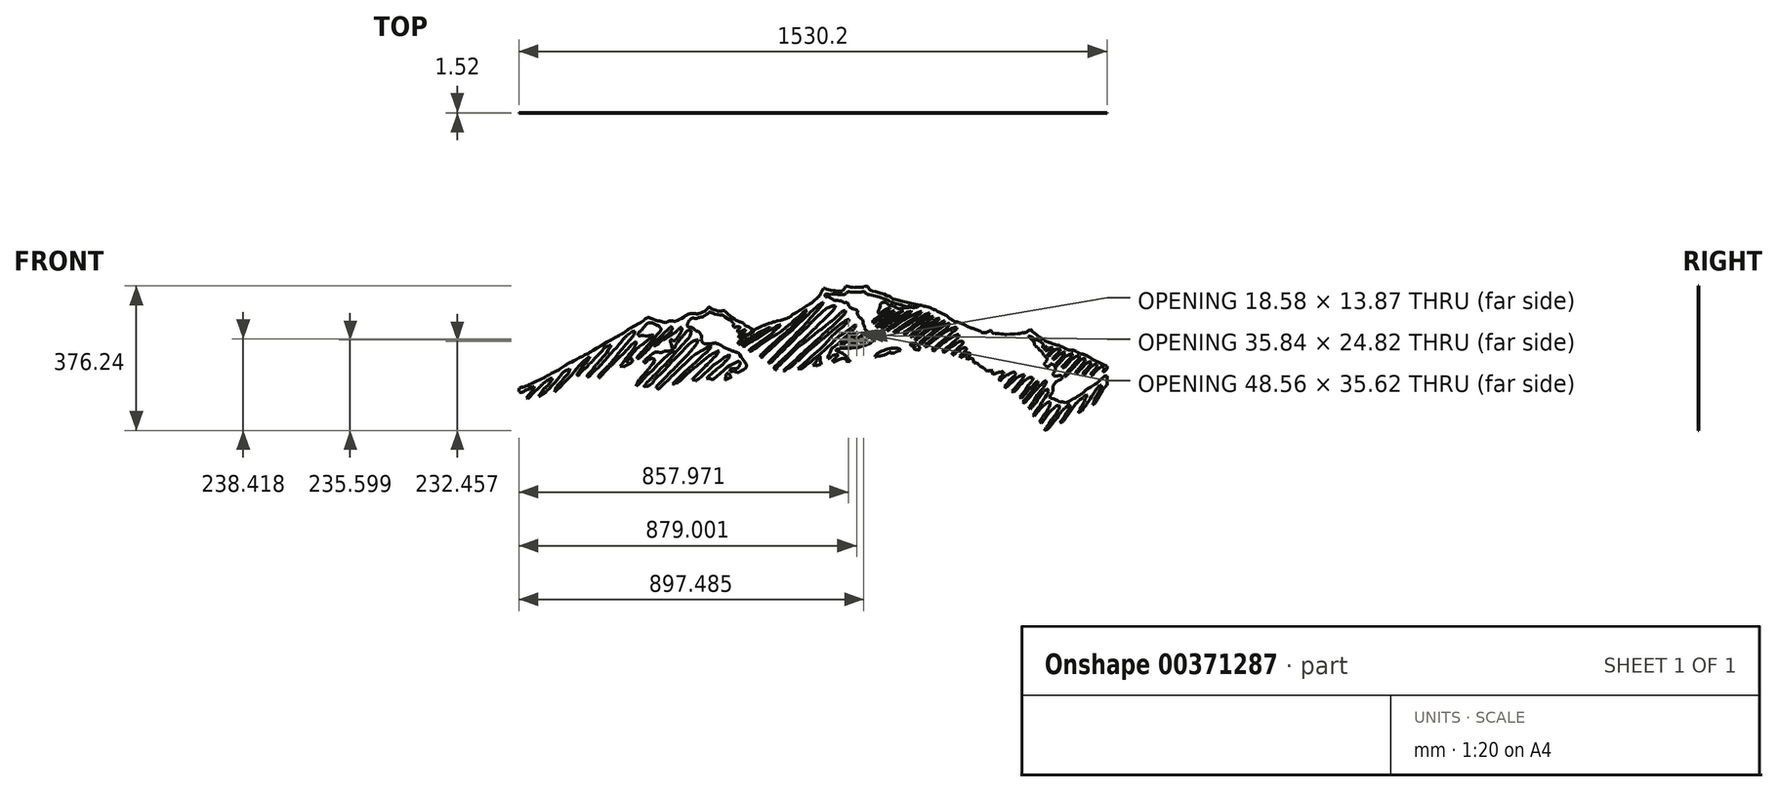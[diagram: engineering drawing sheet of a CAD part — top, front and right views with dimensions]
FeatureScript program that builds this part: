
annotation { "Feature Type Name" : "Feature", "Feature Type Description" : "" }
export const myFeature = defineFeature(function(context is Context, id is Id, definition is map)
    precondition{}
    {
        {
            var Q0;
            Q0=qCreatedBy(makeId("Front.planeOp"),FACE);
            var sketch = newSketch(context, id + "F0", { "sketchPlane" : qUnion([Q0])});
            skLineSegment(sketch, "E0", {"start": v(-154.66, 73) * mm, "end": v(-154.93, 73) * mm});
            skLineSegment(sketch, "E1", {"start": v(-154.93, 73) * mm, "end": v(-155.73, 73.26) * mm});
            skLineSegment(sketch, "E2", {"start": v(-155.73, 73.26) * mm, "end": v(-156.92, 73.96) * mm});
            skLineSegment(sketch, "E3", {"start": v(-156.92, 73.96) * mm, "end": v(-158.2, 74.97) * mm});
            skLineSegment(sketch, "E4", {"start": v(-158.2, 74.97) * mm, "end": v(-159.52, 76.17) * mm});
            skLineSegment(sketch, "E5", {"start": v(-159.52, 76.17) * mm, "end": v(-160.86, 77.43) * mm});
            skLineSegment(sketch, "E6", {"start": v(-160.86, 77.43) * mm, "end": v(-162.18, 78.62) * mm});
            skLineSegment(sketch, "E7", {"start": v(-162.18, 78.62) * mm, "end": v(-163.45, 79.62) * mm});
            skLineSegment(sketch, "E8", {"start": v(-163.45, 79.62) * mm, "end": v(-164.32, 80.17) * mm});
            skLineSegment(sketch, "E9", {"start": v(-164.32, 80.17) * mm, "end": v(-164.63, 80.3) * mm});
            skLineSegment(sketch, "E10", {"start": v(-164.63, 80.3) * mm, "end": v(-165.19, 80.55) * mm});
            skLineSegment(sketch, "E11", {"start": v(-165.19, 80.55) * mm, "end": v(-168.15, 81.65) * mm});
            skLineSegment(sketch, "E12", {"start": v(-168.15, 81.65) * mm, "end": v(-171.05, 82.83) * mm});
            skLineSegment(sketch, "E13", {"start": v(-171.05, 82.83) * mm, "end": v(-171.57, 83.1) * mm});
            skLineSegment(sketch, "E14", {"start": v(-171.57, 83.1) * mm, "end": v(-171.75, 83.2) * mm});
            skLineSegment(sketch, "E15", {"start": v(-171.75, 83.2) * mm, "end": v(-172.31, 83.4) * mm});
            skLineSegment(sketch, "E16", {"start": v(-172.31, 83.4) * mm, "end": v(-173.14, 83.63) * mm});
            skLineSegment(sketch, "E17", {"start": v(-173.14, 83.63) * mm, "end": v(-173.9, 83.85) * mm});
            skLineSegment(sketch, "E18", {"start": v(-173.9, 83.85) * mm, "end": v(-174.37, 84.03) * mm});
            skLineSegment(sketch, "E19", {"start": v(-174.37, 84.03) * mm, "end": v(-174.51, 84.11) * mm});
            skLineSegment(sketch, "E20", {"start": v(-174.51, 84.11) * mm, "end": v(-175, 84.43) * mm});
            skLineSegment(sketch, "E21", {"start": v(-175, 84.43) * mm, "end": v(-176.3, 85.66) * mm});
            skLineSegment(sketch, "E22", {"start": v(-176.3, 85.66) * mm, "end": v(-177.82, 87.53) * mm});
            skLineSegment(sketch, "E23", {"start": v(-177.82, 87.53) * mm, "end": v(-179.36, 89.45) * mm});
            skLineSegment(sketch, "E24", {"start": v(-179.36, 89.45) * mm, "end": v(-180.68, 90.77) * mm});
            skLineSegment(sketch, "E25", {"start": v(-180.68, 90.77) * mm, "end": v(-181.18, 91.12) * mm});
            skLineSegment(sketch, "E26", {"start": v(-181.18, 91.12) * mm, "end": v(-181.77, 91.55) * mm});
            skLineSegment(sketch, "E27", {"start": v(-181.77, 91.55) * mm, "end": v(-185.18, 93.13) * mm});
            skLineSegment(sketch, "E28", {"start": v(-185.18, 93.13) * mm, "end": v(-188.74, 94.46) * mm});
            skLineSegment(sketch, "E29", {"start": v(-188.74, 94.46) * mm, "end": v(-189.4, 94.76) * mm});
            skLineSegment(sketch, "E30", {"start": v(-189.4, 94.76) * mm, "end": v(-190.22, 95.12) * mm});
            skLineSegment(sketch, "E31", {"start": v(-190.22, 95.12) * mm, "end": v(-192.73, 96.1) * mm});
            skLineSegment(sketch, "E32", {"start": v(-192.73, 96.1) * mm, "end": v(-196.17, 97.44) * mm});
            skLineSegment(sketch, "E33", {"start": v(-196.17, 97.44) * mm, "end": v(-199.53, 98.9) * mm});
            skLineSegment(sketch, "E34", {"start": v(-199.53, 98.9) * mm, "end": v(-201.89, 100.16) * mm});
            skLineSegment(sketch, "E35", {"start": v(-201.89, 100.16) * mm, "end": v(-202.62, 100.65) * mm});
            skLineSegment(sketch, "E36", {"start": v(-202.62, 100.65) * mm, "end": v(-204.02, 101.56) * mm});
            skLineSegment(sketch, "E37", {"start": v(-204.02, 101.56) * mm, "end": v(-210.9, 106.39) * mm});
            skLineSegment(sketch, "E38", {"start": v(-210.9, 106.39) * mm, "end": v(-217.38, 111.71) * mm});
            skLineSegment(sketch, "E39", {"start": v(-217.38, 111.71) * mm, "end": v(-218.6, 112.87) * mm});
            skLineSegment(sketch, "E40", {"start": v(-218.6, 112.87) * mm, "end": v(-219.51, 113.75) * mm});
            skLineSegment(sketch, "E41", {"start": v(-219.51, 113.75) * mm, "end": v(-228.41, 122.8) * mm});
            skLineSegment(sketch, "E42", {"start": v(-228.41, 122.8) * mm, "end": v(-229.29, 123.73) * mm});
            skLineSegment(sketch, "E43", {"start": v(-229.29, 123.73) * mm, "end": v(-229.56, 124.01) * mm});
            skLineSegment(sketch, "E44", {"start": v(-229.56, 124.01) * mm, "end": v(-229.94, 124.05) * mm});
            skLineSegment(sketch, "E45", {"start": v(-229.94, 124.05) * mm, "end": v(-230.65, 124.13) * mm});
            skLineSegment(sketch, "E46", {"start": v(-230.65, 124.13) * mm, "end": v(-232.82, 123.92) * mm});
            skLineSegment(sketch, "E47", {"start": v(-232.82, 123.92) * mm, "end": v(-235.5, 123.2) * mm});
            skLineSegment(sketch, "E48", {"start": v(-235.5, 123.2) * mm, "end": v(-238.12, 122.38) * mm});
            skLineSegment(sketch, "E49", {"start": v(-238.12, 122.38) * mm, "end": v(-240.15, 121.95) * mm});
            skLineSegment(sketch, "E50", {"start": v(-240.15, 121.95) * mm, "end": v(-240.84, 121.92) * mm});
            skLineSegment(sketch, "E51", {"start": v(-240.84, 121.92) * mm, "end": v(-242.3, 121.87) * mm});
            skLineSegment(sketch, "E52", {"start": v(-242.3, 121.87) * mm, "end": v(-246.75, 122.56) * mm});
            skLineSegment(sketch, "E53", {"start": v(-246.75, 122.56) * mm, "end": v(-252.44, 124.4) * mm});
            skLineSegment(sketch, "E54", {"start": v(-252.44, 124.4) * mm, "end": v(-258.04, 126.65) * mm});
            skLineSegment(sketch, "E55", {"start": v(-258.04, 126.65) * mm, "end": v(-262.24, 128.16) * mm});
            skLineSegment(sketch, "E56", {"start": v(-262.24, 128.16) * mm, "end": v(-263.68, 128.53) * mm});
            skLineSegment(sketch, "E57", {"start": v(-263.68, 128.53) * mm, "end": v(-264.07, 128.93) * mm});
            skLineSegment(sketch, "E58", {"start": v(-264.07, 128.93) * mm, "end": v(-265.26, 130.13) * mm});
            skLineSegment(sketch, "E59", {"start": v(-265.26, 130.13) * mm, "end": v(-266.9, 131.46) * mm});
            skLineSegment(sketch, "E60", {"start": v(-266.9, 131.46) * mm, "end": v(-268.8, 132.22) * mm});
            skLineSegment(sketch, "E61", {"start": v(-268.8, 132.22) * mm, "end": v(-270.62, 132.25) * mm});
            skLineSegment(sketch, "E62", {"start": v(-270.62, 132.25) * mm, "end": v(-271.19, 132.12) * mm});
            skLineSegment(sketch, "E63", {"start": v(-271.19, 132.12) * mm, "end": v(-271.57, 132.03) * mm});
            skLineSegment(sketch, "E64", {"start": v(-271.57, 132.03) * mm, "end": v(-272.62, 131.34) * mm});
            skLineSegment(sketch, "E65", {"start": v(-272.62, 131.34) * mm, "end": v(-273.76, 130.02) * mm});
            skLineSegment(sketch, "E66", {"start": v(-273.76, 130.02) * mm, "end": v(-274.76, 128.52) * mm});
            skLineSegment(sketch, "E67", {"start": v(-274.76, 128.52) * mm, "end": v(-275.46, 127.52) * mm});
            skLineSegment(sketch, "E68", {"start": v(-275.46, 127.52) * mm, "end": v(-275.74, 127.23) * mm});
            skLineSegment(sketch, "E69", {"start": v(-275.74, 127.23) * mm, "end": v(-276.9, 126.06) * mm});
            skLineSegment(sketch, "E70", {"start": v(-276.9, 126.06) * mm, "end": v(-280.8, 122.96) * mm});
            skLineSegment(sketch, "E71", {"start": v(-280.8, 122.96) * mm, "end": v(-286.58, 119.56) * mm});
            skLineSegment(sketch, "E72", {"start": v(-286.58, 119.56) * mm, "end": v(-292.8, 117.09) * mm});
            skLineSegment(sketch, "E73", {"start": v(-292.8, 117.09) * mm, "end": v(-297.63, 115.84) * mm});
            skLineSegment(sketch, "E74", {"start": v(-297.63, 115.84) * mm, "end": v(-299.26, 115.59) * mm});
            skLineSegment(sketch, "E75", {"start": v(-299.26, 115.59) * mm, "end": v(-299.93, 115.48) * mm});
            skLineSegment(sketch, "E76", {"start": v(-299.93, 115.48) * mm, "end": v(-302, 115.4) * mm});
            skLineSegment(sketch, "E77", {"start": v(-302, 115.4) * mm, "end": v(-304.96, 115.55) * mm});
            skLineSegment(sketch, "E78", {"start": v(-304.96, 115.55) * mm, "end": v(-307.95, 115.8) * mm});
            skLineSegment(sketch, "E79", {"start": v(-307.95, 115.8) * mm, "end": v(-310.08, 115.95) * mm});
            skLineSegment(sketch, "E80", {"start": v(-310.08, 115.95) * mm, "end": v(-310.8, 115.96) * mm});
            skLineSegment(sketch, "E81", {"start": v(-310.8, 115.96) * mm, "end": v(-311.37, 115.98) * mm});
            skLineSegment(sketch, "E82", {"start": v(-311.37, 115.98) * mm, "end": v(-314.2, 116.23) * mm});
            skLineSegment(sketch, "E83", {"start": v(-314.2, 116.23) * mm, "end": v(-317.05, 116.35) * mm});
            skLineSegment(sketch, "E84", {"start": v(-317.05, 116.35) * mm, "end": v(-317.63, 116.3) * mm});
            skLineSegment(sketch, "E85", {"start": v(-317.63, 116.3) * mm, "end": v(-318.1, 116.25) * mm});
            skLineSegment(sketch, "E86", {"start": v(-318.1, 116.25) * mm, "end": v(-319.52, 115.93) * mm});
            skLineSegment(sketch, "E87", {"start": v(-319.52, 115.93) * mm, "end": v(-321.6, 115.22) * mm});
            skLineSegment(sketch, "E88", {"start": v(-321.6, 115.22) * mm, "end": v(-323.8, 114.25) * mm});
            skLineSegment(sketch, "E89", {"start": v(-323.8, 114.25) * mm, "end": v(-326.05, 113.1) * mm});
            skLineSegment(sketch, "E90", {"start": v(-326.05, 113.1) * mm, "end": v(-328.27, 111.86) * mm});
            skLineSegment(sketch, "E91", {"start": v(-328.27, 111.86) * mm, "end": v(-330.41, 110.6) * mm});
            skLineSegment(sketch, "E92", {"start": v(-330.41, 110.6) * mm, "end": v(-332.4, 109.42) * mm});
            skLineSegment(sketch, "E93", {"start": v(-332.4, 109.42) * mm, "end": v(-333.72, 108.65) * mm});
            skLineSegment(sketch, "E94", {"start": v(-333.72, 108.65) * mm, "end": v(-334.16, 108.4) * mm});
            skLineSegment(sketch, "E95", {"start": v(-334.16, 108.4) * mm, "end": v(-335.43, 107.7) * mm});
            skLineSegment(sketch, "E96", {"start": v(-335.43, 107.7) * mm, "end": v(-341.69, 104.02) * mm});
            skLineSegment(sketch, "E97", {"start": v(-341.69, 104.02) * mm, "end": v(-347.94, 100.33) * mm});
            skLineSegment(sketch, "E98", {"start": v(-347.94, 100.33) * mm, "end": v(-349.21, 99.62) * mm});
            skLineSegment(sketch, "E99", {"start": v(-349.21, 99.62) * mm, "end": v(-349.69, 99.37) * mm});
            skLineSegment(sketch, "E100", {"start": v(-349.69, 99.37) * mm, "end": v(-352.39, 97.91) * mm});
            skLineSegment(sketch, "E101", {"start": v(-352.39, 97.91) * mm, "end": v(-355.17, 96.69) * mm});
            skLineSegment(sketch, "E102", {"start": v(-355.17, 96.69) * mm, "end": v(-355.7, 96.55) * mm});
            skLineSegment(sketch, "E103", {"start": v(-355.7, 96.55) * mm, "end": v(-356.82, 96.26) * mm});
            skLineSegment(sketch, "E104", {"start": v(-356.82, 96.26) * mm, "end": v(-360.37, 96.1) * mm});
            skLineSegment(sketch, "E105", {"start": v(-360.37, 96.1) * mm, "end": v(-365.16, 96.53) * mm});
            skLineSegment(sketch, "E106", {"start": v(-365.16, 96.53) * mm, "end": v(-369.9, 96.97) * mm});
            skLineSegment(sketch, "E107", {"start": v(-369.9, 96.97) * mm, "end": v(-373.35, 96.83) * mm});
            skLineSegment(sketch, "E108", {"start": v(-373.35, 96.83) * mm, "end": v(-374.43, 96.55) * mm});
            skLineSegment(sketch, "E109", {"start": v(-374.43, 96.55) * mm, "end": v(-374.92, 96.43) * mm});
            skLineSegment(sketch, "E110", {"start": v(-374.92, 96.43) * mm, "end": v(-376.28, 95.77) * mm});
            skLineSegment(sketch, "E111", {"start": v(-376.28, 95.77) * mm, "end": v(-378.05, 94.66) * mm});
            skLineSegment(sketch, "E112", {"start": v(-378.05, 94.66) * mm, "end": v(-379.8, 93.63) * mm});
            skLineSegment(sketch, "E113", {"start": v(-379.8, 93.63) * mm, "end": v(-381.17, 93.13) * mm});
            skLineSegment(sketch, "E114", {"start": v(-381.17, 93.13) * mm, "end": v(-381.64, 93.08) * mm});
            skLineSegment(sketch, "E115", {"start": v(-381.64, 93.08) * mm, "end": v(-382.45, 93) * mm});
            skLineSegment(sketch, "E116", {"start": v(-382.45, 93) * mm, "end": v(-384.92, 93.19) * mm});
            skLineSegment(sketch, "E117", {"start": v(-384.92, 93.19) * mm, "end": v(-388.1, 93.91) * mm});
            skLineSegment(sketch, "E118", {"start": v(-388.1, 93.91) * mm, "end": v(-391.21, 94.92) * mm});
            skLineSegment(sketch, "E119", {"start": v(-391.21, 94.92) * mm, "end": v(-393.55, 95.66) * mm});
            skLineSegment(sketch, "E120", {"start": v(-393.55, 95.66) * mm, "end": v(-394.34, 95.86) * mm});
            skLineSegment(sketch, "E121", {"start": v(-394.34, 95.86) * mm, "end": v(-395.48, 96.15) * mm});
            skLineSegment(sketch, "E122", {"start": v(-395.48, 96.15) * mm, "end": v(-398.93, 96.82) * mm});
            skLineSegment(sketch, "E123", {"start": v(-398.93, 96.82) * mm, "end": v(-403.6, 97.62) * mm});
            skLineSegment(sketch, "E124", {"start": v(-403.6, 97.62) * mm, "end": v(-408.21, 98.6) * mm});
            skLineSegment(sketch, "E125", {"start": v(-408.21, 98.6) * mm, "end": v(-411.57, 99.6) * mm});
            skLineSegment(sketch, "E126", {"start": v(-411.57, 99.6) * mm, "end": v(-412.63, 100.04) * mm});
            skLineSegment(sketch, "E127", {"start": v(-412.63, 100.04) * mm, "end": v(-413.56, 100.43) * mm});
            skLineSegment(sketch, "E128", {"start": v(-413.56, 100.43) * mm, "end": v(-416.26, 101.75) * mm});
            skLineSegment(sketch, "E129", {"start": v(-416.26, 101.75) * mm, "end": v(-420.03, 103.62) * mm});
            skLineSegment(sketch, "E130", {"start": v(-420.03, 103.62) * mm, "end": v(-423.9, 105.11) * mm});
            skLineSegment(sketch, "E131", {"start": v(-423.9, 105.11) * mm, "end": v(-426.81, 105.73) * mm});
            skLineSegment(sketch, "E132", {"start": v(-426.81, 105.73) * mm, "end": v(-427.78, 105.73) * mm});
            skLineSegment(sketch, "E133", {"start": v(-427.78, 105.73) * mm, "end": v(-428.43, 105.73) * mm});
            skLineSegment(sketch, "E134", {"start": v(-428.43, 105.73) * mm, "end": v(-430.35, 105.37) * mm});
            skLineSegment(sketch, "E135", {"start": v(-430.35, 105.37) * mm, "end": v(-432.33, 104.49) * mm});
            skLineSegment(sketch, "E136", {"start": v(-432.33, 104.49) * mm, "end": v(-434.2, 103.44) * mm});
            skLineSegment(sketch, "E137", {"start": v(-434.2, 103.44) * mm, "end": v(-435.87, 102.7) * mm});
            skLineSegment(sketch, "E138", {"start": v(-435.87, 102.7) * mm, "end": v(-436.45, 102.53) * mm});
            skLineSegment(sketch, "E139", {"start": v(-436.45, 102.53) * mm, "end": v(-436.81, 102.44) * mm});
            skLineSegment(sketch, "E140", {"start": v(-436.81, 102.44) * mm, "end": v(-437.03, 102.14) * mm});
            skLineSegment(sketch, "E141", {"start": v(-437.03, 102.14) * mm, "end": v(-437.65, 101.29) * mm});
            skLineSegment(sketch, "E142", {"start": v(-437.65, 101.29) * mm, "end": v(-439.87, 98.99) * mm});
            skLineSegment(sketch, "E143", {"start": v(-439.87, 98.99) * mm, "end": v(-443.24, 96.22) * mm});
            skLineSegment(sketch, "E144", {"start": v(-443.24, 96.22) * mm, "end": v(-446.87, 93.75) * mm});
            skLineSegment(sketch, "E145", {"start": v(-446.87, 93.75) * mm, "end": v(-449.58, 92.07) * mm});
            skLineSegment(sketch, "E146", {"start": v(-449.58, 92.07) * mm, "end": v(-450.49, 91.5) * mm});
            skLineSegment(sketch, "E147", {"start": v(-450.49, 91.5) * mm, "end": v(-452.63, 90.2) * mm});
            skLineSegment(sketch, "E148", {"start": v(-452.63, 90.2) * mm, "end": v(-463.65, 84.2) * mm});
            skLineSegment(sketch, "E149", {"start": v(-463.65, 84.2) * mm, "end": v(-474.74, 78.32) * mm});
            skLineSegment(sketch, "E150", {"start": v(-474.74, 78.32) * mm, "end": v(-476.9, 77.07) * mm});
            skLineSegment(sketch, "E151", {"start": v(-476.9, 77.07) * mm, "end": v(-478.36, 76.24) * mm});
            skLineSegment(sketch, "E152", {"start": v(-478.36, 76.24) * mm, "end": v(-482.58, 73.55) * mm});
            skLineSegment(sketch, "E153", {"start": v(-482.58, 73.55) * mm, "end": v(-488.06, 69.76) * mm});
            skLineSegment(sketch, "E154", {"start": v(-488.06, 69.76) * mm, "end": v(-493.5, 65.94) * mm});
            skLineSegment(sketch, "E155", {"start": v(-493.5, 65.94) * mm, "end": v(-497.67, 63.18) * mm});
            skLineSegment(sketch, "E156", {"start": v(-497.67, 63.18) * mm, "end": v(-499.09, 62.32) * mm});
            skLineSegment(sketch, "E157", {"start": v(-499.09, 62.32) * mm, "end": v(-500, 61.75) * mm});
            skLineSegment(sketch, "E158", {"start": v(-500, 61.75) * mm, "end": v(-504.75, 59.3) * mm});
            skLineSegment(sketch, "E159", {"start": v(-504.75, 59.3) * mm, "end": v(-509.53, 56.87) * mm});
            skLineSegment(sketch, "E160", {"start": v(-509.53, 56.87) * mm, "end": v(-510.45, 56.32) * mm});
            skLineSegment(sketch, "E161", {"start": v(-510.45, 56.32) * mm, "end": v(-511.36, 55.78) * mm});
            skLineSegment(sketch, "E162", {"start": v(-511.36, 55.78) * mm, "end": v(-520.54, 50.5) * mm});
            skLineSegment(sketch, "E163", {"start": v(-520.54, 50.5) * mm, "end": v(-521.48, 50) * mm});
            skLineSegment(sketch, "E164", {"start": v(-521.48, 50) * mm, "end": v(-524.98, 48.15) * mm});
            skLineSegment(sketch, "E165", {"start": v(-524.98, 48.15) * mm, "end": v(-535.28, 42.16) * mm});
            skLineSegment(sketch, "E166", {"start": v(-535.28, 42.16) * mm, "end": v(-548.8, 33.82) * mm});
            skLineSegment(sketch, "E167", {"start": v(-548.8, 33.82) * mm, "end": v(-562.3, 25.48) * mm});
            skLineSegment(sketch, "E168", {"start": v(-562.3, 25.48) * mm, "end": v(-572.6, 19.48) * mm});
            skLineSegment(sketch, "E169", {"start": v(-572.6, 19.48) * mm, "end": v(-576.1, 17.62) * mm});
            skLineSegment(sketch, "E170", {"start": v(-576.1, 17.62) * mm, "end": v(-576.8, 17.24) * mm});
            skLineSegment(sketch, "E171", {"start": v(-576.8, 17.24) * mm, "end": v(-578.83, 15.95) * mm});
            skLineSegment(sketch, "E172", {"start": v(-578.83, 15.95) * mm, "end": v(-581.54, 14.11) * mm});
            skLineSegment(sketch, "E173", {"start": v(-581.54, 14.11) * mm, "end": v(-584.27, 12.36) * mm});
            skLineSegment(sketch, "E174", {"start": v(-584.27, 12.36) * mm, "end": v(-586.33, 11.26) * mm});
            skLineSegment(sketch, "E175", {"start": v(-586.33, 11.26) * mm, "end": v(-587.05, 10.97) * mm});
            skLineSegment(sketch, "E176", {"start": v(-587.05, 10.97) * mm, "end": v(-587.4, 10.84) * mm});
            skLineSegment(sketch, "E177", {"start": v(-587.4, 10.84) * mm, "end": v(-589.2, 10.46) * mm});
            skLineSegment(sketch, "E178", {"start": v(-589.2, 10.46) * mm, "end": v(-591.05, 10.08) * mm});
            skLineSegment(sketch, "E179", {"start": v(-591.05, 10.08) * mm, "end": v(-591.4, 9.94) * mm});
            skLineSegment(sketch, "E180", {"start": v(-591.4, 9.94) * mm, "end": v(-592.04, 9.67) * mm});
            skLineSegment(sketch, "E181", {"start": v(-592.04, 9.67) * mm, "end": v(-595, 7.85) * mm});
            skLineSegment(sketch, "E182", {"start": v(-595, 7.85) * mm, "end": v(-597.92, 5.95) * mm});
            skLineSegment(sketch, "E183", {"start": v(-597.92, 5.95) * mm, "end": v(-598.54, 5.63) * mm});
            skLineSegment(sketch, "E184", {"start": v(-598.54, 5.63) * mm, "end": v(-599.98, 4.9) * mm});
            skLineSegment(sketch, "E185", {"start": v(-599.98, 4.9) * mm, "end": v(-607.24, 1.24) * mm});
            skLineSegment(sketch, "E186", {"start": v(-607.24, 1.24) * mm, "end": v(-614.35, -2.68) * mm});
            skLineSegment(sketch, "E187", {"start": v(-614.35, -2.68) * mm, "end": v(-615.73, -3.56) * mm});
            skLineSegment(sketch, "E188", {"start": v(-615.73, -3.56) * mm, "end": v(-616.88, -4.28) * mm});
            skLineSegment(sketch, "E189", {"start": v(-616.88, -4.28) * mm, "end": v(-622.91, -7.44) * mm});
            skLineSegment(sketch, "E190", {"start": v(-622.91, -7.44) * mm, "end": v(-629.1, -10.3) * mm});
            skLineSegment(sketch, "E191", {"start": v(-629.1, -10.3) * mm, "end": v(-630.32, -10.88) * mm});
            skLineSegment(sketch, "E192", {"start": v(-630.32, -10.88) * mm, "end": v(-630.9, -11.15) * mm});
            skLineSegment(sketch, "E193", {"start": v(-630.9, -11.15) * mm, "end": v(-633.96, -12.23) * mm});
            skLineSegment(sketch, "E194", {"start": v(-633.96, -12.23) * mm, "end": v(-636.94, -13.44) * mm});
            skLineSegment(sketch, "E195", {"start": v(-636.94, -13.44) * mm, "end": v(-637.48, -13.77) * mm});
            skLineSegment(sketch, "E196", {"start": v(-637.48, -13.77) * mm, "end": v(-637.78, -13.95) * mm});
            skLineSegment(sketch, "E197", {"start": v(-637.78, -13.95) * mm, "end": v(-638.64, -14.59) * mm});
            skLineSegment(sketch, "E198", {"start": v(-638.64, -14.59) * mm, "end": v(-639.71, -15.51) * mm});
            skLineSegment(sketch, "E199", {"start": v(-639.71, -15.51) * mm, "end": v(-640.77, -16.45) * mm});
            skLineSegment(sketch, "E200", {"start": v(-640.77, -16.45) * mm, "end": v(-641.6, -17.1) * mm});
            skLineSegment(sketch, "E201", {"start": v(-641.6, -17.1) * mm, "end": v(-641.9, -17.3) * mm});
            skLineSegment(sketch, "E202", {"start": v(-641.9, -17.3) * mm, "end": v(-643.49, -18.35) * mm});
            skLineSegment(sketch, "E203", {"start": v(-643.49, -18.35) * mm, "end": v(-651.34, -23.75) * mm});
            skLineSegment(sketch, "E204", {"start": v(-651.34, -23.75) * mm, "end": v(-659.3, -28.99) * mm});
            skLineSegment(sketch, "E205", {"start": v(-659.3, -28.99) * mm, "end": v(-660.95, -29.97) * mm});
            skLineSegment(sketch, "E206", {"start": v(-660.95, -29.97) * mm, "end": v(-662.12, -30.66) * mm});
            skLineSegment(sketch, "E207", {"start": v(-662.12, -30.66) * mm, "end": v(-665.76, -32.5) * mm});
            skLineSegment(sketch, "E208", {"start": v(-665.76, -32.5) * mm, "end": v(-670.7, -34.8) * mm});
            skLineSegment(sketch, "E209", {"start": v(-670.7, -34.8) * mm, "end": v(-675.64, -37.14) * mm});
            skLineSegment(sketch, "E210", {"start": v(-675.64, -37.14) * mm, "end": v(-679.26, -39.1) * mm});
            skLineSegment(sketch, "E211", {"start": v(-679.26, -39.1) * mm, "end": v(-680.4, -39.83) * mm});
            skLineSegment(sketch, "E212", {"start": v(-680.4, -39.83) * mm, "end": v(-681.16, -40.3) * mm});
            skLineSegment(sketch, "E213", {"start": v(-681.16, -40.3) * mm, "end": v(-688.94, -44.62) * mm});
            skLineSegment(sketch, "E214", {"start": v(-688.94, -44.62) * mm, "end": v(-689.73, -45.03) * mm});
            skLineSegment(sketch, "E215", {"start": v(-689.73, -45.03) * mm, "end": v(-690.15, -45.26) * mm});
            skLineSegment(sketch, "E216", {"start": v(-690.15, -45.26) * mm, "end": v(-692.18, -46.53) * mm});
            skLineSegment(sketch, "E217", {"start": v(-692.18, -46.53) * mm, "end": v(-694.14, -47.9) * mm});
            skLineSegment(sketch, "E218", {"start": v(-694.14, -47.9) * mm, "end": v(-694.53, -48.17) * mm});
            skLineSegment(sketch, "E219", {"start": v(-694.53, -48.17) * mm, "end": v(-694.85, -48.4) * mm});
            skLineSegment(sketch, "E220", {"start": v(-694.85, -48.4) * mm, "end": v(-696.53, -49.52) * mm});
            skLineSegment(sketch, "E221", {"start": v(-696.53, -49.52) * mm, "end": v(-698.3, -50.47) * mm});
            skLineSegment(sketch, "E222", {"start": v(-698.3, -50.47) * mm, "end": v(-698.67, -50.62) * mm});
            skLineSegment(sketch, "E223", {"start": v(-698.67, -50.62) * mm, "end": v(-699.33, -50.9) * mm});
            skLineSegment(sketch, "E224", {"start": v(-699.33, -50.9) * mm, "end": v(-705.77, -53.88) * mm});
            skLineSegment(sketch, "E225", {"start": v(-705.77, -53.88) * mm, "end": v(-706.42, -54.2) * mm});
            skLineSegment(sketch, "E226", {"start": v(-706.42, -54.2) * mm, "end": v(-708.78, -55.33) * mm});
            skLineSegment(sketch, "E227", {"start": v(-708.78, -55.33) * mm, "end": v(-720.58, -60.94) * mm});
            skLineSegment(sketch, "E228", {"start": v(-720.58, -60.94) * mm, "end": v(-732.3, -66.72) * mm});
            skLineSegment(sketch, "E229", {"start": v(-732.3, -66.72) * mm, "end": v(-734.63, -67.95) * mm});
            skLineSegment(sketch, "E230", {"start": v(-734.63, -67.95) * mm, "end": v(-735.8, -68.55) * mm});
            skLineSegment(sketch, "E231", {"start": v(-735.8, -68.55) * mm, "end": v(-741.82, -71.19) * mm});
            skLineSegment(sketch, "E232", {"start": v(-741.82, -71.19) * mm, "end": v(-748.01, -73.46) * mm});
            skLineSegment(sketch, "E233", {"start": v(-748.01, -73.46) * mm, "end": v(-749.25, -73.88) * mm});
            skLineSegment(sketch, "E234", {"start": v(-749.25, -73.88) * mm, "end": v(-749.72, -74.04) * mm});
            skLineSegment(sketch, "E235", {"start": v(-749.72, -74.04) * mm, "end": v(-754.6, -75.3) * mm});
            skLineSegment(sketch, "E236", {"start": v(-754.6, -75.3) * mm, "end": v(-755.1, -75.42) * mm});
            skLineSegment(sketch, "E237", {"start": v(-755.1, -75.42) * mm, "end": v(-755.75, -75.58) * mm});
            skLineSegment(sketch, "E238", {"start": v(-755.75, -75.58) * mm, "end": v(-757.7, -76.1) * mm});
            skLineSegment(sketch, "E239", {"start": v(-757.7, -76.1) * mm, "end": v(-760.68, -77.1) * mm});
            skLineSegment(sketch, "E240", {"start": v(-760.68, -77.1) * mm, "end": v(-763.31, -78.58) * mm});
            skLineSegment(sketch, "E241", {"start": v(-763.31, -78.58) * mm, "end": v(-764.7, -80.08) * mm});
            skLineSegment(sketch, "E242", {"start": v(-764.7, -80.08) * mm, "end": v(-764.9, -80.66) * mm});
            skLineSegment(sketch, "E243", {"start": v(-764.9, -80.66) * mm, "end": v(-765, -80.94) * mm});
            skLineSegment(sketch, "E244", {"start": v(-765, -80.94) * mm, "end": v(-765.1, -81.82) * mm});
            skLineSegment(sketch, "E245", {"start": v(-765.1, -81.82) * mm, "end": v(-764.95, -82.95) * mm});
            skLineSegment(sketch, "E246", {"start": v(-764.95, -82.95) * mm, "end": v(-764.53, -84.03) * mm});
            skLineSegment(sketch, "E247", {"start": v(-764.53, -84.03) * mm, "end": v(-764.08, -84.8) * mm});
            skLineSegment(sketch, "E248", {"start": v(-764.08, -84.8) * mm, "end": v(-763.92, -85.05) * mm});
            skLineSegment(sketch, "E249", {"start": v(-763.92, -85.05) * mm, "end": v(-763.94, -85.07) * mm});
            skLineSegment(sketch, "E250", {"start": v(-763.94, -85.07) * mm, "end": v(-764.2, -85.36) * mm});
            skLineSegment(sketch, "E251", {"start": v(-764.2, -85.36) * mm, "end": v(-764.22, -85.39) * mm});
            skLineSegment(sketch, "E252", {"start": v(-764.22, -85.39) * mm, "end": v(-764.77, -86.16) * mm});
            skLineSegment(sketch, "E253", {"start": v(-764.77, -86.16) * mm, "end": v(-764.07, -86.8) * mm});
            skLineSegment(sketch, "E254", {"start": v(-764.07, -86.8) * mm, "end": v(-763.78, -87.07) * mm});
            skLineSegment(sketch, "E255", {"start": v(-763.78, -87.07) * mm, "end": v(-760.86, -89.66) * mm});
            skLineSegment(sketch, "E256", {"start": v(-760.86, -89.66) * mm, "end": v(-760.57, -89.91) * mm});
            skLineSegment(sketch, "E257", {"start": v(-760.57, -89.91) * mm, "end": v(-759.86, -90.55) * mm});
            skLineSegment(sketch, "E258", {"start": v(-759.86, -90.55) * mm, "end": v(-759.15, -89.92) * mm});
            skLineSegment(sketch, "E259", {"start": v(-759.15, -89.92) * mm, "end": v(-758.98, -89.77) * mm});
            skLineSegment(sketch, "E260", {"start": v(-758.98, -89.77) * mm, "end": v(-758.05, -88.97) * mm});
            skLineSegment(sketch, "E261", {"start": v(-758.05, -88.97) * mm, "end": v(-757.04, -88.26) * mm});
            skLineSegment(sketch, "E262", {"start": v(-757.04, -88.26) * mm, "end": v(-756.83, -88.17) * mm});
            skLineSegment(sketch, "E263", {"start": v(-756.83, -88.17) * mm, "end": v(-756.68, -88.1) * mm});
            skLineSegment(sketch, "E264", {"start": v(-756.68, -88.1) * mm, "end": v(-756.18, -88.04) * mm});
            skLineSegment(sketch, "E265", {"start": v(-756.18, -88.04) * mm, "end": v(-755.35, -88.03) * mm});
            skLineSegment(sketch, "E266", {"start": v(-755.35, -88.03) * mm, "end": v(-754.45, -88) * mm});
            skLineSegment(sketch, "E267", {"start": v(-754.45, -88) * mm, "end": v(-753.78, -87.91) * mm});
            skLineSegment(sketch, "E268", {"start": v(-753.78, -87.91) * mm, "end": v(-753.57, -87.85) * mm});
            skLineSegment(sketch, "E269", {"start": v(-753.57, -87.85) * mm, "end": v(-753.28, -87.75) * mm});
            skLineSegment(sketch, "E270", {"start": v(-753.28, -87.75) * mm, "end": v(-752.46, -87.3) * mm});
            skLineSegment(sketch, "E271", {"start": v(-752.46, -87.3) * mm, "end": v(-751.4, -86.52) * mm});
            skLineSegment(sketch, "E272", {"start": v(-751.4, -86.52) * mm, "end": v(-750.38, -85.67) * mm});
            skLineSegment(sketch, "E273", {"start": v(-750.38, -85.67) * mm, "end": v(-749.6, -85.09) * mm});
            skLineSegment(sketch, "E274", {"start": v(-749.6, -85.09) * mm, "end": v(-749.33, -84.93) * mm});
            skLineSegment(sketch, "E275", {"start": v(-749.33, -84.93) * mm, "end": v(-748.95, -84.7) * mm});
            skLineSegment(sketch, "E276", {"start": v(-748.95, -84.7) * mm, "end": v(-746.89, -83.87) * mm});
            skLineSegment(sketch, "E277", {"start": v(-746.89, -83.87) * mm, "end": v(-744.78, -83.07) * mm});
            skLineSegment(sketch, "E278", {"start": v(-744.78, -83.07) * mm, "end": v(-744.38, -82.87) * mm});
            skLineSegment(sketch, "E279", {"start": v(-744.38, -82.87) * mm, "end": v(-743.19, -82.3) * mm});
            skLineSegment(sketch, "E280", {"start": v(-743.19, -82.3) * mm, "end": v(-739.71, -80.31) * mm});
            skLineSegment(sketch, "E281", {"start": v(-739.71, -80.31) * mm, "end": v(-735.11, -77.62) * mm});
            skLineSegment(sketch, "E282", {"start": v(-735.11, -77.62) * mm, "end": v(-730.34, -75.4) * mm});
            skLineSegment(sketch, "E283", {"start": v(-730.34, -75.4) * mm, "end": v(-726.46, -74.33) * mm});
            skLineSegment(sketch, "E284", {"start": v(-726.46, -74.33) * mm, "end": v(-725.15, -74.23) * mm});
            skLineSegment(sketch, "E285", {"start": v(-725.15, -74.23) * mm, "end": v(-725.2, -75.1) * mm});
            skLineSegment(sketch, "E286", {"start": v(-725.2, -75.1) * mm, "end": v(-725.92, -77.73) * mm});
            skLineSegment(sketch, "E287", {"start": v(-725.92, -77.73) * mm, "end": v(-727.58, -80.66) * mm});
            skLineSegment(sketch, "E288", {"start": v(-727.58, -80.66) * mm, "end": v(-729.74, -83.37) * mm});
            skLineSegment(sketch, "E289", {"start": v(-729.74, -83.37) * mm, "end": v(-731.46, -85.47) * mm});
            skLineSegment(sketch, "E290", {"start": v(-731.46, -85.47) * mm, "end": v(-731.99, -86.2) * mm});
            skLineSegment(sketch, "E291", {"start": v(-731.99, -86.2) * mm, "end": v(-732.67, -87.15) * mm});
            skLineSegment(sketch, "E292", {"start": v(-732.67, -87.15) * mm, "end": v(-735.97, -91.92) * mm});
            skLineSegment(sketch, "E293", {"start": v(-735.97, -91.92) * mm, "end": v(-739.5, -96.52) * mm});
            skLineSegment(sketch, "E294", {"start": v(-739.5, -96.52) * mm, "end": v(-740.28, -97.38) * mm});
            skLineSegment(sketch, "E295", {"start": v(-740.28, -97.38) * mm, "end": v(-740.65, -97.78) * mm});
            skLineSegment(sketch, "E296", {"start": v(-740.65, -97.78) * mm, "end": v(-744.15, -101.88) * mm});
            skLineSegment(sketch, "E297", {"start": v(-744.15, -101.88) * mm, "end": v(-744.5, -102.3) * mm});
            skLineSegment(sketch, "E298", {"start": v(-744.5, -102.3) * mm, "end": v(-745.22, -103.13) * mm});
            skLineSegment(sketch, "E299", {"start": v(-745.22, -103.13) * mm, "end": v(-744.35, -103.82) * mm});
            skLineSegment(sketch, "E300", {"start": v(-744.35, -103.82) * mm, "end": v(-744.2, -103.95) * mm});
            skLineSegment(sketch, "E301", {"start": v(-744.2, -103.95) * mm, "end": v(-742.66, -105.22) * mm});
            skLineSegment(sketch, "E302", {"start": v(-742.66, -105.22) * mm, "end": v(-742.52, -105.35) * mm});
            skLineSegment(sketch, "E303", {"start": v(-742.52, -105.35) * mm, "end": v(-741.7, -106.08) * mm});
            skLineSegment(sketch, "E304", {"start": v(-741.7, -106.08) * mm, "end": v(-740.99, -105.27) * mm});
            skLineSegment(sketch, "E305", {"start": v(-740.99, -105.27) * mm, "end": v(-738.6, -102.54) * mm});
            skLineSegment(sketch, "E306", {"start": v(-738.6, -102.54) * mm, "end": v(-726.12, -89.3) * mm});
            skLineSegment(sketch, "E307", {"start": v(-726.12, -89.3) * mm, "end": v(-713, -76.68) * mm});
            skLineSegment(sketch, "E308", {"start": v(-713, -76.68) * mm, "end": v(-710.29, -74.27) * mm});
            skLineSegment(sketch, "E309", {"start": v(-710.29, -74.27) * mm, "end": v(-709.67, -73.72) * mm});
            skLineSegment(sketch, "E310", {"start": v(-709.67, -73.72) * mm, "end": v(-707.95, -71.94) * mm});
            skLineSegment(sketch, "E311", {"start": v(-707.95, -71.94) * mm, "end": v(-705.59, -69.49) * mm});
            skLineSegment(sketch, "E312", {"start": v(-705.59, -69.49) * mm, "end": v(-703.07, -67.26) * mm});
            skLineSegment(sketch, "E313", {"start": v(-703.07, -67.26) * mm, "end": v(-700.99, -65.94) * mm});
            skLineSegment(sketch, "E314", {"start": v(-700.99, -65.94) * mm, "end": v(-700.24, -65.65) * mm});
            skLineSegment(sketch, "E315", {"start": v(-700.24, -65.65) * mm, "end": v(-699.9, -65.52) * mm});
            skLineSegment(sketch, "E316", {"start": v(-699.9, -65.52) * mm, "end": v(-699.72, -65.24) * mm});
            skLineSegment(sketch, "E317", {"start": v(-699.72, -65.24) * mm, "end": v(-699.6, -65.02) * mm});
            skLineSegment(sketch, "E318", {"start": v(-699.6, -65.02) * mm, "end": v(-698.44, -62.84) * mm});
            skLineSegment(sketch, "E319", {"start": v(-698.44, -62.84) * mm, "end": v(-698.33, -62.62) * mm});
            skLineSegment(sketch, "E320", {"start": v(-698.33, -62.62) * mm, "end": v(-698.14, -62.62) * mm});
            skLineSegment(sketch, "E321", {"start": v(-698.14, -62.62) * mm, "end": v(-697.42, -62.45) * mm});
            skLineSegment(sketch, "E322", {"start": v(-697.42, -62.45) * mm, "end": v(-696.65, -62.22) * mm});
            skLineSegment(sketch, "E323", {"start": v(-696.65, -62.22) * mm, "end": v(-696.44, -62.2) * mm});
            skLineSegment(sketch, "E324", {"start": v(-696.44, -62.2) * mm, "end": v(-695.97, -62.12) * mm});
            skLineSegment(sketch, "E325", {"start": v(-695.97, -62.12) * mm, "end": v(-695.7, -61.72) * mm});
            skLineSegment(sketch, "E326", {"start": v(-695.7, -61.72) * mm, "end": v(-695.27, -61.06) * mm});
            skLineSegment(sketch, "E327", {"start": v(-695.27, -61.06) * mm, "end": v(-693.64, -59.3) * mm});
            skLineSegment(sketch, "E328", {"start": v(-693.64, -59.3) * mm, "end": v(-691.23, -57.52) * mm});
            skLineSegment(sketch, "E329", {"start": v(-691.23, -57.52) * mm, "end": v(-688.56, -56.08) * mm});
            skLineSegment(sketch, "E330", {"start": v(-688.56, -56.08) * mm, "end": v(-686.4, -55.04) * mm});
            skLineSegment(sketch, "E331", {"start": v(-686.4, -55.04) * mm, "end": v(-685.7, -54.69) * mm});
            skLineSegment(sketch, "E332", {"start": v(-685.7, -54.69) * mm, "end": v(-685.54, -54.6) * mm});
            skLineSegment(sketch, "E333", {"start": v(-685.54, -54.6) * mm, "end": v(-685.06, -54.35) * mm});
            skLineSegment(sketch, "E334", {"start": v(-685.06, -54.35) * mm, "end": v(-684.12, -53.87) * mm});
            skLineSegment(sketch, "E335", {"start": v(-684.12, -53.87) * mm, "end": v(-683, -53.33) * mm});
            skLineSegment(sketch, "E336", {"start": v(-683, -53.33) * mm, "end": v(-681.79, -52.83) * mm});
            skLineSegment(sketch, "E337", {"start": v(-681.79, -52.83) * mm, "end": v(-680.59, -52.46) * mm});
            skLineSegment(sketch, "E338", {"start": v(-680.59, -52.46) * mm, "end": v(-679.51, -52.32) * mm});
            skLineSegment(sketch, "E339", {"start": v(-679.51, -52.32) * mm, "end": v(-678.66, -52.49) * mm});
            skLineSegment(sketch, "E340", {"start": v(-678.66, -52.49) * mm, "end": v(-678.2, -52.9) * mm});
            skLineSegment(sketch, "E341", {"start": v(-678.2, -52.9) * mm, "end": v(-678.14, -53.07) * mm});
            skLineSegment(sketch, "E342", {"start": v(-678.14, -53.07) * mm, "end": v(-677.98, -53.48) * mm});
            skLineSegment(sketch, "E343", {"start": v(-677.98, -53.48) * mm, "end": v(-678.26, -54.98) * mm});
            skLineSegment(sketch, "E344", {"start": v(-678.26, -54.98) * mm, "end": v(-679.4, -57.32) * mm});
            skLineSegment(sketch, "E345", {"start": v(-679.4, -57.32) * mm, "end": v(-680.88, -59.57) * mm});
            skLineSegment(sketch, "E346", {"start": v(-680.88, -59.57) * mm, "end": v(-681.79, -60.85) * mm});
            skLineSegment(sketch, "E347", {"start": v(-681.79, -60.85) * mm, "end": v(-682.05, -61.26) * mm});
            skLineSegment(sketch, "E348", {"start": v(-682.05, -61.26) * mm, "end": v(-682.84, -62.47) * mm});
            skLineSegment(sketch, "E349", {"start": v(-682.84, -62.47) * mm, "end": v(-685.3, -66.03) * mm});
            skLineSegment(sketch, "E350", {"start": v(-685.3, -66.03) * mm, "end": v(-688.88, -70.55) * mm});
            skLineSegment(sketch, "E351", {"start": v(-688.88, -70.55) * mm, "end": v(-692.97, -74.55) * mm});
            skLineSegment(sketch, "E352", {"start": v(-692.97, -74.55) * mm, "end": v(-696.5, -77.1) * mm});
            skLineSegment(sketch, "E353", {"start": v(-696.5, -77.1) * mm, "end": v(-697.77, -77.78) * mm});
            skLineSegment(sketch, "E354", {"start": v(-697.77, -77.78) * mm, "end": v(-697.94, -77.87) * mm});
            skLineSegment(sketch, "E355", {"start": v(-697.94, -77.87) * mm, "end": v(-698.08, -78.04) * mm});
            skLineSegment(sketch, "E356", {"start": v(-698.08, -78.04) * mm, "end": v(-698.2, -78.18) * mm});
            skLineSegment(sketch, "E357", {"start": v(-698.2, -78.18) * mm, "end": v(-699.45, -79.46) * mm});
            skLineSegment(sketch, "E358", {"start": v(-699.45, -79.46) * mm, "end": v(-699.57, -79.6) * mm});
            skLineSegment(sketch, "E359", {"start": v(-699.57, -79.6) * mm, "end": v(-699.62, -79.65) * mm});
            skLineSegment(sketch, "E360", {"start": v(-699.62, -79.65) * mm, "end": v(-713.4, -100.09) * mm});
            skLineSegment(sketch, "E361", {"start": v(-713.4, -100.09) * mm, "end": v(-693.84, -86.5) * mm});
            skLineSegment(sketch, "E362", {"start": v(-693.84, -86.5) * mm, "end": v(-693.79, -86.46) * mm});
            skLineSegment(sketch, "E363", {"start": v(-693.79, -86.46) * mm, "end": v(-691.75, -84.63) * mm});
            skLineSegment(sketch, "E364", {"start": v(-691.75, -84.63) * mm, "end": v(-685.83, -78.92) * mm});
            skLineSegment(sketch, "E365", {"start": v(-685.83, -78.92) * mm, "end": v(-678.24, -71.07) * mm});
            skLineSegment(sketch, "E366", {"start": v(-678.24, -71.07) * mm, "end": v(-670.88, -63) * mm});
            skLineSegment(sketch, "E367", {"start": v(-670.88, -63) * mm, "end": v(-665.43, -56.84) * mm});
            skLineSegment(sketch, "E368", {"start": v(-665.43, -56.84) * mm, "end": v(-663.62, -54.79) * mm});
            skLineSegment(sketch, "E369", {"start": v(-663.62, -54.79) * mm, "end": v(-663.06, -54.15) * mm});
            skLineSegment(sketch, "E370", {"start": v(-663.06, -54.15) * mm, "end": v(-660.4, -50.78) * mm});
            skLineSegment(sketch, "E371", {"start": v(-660.4, -50.78) * mm, "end": v(-657.9, -47.3) * mm});
            skLineSegment(sketch, "E372", {"start": v(-657.9, -47.3) * mm, "end": v(-657.4, -46.6) * mm});
            skLineSegment(sketch, "E373", {"start": v(-657.4, -46.6) * mm, "end": v(-656.84, -45.8) * mm});
            skLineSegment(sketch, "E374", {"start": v(-656.84, -45.8) * mm, "end": v(-655.15, -43.44) * mm});
            skLineSegment(sketch, "E375", {"start": v(-655.15, -43.44) * mm, "end": v(-652.58, -40.08) * mm});
            skLineSegment(sketch, "E376", {"start": v(-652.58, -40.08) * mm, "end": v(-649.77, -36.97) * mm});
            skLineSegment(sketch, "E377", {"start": v(-649.77, -36.97) * mm, "end": v(-647.58, -35.08) * mm});
            skLineSegment(sketch, "E378", {"start": v(-647.58, -35.08) * mm, "end": v(-646.77, -34.58) * mm});
            skLineSegment(sketch, "E379", {"start": v(-646.77, -34.58) * mm, "end": v(-645.68, -33.92) * mm});
            skLineSegment(sketch, "E380", {"start": v(-645.68, -33.92) * mm, "end": v(-639.99, -31.08) * mm});
            skLineSegment(sketch, "E381", {"start": v(-639.99, -31.08) * mm, "end": v(-634.28, -28.3) * mm});
            skLineSegment(sketch, "E382", {"start": v(-634.28, -28.3) * mm, "end": v(-633.18, -27.67) * mm});
            skLineSegment(sketch, "E383", {"start": v(-633.18, -27.67) * mm, "end": v(-632.97, -28) * mm});
            skLineSegment(sketch, "E384", {"start": v(-632.97, -28) * mm, "end": v(-632.68, -29.17) * mm});
            skLineSegment(sketch, "E385", {"start": v(-632.68, -29.17) * mm, "end": v(-632.84, -30.74) * mm});
            skLineSegment(sketch, "E386", {"start": v(-632.84, -30.74) * mm, "end": v(-633.36, -32.33) * mm});
            skLineSegment(sketch, "E387", {"start": v(-633.36, -32.33) * mm, "end": v(-633.82, -33.5) * mm});
            skLineSegment(sketch, "E388", {"start": v(-633.82, -33.5) * mm, "end": v(-633.96, -33.9) * mm});
            skLineSegment(sketch, "E389", {"start": v(-633.96, -33.9) * mm, "end": v(-634.04, -34.14) * mm});
            skLineSegment(sketch, "E390", {"start": v(-634.04, -34.14) * mm, "end": v(-634.4, -35.35) * mm});
            skLineSegment(sketch, "E391", {"start": v(-634.4, -35.35) * mm, "end": v(-634.62, -36.57) * mm});
            skLineSegment(sketch, "E392", {"start": v(-634.62, -36.57) * mm, "end": v(-634.64, -36.82) * mm});
            skLineSegment(sketch, "E393", {"start": v(-634.64, -36.82) * mm, "end": v(-635.73, -38.27) * mm});
            skLineSegment(sketch, "E394", {"start": v(-635.73, -38.27) * mm, "end": v(-639.26, -42.4) * mm});
            skLineSegment(sketch, "E395", {"start": v(-639.26, -42.4) * mm, "end": v(-644.08, -47.76) * mm});
            skLineSegment(sketch, "E396", {"start": v(-644.08, -47.76) * mm, "end": v(-648.72, -53.25) * mm});
            skLineSegment(sketch, "E397", {"start": v(-648.72, -53.25) * mm, "end": v(-651.9, -57.7) * mm});
            skLineSegment(sketch, "E398", {"start": v(-651.9, -57.7) * mm, "end": v(-652.8, -59.28) * mm});
            skLineSegment(sketch, "E399", {"start": v(-652.8, -59.28) * mm, "end": v(-653.97, -59.97) * mm});
            skLineSegment(sketch, "E400", {"start": v(-653.97, -59.97) * mm, "end": v(-657.2, -62.52) * mm});
            skLineSegment(sketch, "E401", {"start": v(-657.2, -62.52) * mm, "end": v(-660.91, -66.37) * mm});
            skLineSegment(sketch, "E402", {"start": v(-660.91, -66.37) * mm, "end": v(-664.27, -70.58) * mm});
            skLineSegment(sketch, "E403", {"start": v(-664.27, -70.58) * mm, "end": v(-666.75, -73.83) * mm});
            skLineSegment(sketch, "E404", {"start": v(-666.75, -73.83) * mm, "end": v(-667.6, -74.9) * mm});
            skLineSegment(sketch, "E405", {"start": v(-667.6, -74.9) * mm, "end": v(-667.67, -74.99) * mm});
            skLineSegment(sketch, "E406", {"start": v(-667.67, -74.99) * mm, "end": v(-668.46, -75.86) * mm});
            skLineSegment(sketch, "E407", {"start": v(-668.46, -75.86) * mm, "end": v(-668.54, -75.95) * mm});
            skLineSegment(sketch, "E408", {"start": v(-668.54, -75.95) * mm, "end": v(-668.69, -76.12) * mm});
            skLineSegment(sketch, "E409", {"start": v(-668.69, -76.12) * mm, "end": v(-672.34, -88.94) * mm});
            skLineSegment(sketch, "E410", {"start": v(-672.34, -88.94) * mm, "end": v(-653.47, -70) * mm});
            skLineSegment(sketch, "E411", {"start": v(-653.47, -70) * mm, "end": v(-653.45, -69.98) * mm});
            skLineSegment(sketch, "E412", {"start": v(-653.45, -69.98) * mm, "end": v(-653.03, -69.5) * mm});
            skLineSegment(sketch, "E413", {"start": v(-653.03, -69.5) * mm, "end": v(-650.84, -67.2) * mm});
            skLineSegment(sketch, "E414", {"start": v(-650.84, -67.2) * mm, "end": v(-648.56, -64.96) * mm});
            skLineSegment(sketch, "E415", {"start": v(-648.56, -64.96) * mm, "end": v(-648.1, -64.52) * mm});
            skLineSegment(sketch, "E416", {"start": v(-648.1, -64.52) * mm, "end": v(-640.17, -56.62) * mm});
            skLineSegment(sketch, "E417", {"start": v(-640.17, -56.62) * mm, "end": v(-638.5, -54.93) * mm});
            skLineSegment(sketch, "E418", {"start": v(-638.5, -54.93) * mm, "end": v(-630.35, -46.25) * mm});
            skLineSegment(sketch, "E419", {"start": v(-630.35, -46.25) * mm, "end": v(-622.54, -37.26) * mm});
            skLineSegment(sketch, "E420", {"start": v(-622.54, -37.26) * mm, "end": v(-621.02, -35.42) * mm});
            skLineSegment(sketch, "E421", {"start": v(-621.02, -35.42) * mm, "end": v(-619.44, -33.49) * mm});
            skLineSegment(sketch, "E422", {"start": v(-619.44, -33.49) * mm, "end": v(-614.73, -27.67) * mm});
            skLineSegment(sketch, "E423", {"start": v(-614.73, -27.67) * mm, "end": v(-608.28, -19.98) * mm});
            skLineSegment(sketch, "E424", {"start": v(-608.28, -19.98) * mm, "end": v(-601.45, -12.64) * mm});
            skLineSegment(sketch, "E425", {"start": v(-601.45, -12.64) * mm, "end": v(-595.97, -7.53) * mm});
            skLineSegment(sketch, "E426", {"start": v(-595.97, -7.53) * mm, "end": v(-594.02, -5.97) * mm});
            skLineSegment(sketch, "E427", {"start": v(-594.02, -5.97) * mm, "end": v(-593.24, -5.34) * mm});
            skLineSegment(sketch, "E428", {"start": v(-593.24, -5.34) * mm, "end": v(-590.94, -3.39) * mm});
            skLineSegment(sketch, "E429", {"start": v(-590.94, -3.39) * mm, "end": v(-587.56, -0.67) * mm});
            skLineSegment(sketch, "E430", {"start": v(-587.56, -0.67) * mm, "end": v(-583.93, 1.67) * mm});
            skLineSegment(sketch, "E431", {"start": v(-583.93, 1.67) * mm, "end": v(-581.1, 2.89) * mm});
            skLineSegment(sketch, "E432", {"start": v(-581.1, 2.89) * mm, "end": v(-580.12, 3.09) * mm});
            skLineSegment(sketch, "E433", {"start": v(-580.12, 3.09) * mm, "end": v(-580.39, 2.33) * mm});
            skLineSegment(sketch, "E434", {"start": v(-580.39, 2.33) * mm, "end": v(-581.45, 0.16) * mm});
            skLineSegment(sketch, "E435", {"start": v(-581.45, 0.16) * mm, "end": v(-583.18, -2.58) * mm});
            skLineSegment(sketch, "E436", {"start": v(-583.18, -2.58) * mm, "end": v(-585.14, -5.17) * mm});
            skLineSegment(sketch, "E437", {"start": v(-585.14, -5.17) * mm, "end": v(-586.66, -7.04) * mm});
            skLineSegment(sketch, "E438", {"start": v(-586.66, -7.04) * mm, "end": v(-587.17, -7.67) * mm});
            skLineSegment(sketch, "E439", {"start": v(-587.17, -7.67) * mm, "end": v(-588.61, -9.44) * mm});
            skLineSegment(sketch, "E440", {"start": v(-588.61, -9.44) * mm, "end": v(-593.04, -14.68) * mm});
            skLineSegment(sketch, "E441", {"start": v(-593.04, -14.68) * mm, "end": v(-598.95, -21.68) * mm});
            skLineSegment(sketch, "E442", {"start": v(-598.95, -21.68) * mm, "end": v(-604.67, -28.81) * mm});
            skLineSegment(sketch, "E443", {"start": v(-604.67, -28.81) * mm, "end": v(-608.74, -34.34) * mm});
            skLineSegment(sketch, "E444", {"start": v(-608.74, -34.34) * mm, "end": v(-610, -36.25) * mm});
            skLineSegment(sketch, "E445", {"start": v(-610, -36.25) * mm, "end": v(-610.3, -36.7) * mm});
            skLineSegment(sketch, "E446", {"start": v(-610.3, -36.7) * mm, "end": v(-611.32, -37.96) * mm});
            skLineSegment(sketch, "E447", {"start": v(-611.32, -37.96) * mm, "end": v(-612.6, -39.69) * mm});
            skLineSegment(sketch, "E448", {"start": v(-612.6, -39.69) * mm, "end": v(-613.36, -41.6) * mm});
            skLineSegment(sketch, "E449", {"start": v(-613.36, -41.6) * mm, "end": v(-613.34, -43.33) * mm});
            skLineSegment(sketch, "E450", {"start": v(-613.34, -43.33) * mm, "end": v(-613.16, -43.86) * mm});
            skLineSegment(sketch, "E451", {"start": v(-613.16, -43.86) * mm, "end": v(-612.95, -44.46) * mm});
            skLineSegment(sketch, "E452", {"start": v(-612.95, -44.46) * mm, "end": v(-612.31, -44.56) * mm});
            skLineSegment(sketch, "E453", {"start": v(-612.31, -44.56) * mm, "end": v(-611.78, -44.66) * mm});
            skLineSegment(sketch, "E454", {"start": v(-611.78, -44.66) * mm, "end": v(-610.12, -44.56) * mm});
            skLineSegment(sketch, "E455", {"start": v(-610.12, -44.56) * mm, "end": v(-608.55, -43.76) * mm});
            skLineSegment(sketch, "E456", {"start": v(-608.55, -43.76) * mm, "end": v(-607.42, -42.33) * mm});
            skLineSegment(sketch, "E457", {"start": v(-607.42, -42.33) * mm, "end": v(-606.7, -40.92) * mm});
            skLineSegment(sketch, "E458", {"start": v(-606.7, -40.92) * mm, "end": v(-606.51, -40.43) * mm});
            skLineSegment(sketch, "E459", {"start": v(-606.51, -40.43) * mm, "end": v(-606.45, -40.27) * mm});
            skLineSegment(sketch, "E460", {"start": v(-606.45, -40.27) * mm, "end": v(-606.1, -39.44) * mm});
            skLineSegment(sketch, "E461", {"start": v(-606.1, -39.44) * mm, "end": v(-605.68, -38.65) * mm});
            skLineSegment(sketch, "E462", {"start": v(-605.68, -38.65) * mm, "end": v(-605.58, -38.5) * mm});
            skLineSegment(sketch, "E463", {"start": v(-605.58, -38.5) * mm, "end": v(-604.8, -37.42) * mm});
            skLineSegment(sketch, "E464", {"start": v(-604.8, -37.42) * mm, "end": v(-602.03, -34.5) * mm});
            skLineSegment(sketch, "E465", {"start": v(-602.03, -34.5) * mm, "end": v(-597.8, -30.92) * mm});
            skLineSegment(sketch, "E466", {"start": v(-597.8, -30.92) * mm, "end": v(-593.38, -27.47) * mm});
            skLineSegment(sketch, "E467", {"start": v(-593.38, -27.47) * mm, "end": v(-590.23, -24.83) * mm});
            skLineSegment(sketch, "E468", {"start": v(-590.23, -24.83) * mm, "end": v(-589.27, -23.87) * mm});
            skLineSegment(sketch, "E469", {"start": v(-589.27, -23.87) * mm, "end": v(-588.6, -23.21) * mm});
            skLineSegment(sketch, "E470", {"start": v(-588.6, -23.21) * mm, "end": v(-585.52, -19.68) * mm});
            skLineSegment(sketch, "E471", {"start": v(-585.52, -19.68) * mm, "end": v(-582.5, -16.1) * mm});
            skLineSegment(sketch, "E472", {"start": v(-582.5, -16.1) * mm, "end": v(-581.85, -15.42) * mm});
            skLineSegment(sketch, "E473", {"start": v(-581.85, -15.42) * mm, "end": v(-581.21, -14.74) * mm});
            skLineSegment(sketch, "E474", {"start": v(-581.21, -14.74) * mm, "end": v(-577.7, -11.7) * mm});
            skLineSegment(sketch, "E475", {"start": v(-577.7, -11.7) * mm, "end": v(-574.17, -8.69) * mm});
            skLineSegment(sketch, "E476", {"start": v(-574.17, -8.69) * mm, "end": v(-573.52, -8.02) * mm});
            skLineSegment(sketch, "E477", {"start": v(-573.52, -8.02) * mm, "end": v(-573.2, -7.7) * mm});
            skLineSegment(sketch, "E478", {"start": v(-573.2, -7.7) * mm, "end": v(-572.35, -6.66) * mm});
            skLineSegment(sketch, "E479", {"start": v(-572.35, -6.66) * mm, "end": v(-571.31, -5.2) * mm});
            skLineSegment(sketch, "E480", {"start": v(-571.31, -5.2) * mm, "end": v(-570.28, -3.74) * mm});
            skLineSegment(sketch, "E481", {"start": v(-570.28, -3.74) * mm, "end": v(-569.44, -2.7) * mm});
            skLineSegment(sketch, "E482", {"start": v(-569.44, -2.7) * mm, "end": v(-569.13, -2.4) * mm});
            skLineSegment(sketch, "E483", {"start": v(-569.13, -2.4) * mm, "end": v(-567.24, -0.48) * mm});
            skLineSegment(sketch, "E484", {"start": v(-567.24, -0.48) * mm, "end": v(-557.99, 9.3) * mm});
            skLineSegment(sketch, "E485", {"start": v(-557.99, 9.3) * mm, "end": v(-548.64, 18.97) * mm});
            skLineSegment(sketch, "E486", {"start": v(-548.64, 18.97) * mm, "end": v(-546.7, 20.83) * mm});
            skLineSegment(sketch, "E487", {"start": v(-546.7, 20.83) * mm, "end": v(-546.36, 21.15) * mm});
            skLineSegment(sketch, "E488", {"start": v(-546.36, 21.15) * mm, "end": v(-546.37, 21.62) * mm});
            skLineSegment(sketch, "E489", {"start": v(-546.37, 21.62) * mm, "end": v(-546.37, 21.85) * mm});
            skLineSegment(sketch, "E490", {"start": v(-546.37, 21.85) * mm, "end": v(-546.25, 22.87) * mm});
            skLineSegment(sketch, "E491", {"start": v(-546.25, 22.87) * mm, "end": v(-545.98, 23.83) * mm});
            skLineSegment(sketch, "E492", {"start": v(-545.98, 23.83) * mm, "end": v(-545.91, 24.03) * mm});
            skLineSegment(sketch, "E493", {"start": v(-545.91, 24.03) * mm, "end": v(-545.45, 24.3) * mm});
            skLineSegment(sketch, "E494", {"start": v(-545.45, 24.3) * mm, "end": v(-543.25, 25.8) * mm});
            skLineSegment(sketch, "E495", {"start": v(-543.25, 25.8) * mm, "end": v(-541.08, 27.35) * mm});
            skLineSegment(sketch, "E496", {"start": v(-541.08, 27.35) * mm, "end": v(-540.63, 27.64) * mm});
            skLineSegment(sketch, "E497", {"start": v(-540.63, 27.64) * mm, "end": v(-539.68, 27.9) * mm});
            skLineSegment(sketch, "E498", {"start": v(-539.68, 27.9) * mm, "end": v(-536.97, 29.16) * mm});
            skLineSegment(sketch, "E499", {"start": v(-536.97, 29.16) * mm, "end": v(-533.45, 31.18) * mm});
            skLineSegment(sketch, "E500", {"start": v(-533.45, 31.18) * mm, "end": v(-529.93, 32.99) * mm});
            skLineSegment(sketch, "E501", {"start": v(-529.93, 32.99) * mm, "end": v(-527.17, 33.84) * mm});
            skLineSegment(sketch, "E502", {"start": v(-527.17, 33.84) * mm, "end": v(-526.24, 33.89) * mm});
            skLineSegment(sketch, "E503", {"start": v(-526.24, 33.89) * mm, "end": v(-526.07, 33.52) * mm});
            skLineSegment(sketch, "E504", {"start": v(-526.07, 33.52) * mm, "end": v(-525.98, 32.22) * mm});
            skLineSegment(sketch, "E505", {"start": v(-525.98, 32.22) * mm, "end": v(-526.5, 30.5) * mm});
            skLineSegment(sketch, "E506", {"start": v(-526.5, 30.5) * mm, "end": v(-527.4, 28.87) * mm});
            skLineSegment(sketch, "E507", {"start": v(-527.4, 28.87) * mm, "end": v(-528.07, 27.77) * mm});
            skLineSegment(sketch, "E508", {"start": v(-528.07, 27.77) * mm, "end": v(-528.27, 27.4) * mm});
            skLineSegment(sketch, "E509", {"start": v(-528.27, 27.4) * mm, "end": v(-529.17, 25.7) * mm});
            skLineSegment(sketch, "E510", {"start": v(-529.17, 25.7) * mm, "end": v(-532.24, 20.82) * mm});
            skLineSegment(sketch, "E511", {"start": v(-532.24, 20.82) * mm, "end": v(-536.65, 14.67) * mm});
            skLineSegment(sketch, "E512", {"start": v(-536.65, 14.67) * mm, "end": v(-541.27, 8.69) * mm});
            skLineSegment(sketch, "E513", {"start": v(-541.27, 8.69) * mm, "end": v(-544.76, 4.14) * mm});
            skLineSegment(sketch, "E514", {"start": v(-544.76, 4.14) * mm, "end": v(-545.88, 2.6) * mm});
            skLineSegment(sketch, "E515", {"start": v(-545.88, 2.6) * mm, "end": v(-547.13, 1.58) * mm});
            skLineSegment(sketch, "E516", {"start": v(-547.13, 1.58) * mm, "end": v(-550.5, -1.94) * mm});
            skLineSegment(sketch, "E517", {"start": v(-550.5, -1.94) * mm, "end": v(-554.64, -6.95) * mm});
            skLineSegment(sketch, "E518", {"start": v(-554.64, -6.95) * mm, "end": v(-558.8, -11.9) * mm});
            skLineSegment(sketch, "E519", {"start": v(-558.8, -11.9) * mm, "end": v(-562.23, -15.33) * mm});
            skLineSegment(sketch, "E520", {"start": v(-562.23, -15.33) * mm, "end": v(-563.5, -16.3) * mm});
            skLineSegment(sketch, "E521", {"start": v(-563.5, -16.3) * mm, "end": v(-563.67, -16.45) * mm});
            skLineSegment(sketch, "E522", {"start": v(-563.67, -16.45) * mm, "end": v(-563.77, -16.63) * mm});
            skLineSegment(sketch, "E523", {"start": v(-563.77, -16.63) * mm, "end": v(-564.64, -18.18) * mm});
            skLineSegment(sketch, "E524", {"start": v(-564.64, -18.18) * mm, "end": v(-567.63, -22.62) * mm});
            skLineSegment(sketch, "E525", {"start": v(-567.63, -22.62) * mm, "end": v(-572.04, -28.17) * mm});
            skLineSegment(sketch, "E526", {"start": v(-572.04, -28.17) * mm, "end": v(-576.8, -33.43) * mm});
            skLineSegment(sketch, "E527", {"start": v(-576.8, -33.43) * mm, "end": v(-580.49, -37.28) * mm});
            skLineSegment(sketch, "E528", {"start": v(-580.49, -37.28) * mm, "end": v(-581.72, -38.56) * mm});
            skLineSegment(sketch, "E529", {"start": v(-581.72, -38.56) * mm, "end": v(-582.2, -39.05) * mm});
            skLineSegment(sketch, "E530", {"start": v(-582.2, -39.05) * mm, "end": v(-583.68, -40.47) * mm});
            skLineSegment(sketch, "E531", {"start": v(-583.68, -40.47) * mm, "end": v(-585.5, -42.47) * mm});
            skLineSegment(sketch, "E532", {"start": v(-585.5, -42.47) * mm, "end": v(-586.66, -44.78) * mm});
            skLineSegment(sketch, "E533", {"start": v(-586.66, -44.78) * mm, "end": v(-586.85, -46.96) * mm});
            skLineSegment(sketch, "E534", {"start": v(-586.85, -46.96) * mm, "end": v(-586.7, -47.64) * mm});
            skLineSegment(sketch, "E535", {"start": v(-586.7, -47.64) * mm, "end": v(-586.52, -48.44) * mm});
            skLineSegment(sketch, "E536", {"start": v(-586.52, -48.44) * mm, "end": v(-585.7, -48.48) * mm});
            skLineSegment(sketch, "E537", {"start": v(-585.7, -48.48) * mm, "end": v(-585.3, -48.5) * mm});
            skLineSegment(sketch, "E538", {"start": v(-585.3, -48.5) * mm, "end": v(-584.08, -48.35) * mm});
            skLineSegment(sketch, "E539", {"start": v(-584.08, -48.35) * mm, "end": v(-582.74, -47.86) * mm});
            skLineSegment(sketch, "E540", {"start": v(-582.74, -47.86) * mm, "end": v(-581.6, -47.08) * mm});
            skLineSegment(sketch, "E541", {"start": v(-581.6, -47.08) * mm, "end": v(-580.63, -46.08) * mm});
            skLineSegment(sketch, "E542", {"start": v(-580.63, -46.08) * mm, "end": v(-579.76, -44.94) * mm});
            skLineSegment(sketch, "E543", {"start": v(-579.76, -44.94) * mm, "end": v(-578.93, -43.75) * mm});
            skLineSegment(sketch, "E544", {"start": v(-578.93, -43.75) * mm, "end": v(-578.08, -42.56) * mm});
            skLineSegment(sketch, "E545", {"start": v(-578.08, -42.56) * mm, "end": v(-577.4, -41.73) * mm});
            skLineSegment(sketch, "E546", {"start": v(-577.4, -41.73) * mm, "end": v(-577.16, -41.47) * mm});
            skLineSegment(sketch, "E547", {"start": v(-577.16, -41.47) * mm, "end": v(-576.8, -41.09) * mm});
            skLineSegment(sketch, "E548", {"start": v(-576.8, -41.09) * mm, "end": v(-574.72, -39.34) * mm});
            skLineSegment(sketch, "E549", {"start": v(-574.72, -39.34) * mm, "end": v(-572.6, -37.64) * mm});
            skLineSegment(sketch, "E550", {"start": v(-572.6, -37.64) * mm, "end": v(-572.2, -37.28) * mm});
            skLineSegment(sketch, "E551", {"start": v(-572.2, -37.28) * mm, "end": v(-571.27, -36.44) * mm});
            skLineSegment(sketch, "E552", {"start": v(-571.27, -36.44) * mm, "end": v(-568.56, -33.86) * mm});
            skLineSegment(sketch, "E553", {"start": v(-568.56, -33.86) * mm, "end": v(-564.91, -30.39) * mm});
            skLineSegment(sketch, "E554", {"start": v(-564.91, -30.39) * mm, "end": v(-561.17, -27.03) * mm});
            skLineSegment(sketch, "E555", {"start": v(-561.17, -27.03) * mm, "end": v(-558.25, -24.7) * mm});
            skLineSegment(sketch, "E556", {"start": v(-558.25, -24.7) * mm, "end": v(-557.24, -23.98) * mm});
            skLineSegment(sketch, "E557", {"start": v(-557.24, -23.98) * mm, "end": v(-557.12, -23.9) * mm});
            skLineSegment(sketch, "E558", {"start": v(-557.12, -23.9) * mm, "end": v(-557.04, -23.8) * mm});
            skLineSegment(sketch, "E559", {"start": v(-557.04, -23.8) * mm, "end": v(-554.46, -20.82) * mm});
            skLineSegment(sketch, "E560", {"start": v(-554.46, -20.82) * mm, "end": v(-541.68, -5.8) * mm});
            skLineSegment(sketch, "E561", {"start": v(-541.68, -5.8) * mm, "end": v(-528.82, 9.14) * mm});
            skLineSegment(sketch, "E562", {"start": v(-528.82, 9.14) * mm, "end": v(-526.2, 12.09) * mm});
            skLineSegment(sketch, "E563", {"start": v(-526.2, 12.09) * mm, "end": v(-524.88, 13.55) * mm});
            skLineSegment(sketch, "E564", {"start": v(-524.88, 13.55) * mm, "end": v(-517.93, 20.5) * mm});
            skLineSegment(sketch, "E565", {"start": v(-517.93, 20.5) * mm, "end": v(-511.04, 27.5) * mm});
            skLineSegment(sketch, "E566", {"start": v(-511.04, 27.5) * mm, "end": v(-509.76, 28.98) * mm});
            skLineSegment(sketch, "E567", {"start": v(-509.76, 28.98) * mm, "end": v(-509.11, 29.74) * mm});
            skLineSegment(sketch, "E568", {"start": v(-509.11, 29.74) * mm, "end": v(-502.7, 37.4) * mm});
            skLineSegment(sketch, "E569", {"start": v(-502.7, 37.4) * mm, "end": v(-502.07, 38.17) * mm});
            skLineSegment(sketch, "E570", {"start": v(-502.07, 38.17) * mm, "end": v(-501.4, 38.95) * mm});
            skLineSegment(sketch, "E571", {"start": v(-501.4, 38.95) * mm, "end": v(-498.49, 43.08) * mm});
            skLineSegment(sketch, "E572", {"start": v(-498.49, 43.08) * mm, "end": v(-495.63, 47.25) * mm});
            skLineSegment(sketch, "E573", {"start": v(-495.63, 47.25) * mm, "end": v(-495, 48.04) * mm});
            skLineSegment(sketch, "E574", {"start": v(-495, 48.04) * mm, "end": v(-494.58, 48.55) * mm});
            skLineSegment(sketch, "E575", {"start": v(-494.58, 48.55) * mm, "end": v(-492.12, 50.88) * mm});
            skLineSegment(sketch, "E576", {"start": v(-492.12, 50.88) * mm, "end": v(-489.55, 53.12) * mm});
            skLineSegment(sketch, "E577", {"start": v(-489.55, 53.12) * mm, "end": v(-489.07, 53.58) * mm});
            skLineSegment(sketch, "E578", {"start": v(-489.07, 53.58) * mm, "end": v(-488.56, 54.06) * mm});
            skLineSegment(sketch, "E579", {"start": v(-488.56, 54.06) * mm, "end": v(-486.27, 56.79) * mm});
            skLineSegment(sketch, "E580", {"start": v(-486.27, 56.79) * mm, "end": v(-483.94, 59.42) * mm});
            skLineSegment(sketch, "E581", {"start": v(-483.94, 59.42) * mm, "end": v(-483.42, 59.85) * mm});
            skLineSegment(sketch, "E582", {"start": v(-483.42, 59.85) * mm, "end": v(-482.73, 60.43) * mm});
            skLineSegment(sketch, "E583", {"start": v(-482.73, 60.43) * mm, "end": v(-479.07, 63.13) * mm});
            skLineSegment(sketch, "E584", {"start": v(-479.07, 63.13) * mm, "end": v(-475.27, 65.63) * mm});
            skLineSegment(sketch, "E585", {"start": v(-475.27, 65.63) * mm, "end": v(-474.5, 66.1) * mm});
            skLineSegment(sketch, "E586", {"start": v(-474.5, 66.1) * mm, "end": v(-473.75, 66.57) * mm});
            skLineSegment(sketch, "E587", {"start": v(-473.75, 66.57) * mm, "end": v(-469.67, 68.72) * mm});
            skLineSegment(sketch, "E588", {"start": v(-469.67, 68.72) * mm, "end": v(-465.32, 70.25) * mm});
            skLineSegment(sketch, "E589", {"start": v(-465.32, 70.25) * mm, "end": v(-464.43, 70.4) * mm});
            skLineSegment(sketch, "E590", {"start": v(-464.43, 70.4) * mm, "end": v(-464.2, 70.06) * mm});
            skLineSegment(sketch, "E591", {"start": v(-464.2, 70.06) * mm, "end": v(-463.82, 68.8) * mm});
            skLineSegment(sketch, "E592", {"start": v(-463.82, 68.8) * mm, "end": v(-463.78, 66.98) * mm});
            skLineSegment(sketch, "E593", {"start": v(-463.78, 66.98) * mm, "end": v(-464.12, 65.15) * mm});
            skLineSegment(sketch, "E594", {"start": v(-464.12, 65.15) * mm, "end": v(-464.5, 63.94) * mm});
            skLineSegment(sketch, "E595", {"start": v(-464.5, 63.94) * mm, "end": v(-464.65, 63.54) * mm});
            skLineSegment(sketch, "E596", {"start": v(-464.65, 63.54) * mm, "end": v(-465.03, 62.6) * mm});
            skLineSegment(sketch, "E597", {"start": v(-465.03, 62.6) * mm, "end": v(-466.63, 59.99) * mm});
            skLineSegment(sketch, "E598", {"start": v(-466.63, 59.99) * mm, "end": v(-469.18, 56.65) * mm});
            skLineSegment(sketch, "E599", {"start": v(-469.18, 56.65) * mm, "end": v(-471.7, 53.29) * mm});
            skLineSegment(sketch, "E600", {"start": v(-471.7, 53.29) * mm, "end": v(-473.26, 50.63) * mm});
            skLineSegment(sketch, "E601", {"start": v(-473.26, 50.63) * mm, "end": v(-473.6, 49.68) * mm});
            skLineSegment(sketch, "E602", {"start": v(-473.6, 49.68) * mm, "end": v(-474.86, 48.55) * mm});
            skLineSegment(sketch, "E603", {"start": v(-474.86, 48.55) * mm, "end": v(-478.45, 45) * mm});
            skLineSegment(sketch, "E604", {"start": v(-478.45, 45) * mm, "end": v(-483, 40.06) * mm});
            skLineSegment(sketch, "E605", {"start": v(-483, 40.06) * mm, "end": v(-487.32, 34.91) * mm});
            skLineSegment(sketch, "E606", {"start": v(-487.32, 34.91) * mm, "end": v(-491.51, 29.65) * mm});
            skLineSegment(sketch, "E607", {"start": v(-491.51, 29.65) * mm, "end": v(-495.66, 24.35) * mm});
            skLineSegment(sketch, "E608", {"start": v(-495.66, 24.35) * mm, "end": v(-499.84, 19.08) * mm});
            skLineSegment(sketch, "E609", {"start": v(-499.84, 19.08) * mm, "end": v(-504.15, 13.92) * mm});
            skLineSegment(sketch, "E610", {"start": v(-504.15, 13.92) * mm, "end": v(-507.51, 10.16) * mm});
            skLineSegment(sketch, "E611", {"start": v(-507.51, 10.16) * mm, "end": v(-508.67, 8.95) * mm});
            skLineSegment(sketch, "E612", {"start": v(-508.67, 8.95) * mm, "end": v(-508.82, 8.78) * mm});
            skLineSegment(sketch, "E613", {"start": v(-508.82, 8.78) * mm, "end": v(-508.9, 8.58) * mm});
            skLineSegment(sketch, "E614", {"start": v(-508.9, 8.58) * mm, "end": v(-509.34, 7.4) * mm});
            skLineSegment(sketch, "E615", {"start": v(-509.34, 7.4) * mm, "end": v(-511.34, 4.13) * mm});
            skLineSegment(sketch, "E616", {"start": v(-511.34, 4.13) * mm, "end": v(-514.62, 0.3) * mm});
            skLineSegment(sketch, "E617", {"start": v(-514.62, 0.3) * mm, "end": v(-518.26, -3.28) * mm});
            skLineSegment(sketch, "E618", {"start": v(-518.26, -3.28) * mm, "end": v(-520.95, -5.97) * mm});
            skLineSegment(sketch, "E619", {"start": v(-520.95, -5.97) * mm, "end": v(-521.78, -6.92) * mm});
            skLineSegment(sketch, "E620", {"start": v(-521.78, -6.92) * mm, "end": v(-521.97, -7.14) * mm});
            skLineSegment(sketch, "E621", {"start": v(-521.97, -7.14) * mm, "end": v(-522.46, -7.88) * mm});
            skLineSegment(sketch, "E622", {"start": v(-522.46, -7.88) * mm, "end": v(-523, -8.9) * mm});
            skLineSegment(sketch, "E623", {"start": v(-523, -8.9) * mm, "end": v(-523.53, -9.9) * mm});
            skLineSegment(sketch, "E624", {"start": v(-523.53, -9.9) * mm, "end": v(-523.97, -10.61) * mm});
            skLineSegment(sketch, "E625", {"start": v(-523.97, -10.61) * mm, "end": v(-524.14, -10.83) * mm});
            skLineSegment(sketch, "E626", {"start": v(-524.14, -10.83) * mm, "end": v(-524.73, -11.54) * mm});
            skLineSegment(sketch, "E627", {"start": v(-524.73, -11.54) * mm, "end": v(-527.96, -14.87) * mm});
            skLineSegment(sketch, "E628", {"start": v(-527.96, -14.87) * mm, "end": v(-531.23, -18.18) * mm});
            skLineSegment(sketch, "E629", {"start": v(-531.23, -18.18) * mm, "end": v(-531.84, -18.88) * mm});
            skLineSegment(sketch, "E630", {"start": v(-531.84, -18.88) * mm, "end": v(-533.69, -21.03) * mm});
            skLineSegment(sketch, "E631", {"start": v(-533.69, -21.03) * mm, "end": v(-543.48, -31.23) * mm});
            skLineSegment(sketch, "E632", {"start": v(-543.48, -31.23) * mm, "end": v(-553.58, -41.14) * mm});
            skLineSegment(sketch, "E633", {"start": v(-553.58, -41.14) * mm, "end": v(-555.58, -43.14) * mm});
            skLineSegment(sketch, "E634", {"start": v(-555.58, -43.14) * mm, "end": v(-555.75, -43.29) * mm});
            skLineSegment(sketch, "E635", {"start": v(-555.75, -43.29) * mm, "end": v(-555.82, -43.48) * mm});
            skLineSegment(sketch, "E636", {"start": v(-555.82, -43.48) * mm, "end": v(-555.96, -43.83) * mm});
            skLineSegment(sketch, "E637", {"start": v(-555.96, -43.83) * mm, "end": v(-556.45, -44.83) * mm});
            skLineSegment(sketch, "E638", {"start": v(-556.45, -44.83) * mm, "end": v(-557.08, -46.3) * mm});
            skLineSegment(sketch, "E639", {"start": v(-557.08, -46.3) * mm, "end": v(-557.42, -47.79) * mm});
            skLineSegment(sketch, "E640", {"start": v(-557.42, -47.79) * mm, "end": v(-557.35, -48.92) * mm});
            skLineSegment(sketch, "E641", {"start": v(-557.35, -48.92) * mm, "end": v(-557.2, -49.25) * mm});
            skLineSegment(sketch, "E642", {"start": v(-557.2, -49.25) * mm, "end": v(-557.11, -49.47) * mm});
            skLineSegment(sketch, "E643", {"start": v(-557.11, -49.47) * mm, "end": v(-556.35, -50.32) * mm});
            skLineSegment(sketch, "E644", {"start": v(-556.35, -50.32) * mm, "end": v(-555.34, -50.84) * mm});
            skLineSegment(sketch, "E645", {"start": v(-555.34, -50.84) * mm, "end": v(-555.1, -50.9) * mm});
            skLineSegment(sketch, "E646", {"start": v(-555.1, -50.9) * mm, "end": v(-554.38, -51.1) * mm});
            skLineSegment(sketch, "E647", {"start": v(-554.38, -51.1) * mm, "end": v(-553.95, -50.47) * mm});
            skLineSegment(sketch, "E648", {"start": v(-553.95, -50.47) * mm, "end": v(-552.48, -48.32) * mm});
            skLineSegment(sketch, "E649", {"start": v(-552.48, -48.32) * mm, "end": v(-547.56, -42.22) * mm});
            skLineSegment(sketch, "E650", {"start": v(-547.56, -42.22) * mm, "end": v(-540.52, -34.55) * mm});
            skLineSegment(sketch, "E651", {"start": v(-540.52, -34.55) * mm, "end": v(-533.23, -27.1) * mm});
            skLineSegment(sketch, "E652", {"start": v(-533.23, -27.1) * mm, "end": v(-527.82, -21.45) * mm});
            skLineSegment(sketch, "E653", {"start": v(-527.82, -21.45) * mm, "end": v(-526.08, -19.5) * mm});
            skLineSegment(sketch, "E654", {"start": v(-526.08, -19.5) * mm, "end": v(-525.91, -19.54) * mm});
            skLineSegment(sketch, "E655", {"start": v(-525.91, -19.54) * mm, "end": v(-525.04, -19.61) * mm});
            skLineSegment(sketch, "E656", {"start": v(-525.04, -19.61) * mm, "end": v(-524.25, -19.6) * mm});
            skLineSegment(sketch, "E657", {"start": v(-524.25, -19.6) * mm, "end": v(-523.99, -19.6) * mm});
            skLineSegment(sketch, "E658", {"start": v(-523.99, -19.6) * mm, "end": v(-523.53, -19.6) * mm});
            skLineSegment(sketch, "E659", {"start": v(-523.53, -19.6) * mm, "end": v(-523.22, -19.27) * mm});
            skLineSegment(sketch, "E660", {"start": v(-523.22, -19.27) * mm, "end": v(-523.05, -19.1) * mm});
            skLineSegment(sketch, "E661", {"start": v(-523.05, -19.1) * mm, "end": v(-522.7, -18.45) * mm});
            skLineSegment(sketch, "E662", {"start": v(-522.7, -18.45) * mm, "end": v(-522.34, -17.44) * mm});
            skLineSegment(sketch, "E663", {"start": v(-522.34, -17.44) * mm, "end": v(-522.06, -16.52) * mm});
            skLineSegment(sketch, "E664", {"start": v(-522.06, -16.52) * mm, "end": v(-521.88, -16.05) * mm});
            skLineSegment(sketch, "E665", {"start": v(-521.88, -16.05) * mm, "end": v(-521.78, -15.94) * mm});
            skLineSegment(sketch, "E666", {"start": v(-521.78, -15.94) * mm, "end": v(-521.62, -15.88) * mm});
            skLineSegment(sketch, "E667", {"start": v(-521.62, -15.88) * mm, "end": v(-521.17, -15.6) * mm});
            skLineSegment(sketch, "E668", {"start": v(-521.17, -15.6) * mm, "end": v(-520.6, -15.19) * mm});
            skLineSegment(sketch, "E669", {"start": v(-520.6, -15.19) * mm, "end": v(-520.06, -14.83) * mm});
            skLineSegment(sketch, "E670", {"start": v(-520.06, -14.83) * mm, "end": v(-519.69, -14.68) * mm});
            skLineSegment(sketch, "E671", {"start": v(-519.69, -14.68) * mm, "end": v(-519.56, -14.67) * mm});
            skLineSegment(sketch, "E672", {"start": v(-519.56, -14.67) * mm, "end": v(-519, -14.64) * mm});
            skLineSegment(sketch, "E673", {"start": v(-519, -14.64) * mm, "end": v(-518.7, -14.15) * mm});
            skLineSegment(sketch, "E674", {"start": v(-518.7, -14.15) * mm, "end": v(-518.01, -12.98) * mm});
            skLineSegment(sketch, "E675", {"start": v(-518.01, -12.98) * mm, "end": v(-515.67, -9.65) * mm});
            skLineSegment(sketch, "E676", {"start": v(-515.67, -9.65) * mm, "end": v(-512.19, -5.47) * mm});
            skLineSegment(sketch, "E677", {"start": v(-512.19, -5.47) * mm, "end": v(-508.37, -1.53) * mm});
            skLineSegment(sketch, "E678", {"start": v(-508.37, -1.53) * mm, "end": v(-504.32, 2.23) * mm});
            skLineSegment(sketch, "E679", {"start": v(-504.32, 2.23) * mm, "end": v(-500.16, 5.89) * mm});
            skLineSegment(sketch, "E680", {"start": v(-500.16, 5.89) * mm, "end": v(-495.98, 9.51) * mm});
            skLineSegment(sketch, "E681", {"start": v(-495.98, 9.51) * mm, "end": v(-491.9, 13.18) * mm});
            skLineSegment(sketch, "E682", {"start": v(-491.9, 13.18) * mm, "end": v(-488.97, 16) * mm});
            skLineSegment(sketch, "E683", {"start": v(-488.97, 16) * mm, "end": v(-488.03, 16.97) * mm});
            skLineSegment(sketch, "E684", {"start": v(-488.03, 16.97) * mm, "end": v(-487.22, 17.8) * mm});
            skLineSegment(sketch, "E685", {"start": v(-487.22, 17.8) * mm, "end": v(-484.87, 20.36) * mm});
            skLineSegment(sketch, "E686", {"start": v(-484.87, 20.36) * mm, "end": v(-481.72, 23.87) * mm});
            skLineSegment(sketch, "E687", {"start": v(-481.72, 23.87) * mm, "end": v(-478.55, 27.43) * mm});
            skLineSegment(sketch, "E688", {"start": v(-478.55, 27.43) * mm, "end": v(-475.32, 30.94) * mm});
            skLineSegment(sketch, "E689", {"start": v(-475.32, 30.94) * mm, "end": v(-471.97, 34.32) * mm});
            skLineSegment(sketch, "E690", {"start": v(-471.97, 34.32) * mm, "end": v(-468.48, 37.5) * mm});
            skLineSegment(sketch, "E691", {"start": v(-468.48, 37.5) * mm, "end": v(-464.8, 40.4) * mm});
            skLineSegment(sketch, "E692", {"start": v(-464.8, 40.4) * mm, "end": v(-461.9, 42.35) * mm});
            skLineSegment(sketch, "E693", {"start": v(-461.9, 42.35) * mm, "end": v(-460.89, 42.93) * mm});
            skLineSegment(sketch, "E694", {"start": v(-460.89, 42.93) * mm, "end": v(-460.76, 42.6) * mm});
            skLineSegment(sketch, "E695", {"start": v(-460.76, 42.6) * mm, "end": v(-460.4, 41.6) * mm});
            skLineSegment(sketch, "E696", {"start": v(-460.4, 41.6) * mm, "end": v(-459.97, 40.22) * mm});
            skLineSegment(sketch, "E697", {"start": v(-459.97, 40.22) * mm, "end": v(-459.7, 38.87) * mm});
            skLineSegment(sketch, "E698", {"start": v(-459.7, 38.87) * mm, "end": v(-459.65, 37.92) * mm});
            skLineSegment(sketch, "E699", {"start": v(-459.65, 37.92) * mm, "end": v(-459.7, 37.62) * mm});
            skLineSegment(sketch, "E700", {"start": v(-459.7, 37.62) * mm, "end": v(-459.7, 37.58) * mm});
            skLineSegment(sketch, "E701", {"start": v(-459.7, 37.58) * mm, "end": v(-459.78, 37.23) * mm});
            skLineSegment(sketch, "E702", {"start": v(-459.78, 37.23) * mm, "end": v(-459.8, 37.2) * mm});
            skLineSegment(sketch, "E703", {"start": v(-459.8, 37.2) * mm, "end": v(-459.86, 37) * mm});
            skLineSegment(sketch, "E704", {"start": v(-459.86, 37) * mm, "end": v(-460.5, 36.07) * mm});
            skLineSegment(sketch, "E705", {"start": v(-460.5, 36.07) * mm, "end": v(-461.26, 35.23) * mm});
            skLineSegment(sketch, "E706", {"start": v(-461.26, 35.23) * mm, "end": v(-461.39, 35.08) * mm});
            skLineSegment(sketch, "E707", {"start": v(-461.39, 35.08) * mm, "end": v(-461.62, 34.83) * mm});
            skLineSegment(sketch, "E708", {"start": v(-461.62, 34.83) * mm, "end": v(-462.66, 33.58) * mm});
            skLineSegment(sketch, "E709", {"start": v(-462.66, 33.58) * mm, "end": v(-463.5, 32.2) * mm});
            skLineSegment(sketch, "E710", {"start": v(-463.5, 32.2) * mm, "end": v(-463.63, 31.88) * mm});
            skLineSegment(sketch, "E711", {"start": v(-463.63, 31.88) * mm, "end": v(-463.71, 31.68) * mm});
            skLineSegment(sketch, "E712", {"start": v(-463.71, 31.68) * mm, "end": v(-463.97, 30.67) * mm});
            skLineSegment(sketch, "E713", {"start": v(-463.97, 30.67) * mm, "end": v(-464.1, 29.62) * mm});
            skLineSegment(sketch, "E714", {"start": v(-464.1, 29.62) * mm, "end": v(-464.11, 29.4) * mm});
            skLineSegment(sketch, "E715", {"start": v(-464.11, 29.4) * mm, "end": v(-464.12, 29.33) * mm});
            skLineSegment(sketch, "E716", {"start": v(-464.12, 29.33) * mm, "end": v(-464.16, 28.72) * mm});
            skLineSegment(sketch, "E717", {"start": v(-464.16, 28.72) * mm, "end": v(-464.26, 28.12) * mm});
            skLineSegment(sketch, "E718", {"start": v(-464.26, 28.12) * mm, "end": v(-464.3, 28.06) * mm});
            skLineSegment(sketch, "E719", {"start": v(-464.3, 28.06) * mm, "end": v(-464.37, 27.9) * mm});
            skLineSegment(sketch, "E720", {"start": v(-464.37, 27.9) * mm, "end": v(-464.75, 27.48) * mm});
            skLineSegment(sketch, "E721", {"start": v(-464.75, 27.48) * mm, "end": v(-465.48, 26.8) * mm});
            skLineSegment(sketch, "E722", {"start": v(-465.48, 26.8) * mm, "end": v(-466.26, 26.08) * mm});
            skLineSegment(sketch, "E723", {"start": v(-466.26, 26.08) * mm, "end": v(-466.76, 25.55) * mm});
            skLineSegment(sketch, "E724", {"start": v(-466.76, 25.55) * mm, "end": v(-466.9, 25.35) * mm});
            skLineSegment(sketch, "E725", {"start": v(-466.9, 25.35) * mm, "end": v(-467.02, 25.17) * mm});
            skLineSegment(sketch, "E726", {"start": v(-467.02, 25.17) * mm, "end": v(-467.3, 24.56) * mm});
            skLineSegment(sketch, "E727", {"start": v(-467.3, 24.56) * mm, "end": v(-467.6, 23.72) * mm});
            skLineSegment(sketch, "E728", {"start": v(-467.6, 23.72) * mm, "end": v(-467.88, 22.9) * mm});
            skLineSegment(sketch, "E729", {"start": v(-467.88, 22.9) * mm, "end": v(-468.13, 22.37) * mm});
            skLineSegment(sketch, "E730", {"start": v(-468.13, 22.37) * mm, "end": v(-468.23, 22.2) * mm});
            skLineSegment(sketch, "E731", {"start": v(-468.23, 22.2) * mm, "end": v(-469, 21.07) * mm});
            skLineSegment(sketch, "E732", {"start": v(-469, 21.07) * mm, "end": v(-471.68, 17.9) * mm});
            skLineSegment(sketch, "E733", {"start": v(-471.68, 17.9) * mm, "end": v(-475.61, 13.54) * mm});
            skLineSegment(sketch, "E734", {"start": v(-475.61, 13.54) * mm, "end": v(-479.22, 9.03) * mm});
            skLineSegment(sketch, "E735", {"start": v(-479.22, 9.03) * mm, "end": v(-481.26, 5.52) * mm});
            skLineSegment(sketch, "E736", {"start": v(-481.26, 5.52) * mm, "end": v(-481.67, 4.26) * mm});
            skLineSegment(sketch, "E737", {"start": v(-481.67, 4.26) * mm, "end": v(-482.51, 3.55) * mm});
            skLineSegment(sketch, "E738", {"start": v(-482.51, 3.55) * mm, "end": v(-484.78, 1.11) * mm});
            skLineSegment(sketch, "E739", {"start": v(-484.78, 1.11) * mm, "end": v(-487.44, -2.43) * mm});
            skLineSegment(sketch, "E740", {"start": v(-487.44, -2.43) * mm, "end": v(-489.88, -6.14) * mm});
            skLineSegment(sketch, "E741", {"start": v(-489.88, -6.14) * mm, "end": v(-491.7, -8.91) * mm});
            skLineSegment(sketch, "E742", {"start": v(-491.7, -8.91) * mm, "end": v(-492.35, -9.81) * mm});
            skLineSegment(sketch, "E743", {"start": v(-492.35, -9.81) * mm, "end": v(-492.96, -10.66) * mm});
            skLineSegment(sketch, "E744", {"start": v(-492.96, -10.66) * mm, "end": v(-499.56, -18.82) * mm});
            skLineSegment(sketch, "E745", {"start": v(-499.56, -18.82) * mm, "end": v(-500.25, -19.6) * mm});
            skLineSegment(sketch, "E746", {"start": v(-500.25, -19.6) * mm, "end": v(-501.73, -21.28) * mm});
            skLineSegment(sketch, "E747", {"start": v(-501.73, -21.28) * mm, "end": v(-490.3, -21.78) * mm});
            skLineSegment(sketch, "E748", {"start": v(-490.3, -21.78) * mm, "end": v(-489.99, -21.57) * mm});
            skLineSegment(sketch, "E749", {"start": v(-489.99, -21.57) * mm, "end": v(-489.81, -21.44) * mm});
            skLineSegment(sketch, "E750", {"start": v(-489.81, -21.44) * mm, "end": v(-488.09, -20.26) * mm});
            skLineSegment(sketch, "E751", {"start": v(-488.09, -20.26) * mm, "end": v(-487.9, -20.16) * mm});
            skLineSegment(sketch, "E752", {"start": v(-487.9, -20.16) * mm, "end": v(-487.27, -19.77) * mm});
            skLineSegment(sketch, "E753", {"start": v(-487.27, -19.77) * mm, "end": v(-485.32, -18.7) * mm});
            skLineSegment(sketch, "E754", {"start": v(-485.32, -18.7) * mm, "end": v(-482.68, -17.35) * mm});
            skLineSegment(sketch, "E755", {"start": v(-482.68, -17.35) * mm, "end": v(-480.04, -16.02) * mm});
            skLineSegment(sketch, "E756", {"start": v(-480.04, -16.02) * mm, "end": v(-477.47, -14.62) * mm});
            skLineSegment(sketch, "E757", {"start": v(-477.47, -14.62) * mm, "end": v(-475, -13.08) * mm});
            skLineSegment(sketch, "E758", {"start": v(-475, -13.08) * mm, "end": v(-472.7, -11.32) * mm});
            skLineSegment(sketch, "E759", {"start": v(-472.7, -11.32) * mm, "end": v(-470.6, -9.24) * mm});
            skLineSegment(sketch, "E760", {"start": v(-470.6, -9.24) * mm, "end": v(-469.2, -7.43) * mm});
            skLineSegment(sketch, "E761", {"start": v(-469.2, -7.43) * mm, "end": v(-468.8, -6.78) * mm});
            skLineSegment(sketch, "E762", {"start": v(-468.8, -6.78) * mm, "end": v(-468.51, -6.34) * mm});
            skLineSegment(sketch, "E763", {"start": v(-468.51, -6.34) * mm, "end": v(-468.7, -5.86) * mm});
            skLineSegment(sketch, "E764", {"start": v(-468.7, -5.86) * mm, "end": v(-468.87, -5.37) * mm});
            skLineSegment(sketch, "E765", {"start": v(-468.87, -5.37) * mm, "end": v(-469.48, -3.93) * mm});
            skLineSegment(sketch, "E766", {"start": v(-469.48, -3.93) * mm, "end": v(-470.63, -1.93) * mm});
            skLineSegment(sketch, "E767", {"start": v(-470.63, -1.93) * mm, "end": v(-472.18, -0.39) * mm});
            skLineSegment(sketch, "E768", {"start": v(-472.18, -0.39) * mm, "end": v(-473.67, 0.16) * mm});
            skLineSegment(sketch, "E769", {"start": v(-473.67, 0.16) * mm, "end": v(-474.14, 0.12) * mm});
            skLineSegment(sketch, "E770", {"start": v(-474.14, 0.12) * mm, "end": v(-474.56, 0.1) * mm});
            skLineSegment(sketch, "E771", {"start": v(-474.56, 0.1) * mm, "end": v(-475.8, -0.67) * mm});
            skLineSegment(sketch, "E772", {"start": v(-475.8, -0.67) * mm, "end": v(-477.14, -2.36) * mm});
            skLineSegment(sketch, "E773", {"start": v(-477.14, -2.36) * mm, "end": v(-478.32, -4.28) * mm});
            skLineSegment(sketch, "E774", {"start": v(-478.32, -4.28) * mm, "end": v(-479.11, -5.48) * mm});
            skLineSegment(sketch, "E775", {"start": v(-479.11, -5.48) * mm, "end": v(-479.45, -5.8) * mm});
            skLineSegment(sketch, "E776", {"start": v(-479.45, -5.8) * mm, "end": v(-479.98, -6.29) * mm});
            skLineSegment(sketch, "E777", {"start": v(-479.98, -6.29) * mm, "end": v(-483.05, -8.62) * mm});
            skLineSegment(sketch, "E778", {"start": v(-483.05, -8.62) * mm, "end": v(-486.45, -10.73) * mm});
            skLineSegment(sketch, "E779", {"start": v(-486.45, -10.73) * mm, "end": v(-487.14, -11.1) * mm});
            skLineSegment(sketch, "E780", {"start": v(-487.14, -11.1) * mm, "end": v(-486.48, -9.97) * mm});
            skLineSegment(sketch, "E781", {"start": v(-486.48, -9.97) * mm, "end": v(-484.41, -6.65) * mm});
            skLineSegment(sketch, "E782", {"start": v(-484.41, -6.65) * mm, "end": v(-481.44, -2.35) * mm});
            skLineSegment(sketch, "E783", {"start": v(-481.44, -2.35) * mm, "end": v(-478.12, 1.67) * mm});
            skLineSegment(sketch, "E784", {"start": v(-478.12, 1.67) * mm, "end": v(-475.37, 4.44) * mm});
            skLineSegment(sketch, "E785", {"start": v(-475.37, 4.44) * mm, "end": v(-474.38, 5.28) * mm});
            skLineSegment(sketch, "E786", {"start": v(-474.38, 5.28) * mm, "end": v(-474.23, 5.41) * mm});
            skLineSegment(sketch, "E787", {"start": v(-474.23, 5.41) * mm, "end": v(-474.12, 5.58) * mm});
            skLineSegment(sketch, "E788", {"start": v(-474.12, 5.58) * mm, "end": v(-473.13, 7.42) * mm});
            skLineSegment(sketch, "E789", {"start": v(-473.13, 7.42) * mm, "end": v(-469.52, 12.58) * mm});
            skLineSegment(sketch, "E790", {"start": v(-469.52, 12.58) * mm, "end": v(-464.01, 18.8) * mm});
            skLineSegment(sketch, "E791", {"start": v(-464.01, 18.8) * mm, "end": v(-457.93, 24.5) * mm});
            skLineSegment(sketch, "E792", {"start": v(-457.93, 24.5) * mm, "end": v(-453.18, 28.6) * mm});
            skLineSegment(sketch, "E793", {"start": v(-453.18, 28.6) * mm, "end": v(-451.59, 29.95) * mm});
            skLineSegment(sketch, "E794", {"start": v(-451.59, 29.95) * mm, "end": v(-450.85, 30.56) * mm});
            skLineSegment(sketch, "E795", {"start": v(-450.85, 30.56) * mm, "end": v(-446.93, 33.32) * mm});
            skLineSegment(sketch, "E796", {"start": v(-446.93, 33.32) * mm, "end": v(-442.97, 36.04) * mm});
            skLineSegment(sketch, "E797", {"start": v(-442.97, 36.04) * mm, "end": v(-442.21, 36.63) * mm});
            skLineSegment(sketch, "E798", {"start": v(-442.21, 36.63) * mm, "end": v(-441.07, 37.5) * mm});
            skLineSegment(sketch, "E799", {"start": v(-441.07, 37.5) * mm, "end": v(-437.77, 40.28) * mm});
            skLineSegment(sketch, "E800", {"start": v(-437.77, 40.28) * mm, "end": v(-433.4, 44.07) * mm});
            skLineSegment(sketch, "E801", {"start": v(-433.4, 44.07) * mm, "end": v(-428.95, 47.72) * mm});
            skLineSegment(sketch, "E802", {"start": v(-428.95, 47.72) * mm, "end": v(-425.44, 50.23) * mm});
            skLineSegment(sketch, "E803", {"start": v(-425.44, 50.23) * mm, "end": v(-424.21, 50.97) * mm});
            skLineSegment(sketch, "E804", {"start": v(-424.21, 50.97) * mm, "end": v(-423.82, 51.2) * mm});
            skLineSegment(sketch, "E805", {"start": v(-423.82, 51.2) * mm, "end": v(-419.93, 53.54) * mm});
            skLineSegment(sketch, "E806", {"start": v(-419.93, 53.54) * mm, "end": v(-419.54, 53.77) * mm});
            skLineSegment(sketch, "E807", {"start": v(-419.54, 53.77) * mm, "end": v(-419.43, 53.84) * mm});
            skLineSegment(sketch, "E808", {"start": v(-419.43, 53.84) * mm, "end": v(-418.57, 54.13) * mm});
            skLineSegment(sketch, "E809", {"start": v(-418.57, 54.13) * mm, "end": v(-417.66, 54.38) * mm});
            skLineSegment(sketch, "E810", {"start": v(-417.66, 54.38) * mm, "end": v(-417.53, 54.42) * mm});
            skLineSegment(sketch, "E811", {"start": v(-417.53, 54.42) * mm, "end": v(-417.35, 54.48) * mm});
            skLineSegment(sketch, "E812", {"start": v(-417.35, 54.48) * mm, "end": v(-416.49, 54.87) * mm});
            skLineSegment(sketch, "E813", {"start": v(-416.49, 54.87) * mm, "end": v(-415.71, 55.4) * mm});
            skLineSegment(sketch, "E814", {"start": v(-415.71, 55.4) * mm, "end": v(-415.57, 55.54) * mm});
            skLineSegment(sketch, "E815", {"start": v(-415.57, 55.54) * mm, "end": v(-415.39, 55.73) * mm});
            skLineSegment(sketch, "E816", {"start": v(-415.39, 55.73) * mm, "end": v(-414.8, 56.81) * mm});
            skLineSegment(sketch, "E817", {"start": v(-414.8, 56.81) * mm, "end": v(-414.64, 58.04) * mm});
            skLineSegment(sketch, "E818", {"start": v(-414.64, 58.04) * mm, "end": v(-414.66, 58.3) * mm});
            skLineSegment(sketch, "E819", {"start": v(-414.66, 58.3) * mm, "end": v(-414.69, 58.67) * mm});
            skLineSegment(sketch, "E820", {"start": v(-414.69, 58.67) * mm, "end": v(-414.95, 58.95) * mm});
            skLineSegment(sketch, "E821", {"start": v(-414.95, 58.95) * mm, "end": v(-415.34, 59.35) * mm});
            skLineSegment(sketch, "E822", {"start": v(-415.34, 59.35) * mm, "end": v(-416.97, 60.1) * mm});
            skLineSegment(sketch, "E823", {"start": v(-416.97, 60.1) * mm, "end": v(-419.16, 60.06) * mm});
            skLineSegment(sketch, "E824", {"start": v(-419.16, 60.06) * mm, "end": v(-421.42, 59.46) * mm});
            skLineSegment(sketch, "E825", {"start": v(-421.42, 59.46) * mm, "end": v(-423.04, 59) * mm});
            skLineSegment(sketch, "E826", {"start": v(-423.04, 59) * mm, "end": v(-423.6, 58.9) * mm});
            skLineSegment(sketch, "E827", {"start": v(-423.6, 58.9) * mm, "end": v(-424.99, 58.7) * mm});
            skLineSegment(sketch, "E828", {"start": v(-424.99, 58.7) * mm, "end": v(-429.2, 58.3) * mm});
            skLineSegment(sketch, "E829", {"start": v(-429.2, 58.3) * mm, "end": v(-435.17, 58.09) * mm});
            skLineSegment(sketch, "E830", {"start": v(-435.17, 58.09) * mm, "end": v(-441.12, 58.37) * mm});
            skLineSegment(sketch, "E831", {"start": v(-441.12, 58.37) * mm, "end": v(-445.29, 58.93) * mm});
            skLineSegment(sketch, "E832", {"start": v(-445.29, 58.93) * mm, "end": v(-446.65, 59.25) * mm});
            skLineSegment(sketch, "E833", {"start": v(-446.65, 59.25) * mm, "end": v(-447.16, 59.37) * mm});
            skLineSegment(sketch, "E834", {"start": v(-447.16, 59.37) * mm, "end": v(-447.57, 59.02) * mm});
            skLineSegment(sketch, "E835", {"start": v(-447.57, 59.02) * mm, "end": v(-447.9, 58.75) * mm});
            skLineSegment(sketch, "E836", {"start": v(-447.9, 58.75) * mm, "end": v(-449.2, 58.33) * mm});
            skLineSegment(sketch, "E837", {"start": v(-449.2, 58.33) * mm, "end": v(-451.4, 58.2) * mm});
            skLineSegment(sketch, "E838", {"start": v(-451.4, 58.2) * mm, "end": v(-453.58, 58.6) * mm});
            skLineSegment(sketch, "E839", {"start": v(-453.58, 58.6) * mm, "end": v(-454.85, 59.21) * mm});
            skLineSegment(sketch, "E840", {"start": v(-454.85, 59.21) * mm, "end": v(-455.14, 59.53) * mm});
            skLineSegment(sketch, "E841", {"start": v(-455.14, 59.53) * mm, "end": v(-455.06, 60.02) * mm});
            skLineSegment(sketch, "E842", {"start": v(-455.06, 60.02) * mm, "end": v(-454.83, 61.46) * mm});
            skLineSegment(sketch, "E843", {"start": v(-454.83, 61.46) * mm, "end": v(-454.42, 63.49) * mm});
            skLineSegment(sketch, "E844", {"start": v(-454.42, 63.49) * mm, "end": v(-453.85, 65.43) * mm});
            skLineSegment(sketch, "E845", {"start": v(-453.85, 65.43) * mm, "end": v(-453.29, 66.73) * mm});
            skLineSegment(sketch, "E846", {"start": v(-453.29, 66.73) * mm, "end": v(-453.04, 67.12) * mm});
            skLineSegment(sketch, "E847", {"start": v(-453.04, 67.12) * mm, "end": v(-452.8, 67.48) * mm});
            skLineSegment(sketch, "E848", {"start": v(-452.8, 67.48) * mm, "end": v(-451.87, 68.4) * mm});
            skLineSegment(sketch, "E849", {"start": v(-451.87, 68.4) * mm, "end": v(-450.33, 69.45) * mm});
            skLineSegment(sketch, "E850", {"start": v(-450.33, 69.45) * mm, "end": v(-448.7, 70.44) * mm});
            skLineSegment(sketch, "E851", {"start": v(-448.7, 70.44) * mm, "end": v(-447.56, 71.2) * mm});
            skLineSegment(sketch, "E852", {"start": v(-447.56, 71.2) * mm, "end": v(-447.22, 71.5) * mm});
            skLineSegment(sketch, "E853", {"start": v(-447.22, 71.5) * mm, "end": v(-446.42, 72.2) * mm});
            skLineSegment(sketch, "E854", {"start": v(-446.42, 72.2) * mm, "end": v(-442.81, 76.14) * mm});
            skLineSegment(sketch, "E855", {"start": v(-442.81, 76.14) * mm, "end": v(-439.42, 80.29) * mm});
            skLineSegment(sketch, "E856", {"start": v(-439.42, 80.29) * mm, "end": v(-438.73, 81.08) * mm});
            skLineSegment(sketch, "E857", {"start": v(-438.73, 81.08) * mm, "end": v(-438.55, 81.28) * mm});
            skLineSegment(sketch, "E858", {"start": v(-438.55, 81.28) * mm, "end": v(-436.9, 83.3) * mm});
            skLineSegment(sketch, "E859", {"start": v(-436.9, 83.3) * mm, "end": v(-436.74, 83.51) * mm});
            skLineSegment(sketch, "E860", {"start": v(-436.74, 83.51) * mm, "end": v(-436.4, 83.94) * mm});
            skLineSegment(sketch, "E861", {"start": v(-436.4, 83.94) * mm, "end": v(-435.44, 85.22) * mm});
            skLineSegment(sketch, "E862", {"start": v(-435.44, 85.22) * mm, "end": v(-433.88, 87.22) * mm});
            skLineSegment(sketch, "E863", {"start": v(-433.88, 87.22) * mm, "end": v(-432.22, 89.09) * mm});
            skLineSegment(sketch, "E864", {"start": v(-432.22, 89.09) * mm, "end": v(-431.07, 90.14) * mm});
            skLineSegment(sketch, "E865", {"start": v(-431.07, 90.14) * mm, "end": v(-430.63, 90.4) * mm});
            skLineSegment(sketch, "E866", {"start": v(-430.63, 90.4) * mm, "end": v(-430, 90.77) * mm});
            skLineSegment(sketch, "E867", {"start": v(-430, 90.77) * mm, "end": v(-427.89, 91.55) * mm});
            skLineSegment(sketch, "E868", {"start": v(-427.89, 91.55) * mm, "end": v(-424.9, 92.08) * mm});
            skLineSegment(sketch, "E869", {"start": v(-424.9, 92.08) * mm, "end": v(-421.76, 92.05) * mm});
            skLineSegment(sketch, "E870", {"start": v(-421.76, 92.05) * mm, "end": v(-418.57, 91.55) * mm});
            skLineSegment(sketch, "E871", {"start": v(-418.57, 91.55) * mm, "end": v(-415.44, 90.64) * mm});
            skLineSegment(sketch, "E872", {"start": v(-415.44, 90.64) * mm, "end": v(-412.46, 89.4) * mm});
            skLineSegment(sketch, "E873", {"start": v(-412.46, 89.4) * mm, "end": v(-409.73, 87.92) * mm});
            skLineSegment(sketch, "E874", {"start": v(-409.73, 87.92) * mm, "end": v(-407.92, 86.7) * mm});
            skLineSegment(sketch, "E875", {"start": v(-407.92, 86.7) * mm, "end": v(-407.36, 86.25) * mm});
            skLineSegment(sketch, "E876", {"start": v(-407.36, 86.25) * mm, "end": v(-407.05, 86) * mm});
            skLineSegment(sketch, "E877", {"start": v(-407.05, 86) * mm, "end": v(-406.65, 86.02) * mm});
            skLineSegment(sketch, "E878", {"start": v(-406.65, 86.02) * mm, "end": v(-405.94, 86.04) * mm});
            skLineSegment(sketch, "E879", {"start": v(-405.94, 86.04) * mm, "end": v(-403.82, 85.65) * mm});
            skLineSegment(sketch, "E880", {"start": v(-403.82, 85.65) * mm, "end": v(-401.81, 84.44) * mm});
            skLineSegment(sketch, "E881", {"start": v(-401.81, 84.44) * mm, "end": v(-400.18, 82.62) * mm});
            skLineSegment(sketch, "E882", {"start": v(-400.18, 82.62) * mm, "end": v(-398.92, 80.97) * mm});
            skLineSegment(sketch, "E883", {"start": v(-398.92, 80.97) * mm, "end": v(-398.48, 80.43) * mm});
            skLineSegment(sketch, "E884", {"start": v(-398.48, 80.43) * mm, "end": v(-398.2, 80.1) * mm});
            skLineSegment(sketch, "E885", {"start": v(-398.2, 80.1) * mm, "end": v(-397.4, 79.08) * mm});
            skLineSegment(sketch, "E886", {"start": v(-397.4, 79.08) * mm, "end": v(-396.33, 77.53) * mm});
            skLineSegment(sketch, "E887", {"start": v(-396.33, 77.53) * mm, "end": v(-395.55, 75.87) * mm});
            skLineSegment(sketch, "E888", {"start": v(-395.55, 75.87) * mm, "end": v(-395.3, 74.57) * mm});
            skLineSegment(sketch, "E889", {"start": v(-395.3, 74.57) * mm, "end": v(-395.35, 74.15) * mm});
            skLineSegment(sketch, "E890", {"start": v(-395.35, 74.15) * mm, "end": v(-395.38, 73.82) * mm});
            skLineSegment(sketch, "E891", {"start": v(-395.38, 73.82) * mm, "end": v(-395.7, 72.84) * mm});
            skLineSegment(sketch, "E892", {"start": v(-395.7, 72.84) * mm, "end": v(-396.5, 71.33) * mm});
            skLineSegment(sketch, "E893", {"start": v(-396.5, 71.33) * mm, "end": v(-397.6, 69.7) * mm});
            skLineSegment(sketch, "E894", {"start": v(-397.6, 69.7) * mm, "end": v(-398.9, 68.03) * mm});
            skLineSegment(sketch, "E895", {"start": v(-398.9, 68.03) * mm, "end": v(-400.27, 66.39) * mm});
            skLineSegment(sketch, "E896", {"start": v(-400.27, 66.39) * mm, "end": v(-401.63, 64.85) * mm});
            skLineSegment(sketch, "E897", {"start": v(-401.63, 64.85) * mm, "end": v(-402.85, 63.5) * mm});
            skLineSegment(sketch, "E898", {"start": v(-402.85, 63.5) * mm, "end": v(-403.57, 62.7) * mm});
            skLineSegment(sketch, "E899", {"start": v(-403.57, 62.7) * mm, "end": v(-403.8, 62.43) * mm});
            skLineSegment(sketch, "E900", {"start": v(-403.8, 62.43) * mm, "end": v(-404.85, 61.21) * mm});
            skLineSegment(sketch, "E901", {"start": v(-404.85, 61.21) * mm, "end": v(-415.48, 49.23) * mm});
            skLineSegment(sketch, "E902", {"start": v(-415.48, 49.23) * mm, "end": v(-416.52, 48.02) * mm});
            skLineSegment(sketch, "E903", {"start": v(-416.52, 48.02) * mm, "end": v(-418.84, 45.33) * mm});
            skLineSegment(sketch, "E904", {"start": v(-418.84, 45.33) * mm, "end": v(-430.82, 32.13) * mm});
            skLineSegment(sketch, "E905", {"start": v(-430.82, 32.13) * mm, "end": v(-442.67, 18.85) * mm});
            skLineSegment(sketch, "E906", {"start": v(-442.67, 18.85) * mm, "end": v(-444.93, 16.1) * mm});
            skLineSegment(sketch, "E907", {"start": v(-444.93, 16.1) * mm, "end": v(-445.46, 15.8) * mm});
            skLineSegment(sketch, "E908", {"start": v(-445.46, 15.8) * mm, "end": v(-446.88, 14.58) * mm});
            skLineSegment(sketch, "E909", {"start": v(-446.88, 14.58) * mm, "end": v(-448.42, 12.76) * mm});
            skLineSegment(sketch, "E910", {"start": v(-448.42, 12.76) * mm, "end": v(-449.81, 10.82) * mm});
            skLineSegment(sketch, "E911", {"start": v(-449.81, 10.82) * mm, "end": v(-450.94, 9.38) * mm});
            skLineSegment(sketch, "E912", {"start": v(-450.94, 9.38) * mm, "end": v(-451.36, 8.94) * mm});
            skLineSegment(sketch, "E913", {"start": v(-451.36, 8.94) * mm, "end": v(-451.84, 8.46) * mm});
            skLineSegment(sketch, "E914", {"start": v(-451.84, 8.46) * mm, "end": v(-453.4, 7.12) * mm});
            skLineSegment(sketch, "E915", {"start": v(-453.4, 7.12) * mm, "end": v(-455.34, 5.37) * mm});
            skLineSegment(sketch, "E916", {"start": v(-455.34, 5.37) * mm, "end": v(-456.88, 3.32) * mm});
            skLineSegment(sketch, "E917", {"start": v(-456.88, 3.32) * mm, "end": v(-457.62, 1.3) * mm});
            skLineSegment(sketch, "E918", {"start": v(-457.62, 1.3) * mm, "end": v(-457.7, 0.6) * mm});
            skLineSegment(sketch, "E919", {"start": v(-457.7, 0.6) * mm, "end": v(-457.76, -0.06) * mm});
            skLineSegment(sketch, "E920", {"start": v(-457.76, -0.06) * mm, "end": v(-457.22, -0.42) * mm});
            skLineSegment(sketch, "E921", {"start": v(-457.22, -0.42) * mm, "end": v(-456.8, -0.7) * mm});
            skLineSegment(sketch, "E922", {"start": v(-456.8, -0.7) * mm, "end": v(-455.32, -1.19) * mm});
            skLineSegment(sketch, "E923", {"start": v(-455.32, -1.19) * mm, "end": v(-453.59, -1) * mm});
            skLineSegment(sketch, "E924", {"start": v(-453.59, -1) * mm, "end": v(-452, -0.1) * mm});
            skLineSegment(sketch, "E925", {"start": v(-452, -0.1) * mm, "end": v(-450.9, 0.9) * mm});
            skLineSegment(sketch, "E926", {"start": v(-450.9, 0.9) * mm, "end": v(-450.56, 1.27) * mm});
            skLineSegment(sketch, "E927", {"start": v(-450.56, 1.27) * mm, "end": v(-450.4, 1.45) * mm});
            skLineSegment(sketch, "E928", {"start": v(-450.4, 1.45) * mm, "end": v(-449.58, 2.44) * mm});
            skLineSegment(sketch, "E929", {"start": v(-449.58, 2.44) * mm, "end": v(-448.72, 3.4) * mm});
            skLineSegment(sketch, "E930", {"start": v(-448.72, 3.4) * mm, "end": v(-448.54, 3.55) * mm});
            skLineSegment(sketch, "E931", {"start": v(-448.54, 3.55) * mm, "end": v(-447.38, 4.6) * mm});
            skLineSegment(sketch, "E932", {"start": v(-447.38, 4.6) * mm, "end": v(-441.6, 9.74) * mm});
            skLineSegment(sketch, "E933", {"start": v(-441.6, 9.74) * mm, "end": v(-436.06, 15.16) * mm});
            skLineSegment(sketch, "E934", {"start": v(-436.06, 15.16) * mm, "end": v(-435.02, 16.34) * mm});
            skLineSegment(sketch, "E935", {"start": v(-435.02, 16.34) * mm, "end": v(-434.52, 16.92) * mm});
            skLineSegment(sketch, "E936", {"start": v(-434.52, 16.92) * mm, "end": v(-431.7, 19.51) * mm});
            skLineSegment(sketch, "E937", {"start": v(-431.7, 19.51) * mm, "end": v(-428.86, 22.08) * mm});
            skLineSegment(sketch, "E938", {"start": v(-428.86, 22.08) * mm, "end": v(-428.34, 22.64) * mm});
            skLineSegment(sketch, "E939", {"start": v(-428.34, 22.64) * mm, "end": v(-427.13, 23.96) * mm});
            skLineSegment(sketch, "E940", {"start": v(-427.13, 23.96) * mm, "end": v(-423.69, 28.1) * mm});
            skLineSegment(sketch, "E941", {"start": v(-423.69, 28.1) * mm, "end": v(-419.22, 33.75) * mm});
            skLineSegment(sketch, "E942", {"start": v(-419.22, 33.75) * mm, "end": v(-414.63, 39.28) * mm});
            skLineSegment(sketch, "E943", {"start": v(-414.63, 39.28) * mm, "end": v(-410.96, 43.2) * mm});
            skLineSegment(sketch, "E944", {"start": v(-410.96, 43.2) * mm, "end": v(-409.63, 44.4) * mm});
            skLineSegment(sketch, "E945", {"start": v(-409.63, 44.4) * mm, "end": v(-407.85, 46.02) * mm});
            skLineSegment(sketch, "E946", {"start": v(-407.85, 46.02) * mm, "end": v(-399.1, 54.2) * mm});
            skLineSegment(sketch, "E947", {"start": v(-399.1, 54.2) * mm, "end": v(-390.6, 62.66) * mm});
            skLineSegment(sketch, "E948", {"start": v(-390.6, 62.66) * mm, "end": v(-388.95, 64.4) * mm});
            skLineSegment(sketch, "E949", {"start": v(-388.95, 64.4) * mm, "end": v(-387.73, 65.03) * mm});
            skLineSegment(sketch, "E950", {"start": v(-387.73, 65.03) * mm, "end": v(-384.39, 67.56) * mm});
            skLineSegment(sketch, "E951", {"start": v(-384.39, 67.56) * mm, "end": v(-380.48, 71.35) * mm});
            skLineSegment(sketch, "E952", {"start": v(-380.48, 71.35) * mm, "end": v(-376.65, 75.18) * mm});
            skLineSegment(sketch, "E953", {"start": v(-376.65, 75.18) * mm, "end": v(-373.48, 77.73) * mm});
            skLineSegment(sketch, "E954", {"start": v(-373.48, 77.73) * mm, "end": v(-372.31, 78.4) * mm});
            skLineSegment(sketch, "E955", {"start": v(-372.31, 78.4) * mm, "end": v(-371.9, 78.64) * mm});
            skLineSegment(sketch, "E956", {"start": v(-371.9, 78.64) * mm, "end": v(-371.8, 79.1) * mm});
            skLineSegment(sketch, "E957", {"start": v(-371.8, 79.1) * mm, "end": v(-371.7, 79.54) * mm});
            skLineSegment(sketch, "E958", {"start": v(-371.7, 79.54) * mm, "end": v(-371.24, 80.79) * mm});
            skLineSegment(sketch, "E959", {"start": v(-371.24, 80.79) * mm, "end": v(-370.48, 81.74) * mm});
            skLineSegment(sketch, "E960", {"start": v(-370.48, 81.74) * mm, "end": v(-369.59, 82.06) * mm});
            skLineSegment(sketch, "E961", {"start": v(-369.59, 82.06) * mm, "end": v(-368.66, 81.84) * mm});
            skLineSegment(sketch, "E962", {"start": v(-368.66, 81.84) * mm, "end": v(-367.76, 81.18) * mm});
            skLineSegment(sketch, "E963", {"start": v(-367.76, 81.18) * mm, "end": v(-367, 80.18) * mm});
            skLineSegment(sketch, "E964", {"start": v(-367, 80.18) * mm, "end": v(-366.44, 78.92) * mm});
            skLineSegment(sketch, "E965", {"start": v(-366.44, 78.92) * mm, "end": v(-366.2, 77.86) * mm});
            skLineSegment(sketch, "E966", {"start": v(-366.2, 77.86) * mm, "end": v(-366.18, 77.5) * mm});
            skLineSegment(sketch, "E967", {"start": v(-366.18, 77.5) * mm, "end": v(-366.16, 77.2) * mm});
            skLineSegment(sketch, "E968", {"start": v(-366.16, 77.2) * mm, "end": v(-366.4, 76.14) * mm});
            skLineSegment(sketch, "E969", {"start": v(-366.4, 76.14) * mm, "end": v(-367, 74.26) * mm});
            skLineSegment(sketch, "E970", {"start": v(-367, 74.26) * mm, "end": v(-367.74, 72.4) * mm});
            skLineSegment(sketch, "E971", {"start": v(-367.74, 72.4) * mm, "end": v(-368.21, 71.38) * mm});
            skLineSegment(sketch, "E972", {"start": v(-368.21, 71.38) * mm, "end": v(-368.39, 71.1) * mm});
            skLineSegment(sketch, "E973", {"start": v(-368.39, 71.1) * mm, "end": v(-368.9, 70.27) * mm});
            skLineSegment(sketch, "E974", {"start": v(-368.9, 70.27) * mm, "end": v(-370.73, 67.94) * mm});
            skLineSegment(sketch, "E975", {"start": v(-370.73, 67.94) * mm, "end": v(-373.66, 64.84) * mm});
            skLineSegment(sketch, "E976", {"start": v(-373.66, 64.84) * mm, "end": v(-376.83, 61.95) * mm});
            skLineSegment(sketch, "E977", {"start": v(-376.83, 61.95) * mm, "end": v(-379.1, 60.02) * mm});
            skLineSegment(sketch, "E978", {"start": v(-379.1, 60.02) * mm, "end": v(-379.87, 59.4) * mm});
            skLineSegment(sketch, "E979", {"start": v(-379.87, 59.4) * mm, "end": v(-380.57, 58.84) * mm});
            skLineSegment(sketch, "E980", {"start": v(-380.57, 58.84) * mm, "end": v(-384.32, 56.25) * mm});
            skLineSegment(sketch, "E981", {"start": v(-384.32, 56.25) * mm, "end": v(-388.26, 53.94) * mm});
            skLineSegment(sketch, "E982", {"start": v(-388.26, 53.94) * mm, "end": v(-389.05, 53.52) * mm});
            skLineSegment(sketch, "E983", {"start": v(-389.05, 53.52) * mm, "end": v(-389.35, 53.37) * mm});
            skLineSegment(sketch, "E984", {"start": v(-389.35, 53.37) * mm, "end": v(-390.32, 53.08) * mm});
            skLineSegment(sketch, "E985", {"start": v(-390.32, 53.08) * mm, "end": v(-391.78, 52.81) * mm});
            skLineSegment(sketch, "E986", {"start": v(-391.78, 52.81) * mm, "end": v(-393.29, 52.55) * mm});
            skLineSegment(sketch, "E987", {"start": v(-393.29, 52.55) * mm, "end": v(-394.35, 52.3) * mm});
            skLineSegment(sketch, "E988", {"start": v(-394.35, 52.3) * mm, "end": v(-394.69, 52.16) * mm});
            skLineSegment(sketch, "E989", {"start": v(-394.69, 52.16) * mm, "end": v(-395.4, 51.86) * mm});
            skLineSegment(sketch, "E990", {"start": v(-395.4, 51.86) * mm, "end": v(-397.37, 50.5) * mm});
            skLineSegment(sketch, "E991", {"start": v(-397.37, 50.5) * mm, "end": v(-399.8, 48.14) * mm});
            skLineSegment(sketch, "E992", {"start": v(-399.8, 48.14) * mm, "end": v(-402.02, 45.52) * mm});
            skLineSegment(sketch, "E993", {"start": v(-402.02, 45.52) * mm, "end": v(-403.56, 43.68) * mm});
            skLineSegment(sketch, "E994", {"start": v(-403.56, 43.68) * mm, "end": v(-404.11, 43.1) * mm});
            skLineSegment(sketch, "E995", {"start": v(-404.11, 43.1) * mm, "end": v(-404.67, 42.52) * mm});
            skLineSegment(sketch, "E996", {"start": v(-404.67, 42.52) * mm, "end": v(-406.39, 40.82) * mm});
            skLineSegment(sketch, "E997", {"start": v(-406.39, 40.82) * mm, "end": v(-408.78, 38.45) * mm});
            skLineSegment(sketch, "E998", {"start": v(-408.78, 38.45) * mm, "end": v(-411.05, 35.98) * mm});
            skLineSegment(sketch, "E999", {"start": v(-411.05, 35.98) * mm, "end": v(-412.52, 34.1) * mm});
            skLineSegment(sketch, "E1000", {"start": v(-412.52, 34.1) * mm, "end": v(-412.94, 33.43) * mm});
            skLineSegment(sketch, "E1001", {"start": v(-412.94, 33.43) * mm, "end": v(-413.72, 32.17) * mm});
            skLineSegment(sketch, "E1002", {"start": v(-413.72, 32.17) * mm, "end": v(-412.28, 31.82) * mm});
            skLineSegment(sketch, "E1003", {"start": v(-412.28, 31.82) * mm, "end": v(-412.07, 31.77) * mm});
            skLineSegment(sketch, "E1004", {"start": v(-412.07, 31.77) * mm, "end": v(-411.4, 31.72) * mm});
            skLineSegment(sketch, "E1005", {"start": v(-411.4, 31.72) * mm, "end": v(-410.65, 31.83) * mm});
            skLineSegment(sketch, "E1006", {"start": v(-410.65, 31.83) * mm, "end": v(-409.99, 32.1) * mm});
            skLineSegment(sketch, "E1007", {"start": v(-409.99, 32.1) * mm, "end": v(-409.4, 32.51) * mm});
            skLineSegment(sketch, "E1008", {"start": v(-409.4, 32.51) * mm, "end": v(-408.84, 33) * mm});
            skLineSegment(sketch, "E1009", {"start": v(-408.84, 33) * mm, "end": v(-408.3, 33.5) * mm});
            skLineSegment(sketch, "E1010", {"start": v(-408.3, 33.5) * mm, "end": v(-407.75, 33.99) * mm});
            skLineSegment(sketch, "E1011", {"start": v(-407.75, 33.99) * mm, "end": v(-407.31, 34.32) * mm});
            skLineSegment(sketch, "E1012", {"start": v(-407.31, 34.32) * mm, "end": v(-407.16, 34.42) * mm});
            skLineSegment(sketch, "E1013", {"start": v(-407.16, 34.42) * mm, "end": v(-406.87, 34.58) * mm});
            skLineSegment(sketch, "E1014", {"start": v(-406.87, 34.58) * mm, "end": v(-405.93, 34.95) * mm});
            skLineSegment(sketch, "E1015", {"start": v(-405.93, 34.95) * mm, "end": v(-404.7, 35.36) * mm});
            skLineSegment(sketch, "E1016", {"start": v(-404.7, 35.36) * mm, "end": v(-403.48, 35.86) * mm});
            skLineSegment(sketch, "E1017", {"start": v(-403.48, 35.86) * mm, "end": v(-402.55, 36.43) * mm});
            skLineSegment(sketch, "E1018", {"start": v(-402.55, 36.43) * mm, "end": v(-402.28, 36.66) * mm});
            skLineSegment(sketch, "E1019", {"start": v(-402.28, 36.66) * mm, "end": v(-401.93, 36.96) * mm});
            skLineSegment(sketch, "E1020", {"start": v(-401.93, 36.96) * mm, "end": v(-401, 38) * mm});
            skLineSegment(sketch, "E1021", {"start": v(-401, 38) * mm, "end": v(-400, 39.48) * mm});
            skLineSegment(sketch, "E1022", {"start": v(-400, 39.48) * mm, "end": v(-399.04, 40.95) * mm});
            skLineSegment(sketch, "E1023", {"start": v(-399.04, 40.95) * mm, "end": v(-398.22, 42) * mm});
            skLineSegment(sketch, "E1024", {"start": v(-398.22, 42) * mm, "end": v(-397.91, 42.32) * mm});
            skLineSegment(sketch, "E1025", {"start": v(-397.91, 42.32) * mm, "end": v(-397.4, 42.8) * mm});
            skLineSegment(sketch, "E1026", {"start": v(-397.4, 42.8) * mm, "end": v(-394.66, 45.07) * mm});
            skLineSegment(sketch, "E1027", {"start": v(-394.66, 45.07) * mm, "end": v(-391.7, 47.07) * mm});
            skLineSegment(sketch, "E1028", {"start": v(-391.7, 47.07) * mm, "end": v(-391.1, 47.4) * mm});
            skLineSegment(sketch, "E1029", {"start": v(-391.1, 47.4) * mm, "end": v(-390.78, 47.58) * mm});
            skLineSegment(sketch, "E1030", {"start": v(-390.78, 47.58) * mm, "end": v(-389.76, 47.94) * mm});
            skLineSegment(sketch, "E1031", {"start": v(-389.76, 47.94) * mm, "end": v(-388.33, 48.29) * mm});
            skLineSegment(sketch, "E1032", {"start": v(-388.33, 48.29) * mm, "end": v(-386.87, 48.63) * mm});
            skLineSegment(sketch, "E1033", {"start": v(-386.87, 48.63) * mm, "end": v(-385.8, 48.98) * mm});
            skLineSegment(sketch, "E1034", {"start": v(-385.8, 48.98) * mm, "end": v(-385.46, 49.13) * mm});
            skLineSegment(sketch, "E1035", {"start": v(-385.46, 49.13) * mm, "end": v(-384.82, 49.43) * mm});
            skLineSegment(sketch, "E1036", {"start": v(-384.82, 49.43) * mm, "end": v(-381.9, 51.5) * mm});
            skLineSegment(sketch, "E1037", {"start": v(-381.9, 51.5) * mm, "end": v(-379.14, 53.77) * mm});
            skLineSegment(sketch, "E1038", {"start": v(-379.14, 53.77) * mm, "end": v(-378.57, 54.18) * mm});
            skLineSegment(sketch, "E1039", {"start": v(-378.57, 54.18) * mm, "end": v(-378, 54.58) * mm});
            skLineSegment(sketch, "E1040", {"start": v(-378, 54.58) * mm, "end": v(-375.2, 56.54) * mm});
            skLineSegment(sketch, "E1041", {"start": v(-375.2, 56.54) * mm, "end": v(-372.67, 58.8) * mm});
            skLineSegment(sketch, "E1042", {"start": v(-372.67, 58.8) * mm, "end": v(-372.23, 59.36) * mm});
            skLineSegment(sketch, "E1043", {"start": v(-372.23, 59.36) * mm, "end": v(-371.35, 59.56) * mm});
            skLineSegment(sketch, "E1044", {"start": v(-371.35, 59.56) * mm, "end": v(-368.79, 60.57) * mm});
            skLineSegment(sketch, "E1045", {"start": v(-368.79, 60.57) * mm, "end": v(-365.72, 62.22) * mm});
            skLineSegment(sketch, "E1046", {"start": v(-365.72, 62.22) * mm, "end": v(-362.72, 63.92) * mm});
            skLineSegment(sketch, "E1047", {"start": v(-362.72, 63.92) * mm, "end": v(-360.32, 65.02) * mm});
            skLineSegment(sketch, "E1048", {"start": v(-360.32, 65.02) * mm, "end": v(-359.48, 65.27) * mm});
            skLineSegment(sketch, "E1049", {"start": v(-359.48, 65.27) * mm, "end": v(-359.13, 65.38) * mm});
            skLineSegment(sketch, "E1050", {"start": v(-359.13, 65.38) * mm, "end": v(-358.92, 65.65) * mm});
            skLineSegment(sketch, "E1051", {"start": v(-358.92, 65.65) * mm, "end": v(-358.39, 66.39) * mm});
            skLineSegment(sketch, "E1052", {"start": v(-358.39, 66.39) * mm, "end": v(-355.12, 69.62) * mm});
            skLineSegment(sketch, "E1053", {"start": v(-355.12, 69.62) * mm, "end": v(-351.62, 72.65) * mm});
            skLineSegment(sketch, "E1054", {"start": v(-351.62, 72.65) * mm, "end": v(-350.97, 73.28) * mm});
            skLineSegment(sketch, "E1055", {"start": v(-350.97, 73.28) * mm, "end": v(-350.77, 73.46) * mm});
            skLineSegment(sketch, "E1056", {"start": v(-350.77, 73.46) * mm, "end": v(-350.23, 74.07) * mm});
            skLineSegment(sketch, "E1057", {"start": v(-350.23, 74.07) * mm, "end": v(-349.34, 75.1) * mm});
            skLineSegment(sketch, "E1058", {"start": v(-349.34, 75.1) * mm, "end": v(-348.34, 76.28) * mm});
            skLineSegment(sketch, "E1059", {"start": v(-348.34, 76.28) * mm, "end": v(-347.26, 77.47) * mm});
            skLineSegment(sketch, "E1060", {"start": v(-347.26, 77.47) * mm, "end": v(-346.14, 78.55) * mm});
            skLineSegment(sketch, "E1061", {"start": v(-346.14, 78.55) * mm, "end": v(-345, 79.42) * mm});
            skLineSegment(sketch, "E1062", {"start": v(-345, 79.42) * mm, "end": v(-343.88, 79.96) * mm});
            skLineSegment(sketch, "E1063", {"start": v(-343.88, 79.96) * mm, "end": v(-343.08, 80.09) * mm});
            skLineSegment(sketch, "E1064", {"start": v(-343.08, 80.09) * mm, "end": v(-342.82, 80.04) * mm});
            skLineSegment(sketch, "E1065", {"start": v(-342.82, 80.04) * mm, "end": v(-342.7, 80.02) * mm});
            skLineSegment(sketch, "E1066", {"start": v(-342.7, 80.02) * mm, "end": v(-342.38, 79.82) * mm});
            skLineSegment(sketch, "E1067", {"start": v(-342.38, 79.82) * mm, "end": v(-341.99, 79.4) * mm});
            skLineSegment(sketch, "E1068", {"start": v(-341.99, 79.4) * mm, "end": v(-341.66, 78.9) * mm});
            skLineSegment(sketch, "E1069", {"start": v(-341.66, 78.9) * mm, "end": v(-341.49, 78.57) * mm});
            skLineSegment(sketch, "E1070", {"start": v(-341.49, 78.57) * mm, "end": v(-341.44, 78.46) * mm});
            skLineSegment(sketch, "E1071", {"start": v(-341.44, 78.46) * mm, "end": v(-341.29, 78.1) * mm});
            skLineSegment(sketch, "E1072", {"start": v(-341.29, 78.1) * mm, "end": v(-340.93, 76.2) * mm});
            skLineSegment(sketch, "E1073", {"start": v(-340.93, 76.2) * mm, "end": v(-341, 74.24) * mm});
            skLineSegment(sketch, "E1074", {"start": v(-341, 74.24) * mm, "end": v(-341.05, 73.87) * mm});
            skLineSegment(sketch, "E1075", {"start": v(-341.05, 73.87) * mm, "end": v(-341.13, 73.37) * mm});
            skLineSegment(sketch, "E1076", {"start": v(-341.13, 73.37) * mm, "end": v(-341.58, 71.9) * mm});
            skLineSegment(sketch, "E1077", {"start": v(-341.58, 71.9) * mm, "end": v(-342.5, 69.73) * mm});
            skLineSegment(sketch, "E1078", {"start": v(-342.5, 69.73) * mm, "end": v(-343.58, 67.62) * mm});
            skLineSegment(sketch, "E1079", {"start": v(-343.58, 67.62) * mm, "end": v(-344.34, 66.26) * mm});
            skLineSegment(sketch, "E1080", {"start": v(-344.34, 66.26) * mm, "end": v(-344.6, 65.81) * mm});
            skLineSegment(sketch, "E1081", {"start": v(-344.6, 65.81) * mm, "end": v(-344.87, 65.33) * mm});
            skLineSegment(sketch, "E1082", {"start": v(-344.87, 65.33) * mm, "end": v(-345.7, 63.88) * mm});
            skLineSegment(sketch, "E1083", {"start": v(-345.7, 63.88) * mm, "end": v(-347.1, 61.45) * mm});
            skLineSegment(sketch, "E1084", {"start": v(-347.1, 61.45) * mm, "end": v(-348.7, 58.7) * mm});
            skLineSegment(sketch, "E1085", {"start": v(-348.7, 58.7) * mm, "end": v(-350.42, 55.84) * mm});
            skLineSegment(sketch, "E1086", {"start": v(-350.42, 55.84) * mm, "end": v(-352.2, 53.05) * mm});
            skLineSegment(sketch, "E1087", {"start": v(-352.2, 53.05) * mm, "end": v(-353.95, 50.54) * mm});
            skLineSegment(sketch, "E1088", {"start": v(-353.95, 50.54) * mm, "end": v(-355.59, 48.49) * mm});
            skLineSegment(sketch, "E1089", {"start": v(-355.59, 48.49) * mm, "end": v(-356.66, 47.4) * mm});
            skLineSegment(sketch, "E1090", {"start": v(-356.66, 47.4) * mm, "end": v(-357.06, 47.1) * mm});
            skLineSegment(sketch, "E1091", {"start": v(-357.06, 47.1) * mm, "end": v(-357.3, 46.91) * mm});
            skLineSegment(sketch, "E1092", {"start": v(-357.3, 46.91) * mm, "end": v(-358.22, 46.46) * mm});
            skLineSegment(sketch, "E1093", {"start": v(-358.22, 46.46) * mm, "end": v(-359.93, 45.8) * mm});
            skLineSegment(sketch, "E1094", {"start": v(-359.93, 45.8) * mm, "end": v(-361.7, 45.3) * mm});
            skLineSegment(sketch, "E1095", {"start": v(-361.7, 45.3) * mm, "end": v(-362.68, 45.13) * mm});
            skLineSegment(sketch, "E1096", {"start": v(-362.68, 45.13) * mm, "end": v(-362.98, 45.17) * mm});
            skLineSegment(sketch, "E1097", {"start": v(-362.98, 45.17) * mm, "end": v(-363.26, 45.21) * mm});
            skLineSegment(sketch, "E1098", {"start": v(-363.26, 45.21) * mm, "end": v(-364.05, 45.82) * mm});
            skLineSegment(sketch, "E1099", {"start": v(-364.05, 45.82) * mm, "end": v(-365.11, 46.98) * mm});
            skLineSegment(sketch, "E1100", {"start": v(-365.11, 46.98) * mm, "end": v(-366.66, 48.04) * mm});
            skLineSegment(sketch, "E1101", {"start": v(-366.66, 48.04) * mm, "end": v(-368.57, 48.43) * mm});
            skLineSegment(sketch, "E1102", {"start": v(-368.57, 48.43) * mm, "end": v(-369.2, 48.39) * mm});
            skLineSegment(sketch, "E1103", {"start": v(-369.2, 48.39) * mm, "end": v(-369.68, 48.36) * mm});
            skLineSegment(sketch, "E1104", {"start": v(-369.68, 48.36) * mm, "end": v(-369.96, 47.99) * mm});
            skLineSegment(sketch, "E1105", {"start": v(-369.96, 47.99) * mm, "end": v(-370.4, 47.44) * mm});
            skLineSegment(sketch, "E1106", {"start": v(-370.4, 47.44) * mm, "end": v(-371.08, 45.31) * mm});
            skLineSegment(sketch, "E1107", {"start": v(-371.08, 45.31) * mm, "end": v(-370.7, 42.66) * mm});
            skLineSegment(sketch, "E1108", {"start": v(-370.7, 42.66) * mm, "end": v(-369.58, 40.04) * mm});
            skLineSegment(sketch, "E1109", {"start": v(-369.58, 40.04) * mm, "end": v(-368.7, 38.14) * mm});
            skLineSegment(sketch, "E1110", {"start": v(-368.7, 38.14) * mm, "end": v(-368.5, 37.47) * mm});
            skLineSegment(sketch, "E1111", {"start": v(-368.5, 37.47) * mm, "end": v(-368.21, 36.58) * mm});
            skLineSegment(sketch, "E1112", {"start": v(-368.21, 36.58) * mm, "end": v(-367.35, 31.94) * mm});
            skLineSegment(sketch, "E1113", {"start": v(-367.35, 31.94) * mm, "end": v(-366.7, 27.25) * mm});
            skLineSegment(sketch, "E1114", {"start": v(-366.7, 27.25) * mm, "end": v(-366.51, 26.33) * mm});
            skLineSegment(sketch, "E1115", {"start": v(-366.51, 26.33) * mm, "end": v(-366.37, 25.62) * mm});
            skLineSegment(sketch, "E1116", {"start": v(-366.37, 25.62) * mm, "end": v(-365.66, 25.5) * mm});
            skLineSegment(sketch, "E1117", {"start": v(-365.66, 25.5) * mm, "end": v(-365.29, 25.42) * mm});
            skLineSegment(sketch, "E1118", {"start": v(-365.29, 25.42) * mm, "end": v(-363.52, 25.14) * mm});
            skLineSegment(sketch, "E1119", {"start": v(-363.52, 25.14) * mm, "end": v(-361.73, 25.07) * mm});
            skLineSegment(sketch, "E1120", {"start": v(-361.73, 25.07) * mm, "end": v(-361.33, 25.1) * mm});
            skLineSegment(sketch, "E1121", {"start": v(-361.33, 25.1) * mm, "end": v(-360.75, 25.14) * mm});
            skLineSegment(sketch, "E1122", {"start": v(-360.75, 25.14) * mm, "end": v(-360.48, 25.66) * mm});
            skLineSegment(sketch, "E1123", {"start": v(-360.48, 25.66) * mm, "end": v(-360.25, 26.08) * mm});
            skLineSegment(sketch, "E1124", {"start": v(-360.25, 26.08) * mm, "end": v(-359.65, 27.4) * mm});
            skLineSegment(sketch, "E1125", {"start": v(-359.65, 27.4) * mm, "end": v(-358.85, 29.33) * mm});
            skLineSegment(sketch, "E1126", {"start": v(-358.85, 29.33) * mm, "end": v(-358.05, 31.37) * mm});
            skLineSegment(sketch, "E1127", {"start": v(-358.05, 31.37) * mm, "end": v(-357.2, 33.4) * mm});
            skLineSegment(sketch, "E1128", {"start": v(-357.2, 33.4) * mm, "end": v(-356.24, 35.35) * mm});
            skLineSegment(sketch, "E1129", {"start": v(-356.24, 35.35) * mm, "end": v(-355.12, 37.1) * mm});
            skLineSegment(sketch, "E1130", {"start": v(-355.12, 37.1) * mm, "end": v(-353.8, 38.57) * mm});
            skLineSegment(sketch, "E1131", {"start": v(-353.8, 38.57) * mm, "end": v(-352.65, 39.45) * mm});
            skLineSegment(sketch, "E1132", {"start": v(-352.65, 39.45) * mm, "end": v(-352.23, 39.66) * mm});
            skLineSegment(sketch, "E1133", {"start": v(-352.23, 39.66) * mm, "end": v(-352, 39.77) * mm});
            skLineSegment(sketch, "E1134", {"start": v(-352, 39.77) * mm, "end": v(-351.85, 39.97) * mm});
            skLineSegment(sketch, "E1135", {"start": v(-351.85, 39.97) * mm, "end": v(-350.31, 42.03) * mm});
            skLineSegment(sketch, "E1136", {"start": v(-350.31, 42.03) * mm, "end": v(-342.36, 52.14) * mm});
            skLineSegment(sketch, "E1137", {"start": v(-342.36, 52.14) * mm, "end": v(-334.35, 62.21) * mm});
            skLineSegment(sketch, "E1138", {"start": v(-334.35, 62.21) * mm, "end": v(-332.79, 64.25) * mm});
            skLineSegment(sketch, "E1139", {"start": v(-332.79, 64.25) * mm, "end": v(-332.42, 64.72) * mm});
            skLineSegment(sketch, "E1140", {"start": v(-332.42, 64.72) * mm, "end": v(-331.36, 66.16) * mm});
            skLineSegment(sketch, "E1141", {"start": v(-331.36, 66.16) * mm, "end": v(-329.7, 68.32) * mm});
            skLineSegment(sketch, "E1142", {"start": v(-329.7, 68.32) * mm, "end": v(-327.93, 70.3) * mm});
            skLineSegment(sketch, "E1143", {"start": v(-327.93, 70.3) * mm, "end": v(-326.6, 71.44) * mm});
            skLineSegment(sketch, "E1144", {"start": v(-326.6, 71.44) * mm, "end": v(-326.1, 71.7) * mm});
            skLineSegment(sketch, "E1145", {"start": v(-326.1, 71.7) * mm, "end": v(-325.89, 71.8) * mm});
            skLineSegment(sketch, "E1146", {"start": v(-325.89, 71.8) * mm, "end": v(-325.23, 72.06) * mm});
            skLineSegment(sketch, "E1147", {"start": v(-325.23, 72.06) * mm, "end": v(-324.05, 72.42) * mm});
            skLineSegment(sketch, "E1148", {"start": v(-324.05, 72.42) * mm, "end": v(-322.7, 72.72) * mm});
            skLineSegment(sketch, "E1149", {"start": v(-322.7, 72.72) * mm, "end": v(-321.24, 72.92) * mm});
            skLineSegment(sketch, "E1150", {"start": v(-321.24, 72.92) * mm, "end": v(-319.82, 72.97) * mm});
            skLineSegment(sketch, "E1151", {"start": v(-319.82, 72.97) * mm, "end": v(-318.52, 72.83) * mm});
            skLineSegment(sketch, "E1152", {"start": v(-318.52, 72.83) * mm, "end": v(-317.47, 72.45) * mm});
            skLineSegment(sketch, "E1153", {"start": v(-317.47, 72.45) * mm, "end": v(-316.89, 71.97) * mm});
            skLineSegment(sketch, "E1154", {"start": v(-316.89, 71.97) * mm, "end": v(-316.77, 71.77) * mm});
            skLineSegment(sketch, "E1155", {"start": v(-316.77, 71.77) * mm, "end": v(-316.72, 71.68) * mm});
            skLineSegment(sketch, "E1156", {"start": v(-316.72, 71.68) * mm, "end": v(-316.47, 71.14) * mm});
            skLineSegment(sketch, "E1157", {"start": v(-316.47, 71.14) * mm, "end": v(-316.36, 70.56) * mm});
            skLineSegment(sketch, "E1158", {"start": v(-316.36, 70.56) * mm, "end": v(-316.39, 70.45) * mm});
            skLineSegment(sketch, "E1159", {"start": v(-316.39, 70.45) * mm, "end": v(-316.4, 70.36) * mm});
            skLineSegment(sketch, "E1160", {"start": v(-316.4, 70.36) * mm, "end": v(-316.6, 69.9) * mm});
            skLineSegment(sketch, "E1161", {"start": v(-316.6, 69.9) * mm, "end": v(-316.82, 69.44) * mm});
            skLineSegment(sketch, "E1162", {"start": v(-316.82, 69.44) * mm, "end": v(-316.85, 69.37) * mm});
            skLineSegment(sketch, "E1163", {"start": v(-316.85, 69.37) * mm, "end": v(-316.94, 69.19) * mm});
            skLineSegment(sketch, "E1164", {"start": v(-316.94, 69.19) * mm, "end": v(-317.53, 67.4) * mm});
            skLineSegment(sketch, "E1165", {"start": v(-317.53, 67.4) * mm, "end": v(-317.56, 67.21) * mm});
            skLineSegment(sketch, "E1166", {"start": v(-317.56, 67.21) * mm, "end": v(-317.7, 66.46) * mm});
            skLineSegment(sketch, "E1167", {"start": v(-317.7, 66.46) * mm, "end": v(-318.15, 64.22) * mm});
            skLineSegment(sketch, "E1168", {"start": v(-318.15, 64.22) * mm, "end": v(-318.9, 60.87) * mm});
            skLineSegment(sketch, "E1169", {"start": v(-318.9, 60.87) * mm, "end": v(-319.86, 57.62) * mm});
            skLineSegment(sketch, "E1170", {"start": v(-319.86, 57.62) * mm, "end": v(-320.72, 55.55) * mm});
            skLineSegment(sketch, "E1171", {"start": v(-320.72, 55.55) * mm, "end": v(-321.1, 54.92) * mm});
            skLineSegment(sketch, "E1172", {"start": v(-321.1, 54.92) * mm, "end": v(-321.8, 53.82) * mm});
            skLineSegment(sketch, "E1173", {"start": v(-321.8, 53.82) * mm, "end": v(-324.26, 50.76) * mm});
            skLineSegment(sketch, "E1174", {"start": v(-324.26, 50.76) * mm, "end": v(-327.91, 46.97) * mm});
            skLineSegment(sketch, "E1175", {"start": v(-327.91, 46.97) * mm, "end": v(-331.74, 43.32) * mm});
            skLineSegment(sketch, "E1176", {"start": v(-331.74, 43.32) * mm, "end": v(-334.52, 40.55) * mm});
            skLineSegment(sketch, "E1177", {"start": v(-334.52, 40.55) * mm, "end": v(-335.4, 39.57) * mm});
            skLineSegment(sketch, "E1178", {"start": v(-335.4, 39.57) * mm, "end": v(-335.82, 39.1) * mm});
            skLineSegment(sketch, "E1179", {"start": v(-335.82, 39.1) * mm, "end": v(-337.7, 36.56) * mm});
            skLineSegment(sketch, "E1180", {"start": v(-337.7, 36.56) * mm, "end": v(-339.62, 34.06) * mm});
            skLineSegment(sketch, "E1181", {"start": v(-339.62, 34.06) * mm, "end": v(-340.06, 33.6) * mm});
            skLineSegment(sketch, "E1182", {"start": v(-340.06, 33.6) * mm, "end": v(-341.39, 32.25) * mm});
            skLineSegment(sketch, "E1183", {"start": v(-341.39, 32.25) * mm, "end": v(-347.8, 25.27) * mm});
            skLineSegment(sketch, "E1184", {"start": v(-347.8, 25.27) * mm, "end": v(-354, 18.09) * mm});
            skLineSegment(sketch, "E1185", {"start": v(-354, 18.09) * mm, "end": v(-355.22, 16.63) * mm});
            skLineSegment(sketch, "E1186", {"start": v(-355.22, 16.63) * mm, "end": v(-357.65, 13.74) * mm});
            skLineSegment(sketch, "E1187", {"start": v(-357.65, 13.74) * mm, "end": v(-364.94, 5.08) * mm});
            skLineSegment(sketch, "E1188", {"start": v(-364.94, 5.08) * mm, "end": v(-374.86, -6.37) * mm});
            skLineSegment(sketch, "E1189", {"start": v(-374.86, -6.37) * mm, "end": v(-385.16, -17.45) * mm});
            skLineSegment(sketch, "E1190", {"start": v(-385.16, -17.45) * mm, "end": v(-393.22, -25.42) * mm});
            skLineSegment(sketch, "E1191", {"start": v(-393.22, -25.42) * mm, "end": v(-396.02, -27.94) * mm});
            skLineSegment(sketch, "E1192", {"start": v(-396.02, -27.94) * mm, "end": v(-397.06, -28.9) * mm});
            skLineSegment(sketch, "E1193", {"start": v(-397.06, -28.9) * mm, "end": v(-400.04, -31.9) * mm});
            skLineSegment(sketch, "E1194", {"start": v(-400.04, -31.9) * mm, "end": v(-403.9, -36.02) * mm});
            skLineSegment(sketch, "E1195", {"start": v(-403.9, -36.02) * mm, "end": v(-407.73, -40.16) * mm});
            skLineSegment(sketch, "E1196", {"start": v(-407.73, -40.16) * mm, "end": v(-410.7, -43.17) * mm});
            skLineSegment(sketch, "E1197", {"start": v(-410.7, -43.17) * mm, "end": v(-411.74, -44.12) * mm});
            skLineSegment(sketch, "E1198", {"start": v(-411.74, -44.12) * mm, "end": v(-412.23, -44.56) * mm});
            skLineSegment(sketch, "E1199", {"start": v(-412.23, -44.56) * mm, "end": v(-414.85, -46.57) * mm});
            skLineSegment(sketch, "E1200", {"start": v(-414.85, -46.57) * mm, "end": v(-417.41, -48.65) * mm});
            skLineSegment(sketch, "E1201", {"start": v(-417.41, -48.65) * mm, "end": v(-417.87, -49.14) * mm});
            skLineSegment(sketch, "E1202", {"start": v(-417.87, -49.14) * mm, "end": v(-418.06, -49.34) * mm});
            skLineSegment(sketch, "E1203", {"start": v(-418.06, -49.34) * mm, "end": v(-418.55, -50.08) * mm});
            skLineSegment(sketch, "E1204", {"start": v(-418.55, -50.08) * mm, "end": v(-419.07, -51.11) * mm});
            skLineSegment(sketch, "E1205", {"start": v(-419.07, -51.11) * mm, "end": v(-419.58, -52.12) * mm});
            skLineSegment(sketch, "E1206", {"start": v(-419.58, -52.12) * mm, "end": v(-420.03, -52.8) * mm});
            skLineSegment(sketch, "E1207", {"start": v(-420.03, -52.8) * mm, "end": v(-420.21, -53) * mm});
            skLineSegment(sketch, "E1208", {"start": v(-420.21, -53) * mm, "end": v(-420.93, -53.8) * mm});
            skLineSegment(sketch, "E1209", {"start": v(-420.93, -53.8) * mm, "end": v(-423.4, -55.9) * mm});
            skLineSegment(sketch, "E1210", {"start": v(-423.4, -55.9) * mm, "end": v(-426.97, -58.56) * mm});
            skLineSegment(sketch, "E1211", {"start": v(-426.97, -58.56) * mm, "end": v(-430.38, -61.3) * mm});
            skLineSegment(sketch, "E1212", {"start": v(-430.38, -61.3) * mm, "end": v(-432.54, -63.58) * mm});
            skLineSegment(sketch, "E1213", {"start": v(-432.54, -63.58) * mm, "end": v(-433.08, -64.44) * mm});
            skLineSegment(sketch, "E1214", {"start": v(-433.08, -64.44) * mm, "end": v(-433.23, -64.69) * mm});
            skLineSegment(sketch, "E1215", {"start": v(-433.23, -64.69) * mm, "end": v(-433.57, -65.5) * mm});
            skLineSegment(sketch, "E1216", {"start": v(-433.57, -65.5) * mm, "end": v(-433.9, -66.62) * mm});
            skLineSegment(sketch, "E1217", {"start": v(-433.9, -66.62) * mm, "end": v(-434.24, -67.7) * mm});
            skLineSegment(sketch, "E1218", {"start": v(-434.24, -67.7) * mm, "end": v(-434.56, -68.43) * mm});
            skLineSegment(sketch, "E1219", {"start": v(-434.56, -68.43) * mm, "end": v(-434.7, -68.64) * mm});
            skLineSegment(sketch, "E1220", {"start": v(-434.7, -68.64) * mm, "end": v(-434.92, -68.94) * mm});
            skLineSegment(sketch, "E1221", {"start": v(-434.92, -68.94) * mm, "end": v(-436.13, -70.35) * mm});
            skLineSegment(sketch, "E1222", {"start": v(-436.13, -70.35) * mm, "end": v(-437.47, -71.66) * mm});
            skLineSegment(sketch, "E1223", {"start": v(-437.47, -71.66) * mm, "end": v(-437.74, -71.9) * mm});
            skLineSegment(sketch, "E1224", {"start": v(-437.74, -71.9) * mm, "end": v(-441.4, -75.2) * mm});
            skLineSegment(sketch, "E1225", {"start": v(-441.4, -75.2) * mm, "end": v(-436.7, -73.72) * mm});
            skLineSegment(sketch, "E1226", {"start": v(-436.7, -73.72) * mm, "end": v(-436.03, -73.5) * mm});
            skLineSegment(sketch, "E1227", {"start": v(-436.03, -73.5) * mm, "end": v(-432.54, -72.77) * mm});
            skLineSegment(sketch, "E1228", {"start": v(-432.54, -72.77) * mm, "end": v(-428.97, -72.59) * mm});
            skLineSegment(sketch, "E1229", {"start": v(-428.97, -72.59) * mm, "end": v(-428.27, -72.65) * mm});
            skLineSegment(sketch, "E1230", {"start": v(-428.27, -72.65) * mm, "end": v(-428.22, -72.67) * mm});
            skLineSegment(sketch, "E1231", {"start": v(-428.22, -72.67) * mm, "end": v(-428.17, -72.66) * mm});
            skLineSegment(sketch, "E1232", {"start": v(-428.17, -72.66) * mm, "end": v(-428.15, -72.66) * mm});
            skLineSegment(sketch, "E1233", {"start": v(-428.15, -72.66) * mm, "end": v(-428.1, -72.67) * mm});
            skLineSegment(sketch, "E1234", {"start": v(-428.1, -72.67) * mm, "end": v(-428.08, -72.67) * mm});
            skLineSegment(sketch, "E1235", {"start": v(-428.08, -72.67) * mm, "end": v(-427.6, -72.67) * mm});
            skLineSegment(sketch, "E1236", {"start": v(-427.6, -72.67) * mm, "end": v(-427.27, -72.3) * mm});
            skLineSegment(sketch, "E1237", {"start": v(-427.27, -72.3) * mm, "end": v(-427.04, -72.03) * mm});
            skLineSegment(sketch, "E1238", {"start": v(-427.04, -72.03) * mm, "end": v(-425.77, -70.58) * mm});
            skLineSegment(sketch, "E1239", {"start": v(-425.77, -70.58) * mm, "end": v(-424.4, -69.24) * mm});
            skLineSegment(sketch, "E1240", {"start": v(-424.4, -69.24) * mm, "end": v(-424.12, -69.02) * mm});
            skLineSegment(sketch, "E1241", {"start": v(-424.12, -69.02) * mm, "end": v(-423.93, -68.89) * mm});
            skLineSegment(sketch, "E1242", {"start": v(-423.93, -68.89) * mm, "end": v(-423.33, -68.56) * mm});
            skLineSegment(sketch, "E1243", {"start": v(-423.33, -68.56) * mm, "end": v(-422.47, -68.2) * mm});
            skLineSegment(sketch, "E1244", {"start": v(-422.47, -68.2) * mm, "end": v(-421.6, -67.8) * mm});
            skLineSegment(sketch, "E1245", {"start": v(-421.6, -67.8) * mm, "end": v(-420.95, -67.42) * mm});
            skLineSegment(sketch, "E1246", {"start": v(-420.95, -67.42) * mm, "end": v(-420.76, -67.27) * mm});
            skLineSegment(sketch, "E1247", {"start": v(-420.76, -67.27) * mm, "end": v(-419.77, -66.48) * mm});
            skLineSegment(sketch, "E1248", {"start": v(-419.77, -66.48) * mm, "end": v(-417.14, -63.7) * mm});
            skLineSegment(sketch, "E1249", {"start": v(-417.14, -63.7) * mm, "end": v(-414.07, -59.68) * mm});
            skLineSegment(sketch, "E1250", {"start": v(-414.07, -59.68) * mm, "end": v(-411.13, -55.55) * mm});
            skLineSegment(sketch, "E1251", {"start": v(-411.13, -55.55) * mm, "end": v(-408.78, -52.56) * mm});
            skLineSegment(sketch, "E1252", {"start": v(-408.78, -52.56) * mm, "end": v(-407.91, -51.65) * mm});
            skLineSegment(sketch, "E1253", {"start": v(-407.91, -51.65) * mm, "end": v(-407.02, -50.73) * mm});
            skLineSegment(sketch, "E1254", {"start": v(-407.02, -50.73) * mm, "end": v(-402.3, -46.33) * mm});
            skLineSegment(sketch, "E1255", {"start": v(-402.3, -46.33) * mm, "end": v(-397.5, -42.02) * mm});
            skLineSegment(sketch, "E1256", {"start": v(-397.5, -42.02) * mm, "end": v(-396.56, -41.13) * mm});
            skLineSegment(sketch, "E1257", {"start": v(-396.56, -41.13) * mm, "end": v(-395.6, -40.23) * mm});
            skLineSegment(sketch, "E1258", {"start": v(-395.6, -40.23) * mm, "end": v(-390.75, -35.75) * mm});
            skLineSegment(sketch, "E1259", {"start": v(-390.75, -35.75) * mm, "end": v(-386.02, -31.14) * mm});
            skLineSegment(sketch, "E1260", {"start": v(-386.02, -31.14) * mm, "end": v(-385.12, -30.17) * mm});
            skLineSegment(sketch, "E1261", {"start": v(-385.12, -30.17) * mm, "end": v(-383.78, -28.73) * mm});
            skLineSegment(sketch, "E1262", {"start": v(-383.78, -28.73) * mm, "end": v(-379.98, -24.19) * mm});
            skLineSegment(sketch, "E1263", {"start": v(-379.98, -24.19) * mm, "end": v(-375, -17.96) * mm});
            skLineSegment(sketch, "E1264", {"start": v(-375, -17.96) * mm, "end": v(-369.91, -11.87) * mm});
            skLineSegment(sketch, "E1265", {"start": v(-369.91, -11.87) * mm, "end": v(-365.86, -7.59) * mm});
            skLineSegment(sketch, "E1266", {"start": v(-365.86, -7.59) * mm, "end": v(-364.4, -6.28) * mm});
            skLineSegment(sketch, "E1267", {"start": v(-364.4, -6.28) * mm, "end": v(-362.18, -4.29) * mm});
            skLineSegment(sketch, "E1268", {"start": v(-362.18, -4.29) * mm, "end": v(-355.7, 1.9) * mm});
            skLineSegment(sketch, "E1269", {"start": v(-355.7, 1.9) * mm, "end": v(-347.3, 10.38) * mm});
            skLineSegment(sketch, "E1270", {"start": v(-347.3, 10.38) * mm, "end": v(-339, 18.95) * mm});
            skLineSegment(sketch, "E1271", {"start": v(-339, 18.95) * mm, "end": v(-332.73, 25.35) * mm});
            skLineSegment(sketch, "E1272", {"start": v(-332.73, 25.35) * mm, "end": v(-330.6, 27.45) * mm});
            skLineSegment(sketch, "E1273", {"start": v(-330.6, 27.45) * mm, "end": v(-330.42, 27.57) * mm});
            skLineSegment(sketch, "E1274", {"start": v(-330.42, 27.57) * mm, "end": v(-329.99, 28.1) * mm});
            skLineSegment(sketch, "E1275", {"start": v(-329.99, 28.1) * mm, "end": v(-329.71, 28.86) * mm});
            skLineSegment(sketch, "E1276", {"start": v(-329.71, 28.86) * mm, "end": v(-329.6, 29.63) * mm});
            skLineSegment(sketch, "E1277", {"start": v(-329.6, 29.63) * mm, "end": v(-329.53, 30.15) * mm});
            skLineSegment(sketch, "E1278", {"start": v(-329.53, 30.15) * mm, "end": v(-329.47, 30.32) * mm});
            skLineSegment(sketch, "E1279", {"start": v(-329.47, 30.32) * mm, "end": v(-328.36, 30.9) * mm});
            skLineSegment(sketch, "E1280", {"start": v(-328.36, 30.9) * mm, "end": v(-325.37, 33.25) * mm});
            skLineSegment(sketch, "E1281", {"start": v(-325.37, 33.25) * mm, "end": v(-321.7, 36.86) * mm});
            skLineSegment(sketch, "E1282", {"start": v(-321.7, 36.86) * mm, "end": v(-317.98, 40.42) * mm});
            skLineSegment(sketch, "E1283", {"start": v(-317.98, 40.42) * mm, "end": v(-314.9, 42.63) * mm});
            skLineSegment(sketch, "E1284", {"start": v(-314.9, 42.63) * mm, "end": v(-313.76, 43.14) * mm});
            skLineSegment(sketch, "E1285", {"start": v(-313.76, 43.14) * mm, "end": v(-313.11, 43.43) * mm});
            skLineSegment(sketch, "E1286", {"start": v(-313.11, 43.43) * mm, "end": v(-309.77, 44.6) * mm});
            skLineSegment(sketch, "E1287", {"start": v(-309.77, 44.6) * mm, "end": v(-306.38, 45.7) * mm});
            skLineSegment(sketch, "E1288", {"start": v(-306.38, 45.7) * mm, "end": v(-305.72, 45.95) * mm});
            skLineSegment(sketch, "E1289", {"start": v(-305.72, 45.95) * mm, "end": v(-305.32, 46.12) * mm});
            skLineSegment(sketch, "E1290", {"start": v(-305.32, 46.12) * mm, "end": v(-304.17, 46.74) * mm});
            skLineSegment(sketch, "E1291", {"start": v(-304.17, 46.74) * mm, "end": v(-302.47, 47.63) * mm});
            skLineSegment(sketch, "E1292", {"start": v(-302.47, 47.63) * mm, "end": v(-300.73, 48.2) * mm});
            skLineSegment(sketch, "E1293", {"start": v(-300.73, 48.2) * mm, "end": v(-299.42, 48.17) * mm});
            skLineSegment(sketch, "E1294", {"start": v(-299.42, 48.17) * mm, "end": v(-299.05, 48) * mm});
            skLineSegment(sketch, "E1295", {"start": v(-299.05, 48) * mm, "end": v(-298.95, 47.41) * mm});
            skLineSegment(sketch, "E1296", {"start": v(-298.95, 47.41) * mm, "end": v(-299, 45.58) * mm});
            skLineSegment(sketch, "E1297", {"start": v(-299, 45.58) * mm, "end": v(-299.53, 43.16) * mm});
            skLineSegment(sketch, "E1298", {"start": v(-299.53, 43.16) * mm, "end": v(-300.48, 40.84) * mm});
            skLineSegment(sketch, "E1299", {"start": v(-300.48, 40.84) * mm, "end": v(-301.36, 39.25) * mm});
            skLineSegment(sketch, "E1300", {"start": v(-301.36, 39.25) * mm, "end": v(-301.7, 38.74) * mm});
            skLineSegment(sketch, "E1301", {"start": v(-301.7, 38.74) * mm, "end": v(-302.45, 37.56) * mm});
            skLineSegment(sketch, "E1302", {"start": v(-302.45, 37.56) * mm, "end": v(-306.76, 32) * mm});
            skLineSegment(sketch, "E1303", {"start": v(-306.76, 32) * mm, "end": v(-311.2, 26.52) * mm});
            skLineSegment(sketch, "E1304", {"start": v(-311.2, 26.52) * mm, "end": v(-312.03, 25.38) * mm});
            skLineSegment(sketch, "E1305", {"start": v(-312.03, 25.38) * mm, "end": v(-312.86, 24.23) * mm});
            skLineSegment(sketch, "E1306", {"start": v(-312.86, 24.23) * mm, "end": v(-317.31, 18.75) * mm});
            skLineSegment(sketch, "E1307", {"start": v(-317.31, 18.75) * mm, "end": v(-322.04, 13.5) * mm});
            skLineSegment(sketch, "E1308", {"start": v(-322.04, 13.5) * mm, "end": v(-323.01, 12.47) * mm});
            skLineSegment(sketch, "E1309", {"start": v(-323.01, 12.47) * mm, "end": v(-325.46, 9.84) * mm});
            skLineSegment(sketch, "E1310", {"start": v(-325.46, 9.84) * mm, "end": v(-337.72, -3.35) * mm});
            skLineSegment(sketch, "E1311", {"start": v(-337.72, -3.35) * mm, "end": v(-350.21, -16.3) * mm});
            skLineSegment(sketch, "E1312", {"start": v(-350.21, -16.3) * mm, "end": v(-352.78, -18.81) * mm});
            skLineSegment(sketch, "E1313", {"start": v(-352.78, -18.81) * mm, "end": v(-353.35, -19.36) * mm});
            skLineSegment(sketch, "E1314", {"start": v(-353.35, -19.36) * mm, "end": v(-358.91, -24.95) * mm});
            skLineSegment(sketch, "E1315", {"start": v(-358.91, -24.95) * mm, "end": v(-359.49, -25.48) * mm});
            skLineSegment(sketch, "E1316", {"start": v(-359.49, -25.48) * mm, "end": v(-362.64, -28.42) * mm});
            skLineSegment(sketch, "E1317", {"start": v(-362.64, -28.42) * mm, "end": v(-371.92, -37.45) * mm});
            skLineSegment(sketch, "E1318", {"start": v(-371.92, -37.45) * mm, "end": v(-384, -49.76) * mm});
            skLineSegment(sketch, "E1319", {"start": v(-384, -49.76) * mm, "end": v(-395.85, -62.33) * mm});
            skLineSegment(sketch, "E1320", {"start": v(-395.85, -62.33) * mm, "end": v(-404.6, -71.86) * mm});
            skLineSegment(sketch, "E1321", {"start": v(-404.6, -71.86) * mm, "end": v(-407.5, -75.06) * mm});
            skLineSegment(sketch, "E1322", {"start": v(-407.5, -75.06) * mm, "end": v(-408.4, -76.04) * mm});
            skLineSegment(sketch, "E1323", {"start": v(-408.4, -76.04) * mm, "end": v(-407.24, -76.7) * mm});
            skLineSegment(sketch, "E1324", {"start": v(-407.24, -76.7) * mm, "end": v(-406.8, -76.95) * mm});
            skLineSegment(sketch, "E1325", {"start": v(-406.8, -76.95) * mm, "end": v(-404.73, -78.32) * mm});
            skLineSegment(sketch, "E1326", {"start": v(-404.73, -78.32) * mm, "end": v(-402.8, -79.88) * mm});
            skLineSegment(sketch, "E1327", {"start": v(-402.8, -79.88) * mm, "end": v(-402.43, -80.22) * mm});
            skLineSegment(sketch, "E1328", {"start": v(-402.43, -80.22) * mm, "end": v(-401.7, -80.91) * mm});
            skLineSegment(sketch, "E1329", {"start": v(-401.7, -80.91) * mm, "end": v(-400.96, -80.2) * mm});
            skLineSegment(sketch, "E1330", {"start": v(-400.96, -80.2) * mm, "end": v(-399.96, -79.25) * mm});
            skLineSegment(sketch, "E1331", {"start": v(-399.96, -79.25) * mm, "end": v(-390.14, -69.56) * mm});
            skLineSegment(sketch, "E1332", {"start": v(-390.14, -69.56) * mm, "end": v(-389.16, -68.58) * mm});
            skLineSegment(sketch, "E1333", {"start": v(-389.16, -68.58) * mm, "end": v(-387.03, -66.45) * mm});
            skLineSegment(sketch, "E1334", {"start": v(-387.03, -66.45) * mm, "end": v(-376.2, -56.01) * mm});
            skLineSegment(sketch, "E1335", {"start": v(-376.2, -56.01) * mm, "end": v(-365.25, -45.7) * mm});
            skLineSegment(sketch, "E1336", {"start": v(-365.25, -45.7) * mm, "end": v(-363.06, -43.62) * mm});
            skLineSegment(sketch, "E1337", {"start": v(-363.06, -43.62) * mm, "end": v(-360.9, -41.56) * mm});
            skLineSegment(sketch, "E1338", {"start": v(-360.9, -41.56) * mm, "end": v(-350.37, -30.9) * mm});
            skLineSegment(sketch, "E1339", {"start": v(-350.37, -30.9) * mm, "end": v(-339.78, -20.3) * mm});
            skLineSegment(sketch, "E1340", {"start": v(-339.78, -20.3) * mm, "end": v(-337.58, -18.27) * mm});
            skLineSegment(sketch, "E1341", {"start": v(-337.58, -18.27) * mm, "end": v(-335.94, -16.75) * mm});
            skLineSegment(sketch, "E1342", {"start": v(-335.94, -16.75) * mm, "end": v(-327.88, -8.96) * mm});
            skLineSegment(sketch, "E1343", {"start": v(-327.88, -8.96) * mm, "end": v(-319.6, -1.4) * mm});
            skLineSegment(sketch, "E1344", {"start": v(-319.6, -1.4) * mm, "end": v(-317.86, 0) * mm});
            skLineSegment(sketch, "E1345", {"start": v(-317.86, 0) * mm, "end": v(-317.26, 0.5) * mm});
            skLineSegment(sketch, "E1346", {"start": v(-317.26, 0.5) * mm, "end": v(-314.5, 3.18) * mm});
            skLineSegment(sketch, "E1347", {"start": v(-314.5, 3.18) * mm, "end": v(-311.75, 5.86) * mm});
            skLineSegment(sketch, "E1348", {"start": v(-311.75, 5.86) * mm, "end": v(-311.15, 6.33) * mm});
            skLineSegment(sketch, "E1349", {"start": v(-311.15, 6.33) * mm, "end": v(-310.2, 7.08) * mm});
            skLineSegment(sketch, "E1350", {"start": v(-310.2, 7.08) * mm, "end": v(-305.18, 10.56) * mm});
            skLineSegment(sketch, "E1351", {"start": v(-305.18, 10.56) * mm, "end": v(-299.96, 13.74) * mm});
            skLineSegment(sketch, "E1352", {"start": v(-299.96, 13.74) * mm, "end": v(-298.9, 14.33) * mm});
            skLineSegment(sketch, "E1353", {"start": v(-298.9, 14.33) * mm, "end": v(-297.8, 14.97) * mm});
            skLineSegment(sketch, "E1354", {"start": v(-297.8, 14.97) * mm, "end": v(-292, 17.8) * mm});
            skLineSegment(sketch, "E1355", {"start": v(-292, 17.8) * mm, "end": v(-286.23, 20.7) * mm});
            skLineSegment(sketch, "E1356", {"start": v(-286.23, 20.7) * mm, "end": v(-285.13, 21.39) * mm});
            skLineSegment(sketch, "E1357", {"start": v(-285.13, 21.39) * mm, "end": v(-284.25, 21.94) * mm});
            skLineSegment(sketch, "E1358", {"start": v(-284.25, 21.94) * mm, "end": v(-279.95, 24.9) * mm});
            skLineSegment(sketch, "E1359", {"start": v(-279.95, 24.9) * mm, "end": v(-275.65, 27.89) * mm});
            skLineSegment(sketch, "E1360", {"start": v(-275.65, 27.89) * mm, "end": v(-274.75, 28.44) * mm});
            skLineSegment(sketch, "E1361", {"start": v(-274.75, 28.44) * mm, "end": v(-274.56, 28.55) * mm});
            skLineSegment(sketch, "E1362", {"start": v(-274.56, 28.55) * mm, "end": v(-273.98, 28.9) * mm});
            skLineSegment(sketch, "E1363", {"start": v(-273.98, 28.9) * mm, "end": v(-272.76, 29.61) * mm});
            skLineSegment(sketch, "E1364", {"start": v(-272.76, 29.61) * mm, "end": v(-271.26, 30.4) * mm});
            skLineSegment(sketch, "E1365", {"start": v(-271.26, 30.4) * mm, "end": v(-269.62, 31.16) * mm});
            skLineSegment(sketch, "E1366", {"start": v(-269.62, 31.16) * mm, "end": v(-268.03, 31.72) * mm});
            skLineSegment(sketch, "E1367", {"start": v(-268.03, 31.72) * mm, "end": v(-266.6, 31.96) * mm});
            skLineSegment(sketch, "E1368", {"start": v(-266.6, 31.96) * mm, "end": v(-265.54, 31.72) * mm});
            skLineSegment(sketch, "E1369", {"start": v(-265.54, 31.72) * mm, "end": v(-265.02, 31.1) * mm});
            skLineSegment(sketch, "E1370", {"start": v(-265.02, 31.1) * mm, "end": v(-264.97, 30.87) * mm});
            skLineSegment(sketch, "E1371", {"start": v(-264.97, 30.87) * mm, "end": v(-264.85, 30.4) * mm});
            skLineSegment(sketch, "E1372", {"start": v(-264.85, 30.4) * mm, "end": v(-265.31, 28.75) * mm});
            skLineSegment(sketch, "E1373", {"start": v(-265.31, 28.75) * mm, "end": v(-266.77, 26.46) * mm});
            skLineSegment(sketch, "E1374", {"start": v(-266.77, 26.46) * mm, "end": v(-268.61, 24.31) * mm});
            skLineSegment(sketch, "E1375", {"start": v(-268.61, 24.31) * mm, "end": v(-269.75, 23.04) * mm});
            skLineSegment(sketch, "E1376", {"start": v(-269.75, 23.04) * mm, "end": v(-270.09, 22.59) * mm});
            skLineSegment(sketch, "E1377", {"start": v(-270.09, 22.59) * mm, "end": v(-270.6, 21.93) * mm});
            skLineSegment(sketch, "E1378", {"start": v(-270.6, 21.93) * mm, "end": v(-276.07, 15.61) * mm});
            skLineSegment(sketch, "E1379", {"start": v(-276.07, 15.61) * mm, "end": v(-276.66, 15.02) * mm});
            skLineSegment(sketch, "E1380", {"start": v(-276.66, 15.02) * mm, "end": v(-279.24, 13.1) * mm});
            skLineSegment(sketch, "E1381", {"start": v(-279.24, 13.1) * mm, "end": v(-286.66, 6.96) * mm});
            skLineSegment(sketch, "E1382", {"start": v(-286.66, 6.96) * mm, "end": v(-296.18, -1.62) * mm});
            skLineSegment(sketch, "E1383", {"start": v(-296.18, -1.62) * mm, "end": v(-305.5, -10.43) * mm});
            skLineSegment(sketch, "E1384", {"start": v(-305.5, -10.43) * mm, "end": v(-312.52, -17) * mm});
            skLineSegment(sketch, "E1385", {"start": v(-312.52, -17) * mm, "end": v(-314.9, -19.15) * mm});
            skLineSegment(sketch, "E1386", {"start": v(-314.9, -19.15) * mm, "end": v(-315.64, -19.82) * mm});
            skLineSegment(sketch, "E1387", {"start": v(-315.64, -19.82) * mm, "end": v(-322.96, -26.6) * mm});
            skLineSegment(sketch, "E1388", {"start": v(-322.96, -26.6) * mm, "end": v(-323.66, -27.31) * mm});
            skLineSegment(sketch, "E1389", {"start": v(-323.66, -27.31) * mm, "end": v(-325.05, -28.68) * mm});
            skLineSegment(sketch, "E1390", {"start": v(-325.05, -28.68) * mm, "end": v(-332.28, -35.17) * mm});
            skLineSegment(sketch, "E1391", {"start": v(-332.28, -35.17) * mm, "end": v(-339.43, -41.74) * mm});
            skLineSegment(sketch, "E1392", {"start": v(-339.43, -41.74) * mm, "end": v(-340.77, -43.16) * mm});
            skLineSegment(sketch, "E1393", {"start": v(-340.77, -43.16) * mm, "end": v(-341.97, -44.41) * mm});
            skLineSegment(sketch, "E1394", {"start": v(-341.97, -44.41) * mm, "end": v(-345.55, -48.21) * mm});
            skLineSegment(sketch, "E1395", {"start": v(-345.55, -48.21) * mm, "end": v(-350.35, -53.24) * mm});
            skLineSegment(sketch, "E1396", {"start": v(-350.35, -53.24) * mm, "end": v(-355.29, -58.12) * mm});
            skLineSegment(sketch, "E1397", {"start": v(-355.29, -58.12) * mm, "end": v(-359.14, -61.65) * mm});
            skLineSegment(sketch, "E1398", {"start": v(-359.14, -61.65) * mm, "end": v(-360.48, -62.76) * mm});
            skLineSegment(sketch, "E1399", {"start": v(-360.48, -62.76) * mm, "end": v(-360.53, -62.8) * mm});
            skLineSegment(sketch, "E1400", {"start": v(-360.53, -62.8) * mm, "end": v(-360.57, -62.86) * mm});
            skLineSegment(sketch, "E1401", {"start": v(-360.57, -62.86) * mm, "end": v(-360.81, -63.12) * mm});
            skLineSegment(sketch, "E1402", {"start": v(-360.81, -63.12) * mm, "end": v(-363.33, -65.73) * mm});
            skLineSegment(sketch, "E1403", {"start": v(-363.33, -65.73) * mm, "end": v(-363.57, -66) * mm});
            skLineSegment(sketch, "E1404", {"start": v(-363.57, -66) * mm, "end": v(-364.2, -66.72) * mm});
            skLineSegment(sketch, "E1405", {"start": v(-364.2, -66.72) * mm, "end": v(-362.95, -68.14) * mm});
            skLineSegment(sketch, "E1406", {"start": v(-362.95, -68.14) * mm, "end": v(-362.16, -67.6) * mm});
            skLineSegment(sketch, "E1407", {"start": v(-362.16, -67.6) * mm, "end": v(-361.54, -67.17) * mm});
            skLineSegment(sketch, "E1408", {"start": v(-361.54, -67.17) * mm, "end": v(-359.56, -66) * mm});
            skLineSegment(sketch, "E1409", {"start": v(-359.56, -66) * mm, "end": v(-356.77, -64.74) * mm});
            skLineSegment(sketch, "E1410", {"start": v(-356.77, -64.74) * mm, "end": v(-353.84, -63.92) * mm});
            skLineSegment(sketch, "E1411", {"start": v(-353.84, -63.92) * mm, "end": v(-351.56, -63.61) * mm});
            skLineSegment(sketch, "E1412", {"start": v(-351.56, -63.61) * mm, "end": v(-350.8, -63.6) * mm});
            skLineSegment(sketch, "E1413", {"start": v(-350.8, -63.6) * mm, "end": v(-350.38, -63.6) * mm});
            skLineSegment(sketch, "E1414", {"start": v(-350.38, -63.6) * mm, "end": v(-350.07, -63.33) * mm});
            skLineSegment(sketch, "E1415", {"start": v(-350.07, -63.33) * mm, "end": v(-346.96, -60.4) * mm});
            skLineSegment(sketch, "E1416", {"start": v(-346.96, -60.4) * mm, "end": v(-331.5, -45.7) * mm});
            skLineSegment(sketch, "E1417", {"start": v(-331.5, -45.7) * mm, "end": v(-315.99, -31.07) * mm});
            skLineSegment(sketch, "E1418", {"start": v(-315.99, -31.07) * mm, "end": v(-312.85, -28.19) * mm});
            skLineSegment(sketch, "E1419", {"start": v(-312.85, -28.19) * mm, "end": v(-309.77, -26.1) * mm});
            skLineSegment(sketch, "E1420", {"start": v(-309.77, -26.1) * mm, "end": v(-300.86, -19.35) * mm});
            skLineSegment(sketch, "E1421", {"start": v(-300.86, -19.35) * mm, "end": v(-289.36, -9.9) * mm});
            skLineSegment(sketch, "E1422", {"start": v(-289.36, -9.9) * mm, "end": v(-277.91, -0.38) * mm});
            skLineSegment(sketch, "E1423", {"start": v(-277.91, -0.38) * mm, "end": v(-269.12, 6.52) * mm});
            skLineSegment(sketch, "E1424", {"start": v(-269.12, 6.52) * mm, "end": v(-266.09, 8.67) * mm});
            skLineSegment(sketch, "E1425", {"start": v(-266.09, 8.67) * mm, "end": v(-265.28, 8.94) * mm});
            skLineSegment(sketch, "E1426", {"start": v(-265.28, 8.94) * mm, "end": v(-262.97, 10.06) * mm});
            skLineSegment(sketch, "E1427", {"start": v(-262.97, 10.06) * mm, "end": v(-260.02, 11.86) * mm});
            skLineSegment(sketch, "E1428", {"start": v(-260.02, 11.86) * mm, "end": v(-257.09, 13.73) * mm});
            skLineSegment(sketch, "E1429", {"start": v(-257.09, 13.73) * mm, "end": v(-254.85, 15.01) * mm});
            skLineSegment(sketch, "E1430", {"start": v(-254.85, 15.01) * mm, "end": v(-254.07, 15.37) * mm});
            skLineSegment(sketch, "E1431", {"start": v(-254.07, 15.37) * mm, "end": v(-253.52, 15.62) * mm});
            skLineSegment(sketch, "E1432", {"start": v(-253.52, 15.62) * mm, "end": v(-251.85, 16.36) * mm});
            skLineSegment(sketch, "E1433", {"start": v(-251.85, 16.36) * mm, "end": v(-249.47, 17.3) * mm});
            skLineSegment(sketch, "E1434", {"start": v(-249.47, 17.3) * mm, "end": v(-247, 18.04) * mm});
            skLineSegment(sketch, "E1435", {"start": v(-247, 18.04) * mm, "end": v(-245.18, 18.38) * mm});
            skLineSegment(sketch, "E1436", {"start": v(-245.18, 18.38) * mm, "end": v(-244.56, 18.42) * mm});
            skLineSegment(sketch, "E1437", {"start": v(-244.56, 18.42) * mm, "end": v(-244.94, 17.34) * mm});
            skLineSegment(sketch, "E1438", {"start": v(-244.94, 17.34) * mm, "end": v(-246.53, 14.27) * mm});
            skLineSegment(sketch, "E1439", {"start": v(-246.53, 14.27) * mm, "end": v(-249.16, 10.53) * mm});
            skLineSegment(sketch, "E1440", {"start": v(-249.16, 10.53) * mm, "end": v(-252.18, 7.04) * mm});
            skLineSegment(sketch, "E1441", {"start": v(-252.18, 7.04) * mm, "end": v(-254.54, 4.5) * mm});
            skLineSegment(sketch, "E1442", {"start": v(-254.54, 4.5) * mm, "end": v(-255.31, 3.64) * mm});
            skLineSegment(sketch, "E1443", {"start": v(-255.31, 3.64) * mm, "end": v(-256.12, 2.75) * mm});
            skLineSegment(sketch, "E1444", {"start": v(-256.12, 2.75) * mm, "end": v(-264.44, -6.01) * mm});
            skLineSegment(sketch, "E1445", {"start": v(-264.44, -6.01) * mm, "end": v(-265.3, -6.85) * mm});
            skLineSegment(sketch, "E1446", {"start": v(-265.3, -6.85) * mm, "end": v(-265.62, -7.14) * mm});
            skLineSegment(sketch, "E1447", {"start": v(-265.62, -7.14) * mm, "end": v(-267.34, -8.42) * mm});
            skLineSegment(sketch, "E1448", {"start": v(-267.34, -8.42) * mm, "end": v(-269.04, -9.73) * mm});
            skLineSegment(sketch, "E1449", {"start": v(-269.04, -9.73) * mm, "end": v(-269.35, -10.04) * mm});
            skLineSegment(sketch, "E1450", {"start": v(-269.35, -10.04) * mm, "end": v(-269.6, -10.29) * mm});
            skLineSegment(sketch, "E1451", {"start": v(-269.6, -10.29) * mm, "end": v(-270.27, -11.14) * mm});
            skLineSegment(sketch, "E1452", {"start": v(-270.27, -11.14) * mm, "end": v(-271.06, -12.34) * mm});
            skLineSegment(sketch, "E1453", {"start": v(-271.06, -12.34) * mm, "end": v(-271.83, -13.54) * mm});
            skLineSegment(sketch, "E1454", {"start": v(-271.83, -13.54) * mm, "end": v(-272.47, -14.38) * mm});
            skLineSegment(sketch, "E1455", {"start": v(-272.47, -14.38) * mm, "end": v(-272.72, -14.63) * mm});
            skLineSegment(sketch, "E1456", {"start": v(-272.72, -14.63) * mm, "end": v(-273.7, -15.61) * mm});
            skLineSegment(sketch, "E1457", {"start": v(-273.7, -15.61) * mm, "end": v(-278.84, -20.37) * mm});
            skLineSegment(sketch, "E1458", {"start": v(-278.84, -20.37) * mm, "end": v(-283.87, -25.24) * mm});
            skLineSegment(sketch, "E1459", {"start": v(-283.87, -25.24) * mm, "end": v(-284.8, -26.28) * mm});
            skLineSegment(sketch, "E1460", {"start": v(-284.8, -26.28) * mm, "end": v(-286.97, -28.71) * mm});
            skLineSegment(sketch, "E1461", {"start": v(-286.97, -28.71) * mm, "end": v(-298.09, -40.6) * mm});
            skLineSegment(sketch, "E1462", {"start": v(-298.09, -40.6) * mm, "end": v(-309.68, -52.04) * mm});
            skLineSegment(sketch, "E1463", {"start": v(-309.68, -52.04) * mm, "end": v(-312.09, -54.23) * mm});
            skLineSegment(sketch, "E1464", {"start": v(-312.09, -54.23) * mm, "end": v(-314.04, -56) * mm});
            skLineSegment(sketch, "E1465", {"start": v(-314.04, -56) * mm, "end": v(-311.4, -56.08) * mm});
            skLineSegment(sketch, "E1466", {"start": v(-311.4, -56.08) * mm, "end": v(-310.7, -56.1) * mm});
            skLineSegment(sketch, "E1467", {"start": v(-310.7, -56.1) * mm, "end": v(-307.37, -56.8) * mm});
            skLineSegment(sketch, "E1468", {"start": v(-307.37, -56.8) * mm, "end": v(-304.3, -58.24) * mm});
            skLineSegment(sketch, "E1469", {"start": v(-304.3, -58.24) * mm, "end": v(-303.73, -58.64) * mm});
            skLineSegment(sketch, "E1470", {"start": v(-303.73, -58.64) * mm, "end": v(-303.06, -59.1) * mm});
            skLineSegment(sketch, "E1471", {"start": v(-303.06, -59.1) * mm, "end": v(-302.43, -58.57) * mm});
            skLineSegment(sketch, "E1472", {"start": v(-302.43, -58.57) * mm, "end": v(-302.16, -58.35) * mm});
            skLineSegment(sketch, "E1473", {"start": v(-302.16, -58.35) * mm, "end": v(-300.9, -57.19) * mm});
            skLineSegment(sketch, "E1474", {"start": v(-300.9, -57.19) * mm, "end": v(-299.82, -55.87) * mm});
            skLineSegment(sketch, "E1475", {"start": v(-299.82, -55.87) * mm, "end": v(-299.65, -55.56) * mm});
            skLineSegment(sketch, "E1476", {"start": v(-299.65, -55.56) * mm, "end": v(-297.27, -53.9) * mm});
            skLineSegment(sketch, "E1477", {"start": v(-297.27, -53.9) * mm, "end": v(-290.45, -48.42) * mm});
            skLineSegment(sketch, "E1478", {"start": v(-290.45, -48.42) * mm, "end": v(-281.82, -40.6) * mm});
            skLineSegment(sketch, "E1479", {"start": v(-281.82, -40.6) * mm, "end": v(-273.48, -32.41) * mm});
            skLineSegment(sketch, "E1480", {"start": v(-273.48, -32.41) * mm, "end": v(-267.28, -26.27) * mm});
            skLineSegment(sketch, "E1481", {"start": v(-267.28, -26.27) * mm, "end": v(-265.18, -24.25) * mm});
            skLineSegment(sketch, "E1482", {"start": v(-265.18, -24.25) * mm, "end": v(-263.34, -22.47) * mm});
            skLineSegment(sketch, "E1483", {"start": v(-263.34, -22.47) * mm, "end": v(-257.33, -17.58) * mm});
            skLineSegment(sketch, "E1484", {"start": v(-257.33, -17.58) * mm, "end": v(-248.97, -11.55) * mm});
            skLineSegment(sketch, "E1485", {"start": v(-248.97, -11.55) * mm, "end": v(-240.55, -5.58) * mm});
            skLineSegment(sketch, "E1486", {"start": v(-240.55, -5.58) * mm, "end": v(-234.44, -0.82) * mm});
            skLineSegment(sketch, "E1487", {"start": v(-234.44, -0.82) * mm, "end": v(-232.53, 0.9) * mm});
            skLineSegment(sketch, "E1488", {"start": v(-232.53, 0.9) * mm, "end": v(-231.5, 1.22) * mm});
            skLineSegment(sketch, "E1489", {"start": v(-231.5, 1.22) * mm, "end": v(-228.6, 2.66) * mm});
            skLineSegment(sketch, "E1490", {"start": v(-228.6, 2.66) * mm, "end": v(-225.1, 4.94) * mm});
            skLineSegment(sketch, "E1491", {"start": v(-225.1, 4.94) * mm, "end": v(-221.66, 7.25) * mm});
            skLineSegment(sketch, "E1492", {"start": v(-221.66, 7.25) * mm, "end": v(-218.92, 8.74) * mm});
            skLineSegment(sketch, "E1493", {"start": v(-218.92, 8.74) * mm, "end": v(-217.95, 9.1) * mm});
            skLineSegment(sketch, "E1494", {"start": v(-217.95, 9.1) * mm, "end": v(-217.68, 8.79) * mm});
            skLineSegment(sketch, "E1495", {"start": v(-217.68, 8.79) * mm, "end": v(-217.13, 7.64) * mm});
            skLineSegment(sketch, "E1496", {"start": v(-217.13, 7.64) * mm, "end": v(-216.98, 6.09) * mm});
            skLineSegment(sketch, "E1497", {"start": v(-216.98, 6.09) * mm, "end": v(-217.36, 4.47) * mm});
            skLineSegment(sketch, "E1498", {"start": v(-217.36, 4.47) * mm, "end": v(-218.14, 2.85) * mm});
            skLineSegment(sketch, "E1499", {"start": v(-218.14, 2.85) * mm, "end": v(-219.19, 1.27) * mm});
            skLineSegment(sketch, "E1500", {"start": v(-219.19, 1.27) * mm, "end": v(-220.35, -0.2) * mm});
            skLineSegment(sketch, "E1501", {"start": v(-220.35, -0.2) * mm, "end": v(-221.5, -1.55) * mm});
            skLineSegment(sketch, "E1502", {"start": v(-221.5, -1.55) * mm, "end": v(-222.26, -2.41) * mm});
            skLineSegment(sketch, "E1503", {"start": v(-222.26, -2.41) * mm, "end": v(-222.51, -2.7) * mm});
            skLineSegment(sketch, "E1504", {"start": v(-222.51, -2.7) * mm, "end": v(-222.93, -3.2) * mm});
            skLineSegment(sketch, "E1505", {"start": v(-222.93, -3.2) * mm, "end": v(-224.25, -4.7) * mm});
            skLineSegment(sketch, "E1506", {"start": v(-224.25, -4.7) * mm, "end": v(-226.19, -6.73) * mm});
            skLineSegment(sketch, "E1507", {"start": v(-226.19, -6.73) * mm, "end": v(-228.24, -8.64) * mm});
            skLineSegment(sketch, "E1508", {"start": v(-228.24, -8.64) * mm, "end": v(-229.78, -9.87) * mm});
            skLineSegment(sketch, "E1509", {"start": v(-229.78, -9.87) * mm, "end": v(-230.33, -10.24) * mm});
            skLineSegment(sketch, "E1510", {"start": v(-230.33, -10.24) * mm, "end": v(-230.67, -10.46) * mm});
            skLineSegment(sketch, "E1511", {"start": v(-230.67, -10.46) * mm, "end": v(-230.76, -10.86) * mm});
            skLineSegment(sketch, "E1512", {"start": v(-230.76, -10.86) * mm, "end": v(-231, -11.74) * mm});
            skLineSegment(sketch, "E1513", {"start": v(-231, -11.74) * mm, "end": v(-232.4, -14.18) * mm});
            skLineSegment(sketch, "E1514", {"start": v(-232.4, -14.18) * mm, "end": v(-234.93, -16.74) * mm});
            skLineSegment(sketch, "E1515", {"start": v(-234.93, -16.74) * mm, "end": v(-237.8, -19.03) * mm});
            skLineSegment(sketch, "E1516", {"start": v(-237.8, -19.03) * mm, "end": v(-239.89, -20.87) * mm});
            skLineSegment(sketch, "E1517", {"start": v(-239.89, -20.87) * mm, "end": v(-240.48, -21.58) * mm});
            skLineSegment(sketch, "E1518", {"start": v(-240.48, -21.58) * mm, "end": v(-241.36, -22.04) * mm});
            skLineSegment(sketch, "E1519", {"start": v(-241.36, -22.04) * mm, "end": v(-245.16, -24.7) * mm});
            skLineSegment(sketch, "E1520", {"start": v(-245.16, -24.7) * mm, "end": v(-248.73, -27.65) * mm});
            skLineSegment(sketch, "E1521", {"start": v(-248.73, -27.65) * mm, "end": v(-249.5, -28.27) * mm});
            skLineSegment(sketch, "E1522", {"start": v(-249.5, -28.27) * mm, "end": v(-251.6, -29.92) * mm});
            skLineSegment(sketch, "E1523", {"start": v(-251.6, -29.92) * mm, "end": v(-261.68, -38.75) * mm});
            skLineSegment(sketch, "E1524", {"start": v(-261.68, -38.75) * mm, "end": v(-271.42, -47.96) * mm});
            skLineSegment(sketch, "E1525", {"start": v(-271.42, -47.96) * mm, "end": v(-273.36, -49.8) * mm});
            skLineSegment(sketch, "E1526", {"start": v(-273.36, -49.8) * mm, "end": v(-273.46, -49.9) * mm});
            skLineSegment(sketch, "E1527", {"start": v(-273.46, -49.9) * mm, "end": v(-274.51, -50.84) * mm});
            skLineSegment(sketch, "E1528", {"start": v(-274.51, -50.84) * mm, "end": v(-274.6, -50.94) * mm});
            skLineSegment(sketch, "E1529", {"start": v(-274.6, -50.94) * mm, "end": v(-276.66, -52.88) * mm});
            skLineSegment(sketch, "E1530", {"start": v(-276.66, -52.88) * mm, "end": v(-273.85, -52.78) * mm});
            skLineSegment(sketch, "E1531", {"start": v(-273.85, -52.78) * mm, "end": v(-272.84, -52.75) * mm});
            skLineSegment(sketch, "E1532", {"start": v(-272.84, -52.75) * mm, "end": v(-267.76, -53.33) * mm});
            skLineSegment(sketch, "E1533", {"start": v(-267.76, -53.33) * mm, "end": v(-262.94, -54.95) * mm});
            skLineSegment(sketch, "E1534", {"start": v(-262.94, -54.95) * mm, "end": v(-262.05, -55.45) * mm});
            skLineSegment(sketch, "E1535", {"start": v(-262.05, -55.45) * mm, "end": v(-261.47, -55.77) * mm});
            skLineSegment(sketch, "E1536", {"start": v(-261.47, -55.77) * mm, "end": v(-260.92, -55.4) * mm});
            skLineSegment(sketch, "E1537", {"start": v(-260.92, -55.4) * mm, "end": v(-258.32, -53.63) * mm});
            skLineSegment(sketch, "E1538", {"start": v(-258.32, -53.63) * mm, "end": v(-250.76, -47.99) * mm});
            skLineSegment(sketch, "E1539", {"start": v(-250.76, -47.99) * mm, "end": v(-241.05, -40.05) * mm});
            skLineSegment(sketch, "E1540", {"start": v(-241.05, -40.05) * mm, "end": v(-231.62, -31.76) * mm});
            skLineSegment(sketch, "E1541", {"start": v(-231.62, -31.76) * mm, "end": v(-224.66, -25.4) * mm});
            skLineSegment(sketch, "E1542", {"start": v(-224.66, -25.4) * mm, "end": v(-222.35, -23.27) * mm});
            skLineSegment(sketch, "E1543", {"start": v(-222.35, -23.27) * mm, "end": v(-220.5, -22.1) * mm});
            skLineSegment(sketch, "E1544", {"start": v(-220.5, -22.1) * mm, "end": v(-214.98, -18.6) * mm});
            skLineSegment(sketch, "E1545", {"start": v(-214.98, -18.6) * mm, "end": v(-207.7, -14.33) * mm});
            skLineSegment(sketch, "E1546", {"start": v(-207.7, -14.33) * mm, "end": v(-200.1, -10.75) * mm});
            skLineSegment(sketch, "E1547", {"start": v(-200.1, -10.75) * mm, "end": v(-193.88, -8.62) * mm});
            skLineSegment(sketch, "E1548", {"start": v(-193.88, -8.62) * mm, "end": v(-191.75, -8.13) * mm});
            skLineSegment(sketch, "E1549", {"start": v(-191.75, -8.13) * mm, "end": v(-191.5, -8.58) * mm});
            skLineSegment(sketch, "E1550", {"start": v(-191.5, -8.58) * mm, "end": v(-190.64, -9.88) * mm});
            skLineSegment(sketch, "E1551", {"start": v(-190.64, -9.88) * mm, "end": v(-189.63, -11.58) * mm});
            skLineSegment(sketch, "E1552", {"start": v(-189.63, -11.58) * mm, "end": v(-188.96, -13.4) * mm});
            skLineSegment(sketch, "E1553", {"start": v(-188.96, -13.4) * mm, "end": v(-188.81, -15.04) * mm});
            skLineSegment(sketch, "E1554", {"start": v(-188.81, -15.04) * mm, "end": v(-188.88, -15.57) * mm});
            skLineSegment(sketch, "E1555", {"start": v(-188.88, -15.57) * mm, "end": v(-188.93, -15.97) * mm});
            skLineSegment(sketch, "E1556", {"start": v(-188.93, -15.97) * mm, "end": v(-189.35, -17.14) * mm});
            skLineSegment(sketch, "E1557", {"start": v(-189.35, -17.14) * mm, "end": v(-190.24, -18.81) * mm});
            skLineSegment(sketch, "E1558", {"start": v(-190.24, -18.81) * mm, "end": v(-191.3, -20.4) * mm});
            skLineSegment(sketch, "E1559", {"start": v(-191.3, -20.4) * mm, "end": v(-192.07, -21.39) * mm});
            skLineSegment(sketch, "E1560", {"start": v(-192.07, -21.39) * mm, "end": v(-192.34, -21.7) * mm});
            skLineSegment(sketch, "E1561", {"start": v(-192.34, -21.7) * mm, "end": v(-192.6, -22.04) * mm});
            skLineSegment(sketch, "E1562", {"start": v(-192.6, -22.04) * mm, "end": v(-193.48, -23) * mm});
            skLineSegment(sketch, "E1563", {"start": v(-193.48, -23) * mm, "end": v(-195.02, -24.52) * mm});
            skLineSegment(sketch, "E1564", {"start": v(-195.02, -24.52) * mm, "end": v(-196.67, -25.88) * mm});
            skLineSegment(sketch, "E1565", {"start": v(-196.67, -25.88) * mm, "end": v(-197.75, -26.56) * mm});
            skLineSegment(sketch, "E1566", {"start": v(-197.75, -26.56) * mm, "end": v(-198.14, -26.67) * mm});
            skLineSegment(sketch, "E1567", {"start": v(-198.14, -26.67) * mm, "end": v(-198.7, -26.82) * mm});
            skLineSegment(sketch, "E1568", {"start": v(-198.7, -26.82) * mm, "end": v(-200.47, -27.05) * mm});
            skLineSegment(sketch, "E1569", {"start": v(-200.47, -27.05) * mm, "end": v(-203.05, -27.12) * mm});
            skLineSegment(sketch, "E1570", {"start": v(-203.05, -27.12) * mm, "end": v(-205.74, -27.08) * mm});
            skLineSegment(sketch, "E1571", {"start": v(-205.74, -27.08) * mm, "end": v(-208.43, -27.13) * mm});
            skLineSegment(sketch, "E1572", {"start": v(-208.43, -27.13) * mm, "end": v(-210.96, -27.47) * mm});
            skLineSegment(sketch, "E1573", {"start": v(-210.96, -27.47) * mm, "end": v(-213.2, -28.3) * mm});
            skLineSegment(sketch, "E1574", {"start": v(-213.2, -28.3) * mm, "end": v(-215.05, -29.82) * mm});
            skLineSegment(sketch, "E1575", {"start": v(-215.05, -29.82) * mm, "end": v(-216.12, -31.6) * mm});
            skLineSegment(sketch, "E1576", {"start": v(-216.12, -31.6) * mm, "end": v(-216.34, -32.24) * mm});
            skLineSegment(sketch, "E1577", {"start": v(-216.34, -32.24) * mm, "end": v(-216.53, -32.81) * mm});
            skLineSegment(sketch, "E1578", {"start": v(-216.53, -32.81) * mm, "end": v(-216.14, -33.26) * mm});
            skLineSegment(sketch, "E1579", {"start": v(-216.14, -33.26) * mm, "end": v(-215.89, -33.56) * mm});
            skLineSegment(sketch, "E1580", {"start": v(-215.89, -33.56) * mm, "end": v(-214.96, -34.3) * mm});
            skLineSegment(sketch, "E1581", {"start": v(-214.96, -34.3) * mm, "end": v(-213.72, -34.82) * mm});
            skLineSegment(sketch, "E1582", {"start": v(-213.72, -34.82) * mm, "end": v(-212.4, -34.94) * mm});
            skLineSegment(sketch, "E1583", {"start": v(-212.4, -34.94) * mm, "end": v(-211.05, -34.78) * mm});
            skLineSegment(sketch, "E1584", {"start": v(-211.05, -34.78) * mm, "end": v(-209.66, -34.48) * mm});
            skLineSegment(sketch, "E1585", {"start": v(-209.66, -34.48) * mm, "end": v(-208.25, -34.17) * mm});
            skLineSegment(sketch, "E1586", {"start": v(-208.25, -34.17) * mm, "end": v(-206.82, -33.97) * mm});
            skLineSegment(sketch, "E1587", {"start": v(-206.82, -33.97) * mm, "end": v(-205.75, -33.96) * mm});
            skLineSegment(sketch, "E1588", {"start": v(-205.75, -33.96) * mm, "end": v(-205.4, -34) * mm});
            skLineSegment(sketch, "E1589", {"start": v(-205.4, -34) * mm, "end": v(-204.71, -34.12) * mm});
            skLineSegment(sketch, "E1590", {"start": v(-204.71, -34.12) * mm, "end": v(-202.7, -34.78) * mm});
            skLineSegment(sketch, "E1591", {"start": v(-202.7, -34.78) * mm, "end": v(-200.06, -35.89) * mm});
            skLineSegment(sketch, "E1592", {"start": v(-200.06, -35.89) * mm, "end": v(-197.36, -36.86) * mm});
            skLineSegment(sketch, "E1593", {"start": v(-197.36, -36.86) * mm, "end": v(-195.21, -37.24) * mm});
            skLineSegment(sketch, "E1594", {"start": v(-195.21, -37.24) * mm, "end": v(-194.5, -37.22) * mm});
            skLineSegment(sketch, "E1595", {"start": v(-194.5, -37.22) * mm, "end": v(-194.08, -37.2) * mm});
            skLineSegment(sketch, "E1596", {"start": v(-194.08, -37.2) * mm, "end": v(-192.84, -36.88) * mm});
            skLineSegment(sketch, "E1597", {"start": v(-192.84, -36.88) * mm, "end": v(-191.5, -36.14) * mm});
            skLineSegment(sketch, "E1598", {"start": v(-191.5, -36.14) * mm, "end": v(-190.29, -35.2) * mm});
            skLineSegment(sketch, "E1599", {"start": v(-190.29, -35.2) * mm, "end": v(-189.3, -34.46) * mm});
            skLineSegment(sketch, "E1600", {"start": v(-189.3, -34.46) * mm, "end": v(-188.94, -34.24) * mm});
            skLineSegment(sketch, "E1601", {"start": v(-188.94, -34.24) * mm, "end": v(-188.03, -33.67) * mm});
            skLineSegment(sketch, "E1602", {"start": v(-188.03, -33.67) * mm, "end": v(-185.2, -32.1) * mm});
            skLineSegment(sketch, "E1603", {"start": v(-185.2, -32.1) * mm, "end": v(-180.98, -29.71) * mm});
            skLineSegment(sketch, "E1604", {"start": v(-180.98, -29.71) * mm, "end": v(-177.04, -27.04) * mm});
            skLineSegment(sketch, "E1605", {"start": v(-177.04, -27.04) * mm, "end": v(-174.74, -24.91) * mm});
            skLineSegment(sketch, "E1606", {"start": v(-174.74, -24.91) * mm, "end": v(-174.18, -24.06) * mm});
            skLineSegment(sketch, "E1607", {"start": v(-174.18, -24.06) * mm, "end": v(-173.88, -23.6) * mm});
            skLineSegment(sketch, "E1608", {"start": v(-173.88, -23.6) * mm, "end": v(-173.17, -22.08) * mm});
            skLineSegment(sketch, "E1609", {"start": v(-173.17, -22.08) * mm, "end": v(-172.66, -20.09) * mm});
            skLineSegment(sketch, "E1610", {"start": v(-172.66, -20.09) * mm, "end": v(-172.63, -18.12) * mm});
            skLineSegment(sketch, "E1611", {"start": v(-172.63, -18.12) * mm, "end": v(-173.03, -16.2) * mm});
            skLineSegment(sketch, "E1612", {"start": v(-173.03, -16.2) * mm, "end": v(-173.8, -14.4) * mm});
            skLineSegment(sketch, "E1613", {"start": v(-173.8, -14.4) * mm, "end": v(-174.92, -12.71) * mm});
            skLineSegment(sketch, "E1614", {"start": v(-174.92, -12.71) * mm, "end": v(-176.33, -11.2) * mm});
            skLineSegment(sketch, "E1615", {"start": v(-176.33, -11.2) * mm, "end": v(-177.55, -10.18) * mm});
            skLineSegment(sketch, "E1616", {"start": v(-177.55, -10.18) * mm, "end": v(-177.98, -9.89) * mm});
            skLineSegment(sketch, "E1617", {"start": v(-177.98, -9.89) * mm, "end": v(-177.98, -9.62) * mm});
            skLineSegment(sketch, "E1618", {"start": v(-177.98, -9.62) * mm, "end": v(-178.21, -8.5) * mm});
            skLineSegment(sketch, "E1619", {"start": v(-178.21, -8.5) * mm, "end": v(-178.71, -7.4) * mm});
            skLineSegment(sketch, "E1620", {"start": v(-178.71, -7.4) * mm, "end": v(-178.84, -7.14) * mm});
            skLineSegment(sketch, "E1621", {"start": v(-178.84, -7.14) * mm, "end": v(-178.93, -6.97) * mm});
            skLineSegment(sketch, "E1622", {"start": v(-178.93, -6.97) * mm, "end": v(-179.08, -6.83) * mm});
            skLineSegment(sketch, "E1623", {"start": v(-179.08, -6.83) * mm, "end": v(-180.27, -5.76) * mm});
            skLineSegment(sketch, "E1624", {"start": v(-180.27, -5.76) * mm, "end": v(-183.37, -2.05) * mm});
            skLineSegment(sketch, "E1625", {"start": v(-183.37, -2.05) * mm, "end": v(-187.01, 3.42) * mm});
            skLineSegment(sketch, "E1626", {"start": v(-187.01, 3.42) * mm, "end": v(-190.43, 9.1) * mm});
            skLineSegment(sketch, "E1627", {"start": v(-190.43, 9.1) * mm, "end": v(-193.05, 13.2) * mm});
            skLineSegment(sketch, "E1628", {"start": v(-193.05, 13.2) * mm, "end": v(-194.02, 14.5) * mm});
            skLineSegment(sketch, "E1629", {"start": v(-194.02, 14.5) * mm, "end": v(-194.38, 14.96) * mm});
            skLineSegment(sketch, "E1630", {"start": v(-194.38, 14.96) * mm, "end": v(-194.96, 14.92) * mm});
            skLineSegment(sketch, "E1631", {"start": v(-194.96, 14.92) * mm, "end": v(-195.5, 14.88) * mm});
            skLineSegment(sketch, "E1632", {"start": v(-195.5, 14.88) * mm, "end": v(-197.1, 15.01) * mm});
            skLineSegment(sketch, "E1633", {"start": v(-197.1, 15.01) * mm, "end": v(-199.11, 15.5) * mm});
            skLineSegment(sketch, "E1634", {"start": v(-199.11, 15.5) * mm, "end": v(-201.02, 16.24) * mm});
            skLineSegment(sketch, "E1635", {"start": v(-201.02, 16.24) * mm, "end": v(-202.88, 17.08) * mm});
            skLineSegment(sketch, "E1636", {"start": v(-202.88, 17.08) * mm, "end": v(-204.73, 17.89) * mm});
            skLineSegment(sketch, "E1637", {"start": v(-204.73, 17.89) * mm, "end": v(-206.64, 18.5) * mm});
            skLineSegment(sketch, "E1638", {"start": v(-206.64, 18.5) * mm, "end": v(-208.63, 18.8) * mm});
            skLineSegment(sketch, "E1639", {"start": v(-208.63, 18.8) * mm, "end": v(-210.25, 18.71) * mm});
            skLineSegment(sketch, "E1640", {"start": v(-210.25, 18.71) * mm, "end": v(-210.78, 18.6) * mm});
            skLineSegment(sketch, "E1641", {"start": v(-210.78, 18.6) * mm, "end": v(-211.02, 18.98) * mm});
            skLineSegment(sketch, "E1642", {"start": v(-211.02, 18.98) * mm, "end": v(-211.95, 20.01) * mm});
            skLineSegment(sketch, "E1643", {"start": v(-211.95, 20.01) * mm, "end": v(-213.34, 21.04) * mm});
            skLineSegment(sketch, "E1644", {"start": v(-213.34, 21.04) * mm, "end": v(-214.9, 21.77) * mm});
            skLineSegment(sketch, "E1645", {"start": v(-214.9, 21.77) * mm, "end": v(-216.58, 22.3) * mm});
            skLineSegment(sketch, "E1646", {"start": v(-216.58, 22.3) * mm, "end": v(-218.34, 22.74) * mm});
            skLineSegment(sketch, "E1647", {"start": v(-218.34, 22.74) * mm, "end": v(-220.12, 23.16) * mm});
            skLineSegment(sketch, "E1648", {"start": v(-220.12, 23.16) * mm, "end": v(-221.88, 23.66) * mm});
            skLineSegment(sketch, "E1649", {"start": v(-221.88, 23.66) * mm, "end": v(-223.15, 24.14) * mm});
            skLineSegment(sketch, "E1650", {"start": v(-223.15, 24.14) * mm, "end": v(-223.55, 24.33) * mm});
            skLineSegment(sketch, "E1651", {"start": v(-223.55, 24.33) * mm, "end": v(-224.05, 24.57) * mm});
            skLineSegment(sketch, "E1652", {"start": v(-224.05, 24.57) * mm, "end": v(-225.45, 25.4) * mm});
            skLineSegment(sketch, "E1653", {"start": v(-225.45, 25.4) * mm, "end": v(-227.15, 26.4) * mm});
            skLineSegment(sketch, "E1654", {"start": v(-227.15, 26.4) * mm, "end": v(-228.94, 27.02) * mm});
            skLineSegment(sketch, "E1655", {"start": v(-228.94, 27.02) * mm, "end": v(-230.6, 27.08) * mm});
            skLineSegment(sketch, "E1656", {"start": v(-230.6, 27.08) * mm, "end": v(-231.12, 26.98) * mm});
            skLineSegment(sketch, "E1657", {"start": v(-231.12, 26.98) * mm, "end": v(-231.34, 27.18) * mm});
            skLineSegment(sketch, "E1658", {"start": v(-231.34, 27.18) * mm, "end": v(-232.4, 28.4) * mm});
            skLineSegment(sketch, "E1659", {"start": v(-232.4, 28.4) * mm, "end": v(-233.37, 29.64) * mm});
            skLineSegment(sketch, "E1660", {"start": v(-233.37, 29.64) * mm, "end": v(-233.54, 29.86) * mm});
            skLineSegment(sketch, "E1661", {"start": v(-233.54, 29.86) * mm, "end": v(-233.74, 30.1) * mm});
            skLineSegment(sketch, "E1662", {"start": v(-233.74, 30.1) * mm, "end": v(-234.78, 31.22) * mm});
            skLineSegment(sketch, "E1663", {"start": v(-234.78, 31.22) * mm, "end": v(-235.95, 32.21) * mm});
            skLineSegment(sketch, "E1664", {"start": v(-235.95, 32.21) * mm, "end": v(-236.21, 32.37) * mm});
            skLineSegment(sketch, "E1665", {"start": v(-236.21, 32.37) * mm, "end": v(-236.42, 32.5) * mm});
            skLineSegment(sketch, "E1666", {"start": v(-236.42, 32.5) * mm, "end": v(-237.14, 32.77) * mm});
            skLineSegment(sketch, "E1667", {"start": v(-237.14, 32.77) * mm, "end": v(-238.1, 32.97) * mm});
            skLineSegment(sketch, "E1668", {"start": v(-238.1, 32.97) * mm, "end": v(-239.07, 33.15) * mm});
            skLineSegment(sketch, "E1669", {"start": v(-239.07, 33.15) * mm, "end": v(-239.76, 33.35) * mm});
            skLineSegment(sketch, "E1670", {"start": v(-239.76, 33.35) * mm, "end": v(-239.97, 33.46) * mm});
            skLineSegment(sketch, "E1671", {"start": v(-239.97, 33.46) * mm, "end": v(-240.3, 33.62) * mm});
            skLineSegment(sketch, "E1672", {"start": v(-240.3, 33.62) * mm, "end": v(-241.2, 34.25) * mm});
            skLineSegment(sketch, "E1673", {"start": v(-241.2, 34.25) * mm, "end": v(-242.35, 35.19) * mm});
            skLineSegment(sketch, "E1674", {"start": v(-242.35, 35.19) * mm, "end": v(-243.53, 36.07) * mm});
            skLineSegment(sketch, "E1675", {"start": v(-243.53, 36.07) * mm, "end": v(-244.48, 36.59) * mm});
            skLineSegment(sketch, "E1676", {"start": v(-244.48, 36.59) * mm, "end": v(-244.82, 36.7) * mm});
            skLineSegment(sketch, "E1677", {"start": v(-244.82, 36.7) * mm, "end": v(-245.33, 36.85) * mm});
            skLineSegment(sketch, "E1678", {"start": v(-245.33, 36.85) * mm, "end": v(-246.88, 37.18) * mm});
            skLineSegment(sketch, "E1679", {"start": v(-246.88, 37.18) * mm, "end": v(-249.02, 37.65) * mm});
            skLineSegment(sketch, "E1680", {"start": v(-249.02, 37.65) * mm, "end": v(-251.03, 38.36) * mm});
            skLineSegment(sketch, "E1681", {"start": v(-251.03, 38.36) * mm, "end": v(-252.38, 39.21) * mm});
            skLineSegment(sketch, "E1682", {"start": v(-252.38, 39.21) * mm, "end": v(-252.73, 39.59) * mm});
            skLineSegment(sketch, "E1683", {"start": v(-252.73, 39.59) * mm, "end": v(-253.4, 40.32) * mm});
            skLineSegment(sketch, "E1684", {"start": v(-253.4, 40.32) * mm, "end": v(-254.19, 39.68) * mm});
            skLineSegment(sketch, "E1685", {"start": v(-254.19, 39.68) * mm, "end": v(-254.24, 39.64) * mm});
            skLineSegment(sketch, "E1686", {"start": v(-254.24, 39.64) * mm, "end": v(-254.8, 39.33) * mm});
            skLineSegment(sketch, "E1687", {"start": v(-254.8, 39.33) * mm, "end": v(-254.87, 39.3) * mm});
            skLineSegment(sketch, "E1688", {"start": v(-254.87, 39.3) * mm, "end": v(-255.06, 39.23) * mm});
            skLineSegment(sketch, "E1689", {"start": v(-255.06, 39.23) * mm, "end": v(-256.13, 39.1) * mm});
            skLineSegment(sketch, "E1690", {"start": v(-256.13, 39.1) * mm, "end": v(-257.23, 39.12) * mm});
            skLineSegment(sketch, "E1691", {"start": v(-257.23, 39.12) * mm, "end": v(-257.42, 39.14) * mm});
            skLineSegment(sketch, "E1692", {"start": v(-257.42, 39.14) * mm, "end": v(-257.75, 39.16) * mm});
            skLineSegment(sketch, "E1693", {"start": v(-257.75, 39.16) * mm, "end": v(-259.34, 39.25) * mm});
            skLineSegment(sketch, "E1694", {"start": v(-259.34, 39.25) * mm, "end": v(-260.95, 39.25) * mm});
            skLineSegment(sketch, "E1695", {"start": v(-260.95, 39.25) * mm, "end": v(-261.27, 39.23) * mm});
            skLineSegment(sketch, "E1696", {"start": v(-261.27, 39.23) * mm, "end": v(-261.53, 39.23) * mm});
            skLineSegment(sketch, "E1697", {"start": v(-261.53, 39.23) * mm, "end": v(-262.32, 39.04) * mm});
            skLineSegment(sketch, "E1698", {"start": v(-262.32, 39.04) * mm, "end": v(-263.02, 38.58) * mm});
            skLineSegment(sketch, "E1699", {"start": v(-263.02, 38.58) * mm, "end": v(-263.5, 38.09) * mm});
            skLineSegment(sketch, "E1700", {"start": v(-263.5, 38.09) * mm, "end": v(-263.8, 37.83) * mm});
            skLineSegment(sketch, "E1701", {"start": v(-263.8, 37.83) * mm, "end": v(-263.9, 37.8) * mm});
            skLineSegment(sketch, "E1702", {"start": v(-263.9, 37.8) * mm, "end": v(-264.4, 37.88) * mm});
            skLineSegment(sketch, "E1703", {"start": v(-264.4, 37.88) * mm, "end": v(-269.44, 37.94) * mm});
            skLineSegment(sketch, "E1704", {"start": v(-269.44, 37.94) * mm, "end": v(-269.94, 37.9) * mm});
            skLineSegment(sketch, "E1705", {"start": v(-269.94, 37.9) * mm, "end": v(-270.71, 37.83) * mm});
            skLineSegment(sketch, "E1706", {"start": v(-270.71, 37.83) * mm, "end": v(-273, 37.55) * mm});
            skLineSegment(sketch, "E1707", {"start": v(-273, 37.55) * mm, "end": v(-276.36, 37.18) * mm});
            skLineSegment(sketch, "E1708", {"start": v(-276.36, 37.18) * mm, "end": v(-279.68, 37.13) * mm});
            skLineSegment(sketch, "E1709", {"start": v(-279.68, 37.13) * mm, "end": v(-281.93, 37.46) * mm});
            skLineSegment(sketch, "E1710", {"start": v(-281.93, 37.46) * mm, "end": v(-282.62, 37.72) * mm});
            skLineSegment(sketch, "E1711", {"start": v(-282.62, 37.72) * mm, "end": v(-283.25, 37.96) * mm});
            skLineSegment(sketch, "E1712", {"start": v(-283.25, 37.96) * mm, "end": v(-284.97, 39.14) * mm});
            skLineSegment(sketch, "E1713", {"start": v(-284.97, 39.14) * mm, "end": v(-287.21, 41.33) * mm});
            skLineSegment(sketch, "E1714", {"start": v(-287.21, 41.33) * mm, "end": v(-289.02, 43.9) * mm});
            skLineSegment(sketch, "E1715", {"start": v(-289.02, 43.9) * mm, "end": v(-289.9, 45.8) * mm});
            skLineSegment(sketch, "E1716", {"start": v(-289.9, 45.8) * mm, "end": v(-290.03, 46.46) * mm});
            skLineSegment(sketch, "E1717", {"start": v(-290.03, 46.46) * mm, "end": v(-290.2, 47.25) * mm});
            skLineSegment(sketch, "E1718", {"start": v(-290.2, 47.25) * mm, "end": v(-290.32, 49.69) * mm});
            skLineSegment(sketch, "E1719", {"start": v(-290.32, 49.69) * mm, "end": v(-290.16, 53.05) * mm});
            skLineSegment(sketch, "E1720", {"start": v(-290.16, 53.05) * mm, "end": v(-289.94, 56.44) * mm});
            skLineSegment(sketch, "E1721", {"start": v(-289.94, 56.44) * mm, "end": v(-289.93, 58.92) * mm});
            skLineSegment(sketch, "E1722", {"start": v(-289.93, 58.92) * mm, "end": v(-290.02, 59.74) * mm});
            skLineSegment(sketch, "E1723", {"start": v(-290.02, 59.74) * mm, "end": v(-290.07, 60.3) * mm});
            skLineSegment(sketch, "E1724", {"start": v(-290.07, 60.3) * mm, "end": v(-290.6, 60.58) * mm});
            skLineSegment(sketch, "E1725", {"start": v(-290.6, 60.58) * mm, "end": v(-290.89, 60.72) * mm});
            skLineSegment(sketch, "E1726", {"start": v(-290.89, 60.72) * mm, "end": v(-291.66, 61.39) * mm});
            skLineSegment(sketch, "E1727", {"start": v(-291.66, 61.39) * mm, "end": v(-292.51, 62.54) * mm});
            skLineSegment(sketch, "E1728", {"start": v(-292.51, 62.54) * mm, "end": v(-293.25, 63.92) * mm});
            skLineSegment(sketch, "E1729", {"start": v(-293.25, 63.92) * mm, "end": v(-293.97, 65.42) * mm});
            skLineSegment(sketch, "E1730", {"start": v(-293.97, 65.42) * mm, "end": v(-294.76, 66.9) * mm});
            skLineSegment(sketch, "E1731", {"start": v(-294.76, 66.9) * mm, "end": v(-295.71, 68.27) * mm});
            skLineSegment(sketch, "E1732", {"start": v(-295.71, 68.27) * mm, "end": v(-296.91, 69.39) * mm});
            skLineSegment(sketch, "E1733", {"start": v(-296.91, 69.39) * mm, "end": v(-298.06, 70.02) * mm});
            skLineSegment(sketch, "E1734", {"start": v(-298.06, 70.02) * mm, "end": v(-298.46, 70.15) * mm});
            skLineSegment(sketch, "E1735", {"start": v(-298.46, 70.15) * mm, "end": v(-298.85, 70.27) * mm});
            skLineSegment(sketch, "E1736", {"start": v(-298.85, 70.27) * mm, "end": v(-300.1, 70.36) * mm});
            skLineSegment(sketch, "E1737", {"start": v(-300.1, 70.36) * mm, "end": v(-301.8, 70.25) * mm});
            skLineSegment(sketch, "E1738", {"start": v(-301.8, 70.25) * mm, "end": v(-303.46, 70.2) * mm});
            skLineSegment(sketch, "E1739", {"start": v(-303.46, 70.2) * mm, "end": v(-304.63, 70.4) * mm});
            skLineSegment(sketch, "E1740", {"start": v(-304.63, 70.4) * mm, "end": v(-304.96, 70.58) * mm});
            skLineSegment(sketch, "E1741", {"start": v(-304.96, 70.58) * mm, "end": v(-305.32, 71.42) * mm});
            skLineSegment(sketch, "E1742", {"start": v(-305.32, 71.42) * mm, "end": v(-306.88, 73.75) * mm});
            skLineSegment(sketch, "E1743", {"start": v(-306.88, 73.75) * mm, "end": v(-309.37, 76.22) * mm});
            skLineSegment(sketch, "E1744", {"start": v(-309.37, 76.22) * mm, "end": v(-312.22, 78.36) * mm});
            skLineSegment(sketch, "E1745", {"start": v(-312.22, 78.36) * mm, "end": v(-314.47, 79.95) * mm});
            skLineSegment(sketch, "E1746", {"start": v(-314.47, 79.95) * mm, "end": v(-315.2, 80.51) * mm});
            skLineSegment(sketch, "E1747", {"start": v(-315.2, 80.51) * mm, "end": v(-315.4, 80.68) * mm});
            skLineSegment(sketch, "E1748", {"start": v(-315.4, 80.68) * mm, "end": v(-315.66, 80.73) * mm});
            skLineSegment(sketch, "E1749", {"start": v(-315.66, 80.73) * mm, "end": v(-316.1, 80.8) * mm});
            skLineSegment(sketch, "E1750", {"start": v(-316.1, 80.8) * mm, "end": v(-318.77, 80.7) * mm});
            skLineSegment(sketch, "E1751", {"start": v(-318.77, 80.7) * mm, "end": v(-321.49, 80.39) * mm});
            skLineSegment(sketch, "E1752", {"start": v(-321.49, 80.39) * mm, "end": v(-321.95, 80.36) * mm});
            skLineSegment(sketch, "E1753", {"start": v(-321.95, 80.36) * mm, "end": v(-322.1, 80.35) * mm});
            skLineSegment(sketch, "E1754", {"start": v(-322.1, 80.35) * mm, "end": v(-323.7, 80.35) * mm});
            skLineSegment(sketch, "E1755", {"start": v(-323.7, 80.35) * mm, "end": v(-323.85, 80.36) * mm});
            skLineSegment(sketch, "E1756", {"start": v(-323.85, 80.36) * mm, "end": v(-324.21, 80.62) * mm});
            skLineSegment(sketch, "E1757", {"start": v(-324.21, 80.62) * mm, "end": v(-325.12, 81.64) * mm});
            skLineSegment(sketch, "E1758", {"start": v(-325.12, 81.64) * mm, "end": v(-325.9, 83.25) * mm});
            skLineSegment(sketch, "E1759", {"start": v(-325.9, 83.25) * mm, "end": v(-326.27, 85.1) * mm});
            skLineSegment(sketch, "E1760", {"start": v(-326.27, 85.1) * mm, "end": v(-326.29, 87.06) * mm});
            skLineSegment(sketch, "E1761", {"start": v(-326.29, 87.06) * mm, "end": v(-326.03, 89.07) * mm});
            skLineSegment(sketch, "E1762", {"start": v(-326.03, 89.07) * mm, "end": v(-325.57, 91.02) * mm});
            skLineSegment(sketch, "E1763", {"start": v(-325.57, 91.02) * mm, "end": v(-324.96, 92.81) * mm});
            skLineSegment(sketch, "E1764", {"start": v(-324.96, 92.81) * mm, "end": v(-324.47, 93.97) * mm});
            skLineSegment(sketch, "E1765", {"start": v(-324.47, 93.97) * mm, "end": v(-324.29, 94.34) * mm});
            skLineSegment(sketch, "E1766", {"start": v(-324.29, 94.34) * mm, "end": v(-324.09, 94.75) * mm});
            skLineSegment(sketch, "E1767", {"start": v(-324.09, 94.75) * mm, "end": v(-322.8, 96.73) * mm});
            skLineSegment(sketch, "E1768", {"start": v(-322.8, 96.73) * mm, "end": v(-321.34, 98.6) * mm});
            skLineSegment(sketch, "E1769", {"start": v(-321.34, 98.6) * mm, "end": v(-321.04, 98.93) * mm});
            skLineSegment(sketch, "E1770", {"start": v(-321.04, 98.93) * mm, "end": v(-320.77, 99.25) * mm});
            skLineSegment(sketch, "E1771", {"start": v(-320.77, 99.25) * mm, "end": v(-319.86, 100.2) * mm});
            skLineSegment(sketch, "E1772", {"start": v(-319.86, 100.2) * mm, "end": v(-318.2, 101.79) * mm});
            skLineSegment(sketch, "E1773", {"start": v(-318.2, 101.79) * mm, "end": v(-316.45, 103.21) * mm});
            skLineSegment(sketch, "E1774", {"start": v(-316.45, 103.21) * mm, "end": v(-315.35, 103.88) * mm});
            skLineSegment(sketch, "E1775", {"start": v(-315.35, 103.88) * mm, "end": v(-314.96, 103.97) * mm});
            skLineSegment(sketch, "E1776", {"start": v(-314.96, 103.97) * mm, "end": v(-314.13, 104.15) * mm});
            skLineSegment(sketch, "E1777", {"start": v(-314.13, 104.15) * mm, "end": v(-311.53, 104.22) * mm});
            skLineSegment(sketch, "E1778", {"start": v(-311.53, 104.22) * mm, "end": v(-308.05, 103.88) * mm});
            skLineSegment(sketch, "E1779", {"start": v(-308.05, 103.88) * mm, "end": v(-304.5, 103.59) * mm});
            skLineSegment(sketch, "E1780", {"start": v(-304.5, 103.59) * mm, "end": v(-301.72, 103.76) * mm});
            skLineSegment(sketch, "E1781", {"start": v(-301.72, 103.76) * mm, "end": v(-300.84, 103.98) * mm});
            skLineSegment(sketch, "E1782", {"start": v(-300.84, 103.98) * mm, "end": v(-300.82, 103.98) * mm});
            skLineSegment(sketch, "E1783", {"start": v(-300.82, 103.98) * mm, "end": v(-300.8, 104) * mm});
            skLineSegment(sketch, "E1784", {"start": v(-300.8, 104) * mm, "end": v(-300.62, 104.05) * mm});
            skLineSegment(sketch, "E1785", {"start": v(-300.62, 104.05) * mm, "end": v(-300.11, 104.31) * mm});
            skLineSegment(sketch, "E1786", {"start": v(-300.11, 104.31) * mm, "end": v(-299.52, 104.74) * mm});
            skLineSegment(sketch, "E1787", {"start": v(-299.52, 104.74) * mm, "end": v(-298.97, 105.15) * mm});
            skLineSegment(sketch, "E1788", {"start": v(-298.97, 105.15) * mm, "end": v(-298.58, 105.38) * mm});
            skLineSegment(sketch, "E1789", {"start": v(-298.58, 105.38) * mm, "end": v(-298.43, 105.43) * mm});
            skLineSegment(sketch, "E1790", {"start": v(-298.43, 105.43) * mm, "end": v(-297.55, 105.74) * mm});
            skLineSegment(sketch, "E1791", {"start": v(-297.55, 105.74) * mm, "end": v(-294.81, 106.38) * mm});
            skLineSegment(sketch, "E1792", {"start": v(-294.81, 106.38) * mm, "end": v(-291.04, 107.03) * mm});
            skLineSegment(sketch, "E1793", {"start": v(-291.04, 107.03) * mm, "end": v(-287.33, 107.77) * mm});
            skLineSegment(sketch, "E1794", {"start": v(-287.33, 107.77) * mm, "end": v(-284.7, 108.59) * mm});
            skLineSegment(sketch, "E1795", {"start": v(-284.7, 108.59) * mm, "end": v(-283.87, 108.99) * mm});
            skLineSegment(sketch, "E1796", {"start": v(-283.87, 108.99) * mm, "end": v(-283.6, 109.13) * mm});
            skLineSegment(sketch, "E1797", {"start": v(-283.6, 109.13) * mm, "end": v(-282.81, 109.65) * mm});
            skLineSegment(sketch, "E1798", {"start": v(-282.81, 109.65) * mm, "end": v(-281.7, 110.53) * mm});
            skLineSegment(sketch, "E1799", {"start": v(-281.7, 110.53) * mm, "end": v(-280.6, 111.46) * mm});
            skLineSegment(sketch, "E1800", {"start": v(-280.6, 111.46) * mm, "end": v(-279.86, 112.09) * mm});
            skLineSegment(sketch, "E1801", {"start": v(-279.86, 112.09) * mm, "end": v(-279.6, 112.29) * mm});
            skLineSegment(sketch, "E1802", {"start": v(-279.6, 112.29) * mm, "end": v(-279.53, 112.35) * mm});
            skLineSegment(sketch, "E1803", {"start": v(-279.53, 112.35) * mm, "end": v(-278.77, 112.9) * mm});
            skLineSegment(sketch, "E1804", {"start": v(-278.77, 112.9) * mm, "end": v(-278.69, 112.96) * mm});
            skLineSegment(sketch, "E1805", {"start": v(-278.69, 112.96) * mm, "end": v(-278.26, 113.28) * mm});
            skLineSegment(sketch, "E1806", {"start": v(-278.26, 113.28) * mm, "end": v(-275.92, 114.73) * mm});
            skLineSegment(sketch, "E1807", {"start": v(-275.92, 114.73) * mm, "end": v(-273.66, 116.22) * mm});
            skLineSegment(sketch, "E1808", {"start": v(-273.66, 116.22) * mm, "end": v(-273.26, 116.55) * mm});
            skLineSegment(sketch, "E1809", {"start": v(-273.26, 116.55) * mm, "end": v(-273.06, 116.72) * mm});
            skLineSegment(sketch, "E1810", {"start": v(-273.06, 116.72) * mm, "end": v(-272.2, 117.57) * mm});
            skLineSegment(sketch, "E1811", {"start": v(-272.2, 117.57) * mm, "end": v(-271.39, 118.48) * mm});
            skLineSegment(sketch, "E1812", {"start": v(-271.39, 118.48) * mm, "end": v(-271.23, 118.68) * mm});
            skLineSegment(sketch, "E1813", {"start": v(-271.23, 118.68) * mm, "end": v(-271.14, 118.78) * mm});
            skLineSegment(sketch, "E1814", {"start": v(-271.14, 118.78) * mm, "end": v(-270.66, 119.33) * mm});
            skLineSegment(sketch, "E1815", {"start": v(-270.66, 119.33) * mm, "end": v(-270.13, 119.83) * mm});
            skLineSegment(sketch, "E1816", {"start": v(-270.13, 119.83) * mm, "end": v(-270.01, 119.9) * mm});
            skLineSegment(sketch, "E1817", {"start": v(-270.01, 119.9) * mm, "end": v(-269.94, 119.95) * mm});
            skLineSegment(sketch, "E1818", {"start": v(-269.94, 119.95) * mm, "end": v(-269.24, 120.17) * mm});
            skLineSegment(sketch, "E1819", {"start": v(-269.24, 120.17) * mm, "end": v(-269.15, 120.17) * mm});
            skLineSegment(sketch, "E1820", {"start": v(-269.15, 120.17) * mm, "end": v(-268.9, 120.19) * mm});
            skLineSegment(sketch, "E1821", {"start": v(-268.9, 120.19) * mm, "end": v(-267.76, 119.89) * mm});
            skLineSegment(sketch, "E1822", {"start": v(-267.76, 119.89) * mm, "end": v(-265.62, 119.16) * mm});
            skLineSegment(sketch, "E1823", {"start": v(-265.62, 119.16) * mm, "end": v(-263.45, 118.34) * mm});
            skLineSegment(sketch, "E1824", {"start": v(-263.45, 118.34) * mm, "end": v(-262.25, 117.87) * mm});
            skLineSegment(sketch, "E1825", {"start": v(-262.25, 117.87) * mm, "end": v(-261.93, 117.76) * mm});
            skLineSegment(sketch, "E1826", {"start": v(-261.93, 117.76) * mm, "end": v(-260.2, 117.13) * mm});
            skLineSegment(sketch, "E1827", {"start": v(-260.2, 117.13) * mm, "end": v(-255.05, 115.26) * mm});
            skLineSegment(sketch, "E1828", {"start": v(-255.05, 115.26) * mm, "end": v(-248.17, 113.19) * mm});
            skLineSegment(sketch, "E1829", {"start": v(-248.17, 113.19) * mm, "end": v(-241.14, 112.05) * mm});
            skLineSegment(sketch, "E1830", {"start": v(-241.14, 112.05) * mm, "end": v(-235.6, 112.05) * mm});
            skLineSegment(sketch, "E1831", {"start": v(-235.6, 112.05) * mm, "end": v(-233.8, 112.33) * mm});
            skLineSegment(sketch, "E1832", {"start": v(-233.8, 112.33) * mm, "end": v(-232.57, 111.08) * mm});
            skLineSegment(sketch, "E1833", {"start": v(-232.57, 111.08) * mm, "end": v(-228.43, 107.76) * mm});
            skLineSegment(sketch, "E1834", {"start": v(-228.43, 107.76) * mm, "end": v(-222.57, 103.85) * mm});
            skLineSegment(sketch, "E1835", {"start": v(-222.57, 103.85) * mm, "end": v(-216.6, 100.09) * mm});
            skLineSegment(sketch, "E1836", {"start": v(-216.6, 100.09) * mm, "end": v(-212.25, 97.08) * mm});
            skLineSegment(sketch, "E1837", {"start": v(-212.25, 97.08) * mm, "end": v(-210.89, 95.97) * mm});
            skLineSegment(sketch, "E1838", {"start": v(-210.89, 95.97) * mm, "end": v(-210.81, 95.73) * mm});
            skLineSegment(sketch, "E1839", {"start": v(-210.81, 95.73) * mm, "end": v(-210.05, 93.35) * mm});
            skLineSegment(sketch, "E1840", {"start": v(-210.05, 93.35) * mm, "end": v(-209.97, 93.12) * mm});
            skLineSegment(sketch, "E1841", {"start": v(-209.97, 93.12) * mm, "end": v(-209.87, 92.78) * mm});
            skLineSegment(sketch, "E1842", {"start": v(-209.87, 92.78) * mm, "end": v(-209.6, 92.57) * mm});
            skLineSegment(sketch, "E1843", {"start": v(-209.6, 92.57) * mm, "end": v(-209.32, 92.37) * mm});
            skLineSegment(sketch, "E1844", {"start": v(-209.32, 92.37) * mm, "end": v(-208.47, 91.83) * mm});
            skLineSegment(sketch, "E1845", {"start": v(-208.47, 91.83) * mm, "end": v(-207.27, 91.06) * mm});
            skLineSegment(sketch, "E1846", {"start": v(-207.27, 91.06) * mm, "end": v(-206.15, 90.2) * mm});
            skLineSegment(sketch, "E1847", {"start": v(-206.15, 90.2) * mm, "end": v(-205.43, 89.46) * mm});
            skLineSegment(sketch, "E1848", {"start": v(-205.43, 89.46) * mm, "end": v(-205.25, 89.18) * mm});
            skLineSegment(sketch, "E1849", {"start": v(-205.25, 89.18) * mm, "end": v(-205.66, 88.81) * mm});
            skLineSegment(sketch, "E1850", {"start": v(-205.66, 88.81) * mm, "end": v(-206.58, 87.37) * mm});
            skLineSegment(sketch, "E1851", {"start": v(-206.58, 87.37) * mm, "end": v(-207.18, 85.15) * mm});
            skLineSegment(sketch, "E1852", {"start": v(-207.18, 85.15) * mm, "end": v(-207.03, 82.87) * mm});
            skLineSegment(sketch, "E1853", {"start": v(-207.03, 82.87) * mm, "end": v(-206.42, 81.27) * mm});
            skLineSegment(sketch, "E1854", {"start": v(-206.42, 81.27) * mm, "end": v(-206.1, 80.83) * mm});
            skLineSegment(sketch, "E1855", {"start": v(-206.1, 80.83) * mm, "end": v(-205.74, 80.35) * mm});
            skLineSegment(sketch, "E1856", {"start": v(-205.74, 80.35) * mm, "end": v(-205.15, 80.4) * mm});
            skLineSegment(sketch, "E1857", {"start": v(-205.15, 80.4) * mm, "end": v(-204.74, 80.43) * mm});
            skLineSegment(sketch, "E1858", {"start": v(-204.74, 80.43) * mm, "end": v(-203.53, 80.65) * mm});
            skLineSegment(sketch, "E1859", {"start": v(-203.53, 80.65) * mm, "end": v(-201.55, 81.08) * mm});
            skLineSegment(sketch, "E1860", {"start": v(-201.55, 81.08) * mm, "end": v(-199.36, 81.56) * mm});
            skLineSegment(sketch, "E1861", {"start": v(-199.36, 81.56) * mm, "end": v(-197.09, 81.97) * mm});
            skLineSegment(sketch, "E1862", {"start": v(-197.09, 81.97) * mm, "end": v(-194.85, 82.19) * mm});
            skLineSegment(sketch, "E1863", {"start": v(-194.85, 82.19) * mm, "end": v(-192.8, 82.07) * mm});
            skLineSegment(sketch, "E1864", {"start": v(-192.8, 82.07) * mm, "end": v(-191.04, 81.5) * mm});
            skLineSegment(sketch, "E1865", {"start": v(-191.04, 81.5) * mm, "end": v(-189.98, 80.68) * mm});
            skLineSegment(sketch, "E1866", {"start": v(-189.98, 80.68) * mm, "end": v(-189.73, 80.33) * mm});
            skLineSegment(sketch, "E1867", {"start": v(-189.73, 80.33) * mm, "end": v(-189.97, 79.89) * mm});
            skLineSegment(sketch, "E1868", {"start": v(-189.97, 79.89) * mm, "end": v(-190.94, 78.68) * mm});
            skLineSegment(sketch, "E1869", {"start": v(-190.94, 78.68) * mm, "end": v(-192.46, 77.14) * mm});
            skLineSegment(sketch, "E1870", {"start": v(-192.46, 77.14) * mm, "end": v(-194.02, 75.58) * mm});
            skLineSegment(sketch, "E1871", {"start": v(-194.02, 75.58) * mm, "end": v(-195.05, 74.32) * mm});
            skLineSegment(sketch, "E1872", {"start": v(-195.05, 74.32) * mm, "end": v(-195.32, 73.86) * mm});
            skLineSegment(sketch, "E1873", {"start": v(-195.32, 73.86) * mm, "end": v(-195.52, 73.5) * mm});
            skLineSegment(sketch, "E1874", {"start": v(-195.52, 73.5) * mm, "end": v(-196.17, 71.7) * mm});
            skLineSegment(sketch, "E1875", {"start": v(-196.17, 71.7) * mm, "end": v(-196.3, 69.78) * mm});
            skLineSegment(sketch, "E1876", {"start": v(-196.3, 69.78) * mm, "end": v(-196.26, 69.38) * mm});
            skLineSegment(sketch, "E1877", {"start": v(-196.26, 69.38) * mm, "end": v(-196.2, 68.75) * mm});
            skLineSegment(sketch, "E1878", {"start": v(-196.2, 68.75) * mm, "end": v(-195.6, 68.5) * mm});
            skLineSegment(sketch, "E1879", {"start": v(-195.6, 68.5) * mm, "end": v(-194.92, 68.23) * mm});
            skLineSegment(sketch, "E1880", {"start": v(-194.92, 68.23) * mm, "end": v(-192.7, 67.82) * mm});
            skLineSegment(sketch, "E1881", {"start": v(-192.7, 67.82) * mm, "end": v(-190.07, 68.1) * mm});
            skLineSegment(sketch, "E1882", {"start": v(-190.07, 68.1) * mm, "end": v(-187.62, 69.03) * mm});
            skLineSegment(sketch, "E1883", {"start": v(-187.62, 69.03) * mm, "end": v(-185.26, 70.36) * mm});
            skLineSegment(sketch, "E1884", {"start": v(-185.26, 70.36) * mm, "end": v(-182.92, 71.8) * mm});
            skLineSegment(sketch, "E1885", {"start": v(-182.92, 71.8) * mm, "end": v(-180.51, 73.05) * mm});
            skLineSegment(sketch, "E1886", {"start": v(-180.51, 73.05) * mm, "end": v(-177.96, 73.84) * mm});
            skLineSegment(sketch, "E1887", {"start": v(-177.96, 73.84) * mm, "end": v(-175.86, 73.98) * mm});
            skLineSegment(sketch, "E1888", {"start": v(-175.86, 73.98) * mm, "end": v(-175.17, 73.88) * mm});
            skLineSegment(sketch, "E1889", {"start": v(-175.17, 73.88) * mm, "end": v(-175.2, 73.31) * mm});
            skLineSegment(sketch, "E1890", {"start": v(-175.2, 73.31) * mm, "end": v(-175.52, 71.6) * mm});
            skLineSegment(sketch, "E1891", {"start": v(-175.52, 71.6) * mm, "end": v(-176.26, 69.8) * mm});
            skLineSegment(sketch, "E1892", {"start": v(-176.26, 69.8) * mm, "end": v(-177.34, 68.33) * mm});
            skLineSegment(sketch, "E1893", {"start": v(-177.34, 68.33) * mm, "end": v(-178.7, 67.13) * mm});
            skLineSegment(sketch, "E1894", {"start": v(-178.7, 67.13) * mm, "end": v(-180.28, 66.1) * mm});
            skLineSegment(sketch, "E1895", {"start": v(-180.28, 66.1) * mm, "end": v(-182.02, 65.12) * mm});
            skLineSegment(sketch, "E1896", {"start": v(-182.02, 65.12) * mm, "end": v(-183.85, 64.1) * mm});
            skLineSegment(sketch, "E1897", {"start": v(-183.85, 64.1) * mm, "end": v(-185.27, 63.26) * mm});
            skLineSegment(sketch, "E1898", {"start": v(-185.27, 63.26) * mm, "end": v(-185.72, 62.96) * mm});
            skLineSegment(sketch, "E1899", {"start": v(-185.72, 62.96) * mm, "end": v(-186.02, 62.77) * mm});
            skLineSegment(sketch, "E1900", {"start": v(-186.02, 62.77) * mm, "end": v(-186.93, 62.26) * mm});
            skLineSegment(sketch, "E1901", {"start": v(-186.93, 62.26) * mm, "end": v(-188.23, 61.6) * mm});
            skLineSegment(sketch, "E1902", {"start": v(-188.23, 61.6) * mm, "end": v(-189.55, 60.9) * mm});
            skLineSegment(sketch, "E1903", {"start": v(-189.55, 60.9) * mm, "end": v(-190.8, 60.15) * mm});
            skLineSegment(sketch, "E1904", {"start": v(-190.8, 60.15) * mm, "end": v(-191.91, 59.27) * mm});
            skLineSegment(sketch, "E1905", {"start": v(-191.91, 59.27) * mm, "end": v(-192.8, 58.22) * mm});
            skLineSegment(sketch, "E1906", {"start": v(-192.8, 58.22) * mm, "end": v(-193.37, 56.94) * mm});
            skLineSegment(sketch, "E1907", {"start": v(-193.37, 56.94) * mm, "end": v(-193.57, 55.77) * mm});
            skLineSegment(sketch, "E1908", {"start": v(-193.57, 55.77) * mm, "end": v(-193.57, 55.38) * mm});
            skLineSegment(sketch, "E1909", {"start": v(-193.57, 55.38) * mm, "end": v(-193.55, 54.57) * mm});
            skLineSegment(sketch, "E1910", {"start": v(-193.55, 54.57) * mm, "end": v(-192.75, 54.37) * mm});
            skLineSegment(sketch, "E1911", {"start": v(-192.75, 54.37) * mm, "end": v(-191.83, 54.15) * mm});
            skLineSegment(sketch, "E1912", {"start": v(-191.83, 54.15) * mm, "end": v(-188.88, 54.4) * mm});
            skLineSegment(sketch, "E1913", {"start": v(-188.88, 54.4) * mm, "end": v(-185.3, 55.85) * mm});
            skLineSegment(sketch, "E1914", {"start": v(-185.3, 55.85) * mm, "end": v(-181.85, 57.9) * mm});
            skLineSegment(sketch, "E1915", {"start": v(-181.85, 57.9) * mm, "end": v(-179.29, 59.33) * mm});
            skLineSegment(sketch, "E1916", {"start": v(-179.29, 59.33) * mm, "end": v(-178.39, 59.67) * mm});
            skLineSegment(sketch, "E1917", {"start": v(-178.39, 59.67) * mm, "end": v(-177.3, 60.1) * mm});
            skLineSegment(sketch, "E1918", {"start": v(-177.3, 60.1) * mm, "end": v(-171.67, 61.73) * mm});
            skLineSegment(sketch, "E1919", {"start": v(-171.67, 61.73) * mm, "end": v(-165.9, 62.75) * mm});
            skLineSegment(sketch, "E1920", {"start": v(-165.9, 62.75) * mm, "end": v(-164.73, 62.87) * mm});
            skLineSegment(sketch, "E1921", {"start": v(-164.73, 62.87) * mm, "end": v(-164.38, 62.92) * mm});
            skLineSegment(sketch, "E1922", {"start": v(-164.38, 62.92) * mm, "end": v(-163.44, 63.08) * mm});
            skLineSegment(sketch, "E1923", {"start": v(-163.44, 63.08) * mm, "end": v(-162.09, 63.36) * mm});
            skLineSegment(sketch, "E1924", {"start": v(-162.09, 63.36) * mm, "end": v(-160.5, 63.78) * mm});
            skLineSegment(sketch, "E1925", {"start": v(-160.5, 63.78) * mm, "end": v(-158.85, 64.37) * mm});
            skLineSegment(sketch, "E1926", {"start": v(-158.85, 64.37) * mm, "end": v(-157.31, 65.13) * mm});
            skLineSegment(sketch, "E1927", {"start": v(-157.31, 65.13) * mm, "end": v(-156.06, 66.1) * mm});
            skLineSegment(sketch, "E1928", {"start": v(-156.06, 66.1) * mm, "end": v(-155.4, 66.95) * mm});
            skLineSegment(sketch, "E1929", {"start": v(-155.4, 66.95) * mm, "end": v(-155.27, 67.27) * mm});
            skLineSegment(sketch, "E1930", {"start": v(-155.27, 67.27) * mm, "end": v(-155.05, 67.83) * mm});
            skLineSegment(sketch, "E1931", {"start": v(-155.05, 67.83) * mm, "end": v(-154.62, 69.62) * mm});
            skLineSegment(sketch, "E1932", {"start": v(-154.62, 69.62) * mm, "end": v(-154.47, 71.43) * mm});
            skLineSegment(sketch, "E1933", {"start": v(-154.47, 71.43) * mm, "end": v(-154.57, 72.59) * mm});
            skLineSegment(sketch, "E1934", {"start": v(-154.57, 72.59) * mm, "end": v(-154.66, 73) * mm});
            skLineSegment(sketch, "E1935", {"start": v(276.9, 138.1) * mm, "end": v(272.52, 138.91) * mm});
            skLineSegment(sketch, "E1936", {"start": v(272.52, 138.91) * mm, "end": v(250.67, 143.53) * mm});
            skLineSegment(sketch, "E1937", {"start": v(250.67, 143.53) * mm, "end": v(229, 148.88) * mm});
            skLineSegment(sketch, "E1938", {"start": v(229, 148.88) * mm, "end": v(224.7, 150.05) * mm});
            skLineSegment(sketch, "E1939", {"start": v(224.7, 150.05) * mm, "end": v(223.4, 150.4) * mm});
            skLineSegment(sketch, "E1940", {"start": v(223.4, 150.4) * mm, "end": v(219.53, 151.39) * mm});
            skLineSegment(sketch, "E1941", {"start": v(219.53, 151.39) * mm, "end": v(213.91, 152.92) * mm});
            skLineSegment(sketch, "E1942", {"start": v(213.91, 152.92) * mm, "end": v(208.5, 154.84) * mm});
            skLineSegment(sketch, "E1943", {"start": v(208.5, 154.84) * mm, "end": v(204.96, 156.58) * mm});
            skLineSegment(sketch, "E1944", {"start": v(204.96, 156.58) * mm, "end": v(203.9, 157.34) * mm});
            skLineSegment(sketch, "E1945", {"start": v(203.9, 157.34) * mm, "end": v(203.67, 157.5) * mm});
            skLineSegment(sketch, "E1946", {"start": v(203.67, 157.5) * mm, "end": v(203.03, 158.1) * mm});
            skLineSegment(sketch, "E1947", {"start": v(203.03, 158.1) * mm, "end": v(202.26, 158.96) * mm});
            skLineSegment(sketch, "E1948", {"start": v(202.26, 158.96) * mm, "end": v(201.46, 159.82) * mm});
            skLineSegment(sketch, "E1949", {"start": v(201.46, 159.82) * mm, "end": v(200.74, 160.4) * mm});
            skLineSegment(sketch, "E1950", {"start": v(200.74, 160.4) * mm, "end": v(200.47, 160.55) * mm});
            skLineSegment(sketch, "E1951", {"start": v(200.47, 160.55) * mm, "end": v(200.01, 160.8) * mm});
            skLineSegment(sketch, "E1952", {"start": v(200.01, 160.8) * mm, "end": v(197.59, 161.5) * mm});
            skLineSegment(sketch, "E1953", {"start": v(197.59, 161.5) * mm, "end": v(195.16, 162.13) * mm});
            skLineSegment(sketch, "E1954", {"start": v(195.16, 162.13) * mm, "end": v(194.7, 162.34) * mm});
            skLineSegment(sketch, "E1955", {"start": v(194.7, 162.34) * mm, "end": v(192.26, 163.44) * mm});
            skLineSegment(sketch, "E1956", {"start": v(192.26, 163.44) * mm, "end": v(184.82, 166.46) * mm});
            skLineSegment(sketch, "E1957", {"start": v(184.82, 166.46) * mm, "end": v(174.63, 169.98) * mm});
            skLineSegment(sketch, "E1958", {"start": v(174.63, 169.98) * mm, "end": v(164.23, 172.77) * mm});
            skLineSegment(sketch, "E1959", {"start": v(164.23, 172.77) * mm, "end": v(156.36, 174.34) * mm});
            skLineSegment(sketch, "E1960", {"start": v(156.36, 174.34) * mm, "end": v(153.72, 174.71) * mm});
            skLineSegment(sketch, "E1961", {"start": v(153.72, 174.71) * mm, "end": v(152.8, 175.25) * mm});
            skLineSegment(sketch, "E1962", {"start": v(152.8, 175.25) * mm, "end": v(150.13, 177) * mm});
            skLineSegment(sketch, "E1963", {"start": v(150.13, 177) * mm, "end": v(147, 179.61) * mm});
            skLineSegment(sketch, "E1964", {"start": v(147, 179.61) * mm, "end": v(144.45, 182.77) * mm});
            skLineSegment(sketch, "E1965", {"start": v(144.45, 182.77) * mm, "end": v(142.99, 185.66) * mm});
            skLineSegment(sketch, "E1966", {"start": v(142.99, 185.66) * mm, "end": v(142.67, 186.68) * mm});
            skLineSegment(sketch, "E1967", {"start": v(142.67, 186.68) * mm, "end": v(142.44, 187.36) * mm});
            skLineSegment(sketch, "E1968", {"start": v(142.44, 187.36) * mm, "end": v(141.73, 187.43) * mm});
            skLineSegment(sketch, "E1969", {"start": v(141.73, 187.43) * mm, "end": v(141.49, 187.45) * mm});
            skLineSegment(sketch, "E1970", {"start": v(141.49, 187.45) * mm, "end": v(139.2, 187.34) * mm});
            skLineSegment(sketch, "E1971", {"start": v(139.2, 187.34) * mm, "end": v(138.95, 187.3) * mm});
            skLineSegment(sketch, "E1972", {"start": v(138.95, 187.3) * mm, "end": v(138.8, 187.3) * mm});
            skLineSegment(sketch, "E1973", {"start": v(138.8, 187.3) * mm, "end": v(138.03, 187.21) * mm});
            skLineSegment(sketch, "E1974", {"start": v(138.03, 187.21) * mm, "end": v(137.25, 187.21) * mm});
            skLineSegment(sketch, "E1975", {"start": v(137.25, 187.21) * mm, "end": v(137.1, 187.23) * mm});
            skLineSegment(sketch, "E1976", {"start": v(137.1, 187.23) * mm, "end": v(137.02, 187.24) * mm});
            skLineSegment(sketch, "E1977", {"start": v(137.02, 187.24) * mm, "end": v(136.27, 187.55) * mm});
            skLineSegment(sketch, "E1978", {"start": v(136.27, 187.55) * mm, "end": v(136.2, 187.6) * mm});
            skLineSegment(sketch, "E1979", {"start": v(136.2, 187.6) * mm, "end": v(135.45, 188.12) * mm});
            skLineSegment(sketch, "E1980", {"start": v(135.45, 188.12) * mm, "end": v(134.82, 187.45) * mm});
            skLineSegment(sketch, "E1981", {"start": v(134.82, 187.45) * mm, "end": v(134.6, 187.22) * mm});
            skLineSegment(sketch, "E1982", {"start": v(134.6, 187.22) * mm, "end": v(133.47, 186.27) * mm});
            skLineSegment(sketch, "E1983", {"start": v(133.47, 186.27) * mm, "end": v(132.19, 185.5) * mm});
            skLineSegment(sketch, "E1984", {"start": v(132.19, 185.5) * mm, "end": v(131.9, 185.39) * mm});
            skLineSegment(sketch, "E1985", {"start": v(131.9, 185.39) * mm, "end": v(131.4, 185.17) * mm});
            skLineSegment(sketch, "E1986", {"start": v(131.4, 185.17) * mm, "end": v(128.7, 184.55) * mm});
            skLineSegment(sketch, "E1987", {"start": v(128.7, 184.55) * mm, "end": v(126.21, 184.37) * mm});
            skLineSegment(sketch, "E1988", {"start": v(126.21, 184.37) * mm, "end": v(125.38, 184.37) * mm});
            skLineSegment(sketch, "E1989", {"start": v(125.38, 184.37) * mm, "end": v(123.25, 184.37) * mm});
            skLineSegment(sketch, "E1990", {"start": v(123.25, 184.37) * mm, "end": v(117.56, 184.58) * mm});
            skLineSegment(sketch, "E1991", {"start": v(117.56, 184.58) * mm, "end": v(116.85, 184.58) * mm});
            skLineSegment(sketch, "E1992", {"start": v(116.85, 184.58) * mm, "end": v(116.05, 184.58) * mm});
            skLineSegment(sketch, "E1993", {"start": v(116.05, 184.58) * mm, "end": v(113.64, 184.45) * mm});
            skLineSegment(sketch, "E1994", {"start": v(113.64, 184.45) * mm, "end": v(110.33, 184.2) * mm});
            skLineSegment(sketch, "E1995", {"start": v(110.33, 184.2) * mm, "end": v(107.04, 184.06) * mm});
            skLineSegment(sketch, "E1996", {"start": v(107.04, 184.06) * mm, "end": v(104.69, 184.15) * mm});
            skLineSegment(sketch, "E1997", {"start": v(104.69, 184.15) * mm, "end": v(103.92, 184.27) * mm});
            skLineSegment(sketch, "E1998", {"start": v(103.92, 184.27) * mm, "end": v(102.79, 184.43) * mm});
            skLineSegment(sketch, "E1999", {"start": v(102.79, 184.43) * mm, "end": v(99.45, 185.15) * mm});
            skLineSegment(sketch, "E2000", {"start": v(99.45, 185.15) * mm, "end": v(95, 186.29) * mm});
            skLineSegment(sketch, "E2001", {"start": v(95, 186.29) * mm, "end": v(90.53, 187.3) * mm});
            skLineSegment(sketch, "E2002", {"start": v(90.53, 187.3) * mm, "end": v(87.15, 187.76) * mm});
            skLineSegment(sketch, "E2003", {"start": v(87.15, 187.76) * mm, "end": v(86.02, 187.78) * mm});
            skLineSegment(sketch, "E2004", {"start": v(86.02, 187.78) * mm, "end": v(85.48, 187.8) * mm});
            skLineSegment(sketch, "E2005", {"start": v(85.48, 187.8) * mm, "end": v(85.16, 187.38) * mm});
            skLineSegment(sketch, "E2006", {"start": v(85.16, 187.38) * mm, "end": v(84.85, 187) * mm});
            skLineSegment(sketch, "E2007", {"start": v(84.85, 187) * mm, "end": v(83.58, 185) * mm});
            skLineSegment(sketch, "E2008", {"start": v(83.58, 185) * mm, "end": v(82.52, 182.88) * mm});
            skLineSegment(sketch, "E2009", {"start": v(82.52, 182.88) * mm, "end": v(82.33, 182.44) * mm});
            skLineSegment(sketch, "E2010", {"start": v(82.33, 182.44) * mm, "end": v(82.16, 182.08) * mm});
            skLineSegment(sketch, "E2011", {"start": v(82.16, 182.08) * mm, "end": v(81.3, 180.23) * mm});
            skLineSegment(sketch, "E2012", {"start": v(81.3, 180.23) * mm, "end": v(80.32, 178.47) * mm});
            skLineSegment(sketch, "E2013", {"start": v(80.32, 178.47) * mm, "end": v(80.08, 178.15) * mm});
            skLineSegment(sketch, "E2014", {"start": v(80.08, 178.15) * mm, "end": v(79.85, 177.82) * mm});
            skLineSegment(sketch, "E2015", {"start": v(79.85, 177.82) * mm, "end": v(78.52, 176.5) * mm});
            skLineSegment(sketch, "E2016", {"start": v(78.52, 176.5) * mm, "end": v(76.92, 175.53) * mm});
            skLineSegment(sketch, "E2017", {"start": v(76.92, 175.53) * mm, "end": v(76.56, 175.38) * mm});
            skLineSegment(sketch, "E2018", {"start": v(76.56, 175.38) * mm, "end": v(75.8, 175.08) * mm});
            skLineSegment(sketch, "E2019", {"start": v(75.8, 175.08) * mm, "end": v(73.33, 174.61) * mm});
            skLineSegment(sketch, "E2020", {"start": v(73.33, 174.61) * mm, "end": v(69.64, 174.41) * mm});
            skLineSegment(sketch, "E2021", {"start": v(69.64, 174.41) * mm, "end": v(65.9, 174.56) * mm});
            skLineSegment(sketch, "E2022", {"start": v(65.9, 174.56) * mm, "end": v(63.39, 174.76) * mm});
            skLineSegment(sketch, "E2023", {"start": v(63.39, 174.76) * mm, "end": v(62.55, 174.83) * mm});
            skLineSegment(sketch, "E2024", {"start": v(62.55, 174.83) * mm, "end": v(61.63, 174.9) * mm});
            skLineSegment(sketch, "E2025", {"start": v(61.63, 174.9) * mm, "end": v(56.8, 175.26) * mm});
            skLineSegment(sketch, "E2026", {"start": v(56.8, 175.26) * mm, "end": v(51.94, 175.26) * mm});
            skLineSegment(sketch, "E2027", {"start": v(51.94, 175.26) * mm, "end": v(51.01, 175.15) * mm});
            skLineSegment(sketch, "E2028", {"start": v(51.01, 175.15) * mm, "end": v(49.8, 175.8) * mm});
            skLineSegment(sketch, "E2029", {"start": v(49.8, 175.8) * mm, "end": v(45.9, 177.24) * mm});
            skLineSegment(sketch, "E2030", {"start": v(45.9, 177.24) * mm, "end": v(40.53, 178.72) * mm});
            skLineSegment(sketch, "E2031", {"start": v(40.53, 178.72) * mm, "end": v(35.2, 180.23) * mm});
            skLineSegment(sketch, "E2032", {"start": v(35.2, 180.23) * mm, "end": v(31.38, 181.7) * mm});
            skLineSegment(sketch, "E2033", {"start": v(31.38, 181.7) * mm, "end": v(30.2, 182.37) * mm});
            skLineSegment(sketch, "E2034", {"start": v(30.2, 182.37) * mm, "end": v(29.57, 182.73) * mm});
            skLineSegment(sketch, "E2035", {"start": v(29.57, 182.73) * mm, "end": v(29, 182.25) * mm});
            skLineSegment(sketch, "E2036", {"start": v(29, 182.25) * mm, "end": v(28.22, 181.6) * mm});
            skLineSegment(sketch, "E2037", {"start": v(28.22, 181.6) * mm, "end": v(26.13, 179.36) * mm});
            skLineSegment(sketch, "E2038", {"start": v(26.13, 179.36) * mm, "end": v(23.84, 176.07) * mm});
            skLineSegment(sketch, "E2039", {"start": v(23.84, 176.07) * mm, "end": v(22.05, 172.47) * mm});
            skLineSegment(sketch, "E2040", {"start": v(22.05, 172.47) * mm, "end": v(21, 169.6) * mm});
            skLineSegment(sketch, "E2041", {"start": v(21, 169.6) * mm, "end": v(20.73, 168.62) * mm});
            skLineSegment(sketch, "E2042", {"start": v(20.73, 168.62) * mm, "end": v(20.34, 168.28) * mm});
            skLineSegment(sketch, "E2043", {"start": v(20.34, 168.28) * mm, "end": v(19.34, 167.06) * mm});
            skLineSegment(sketch, "E2044", {"start": v(19.34, 167.06) * mm, "end": v(18.3, 165.4) * mm});
            skLineSegment(sketch, "E2045", {"start": v(18.3, 165.4) * mm, "end": v(17.35, 163.72) * mm});
            skLineSegment(sketch, "E2046", {"start": v(17.35, 163.72) * mm, "end": v(16.49, 162.46) * mm});
            skLineSegment(sketch, "E2047", {"start": v(16.49, 162.46) * mm, "end": v(16.15, 162.08) * mm});
            skLineSegment(sketch, "E2048", {"start": v(16.15, 162.08) * mm, "end": v(15.3, 161.1) * mm});
            skLineSegment(sketch, "E2049", {"start": v(15.3, 161.1) * mm, "end": v(12.53, 158.34) * mm});
            skLineSegment(sketch, "E2050", {"start": v(12.53, 158.34) * mm, "end": v(8.68, 154.82) * mm});
            skLineSegment(sketch, "E2051", {"start": v(8.68, 154.82) * mm, "end": v(4.8, 151.33) * mm});
            skLineSegment(sketch, "E2052", {"start": v(4.8, 151.33) * mm, "end": v(2, 148.62) * mm});
            skLineSegment(sketch, "E2053", {"start": v(2, 148.62) * mm, "end": v(1.1, 147.67) * mm});
            skLineSegment(sketch, "E2054", {"start": v(1.1, 147.67) * mm, "end": v(0.19, 146.7) * mm});
            skLineSegment(sketch, "E2055", {"start": v(0.19, 146.7) * mm, "end": v(-2.86, 144.1) * mm});
            skLineSegment(sketch, "E2056", {"start": v(-2.86, 144.1) * mm, "end": v(-7.23, 141.14) * mm});
            skLineSegment(sketch, "E2057", {"start": v(-7.23, 141.14) * mm, "end": v(-11.81, 138.5) * mm});
            skLineSegment(sketch, "E2058", {"start": v(-11.81, 138.5) * mm, "end": v(-15.29, 136.55) * mm});
            skLineSegment(sketch, "E2059", {"start": v(-15.29, 136.55) * mm, "end": v(-16.44, 135.88) * mm});
            skLineSegment(sketch, "E2060", {"start": v(-16.44, 135.88) * mm, "end": v(-18, 134.96) * mm});
            skLineSegment(sketch, "E2061", {"start": v(-18, 134.96) * mm, "end": v(-25.87, 130.5) * mm});
            skLineSegment(sketch, "E2062", {"start": v(-25.87, 130.5) * mm, "end": v(-33.5, 125.67) * mm});
            skLineSegment(sketch, "E2063", {"start": v(-33.5, 125.67) * mm, "end": v(-34.96, 124.56) * mm});
            skLineSegment(sketch, "E2064", {"start": v(-34.96, 124.56) * mm, "end": v(-35.66, 124.03) * mm});
            skLineSegment(sketch, "E2065", {"start": v(-35.66, 124.03) * mm, "end": v(-42.84, 119.07) * mm});
            skLineSegment(sketch, "E2066", {"start": v(-42.84, 119.07) * mm, "end": v(-43.59, 118.62) * mm});
            skLineSegment(sketch, "E2067", {"start": v(-43.59, 118.62) * mm, "end": v(-44.18, 118.26) * mm});
            skLineSegment(sketch, "E2068", {"start": v(-44.18, 118.26) * mm, "end": v(-46.06, 117.3) * mm});
            skLineSegment(sketch, "E2069", {"start": v(-46.06, 117.3) * mm, "end": v(-48.6, 116.08) * mm});
            skLineSegment(sketch, "E2070", {"start": v(-48.6, 116.08) * mm, "end": v(-51.1, 114.79) * mm});
            skLineSegment(sketch, "E2071", {"start": v(-51.1, 114.79) * mm, "end": v(-52.88, 113.67) * mm});
            skLineSegment(sketch, "E2072", {"start": v(-52.88, 113.67) * mm, "end": v(-53.43, 113.24) * mm});
            skLineSegment(sketch, "E2073", {"start": v(-53.43, 113.24) * mm, "end": v(-53.73, 113) * mm});
            skLineSegment(sketch, "E2074", {"start": v(-53.73, 113) * mm, "end": v(-54.56, 112.16) * mm});
            skLineSegment(sketch, "E2075", {"start": v(-54.56, 112.16) * mm, "end": v(-55.57, 110.93) * mm});
            skLineSegment(sketch, "E2076", {"start": v(-55.57, 110.93) * mm, "end": v(-56.58, 109.73) * mm});
            skLineSegment(sketch, "E2077", {"start": v(-56.58, 109.73) * mm, "end": v(-57.4, 108.94) * mm});
            skLineSegment(sketch, "E2078", {"start": v(-57.4, 108.94) * mm, "end": v(-57.7, 108.74) * mm});
            skLineSegment(sketch, "E2079", {"start": v(-57.7, 108.74) * mm, "end": v(-58.38, 108.29) * mm});
            skLineSegment(sketch, "E2080", {"start": v(-58.38, 108.29) * mm, "end": v(-62.37, 106.3) * mm});
            skLineSegment(sketch, "E2081", {"start": v(-62.37, 106.3) * mm, "end": v(-66.51, 104.58) * mm});
            skLineSegment(sketch, "E2082", {"start": v(-66.51, 104.58) * mm, "end": v(-67.26, 104.26) * mm});
            skLineSegment(sketch, "E2083", {"start": v(-67.26, 104.26) * mm, "end": v(-69.34, 103.39) * mm});
            skLineSegment(sketch, "E2084", {"start": v(-69.34, 103.39) * mm, "end": v(-75.72, 101.14) * mm});
            skLineSegment(sketch, "E2085", {"start": v(-75.72, 101.14) * mm, "end": v(-84.37, 98.64) * mm});
            skLineSegment(sketch, "E2086", {"start": v(-84.37, 98.64) * mm, "end": v(-93.13, 96.5) * mm});
            skLineSegment(sketch, "E2087", {"start": v(-93.13, 96.5) * mm, "end": v(-99.72, 94.99) * mm});
            skLineSegment(sketch, "E2088", {"start": v(-99.72, 94.99) * mm, "end": v(-101.92, 94.47) * mm});
            skLineSegment(sketch, "E2089", {"start": v(-101.92, 94.47) * mm, "end": v(-103.58, 94.08) * mm});
            skLineSegment(sketch, "E2090", {"start": v(-103.58, 94.08) * mm, "end": v(-108.52, 92.61) * mm});
            skLineSegment(sketch, "E2091", {"start": v(-108.52, 92.61) * mm, "end": v(-114.98, 90.36) * mm});
            skLineSegment(sketch, "E2092", {"start": v(-114.98, 90.36) * mm, "end": v(-121.4, 87.95) * mm});
            skLineSegment(sketch, "E2093", {"start": v(-121.4, 87.95) * mm, "end": v(-126.23, 86.17) * mm});
            skLineSegment(sketch, "E2094", {"start": v(-126.23, 86.17) * mm, "end": v(-127.85, 85.62) * mm});
            skLineSegment(sketch, "E2095", {"start": v(-127.85, 85.62) * mm, "end": v(-129.2, 85.17) * mm});
            skLineSegment(sketch, "E2096", {"start": v(-129.2, 85.17) * mm, "end": v(-133.16, 83.53) * mm});
            skLineSegment(sketch, "E2097", {"start": v(-133.16, 83.53) * mm, "end": v(-138.25, 81.1) * mm});
            skLineSegment(sketch, "E2098", {"start": v(-138.25, 81.1) * mm, "end": v(-143.27, 78.54) * mm});
            skLineSegment(sketch, "E2099", {"start": v(-143.27, 78.54) * mm, "end": v(-147.1, 76.66) * mm});
            skLineSegment(sketch, "E2100", {"start": v(-147.1, 76.66) * mm, "end": v(-148.39, 76.08) * mm});
            skLineSegment(sketch, "E2101", {"start": v(-148.39, 76.08) * mm, "end": v(-148.71, 75.93) * mm});
            skLineSegment(sketch, "E2102", {"start": v(-148.71, 75.93) * mm, "end": v(-149.78, 75.36) * mm});
            skLineSegment(sketch, "E2103", {"start": v(-149.78, 75.36) * mm, "end": v(-151.65, 74.32) * mm});
            skLineSegment(sketch, "E2104", {"start": v(-151.65, 74.32) * mm, "end": v(-153.47, 73.4) * mm});
            skLineSegment(sketch, "E2105", {"start": v(-153.47, 73.4) * mm, "end": v(-154.36, 73) * mm});
            skLineSegment(sketch, "E2106", {"start": v(-154.36, 73) * mm, "end": v(-154.66, 73) * mm});
            skLineSegment(sketch, "E2107", {"start": v(-154.66, 73) * mm, "end": v(-154.93, 72.9) * mm});
            skLineSegment(sketch, "E2108", {"start": v(-154.93, 72.9) * mm, "end": v(-155.63, 72.61) * mm});
            skLineSegment(sketch, "E2109", {"start": v(-155.63, 72.61) * mm, "end": v(-156.67, 72.16) * mm});
            skLineSegment(sketch, "E2110", {"start": v(-156.67, 72.16) * mm, "end": v(-157.89, 71.57) * mm});
            skLineSegment(sketch, "E2111", {"start": v(-157.89, 71.57) * mm, "end": v(-159.18, 70.86) * mm});
            skLineSegment(sketch, "E2112", {"start": v(-159.18, 70.86) * mm, "end": v(-160.42, 70.07) * mm});
            skLineSegment(sketch, "E2113", {"start": v(-160.42, 70.07) * mm, "end": v(-161.47, 69.2) * mm});
            skLineSegment(sketch, "E2114", {"start": v(-161.47, 69.2) * mm, "end": v(-162.07, 68.55) * mm});
            skLineSegment(sketch, "E2115", {"start": v(-162.07, 68.55) * mm, "end": v(-162.22, 68.3) * mm});
            skLineSegment(sketch, "E2116", {"start": v(-162.22, 68.3) * mm, "end": v(-162.36, 68.08) * mm});
            skLineSegment(sketch, "E2117", {"start": v(-162.36, 68.08) * mm, "end": v(-162.75, 67.37) * mm});
            skLineSegment(sketch, "E2118", {"start": v(-162.75, 67.37) * mm, "end": v(-163.24, 66.43) * mm});
            skLineSegment(sketch, "E2119", {"start": v(-163.24, 66.43) * mm, "end": v(-163.67, 65.51) * mm});
            skLineSegment(sketch, "E2120", {"start": v(-163.67, 65.51) * mm, "end": v(-164.03, 64.68) * mm});
            skLineSegment(sketch, "E2121", {"start": v(-164.03, 64.68) * mm, "end": v(-164.33, 63.95) * mm});
            skLineSegment(sketch, "E2122", {"start": v(-164.33, 63.95) * mm, "end": v(-164.55, 63.38) * mm});
            skLineSegment(sketch, "E2123", {"start": v(-164.55, 63.38) * mm, "end": v(-164.68, 63) * mm});
            skLineSegment(sketch, "E2124", {"start": v(-164.68, 63) * mm, "end": v(-164.73, 62.87) * mm});
            skLineSegment(sketch, "E2125", {"start": v(-164.73, 62.87) * mm, "end": v(-165.32, 62.37) * mm});
            skLineSegment(sketch, "E2126", {"start": v(-165.32, 62.37) * mm, "end": v(-171.36, 57.52) * mm});
            skLineSegment(sketch, "E2127", {"start": v(-171.36, 57.52) * mm, "end": v(-171.95, 57.02) * mm});
            skLineSegment(sketch, "E2128", {"start": v(-171.95, 57.02) * mm, "end": v(-172.56, 56.8) * mm});
            skLineSegment(sketch, "E2129", {"start": v(-172.56, 56.8) * mm, "end": v(-174.35, 55.89) * mm});
            skLineSegment(sketch, "E2130", {"start": v(-174.35, 55.89) * mm, "end": v(-176.78, 54.38) * mm});
            skLineSegment(sketch, "E2131", {"start": v(-176.78, 54.38) * mm, "end": v(-179.12, 52.72) * mm});
            skLineSegment(sketch, "E2132", {"start": v(-179.12, 52.72) * mm, "end": v(-180.72, 51.52) * mm});
            skLineSegment(sketch, "E2133", {"start": v(-180.72, 51.52) * mm, "end": v(-181.25, 51.12) * mm});
            skLineSegment(sketch, "E2134", {"start": v(-181.25, 51.12) * mm, "end": v(-181.8, 50.7) * mm});
            skLineSegment(sketch, "E2135", {"start": v(-181.8, 50.7) * mm, "end": v(-187.5, 46.48) * mm});
            skLineSegment(sketch, "E2136", {"start": v(-187.5, 46.48) * mm, "end": v(-188.1, 46.1) * mm});
            skLineSegment(sketch, "E2137", {"start": v(-188.1, 46.1) * mm, "end": v(-188.5, 45.82) * mm});
            skLineSegment(sketch, "E2138", {"start": v(-188.5, 45.82) * mm, "end": v(-189.83, 45.07) * mm});
            skLineSegment(sketch, "E2139", {"start": v(-189.83, 45.07) * mm, "end": v(-191.74, 43.94) * mm});
            skLineSegment(sketch, "E2140", {"start": v(-191.74, 43.94) * mm, "end": v(-193.38, 42.57) * mm});
            skLineSegment(sketch, "E2141", {"start": v(-193.38, 42.57) * mm, "end": v(-194.22, 41.33) * mm});
            skLineSegment(sketch, "E2142", {"start": v(-194.22, 41.33) * mm, "end": v(-194.32, 40.87) * mm});
            skLineSegment(sketch, "E2143", {"start": v(-194.32, 40.87) * mm, "end": v(-194.4, 40.58) * mm});
            skLineSegment(sketch, "E2144", {"start": v(-194.4, 40.58) * mm, "end": v(-194.38, 39.67) * mm});
            skLineSegment(sketch, "E2145", {"start": v(-194.38, 39.67) * mm, "end": v(-194.03, 38.56) * mm});
            skLineSegment(sketch, "E2146", {"start": v(-194.03, 38.56) * mm, "end": v(-193.4, 37.57) * mm});
            skLineSegment(sketch, "E2147", {"start": v(-193.4, 37.57) * mm, "end": v(-192.8, 36.9) * mm});
            skLineSegment(sketch, "E2148", {"start": v(-192.8, 36.9) * mm, "end": v(-192.58, 36.7) * mm});
            skLineSegment(sketch, "E2149", {"start": v(-192.58, 36.7) * mm, "end": v(-192.18, 36.34) * mm});
            skLineSegment(sketch, "E2150", {"start": v(-192.18, 36.34) * mm, "end": v(-191.67, 36.41) * mm});
            skLineSegment(sketch, "E2151", {"start": v(-191.67, 36.41) * mm, "end": v(-191.17, 36.5) * mm});
            skLineSegment(sketch, "E2152", {"start": v(-191.17, 36.5) * mm, "end": v(-189.72, 37.02) * mm});
            skLineSegment(sketch, "E2153", {"start": v(-189.72, 37.02) * mm, "end": v(-188.06, 38.02) * mm});
            skLineSegment(sketch, "E2154", {"start": v(-188.06, 38.02) * mm, "end": v(-186.52, 39.22) * mm});
            skLineSegment(sketch, "E2155", {"start": v(-186.52, 39.22) * mm, "end": v(-185.33, 40.15) * mm});
            skLineSegment(sketch, "E2156", {"start": v(-185.33, 40.15) * mm, "end": v(-184.91, 40.43) * mm});
            skLineSegment(sketch, "E2157", {"start": v(-184.91, 40.43) * mm, "end": v(-183.21, 41.52) * mm});
            skLineSegment(sketch, "E2158", {"start": v(-183.21, 41.52) * mm, "end": v(-174.52, 46.6) * mm});
            skLineSegment(sketch, "E2159", {"start": v(-174.52, 46.6) * mm, "end": v(-165.65, 51.4) * mm});
            skLineSegment(sketch, "E2160", {"start": v(-165.65, 51.4) * mm, "end": v(-163.87, 52.33) * mm});
            skLineSegment(sketch, "E2161", {"start": v(-163.87, 52.33) * mm, "end": v(-162.1, 53.26) * mm});
            skLineSegment(sketch, "E2162", {"start": v(-162.1, 53.26) * mm, "end": v(-156.93, 56.34) * mm});
            skLineSegment(sketch, "E2163", {"start": v(-156.93, 56.34) * mm, "end": v(-150.18, 60.68) * mm});
            skLineSegment(sketch, "E2164", {"start": v(-150.18, 60.68) * mm, "end": v(-143.41, 64.99) * mm});
            skLineSegment(sketch, "E2165", {"start": v(-143.41, 64.99) * mm, "end": v(-138.2, 67.99) * mm});
            skLineSegment(sketch, "E2166", {"start": v(-138.2, 67.99) * mm, "end": v(-136.4, 68.87) * mm});
            skLineSegment(sketch, "E2167", {"start": v(-136.4, 68.87) * mm, "end": v(-135.58, 69.28) * mm});
            skLineSegment(sketch, "E2168", {"start": v(-135.58, 69.28) * mm, "end": v(-133.02, 70.36) * mm});
            skLineSegment(sketch, "E2169", {"start": v(-133.02, 70.36) * mm, "end": v(-129.57, 71.7) * mm});
            skLineSegment(sketch, "E2170", {"start": v(-129.57, 71.7) * mm, "end": v(-126.17, 73.13) * mm});
            skLineSegment(sketch, "E2171", {"start": v(-126.17, 73.13) * mm, "end": v(-123.7, 74.43) * mm});
            skLineSegment(sketch, "E2172", {"start": v(-123.7, 74.43) * mm, "end": v(-122.91, 74.94) * mm});
            skLineSegment(sketch, "E2173", {"start": v(-122.91, 74.94) * mm, "end": v(-121.99, 75.53) * mm});
            skLineSegment(sketch, "E2174", {"start": v(-121.99, 75.53) * mm, "end": v(-117.27, 78.4) * mm});
            skLineSegment(sketch, "E2175", {"start": v(-117.27, 78.4) * mm, "end": v(-112.35, 80.88) * mm});
            skLineSegment(sketch, "E2176", {"start": v(-112.35, 80.88) * mm, "end": v(-111.32, 81.28) * mm});
            skLineSegment(sketch, "E2177", {"start": v(-111.32, 81.28) * mm, "end": v(-111.77, 80.94) * mm});
            skLineSegment(sketch, "E2178", {"start": v(-111.77, 80.94) * mm, "end": v(-114.15, 79.46) * mm});
            skLineSegment(sketch, "E2179", {"start": v(-114.15, 79.46) * mm, "end": v(-116.55, 78.06) * mm});
            skLineSegment(sketch, "E2180", {"start": v(-116.55, 78.06) * mm, "end": v(-117, 77.78) * mm});
            skLineSegment(sketch, "E2181", {"start": v(-117, 77.78) * mm, "end": v(-120.58, 75.52) * mm});
            skLineSegment(sketch, "E2182", {"start": v(-120.58, 75.52) * mm, "end": v(-131.23, 68.58) * mm});
            skLineSegment(sketch, "E2183", {"start": v(-131.23, 68.58) * mm, "end": v(-145.39, 59.26) * mm});
            skLineSegment(sketch, "E2184", {"start": v(-145.39, 59.26) * mm, "end": v(-159.67, 50.14) * mm});
            skLineSegment(sketch, "E2185", {"start": v(-159.67, 50.14) * mm, "end": v(-170.57, 43.6) * mm});
            skLineSegment(sketch, "E2186", {"start": v(-170.57, 43.6) * mm, "end": v(-174.27, 41.54) * mm});
            skLineSegment(sketch, "E2187", {"start": v(-174.27, 41.54) * mm, "end": v(-174.98, 41.15) * mm});
            skLineSegment(sketch, "E2188", {"start": v(-174.98, 41.15) * mm, "end": v(-177.12, 39.96) * mm});
            skLineSegment(sketch, "E2189", {"start": v(-177.12, 39.96) * mm, "end": v(-179.73, 38.15) * mm});
            skLineSegment(sketch, "E2190", {"start": v(-179.73, 38.15) * mm, "end": v(-181.67, 35.78) * mm});
            skLineSegment(sketch, "E2191", {"start": v(-181.67, 35.78) * mm, "end": v(-182.47, 33.36) * mm});
            skLineSegment(sketch, "E2192", {"start": v(-182.47, 33.36) * mm, "end": v(-182.5, 32.54) * mm});
            skLineSegment(sketch, "E2193", {"start": v(-182.5, 32.54) * mm, "end": v(-182.53, 31.6) * mm});
            skLineSegment(sketch, "E2194", {"start": v(-182.53, 31.6) * mm, "end": v(-181.6, 31.45) * mm});
            skLineSegment(sketch, "E2195", {"start": v(-181.6, 31.45) * mm, "end": v(-181.2, 31.39) * mm});
            skLineSegment(sketch, "E2196", {"start": v(-181.2, 31.39) * mm, "end": v(-178.94, 31.26) * mm});
            skLineSegment(sketch, "E2197", {"start": v(-178.94, 31.26) * mm, "end": v(-176.67, 31.39) * mm});
            skLineSegment(sketch, "E2198", {"start": v(-176.67, 31.39) * mm, "end": v(-176.28, 31.44) * mm});
            skLineSegment(sketch, "E2199", {"start": v(-176.28, 31.44) * mm, "end": v(-176.07, 31.48) * mm});
            skLineSegment(sketch, "E2200", {"start": v(-176.07, 31.48) * mm, "end": v(-175.9, 31.6) * mm});
            skLineSegment(sketch, "E2201", {"start": v(-175.9, 31.6) * mm, "end": v(-175.71, 31.7) * mm});
            skLineSegment(sketch, "E2202", {"start": v(-175.71, 31.7) * mm, "end": v(-175.26, 32.17) * mm});
            skLineSegment(sketch, "E2203", {"start": v(-175.26, 32.17) * mm, "end": v(-174.95, 32.8) * mm});
            skLineSegment(sketch, "E2204", {"start": v(-174.95, 32.8) * mm, "end": v(-174.78, 33.42) * mm});
            skLineSegment(sketch, "E2205", {"start": v(-174.78, 33.42) * mm, "end": v(-174.65, 33.8) * mm});
            skLineSegment(sketch, "E2206", {"start": v(-174.65, 33.8) * mm, "end": v(-174.58, 33.9) * mm});
            skLineSegment(sketch, "E2207", {"start": v(-174.58, 33.9) * mm, "end": v(-174.35, 33.93) * mm});
            skLineSegment(sketch, "E2208", {"start": v(-174.35, 33.93) * mm, "end": v(-174.12, 34.1) * mm});
            skLineSegment(sketch, "E2209", {"start": v(-174.12, 34.1) * mm, "end": v(-173.62, 34.49) * mm});
            skLineSegment(sketch, "E2210", {"start": v(-173.62, 34.49) * mm, "end": v(-172.05, 35.54) * mm});
            skLineSegment(sketch, "E2211", {"start": v(-172.05, 35.54) * mm, "end": v(-169.94, 36.9) * mm});
            skLineSegment(sketch, "E2212", {"start": v(-169.94, 36.9) * mm, "end": v(-167.9, 38.38) * mm});
            skLineSegment(sketch, "E2213", {"start": v(-167.9, 38.38) * mm, "end": v(-166.48, 39.64) * mm});
            skLineSegment(sketch, "E2214", {"start": v(-166.48, 39.64) * mm, "end": v(-166.06, 40.1) * mm});
            skLineSegment(sketch, "E2215", {"start": v(-166.06, 40.1) * mm, "end": v(-164.02, 41.06) * mm});
            skLineSegment(sketch, "E2216", {"start": v(-164.02, 41.06) * mm, "end": v(-158, 44.15) * mm});
            skLineSegment(sketch, "E2217", {"start": v(-158, 44.15) * mm, "end": v(-150.17, 48.54) * mm});
            skLineSegment(sketch, "E2218", {"start": v(-150.17, 48.54) * mm, "end": v(-142.5, 53.19) * mm});
            skLineSegment(sketch, "E2219", {"start": v(-142.5, 53.19) * mm, "end": v(-134.94, 58) * mm});
            skLineSegment(sketch, "E2220", {"start": v(-134.94, 58) * mm, "end": v(-127.42, 62.87) * mm});
            skLineSegment(sketch, "E2221", {"start": v(-127.42, 62.87) * mm, "end": v(-119.88, 67.73) * mm});
            skLineSegment(sketch, "E2222", {"start": v(-119.88, 67.73) * mm, "end": v(-112.26, 72.47) * mm});
            skLineSegment(sketch, "E2223", {"start": v(-112.26, 72.47) * mm, "end": v(-106.46, 75.9) * mm});
            skLineSegment(sketch, "E2224", {"start": v(-106.46, 75.9) * mm, "end": v(-104.5, 77) * mm});
            skLineSegment(sketch, "E2225", {"start": v(-104.5, 77) * mm, "end": v(-103.28, 77.68) * mm});
            skLineSegment(sketch, "E2226", {"start": v(-103.28, 77.68) * mm, "end": v(-99.68, 79.87) * mm});
            skLineSegment(sketch, "E2227", {"start": v(-99.68, 79.87) * mm, "end": v(-94.82, 82.75) * mm});
            skLineSegment(sketch, "E2228", {"start": v(-94.82, 82.75) * mm, "end": v(-89.78, 85.21) * mm});
            skLineSegment(sketch, "E2229", {"start": v(-89.78, 85.21) * mm, "end": v(-85.8, 86.57) * mm});
            skLineSegment(sketch, "E2230", {"start": v(-85.8, 86.57) * mm, "end": v(-84.42, 86.82) * mm});
            skLineSegment(sketch, "E2231", {"start": v(-84.42, 86.82) * mm, "end": v(-84.65, 86.26) * mm});
            skLineSegment(sketch, "E2232", {"start": v(-84.65, 86.26) * mm, "end": v(-85.64, 84.67) * mm});
            skLineSegment(sketch, "E2233", {"start": v(-85.64, 84.67) * mm, "end": v(-87.28, 82.78) * mm});
            skLineSegment(sketch, "E2234", {"start": v(-87.28, 82.78) * mm, "end": v(-89.14, 81.06) * mm});
            skLineSegment(sketch, "E2235", {"start": v(-89.14, 81.06) * mm, "end": v(-90.56, 79.83) * mm});
            skLineSegment(sketch, "E2236", {"start": v(-90.56, 79.83) * mm, "end": v(-91.02, 79.4) * mm});
            skLineSegment(sketch, "E2237", {"start": v(-91.02, 79.4) * mm, "end": v(-91.75, 78.73) * mm});
            skLineSegment(sketch, "E2238", {"start": v(-91.75, 78.73) * mm, "end": v(-98.78, 71.63) * mm});
            skLineSegment(sketch, "E2239", {"start": v(-98.78, 71.63) * mm, "end": v(-99.47, 70.9) * mm});
            skLineSegment(sketch, "E2240", {"start": v(-99.47, 70.9) * mm, "end": v(-101.53, 68.73) * mm});
            skLineSegment(sketch, "E2241", {"start": v(-101.53, 68.73) * mm, "end": v(-108.23, 62.71) * mm});
            skLineSegment(sketch, "E2242", {"start": v(-108.23, 62.71) * mm, "end": v(-117.7, 55.4) * mm});
            skLineSegment(sketch, "E2243", {"start": v(-117.7, 55.4) * mm, "end": v(-127.56, 48.56) * mm});
            skLineSegment(sketch, "E2244", {"start": v(-127.56, 48.56) * mm, "end": v(-135.02, 43.55) * mm});
            skLineSegment(sketch, "E2245", {"start": v(-135.02, 43.55) * mm, "end": v(-137.5, 41.85) * mm});
            skLineSegment(sketch, "E2246", {"start": v(-137.5, 41.85) * mm, "end": v(-139.55, 40.44) * mm});
            skLineSegment(sketch, "E2247", {"start": v(-139.55, 40.44) * mm, "end": v(-159.92, 26.04) * mm});
            skLineSegment(sketch, "E2248", {"start": v(-159.92, 26.04) * mm, "end": v(-161.95, 24.59) * mm});
            skLineSegment(sketch, "E2249", {"start": v(-161.95, 24.59) * mm, "end": v(-162.15, 24.44) * mm});
            skLineSegment(sketch, "E2250", {"start": v(-162.15, 24.44) * mm, "end": v(-162.8, 24.03) * mm});
            skLineSegment(sketch, "E2251", {"start": v(-162.8, 24.03) * mm, "end": v(-163.63, 23.48) * mm});
            skLineSegment(sketch, "E2252", {"start": v(-163.63, 23.48) * mm, "end": v(-164.4, 22.84) * mm});
            skLineSegment(sketch, "E2253", {"start": v(-164.4, 22.84) * mm, "end": v(-164.89, 22.24) * mm});
            skLineSegment(sketch, "E2254", {"start": v(-164.89, 22.24) * mm, "end": v(-165, 22.01) * mm});
            skLineSegment(sketch, "E2255", {"start": v(-165, 22.01) * mm, "end": v(-165.16, 21.74) * mm});
            skLineSegment(sketch, "E2256", {"start": v(-165.16, 21.74) * mm, "end": v(-165.4, 20.35) * mm});
            skLineSegment(sketch, "E2257", {"start": v(-165.4, 20.35) * mm, "end": v(-165.1, 18.95) * mm});
            skLineSegment(sketch, "E2258", {"start": v(-165.1, 18.95) * mm, "end": v(-164.97, 18.67) * mm});
            skLineSegment(sketch, "E2259", {"start": v(-164.97, 18.67) * mm, "end": v(-164.77, 18.23) * mm});
            skLineSegment(sketch, "E2260", {"start": v(-164.77, 18.23) * mm, "end": v(-164.29, 18.1) * mm});
            skLineSegment(sketch, "E2261", {"start": v(-164.29, 18.1) * mm, "end": v(-163.83, 17.96) * mm});
            skLineSegment(sketch, "E2262", {"start": v(-163.83, 17.96) * mm, "end": v(-162.36, 17.85) * mm});
            skLineSegment(sketch, "E2263", {"start": v(-162.36, 17.85) * mm, "end": v(-160.64, 18.22) * mm});
            skLineSegment(sketch, "E2264", {"start": v(-160.64, 18.22) * mm, "end": v(-159.1, 19.04) * mm});
            skLineSegment(sketch, "E2265", {"start": v(-159.1, 19.04) * mm, "end": v(-157.68, 20.18) * mm});
            skLineSegment(sketch, "E2266", {"start": v(-157.68, 20.18) * mm, "end": v(-156.34, 21.5) * mm});
            skLineSegment(sketch, "E2267", {"start": v(-156.34, 21.5) * mm, "end": v(-155.04, 22.86) * mm});
            skLineSegment(sketch, "E2268", {"start": v(-155.04, 22.86) * mm, "end": v(-153.72, 24.1) * mm});
            skLineSegment(sketch, "E2269", {"start": v(-153.72, 24.1) * mm, "end": v(-152.71, 24.9) * mm});
            skLineSegment(sketch, "E2270", {"start": v(-152.71, 24.9) * mm, "end": v(-152.35, 25.1) * mm});
            skLineSegment(sketch, "E2271", {"start": v(-152.35, 25.1) * mm, "end": v(-149.2, 25.1) * mm});
            skLineSegment(sketch, "E2272", {"start": v(-149.2, 25.1) * mm, "end": v(-148.9, 25.38) * mm});
            skLineSegment(sketch, "E2273", {"start": v(-148.9, 25.38) * mm, "end": v(-146.4, 27.63) * mm});
            skLineSegment(sketch, "E2274", {"start": v(-146.4, 27.63) * mm, "end": v(-138.5, 33.96) * mm});
            skLineSegment(sketch, "E2275", {"start": v(-138.5, 33.96) * mm, "end": v(-127.55, 41.78) * mm});
            skLineSegment(sketch, "E2276", {"start": v(-127.55, 41.78) * mm, "end": v(-116.21, 49.11) * mm});
            skLineSegment(sketch, "E2277", {"start": v(-116.21, 49.11) * mm, "end": v(-104.7, 56.22) * mm});
            skLineSegment(sketch, "E2278", {"start": v(-104.7, 56.22) * mm, "end": v(-93.23, 63.37) * mm});
            skLineSegment(sketch, "E2279", {"start": v(-93.23, 63.37) * mm, "end": v(-82, 70.83) * mm});
            skLineSegment(sketch, "E2280", {"start": v(-82, 70.83) * mm, "end": v(-71.2, 78.87) * mm});
            skLineSegment(sketch, "E2281", {"start": v(-71.2, 78.87) * mm, "end": v(-63.5, 85.42) * mm});
            skLineSegment(sketch, "E2282", {"start": v(-63.5, 85.42) * mm, "end": v(-61.07, 87.76) * mm});
            skLineSegment(sketch, "E2283", {"start": v(-61.07, 87.76) * mm, "end": v(-60.85, 87.76) * mm});
            skLineSegment(sketch, "E2284", {"start": v(-60.85, 87.76) * mm, "end": v(-59.9, 87.96) * mm});
            skLineSegment(sketch, "E2285", {"start": v(-59.9, 87.96) * mm, "end": v(-58.97, 88.35) * mm});
            skLineSegment(sketch, "E2286", {"start": v(-58.97, 88.35) * mm, "end": v(-58.76, 88.46) * mm});
            skLineSegment(sketch, "E2287", {"start": v(-58.76, 88.46) * mm, "end": v(-58.7, 88.5) * mm});
            skLineSegment(sketch, "E2288", {"start": v(-58.7, 88.5) * mm, "end": v(-57.95, 88.83) * mm});
            skLineSegment(sketch, "E2289", {"start": v(-57.95, 88.83) * mm, "end": v(-57.87, 88.85) * mm});
            skLineSegment(sketch, "E2290", {"start": v(-57.87, 88.85) * mm, "end": v(-57.56, 88.91) * mm});
            skLineSegment(sketch, "E2291", {"start": v(-57.56, 88.91) * mm, "end": v(-57.33, 89.16) * mm});
            skLineSegment(sketch, "E2292", {"start": v(-57.33, 89.16) * mm, "end": v(-56.64, 89.9) * mm});
            skLineSegment(sketch, "E2293", {"start": v(-56.64, 89.9) * mm, "end": v(-54.65, 92.19) * mm});
            skLineSegment(sketch, "E2294", {"start": v(-54.65, 92.19) * mm, "end": v(-52.03, 95.27) * mm});
            skLineSegment(sketch, "E2295", {"start": v(-52.03, 95.27) * mm, "end": v(-49.32, 98.27) * mm});
            skLineSegment(sketch, "E2296", {"start": v(-49.32, 98.27) * mm, "end": v(-47.14, 100.4) * mm});
            skLineSegment(sketch, "E2297", {"start": v(-47.14, 100.4) * mm, "end": v(-46.37, 101.04) * mm});
            skLineSegment(sketch, "E2298", {"start": v(-46.37, 101.04) * mm, "end": v(-45.88, 101.45) * mm});
            skLineSegment(sketch, "E2299", {"start": v(-45.88, 101.45) * mm, "end": v(-43.2, 103.13) * mm});
            skLineSegment(sketch, "E2300", {"start": v(-43.2, 103.13) * mm, "end": v(-40.49, 104.85) * mm});
            skLineSegment(sketch, "E2301", {"start": v(-40.49, 104.85) * mm, "end": v(-40, 105.28) * mm});
            skLineSegment(sketch, "E2302", {"start": v(-40, 105.28) * mm, "end": v(-38.89, 106.26) * mm});
            skLineSegment(sketch, "E2303", {"start": v(-38.89, 106.26) * mm, "end": v(-33.62, 111.44) * mm});
            skLineSegment(sketch, "E2304", {"start": v(-33.62, 111.44) * mm, "end": v(-28.36, 116.63) * mm});
            skLineSegment(sketch, "E2305", {"start": v(-28.36, 116.63) * mm, "end": v(-27.26, 117.6) * mm});
            skLineSegment(sketch, "E2306", {"start": v(-27.26, 117.6) * mm, "end": v(-26.36, 118.4) * mm});
            skLineSegment(sketch, "E2307", {"start": v(-26.36, 118.4) * mm, "end": v(-21.5, 122.07) * mm});
            skLineSegment(sketch, "E2308", {"start": v(-21.5, 122.07) * mm, "end": v(-16.22, 125.1) * mm});
            skLineSegment(sketch, "E2309", {"start": v(-16.22, 125.1) * mm, "end": v(-15.1, 125.57) * mm});
            skLineSegment(sketch, "E2310", {"start": v(-15.1, 125.57) * mm, "end": v(-16.11, 123.76) * mm});
            skLineSegment(sketch, "E2311", {"start": v(-16.11, 123.76) * mm, "end": v(-19.7, 118.66) * mm});
            skLineSegment(sketch, "E2312", {"start": v(-19.7, 118.66) * mm, "end": v(-25.11, 112.38) * mm});
            skLineSegment(sketch, "E2313", {"start": v(-25.11, 112.38) * mm, "end": v(-30.94, 106.42) * mm});
            skLineSegment(sketch, "E2314", {"start": v(-30.94, 106.42) * mm, "end": v(-35.35, 102) * mm});
            skLineSegment(sketch, "E2315", {"start": v(-35.35, 102) * mm, "end": v(-36.78, 100.49) * mm});
            skLineSegment(sketch, "E2316", {"start": v(-36.78, 100.49) * mm, "end": v(-38.33, 98.85) * mm});
            skLineSegment(sketch, "E2317", {"start": v(-38.33, 98.85) * mm, "end": v(-42.92, 93.88) * mm});
            skLineSegment(sketch, "E2318", {"start": v(-42.92, 93.88) * mm, "end": v(-49.04, 87.22) * mm});
            skLineSegment(sketch, "E2319", {"start": v(-49.04, 87.22) * mm, "end": v(-55.3, 80.7) * mm});
            skLineSegment(sketch, "E2320", {"start": v(-55.3, 80.7) * mm, "end": v(-60.16, 76) * mm});
            skLineSegment(sketch, "E2321", {"start": v(-60.16, 76) * mm, "end": v(-61.84, 74.5) * mm});
            skLineSegment(sketch, "E2322", {"start": v(-61.84, 74.5) * mm, "end": v(-62.27, 74.12) * mm});
            skLineSegment(sketch, "E2323", {"start": v(-62.27, 74.12) * mm, "end": v(-64.56, 72.41) * mm});
            skLineSegment(sketch, "E2324", {"start": v(-64.56, 72.41) * mm, "end": v(-66.82, 70.66) * mm});
            skLineSegment(sketch, "E2325", {"start": v(-66.82, 70.66) * mm, "end": v(-67.23, 70.26) * mm});
            skLineSegment(sketch, "E2326", {"start": v(-67.23, 70.26) * mm, "end": v(-68.04, 69.48) * mm});
            skLineSegment(sketch, "E2327", {"start": v(-68.04, 69.48) * mm, "end": v(-70.34, 67) * mm});
            skLineSegment(sketch, "E2328", {"start": v(-70.34, 67) * mm, "end": v(-73.54, 63.61) * mm});
            skLineSegment(sketch, "E2329", {"start": v(-73.54, 63.61) * mm, "end": v(-77, 60.62) * mm});
            skLineSegment(sketch, "E2330", {"start": v(-77, 60.62) * mm, "end": v(-79.91, 58.88) * mm});
            skLineSegment(sketch, "E2331", {"start": v(-79.91, 58.88) * mm, "end": v(-80.96, 58.52) * mm});
            skLineSegment(sketch, "E2332", {"start": v(-80.96, 58.52) * mm, "end": v(-81.17, 58.44) * mm});
            skLineSegment(sketch, "E2333", {"start": v(-81.17, 58.44) * mm, "end": v(-81.37, 58.26) * mm});
            skLineSegment(sketch, "E2334", {"start": v(-81.37, 58.26) * mm, "end": v(-82.5, 57.16) * mm});
            skLineSegment(sketch, "E2335", {"start": v(-82.5, 57.16) * mm, "end": v(-93.91, 46.32) * mm});
            skLineSegment(sketch, "E2336", {"start": v(-93.91, 46.32) * mm, "end": v(-95.06, 45.24) * mm});
            skLineSegment(sketch, "E2337", {"start": v(-95.06, 45.24) * mm, "end": v(-95.56, 44.77) * mm});
            skLineSegment(sketch, "E2338", {"start": v(-95.56, 44.77) * mm, "end": v(-98.26, 42.63) * mm});
            skLineSegment(sketch, "E2339", {"start": v(-98.26, 42.63) * mm, "end": v(-100.94, 40.44) * mm});
            skLineSegment(sketch, "E2340", {"start": v(-100.94, 40.44) * mm, "end": v(-101.44, 39.95) * mm});
            skLineSegment(sketch, "E2341", {"start": v(-101.44, 39.95) * mm, "end": v(-103.93, 37.52) * mm});
            skLineSegment(sketch, "E2342", {"start": v(-103.93, 37.52) * mm, "end": v(-116.53, 25.54) * mm});
            skLineSegment(sketch, "E2343", {"start": v(-116.53, 25.54) * mm, "end": v(-129.33, 13.77) * mm});
            skLineSegment(sketch, "E2344", {"start": v(-129.33, 13.77) * mm, "end": v(-131.91, 11.44) * mm});
            skLineSegment(sketch, "E2345", {"start": v(-131.91, 11.44) * mm, "end": v(-132.23, 11.17) * mm});
            skLineSegment(sketch, "E2346", {"start": v(-132.23, 11.17) * mm, "end": v(-133.2, 10.4) * mm});
            skLineSegment(sketch, "E2347", {"start": v(-133.2, 10.4) * mm, "end": v(-134.49, 9.32) * mm});
            skLineSegment(sketch, "E2348", {"start": v(-134.49, 9.32) * mm, "end": v(-135.6, 8.1) * mm});
            skLineSegment(sketch, "E2349", {"start": v(-135.6, 8.1) * mm, "end": v(-136.22, 6.99) * mm});
            skLineSegment(sketch, "E2350", {"start": v(-136.22, 6.99) * mm, "end": v(-136.34, 6.6) * mm});
            skLineSegment(sketch, "E2351", {"start": v(-136.34, 6.6) * mm, "end": v(-136.43, 6.29) * mm});
            skLineSegment(sketch, "E2352", {"start": v(-136.43, 6.29) * mm, "end": v(-136.46, 4.8) * mm});
            skLineSegment(sketch, "E2353", {"start": v(-136.46, 4.8) * mm, "end": v(-135.98, 3.37) * mm});
            skLineSegment(sketch, "E2354", {"start": v(-135.98, 3.37) * mm, "end": v(-135.81, 3.1) * mm});
            skLineSegment(sketch, "E2355", {"start": v(-135.81, 3.1) * mm, "end": v(-135.67, 2.85) * mm});
            skLineSegment(sketch, "E2356", {"start": v(-135.67, 2.85) * mm, "end": v(-135.41, 2.7) * mm});
            skLineSegment(sketch, "E2357", {"start": v(-135.41, 2.7) * mm, "end": v(-135.08, 2.52) * mm});
            skLineSegment(sketch, "E2358", {"start": v(-135.08, 2.52) * mm, "end": v(-133.92, 2.2) * mm});
            skLineSegment(sketch, "E2359", {"start": v(-133.92, 2.2) * mm, "end": v(-132.6, 2.39) * mm});
            skLineSegment(sketch, "E2360", {"start": v(-132.6, 2.39) * mm, "end": v(-131.45, 3.11) * mm});
            skLineSegment(sketch, "E2361", {"start": v(-131.45, 3.11) * mm, "end": v(-130.66, 3.95) * mm});
            skLineSegment(sketch, "E2362", {"start": v(-130.66, 3.95) * mm, "end": v(-130.44, 4.26) * mm});
            skLineSegment(sketch, "E2363", {"start": v(-130.44, 4.26) * mm, "end": v(-130.35, 4.38) * mm});
            skLineSegment(sketch, "E2364", {"start": v(-130.35, 4.38) * mm, "end": v(-129.48, 5.66) * mm});
            skLineSegment(sketch, "E2365", {"start": v(-129.48, 5.66) * mm, "end": v(-129.38, 5.77) * mm});
            skLineSegment(sketch, "E2366", {"start": v(-129.38, 5.77) * mm, "end": v(-128.42, 6.85) * mm});
            skLineSegment(sketch, "E2367", {"start": v(-128.42, 6.85) * mm, "end": v(-123.4, 12.04) * mm});
            skLineSegment(sketch, "E2368", {"start": v(-123.4, 12.04) * mm, "end": v(-118.14, 17.02) * mm});
            skLineSegment(sketch, "E2369", {"start": v(-118.14, 17.02) * mm, "end": v(-117.08, 18) * mm});
            skLineSegment(sketch, "E2370", {"start": v(-117.08, 18) * mm, "end": v(-114.85, 20.02) * mm});
            skLineSegment(sketch, "E2371", {"start": v(-114.85, 20.02) * mm, "end": v(-108.13, 26.01) * mm});
            skLineSegment(sketch, "E2372", {"start": v(-108.13, 26.01) * mm, "end": v(-99.14, 33.98) * mm});
            skLineSegment(sketch, "E2373", {"start": v(-99.14, 33.98) * mm, "end": v(-90.24, 42.05) * mm});
            skLineSegment(sketch, "E2374", {"start": v(-90.24, 42.05) * mm, "end": v(-83.69, 48.23) * mm});
            skLineSegment(sketch, "E2375", {"start": v(-83.69, 48.23) * mm, "end": v(-81.56, 50.35) * mm});
            skLineSegment(sketch, "E2376", {"start": v(-81.56, 50.35) * mm, "end": v(-78.93, 52.3) * mm});
            skLineSegment(sketch, "E2377", {"start": v(-78.93, 52.3) * mm, "end": v(-66.08, 62.41) * mm});
            skLineSegment(sketch, "E2378", {"start": v(-66.08, 62.41) * mm, "end": v(-53.73, 73.14) * mm});
            skLineSegment(sketch, "E2379", {"start": v(-53.73, 73.14) * mm, "end": v(-51.35, 75.38) * mm});
            skLineSegment(sketch, "E2380", {"start": v(-51.35, 75.38) * mm, "end": v(-50.55, 76.15) * mm});
            skLineSegment(sketch, "E2381", {"start": v(-50.55, 76.15) * mm, "end": v(-46.93, 80.29) * mm});
            skLineSegment(sketch, "E2382", {"start": v(-46.93, 80.29) * mm, "end": v(-43.37, 84.47) * mm});
            skLineSegment(sketch, "E2383", {"start": v(-43.37, 84.47) * mm, "end": v(-42.6, 85.25) * mm});
            skLineSegment(sketch, "E2384", {"start": v(-42.6, 85.25) * mm, "end": v(-40.85, 87.05) * mm});
            skLineSegment(sketch, "E2385", {"start": v(-40.85, 87.05) * mm, "end": v(-35.36, 92.18) * mm});
            skLineSegment(sketch, "E2386", {"start": v(-35.36, 92.18) * mm, "end": v(-27.82, 98.8) * mm});
            skLineSegment(sketch, "E2387", {"start": v(-27.82, 98.8) * mm, "end": v(-20.3, 105.42) * mm});
            skLineSegment(sketch, "E2388", {"start": v(-20.3, 105.42) * mm, "end": v(-14.83, 110.59) * mm});
            skLineSegment(sketch, "E2389", {"start": v(-14.83, 110.59) * mm, "end": v(-13.1, 112.4) * mm});
            skLineSegment(sketch, "E2390", {"start": v(-13.1, 112.4) * mm, "end": v(-11.39, 114.2) * mm});
            skLineSegment(sketch, "E2391", {"start": v(-11.39, 114.2) * mm, "end": v(-6.21, 119.57) * mm});
            skLineSegment(sketch, "E2392", {"start": v(-6.21, 119.57) * mm, "end": v(0.85, 126.52) * mm});
            skLineSegment(sketch, "E2393", {"start": v(0.85, 126.52) * mm, "end": v(8.26, 133.07) * mm});
            skLineSegment(sketch, "E2394", {"start": v(8.26, 133.07) * mm, "end": v(14.17, 137.64) * mm});
            skLineSegment(sketch, "E2395", {"start": v(14.17, 137.64) * mm, "end": v(16.23, 139.03) * mm});
            skLineSegment(sketch, "E2396", {"start": v(16.23, 139.03) * mm, "end": v(16.85, 139.45) * mm});
            skLineSegment(sketch, "E2397", {"start": v(16.85, 139.45) * mm, "end": v(18.65, 140.83) * mm});
            skLineSegment(sketch, "E2398", {"start": v(18.65, 140.83) * mm, "end": v(21.11, 142.75) * mm});
            skLineSegment(sketch, "E2399", {"start": v(21.11, 142.75) * mm, "end": v(23.69, 144.46) * mm});
            skLineSegment(sketch, "E2400", {"start": v(23.69, 144.46) * mm, "end": v(25.75, 145.44) * mm});
            skLineSegment(sketch, "E2401", {"start": v(25.75, 145.44) * mm, "end": v(26.47, 145.64) * mm});
            skLineSegment(sketch, "E2402", {"start": v(26.47, 145.64) * mm, "end": v(26.53, 144.85) * mm});
            skLineSegment(sketch, "E2403", {"start": v(26.53, 144.85) * mm, "end": v(25.93, 142.41) * mm});
            skLineSegment(sketch, "E2404", {"start": v(25.93, 142.41) * mm, "end": v(24.23, 139.43) * mm});
            skLineSegment(sketch, "E2405", {"start": v(24.23, 139.43) * mm, "end": v(21.98, 136.7) * mm});
            skLineSegment(sketch, "E2406", {"start": v(21.98, 136.7) * mm, "end": v(20.32, 134.86) * mm});
            skLineSegment(sketch, "E2407", {"start": v(20.32, 134.86) * mm, "end": v(19.8, 134.23) * mm});
            skLineSegment(sketch, "E2408", {"start": v(19.8, 134.23) * mm, "end": v(17.98, 132) * mm});
            skLineSegment(sketch, "E2409", {"start": v(17.98, 132) * mm, "end": v(12.3, 125.47) * mm});
            skLineSegment(sketch, "E2410", {"start": v(12.3, 125.47) * mm, "end": v(4.56, 116.9) * mm});
            skLineSegment(sketch, "E2411", {"start": v(4.56, 116.9) * mm, "end": v(-3.09, 108.28) * mm});
            skLineSegment(sketch, "E2412", {"start": v(-3.09, 108.28) * mm, "end": v(-8.62, 101.63) * mm});
            skLineSegment(sketch, "E2413", {"start": v(-8.62, 101.63) * mm, "end": v(-10.36, 99.33) * mm});
            skLineSegment(sketch, "E2414", {"start": v(-10.36, 99.33) * mm, "end": v(-12.1, 97.06) * mm});
            skLineSegment(sketch, "E2415", {"start": v(-12.1, 97.06) * mm, "end": v(-17.65, 90.52) * mm});
            skLineSegment(sketch, "E2416", {"start": v(-17.65, 90.52) * mm, "end": v(-25.47, 82.14) * mm});
            skLineSegment(sketch, "E2417", {"start": v(-25.47, 82.14) * mm, "end": v(-33.6, 74.02) * mm});
            skLineSegment(sketch, "E2418", {"start": v(-33.6, 74.02) * mm, "end": v(-39.74, 68.04) * mm});
            skLineSegment(sketch, "E2419", {"start": v(-39.74, 68.04) * mm, "end": v(-41.78, 66.04) * mm});
            skLineSegment(sketch, "E2420", {"start": v(-41.78, 66.04) * mm, "end": v(-42.7, 65.13) * mm});
            skLineSegment(sketch, "E2421", {"start": v(-42.7, 65.13) * mm, "end": v(-46.82, 60.19) * mm});
            skLineSegment(sketch, "E2422", {"start": v(-46.82, 60.19) * mm, "end": v(-50.93, 55.27) * mm});
            skLineSegment(sketch, "E2423", {"start": v(-50.93, 55.27) * mm, "end": v(-51.84, 54.37) * mm});
            skLineSegment(sketch, "E2424", {"start": v(-51.84, 54.37) * mm, "end": v(-56.65, 49.67) * mm});
            skLineSegment(sketch, "E2425", {"start": v(-56.65, 49.67) * mm, "end": v(-80.3, 25.77) * mm});
            skLineSegment(sketch, "E2426", {"start": v(-80.3, 25.77) * mm, "end": v(-103.55, 1.51) * mm});
            skLineSegment(sketch, "E2427", {"start": v(-103.55, 1.51) * mm, "end": v(-108.16, -3.38) * mm});
            skLineSegment(sketch, "E2428", {"start": v(-108.16, -3.38) * mm, "end": v(-108.17, -3.4) * mm});
            skLineSegment(sketch, "E2429", {"start": v(-108.17, -3.4) * mm, "end": v(-108.19, -3.41) * mm});
            skLineSegment(sketch, "E2430", {"start": v(-108.19, -3.41) * mm, "end": v(-108.46, -3.73) * mm});
            skLineSegment(sketch, "E2431", {"start": v(-108.46, -3.73) * mm, "end": v(-109.47, -4.5) * mm});
            skLineSegment(sketch, "E2432", {"start": v(-109.47, -4.5) * mm, "end": v(-110.96, -5.4) * mm});
            skLineSegment(sketch, "E2433", {"start": v(-110.96, -5.4) * mm, "end": v(-112.44, -6.42) * mm});
            skLineSegment(sketch, "E2434", {"start": v(-112.44, -6.42) * mm, "end": v(-113.46, -7.45) * mm});
            skLineSegment(sketch, "E2435", {"start": v(-113.46, -7.45) * mm, "end": v(-113.7, -7.84) * mm});
            skLineSegment(sketch, "E2436", {"start": v(-113.7, -7.84) * mm, "end": v(-113.86, -8.08) * mm});
            skLineSegment(sketch, "E2437", {"start": v(-113.86, -8.08) * mm, "end": v(-114.2, -8.88) * mm});
            skLineSegment(sketch, "E2438", {"start": v(-114.2, -8.88) * mm, "end": v(-114.4, -9.95) * mm});
            skLineSegment(sketch, "E2439", {"start": v(-114.4, -9.95) * mm, "end": v(-114.36, -11.05) * mm});
            skLineSegment(sketch, "E2440", {"start": v(-114.36, -11.05) * mm, "end": v(-114.2, -11.9) * mm});
            skLineSegment(sketch, "E2441", {"start": v(-114.2, -11.9) * mm, "end": v(-114.1, -12.17) * mm});
            skLineSegment(sketch, "E2442", {"start": v(-114.1, -12.17) * mm, "end": v(-113.82, -13.1) * mm});
            skLineSegment(sketch, "E2443", {"start": v(-113.82, -13.1) * mm, "end": v(-112.86, -12.9) * mm});
            skLineSegment(sketch, "E2444", {"start": v(-112.86, -12.9) * mm, "end": v(-111.97, -12.7) * mm});
            skLineSegment(sketch, "E2445", {"start": v(-111.97, -12.7) * mm, "end": v(-109.42, -11.47) * mm});
            skLineSegment(sketch, "E2446", {"start": v(-109.42, -11.47) * mm, "end": v(-106.51, -9.18) * mm});
            skLineSegment(sketch, "E2447", {"start": v(-106.51, -9.18) * mm, "end": v(-103.9, -6.48) * mm});
            skLineSegment(sketch, "E2448", {"start": v(-103.9, -6.48) * mm, "end": v(-101.97, -4.45) * mm});
            skLineSegment(sketch, "E2449", {"start": v(-101.97, -4.45) * mm, "end": v(-101.3, -3.82) * mm});
            skLineSegment(sketch, "E2450", {"start": v(-101.3, -3.82) * mm, "end": v(-100.4, -3) * mm});
            skLineSegment(sketch, "E2451", {"start": v(-100.4, -3) * mm, "end": v(-96.17, 1.4) * mm});
            skLineSegment(sketch, "E2452", {"start": v(-96.17, 1.4) * mm, "end": v(-92.04, 5.9) * mm});
            skLineSegment(sketch, "E2453", {"start": v(-92.04, 5.9) * mm, "end": v(-91.2, 6.78) * mm});
            skLineSegment(sketch, "E2454", {"start": v(-91.2, 6.78) * mm, "end": v(-89.91, 8.1) * mm});
            skLineSegment(sketch, "E2455", {"start": v(-89.91, 8.1) * mm, "end": v(-85.92, 11.92) * mm});
            skLineSegment(sketch, "E2456", {"start": v(-85.92, 11.92) * mm, "end": v(-80.55, 16.98) * mm});
            skLineSegment(sketch, "E2457", {"start": v(-80.55, 16.98) * mm, "end": v(-75.39, 22.21) * mm});
            skLineSegment(sketch, "E2458", {"start": v(-75.39, 22.21) * mm, "end": v(-71.8, 26.42) * mm});
            skLineSegment(sketch, "E2459", {"start": v(-71.8, 26.42) * mm, "end": v(-70.73, 27.92) * mm});
            skLineSegment(sketch, "E2460", {"start": v(-70.73, 27.92) * mm, "end": v(-69.35, 29.13) * mm});
            skLineSegment(sketch, "E2461", {"start": v(-69.35, 29.13) * mm, "end": v(-62.68, 35.42) * mm});
            skLineSegment(sketch, "E2462", {"start": v(-62.68, 35.42) * mm, "end": v(-56.07, 41.76) * mm});
            skLineSegment(sketch, "E2463", {"start": v(-56.07, 41.76) * mm, "end": v(-54.72, 43) * mm});
            skLineSegment(sketch, "E2464", {"start": v(-54.72, 43) * mm, "end": v(-54.04, 43.62) * mm});
            skLineSegment(sketch, "E2465", {"start": v(-54.04, 43.62) * mm, "end": v(-47.58, 50.11) * mm});
            skLineSegment(sketch, "E2466", {"start": v(-47.58, 50.11) * mm, "end": v(-46.95, 50.78) * mm});
            skLineSegment(sketch, "E2467", {"start": v(-46.95, 50.78) * mm, "end": v(-46.3, 51.45) * mm});
            skLineSegment(sketch, "E2468", {"start": v(-46.3, 51.45) * mm, "end": v(-43.35, 55.06) * mm});
            skLineSegment(sketch, "E2469", {"start": v(-43.35, 55.06) * mm, "end": v(-40.3, 58.58) * mm});
            skLineSegment(sketch, "E2470", {"start": v(-40.3, 58.58) * mm, "end": v(-39.62, 59.2) * mm});
            skLineSegment(sketch, "E2471", {"start": v(-39.62, 59.2) * mm, "end": v(-39.22, 59.57) * mm});
            skLineSegment(sketch, "E2472", {"start": v(-39.22, 59.57) * mm, "end": v(-36.99, 61.13) * mm});
            skLineSegment(sketch, "E2473", {"start": v(-36.99, 61.13) * mm, "end": v(-34.72, 62.69) * mm});
            skLineSegment(sketch, "E2474", {"start": v(-34.72, 62.69) * mm, "end": v(-34.3, 63.04) * mm});
            skLineSegment(sketch, "E2475", {"start": v(-34.3, 63.04) * mm, "end": v(-33.88, 63.4) * mm});
            skLineSegment(sketch, "E2476", {"start": v(-33.88, 63.4) * mm, "end": v(-31.94, 65.32) * mm});
            skLineSegment(sketch, "E2477", {"start": v(-31.94, 65.32) * mm, "end": v(-30, 67.25) * mm});
            skLineSegment(sketch, "E2478", {"start": v(-30, 67.25) * mm, "end": v(-29.59, 67.61) * mm});
            skLineSegment(sketch, "E2479", {"start": v(-29.59, 67.61) * mm, "end": v(-27.14, 69.81) * mm});
            skLineSegment(sketch, "E2480", {"start": v(-27.14, 69.81) * mm, "end": v(-15.18, 81.09) * mm});
            skLineSegment(sketch, "E2481", {"start": v(-15.18, 81.09) * mm, "end": v(-3.62, 92.77) * mm});
            skLineSegment(sketch, "E2482", {"start": v(-3.62, 92.77) * mm, "end": v(-1.38, 95.18) * mm});
            skLineSegment(sketch, "E2483", {"start": v(-1.38, 95.18) * mm, "end": v(0.12, 96.76) * mm});
            skLineSegment(sketch, "E2484", {"start": v(0.12, 96.76) * mm, "end": v(7.89, 104.4) * mm});
            skLineSegment(sketch, "E2485", {"start": v(7.89, 104.4) * mm, "end": v(15.8, 111.9) * mm});
            skLineSegment(sketch, "E2486", {"start": v(15.8, 111.9) * mm, "end": v(17.37, 113.42) * mm});
            skLineSegment(sketch, "E2487", {"start": v(17.37, 113.42) * mm, "end": v(18.54, 114.54) * mm});
            skLineSegment(sketch, "E2488", {"start": v(18.54, 114.54) * mm, "end": v(22, 117.93) * mm});
            skLineSegment(sketch, "E2489", {"start": v(22, 117.93) * mm, "end": v(26.8, 122.44) * mm});
            skLineSegment(sketch, "E2490", {"start": v(26.8, 122.44) * mm, "end": v(31.77, 126.72) * mm});
            skLineSegment(sketch, "E2491", {"start": v(31.77, 126.72) * mm, "end": v(35.63, 129.64) * mm});
            skLineSegment(sketch, "E2492", {"start": v(35.63, 129.64) * mm, "end": v(36.97, 130.52) * mm});
            skLineSegment(sketch, "E2493", {"start": v(36.97, 130.52) * mm, "end": v(37.62, 130.95) * mm});
            skLineSegment(sketch, "E2494", {"start": v(37.62, 130.95) * mm, "end": v(39.73, 131.97) * mm});
            skLineSegment(sketch, "E2495", {"start": v(39.73, 131.97) * mm, "end": v(42.87, 133.12) * mm});
            skLineSegment(sketch, "E2496", {"start": v(42.87, 133.12) * mm, "end": v(46.1, 134.09) * mm});
            skLineSegment(sketch, "E2497", {"start": v(46.1, 134.09) * mm, "end": v(48.38, 134.75) * mm});
            skLineSegment(sketch, "E2498", {"start": v(48.38, 134.75) * mm, "end": v(49.14, 134.99) * mm});
            skLineSegment(sketch, "E2499", {"start": v(49.14, 134.99) * mm, "end": v(49.72, 135.18) * mm});
            skLineSegment(sketch, "E2500", {"start": v(49.72, 135.18) * mm, "end": v(51.45, 135.85) * mm});
            skLineSegment(sketch, "E2501", {"start": v(51.45, 135.85) * mm, "end": v(53.91, 136.72) * mm});
            skLineSegment(sketch, "E2502", {"start": v(53.91, 136.72) * mm, "end": v(56.38, 137.1) * mm});
            skLineSegment(sketch, "E2503", {"start": v(56.38, 137.1) * mm, "end": v(58.23, 136.77) * mm});
            skLineSegment(sketch, "E2504", {"start": v(58.23, 136.77) * mm, "end": v(58.74, 136.48) * mm});
            skLineSegment(sketch, "E2505", {"start": v(58.74, 136.48) * mm, "end": v(58.7, 135.99) * mm});
            skLineSegment(sketch, "E2506", {"start": v(58.7, 135.99) * mm, "end": v(58.42, 134.5) * mm});
            skLineSegment(sketch, "E2507", {"start": v(58.42, 134.5) * mm, "end": v(57.8, 132.81) * mm});
            skLineSegment(sketch, "E2508", {"start": v(57.8, 132.81) * mm, "end": v(56.96, 131.31) * mm});
            skLineSegment(sketch, "E2509", {"start": v(56.96, 131.31) * mm, "end": v(55.97, 129.93) * mm});
            skLineSegment(sketch, "E2510", {"start": v(55.97, 129.93) * mm, "end": v(54.91, 128.58) * mm});
            skLineSegment(sketch, "E2511", {"start": v(54.91, 128.58) * mm, "end": v(53.88, 127.18) * mm});
            skLineSegment(sketch, "E2512", {"start": v(53.88, 127.18) * mm, "end": v(52.95, 125.65) * mm});
            skLineSegment(sketch, "E2513", {"start": v(52.95, 125.65) * mm, "end": v(52.35, 124.35) * mm});
            skLineSegment(sketch, "E2514", {"start": v(52.35, 124.35) * mm, "end": v(52.2, 123.9) * mm});
            skLineSegment(sketch, "E2515", {"start": v(52.2, 123.9) * mm, "end": v(50.95, 122.6) * mm});
            skLineSegment(sketch, "E2516", {"start": v(50.95, 122.6) * mm, "end": v(47.2, 118.66) * mm});
            skLineSegment(sketch, "E2517", {"start": v(47.2, 118.66) * mm, "end": v(42.15, 113.46) * mm});
            skLineSegment(sketch, "E2518", {"start": v(42.15, 113.46) * mm, "end": v(36.9, 108.45) * mm});
            skLineSegment(sketch, "E2519", {"start": v(36.9, 108.45) * mm, "end": v(32.8, 104.89) * mm});
            skLineSegment(sketch, "E2520", {"start": v(32.8, 104.89) * mm, "end": v(31.36, 103.78) * mm});
            skLineSegment(sketch, "E2521", {"start": v(31.36, 103.78) * mm, "end": v(31.26, 103.7) * mm});
            skLineSegment(sketch, "E2522", {"start": v(31.26, 103.7) * mm, "end": v(31.19, 103.6) * mm});
            skLineSegment(sketch, "E2523", {"start": v(31.19, 103.6) * mm, "end": v(29.85, 101.91) * mm});
            skLineSegment(sketch, "E2524", {"start": v(29.85, 101.91) * mm, "end": v(25.35, 97.23) * mm});
            skLineSegment(sketch, "E2525", {"start": v(25.35, 97.23) * mm, "end": v(19, 91.39) * mm});
            skLineSegment(sketch, "E2526", {"start": v(19, 91.39) * mm, "end": v(12.64, 85.52) * mm});
            skLineSegment(sketch, "E2527", {"start": v(12.64, 85.52) * mm, "end": v(8.15, 80.8) * mm});
            skLineSegment(sketch, "E2528", {"start": v(8.15, 80.8) * mm, "end": v(6.83, 79.1) * mm});
            skLineSegment(sketch, "E2529", {"start": v(6.83, 79.1) * mm, "end": v(5.62, 78.32) * mm});
            skLineSegment(sketch, "E2530", {"start": v(5.62, 78.32) * mm, "end": v(2.26, 75.59) * mm});
            skLineSegment(sketch, "E2531", {"start": v(2.26, 75.59) * mm, "end": v(-1.77, 71.57) * mm});
            skLineSegment(sketch, "E2532", {"start": v(-1.77, 71.57) * mm, "end": v(-5.62, 67.34) * mm});
            skLineSegment(sketch, "E2533", {"start": v(-5.62, 67.34) * mm, "end": v(-8.56, 64.2) * mm});
            skLineSegment(sketch, "E2534", {"start": v(-8.56, 64.2) * mm, "end": v(-9.6, 63.22) * mm});
            skLineSegment(sketch, "E2535", {"start": v(-9.6, 63.22) * mm, "end": v(-10.18, 62.66) * mm});
            skLineSegment(sketch, "E2536", {"start": v(-10.18, 62.66) * mm, "end": v(-16, 57.08) * mm});
            skLineSegment(sketch, "E2537", {"start": v(-16, 57.08) * mm, "end": v(-16.6, 56.55) * mm});
            skLineSegment(sketch, "E2538", {"start": v(-16.6, 56.55) * mm, "end": v(-17.23, 56) * mm});
            skLineSegment(sketch, "E2539", {"start": v(-17.23, 56) * mm, "end": v(-20.02, 53.06) * mm});
            skLineSegment(sketch, "E2540", {"start": v(-20.02, 53.06) * mm, "end": v(-22.75, 50.05) * mm});
            skLineSegment(sketch, "E2541", {"start": v(-22.75, 50.05) * mm, "end": v(-23.34, 49.48) * mm});
            skLineSegment(sketch, "E2542", {"start": v(-23.34, 49.48) * mm, "end": v(-24.25, 48.6) * mm});
            skLineSegment(sketch, "E2543", {"start": v(-24.25, 48.6) * mm, "end": v(-29.18, 44.71) * mm});
            skLineSegment(sketch, "E2544", {"start": v(-29.18, 44.71) * mm, "end": v(-34.13, 40.83) * mm});
            skLineSegment(sketch, "E2545", {"start": v(-34.13, 40.83) * mm, "end": v(-35.05, 39.97) * mm});
            skLineSegment(sketch, "E2546", {"start": v(-35.05, 39.97) * mm, "end": v(-36.85, 38.3) * mm});
            skLineSegment(sketch, "E2547", {"start": v(-36.85, 38.3) * mm, "end": v(-42.08, 33.1) * mm});
            skLineSegment(sketch, "E2548", {"start": v(-42.08, 33.1) * mm, "end": v(-48.92, 26.02) * mm});
            skLineSegment(sketch, "E2549", {"start": v(-48.92, 26.02) * mm, "end": v(-55.77, 18.97) * mm});
            skLineSegment(sketch, "E2550", {"start": v(-55.77, 18.97) * mm, "end": v(-61.05, 13.82) * mm});
            skLineSegment(sketch, "E2551", {"start": v(-61.05, 13.82) * mm, "end": v(-62.87, 12.17) * mm});
            skLineSegment(sketch, "E2552", {"start": v(-62.87, 12.17) * mm, "end": v(-63.86, 11.28) * mm});
            skLineSegment(sketch, "E2553", {"start": v(-63.86, 11.28) * mm, "end": v(-73.64, 2.17) * mm});
            skLineSegment(sketch, "E2554", {"start": v(-73.64, 2.17) * mm, "end": v(-74.6, 1.25) * mm});
            skLineSegment(sketch, "E2555", {"start": v(-74.6, 1.25) * mm, "end": v(-75.1, 0.78) * mm});
            skLineSegment(sketch, "E2556", {"start": v(-75.1, 0.78) * mm, "end": v(-77.36, -1.71) * mm});
            skLineSegment(sketch, "E2557", {"start": v(-77.36, -1.71) * mm, "end": v(-79.55, -4.26) * mm});
            skLineSegment(sketch, "E2558", {"start": v(-79.55, -4.26) * mm, "end": v(-80.02, -4.76) * mm});
            skLineSegment(sketch, "E2559", {"start": v(-80.02, -4.76) * mm, "end": v(-80.45, -5.22) * mm});
            skLineSegment(sketch, "E2560", {"start": v(-80.45, -5.22) * mm, "end": v(-82.99, -7.23) * mm});
            skLineSegment(sketch, "E2561", {"start": v(-82.99, -7.23) * mm, "end": v(-85.58, -9.22) * mm});
            skLineSegment(sketch, "E2562", {"start": v(-85.58, -9.22) * mm, "end": v(-86.03, -9.68) * mm});
            skLineSegment(sketch, "E2563", {"start": v(-86.03, -9.68) * mm, "end": v(-86.48, -10.15) * mm});
            skLineSegment(sketch, "E2564", {"start": v(-86.48, -10.15) * mm, "end": v(-88.5, -12.7) * mm});
            skLineSegment(sketch, "E2565", {"start": v(-88.5, -12.7) * mm, "end": v(-90.56, -15.2) * mm});
            skLineSegment(sketch, "E2566", {"start": v(-90.56, -15.2) * mm, "end": v(-91.02, -15.63) * mm});
            skLineSegment(sketch, "E2567", {"start": v(-91.02, -15.63) * mm, "end": v(-91.66, -16.23) * mm});
            skLineSegment(sketch, "E2568", {"start": v(-91.66, -16.23) * mm, "end": v(-95.2, -18.82) * mm});
            skLineSegment(sketch, "E2569", {"start": v(-95.2, -18.82) * mm, "end": v(-98.76, -21.4) * mm});
            skLineSegment(sketch, "E2570", {"start": v(-98.76, -21.4) * mm, "end": v(-99.42, -22) * mm});
            skLineSegment(sketch, "E2571", {"start": v(-99.42, -22) * mm, "end": v(-99.65, -22.2) * mm});
            skLineSegment(sketch, "E2572", {"start": v(-99.65, -22.2) * mm, "end": v(-99.73, -22.52) * mm});
            skLineSegment(sketch, "E2573", {"start": v(-99.73, -22.52) * mm, "end": v(-99.82, -22.86) * mm});
            skLineSegment(sketch, "E2574", {"start": v(-99.82, -22.86) * mm, "end": v(-100.02, -23.9) * mm});
            skLineSegment(sketch, "E2575", {"start": v(-100.02, -23.9) * mm, "end": v(-100.16, -25.27) * mm});
            skLineSegment(sketch, "E2576", {"start": v(-100.16, -25.27) * mm, "end": v(-100.12, -26.58) * mm});
            skLineSegment(sketch, "E2577", {"start": v(-100.12, -26.58) * mm, "end": v(-99.84, -27.78) * mm});
            skLineSegment(sketch, "E2578", {"start": v(-99.84, -27.78) * mm, "end": v(-99.3, -28.8) * mm});
            skLineSegment(sketch, "E2579", {"start": v(-99.3, -28.8) * mm, "end": v(-98.44, -29.57) * mm});
            skLineSegment(sketch, "E2580", {"start": v(-98.44, -29.57) * mm, "end": v(-97.22, -30.05) * mm});
            skLineSegment(sketch, "E2581", {"start": v(-97.22, -30.05) * mm, "end": v(-96, -30.2) * mm});
            skLineSegment(sketch, "E2582", {"start": v(-96, -30.2) * mm, "end": v(-95.6, -30.18) * mm});
            skLineSegment(sketch, "E2583", {"start": v(-95.6, -30.18) * mm, "end": v(-95.12, -30.15) * mm});
            skLineSegment(sketch, "E2584", {"start": v(-95.12, -30.15) * mm, "end": v(-94.81, -29.77) * mm});
            skLineSegment(sketch, "E2585", {"start": v(-94.81, -29.77) * mm, "end": v(-94.63, -29.54) * mm});
            skLineSegment(sketch, "E2586", {"start": v(-94.63, -29.54) * mm, "end": v(-94.27, -28.68) * mm});
            skLineSegment(sketch, "E2587", {"start": v(-94.27, -28.68) * mm, "end": v(-94.27, -27.66) * mm});
            skLineSegment(sketch, "E2588", {"start": v(-94.27, -27.66) * mm, "end": v(-94.5, -26.7) * mm});
            skLineSegment(sketch, "E2589", {"start": v(-94.5, -26.7) * mm, "end": v(-94.63, -25.98) * mm});
            skLineSegment(sketch, "E2590", {"start": v(-94.63, -25.98) * mm, "end": v(-94.63, -25.75) * mm});
            skLineSegment(sketch, "E2591", {"start": v(-94.63, -25.75) * mm, "end": v(-93.59, -24.77) * mm});
            skLineSegment(sketch, "E2592", {"start": v(-93.59, -24.77) * mm, "end": v(-83.17, -15.02) * mm});
            skLineSegment(sketch, "E2593", {"start": v(-83.17, -15.02) * mm, "end": v(-82.16, -14.02) * mm});
            skLineSegment(sketch, "E2594", {"start": v(-82.16, -14.02) * mm, "end": v(-81.9, -13.74) * mm});
            skLineSegment(sketch, "E2595", {"start": v(-81.9, -13.74) * mm, "end": v(-81.17, -12.82) * mm});
            skLineSegment(sketch, "E2596", {"start": v(-81.17, -12.82) * mm, "end": v(-80.3, -11.52) * mm});
            skLineSegment(sketch, "E2597", {"start": v(-80.3, -11.52) * mm, "end": v(-79.45, -10.25) * mm});
            skLineSegment(sketch, "E2598", {"start": v(-79.45, -10.25) * mm, "end": v(-78.75, -9.37) * mm});
            skLineSegment(sketch, "E2599", {"start": v(-78.75, -9.37) * mm, "end": v(-78.49, -9.11) * mm});
            skLineSegment(sketch, "E2600", {"start": v(-78.49, -9.11) * mm, "end": v(-78.28, -8.9) * mm});
            skLineSegment(sketch, "E2601", {"start": v(-78.28, -8.9) * mm, "end": v(-77.55, -8.36) * mm});
            skLineSegment(sketch, "E2602", {"start": v(-77.55, -8.36) * mm, "end": v(-76.5, -7.72) * mm});
            skLineSegment(sketch, "E2603", {"start": v(-76.5, -7.72) * mm, "end": v(-75.43, -7.05) * mm});
            skLineSegment(sketch, "E2604", {"start": v(-75.43, -7.05) * mm, "end": v(-74.67, -6.46) * mm});
            skLineSegment(sketch, "E2605", {"start": v(-74.67, -6.46) * mm, "end": v(-74.45, -6.23) * mm});
            skLineSegment(sketch, "E2606", {"start": v(-74.45, -6.23) * mm, "end": v(-73, -4.75) * mm});
            skLineSegment(sketch, "E2607", {"start": v(-73, -4.75) * mm, "end": v(-58.23, 9.9) * mm});
            skLineSegment(sketch, "E2608", {"start": v(-58.23, 9.9) * mm, "end": v(-56.72, 11.32) * mm});
            skLineSegment(sketch, "E2609", {"start": v(-56.72, 11.32) * mm, "end": v(-55.6, 12.38) * mm});
            skLineSegment(sketch, "E2610", {"start": v(-55.6, 12.38) * mm, "end": v(-52.4, 15.68) * mm});
            skLineSegment(sketch, "E2611", {"start": v(-52.4, 15.68) * mm, "end": v(-48.13, 20.21) * mm});
            skLineSegment(sketch, "E2612", {"start": v(-48.13, 20.21) * mm, "end": v(-43.75, 24.6) * mm});
            skLineSegment(sketch, "E2613", {"start": v(-43.75, 24.6) * mm, "end": v(-40.28, 27.6) * mm});
            skLineSegment(sketch, "E2614", {"start": v(-40.28, 27.6) * mm, "end": v(-39.05, 28.5) * mm});
            skLineSegment(sketch, "E2615", {"start": v(-39.05, 28.5) * mm, "end": v(-35.44, 31.11) * mm});
            skLineSegment(sketch, "E2616", {"start": v(-35.44, 31.11) * mm, "end": v(-24.76, 39.16) * mm});
            skLineSegment(sketch, "E2617", {"start": v(-24.76, 39.16) * mm, "end": v(-10.72, 50.15) * mm});
            skLineSegment(sketch, "E2618", {"start": v(-10.72, 50.15) * mm, "end": v(3.13, 61.38) * mm});
            skLineSegment(sketch, "E2619", {"start": v(3.13, 61.38) * mm, "end": v(13.43, 69.9) * mm});
            skLineSegment(sketch, "E2620", {"start": v(13.43, 69.9) * mm, "end": v(16.84, 72.77) * mm});
            skLineSegment(sketch, "E2621", {"start": v(16.84, 72.77) * mm, "end": v(17.63, 73.1) * mm});
            skLineSegment(sketch, "E2622", {"start": v(17.63, 73.1) * mm, "end": v(19.89, 74.29) * mm});
            skLineSegment(sketch, "E2623", {"start": v(19.89, 74.29) * mm, "end": v(22.59, 76.08) * mm});
            skLineSegment(sketch, "E2624", {"start": v(22.59, 76.08) * mm, "end": v(25.13, 78.1) * mm});
            skLineSegment(sketch, "E2625", {"start": v(25.13, 78.1) * mm, "end": v(27.06, 79.74) * mm});
            skLineSegment(sketch, "E2626", {"start": v(27.06, 79.74) * mm, "end": v(27.71, 80.29) * mm});
            skLineSegment(sketch, "E2627", {"start": v(27.71, 80.29) * mm, "end": v(28.79, 81.19) * mm});
            skLineSegment(sketch, "E2628", {"start": v(28.79, 81.19) * mm, "end": v(34.29, 85.53) * mm});
            skLineSegment(sketch, "E2629", {"start": v(34.29, 85.53) * mm, "end": v(39.75, 89.93) * mm});
            skLineSegment(sketch, "E2630", {"start": v(39.75, 89.93) * mm, "end": v(40.8, 90.85) * mm});
            skLineSegment(sketch, "E2631", {"start": v(40.8, 90.85) * mm, "end": v(41.26, 91.26) * mm});
            skLineSegment(sketch, "E2632", {"start": v(41.26, 91.26) * mm, "end": v(43.68, 93.03) * mm});
            skLineSegment(sketch, "E2633", {"start": v(43.68, 93.03) * mm, "end": v(46.2, 94.67) * mm});
            skLineSegment(sketch, "E2634", {"start": v(46.2, 94.67) * mm, "end": v(46.71, 95.01) * mm});
            skLineSegment(sketch, "E2635", {"start": v(46.71, 95.01) * mm, "end": v(47.75, 95.7) * mm});
            skLineSegment(sketch, "E2636", {"start": v(47.75, 95.7) * mm, "end": v(50.71, 98.05) * mm});
            skLineSegment(sketch, "E2637", {"start": v(50.71, 98.05) * mm, "end": v(54.43, 101.42) * mm});
            skLineSegment(sketch, "E2638", {"start": v(54.43, 101.42) * mm, "end": v(58, 104.96) * mm});
            skLineSegment(sketch, "E2639", {"start": v(58, 104.96) * mm, "end": v(60.67, 107.61) * mm});
            skLineSegment(sketch, "E2640", {"start": v(60.67, 107.61) * mm, "end": v(61.58, 108.47) * mm});
            skLineSegment(sketch, "E2641", {"start": v(61.58, 108.47) * mm, "end": v(61.88, 108.77) * mm});
            skLineSegment(sketch, "E2642", {"start": v(61.88, 108.77) * mm, "end": v(62.88, 109.58) * mm});
            skLineSegment(sketch, "E2643", {"start": v(62.88, 109.58) * mm, "end": v(64.26, 110.6) * mm});
            skLineSegment(sketch, "E2644", {"start": v(64.26, 110.6) * mm, "end": v(65.64, 111.6) * mm});
            skLineSegment(sketch, "E2645", {"start": v(65.64, 111.6) * mm, "end": v(66.64, 112.4) * mm});
            skLineSegment(sketch, "E2646", {"start": v(66.64, 112.4) * mm, "end": v(66.95, 112.7) * mm});
            skLineSegment(sketch, "E2647", {"start": v(66.95, 112.7) * mm, "end": v(67.43, 113.16) * mm});
            skLineSegment(sketch, "E2648", {"start": v(67.43, 113.16) * mm, "end": v(68.84, 114.58) * mm});
            skLineSegment(sketch, "E2649", {"start": v(68.84, 114.58) * mm, "end": v(70.65, 116.5) * mm});
            skLineSegment(sketch, "E2650", {"start": v(70.65, 116.5) * mm, "end": v(72.44, 118.34) * mm});
            skLineSegment(sketch, "E2651", {"start": v(72.44, 118.34) * mm, "end": v(74.29, 120.06) * mm});
            skLineSegment(sketch, "E2652", {"start": v(74.29, 120.06) * mm, "end": v(76.26, 121.57) * mm});
            skLineSegment(sketch, "E2653", {"start": v(76.26, 121.57) * mm, "end": v(78.42, 122.78) * mm});
            skLineSegment(sketch, "E2654", {"start": v(78.42, 122.78) * mm, "end": v(80.84, 123.62) * mm});
            skLineSegment(sketch, "E2655", {"start": v(80.84, 123.62) * mm, "end": v(82.9, 123.98) * mm});
            skLineSegment(sketch, "E2656", {"start": v(82.9, 123.98) * mm, "end": v(83.6, 124.01) * mm});
            skLineSegment(sketch, "E2657", {"start": v(83.6, 124.01) * mm, "end": v(83.73, 123.6) * mm});
            skLineSegment(sketch, "E2658", {"start": v(83.73, 123.6) * mm, "end": v(84.8, 119.39) * mm});
            skLineSegment(sketch, "E2659", {"start": v(84.8, 119.39) * mm, "end": v(84.88, 118.96) * mm});
            skLineSegment(sketch, "E2660", {"start": v(84.88, 118.96) * mm, "end": v(84.25, 117.87) * mm});
            skLineSegment(sketch, "E2661", {"start": v(84.25, 117.87) * mm, "end": v(82.02, 114.8) * mm});
            skLineSegment(sketch, "E2662", {"start": v(82.02, 114.8) * mm, "end": v(78.68, 111.07) * mm});
            skLineSegment(sketch, "E2663", {"start": v(78.68, 111.07) * mm, "end": v(75.1, 107.54) * mm});
            skLineSegment(sketch, "E2664", {"start": v(75.1, 107.54) * mm, "end": v(72.39, 104.91) * mm});
            skLineSegment(sketch, "E2665", {"start": v(72.39, 104.91) * mm, "end": v(71.51, 104.01) * mm});
            skLineSegment(sketch, "E2666", {"start": v(71.51, 104.01) * mm, "end": v(69.76, 102.24) * mm});
            skLineSegment(sketch, "E2667", {"start": v(69.76, 102.24) * mm, "end": v(64.58, 96.86) * mm});
            skLineSegment(sketch, "E2668", {"start": v(64.58, 96.86) * mm, "end": v(57.56, 89.75) * mm});
            skLineSegment(sketch, "E2669", {"start": v(57.56, 89.75) * mm, "end": v(50.25, 82.94) * mm});
            skLineSegment(sketch, "E2670", {"start": v(50.25, 82.94) * mm, "end": v(44.5, 78.16) * mm});
            skLineSegment(sketch, "E2671", {"start": v(44.5, 78.16) * mm, "end": v(42.49, 76.7) * mm});
            skLineSegment(sketch, "E2672", {"start": v(42.49, 76.7) * mm, "end": v(42.35, 76.6) * mm});
            skLineSegment(sketch, "E2673", {"start": v(42.35, 76.6) * mm, "end": v(42.25, 76.47) * mm});
            skLineSegment(sketch, "E2674", {"start": v(42.25, 76.47) * mm, "end": v(41.7, 75.72) * mm});
            skLineSegment(sketch, "E2675", {"start": v(41.7, 75.72) * mm, "end": v(39.83, 73.61) * mm});
            skLineSegment(sketch, "E2676", {"start": v(39.83, 73.61) * mm, "end": v(37.14, 71.03) * mm});
            skLineSegment(sketch, "E2677", {"start": v(37.14, 71.03) * mm, "end": v(34.27, 68.62) * mm});
            skLineSegment(sketch, "E2678", {"start": v(34.27, 68.62) * mm, "end": v(31.31, 66.3) * mm});
            skLineSegment(sketch, "E2679", {"start": v(31.31, 66.3) * mm, "end": v(28.36, 63.95) * mm});
            skLineSegment(sketch, "E2680", {"start": v(28.36, 63.95) * mm, "end": v(25.52, 61.49) * mm});
            skLineSegment(sketch, "E2681", {"start": v(25.52, 61.49) * mm, "end": v(22.87, 58.8) * mm});
            skLineSegment(sketch, "E2682", {"start": v(22.87, 58.8) * mm, "end": v(21.05, 56.59) * mm});
            skLineSegment(sketch, "E2683", {"start": v(21.05, 56.59) * mm, "end": v(20.5, 55.8) * mm});
            skLineSegment(sketch, "E2684", {"start": v(20.5, 55.8) * mm, "end": v(18.7, 54.48) * mm});
            skLineSegment(sketch, "E2685", {"start": v(18.7, 54.48) * mm, "end": v(13.48, 50.22) * mm});
            skLineSegment(sketch, "E2686", {"start": v(13.48, 50.22) * mm, "end": v(6.83, 44.18) * mm});
            skLineSegment(sketch, "E2687", {"start": v(6.83, 44.18) * mm, "end": v(0.42, 37.88) * mm});
            skLineSegment(sketch, "E2688", {"start": v(0.42, 37.88) * mm, "end": v(-4.33, 33.1) * mm});
            skLineSegment(sketch, "E2689", {"start": v(-4.33, 33.1) * mm, "end": v(-5.93, 31.51) * mm});
            skLineSegment(sketch, "E2690", {"start": v(-5.93, 31.51) * mm, "end": v(-6.37, 31.08) * mm});
            skLineSegment(sketch, "E2691", {"start": v(-6.37, 31.08) * mm, "end": v(-8.88, 29.21) * mm});
            skLineSegment(sketch, "E2692", {"start": v(-8.88, 29.21) * mm, "end": v(-11.45, 27.38) * mm});
            skLineSegment(sketch, "E2693", {"start": v(-11.45, 27.38) * mm, "end": v(-11.91, 26.96) * mm});
            skLineSegment(sketch, "E2694", {"start": v(-11.91, 26.96) * mm, "end": v(-13.32, 25.68) * mm});
            skLineSegment(sketch, "E2695", {"start": v(-13.32, 25.68) * mm, "end": v(-20.19, 19.07) * mm});
            skLineSegment(sketch, "E2696", {"start": v(-20.19, 19.07) * mm, "end": v(-27, 12.41) * mm});
            skLineSegment(sketch, "E2697", {"start": v(-27, 12.41) * mm, "end": v(-28.39, 11.1) * mm});
            skLineSegment(sketch, "E2698", {"start": v(-28.39, 11.1) * mm, "end": v(-28.86, 10.66) * mm});
            skLineSegment(sketch, "E2699", {"start": v(-28.86, 10.66) * mm, "end": v(-31.54, 8.84) * mm});
            skLineSegment(sketch, "E2700", {"start": v(-31.54, 8.84) * mm, "end": v(-34.25, 6.99) * mm});
            skLineSegment(sketch, "E2701", {"start": v(-34.25, 6.99) * mm, "end": v(-34.73, 6.53) * mm});
            skLineSegment(sketch, "E2702", {"start": v(-34.73, 6.53) * mm, "end": v(-35.6, 5.7) * mm});
            skLineSegment(sketch, "E2703", {"start": v(-35.6, 5.7) * mm, "end": v(-39.56, 1.22) * mm});
            skLineSegment(sketch, "E2704", {"start": v(-39.56, 1.22) * mm, "end": v(-43.56, -3.2) * mm});
            skLineSegment(sketch, "E2705", {"start": v(-43.56, -3.2) * mm, "end": v(-44.45, -4) * mm});
            skLineSegment(sketch, "E2706", {"start": v(-44.45, -4) * mm, "end": v(-44.93, -4.45) * mm});
            skLineSegment(sketch, "E2707", {"start": v(-44.93, -4.45) * mm, "end": v(-47.48, -6.46) * mm});
            skLineSegment(sketch, "E2708", {"start": v(-47.48, -6.46) * mm, "end": v(-50.03, -8.5) * mm});
            skLineSegment(sketch, "E2709", {"start": v(-50.03, -8.5) * mm, "end": v(-50.5, -8.96) * mm});
            skLineSegment(sketch, "E2710", {"start": v(-50.5, -8.96) * mm, "end": v(-50.98, -9.43) * mm});
            skLineSegment(sketch, "E2711", {"start": v(-50.98, -9.43) * mm, "end": v(-53.48, -11.62) * mm});
            skLineSegment(sketch, "E2712", {"start": v(-53.48, -11.62) * mm, "end": v(-56.01, -13.76) * mm});
            skLineSegment(sketch, "E2713", {"start": v(-56.01, -13.76) * mm, "end": v(-56.5, -14.2) * mm});
            skLineSegment(sketch, "E2714", {"start": v(-56.5, -14.2) * mm, "end": v(-58.09, -15.66) * mm});
            skLineSegment(sketch, "E2715", {"start": v(-58.09, -15.66) * mm, "end": v(-73.94, -30.12) * mm});
            skLineSegment(sketch, "E2716", {"start": v(-73.94, -30.12) * mm, "end": v(-75.54, -31.55) * mm});
            skLineSegment(sketch, "E2717", {"start": v(-75.54, -31.55) * mm, "end": v(-76.27, -32.2) * mm});
            skLineSegment(sketch, "E2718", {"start": v(-76.27, -32.2) * mm, "end": v(-75.1, -33.77) * mm});
            skLineSegment(sketch, "E2719", {"start": v(-75.1, -33.77) * mm, "end": v(-74.27, -33.26) * mm});
            skLineSegment(sketch, "E2720", {"start": v(-74.27, -33.26) * mm, "end": v(-74.1, -33.15) * mm});
            skLineSegment(sketch, "E2721", {"start": v(-74.1, -33.15) * mm, "end": v(-73.1, -32.6) * mm});
            skLineSegment(sketch, "E2722", {"start": v(-73.1, -32.6) * mm, "end": v(-72.17, -32) * mm});
            skLineSegment(sketch, "E2723", {"start": v(-72.17, -32) * mm, "end": v(-72, -31.86) * mm});
            skLineSegment(sketch, "E2724", {"start": v(-72, -31.86) * mm, "end": v(-63.18, -24.88) * mm});
            skLineSegment(sketch, "E2725", {"start": v(-63.18, -24.88) * mm, "end": v(-63.09, -24.94) * mm});
            skLineSegment(sketch, "E2726", {"start": v(-63.09, -24.94) * mm, "end": v(-62.2, -25.6) * mm});
            skLineSegment(sketch, "E2727", {"start": v(-62.2, -25.6) * mm, "end": v(-62.12, -25.68) * mm});
            skLineSegment(sketch, "E2728", {"start": v(-62.12, -25.68) * mm, "end": v(-61.44, -26.2) * mm});
            skLineSegment(sketch, "E2729", {"start": v(-61.44, -26.2) * mm, "end": v(-60.78, -25.64) * mm});
            skLineSegment(sketch, "E2730", {"start": v(-60.78, -25.64) * mm, "end": v(-60.05, -25.02) * mm});
            skLineSegment(sketch, "E2731", {"start": v(-60.05, -25.02) * mm, "end": v(-56.34, -22.02) * mm});
            skLineSegment(sketch, "E2732", {"start": v(-56.34, -22.02) * mm, "end": v(-52.7, -18.92) * mm});
            skLineSegment(sketch, "E2733", {"start": v(-52.7, -18.92) * mm, "end": v(-52.02, -18.25) * mm});
            skLineSegment(sketch, "E2734", {"start": v(-52.02, -18.25) * mm, "end": v(-51.23, -17.49) * mm});
            skLineSegment(sketch, "E2735", {"start": v(-51.23, -17.49) * mm, "end": v(-47.27, -13.62) * mm});
            skLineSegment(sketch, "E2736", {"start": v(-47.27, -13.62) * mm, "end": v(-43.2, -9.88) * mm});
            skLineSegment(sketch, "E2737", {"start": v(-43.2, -9.88) * mm, "end": v(-42.35, -9.17) * mm});
            skLineSegment(sketch, "E2738", {"start": v(-42.35, -9.17) * mm, "end": v(-40.43, -7.56) * mm});
            skLineSegment(sketch, "E2739", {"start": v(-40.43, -7.56) * mm, "end": v(-34.78, -2.62) * mm});
            skLineSegment(sketch, "E2740", {"start": v(-34.78, -2.62) * mm, "end": v(-27.36, 4.12) * mm});
            skLineSegment(sketch, "E2741", {"start": v(-27.36, 4.12) * mm, "end": v(-20.02, 10.94) * mm});
            skLineSegment(sketch, "E2742", {"start": v(-20.02, 10.94) * mm, "end": v(-12.69, 17.78) * mm});
            skLineSegment(sketch, "E2743", {"start": v(-12.69, 17.78) * mm, "end": v(-5.3, 24.55) * mm});
            skLineSegment(sketch, "E2744", {"start": v(-5.3, 24.55) * mm, "end": v(2.22, 31.16) * mm});
            skLineSegment(sketch, "E2745", {"start": v(2.22, 31.16) * mm, "end": v(9.93, 37.55) * mm});
            skLineSegment(sketch, "E2746", {"start": v(9.93, 37.55) * mm, "end": v(15.88, 42.14) * mm});
            skLineSegment(sketch, "E2747", {"start": v(15.88, 42.14) * mm, "end": v(17.91, 43.6) * mm});
            skLineSegment(sketch, "E2748", {"start": v(17.91, 43.6) * mm, "end": v(18.2, 43.8) * mm});
            skLineSegment(sketch, "E2749", {"start": v(18.2, 43.8) * mm, "end": v(18.3, 44.13) * mm});
            skLineSegment(sketch, "E2750", {"start": v(18.3, 44.13) * mm, "end": v(18.43, 44.53) * mm});
            skLineSegment(sketch, "E2751", {"start": v(18.43, 44.53) * mm, "end": v(19.17, 45.6) * mm});
            skLineSegment(sketch, "E2752", {"start": v(19.17, 45.6) * mm, "end": v(20.49, 46.81) * mm});
            skLineSegment(sketch, "E2753", {"start": v(20.49, 46.81) * mm, "end": v(21.95, 48) * mm});
            skLineSegment(sketch, "E2754", {"start": v(21.95, 48) * mm, "end": v(22.98, 49) * mm});
            skLineSegment(sketch, "E2755", {"start": v(22.98, 49) * mm, "end": v(23.26, 49.39) * mm});
            skLineSegment(sketch, "E2756", {"start": v(23.26, 49.39) * mm, "end": v(23.45, 49.4) * mm});
            skLineSegment(sketch, "E2757", {"start": v(23.45, 49.4) * mm, "end": v(24.26, 49.7) * mm});
            skLineSegment(sketch, "E2758", {"start": v(24.26, 49.7) * mm, "end": v(25.05, 50.17) * mm});
            skLineSegment(sketch, "E2759", {"start": v(25.05, 50.17) * mm, "end": v(25.24, 50.28) * mm});
            skLineSegment(sketch, "E2760", {"start": v(25.24, 50.28) * mm, "end": v(25.27, 50.3) * mm});
            skLineSegment(sketch, "E2761", {"start": v(25.27, 50.3) * mm, "end": v(25.6, 50.48) * mm});
            skLineSegment(sketch, "E2762", {"start": v(25.6, 50.48) * mm, "end": v(25.63, 50.49) * mm});
            skLineSegment(sketch, "E2763", {"start": v(25.63, 50.49) * mm, "end": v(25.84, 50.55) * mm});
            skLineSegment(sketch, "E2764", {"start": v(25.84, 50.55) * mm, "end": v(26.02, 50.7) * mm});
            skLineSegment(sketch, "E2765", {"start": v(26.02, 50.7) * mm, "end": v(30.06, 54.13) * mm});
            skLineSegment(sketch, "E2766", {"start": v(30.06, 54.13) * mm, "end": v(50.45, 71.17) * mm});
            skLineSegment(sketch, "E2767", {"start": v(50.45, 71.17) * mm, "end": v(71.3, 87.64) * mm});
            skLineSegment(sketch, "E2768", {"start": v(71.3, 87.64) * mm, "end": v(75.57, 90.8) * mm});
            skLineSegment(sketch, "E2769", {"start": v(75.57, 90.8) * mm, "end": v(76.61, 91.57) * mm});
            skLineSegment(sketch, "E2770", {"start": v(76.61, 91.57) * mm, "end": v(79.75, 93.88) * mm});
            skLineSegment(sketch, "E2771", {"start": v(79.75, 93.88) * mm, "end": v(84.09, 96.84) * mm});
            skLineSegment(sketch, "E2772", {"start": v(84.09, 96.84) * mm, "end": v(88.64, 99.39) * mm});
            skLineSegment(sketch, "E2773", {"start": v(88.64, 99.39) * mm, "end": v(92.24, 100.92) * mm});
            skLineSegment(sketch, "E2774", {"start": v(92.24, 100.92) * mm, "end": v(93.49, 101.28) * mm});
            skLineSegment(sketch, "E2775", {"start": v(93.49, 101.28) * mm, "end": v(93.57, 101.02) * mm});
            skLineSegment(sketch, "E2776", {"start": v(93.57, 101.02) * mm, "end": v(93.7, 100.2) * mm});
            skLineSegment(sketch, "E2777", {"start": v(93.7, 100.2) * mm, "end": v(93.74, 98.99) * mm});
            skLineSegment(sketch, "E2778", {"start": v(93.74, 98.99) * mm, "end": v(93.7, 97.76) * mm});
            skLineSegment(sketch, "E2779", {"start": v(93.7, 97.76) * mm, "end": v(93.64, 96.93) * mm});
            skLineSegment(sketch, "E2780", {"start": v(93.64, 96.93) * mm, "end": v(93.63, 96.65) * mm});
            skLineSegment(sketch, "E2781", {"start": v(93.63, 96.65) * mm, "end": v(92.55, 95.43) * mm});
            skLineSegment(sketch, "E2782", {"start": v(92.55, 95.43) * mm, "end": v(89.12, 91.96) * mm});
            skLineSegment(sketch, "E2783", {"start": v(89.12, 91.96) * mm, "end": v(84.32, 87.58) * mm});
            skLineSegment(sketch, "E2784", {"start": v(84.32, 87.58) * mm, "end": v(79.33, 83.41) * mm});
            skLineSegment(sketch, "E2785", {"start": v(79.33, 83.41) * mm, "end": v(74.24, 79.34) * mm});
            skLineSegment(sketch, "E2786", {"start": v(74.24, 79.34) * mm, "end": v(69.15, 75.27) * mm});
            skLineSegment(sketch, "E2787", {"start": v(69.15, 75.27) * mm, "end": v(64.17, 71.08) * mm});
            skLineSegment(sketch, "E2788", {"start": v(64.17, 71.08) * mm, "end": v(59.38, 66.66) * mm});
            skLineSegment(sketch, "E2789", {"start": v(59.38, 66.66) * mm, "end": v(55.97, 63.15) * mm});
            skLineSegment(sketch, "E2790", {"start": v(55.97, 63.15) * mm, "end": v(54.9, 61.92) * mm});
            skLineSegment(sketch, "E2791", {"start": v(54.9, 61.92) * mm, "end": v(54.67, 61.84) * mm});
            skLineSegment(sketch, "E2792", {"start": v(54.67, 61.84) * mm, "end": v(53.67, 61.22) * mm});
            skLineSegment(sketch, "E2793", {"start": v(53.67, 61.22) * mm, "end": v(52.78, 60.7) * mm});
            skLineSegment(sketch, "E2794", {"start": v(52.78, 60.7) * mm, "end": v(52.6, 60.66) * mm});
            skLineSegment(sketch, "E2795", {"start": v(52.6, 60.66) * mm, "end": v(52.26, 60.59) * mm});
            skLineSegment(sketch, "E2796", {"start": v(52.26, 60.59) * mm, "end": v(52.02, 60.34) * mm});
            skLineSegment(sketch, "E2797", {"start": v(52.02, 60.34) * mm, "end": v(50.9, 59.08) * mm});
            skLineSegment(sketch, "E2798", {"start": v(50.9, 59.08) * mm, "end": v(45.43, 52.61) * mm});
            skLineSegment(sketch, "E2799", {"start": v(45.43, 52.61) * mm, "end": v(40.03, 46.1) * mm});
            skLineSegment(sketch, "E2800", {"start": v(40.03, 46.1) * mm, "end": v(38.93, 44.8) * mm});
            skLineSegment(sketch, "E2801", {"start": v(38.93, 44.8) * mm, "end": v(37.51, 43.17) * mm});
            skLineSegment(sketch, "E2802", {"start": v(37.51, 43.17) * mm, "end": v(30, 35.4) * mm});
            skLineSegment(sketch, "E2803", {"start": v(30, 35.4) * mm, "end": v(22.37, 27.76) * mm});
            skLineSegment(sketch, "E2804", {"start": v(22.37, 27.76) * mm, "end": v(20.89, 26.18) * mm});
            skLineSegment(sketch, "E2805", {"start": v(20.89, 26.18) * mm, "end": v(20.03, 25.28) * mm});
            skLineSegment(sketch, "E2806", {"start": v(20.03, 25.28) * mm, "end": v(17.32, 22.68) * mm});
            skLineSegment(sketch, "E2807", {"start": v(17.32, 22.68) * mm, "end": v(13.56, 19.37) * mm});
            skLineSegment(sketch, "E2808", {"start": v(13.56, 19.37) * mm, "end": v(9.68, 16.16) * mm});
            skLineSegment(sketch, "E2809", {"start": v(9.68, 16.16) * mm, "end": v(5.75, 13) * mm});
            skLineSegment(sketch, "E2810", {"start": v(5.75, 13) * mm, "end": v(1.88, 9.78) * mm});
            skLineSegment(sketch, "E2811", {"start": v(1.88, 9.78) * mm, "end": v(-1.87, 6.44) * mm});
            skLineSegment(sketch, "E2812", {"start": v(-1.87, 6.44) * mm, "end": v(-5.4, 2.9) * mm});
            skLineSegment(sketch, "E2813", {"start": v(-5.4, 2.9) * mm, "end": v(-7.87, 0.1) * mm});
            skLineSegment(sketch, "E2814", {"start": v(-7.87, 0.1) * mm, "end": v(-8.63, -0.9) * mm});
            skLineSegment(sketch, "E2815", {"start": v(-8.63, -0.9) * mm, "end": v(-11.04, -2.91) * mm});
            skLineSegment(sketch, "E2816", {"start": v(-11.04, -2.91) * mm, "end": v(-22.9, -13.17) * mm});
            skLineSegment(sketch, "E2817", {"start": v(-22.9, -13.17) * mm, "end": v(-34.63, -23.6) * mm});
            skLineSegment(sketch, "E2818", {"start": v(-34.63, -23.6) * mm, "end": v(-36.96, -25.7) * mm});
            skLineSegment(sketch, "E2819", {"start": v(-36.96, -25.7) * mm, "end": v(-39.13, -27.66) * mm});
            skLineSegment(sketch, "E2820", {"start": v(-39.13, -27.66) * mm, "end": v(-36.22, -27.57) * mm});
            skLineSegment(sketch, "E2821", {"start": v(-36.22, -27.57) * mm, "end": v(-35.6, -27.55) * mm});
            skLineSegment(sketch, "E2822", {"start": v(-35.6, -27.55) * mm, "end": v(-29.42, -27.57) * mm});
            skLineSegment(sketch, "E2823", {"start": v(-29.42, -27.57) * mm, "end": v(-28.8, -27.6) * mm});
            skLineSegment(sketch, "E2824", {"start": v(-28.8, -27.6) * mm, "end": v(-28.36, -27.63) * mm});
            skLineSegment(sketch, "E2825", {"start": v(-28.36, -27.63) * mm, "end": v(-28.04, -27.33) * mm});
            skLineSegment(sketch, "E2826", {"start": v(-28.04, -27.33) * mm, "end": v(-27.95, -27.25) * mm});
            skLineSegment(sketch, "E2827", {"start": v(-27.95, -27.25) * mm, "end": v(-27.04, -26.47) * mm});
            skLineSegment(sketch, "E2828", {"start": v(-27.04, -26.47) * mm, "end": v(-26.95, -26.39) * mm});
            skLineSegment(sketch, "E2829", {"start": v(-26.95, -26.39) * mm, "end": v(-25.85, -25.41) * mm});
            skLineSegment(sketch, "E2830", {"start": v(-25.85, -25.41) * mm, "end": v(-20.4, -20.45) * mm});
            skLineSegment(sketch, "E2831", {"start": v(-20.4, -20.45) * mm, "end": v(-14.75, -15.7) * mm});
            skLineSegment(sketch, "E2832", {"start": v(-14.75, -15.7) * mm, "end": v(-13.57, -14.83) * mm});
            skLineSegment(sketch, "E2833", {"start": v(-13.57, -14.83) * mm, "end": v(-12.98, -14.38) * mm});
            skLineSegment(sketch, "E2834", {"start": v(-12.98, -14.38) * mm, "end": v(-9.83, -12.41) * mm});
            skLineSegment(sketch, "E2835", {"start": v(-9.83, -12.41) * mm, "end": v(-6.72, -10.37) * mm});
            skLineSegment(sketch, "E2836", {"start": v(-6.72, -10.37) * mm, "end": v(-6.15, -9.89) * mm});
            skLineSegment(sketch, "E2837", {"start": v(-6.15, -9.89) * mm, "end": v(-4.47, -8.41) * mm});
            skLineSegment(sketch, "E2838", {"start": v(-4.47, -8.41) * mm, "end": v(4.1, -1.3) * mm});
            skLineSegment(sketch, "E2839", {"start": v(4.1, -1.3) * mm, "end": v(13.03, 5.39) * mm});
            skLineSegment(sketch, "E2840", {"start": v(13.03, 5.39) * mm, "end": v(14.87, 6.64) * mm});
            skLineSegment(sketch, "E2841", {"start": v(14.87, 6.64) * mm, "end": v(14.93, 6.69) * mm});
            skLineSegment(sketch, "E2842", {"start": v(14.93, 6.69) * mm, "end": v(14.99, 6.73) * mm});
            skLineSegment(sketch, "E2843", {"start": v(14.99, 6.73) * mm, "end": v(18.28, 9.7) * mm});
            skLineSegment(sketch, "E2844", {"start": v(18.28, 9.7) * mm, "end": v(34.44, 24.86) * mm});
            skLineSegment(sketch, "E2845", {"start": v(34.44, 24.86) * mm, "end": v(50.39, 40.25) * mm});
            skLineSegment(sketch, "E2846", {"start": v(50.39, 40.25) * mm, "end": v(53.56, 43.33) * mm});
            skLineSegment(sketch, "E2847", {"start": v(53.56, 43.33) * mm, "end": v(54.62, 44.37) * mm});
            skLineSegment(sketch, "E2848", {"start": v(54.62, 44.37) * mm, "end": v(59.86, 49.68) * mm});
            skLineSegment(sketch, "E2849", {"start": v(59.86, 49.68) * mm, "end": v(65.35, 54.7) * mm});
            skLineSegment(sketch, "E2850", {"start": v(65.35, 54.7) * mm, "end": v(66.53, 55.6) * mm});
            skLineSegment(sketch, "E2851", {"start": v(66.53, 55.6) * mm, "end": v(68.6, 57.19) * mm});
            skLineSegment(sketch, "E2852", {"start": v(68.6, 57.19) * mm, "end": v(79.42, 64.6) * mm});
            skLineSegment(sketch, "E2853", {"start": v(79.42, 64.6) * mm, "end": v(90.43, 71.7) * mm});
            skLineSegment(sketch, "E2854", {"start": v(90.43, 71.7) * mm, "end": v(92.61, 73.15) * mm});
            skLineSegment(sketch, "E2855", {"start": v(92.61, 73.15) * mm, "end": v(92.78, 73.26) * mm});
            skLineSegment(sketch, "E2856", {"start": v(92.78, 73.26) * mm, "end": v(92.89, 73.41) * mm});
            skLineSegment(sketch, "E2857", {"start": v(92.89, 73.41) * mm, "end": v(93.37, 74.07) * mm});
            skLineSegment(sketch, "E2858", {"start": v(93.37, 74.07) * mm, "end": v(96.49, 77.11) * mm});
            skLineSegment(sketch, "E2859", {"start": v(96.49, 77.11) * mm, "end": v(100, 79.76) * mm});
            skLineSegment(sketch, "E2860", {"start": v(100, 79.76) * mm, "end": v(100.67, 80.21) * mm});
            skLineSegment(sketch, "E2861", {"start": v(100.67, 80.21) * mm, "end": v(101.34, 80.67) * mm});
            skLineSegment(sketch, "E2862", {"start": v(101.34, 80.67) * mm, "end": v(103.32, 82.13) * mm});
            skLineSegment(sketch, "E2863", {"start": v(103.32, 82.13) * mm, "end": v(106.31, 84.08) * mm});
            skLineSegment(sketch, "E2864", {"start": v(106.31, 84.08) * mm, "end": v(109.47, 85.28) * mm});
            skLineSegment(sketch, "E2865", {"start": v(109.47, 85.28) * mm, "end": v(111.94, 85.25) * mm});
            skLineSegment(sketch, "E2866", {"start": v(111.94, 85.25) * mm, "end": v(112.64, 84.95) * mm});
            skLineSegment(sketch, "E2867", {"start": v(112.64, 84.95) * mm, "end": v(112.1, 84.1) * mm});
            skLineSegment(sketch, "E2868", {"start": v(112.1, 84.1) * mm, "end": v(109.5, 79.7) * mm});
            skLineSegment(sketch, "E2869", {"start": v(109.5, 79.7) * mm, "end": v(106.66, 75.5) * mm});
            skLineSegment(sketch, "E2870", {"start": v(106.66, 75.5) * mm, "end": v(106, 74.76) * mm});
            skLineSegment(sketch, "E2871", {"start": v(106, 74.76) * mm, "end": v(105.73, 74.47) * mm});
            skLineSegment(sketch, "E2872", {"start": v(105.73, 74.47) * mm, "end": v(104.82, 73.75) * mm});
            skLineSegment(sketch, "E2873", {"start": v(104.82, 73.75) * mm, "end": v(103.5, 72.87) * mm});
            skLineSegment(sketch, "E2874", {"start": v(103.5, 72.87) * mm, "end": v(102.16, 71.97) * mm});
            skLineSegment(sketch, "E2875", {"start": v(102.16, 71.97) * mm, "end": v(101.22, 71.18) * mm});
            skLineSegment(sketch, "E2876", {"start": v(101.22, 71.18) * mm, "end": v(100.95, 70.88) * mm});
            skLineSegment(sketch, "E2877", {"start": v(100.95, 70.88) * mm, "end": v(100.77, 70.68) * mm});
            skLineSegment(sketch, "E2878", {"start": v(100.77, 70.68) * mm, "end": v(100.34, 70) * mm});
            skLineSegment(sketch, "E2879", {"start": v(100.34, 70) * mm, "end": v(99.9, 69.05) * mm});
            skLineSegment(sketch, "E2880", {"start": v(99.9, 69.05) * mm, "end": v(99.48, 68.14) * mm});
            skLineSegment(sketch, "E2881", {"start": v(99.48, 68.14) * mm, "end": v(99.11, 67.53) * mm});
            skLineSegment(sketch, "E2882", {"start": v(99.11, 67.53) * mm, "end": v(98.96, 67.36) * mm});
            skLineSegment(sketch, "E2883", {"start": v(98.96, 67.36) * mm, "end": v(98.38, 66.75) * mm});
            skLineSegment(sketch, "E2884", {"start": v(98.38, 66.75) * mm, "end": v(96.44, 65.07) * mm});
            skLineSegment(sketch, "E2885", {"start": v(96.44, 65.07) * mm, "end": v(93.69, 62.97) * mm});
            skLineSegment(sketch, "E2886", {"start": v(93.69, 62.97) * mm, "end": v(90.9, 60.88) * mm});
            skLineSegment(sketch, "E2887", {"start": v(90.9, 60.88) * mm, "end": v(88.88, 59.22) * mm});
            skLineSegment(sketch, "E2888", {"start": v(88.88, 59.22) * mm, "end": v(88.25, 58.62) * mm});
            skLineSegment(sketch, "E2889", {"start": v(88.25, 58.62) * mm, "end": v(87.4, 57.8) * mm});
            skLineSegment(sketch, "E2890", {"start": v(87.4, 57.8) * mm, "end": v(82.86, 54.09) * mm});
            skLineSegment(sketch, "E2891", {"start": v(82.86, 54.09) * mm, "end": v(78.36, 50.31) * mm});
            skLineSegment(sketch, "E2892", {"start": v(78.36, 50.31) * mm, "end": v(77.53, 49.47) * mm});
            skLineSegment(sketch, "E2893", {"start": v(77.53, 49.47) * mm, "end": v(75.93, 47.84) * mm});
            skLineSegment(sketch, "E2894", {"start": v(75.93, 47.84) * mm, "end": v(71.15, 42.91) * mm});
            skLineSegment(sketch, "E2895", {"start": v(71.15, 42.91) * mm, "end": v(64.46, 36.44) * mm});
            skLineSegment(sketch, "E2896", {"start": v(64.46, 36.44) * mm, "end": v(57.26, 30.65) * mm});
            skLineSegment(sketch, "E2897", {"start": v(57.26, 30.65) * mm, "end": v(51.43, 27.03) * mm});
            skLineSegment(sketch, "E2898", {"start": v(51.43, 27.03) * mm, "end": v(49.36, 26.1) * mm});
            skLineSegment(sketch, "E2899", {"start": v(49.36, 26.1) * mm, "end": v(49, 25.94) * mm});
            skLineSegment(sketch, "E2900", {"start": v(49, 25.94) * mm, "end": v(48.82, 25.56) * mm});
            skLineSegment(sketch, "E2901", {"start": v(48.82, 25.56) * mm, "end": v(48.36, 24.54) * mm});
            skLineSegment(sketch, "E2902", {"start": v(48.36, 24.54) * mm, "end": v(46.53, 19.21) * mm});
            skLineSegment(sketch, "E2903", {"start": v(46.53, 19.21) * mm, "end": v(44.63, 13.92) * mm});
            skLineSegment(sketch, "E2904", {"start": v(44.63, 13.92) * mm, "end": v(44.14, 12.9) * mm});
            skLineSegment(sketch, "E2905", {"start": v(44.14, 12.9) * mm, "end": v(43.77, 12.14) * mm});
            skLineSegment(sketch, "E2906", {"start": v(43.77, 12.14) * mm, "end": v(42.4, 9.96) * mm});
            skLineSegment(sketch, "E2907", {"start": v(42.4, 9.96) * mm, "end": v(40.63, 7.23) * mm});
            skLineSegment(sketch, "E2908", {"start": v(40.63, 7.23) * mm, "end": v(39.34, 4.3) * mm});
            skLineSegment(sketch, "E2909", {"start": v(39.34, 4.3) * mm, "end": v(38.95, 1.63) * mm});
            skLineSegment(sketch, "E2910", {"start": v(38.95, 1.63) * mm, "end": v(39.03, 0.75) * mm});
            skLineSegment(sketch, "E2911", {"start": v(39.03, 0.75) * mm, "end": v(39.1, 0.07) * mm});
            skLineSegment(sketch, "E2912", {"start": v(39.1, 0.07) * mm, "end": v(39.73, -0.17) * mm});
            skLineSegment(sketch, "E2913", {"start": v(39.73, -0.17) * mm, "end": v(40.13, -0.31) * mm});
            skLineSegment(sketch, "E2914", {"start": v(40.13, -0.31) * mm, "end": v(41.42, -0.48) * mm});
            skLineSegment(sketch, "E2915", {"start": v(41.42, -0.48) * mm, "end": v(42.9, -0.2) * mm});
            skLineSegment(sketch, "E2916", {"start": v(42.9, -0.2) * mm, "end": v(44.22, 0.5) * mm});
            skLineSegment(sketch, "E2917", {"start": v(44.22, 0.5) * mm, "end": v(45.44, 1.52) * mm});
            skLineSegment(sketch, "E2918", {"start": v(45.44, 1.52) * mm, "end": v(46.6, 2.7) * mm});
            skLineSegment(sketch, "E2919", {"start": v(46.6, 2.7) * mm, "end": v(47.77, 3.9) * mm});
            skLineSegment(sketch, "E2920", {"start": v(47.77, 3.9) * mm, "end": v(48.97, 5) * mm});
            skLineSegment(sketch, "E2921", {"start": v(48.97, 5) * mm, "end": v(49.92, 5.66) * mm});
            skLineSegment(sketch, "E2922", {"start": v(49.92, 5.66) * mm, "end": v(50.27, 5.83) * mm});
            skLineSegment(sketch, "E2923", {"start": v(50.27, 5.83) * mm, "end": v(50.83, 6.1) * mm});
            skLineSegment(sketch, "E2924", {"start": v(50.83, 6.1) * mm, "end": v(52.55, 6.87) * mm});
            skLineSegment(sketch, "E2925", {"start": v(52.55, 6.87) * mm, "end": v(55.2, 7.9) * mm});
            skLineSegment(sketch, "E2926", {"start": v(55.2, 7.9) * mm, "end": v(57.9, 8.75) * mm});
            skLineSegment(sketch, "E2927", {"start": v(57.9, 8.75) * mm, "end": v(59.72, 9.18) * mm});
            skLineSegment(sketch, "E2928", {"start": v(59.72, 9.18) * mm, "end": v(60.34, 9.26) * mm});
            skLineSegment(sketch, "E2929", {"start": v(60.34, 9.26) * mm, "end": v(60.5, 9.28) * mm});
            skLineSegment(sketch, "E2930", {"start": v(60.5, 9.28) * mm, "end": v(61, 9.34) * mm});
            skLineSegment(sketch, "E2931", {"start": v(61, 9.34) * mm, "end": v(61.74, 9.4) * mm});
            skLineSegment(sketch, "E2932", {"start": v(61.74, 9.4) * mm, "end": v(62.52, 9.42) * mm});
            skLineSegment(sketch, "E2933", {"start": v(62.52, 9.42) * mm, "end": v(63.3, 9.37) * mm});
            skLineSegment(sketch, "E2934", {"start": v(63.3, 9.37) * mm, "end": v(64.03, 9.23) * mm});
            skLineSegment(sketch, "E2935", {"start": v(64.03, 9.23) * mm, "end": v(64.7, 8.97) * mm});
            skLineSegment(sketch, "E2936", {"start": v(64.7, 8.97) * mm, "end": v(65.26, 8.56) * mm});
            skLineSegment(sketch, "E2937", {"start": v(65.26, 8.56) * mm, "end": v(65.6, 8.15) * mm});
            skLineSegment(sketch, "E2938", {"start": v(65.6, 8.15) * mm, "end": v(65.68, 8) * mm});
            skLineSegment(sketch, "E2939", {"start": v(65.68, 8) * mm, "end": v(65.01, 7.06) * mm});
            skLineSegment(sketch, "E2940", {"start": v(65.01, 7.06) * mm, "end": v(61.1, 2.55) * mm});
            skLineSegment(sketch, "E2941", {"start": v(61.1, 2.55) * mm, "end": v(56.72, -1.5) * mm});
            skLineSegment(sketch, "E2942", {"start": v(56.72, -1.5) * mm, "end": v(55.83, -2.2) * mm});
            skLineSegment(sketch, "E2943", {"start": v(55.83, -2.2) * mm, "end": v(55.6, -2.39) * mm});
            skLineSegment(sketch, "E2944", {"start": v(55.6, -2.39) * mm, "end": v(54.8, -2.87) * mm});
            skLineSegment(sketch, "E2945", {"start": v(54.8, -2.87) * mm, "end": v(53.74, -3.45) * mm});
            skLineSegment(sketch, "E2946", {"start": v(53.74, -3.45) * mm, "end": v(52.76, -4.16) * mm});
            skLineSegment(sketch, "E2947", {"start": v(52.76, -4.16) * mm, "end": v(52.12, -4.95) * mm});
            skLineSegment(sketch, "E2948", {"start": v(52.12, -4.95) * mm, "end": v(51.98, -5.24) * mm});
            skLineSegment(sketch, "E2949", {"start": v(51.98, -5.24) * mm, "end": v(51.85, -5.51) * mm});
            skLineSegment(sketch, "E2950", {"start": v(51.85, -5.51) * mm, "end": v(51.69, -6.9) * mm});
            skLineSegment(sketch, "E2951", {"start": v(51.69, -6.9) * mm, "end": v(52.07, -8.24) * mm});
            skLineSegment(sketch, "E2952", {"start": v(52.07, -8.24) * mm, "end": v(52.2, -8.5) * mm});
            skLineSegment(sketch, "E2953", {"start": v(52.2, -8.5) * mm, "end": v(52.36, -8.8) * mm});
            skLineSegment(sketch, "E2954", {"start": v(52.36, -8.8) * mm, "end": v(52.66, -8.95) * mm});
            skLineSegment(sketch, "E2955", {"start": v(52.66, -8.95) * mm, "end": v(53.3, -9.26) * mm});
            skLineSegment(sketch, "E2956", {"start": v(53.3, -9.26) * mm, "end": v(55.52, -9.53) * mm});
            skLineSegment(sketch, "E2957", {"start": v(55.52, -9.53) * mm, "end": v(58.13, -8.71) * mm});
            skLineSegment(sketch, "E2958", {"start": v(58.13, -8.71) * mm, "end": v(60.6, -7.2) * mm});
            skLineSegment(sketch, "E2959", {"start": v(60.6, -7.2) * mm, "end": v(62.37, -6.06) * mm});
            skLineSegment(sketch, "E2960", {"start": v(62.37, -6.06) * mm, "end": v(63, -5.75) * mm});
            skLineSegment(sketch, "E2961", {"start": v(63, -5.75) * mm, "end": v(63.81, -5.35) * mm});
            skLineSegment(sketch, "E2962", {"start": v(63.81, -5.35) * mm, "end": v(68.03, -3.75) * mm});
            skLineSegment(sketch, "E2963", {"start": v(68.03, -3.75) * mm, "end": v(72.2, -2.04) * mm});
            skLineSegment(sketch, "E2964", {"start": v(72.2, -2.04) * mm, "end": v(73, -1.59) * mm});
            skLineSegment(sketch, "E2965", {"start": v(73, -1.59) * mm, "end": v(73.33, -1.5) * mm});
            skLineSegment(sketch, "E2966", {"start": v(73.33, -1.5) * mm, "end": v(74.36, -1.27) * mm});
            skLineSegment(sketch, "E2967", {"start": v(74.36, -1.27) * mm, "end": v(76.02, -0.97) * mm});
            skLineSegment(sketch, "E2968", {"start": v(76.02, -0.97) * mm, "end": v(77.85, -0.74) * mm});
            skLineSegment(sketch, "E2969", {"start": v(77.85, -0.74) * mm, "end": v(79.75, -0.63) * mm});
            skLineSegment(sketch, "E2970", {"start": v(79.75, -0.63) * mm, "end": v(81.6, -0.68) * mm});
            skLineSegment(sketch, "E2971", {"start": v(81.6, -0.68) * mm, "end": v(83.32, -0.95) * mm});
            skLineSegment(sketch, "E2972", {"start": v(83.32, -0.95) * mm, "end": v(84.78, -1.49) * mm});
            skLineSegment(sketch, "E2973", {"start": v(84.78, -1.49) * mm, "end": v(85.64, -2.07) * mm});
            skLineSegment(sketch, "E2974", {"start": v(85.64, -2.07) * mm, "end": v(85.87, -2.33) * mm});
            skLineSegment(sketch, "E2975", {"start": v(85.87, -2.33) * mm, "end": v(86, -2.49) * mm});
            skLineSegment(sketch, "E2976", {"start": v(86, -2.49) * mm, "end": v(86.24, -3.1) * mm});
            skLineSegment(sketch, "E2977", {"start": v(86.24, -3.1) * mm, "end": v(86.27, -4) * mm});
            skLineSegment(sketch, "E2978", {"start": v(86.27, -4) * mm, "end": v(86.09, -4.92) * mm});
            skLineSegment(sketch, "E2979", {"start": v(86.09, -4.92) * mm, "end": v(85.89, -5.53) * mm});
            skLineSegment(sketch, "E2980", {"start": v(85.89, -5.53) * mm, "end": v(85.81, -5.74) * mm});
            skLineSegment(sketch, "E2981", {"start": v(85.81, -5.74) * mm, "end": v(85.34, -6.94) * mm});
            skLineSegment(sketch, "E2982", {"start": v(85.34, -6.94) * mm, "end": v(86.61, -7.17) * mm});
            skLineSegment(sketch, "E2983", {"start": v(86.61, -7.17) * mm, "end": v(87, -7.25) * mm});
            skLineSegment(sketch, "E2984", {"start": v(87, -7.25) * mm, "end": v(89.03, -7.78) * mm});
            skLineSegment(sketch, "E2985", {"start": v(89.03, -7.78) * mm, "end": v(90.97, -8.56) * mm});
            skLineSegment(sketch, "E2986", {"start": v(90.97, -8.56) * mm, "end": v(91.33, -8.76) * mm});
            skLineSegment(sketch, "E2987", {"start": v(91.33, -8.76) * mm, "end": v(91.65, -8.93) * mm});
            skLineSegment(sketch, "E2988", {"start": v(91.65, -8.93) * mm, "end": v(92.02, -8.87) * mm});
            skLineSegment(sketch, "E2989", {"start": v(92.02, -8.87) * mm, "end": v(92.3, -8.82) * mm});
            skLineSegment(sketch, "E2990", {"start": v(92.3, -8.82) * mm, "end": v(95.16, -8.2) * mm});
            skLineSegment(sketch, "E2991", {"start": v(95.16, -8.2) * mm, "end": v(95.45, -8.14) * mm});
            skLineSegment(sketch, "E2992", {"start": v(95.45, -8.14) * mm, "end": v(96.82, -7.84) * mm});
            skLineSegment(sketch, "E2993", {"start": v(96.82, -7.84) * mm, "end": v(96.16, -6.6) * mm});
            skLineSegment(sketch, "E2994", {"start": v(96.16, -6.6) * mm, "end": v(96, -6.3) * mm});
            skLineSegment(sketch, "E2995", {"start": v(96, -6.3) * mm, "end": v(95.39, -5.48) * mm});
            skLineSegment(sketch, "E2996", {"start": v(95.39, -5.48) * mm, "end": v(94.44, -4.49) * mm});
            skLineSegment(sketch, "E2997", {"start": v(94.44, -4.49) * mm, "end": v(93.44, -3.5) * mm});
            skLineSegment(sketch, "E2998", {"start": v(93.44, -3.5) * mm, "end": v(92.75, -2.71) * mm});
            skLineSegment(sketch, "E2999", {"start": v(92.75, -2.71) * mm, "end": v(92.56, -2.43) * mm});
            skLineSegment(sketch, "E3000", {"start": v(92.56, -2.43) * mm, "end": v(92.2, -1.89) * mm});
            skLineSegment(sketch, "E3001", {"start": v(92.2, -1.89) * mm, "end": v(91.22, -0.2) * mm});
            skLineSegment(sketch, "E3002", {"start": v(91.22, -0.2) * mm, "end": v(89.9, 2.17) * mm});
            skLineSegment(sketch, "E3003", {"start": v(89.9, 2.17) * mm, "end": v(88.42, 4.4) * mm});
            skLineSegment(sketch, "E3004", {"start": v(88.42, 4.4) * mm, "end": v(87.15, 5.85) * mm});
            skLineSegment(sketch, "E3005", {"start": v(87.15, 5.85) * mm, "end": v(86.65, 6.24) * mm});
            skLineSegment(sketch, "E3006", {"start": v(86.65, 6.24) * mm, "end": v(86.41, 6.42) * mm});
            skLineSegment(sketch, "E3007", {"start": v(86.41, 6.42) * mm, "end": v(85.64, 6.88) * mm});
            skLineSegment(sketch, "E3008", {"start": v(85.64, 6.88) * mm, "end": v(84.58, 7.36) * mm});
            skLineSegment(sketch, "E3009", {"start": v(84.58, 7.36) * mm, "end": v(83.55, 7.82) * mm});
            skLineSegment(sketch, "E3010", {"start": v(83.55, 7.82) * mm, "end": v(82.84, 8.21) * mm});
            skLineSegment(sketch, "E3011", {"start": v(82.84, 8.21) * mm, "end": v(82.62, 8.37) * mm});
            skLineSegment(sketch, "E3012", {"start": v(82.62, 8.37) * mm, "end": v(82.3, 8.61) * mm});
            skLineSegment(sketch, "E3013", {"start": v(82.3, 8.61) * mm, "end": v(81.48, 9.46) * mm});
            skLineSegment(sketch, "E3014", {"start": v(81.48, 9.46) * mm, "end": v(80.43, 10.69) * mm});
            skLineSegment(sketch, "E3015", {"start": v(80.43, 10.69) * mm, "end": v(79.34, 11.84) * mm});
            skLineSegment(sketch, "E3016", {"start": v(79.34, 11.84) * mm, "end": v(78.4, 12.54) * mm});
            skLineSegment(sketch, "E3017", {"start": v(78.4, 12.54) * mm, "end": v(78.06, 12.7) * mm});
            skLineSegment(sketch, "E3018", {"start": v(78.06, 12.7) * mm, "end": v(77.82, 12.81) * mm});
            skLineSegment(sketch, "E3019", {"start": v(77.82, 12.81) * mm, "end": v(77.04, 13.01) * mm});
            skLineSegment(sketch, "E3020", {"start": v(77.04, 13.01) * mm, "end": v(76, 13.12) * mm});
            skLineSegment(sketch, "E3021", {"start": v(76, 13.12) * mm, "end": v(74.97, 13.2) * mm});
            skLineSegment(sketch, "E3022", {"start": v(74.97, 13.2) * mm, "end": v(74.23, 13.35) * mm});
            skLineSegment(sketch, "E3023", {"start": v(74.23, 13.35) * mm, "end": v(74, 13.44) * mm});
            skLineSegment(sketch, "E3024", {"start": v(74, 13.44) * mm, "end": v(73.83, 13.5) * mm});
            skLineSegment(sketch, "E3025", {"start": v(73.83, 13.5) * mm, "end": v(72.3, 14.32) * mm});
            skLineSegment(sketch, "E3026", {"start": v(72.3, 14.32) * mm, "end": v(72.15, 14.42) * mm});
            skLineSegment(sketch, "E3027", {"start": v(72.15, 14.42) * mm, "end": v(71.66, 14.74) * mm});
            skLineSegment(sketch, "E3028", {"start": v(71.66, 14.74) * mm, "end": v(70.18, 15.74) * mm});
            skLineSegment(sketch, "E3029", {"start": v(70.18, 15.74) * mm, "end": v(68.38, 16.81) * mm});
            skLineSegment(sketch, "E3030", {"start": v(68.38, 16.81) * mm, "end": v(66.44, 17.53) * mm});
            skLineSegment(sketch, "E3031", {"start": v(66.44, 17.53) * mm, "end": v(64.67, 17.78) * mm});
            skLineSegment(sketch, "E3032", {"start": v(64.67, 17.78) * mm, "end": v(64.09, 17.77) * mm});
            skLineSegment(sketch, "E3033", {"start": v(64.09, 17.77) * mm, "end": v(63.96, 17.92) * mm});
            skLineSegment(sketch, "E3034", {"start": v(63.96, 17.92) * mm, "end": v(63.52, 18.33) * mm});
            skLineSegment(sketch, "E3035", {"start": v(63.52, 18.33) * mm, "end": v(62.87, 18.8) * mm});
            skLineSegment(sketch, "E3036", {"start": v(62.87, 18.8) * mm, "end": v(62.2, 19.2) * mm});
            skLineSegment(sketch, "E3037", {"start": v(62.2, 19.2) * mm, "end": v(61.53, 19.55) * mm});
            skLineSegment(sketch, "E3038", {"start": v(61.53, 19.55) * mm, "end": v(60.91, 19.88) * mm});
            skLineSegment(sketch, "E3039", {"start": v(60.91, 19.88) * mm, "end": v(60.42, 20.2) * mm});
            skLineSegment(sketch, "E3040", {"start": v(60.42, 20.2) * mm, "end": v(60.07, 20.56) * mm});
            skLineSegment(sketch, "E3041", {"start": v(60.07, 20.56) * mm, "end": v(59.93, 20.87) * mm});
            skLineSegment(sketch, "E3042", {"start": v(59.93, 20.87) * mm, "end": v(59.92, 20.97) * mm});
            skLineSegment(sketch, "E3043", {"start": v(59.92, 20.97) * mm, "end": v(59.91, 21.07) * mm});
            skLineSegment(sketch, "E3044", {"start": v(59.91, 21.07) * mm, "end": v(59.94, 21.62) * mm});
            skLineSegment(sketch, "E3045", {"start": v(59.94, 21.62) * mm, "end": v(60.14, 22.12) * mm});
            skLineSegment(sketch, "E3046", {"start": v(60.14, 22.12) * mm, "end": v(60.21, 22.2) * mm});
            skLineSegment(sketch, "E3047", {"start": v(60.21, 22.2) * mm, "end": v(60.38, 22.38) * mm});
            skLineSegment(sketch, "E3048", {"start": v(60.38, 22.38) * mm, "end": v(61.16, 22.69) * mm});
            skLineSegment(sketch, "E3049", {"start": v(61.16, 22.69) * mm, "end": v(62.54, 22.93) * mm});
            skLineSegment(sketch, "E3050", {"start": v(62.54, 22.93) * mm, "end": v(63.99, 23) * mm});
            skLineSegment(sketch, "E3051", {"start": v(63.99, 23) * mm, "end": v(64.83, 23.02) * mm});
            skLineSegment(sketch, "E3052", {"start": v(64.83, 23.02) * mm, "end": v(65.11, 23.03) * mm});
            skLineSegment(sketch, "E3053", {"start": v(65.11, 23.03) * mm, "end": v(65.5, 23.04) * mm});
            skLineSegment(sketch, "E3054", {"start": v(65.5, 23.04) * mm, "end": v(66.65, 23.1) * mm});
            skLineSegment(sketch, "E3055", {"start": v(66.65, 23.1) * mm, "end": v(68.26, 23.3) * mm});
            skLineSegment(sketch, "E3056", {"start": v(68.26, 23.3) * mm, "end": v(69.77, 23.75) * mm});
            skLineSegment(sketch, "E3057", {"start": v(69.77, 23.75) * mm, "end": v(70.78, 24.32) * mm});
            skLineSegment(sketch, "E3058", {"start": v(70.78, 24.32) * mm, "end": v(71.05, 24.58) * mm});
            skLineSegment(sketch, "E3059", {"start": v(71.05, 24.58) * mm, "end": v(71.1, 24.62) * mm});
            skLineSegment(sketch, "E3060", {"start": v(71.1, 24.62) * mm, "end": v(71.54, 25.14) * mm});
            skLineSegment(sketch, "E3061", {"start": v(71.54, 25.14) * mm, "end": v(71.58, 25.2) * mm});
            skLineSegment(sketch, "E3062", {"start": v(71.58, 25.2) * mm, "end": v(73.3, 25.45) * mm});
            skLineSegment(sketch, "E3063", {"start": v(73.3, 25.45) * mm, "end": v(78.54, 25.9) * mm});
            skLineSegment(sketch, "E3064", {"start": v(78.54, 25.9) * mm, "end": v(85.5, 26.15) * mm});
            skLineSegment(sketch, "E3065", {"start": v(85.5, 26.15) * mm, "end": v(92.48, 26.25) * mm});
            skLineSegment(sketch, "E3066", {"start": v(92.48, 26.25) * mm, "end": v(97.71, 26.4) * mm});
            skLineSegment(sketch, "E3067", {"start": v(97.71, 26.4) * mm, "end": v(99.45, 26.52) * mm});
            skLineSegment(sketch, "E3068", {"start": v(99.45, 26.52) * mm, "end": v(100.07, 26.56) * mm});
            skLineSegment(sketch, "E3069", {"start": v(100.07, 26.56) * mm, "end": v(101.93, 26.86) * mm});
            skLineSegment(sketch, "E3070", {"start": v(101.93, 26.86) * mm, "end": v(104.46, 27.4) * mm});
            skLineSegment(sketch, "E3071", {"start": v(104.46, 27.4) * mm, "end": v(106.96, 27.84) * mm});
            skLineSegment(sketch, "E3072", {"start": v(106.96, 27.84) * mm, "end": v(108.76, 27.99) * mm});
            skLineSegment(sketch, "E3073", {"start": v(108.76, 27.99) * mm, "end": v(109.36, 27.94) * mm});
            skLineSegment(sketch, "E3074", {"start": v(109.36, 27.94) * mm, "end": v(109.66, 27.92) * mm});
            skLineSegment(sketch, "E3075", {"start": v(109.66, 27.92) * mm, "end": v(110.55, 27.7) * mm});
            skLineSegment(sketch, "E3076", {"start": v(110.55, 27.7) * mm, "end": v(111.7, 27.33) * mm});
            skLineSegment(sketch, "E3077", {"start": v(111.7, 27.33) * mm, "end": v(112.87, 26.98) * mm});
            skLineSegment(sketch, "E3078", {"start": v(112.87, 26.98) * mm, "end": v(113.85, 26.83) * mm});
            skLineSegment(sketch, "E3079", {"start": v(113.85, 26.83) * mm, "end": v(114.17, 26.83) * mm});
            skLineSegment(sketch, "E3080", {"start": v(114.17, 26.83) * mm, "end": v(114.96, 26.85) * mm});
            skLineSegment(sketch, "E3081", {"start": v(114.96, 26.85) * mm, "end": v(117.31, 27.27) * mm});
            skLineSegment(sketch, "E3082", {"start": v(117.31, 27.27) * mm, "end": v(120.18, 28.2) * mm});
            skLineSegment(sketch, "E3083", {"start": v(120.18, 28.2) * mm, "end": v(122.97, 29.36) * mm});
            skLineSegment(sketch, "E3084", {"start": v(122.97, 29.36) * mm, "end": v(125.13, 30.22) * mm});
            skLineSegment(sketch, "E3085", {"start": v(125.13, 30.22) * mm, "end": v(125.87, 30.45) * mm});
            skLineSegment(sketch, "E3086", {"start": v(125.87, 30.45) * mm, "end": v(127.27, 30.88) * mm});
            skLineSegment(sketch, "E3087", {"start": v(127.27, 30.88) * mm, "end": v(131.47, 32.07) * mm});
            skLineSegment(sketch, "E3088", {"start": v(131.47, 32.07) * mm, "end": v(137.15, 33.73) * mm});
            skLineSegment(sketch, "E3089", {"start": v(137.15, 33.73) * mm, "end": v(142.7, 35.7) * mm});
            skLineSegment(sketch, "E3090", {"start": v(142.7, 35.7) * mm, "end": v(146.66, 37.53) * mm});
            skLineSegment(sketch, "E3091", {"start": v(146.66, 37.53) * mm, "end": v(147.9, 38.27) * mm});
            skLineSegment(sketch, "E3092", {"start": v(147.9, 38.27) * mm, "end": v(148.26, 38.49) * mm});
            skLineSegment(sketch, "E3093", {"start": v(148.26, 38.49) * mm, "end": v(149.27, 39.24) * mm});
            skLineSegment(sketch, "E3094", {"start": v(149.27, 39.24) * mm, "end": v(150.55, 40.35) * mm});
            skLineSegment(sketch, "E3095", {"start": v(150.55, 40.35) * mm, "end": v(151.79, 41.5) * mm});
            skLineSegment(sketch, "E3096", {"start": v(151.79, 41.5) * mm, "end": v(152.72, 42.35) * mm});
            skLineSegment(sketch, "E3097", {"start": v(152.72, 42.35) * mm, "end": v(153.05, 42.62) * mm});
            skLineSegment(sketch, "E3098", {"start": v(153.05, 42.62) * mm, "end": v(153.6, 43.07) * mm});
            skLineSegment(sketch, "E3099", {"start": v(153.6, 43.07) * mm, "end": v(155.3, 44.36) * mm});
            skLineSegment(sketch, "E3100", {"start": v(155.3, 44.36) * mm, "end": v(157.28, 45.96) * mm});
            skLineSegment(sketch, "E3101", {"start": v(157.28, 45.96) * mm, "end": v(158.97, 47.84) * mm});
            skLineSegment(sketch, "E3102", {"start": v(158.97, 47.84) * mm, "end": v(160.12, 49.74) * mm});
            skLineSegment(sketch, "E3103", {"start": v(160.12, 49.74) * mm, "end": v(160.4, 50.42) * mm});
            skLineSegment(sketch, "E3104", {"start": v(160.4, 50.42) * mm, "end": v(160.57, 50.83) * mm});
            skLineSegment(sketch, "E3105", {"start": v(160.57, 50.83) * mm, "end": v(160.39, 51.25) * mm});
            skLineSegment(sketch, "E3106", {"start": v(160.39, 51.25) * mm, "end": v(160.25, 51.58) * mm});
            skLineSegment(sketch, "E3107", {"start": v(160.25, 51.58) * mm, "end": v(160.02, 52.65) * mm});
            skLineSegment(sketch, "E3108", {"start": v(160.02, 52.65) * mm, "end": v(159.83, 54.16) * mm});
            skLineSegment(sketch, "E3109", {"start": v(159.83, 54.16) * mm, "end": v(159.56, 55.67) * mm});
            skLineSegment(sketch, "E3110", {"start": v(159.56, 55.67) * mm, "end": v(159.14, 56.75) * mm});
            skLineSegment(sketch, "E3111", {"start": v(159.14, 56.75) * mm, "end": v(158.93, 57.06) * mm});
            skLineSegment(sketch, "E3112", {"start": v(158.93, 57.06) * mm, "end": v(158.75, 57.3) * mm});
            skLineSegment(sketch, "E3113", {"start": v(158.75, 57.3) * mm, "end": v(158.47, 57.44) * mm});
            skLineSegment(sketch, "E3114", {"start": v(158.47, 57.44) * mm, "end": v(156.58, 58.24) * mm});
            skLineSegment(sketch, "E3115", {"start": v(156.58, 58.24) * mm, "end": v(151.17, 61.3) * mm});
            skLineSegment(sketch, "E3116", {"start": v(151.17, 61.3) * mm, "end": v(144.75, 66.14) * mm});
            skLineSegment(sketch, "E3117", {"start": v(144.75, 66.14) * mm, "end": v(139, 71.8) * mm});
            skLineSegment(sketch, "E3118", {"start": v(139, 71.8) * mm, "end": v(135.02, 76.5) * mm});
            skLineSegment(sketch, "E3119", {"start": v(135.02, 76.5) * mm, "end": v(133.78, 78.14) * mm});
            skLineSegment(sketch, "E3120", {"start": v(133.78, 78.14) * mm, "end": v(133.98, 78.88) * mm});
            skLineSegment(sketch, "E3121", {"start": v(133.98, 78.88) * mm, "end": v(133.95, 81.3) * mm});
            skLineSegment(sketch, "E3122", {"start": v(133.95, 81.3) * mm, "end": v(132.99, 84) * mm});
            skLineSegment(sketch, "E3123", {"start": v(132.99, 84) * mm, "end": v(131.64, 86.6) * mm});
            skLineSegment(sketch, "E3124", {"start": v(131.64, 86.6) * mm, "end": v(130.8, 88.69) * mm});
            skLineSegment(sketch, "E3125", {"start": v(130.8, 88.69) * mm, "end": v(130.67, 89.4) * mm});
            skLineSegment(sketch, "E3126", {"start": v(130.67, 89.4) * mm, "end": v(130.9, 90) * mm});
            skLineSegment(sketch, "E3127", {"start": v(130.9, 90) * mm, "end": v(131.1, 92.73) * mm});
            skLineSegment(sketch, "E3128", {"start": v(131.1, 92.73) * mm, "end": v(130.39, 95.43) * mm});
            skLineSegment(sketch, "E3129", {"start": v(130.39, 95.43) * mm, "end": v(130.18, 96) * mm});
            skLineSegment(sketch, "E3130", {"start": v(130.18, 96) * mm, "end": v(130.1, 96.2) * mm});
            skLineSegment(sketch, "E3131", {"start": v(130.1, 96.2) * mm, "end": v(129.42, 98.28) * mm});
            skLineSegment(sketch, "E3132", {"start": v(129.42, 98.28) * mm, "end": v(129.38, 98.5) * mm});
            skLineSegment(sketch, "E3133", {"start": v(129.38, 98.5) * mm, "end": v(129.35, 98.62) * mm});
            skLineSegment(sketch, "E3134", {"start": v(129.35, 98.62) * mm, "end": v(129.27, 99.87) * mm});
            skLineSegment(sketch, "E3135", {"start": v(129.27, 99.87) * mm, "end": v(129.28, 100) * mm});
            skLineSegment(sketch, "E3136", {"start": v(129.28, 100) * mm, "end": v(129.34, 100.62) * mm});
            skLineSegment(sketch, "E3137", {"start": v(129.34, 100.62) * mm, "end": v(128.82, 100.99) * mm});
            skLineSegment(sketch, "E3138", {"start": v(128.82, 100.99) * mm, "end": v(128.07, 101.48) * mm});
            skLineSegment(sketch, "E3139", {"start": v(128.07, 101.48) * mm, "end": v(125.84, 102.97) * mm});
            skLineSegment(sketch, "E3140", {"start": v(125.84, 102.97) * mm, "end": v(122.87, 105.11) * mm});
            skLineSegment(sketch, "E3141", {"start": v(122.87, 105.11) * mm, "end": v(120.14, 107.51) * mm});
            skLineSegment(sketch, "E3142", {"start": v(120.14, 107.51) * mm, "end": v(118.35, 109.53) * mm});
            skLineSegment(sketch, "E3143", {"start": v(118.35, 109.53) * mm, "end": v(117.85, 110.27) * mm});
            skLineSegment(sketch, "E3144", {"start": v(117.85, 110.27) * mm, "end": v(117.42, 110.94) * mm});
            skLineSegment(sketch, "E3145", {"start": v(117.42, 110.94) * mm, "end": v(116.4, 113.15) * mm});
            skLineSegment(sketch, "E3146", {"start": v(116.4, 113.15) * mm, "end": v(115.75, 116.11) * mm});
            skLineSegment(sketch, "E3147", {"start": v(115.75, 116.11) * mm, "end": v(115.8, 119.17) * mm});
            skLineSegment(sketch, "E3148", {"start": v(115.8, 119.17) * mm, "end": v(116.28, 121.55) * mm});
            skLineSegment(sketch, "E3149", {"start": v(116.28, 121.55) * mm, "end": v(116.52, 122.3) * mm});
            skLineSegment(sketch, "E3150", {"start": v(116.52, 122.3) * mm, "end": v(116.7, 122.88) * mm});
            skLineSegment(sketch, "E3151", {"start": v(116.7, 122.88) * mm, "end": v(116.32, 123.32) * mm});
            skLineSegment(sketch, "E3152", {"start": v(116.32, 123.32) * mm, "end": v(115.84, 123.9) * mm});
            skLineSegment(sketch, "E3153", {"start": v(115.84, 123.9) * mm, "end": v(114.05, 125.34) * mm});
            skLineSegment(sketch, "E3154", {"start": v(114.05, 125.34) * mm, "end": v(111.35, 126.78) * mm});
            skLineSegment(sketch, "E3155", {"start": v(111.35, 126.78) * mm, "end": v(108.43, 127.84) * mm});
            skLineSegment(sketch, "E3156", {"start": v(108.43, 127.84) * mm, "end": v(106.25, 128.47) * mm});
            skLineSegment(sketch, "E3157", {"start": v(106.25, 128.47) * mm, "end": v(105.52, 128.68) * mm});
            skLineSegment(sketch, "E3158", {"start": v(105.52, 128.68) * mm, "end": v(104.94, 128.84) * mm});
            skLineSegment(sketch, "E3159", {"start": v(104.94, 128.84) * mm, "end": v(103.22, 129.32) * mm});
            skLineSegment(sketch, "E3160", {"start": v(103.22, 129.32) * mm, "end": v(100.83, 130.11) * mm});
            skLineSegment(sketch, "E3161", {"start": v(100.83, 130.11) * mm, "end": v(98.55, 131.12) * mm});
            skLineSegment(sketch, "E3162", {"start": v(98.55, 131.12) * mm, "end": v(97.02, 132.07) * mm});
            skLineSegment(sketch, "E3163", {"start": v(97.02, 132.07) * mm, "end": v(96.57, 132.45) * mm});
            skLineSegment(sketch, "E3164", {"start": v(96.57, 132.45) * mm, "end": v(96.38, 132.8) * mm});
            skLineSegment(sketch, "E3165", {"start": v(96.38, 132.8) * mm, "end": v(95.3, 134.2) * mm});
            skLineSegment(sketch, "E3166", {"start": v(95.3, 134.2) * mm, "end": v(94.13, 135.5) * mm});
            skLineSegment(sketch, "E3167", {"start": v(94.13, 135.5) * mm, "end": v(93.88, 135.8) * mm});
            skLineSegment(sketch, "E3168", {"start": v(93.88, 135.8) * mm, "end": v(93.75, 135.95) * mm});
            skLineSegment(sketch, "E3169", {"start": v(93.75, 135.95) * mm, "end": v(93.19, 136.73) * mm});
            skLineSegment(sketch, "E3170", {"start": v(93.19, 136.73) * mm, "end": v(92.76, 137.57) * mm});
            skLineSegment(sketch, "E3171", {"start": v(92.76, 137.57) * mm, "end": v(92.7, 137.76) * mm});
            skLineSegment(sketch, "E3172", {"start": v(92.7, 137.76) * mm, "end": v(92.66, 137.86) * mm});
            skLineSegment(sketch, "E3173", {"start": v(92.66, 137.86) * mm, "end": v(92.6, 138.53) * mm});
            skLineSegment(sketch, "E3174", {"start": v(92.6, 138.53) * mm, "end": v(92.58, 139.2) * mm});
            skLineSegment(sketch, "E3175", {"start": v(92.58, 139.2) * mm, "end": v(92.57, 139.32) * mm});
            skLineSegment(sketch, "E3176", {"start": v(92.57, 139.32) * mm, "end": v(92.56, 139.54) * mm});
            skLineSegment(sketch, "E3177", {"start": v(92.56, 139.54) * mm, "end": v(92.4, 140.6) * mm});
            skLineSegment(sketch, "E3178", {"start": v(92.4, 140.6) * mm, "end": v(92.06, 141.62) * mm});
            skLineSegment(sketch, "E3179", {"start": v(92.06, 141.62) * mm, "end": v(91.95, 141.82) * mm});
            skLineSegment(sketch, "E3180", {"start": v(91.95, 141.82) * mm, "end": v(91.74, 142.21) * mm});
            skLineSegment(sketch, "E3181", {"start": v(91.74, 142.21) * mm, "end": v(90.88, 143.27) * mm});
            skLineSegment(sketch, "E3182", {"start": v(90.88, 143.27) * mm, "end": v(89.64, 144.17) * mm});
            skLineSegment(sketch, "E3183", {"start": v(89.64, 144.17) * mm, "end": v(88.26, 144.64) * mm});
            skLineSegment(sketch, "E3184", {"start": v(88.26, 144.64) * mm, "end": v(86.8, 144.8) * mm});
            skLineSegment(sketch, "E3185", {"start": v(86.8, 144.8) * mm, "end": v(85.24, 144.78) * mm});
            skLineSegment(sketch, "E3186", {"start": v(85.24, 144.78) * mm, "end": v(83.65, 144.7) * mm});
            skLineSegment(sketch, "E3187", {"start": v(83.65, 144.7) * mm, "end": v(82.06, 144.67) * mm});
            skLineSegment(sketch, "E3188", {"start": v(82.06, 144.67) * mm, "end": v(80.88, 144.75) * mm});
            skLineSegment(sketch, "E3189", {"start": v(80.88, 144.75) * mm, "end": v(80.5, 144.82) * mm});
            skLineSegment(sketch, "E3190", {"start": v(80.5, 144.82) * mm, "end": v(80, 144.9) * mm});
            skLineSegment(sketch, "E3191", {"start": v(80, 144.9) * mm, "end": v(78.6, 145.54) * mm});
            skLineSegment(sketch, "E3192", {"start": v(78.6, 145.54) * mm, "end": v(77.12, 146.7) * mm});
            skLineSegment(sketch, "E3193", {"start": v(77.12, 146.7) * mm, "end": v(75.73, 148.05) * mm});
            skLineSegment(sketch, "E3194", {"start": v(75.73, 148.05) * mm, "end": v(74.58, 149) * mm});
            skLineSegment(sketch, "E3195", {"start": v(74.58, 149) * mm, "end": v(74.15, 149.25) * mm});
            skLineSegment(sketch, "E3196", {"start": v(74.15, 149.25) * mm, "end": v(73.92, 149.38) * mm});
            skLineSegment(sketch, "E3197", {"start": v(73.92, 149.38) * mm, "end": v(73.66, 149.4) * mm});
            skLineSegment(sketch, "E3198", {"start": v(73.66, 149.4) * mm, "end": v(72.55, 149.44) * mm});
            skLineSegment(sketch, "E3199", {"start": v(72.55, 149.44) * mm, "end": v(69.23, 149.77) * mm});
            skLineSegment(sketch, "E3200", {"start": v(69.23, 149.77) * mm, "end": v(64.9, 150.26) * mm});
            skLineSegment(sketch, "E3201", {"start": v(64.9, 150.26) * mm, "end": v(60.6, 150.45) * mm});
            skLineSegment(sketch, "E3202", {"start": v(60.6, 150.45) * mm, "end": v(57.26, 150.18) * mm});
            skLineSegment(sketch, "E3203", {"start": v(57.26, 150.18) * mm, "end": v(56.19, 149.94) * mm});
            skLineSegment(sketch, "E3204", {"start": v(56.19, 149.94) * mm, "end": v(56.04, 150.19) * mm});
            skLineSegment(sketch, "E3205", {"start": v(56.04, 150.19) * mm, "end": v(55.34, 150.77) * mm});
            skLineSegment(sketch, "E3206", {"start": v(55.34, 150.77) * mm, "end": v(54.25, 151.2) * mm});
            skLineSegment(sketch, "E3207", {"start": v(54.25, 151.2) * mm, "end": v(53.1, 151.5) * mm});
            skLineSegment(sketch, "E3208", {"start": v(53.1, 151.5) * mm, "end": v(52.32, 151.82) * mm});
            skLineSegment(sketch, "E3209", {"start": v(52.32, 151.82) * mm, "end": v(52.1, 151.98) * mm});
            skLineSegment(sketch, "E3210", {"start": v(52.1, 151.98) * mm, "end": v(52.01, 152.07) * mm});
            skLineSegment(sketch, "E3211", {"start": v(52.01, 152.07) * mm, "end": v(51.81, 152.41) * mm});
            skLineSegment(sketch, "E3212", {"start": v(51.81, 152.41) * mm, "end": v(51.5, 153.07) * mm});
            skLineSegment(sketch, "E3213", {"start": v(51.5, 153.07) * mm, "end": v(51.07, 153.8) * mm});
            skLineSegment(sketch, "E3214", {"start": v(51.07, 153.8) * mm, "end": v(50.62, 154.33) * mm});
            skLineSegment(sketch, "E3215", {"start": v(50.62, 154.33) * mm, "end": v(50.44, 154.47) * mm});
            skLineSegment(sketch, "E3216", {"start": v(50.44, 154.47) * mm, "end": v(50.03, 154.77) * mm});
            skLineSegment(sketch, "E3217", {"start": v(50.03, 154.77) * mm, "end": v(47.62, 155.94) * mm});
            skLineSegment(sketch, "E3218", {"start": v(47.62, 155.94) * mm, "end": v(45.14, 157.08) * mm});
            skLineSegment(sketch, "E3219", {"start": v(45.14, 157.08) * mm, "end": v(44.7, 157.37) * mm});
            skLineSegment(sketch, "E3220", {"start": v(44.7, 157.37) * mm, "end": v(44, 157.8) * mm});
            skLineSegment(sketch, "E3221", {"start": v(44, 157.8) * mm, "end": v(41.84, 159.06) * mm});
            skLineSegment(sketch, "E3222", {"start": v(41.84, 159.06) * mm, "end": v(39.29, 160.12) * mm});
            skLineSegment(sketch, "E3223", {"start": v(39.29, 160.12) * mm, "end": v(36.63, 160.3) * mm});
            skLineSegment(sketch, "E3224", {"start": v(36.63, 160.3) * mm, "end": v(34.22, 159.72) * mm});
            skLineSegment(sketch, "E3225", {"start": v(34.22, 159.72) * mm, "end": v(33.48, 159.4) * mm});
            skLineSegment(sketch, "E3226", {"start": v(33.48, 159.4) * mm, "end": v(33.17, 159.65) * mm});
            skLineSegment(sketch, "E3227", {"start": v(33.17, 159.65) * mm, "end": v(32.48, 160.7) * mm});
            skLineSegment(sketch, "E3228", {"start": v(32.48, 160.7) * mm, "end": v(31.9, 162.4) * mm});
            skLineSegment(sketch, "E3229", {"start": v(31.9, 162.4) * mm, "end": v(31.6, 164.22) * mm});
            skLineSegment(sketch, "E3230", {"start": v(31.6, 164.22) * mm, "end": v(31.49, 165.49) * mm});
            skLineSegment(sketch, "E3231", {"start": v(31.49, 165.49) * mm, "end": v(31.47, 165.91) * mm});
            skLineSegment(sketch, "E3232", {"start": v(31.47, 165.91) * mm, "end": v(31.8, 166.24) * mm});
            skLineSegment(sketch, "E3233", {"start": v(31.8, 166.24) * mm, "end": v(33.1, 166.91) * mm});
            skLineSegment(sketch, "E3234", {"start": v(33.1, 166.91) * mm, "end": v(34.98, 167.23) * mm});
            skLineSegment(sketch, "E3235", {"start": v(34.98, 167.23) * mm, "end": v(36.96, 167.11) * mm});
            skLineSegment(sketch, "E3236", {"start": v(36.96, 167.11) * mm, "end": v(38.4, 166.89) * mm});
            skLineSegment(sketch, "E3237", {"start": v(38.4, 166.89) * mm, "end": v(38.88, 166.8) * mm});
            skLineSegment(sketch, "E3238", {"start": v(38.88, 166.8) * mm, "end": v(39.2, 166.75) * mm});
            skLineSegment(sketch, "E3239", {"start": v(39.2, 166.75) * mm, "end": v(42.39, 166.3) * mm});
            skLineSegment(sketch, "E3240", {"start": v(42.39, 166.3) * mm, "end": v(42.71, 166.3) * mm});
            skLineSegment(sketch, "E3241", {"start": v(42.71, 166.3) * mm, "end": v(44.11, 166.2) * mm});
            skLineSegment(sketch, "E3242", {"start": v(44.11, 166.2) * mm, "end": v(51.12, 166.34) * mm});
            skLineSegment(sketch, "E3243", {"start": v(51.12, 166.34) * mm, "end": v(57.42, 166.64) * mm});
            skLineSegment(sketch, "E3244", {"start": v(57.42, 166.64) * mm, "end": v(59.51, 166.64) * mm});
            skLineSegment(sketch, "E3245", {"start": v(59.51, 166.64) * mm, "end": v(60.24, 166.64) * mm});
            skLineSegment(sketch, "E3246", {"start": v(60.24, 166.64) * mm, "end": v(62.43, 166.54) * mm});
            skLineSegment(sketch, "E3247", {"start": v(62.43, 166.54) * mm, "end": v(65.5, 166.3) * mm});
            skLineSegment(sketch, "E3248", {"start": v(65.5, 166.3) * mm, "end": v(68.63, 166) * mm});
            skLineSegment(sketch, "E3249", {"start": v(68.63, 166) * mm, "end": v(71.8, 165.75) * mm});
            skLineSegment(sketch, "E3250", {"start": v(71.8, 165.75) * mm, "end": v(74.95, 165.63) * mm});
            skLineSegment(sketch, "E3251", {"start": v(74.95, 165.63) * mm, "end": v(78.03, 165.75) * mm});
            skLineSegment(sketch, "E3252", {"start": v(78.03, 165.75) * mm, "end": v(80.98, 166.2) * mm});
            skLineSegment(sketch, "E3253", {"start": v(80.98, 166.2) * mm, "end": v(83.08, 166.77) * mm});
            skLineSegment(sketch, "E3254", {"start": v(83.08, 166.77) * mm, "end": v(83.75, 167.05) * mm});
            skLineSegment(sketch, "E3255", {"start": v(83.75, 167.05) * mm, "end": v(84.32, 167.3) * mm});
            skLineSegment(sketch, "E3256", {"start": v(84.32, 167.3) * mm, "end": v(85.82, 168.5) * mm});
            skLineSegment(sketch, "E3257", {"start": v(85.82, 168.5) * mm, "end": v(87.94, 170.57) * mm});
            skLineSegment(sketch, "E3258", {"start": v(87.94, 170.57) * mm, "end": v(90.03, 172.46) * mm});
            skLineSegment(sketch, "E3259", {"start": v(90.03, 172.46) * mm, "end": v(91.49, 173.33) * mm});
            skLineSegment(sketch, "E3260", {"start": v(91.49, 173.33) * mm, "end": v(92, 173.37) * mm});
            skLineSegment(sketch, "E3261", {"start": v(92, 173.37) * mm, "end": v(92.04, 173.37) * mm});
            skLineSegment(sketch, "E3262", {"start": v(92.04, 173.37) * mm, "end": v(92.44, 173.33) * mm});
            skLineSegment(sketch, "E3263", {"start": v(92.44, 173.33) * mm, "end": v(92.49, 173.32) * mm});
            skLineSegment(sketch, "E3264", {"start": v(92.49, 173.32) * mm, "end": v(93.57, 173.11) * mm});
            skLineSegment(sketch, "E3265", {"start": v(93.57, 173.11) * mm, "end": v(99.33, 172.53) * mm});
            skLineSegment(sketch, "E3266", {"start": v(99.33, 172.53) * mm, "end": v(105.12, 172.32) * mm});
            skLineSegment(sketch, "E3267", {"start": v(105.12, 172.32) * mm, "end": v(106.23, 172.3) * mm});
            skLineSegment(sketch, "E3268", {"start": v(106.23, 172.3) * mm, "end": v(106.97, 172.29) * mm});
            skLineSegment(sketch, "E3269", {"start": v(106.97, 172.29) * mm, "end": v(113.1, 172.26) * mm});
            skLineSegment(sketch, "E3270", {"start": v(113.1, 172.26) * mm, "end": v(115.15, 172.26) * mm});
            skLineSegment(sketch, "E3271", {"start": v(115.15, 172.26) * mm, "end": v(116.22, 172.26) * mm});
            skLineSegment(sketch, "E3272", {"start": v(116.22, 172.26) * mm, "end": v(119.44, 171.94) * mm});
            skLineSegment(sketch, "E3273", {"start": v(119.44, 171.94) * mm, "end": v(123, 171.8) * mm});
            skLineSegment(sketch, "E3274", {"start": v(123, 171.8) * mm, "end": v(123.69, 171.9) * mm});
            skLineSegment(sketch, "E3275", {"start": v(123.69, 171.9) * mm, "end": v(124.26, 171.98) * mm});
            skLineSegment(sketch, "E3276", {"start": v(124.26, 171.98) * mm, "end": v(125.94, 172.4) * mm});
            skLineSegment(sketch, "E3277", {"start": v(125.94, 172.4) * mm, "end": v(128.54, 173.05) * mm});
            skLineSegment(sketch, "E3278", {"start": v(128.54, 173.05) * mm, "end": v(131.1, 173.49) * mm});
            skLineSegment(sketch, "E3279", {"start": v(131.1, 173.49) * mm, "end": v(132.77, 173.5) * mm});
            skLineSegment(sketch, "E3280", {"start": v(132.77, 173.5) * mm, "end": v(133.29, 173.36) * mm});
            skLineSegment(sketch, "E3281", {"start": v(133.29, 173.36) * mm, "end": v(133.55, 173.28) * mm});
            skLineSegment(sketch, "E3282", {"start": v(133.55, 173.28) * mm, "end": v(134.26, 172.72) * mm});
            skLineSegment(sketch, "E3283", {"start": v(134.26, 172.72) * mm, "end": v(135.25, 171.6) * mm});
            skLineSegment(sketch, "E3284", {"start": v(135.25, 171.6) * mm, "end": v(136.26, 170.35) * mm});
            skLineSegment(sketch, "E3285", {"start": v(136.26, 170.35) * mm, "end": v(136.98, 169.54) * mm});
            skLineSegment(sketch, "E3286", {"start": v(136.98, 169.54) * mm, "end": v(137.26, 169.32) * mm});
            skLineSegment(sketch, "E3287", {"start": v(137.26, 169.32) * mm, "end": v(137.55, 169.1) * mm});
            skLineSegment(sketch, "E3288", {"start": v(137.55, 169.1) * mm, "end": v(139, 168.3) * mm});
            skLineSegment(sketch, "E3289", {"start": v(139, 168.3) * mm, "end": v(140.48, 167.63) * mm});
            skLineSegment(sketch, "E3290", {"start": v(140.48, 167.63) * mm, "end": v(140.8, 167.46) * mm});
            skLineSegment(sketch, "E3291", {"start": v(140.8, 167.46) * mm, "end": v(140.92, 167.39) * mm});
            skLineSegment(sketch, "E3292", {"start": v(140.92, 167.39) * mm, "end": v(141.53, 167) * mm});
            skLineSegment(sketch, "E3293", {"start": v(141.53, 167) * mm, "end": v(142.05, 166.5) * mm});
            skLineSegment(sketch, "E3294", {"start": v(142.05, 166.5) * mm, "end": v(142.14, 166.37) * mm});
            skLineSegment(sketch, "E3295", {"start": v(142.14, 166.37) * mm, "end": v(142.4, 166.03) * mm});
            skLineSegment(sketch, "E3296", {"start": v(142.4, 166.03) * mm, "end": v(142.8, 165.96) * mm});
            skLineSegment(sketch, "E3297", {"start": v(142.8, 165.96) * mm, "end": v(146.5, 165.31) * mm});
            skLineSegment(sketch, "E3298", {"start": v(146.5, 165.31) * mm, "end": v(157.52, 162.94) * mm});
            skLineSegment(sketch, "E3299", {"start": v(157.52, 162.94) * mm, "end": v(172.05, 159.04) * mm});
            skLineSegment(sketch, "E3300", {"start": v(172.05, 159.04) * mm, "end": v(186.3, 154.21) * mm});
            skLineSegment(sketch, "E3301", {"start": v(186.3, 154.21) * mm, "end": v(196.76, 150) * mm});
            skLineSegment(sketch, "E3302", {"start": v(196.76, 150) * mm, "end": v(200.17, 148.43) * mm});
            skLineSegment(sketch, "E3303", {"start": v(200.17, 148.43) * mm, "end": v(200.4, 148.33) * mm});
            skLineSegment(sketch, "E3304", {"start": v(200.4, 148.33) * mm, "end": v(201, 147.9) * mm});
            skLineSegment(sketch, "E3305", {"start": v(201, 147.9) * mm, "end": v(201.8, 147.22) * mm});
            skLineSegment(sketch, "E3306", {"start": v(201.8, 147.22) * mm, "end": v(202.6, 146.53) * mm});
            skLineSegment(sketch, "E3307", {"start": v(202.6, 146.53) * mm, "end": v(203.27, 146.06) * mm});
            skLineSegment(sketch, "E3308", {"start": v(203.27, 146.06) * mm, "end": v(203.52, 145.95) * mm});
            skLineSegment(sketch, "E3309", {"start": v(203.52, 145.95) * mm, "end": v(204.09, 145.7) * mm});
            skLineSegment(sketch, "E3310", {"start": v(204.09, 145.7) * mm, "end": v(207.07, 145) * mm});
            skLineSegment(sketch, "E3311", {"start": v(207.07, 145) * mm, "end": v(210.06, 144.39) * mm});
            skLineSegment(sketch, "E3312", {"start": v(210.06, 144.39) * mm, "end": v(210.64, 144.17) * mm});
            skLineSegment(sketch, "E3313", {"start": v(210.64, 144.17) * mm, "end": v(211.24, 143.95) * mm});
            skLineSegment(sketch, "E3314", {"start": v(211.24, 143.95) * mm, "end": v(217.19, 141.77) * mm});
            skLineSegment(sketch, "E3315", {"start": v(217.19, 141.77) * mm, "end": v(217.79, 141.57) * mm});
            skLineSegment(sketch, "E3316", {"start": v(217.79, 141.57) * mm, "end": v(218.74, 141.25) * mm});
            skLineSegment(sketch, "E3317", {"start": v(218.74, 141.25) * mm, "end": v(223.48, 139.93) * mm});
            skLineSegment(sketch, "E3318", {"start": v(223.48, 139.93) * mm, "end": v(228.3, 139) * mm});
            skLineSegment(sketch, "E3319", {"start": v(228.3, 139) * mm, "end": v(229.3, 138.86) * mm});
            skLineSegment(sketch, "E3320", {"start": v(229.3, 138.86) * mm, "end": v(230.15, 138.73) * mm});
            skLineSegment(sketch, "E3321", {"start": v(230.15, 138.73) * mm, "end": v(232.65, 137.98) * mm});
            skLineSegment(sketch, "E3322", {"start": v(232.65, 137.98) * mm, "end": v(235.95, 136.65) * mm});
            skLineSegment(sketch, "E3323", {"start": v(235.95, 136.65) * mm, "end": v(239.3, 135.3) * mm});
            skLineSegment(sketch, "E3324", {"start": v(239.3, 135.3) * mm, "end": v(241.9, 134.52) * mm});
            skLineSegment(sketch, "E3325", {"start": v(241.9, 134.52) * mm, "end": v(242.8, 134.37) * mm});
            skLineSegment(sketch, "E3326", {"start": v(242.8, 134.37) * mm, "end": v(242.87, 134.36) * mm});
            skLineSegment(sketch, "E3327", {"start": v(242.87, 134.36) * mm, "end": v(243.67, 134.27) * mm});
            skLineSegment(sketch, "E3328", {"start": v(243.67, 134.27) * mm, "end": v(243.75, 134.26) * mm});
            skLineSegment(sketch, "E3329", {"start": v(243.75, 134.26) * mm, "end": v(244.12, 134.23) * mm});
            skLineSegment(sketch, "E3330", {"start": v(244.12, 134.23) * mm, "end": v(245.2, 134.28) * mm});
            skLineSegment(sketch, "E3331", {"start": v(245.2, 134.28) * mm, "end": v(246.57, 134.5) * mm});
            skLineSegment(sketch, "E3332", {"start": v(246.57, 134.5) * mm, "end": v(247.9, 134.77) * mm});
            skLineSegment(sketch, "E3333", {"start": v(247.9, 134.77) * mm, "end": v(248.93, 134.92) * mm});
            skLineSegment(sketch, "E3334", {"start": v(248.93, 134.92) * mm, "end": v(249.28, 134.93) * mm});
            skLineSegment(sketch, "E3335", {"start": v(249.28, 134.93) * mm, "end": v(249.93, 134.96) * mm});
            skLineSegment(sketch, "E3336", {"start": v(249.93, 134.96) * mm, "end": v(251.91, 134.8) * mm});
            skLineSegment(sketch, "E3337", {"start": v(251.91, 134.8) * mm, "end": v(254.38, 134.24) * mm});
            skLineSegment(sketch, "E3338", {"start": v(254.38, 134.24) * mm, "end": v(256.8, 133.42) * mm});
            skLineSegment(sketch, "E3339", {"start": v(256.8, 133.42) * mm, "end": v(258.65, 132.74) * mm});
            skLineSegment(sketch, "E3340", {"start": v(258.65, 132.74) * mm, "end": v(259.27, 132.53) * mm});
            skLineSegment(sketch, "E3341", {"start": v(259.27, 132.53) * mm, "end": v(259.46, 132.46) * mm});
            skLineSegment(sketch, "E3342", {"start": v(259.46, 132.46) * mm, "end": v(260.06, 132.35) * mm});
            skLineSegment(sketch, "E3343", {"start": v(260.06, 132.35) * mm, "end": v(260.97, 132.25) * mm});
            skLineSegment(sketch, "E3344", {"start": v(260.97, 132.25) * mm, "end": v(261.86, 132.15) * mm});
            skLineSegment(sketch, "E3345", {"start": v(261.86, 132.15) * mm, "end": v(262.41, 132.05) * mm});
            skLineSegment(sketch, "E3346", {"start": v(262.41, 132.05) * mm, "end": v(262.59, 131.99) * mm});
            skLineSegment(sketch, "E3347", {"start": v(262.59, 131.99) * mm, "end": v(262.91, 132) * mm});
            skLineSegment(sketch, "E3348", {"start": v(262.91, 132) * mm, "end": v(263.8, 132.02) * mm});
            skLineSegment(sketch, "E3349", {"start": v(263.8, 132.02) * mm, "end": v(265.1, 132.08) * mm});
            skLineSegment(sketch, "E3350", {"start": v(265.1, 132.08) * mm, "end": v(266.69, 132.22) * mm});
            skLineSegment(sketch, "E3351", {"start": v(266.69, 132.22) * mm, "end": v(268.41, 132.45) * mm});
            skLineSegment(sketch, "E3352", {"start": v(268.41, 132.45) * mm, "end": v(270.13, 132.79) * mm});
            skLineSegment(sketch, "E3353", {"start": v(270.13, 132.79) * mm, "end": v(271.7, 133.27) * mm});
            skLineSegment(sketch, "E3354", {"start": v(271.7, 133.27) * mm, "end": v(272.7, 133.7) * mm});
            skLineSegment(sketch, "E3355", {"start": v(272.7, 133.7) * mm, "end": v(273, 133.9) * mm});
            skLineSegment(sketch, "E3356", {"start": v(273, 133.9) * mm, "end": v(273.25, 134.08) * mm});
            skLineSegment(sketch, "E3357", {"start": v(273.25, 134.08) * mm, "end": v(274, 134.64) * mm});
            skLineSegment(sketch, "E3358", {"start": v(274, 134.64) * mm, "end": v(274.83, 135.38) * mm});
            skLineSegment(sketch, "E3359", {"start": v(274.83, 135.38) * mm, "end": v(275.52, 136.09) * mm});
            skLineSegment(sketch, "E3360", {"start": v(275.52, 136.09) * mm, "end": v(276.05, 136.73) * mm});
            skLineSegment(sketch, "E3361", {"start": v(276.05, 136.73) * mm, "end": v(276.44, 137.29) * mm});
            skLineSegment(sketch, "E3362", {"start": v(276.44, 137.29) * mm, "end": v(276.7, 137.72) * mm});
            skLineSegment(sketch, "E3363", {"start": v(276.7, 137.72) * mm, "end": v(276.86, 138) * mm});
            skLineSegment(sketch, "E3364", {"start": v(276.86, 138) * mm, "end": v(276.9, 138.1) * mm});
            skLineSegment(sketch, "E3365", {"start": v(262.59, 131.99) * mm, "end": v(262.47, 131.97) * mm});
            skLineSegment(sketch, "E3366", {"start": v(262.47, 131.97) * mm, "end": v(261.3, 131.9) * mm});
            skLineSegment(sketch, "E3367", {"start": v(261.3, 131.9) * mm, "end": v(261.17, 131.91) * mm});
            skLineSegment(sketch, "E3368", {"start": v(261.17, 131.91) * mm, "end": v(260.56, 131.95) * mm});
            skLineSegment(sketch, "E3369", {"start": v(260.56, 131.95) * mm, "end": v(257.62, 132.58) * mm});
            skLineSegment(sketch, "E3370", {"start": v(257.62, 132.58) * mm, "end": v(254.59, 133.18) * mm});
            skLineSegment(sketch, "E3371", {"start": v(254.59, 133.18) * mm, "end": v(253.94, 133.2) * mm});
            skLineSegment(sketch, "E3372", {"start": v(253.94, 133.2) * mm, "end": v(253.38, 133.22) * mm});
            skLineSegment(sketch, "E3373", {"start": v(253.38, 133.22) * mm, "end": v(250.56, 132.6) * mm});
            skLineSegment(sketch, "E3374", {"start": v(250.56, 132.6) * mm, "end": v(247.71, 131.85) * mm});
            skLineSegment(sketch, "E3375", {"start": v(247.71, 131.85) * mm, "end": v(247.14, 131.8) * mm});
            skLineSegment(sketch, "E3376", {"start": v(247.14, 131.8) * mm, "end": v(246.64, 131.77) * mm});
            skLineSegment(sketch, "E3377", {"start": v(246.64, 131.77) * mm, "end": v(244.1, 131.82) * mm});
            skLineSegment(sketch, "E3378", {"start": v(244.1, 131.82) * mm, "end": v(241.58, 131.86) * mm});
            skLineSegment(sketch, "E3379", {"start": v(241.58, 131.86) * mm, "end": v(241.08, 131.8) * mm});
            skLineSegment(sketch, "E3380", {"start": v(241.08, 131.8) * mm, "end": v(240.64, 131.76) * mm});
            skLineSegment(sketch, "E3381", {"start": v(240.64, 131.76) * mm, "end": v(236.27, 130.99) * mm});
            skLineSegment(sketch, "E3382", {"start": v(236.27, 130.99) * mm, "end": v(235.84, 130.9) * mm});
            skLineSegment(sketch, "E3383", {"start": v(235.84, 130.9) * mm, "end": v(235.09, 130.74) * mm});
            skLineSegment(sketch, "E3384", {"start": v(235.09, 130.74) * mm, "end": v(232.86, 130.2) * mm});
            skLineSegment(sketch, "E3385", {"start": v(232.86, 130.2) * mm, "end": v(229.52, 129.48) * mm});
            skLineSegment(sketch, "E3386", {"start": v(229.52, 129.48) * mm, "end": v(226.17, 128.97) * mm});
            skLineSegment(sketch, "E3387", {"start": v(226.17, 128.97) * mm, "end": v(223.93, 128.88) * mm});
            skLineSegment(sketch, "E3388", {"start": v(223.93, 128.88) * mm, "end": v(223.2, 128.97) * mm});
            skLineSegment(sketch, "E3389", {"start": v(223.2, 128.97) * mm, "end": v(222.62, 129.05) * mm});
            skLineSegment(sketch, "E3390", {"start": v(222.62, 129.05) * mm, "end": v(220.92, 129.64) * mm});
            skLineSegment(sketch, "E3391", {"start": v(220.92, 129.64) * mm, "end": v(218.77, 130.74) * mm});
            skLineSegment(sketch, "E3392", {"start": v(218.77, 130.74) * mm, "end": v(216.63, 131.9) * mm});
            skLineSegment(sketch, "E3393", {"start": v(216.63, 131.9) * mm, "end": v(214.94, 132.6) * mm});
            skLineSegment(sketch, "E3394", {"start": v(214.94, 132.6) * mm, "end": v(214.36, 132.73) * mm});
            skLineSegment(sketch, "E3395", {"start": v(214.36, 132.73) * mm, "end": v(214.05, 133.19) * mm});
            skLineSegment(sketch, "E3396", {"start": v(214.05, 133.19) * mm, "end": v(212.87, 134.38) * mm});
            skLineSegment(sketch, "E3397", {"start": v(212.87, 134.38) * mm, "end": v(211.14, 135.47) * mm});
            skLineSegment(sketch, "E3398", {"start": v(211.14, 135.47) * mm, "end": v(209.24, 136.16) * mm});
            skLineSegment(sketch, "E3399", {"start": v(209.24, 136.16) * mm, "end": v(207.2, 136.55) * mm});
            skLineSegment(sketch, "E3400", {"start": v(207.2, 136.55) * mm, "end": v(205.11, 136.81) * mm});
            skLineSegment(sketch, "E3401", {"start": v(205.11, 136.81) * mm, "end": v(203.01, 137.05) * mm});
            skLineSegment(sketch, "E3402", {"start": v(203.01, 137.05) * mm, "end": v(200.97, 137.42) * mm});
            skLineSegment(sketch, "E3403", {"start": v(200.97, 137.42) * mm, "end": v(199.5, 137.83) * mm});
            skLineSegment(sketch, "E3404", {"start": v(199.5, 137.83) * mm, "end": v(199.04, 138.03) * mm});
            skLineSegment(sketch, "E3405", {"start": v(199.04, 138.03) * mm, "end": v(198.44, 138.3) * mm});
            skLineSegment(sketch, "E3406", {"start": v(198.44, 138.3) * mm, "end": v(196.75, 139.32) * mm});
            skLineSegment(sketch, "E3407", {"start": v(196.75, 139.32) * mm, "end": v(194.6, 140.97) * mm});
            skLineSegment(sketch, "E3408", {"start": v(194.6, 140.97) * mm, "end": v(192.55, 142.79) * mm});
            skLineSegment(sketch, "E3409", {"start": v(192.55, 142.79) * mm, "end": v(191.09, 144.13) * mm});
            skLineSegment(sketch, "E3410", {"start": v(191.09, 144.13) * mm, "end": v(190.6, 144.57) * mm});
            skLineSegment(sketch, "E3411", {"start": v(190.6, 144.57) * mm, "end": v(190.32, 144.8) * mm});
            skLineSegment(sketch, "E3412", {"start": v(190.32, 144.8) * mm, "end": v(189.98, 144.82) * mm});
            skLineSegment(sketch, "E3413", {"start": v(189.98, 144.82) * mm, "end": v(189.24, 144.89) * mm});
            skLineSegment(sketch, "E3414", {"start": v(189.24, 144.89) * mm, "end": v(187.02, 145.1) * mm});
            skLineSegment(sketch, "E3415", {"start": v(187.02, 145.1) * mm, "end": v(184.3, 145.2) * mm});
            skLineSegment(sketch, "E3416", {"start": v(184.3, 145.2) * mm, "end": v(181.6, 144.94) * mm});
            skLineSegment(sketch, "E3417", {"start": v(181.6, 144.94) * mm, "end": v(179.44, 144.33) * mm});
            skLineSegment(sketch, "E3418", {"start": v(179.44, 144.33) * mm, "end": v(178.76, 144.04) * mm});
            skLineSegment(sketch, "E3419", {"start": v(178.76, 144.04) * mm, "end": v(178.73, 144.02) * mm});
            skLineSegment(sketch, "E3420", {"start": v(178.73, 144.02) * mm, "end": v(178.7, 144) * mm});
            skLineSegment(sketch, "E3421", {"start": v(178.7, 144) * mm, "end": v(178.53, 143.92) * mm});
            skLineSegment(sketch, "E3422", {"start": v(178.53, 143.92) * mm, "end": v(177.71, 143.38) * mm});
            skLineSegment(sketch, "E3423", {"start": v(177.71, 143.38) * mm, "end": v(177, 142.72) * mm});
            skLineSegment(sketch, "E3424", {"start": v(177, 142.72) * mm, "end": v(176.88, 142.56) * mm});
            skLineSegment(sketch, "E3425", {"start": v(176.88, 142.56) * mm, "end": v(176.55, 142.17) * mm});
            skLineSegment(sketch, "E3426", {"start": v(176.55, 142.17) * mm, "end": v(175.54, 139.83) * mm});
            skLineSegment(sketch, "E3427", {"start": v(175.54, 139.83) * mm, "end": v(175.07, 137.3) * mm});
            skLineSegment(sketch, "E3428", {"start": v(175.07, 137.3) * mm, "end": v(175.01, 136.8) * mm});
            skLineSegment(sketch, "E3429", {"start": v(175.01, 136.8) * mm, "end": v(174.95, 136.22) * mm});
            skLineSegment(sketch, "E3430", {"start": v(174.95, 136.22) * mm, "end": v(174.24, 130.49) * mm});
            skLineSegment(sketch, "E3431", {"start": v(174.24, 130.49) * mm, "end": v(174.11, 129.92) * mm});
            skLineSegment(sketch, "E3432", {"start": v(174.11, 129.92) * mm, "end": v(173.96, 129.26) * mm});
            skLineSegment(sketch, "E3433", {"start": v(173.96, 129.26) * mm, "end": v(173, 127.4) * mm});
            skLineSegment(sketch, "E3434", {"start": v(173, 127.4) * mm, "end": v(171.34, 124.8) * mm});
            skLineSegment(sketch, "E3435", {"start": v(171.34, 124.8) * mm, "end": v(169.95, 122.13) * mm});
            skLineSegment(sketch, "E3436", {"start": v(169.95, 122.13) * mm, "end": v(169.51, 120.03) * mm});
            skLineSegment(sketch, "E3437", {"start": v(169.51, 120.03) * mm, "end": v(169.62, 119.38) * mm});
            skLineSegment(sketch, "E3438", {"start": v(169.62, 119.38) * mm, "end": v(169.67, 119.1) * mm});
            skLineSegment(sketch, "E3439", {"start": v(169.67, 119.1) * mm, "end": v(169.96, 118.32) * mm});
            skLineSegment(sketch, "E3440", {"start": v(169.96, 118.32) * mm, "end": v(170.56, 117.42) * mm});
            skLineSegment(sketch, "E3441", {"start": v(170.56, 117.42) * mm, "end": v(171.34, 116.68) * mm});
            skLineSegment(sketch, "E3442", {"start": v(171.34, 116.68) * mm, "end": v(172.03, 116.2) * mm});
            skLineSegment(sketch, "E3443", {"start": v(172.03, 116.2) * mm, "end": v(172.27, 116.07) * mm});
            skLineSegment(sketch, "E3444", {"start": v(172.27, 116.07) * mm, "end": v(172.79, 115.78) * mm});
            skLineSegment(sketch, "E3445", {"start": v(172.79, 115.78) * mm, "end": v(173.3, 116.06) * mm});
            skLineSegment(sketch, "E3446", {"start": v(173.3, 116.06) * mm, "end": v(174.21, 116.54) * mm});
            skLineSegment(sketch, "E3447", {"start": v(174.21, 116.54) * mm, "end": v(176.82, 118.22) * mm});
            skLineSegment(sketch, "E3448", {"start": v(176.82, 118.22) * mm, "end": v(180.15, 120.66) * mm});
            skLineSegment(sketch, "E3449", {"start": v(180.15, 120.66) * mm, "end": v(183.4, 123.19) * mm});
            skLineSegment(sketch, "E3450", {"start": v(183.4, 123.19) * mm, "end": v(185.88, 125.05) * mm});
            skLineSegment(sketch, "E3451", {"start": v(185.88, 125.05) * mm, "end": v(186.73, 125.63) * mm});
            skLineSegment(sketch, "E3452", {"start": v(186.73, 125.63) * mm, "end": v(187.55, 126.19) * mm});
            skLineSegment(sketch, "E3453", {"start": v(187.55, 126.19) * mm, "end": v(190.13, 127.71) * mm});
            skLineSegment(sketch, "E3454", {"start": v(190.13, 127.71) * mm, "end": v(193.61, 129.29) * mm});
            skLineSegment(sketch, "E3455", {"start": v(193.61, 129.29) * mm, "end": v(197.26, 130.3) * mm});
            skLineSegment(sketch, "E3456", {"start": v(197.26, 130.3) * mm, "end": v(200.17, 130.7) * mm});
            skLineSegment(sketch, "E3457", {"start": v(200.17, 130.7) * mm, "end": v(201.15, 130.71) * mm});
            skLineSegment(sketch, "E3458", {"start": v(201.15, 130.71) * mm, "end": v(201.06, 130.58) * mm});
            skLineSegment(sketch, "E3459", {"start": v(201.06, 130.58) * mm, "end": v(200.79, 130.19) * mm});
            skLineSegment(sketch, "E3460", {"start": v(200.79, 130.19) * mm, "end": v(200.42, 129.61) * mm});
            skLineSegment(sketch, "E3461", {"start": v(200.42, 129.61) * mm, "end": v(200.1, 128.93) * mm});
            skLineSegment(sketch, "E3462", {"start": v(200.1, 128.93) * mm, "end": v(199.93, 128.3) * mm});
            skLineSegment(sketch, "E3463", {"start": v(199.93, 128.3) * mm, "end": v(199.9, 128.09) * mm});
            skLineSegment(sketch, "E3464", {"start": v(199.9, 128.09) * mm, "end": v(197.43, 126.04) * mm});
            skLineSegment(sketch, "E3465", {"start": v(197.43, 126.04) * mm, "end": v(189.88, 120.05) * mm});
            skLineSegment(sketch, "E3466", {"start": v(189.88, 120.05) * mm, "end": v(179.56, 112.48) * mm});
            skLineSegment(sketch, "E3467", {"start": v(179.56, 112.48) * mm, "end": v(168.83, 105.51) * mm});
            skLineSegment(sketch, "E3468", {"start": v(168.83, 105.51) * mm, "end": v(160.44, 100.74) * mm});
            skLineSegment(sketch, "E3469", {"start": v(160.44, 100.74) * mm, "end": v(157.57, 99.3) * mm});
            skLineSegment(sketch, "E3470", {"start": v(157.57, 99.3) * mm, "end": v(157.35, 99.2) * mm});
            skLineSegment(sketch, "E3471", {"start": v(157.35, 99.2) * mm, "end": v(157.2, 99) * mm});
            skLineSegment(sketch, "E3472", {"start": v(157.2, 99) * mm, "end": v(157.01, 98.76) * mm});
            skLineSegment(sketch, "E3473", {"start": v(157.01, 98.76) * mm, "end": v(156.51, 97.95) * mm});
            skLineSegment(sketch, "E3474", {"start": v(156.51, 97.95) * mm, "end": v(155.98, 96.78) * mm});
            skLineSegment(sketch, "E3475", {"start": v(155.98, 96.78) * mm, "end": v(155.65, 95.56) * mm});
            skLineSegment(sketch, "E3476", {"start": v(155.65, 95.56) * mm, "end": v(155.6, 94.39) * mm});
            skLineSegment(sketch, "E3477", {"start": v(155.6, 94.39) * mm, "end": v(155.85, 93.33) * mm});
            skLineSegment(sketch, "E3478", {"start": v(155.85, 93.33) * mm, "end": v(156.47, 92.46) * mm});
            skLineSegment(sketch, "E3479", {"start": v(156.47, 92.46) * mm, "end": v(157.51, 91.88) * mm});
            skLineSegment(sketch, "E3480", {"start": v(157.51, 91.88) * mm, "end": v(158.65, 91.64) * mm});
            skLineSegment(sketch, "E3481", {"start": v(158.65, 91.64) * mm, "end": v(159.03, 91.64) * mm});
            skLineSegment(sketch, "E3482", {"start": v(159.03, 91.64) * mm, "end": v(159.3, 91.63) * mm});
            skLineSegment(sketch, "E3483", {"start": v(159.3, 91.63) * mm, "end": v(160.15, 91.81) * mm});
            skLineSegment(sketch, "E3484", {"start": v(160.15, 91.81) * mm, "end": v(161.16, 92.33) * mm});
            skLineSegment(sketch, "E3485", {"start": v(161.16, 92.33) * mm, "end": v(162.04, 93.07) * mm});
            skLineSegment(sketch, "E3486", {"start": v(162.04, 93.07) * mm, "end": v(162.63, 93.69) * mm});
            skLineSegment(sketch, "E3487", {"start": v(162.63, 93.69) * mm, "end": v(162.81, 93.9) * mm});
            skLineSegment(sketch, "E3488", {"start": v(162.81, 93.9) * mm, "end": v(162.92, 94.03) * mm});
            skLineSegment(sketch, "E3489", {"start": v(162.92, 94.03) * mm, "end": v(163.24, 94.43) * mm});
            skLineSegment(sketch, "E3490", {"start": v(163.24, 94.43) * mm, "end": v(163.73, 95.06) * mm});
            skLineSegment(sketch, "E3491", {"start": v(163.73, 95.06) * mm, "end": v(164.24, 95.65) * mm});
            skLineSegment(sketch, "E3492", {"start": v(164.24, 95.65) * mm, "end": v(164.59, 95.99) * mm});
            skLineSegment(sketch, "E3493", {"start": v(164.59, 95.99) * mm, "end": v(164.71, 96.08) * mm});
            skLineSegment(sketch, "E3494", {"start": v(164.71, 96.08) * mm, "end": v(165.35, 96.53) * mm});
            skLineSegment(sketch, "E3495", {"start": v(165.35, 96.53) * mm, "end": v(172, 100.71) * mm});
            skLineSegment(sketch, "E3496", {"start": v(172, 100.71) * mm, "end": v(172.67, 101.12) * mm});
            skLineSegment(sketch, "E3497", {"start": v(172.67, 101.12) * mm, "end": v(173.45, 101.58) * mm});
            skLineSegment(sketch, "E3498", {"start": v(173.45, 101.58) * mm, "end": v(181.07, 106.45) * mm});
            skLineSegment(sketch, "E3499", {"start": v(181.07, 106.45) * mm, "end": v(181.81, 106.97) * mm});
            skLineSegment(sketch, "E3500", {"start": v(181.81, 106.97) * mm, "end": v(183.14, 107.93) * mm});
            skLineSegment(sketch, "E3501", {"start": v(183.14, 107.93) * mm, "end": v(189.96, 112.5) * mm});
            skLineSegment(sketch, "E3502", {"start": v(189.96, 112.5) * mm, "end": v(196.73, 117.12) * mm});
            skLineSegment(sketch, "E3503", {"start": v(196.73, 117.12) * mm, "end": v(198.03, 118.1) * mm});
            skLineSegment(sketch, "E3504", {"start": v(198.03, 118.1) * mm, "end": v(198.98, 118.28) * mm});
            skLineSegment(sketch, "E3505", {"start": v(198.98, 118.28) * mm, "end": v(201.74, 119.37) * mm});
            skLineSegment(sketch, "E3506", {"start": v(201.74, 119.37) * mm, "end": v(205.12, 121.21) * mm});
            skLineSegment(sketch, "E3507", {"start": v(205.12, 121.21) * mm, "end": v(208.47, 122.92) * mm});
            skLineSegment(sketch, "E3508", {"start": v(208.47, 122.92) * mm, "end": v(211.18, 123.73) * mm});
            skLineSegment(sketch, "E3509", {"start": v(211.18, 123.73) * mm, "end": v(212.1, 123.77) * mm});
            skLineSegment(sketch, "E3510", {"start": v(212.1, 123.77) * mm, "end": v(211.67, 123.18) * mm});
            skLineSegment(sketch, "E3511", {"start": v(211.67, 123.18) * mm, "end": v(210.2, 121.54) * mm});
            skLineSegment(sketch, "E3512", {"start": v(210.2, 121.54) * mm, "end": v(208.06, 119.52) * mm});
            skLineSegment(sketch, "E3513", {"start": v(208.06, 119.52) * mm, "end": v(205.8, 117.6) * mm});
            skLineSegment(sketch, "E3514", {"start": v(205.8, 117.6) * mm, "end": v(204.12, 116.18) * mm});
            skLineSegment(sketch, "E3515", {"start": v(204.12, 116.18) * mm, "end": v(203.58, 115.68) * mm});
            skLineSegment(sketch, "E3516", {"start": v(203.58, 115.68) * mm, "end": v(203.24, 115.38) * mm});
            skLineSegment(sketch, "E3517", {"start": v(203.24, 115.38) * mm, "end": v(202.39, 114.32) * mm});
            skLineSegment(sketch, "E3518", {"start": v(202.39, 114.32) * mm, "end": v(201.39, 112.81) * mm});
            skLineSegment(sketch, "E3519", {"start": v(201.39, 112.81) * mm, "end": v(200.4, 111.34) * mm});
            skLineSegment(sketch, "E3520", {"start": v(200.4, 111.34) * mm, "end": v(199.57, 110.34) * mm});
            skLineSegment(sketch, "E3521", {"start": v(199.57, 110.34) * mm, "end": v(199.25, 110.06) * mm});
            skLineSegment(sketch, "E3522", {"start": v(199.25, 110.06) * mm, "end": v(198.6, 109.5) * mm});
            skLineSegment(sketch, "E3523", {"start": v(198.6, 109.5) * mm, "end": v(194.88, 107.18) * mm});
            skLineSegment(sketch, "E3524", {"start": v(194.88, 107.18) * mm, "end": v(191.01, 105.01) * mm});
            skLineSegment(sketch, "E3525", {"start": v(191.01, 105.01) * mm, "end": v(190.3, 104.53) * mm});
            skLineSegment(sketch, "E3526", {"start": v(190.3, 104.53) * mm, "end": v(188.6, 103.38) * mm});
            skLineSegment(sketch, "E3527", {"start": v(188.6, 103.38) * mm, "end": v(180.45, 97.28) * mm});
            skLineSegment(sketch, "E3528", {"start": v(180.45, 97.28) * mm, "end": v(172.25, 91.22) * mm});
            skLineSegment(sketch, "E3529", {"start": v(172.25, 91.22) * mm, "end": v(170.55, 90.09) * mm});
            skLineSegment(sketch, "E3530", {"start": v(170.55, 90.09) * mm, "end": v(170.24, 89.88) * mm});
            skLineSegment(sketch, "E3531", {"start": v(170.24, 89.88) * mm, "end": v(169.27, 89.32) * mm});
            skLineSegment(sketch, "E3532", {"start": v(169.27, 89.32) * mm, "end": v(168, 88.56) * mm});
            skLineSegment(sketch, "E3533", {"start": v(168, 88.56) * mm, "end": v(166.83, 87.7) * mm});
            skLineSegment(sketch, "E3534", {"start": v(166.83, 87.7) * mm, "end": v(166.03, 86.87) * mm});
            skLineSegment(sketch, "E3535", {"start": v(166.03, 86.87) * mm, "end": v(165.82, 86.56) * mm});
            skLineSegment(sketch, "E3536", {"start": v(165.82, 86.56) * mm, "end": v(165.61, 86.27) * mm});
            skLineSegment(sketch, "E3537", {"start": v(165.61, 86.27) * mm, "end": v(165.03, 84.7) * mm});
            skLineSegment(sketch, "E3538", {"start": v(165.03, 84.7) * mm, "end": v(164.98, 83) * mm});
            skLineSegment(sketch, "E3539", {"start": v(164.98, 83) * mm, "end": v(165.04, 82.65) * mm});
            skLineSegment(sketch, "E3540", {"start": v(165.04, 82.65) * mm, "end": v(165.11, 82.3) * mm});
            skLineSegment(sketch, "E3541", {"start": v(165.11, 82.3) * mm, "end": v(165.38, 82.06) * mm});
            skLineSegment(sketch, "E3542", {"start": v(165.38, 82.06) * mm, "end": v(165.78, 81.7) * mm});
            skLineSegment(sketch, "E3543", {"start": v(165.78, 81.7) * mm, "end": v(167.3, 80.89) * mm});
            skLineSegment(sketch, "E3544", {"start": v(167.3, 80.89) * mm, "end": v(169, 80.9) * mm});
            skLineSegment(sketch, "E3545", {"start": v(169, 80.9) * mm, "end": v(170.5, 81.87) * mm});
            skLineSegment(sketch, "E3546", {"start": v(170.5, 81.87) * mm, "end": v(171.54, 83.1) * mm});
            skLineSegment(sketch, "E3547", {"start": v(171.54, 83.1) * mm, "end": v(171.82, 83.55) * mm});
            skLineSegment(sketch, "E3548", {"start": v(171.82, 83.55) * mm, "end": v(171.92, 83.7) * mm});
            skLineSegment(sketch, "E3549", {"start": v(171.92, 83.7) * mm, "end": v(172.48, 84.64) * mm});
            skLineSegment(sketch, "E3550", {"start": v(172.48, 84.64) * mm, "end": v(173.09, 85.53) * mm});
            skLineSegment(sketch, "E3551", {"start": v(173.09, 85.53) * mm, "end": v(173.21, 85.66) * mm});
            skLineSegment(sketch, "E3552", {"start": v(173.21, 85.66) * mm, "end": v(173.77, 86.2) * mm});
            skLineSegment(sketch, "E3553", {"start": v(173.77, 86.2) * mm, "end": v(175.6, 87.63) * mm});
            skLineSegment(sketch, "E3554", {"start": v(175.6, 87.63) * mm, "end": v(178.32, 89.45) * mm});
            skLineSegment(sketch, "E3555", {"start": v(178.32, 89.45) * mm, "end": v(181.13, 91.18) * mm});
            skLineSegment(sketch, "E3556", {"start": v(181.13, 91.18) * mm, "end": v(183.14, 92.45) * mm});
            skLineSegment(sketch, "E3557", {"start": v(183.14, 92.45) * mm, "end": v(183.8, 92.9) * mm});
            skLineSegment(sketch, "E3558", {"start": v(183.8, 92.9) * mm, "end": v(185.55, 94.13) * mm});
            skLineSegment(sketch, "E3559", {"start": v(185.55, 94.13) * mm, "end": v(194.34, 100.14) * mm});
            skLineSegment(sketch, "E3560", {"start": v(194.34, 100.14) * mm, "end": v(202.96, 106.4) * mm});
            skLineSegment(sketch, "E3561", {"start": v(202.96, 106.4) * mm, "end": v(204.64, 107.74) * mm});
            skLineSegment(sketch, "E3562", {"start": v(204.64, 107.74) * mm, "end": v(205.4, 108.36) * mm});
            skLineSegment(sketch, "E3563", {"start": v(205.4, 108.36) * mm, "end": v(207.7, 110.21) * mm});
            skLineSegment(sketch, "E3564", {"start": v(207.7, 110.21) * mm, "end": v(210.64, 112.43) * mm});
            skLineSegment(sketch, "E3565", {"start": v(210.64, 112.43) * mm, "end": v(213.75, 114.36) * mm});
            skLineSegment(sketch, "E3566", {"start": v(213.75, 114.36) * mm, "end": v(216.46, 115.65) * mm});
            skLineSegment(sketch, "E3567", {"start": v(216.46, 115.65) * mm, "end": v(217.39, 116) * mm});
            skLineSegment(sketch, "E3568", {"start": v(217.39, 116) * mm, "end": v(218.58, 116.43) * mm});
            skLineSegment(sketch, "E3569", {"start": v(218.58, 116.43) * mm, "end": v(222.05, 118.07) * mm});
            skLineSegment(sketch, "E3570", {"start": v(222.05, 118.07) * mm, "end": v(226.69, 120.5) * mm});
            skLineSegment(sketch, "E3571", {"start": v(226.69, 120.5) * mm, "end": v(231.4, 122.71) * mm});
            skLineSegment(sketch, "E3572", {"start": v(231.4, 122.71) * mm, "end": v(235.04, 123.93) * mm});
            skLineSegment(sketch, "E3573", {"start": v(235.04, 123.93) * mm, "end": v(236.28, 124.14) * mm});
            skLineSegment(sketch, "E3574", {"start": v(236.28, 124.14) * mm, "end": v(233.56, 121.89) * mm});
            skLineSegment(sketch, "E3575", {"start": v(233.56, 121.89) * mm, "end": v(225.06, 115.51) * mm});
            skLineSegment(sketch, "E3576", {"start": v(225.06, 115.51) * mm, "end": v(213.38, 107.43) * mm});
            skLineSegment(sketch, "E3577", {"start": v(213.38, 107.43) * mm, "end": v(201.57, 99.53) * mm});
            skLineSegment(sketch, "E3578", {"start": v(201.57, 99.53) * mm, "end": v(192.8, 93.53) * mm});
            skLineSegment(sketch, "E3579", {"start": v(192.8, 93.53) * mm, "end": v(189.93, 91.46) * mm});
            skLineSegment(sketch, "E3580", {"start": v(189.93, 91.46) * mm, "end": v(189.38, 91.07) * mm});
            skLineSegment(sketch, "E3581", {"start": v(189.38, 91.07) * mm, "end": v(184.07, 86.93) * mm});
            skLineSegment(sketch, "E3582", {"start": v(184.07, 86.93) * mm, "end": v(183.54, 86.52) * mm});
            skLineSegment(sketch, "E3583", {"start": v(183.54, 86.52) * mm, "end": v(183.08, 86.16) * mm});
            skLineSegment(sketch, "E3584", {"start": v(183.08, 86.16) * mm, "end": v(181.67, 85.16) * mm});
            skLineSegment(sketch, "E3585", {"start": v(181.67, 85.16) * mm, "end": v(179.95, 83.76) * mm});
            skLineSegment(sketch, "E3586", {"start": v(179.95, 83.76) * mm, "end": v(178.66, 82.04) * mm});
            skLineSegment(sketch, "E3587", {"start": v(178.66, 82.04) * mm, "end": v(178.13, 80.3) * mm});
            skLineSegment(sketch, "E3588", {"start": v(178.13, 80.3) * mm, "end": v(178.11, 79.7) * mm});
            skLineSegment(sketch, "E3589", {"start": v(178.11, 79.7) * mm, "end": v(178.1, 79.19) * mm});
            skLineSegment(sketch, "E3590", {"start": v(178.1, 79.19) * mm, "end": v(178.5, 78.85) * mm});
            skLineSegment(sketch, "E3591", {"start": v(178.5, 78.85) * mm, "end": v(178.76, 78.62) * mm});
            skLineSegment(sketch, "E3592", {"start": v(178.76, 78.62) * mm, "end": v(179.7, 78.1) * mm});
            skLineSegment(sketch, "E3593", {"start": v(179.7, 78.1) * mm, "end": v(180.98, 77.72) * mm});
            skLineSegment(sketch, "E3594", {"start": v(180.98, 77.72) * mm, "end": v(182.29, 77.69) * mm});
            skLineSegment(sketch, "E3595", {"start": v(182.29, 77.69) * mm, "end": v(183.56, 77.98) * mm});
            skLineSegment(sketch, "E3596", {"start": v(183.56, 77.98) * mm, "end": v(184.72, 78.57) * mm});
            skLineSegment(sketch, "E3597", {"start": v(184.72, 78.57) * mm, "end": v(185.7, 79.43) * mm});
            skLineSegment(sketch, "E3598", {"start": v(185.7, 79.43) * mm, "end": v(186.45, 80.53) * mm});
            skLineSegment(sketch, "E3599", {"start": v(186.45, 80.53) * mm, "end": v(186.82, 81.5) * mm});
            skLineSegment(sketch, "E3600", {"start": v(186.82, 81.5) * mm, "end": v(186.88, 81.85) * mm});
            skLineSegment(sketch, "E3601", {"start": v(186.88, 81.85) * mm, "end": v(187.47, 82.21) * mm});
            skLineSegment(sketch, "E3602", {"start": v(187.47, 82.21) * mm, "end": v(189.17, 83.44) * mm});
            skLineSegment(sketch, "E3603", {"start": v(189.17, 83.44) * mm, "end": v(191.27, 85.15) * mm});
            skLineSegment(sketch, "E3604", {"start": v(191.27, 85.15) * mm, "end": v(193.26, 86.89) * mm});
            skLineSegment(sketch, "E3605", {"start": v(193.26, 86.89) * mm, "end": v(195.25, 88.57) * mm});
            skLineSegment(sketch, "E3606", {"start": v(195.25, 88.57) * mm, "end": v(197.34, 90.12) * mm});
            skLineSegment(sketch, "E3607", {"start": v(197.34, 90.12) * mm, "end": v(199.6, 91.44) * mm});
            skLineSegment(sketch, "E3608", {"start": v(199.6, 91.44) * mm, "end": v(202.17, 92.45) * mm});
            skLineSegment(sketch, "E3609", {"start": v(202.17, 92.45) * mm, "end": v(204.37, 92.97) * mm});
            skLineSegment(sketch, "E3610", {"start": v(204.37, 92.97) * mm, "end": v(205.12, 93.06) * mm});
            skLineSegment(sketch, "E3611", {"start": v(205.12, 93.06) * mm, "end": v(205.7, 93.13) * mm});
            skLineSegment(sketch, "E3612", {"start": v(205.7, 93.13) * mm, "end": v(205.95, 93.67) * mm});
            skLineSegment(sketch, "E3613", {"start": v(205.95, 93.67) * mm, "end": v(206.08, 93.94) * mm});
            skLineSegment(sketch, "E3614", {"start": v(206.08, 93.94) * mm, "end": v(206.85, 95.2) * mm});
            skLineSegment(sketch, "E3615", {"start": v(206.85, 95.2) * mm, "end": v(207.8, 96.32) * mm});
            skLineSegment(sketch, "E3616", {"start": v(207.8, 96.32) * mm, "end": v(208.01, 96.52) * mm});
            skLineSegment(sketch, "E3617", {"start": v(208.01, 96.52) * mm, "end": v(208.58, 97.06) * mm});
            skLineSegment(sketch, "E3618", {"start": v(208.58, 97.06) * mm, "end": v(210.5, 98.41) * mm});
            skLineSegment(sketch, "E3619", {"start": v(210.5, 98.41) * mm, "end": v(213.43, 100.03) * mm});
            skLineSegment(sketch, "E3620", {"start": v(213.43, 100.03) * mm, "end": v(216.47, 101.53) * mm});
            skLineSegment(sketch, "E3621", {"start": v(216.47, 101.53) * mm, "end": v(218.6, 102.66) * mm});
            skLineSegment(sketch, "E3622", {"start": v(218.6, 102.66) * mm, "end": v(219.29, 103.08) * mm});
            skLineSegment(sketch, "E3623", {"start": v(219.29, 103.08) * mm, "end": v(219.52, 103.22) * mm});
            skLineSegment(sketch, "E3624", {"start": v(219.52, 103.22) * mm, "end": v(220.16, 103.75) * mm});
            skLineSegment(sketch, "E3625", {"start": v(220.16, 103.75) * mm, "end": v(220.88, 104.51) * mm});
            skLineSegment(sketch, "E3626", {"start": v(220.88, 104.51) * mm, "end": v(221.57, 105.27) * mm});
            skLineSegment(sketch, "E3627", {"start": v(221.57, 105.27) * mm, "end": v(222.12, 105.78) * mm});
            skLineSegment(sketch, "E3628", {"start": v(222.12, 105.78) * mm, "end": v(222.32, 105.92) * mm});
            skLineSegment(sketch, "E3629", {"start": v(222.32, 105.92) * mm, "end": v(223.3, 106.53) * mm});
            skLineSegment(sketch, "E3630", {"start": v(223.3, 106.53) * mm, "end": v(228.5, 109.06) * mm});
            skLineSegment(sketch, "E3631", {"start": v(228.5, 109.06) * mm, "end": v(233.72, 111.6) * mm});
            skLineSegment(sketch, "E3632", {"start": v(233.72, 111.6) * mm, "end": v(234.7, 112.22) * mm});
            skLineSegment(sketch, "E3633", {"start": v(234.7, 112.22) * mm, "end": v(234.82, 112.29) * mm});
            skLineSegment(sketch, "E3634", {"start": v(234.82, 112.29) * mm, "end": v(234.88, 112.36) * mm});
            skLineSegment(sketch, "E3635", {"start": v(234.88, 112.36) * mm, "end": v(235.98, 113.42) * mm});
            skLineSegment(sketch, "E3636", {"start": v(235.98, 113.42) * mm, "end": v(239.63, 116.23) * mm});
            skLineSegment(sketch, "E3637", {"start": v(239.63, 116.23) * mm, "end": v(245, 119.4) * mm});
            skLineSegment(sketch, "E3638", {"start": v(245, 119.4) * mm, "end": v(250.77, 121.73) * mm});
            skLineSegment(sketch, "E3639", {"start": v(250.77, 121.73) * mm, "end": v(255.25, 122.9) * mm});
            skLineSegment(sketch, "E3640", {"start": v(255.25, 122.9) * mm, "end": v(256.76, 123.13) * mm});
            skLineSegment(sketch, "E3641", {"start": v(256.76, 123.13) * mm, "end": v(256.56, 122.55) * mm});
            skLineSegment(sketch, "E3642", {"start": v(256.56, 122.55) * mm, "end": v(255.73, 120.92) * mm});
            skLineSegment(sketch, "E3643", {"start": v(255.73, 120.92) * mm, "end": v(254.36, 118.97) * mm});
            skLineSegment(sketch, "E3644", {"start": v(254.36, 118.97) * mm, "end": v(252.7, 117.26) * mm});
            skLineSegment(sketch, "E3645", {"start": v(252.7, 117.26) * mm, "end": v(250.86, 115.72) * mm});
            skLineSegment(sketch, "E3646", {"start": v(250.86, 115.72) * mm, "end": v(248.86, 114.32) * mm});
            skLineSegment(sketch, "E3647", {"start": v(248.86, 114.32) * mm, "end": v(246.77, 113.02) * mm});
            skLineSegment(sketch, "E3648", {"start": v(246.77, 113.02) * mm, "end": v(244.67, 111.77) * mm});
            skLineSegment(sketch, "E3649", {"start": v(244.67, 111.77) * mm, "end": v(243.12, 110.84) * mm});
            skLineSegment(sketch, "E3650", {"start": v(243.12, 110.84) * mm, "end": v(242.6, 110.52) * mm});
            skLineSegment(sketch, "E3651", {"start": v(242.6, 110.52) * mm, "end": v(242.26, 110.3) * mm});
            skLineSegment(sketch, "E3652", {"start": v(242.26, 110.3) * mm, "end": v(241.29, 109.52) * mm});
            skLineSegment(sketch, "E3653", {"start": v(241.29, 109.52) * mm, "end": v(240.08, 108.38) * mm});
            skLineSegment(sketch, "E3654", {"start": v(240.08, 108.38) * mm, "end": v(238.88, 107.26) * mm});
            skLineSegment(sketch, "E3655", {"start": v(238.88, 107.26) * mm, "end": v(237.94, 106.52) * mm});
            skLineSegment(sketch, "E3656", {"start": v(237.94, 106.52) * mm, "end": v(237.6, 106.32) * mm});
            skLineSegment(sketch, "E3657", {"start": v(237.6, 106.32) * mm, "end": v(237.02, 105.97) * mm});
            skLineSegment(sketch, "E3658", {"start": v(237.02, 105.97) * mm, "end": v(234.06, 104.39) * mm});
            skLineSegment(sketch, "E3659", {"start": v(234.06, 104.39) * mm, "end": v(231.12, 102.78) * mm});
            skLineSegment(sketch, "E3660", {"start": v(231.12, 102.78) * mm, "end": v(230.55, 102.41) * mm});
            skLineSegment(sketch, "E3661", {"start": v(230.55, 102.41) * mm, "end": v(229.13, 101.5) * mm});
            skLineSegment(sketch, "E3662", {"start": v(229.13, 101.5) * mm, "end": v(225.03, 98.56) * mm});
            skLineSegment(sketch, "E3663", {"start": v(225.03, 98.56) * mm, "end": v(219.7, 94.44) * mm});
            skLineSegment(sketch, "E3664", {"start": v(219.7, 94.44) * mm, "end": v(214.33, 90.35) * mm});
            skLineSegment(sketch, "E3665", {"start": v(214.33, 90.35) * mm, "end": v(210.2, 87.46) * mm});
            skLineSegment(sketch, "E3666", {"start": v(210.2, 87.46) * mm, "end": v(208.76, 86.58) * mm});
            skLineSegment(sketch, "E3667", {"start": v(208.76, 86.58) * mm, "end": v(208.06, 86.16) * mm});
            skLineSegment(sketch, "E3668", {"start": v(208.06, 86.16) * mm, "end": v(204.4, 84.31) * mm});
            skLineSegment(sketch, "E3669", {"start": v(204.4, 84.31) * mm, "end": v(200.75, 82.44) * mm});
            skLineSegment(sketch, "E3670", {"start": v(200.75, 82.44) * mm, "end": v(200.05, 82) * mm});
            skLineSegment(sketch, "E3671", {"start": v(200.05, 82) * mm, "end": v(199.47, 81.63) * mm});
            skLineSegment(sketch, "E3672", {"start": v(199.47, 81.63) * mm, "end": v(197.66, 80.62) * mm});
            skLineSegment(sketch, "E3673", {"start": v(197.66, 80.62) * mm, "end": v(195.4, 79.16) * mm});
            skLineSegment(sketch, "E3674", {"start": v(195.4, 79.16) * mm, "end": v(193.67, 77.24) * mm});
            skLineSegment(sketch, "E3675", {"start": v(193.67, 77.24) * mm, "end": v(192.9, 75.18) * mm});
            skLineSegment(sketch, "E3676", {"start": v(192.9, 75.18) * mm, "end": v(192.84, 74.48) * mm});
            skLineSegment(sketch, "E3677", {"start": v(192.84, 74.48) * mm, "end": v(192.82, 74.05) * mm});
            skLineSegment(sketch, "E3678", {"start": v(192.82, 74.05) * mm, "end": v(193.08, 73.71) * mm});
            skLineSegment(sketch, "E3679", {"start": v(193.08, 73.71) * mm, "end": v(193.26, 73.5) * mm});
            skLineSegment(sketch, "E3680", {"start": v(193.26, 73.5) * mm, "end": v(193.83, 72.93) * mm});
            skLineSegment(sketch, "E3681", {"start": v(193.83, 72.93) * mm, "end": v(194.7, 72.29) * mm});
            skLineSegment(sketch, "E3682", {"start": v(194.7, 72.29) * mm, "end": v(195.7, 71.91) * mm});
            skLineSegment(sketch, "E3683", {"start": v(195.7, 71.91) * mm, "end": v(196.53, 71.87) * mm});
            skLineSegment(sketch, "E3684", {"start": v(196.53, 71.87) * mm, "end": v(196.79, 71.93) * mm});
            skLineSegment(sketch, "E3685", {"start": v(196.79, 71.93) * mm, "end": v(197.04, 71.99) * mm});
            skLineSegment(sketch, "E3686", {"start": v(197.04, 71.99) * mm, "end": v(197.75, 72.35) * mm});
            skLineSegment(sketch, "E3687", {"start": v(197.75, 72.35) * mm, "end": v(198.58, 73.05) * mm});
            skLineSegment(sketch, "E3688", {"start": v(198.58, 73.05) * mm, "end": v(199.28, 73.89) * mm});
            skLineSegment(sketch, "E3689", {"start": v(199.28, 73.89) * mm, "end": v(199.75, 74.53) * mm});
            skLineSegment(sketch, "E3690", {"start": v(199.75, 74.53) * mm, "end": v(199.9, 74.75) * mm});
            skLineSegment(sketch, "E3691", {"start": v(199.9, 74.75) * mm, "end": v(200, 74.86) * mm});
            skLineSegment(sketch, "E3692", {"start": v(200, 74.86) * mm, "end": v(200.91, 76.01) * mm});
            skLineSegment(sketch, "E3693", {"start": v(200.91, 76.01) * mm, "end": v(201.02, 76.1) * mm});
            skLineSegment(sketch, "E3694", {"start": v(201.02, 76.1) * mm, "end": v(201.43, 76.5) * mm});
            skLineSegment(sketch, "E3695", {"start": v(201.43, 76.5) * mm, "end": v(202.84, 77.45) * mm});
            skLineSegment(sketch, "E3696", {"start": v(202.84, 77.45) * mm, "end": v(205.07, 78.67) * mm});
            skLineSegment(sketch, "E3697", {"start": v(205.07, 78.67) * mm, "end": v(207.4, 79.79) * mm});
            skLineSegment(sketch, "E3698", {"start": v(207.4, 79.79) * mm, "end": v(209, 80.56) * mm});
            skLineSegment(sketch, "E3699", {"start": v(209, 80.56) * mm, "end": v(209.5, 80.84) * mm});
            skLineSegment(sketch, "E3700", {"start": v(209.5, 80.84) * mm, "end": v(211.1, 81.73) * mm});
            skLineSegment(sketch, "E3701", {"start": v(211.1, 81.73) * mm, "end": v(215.67, 84.76) * mm});
            skLineSegment(sketch, "E3702", {"start": v(215.67, 84.76) * mm, "end": v(221.53, 89.16) * mm});
            skLineSegment(sketch, "E3703", {"start": v(221.53, 89.16) * mm, "end": v(227.33, 93.63) * mm});
            skLineSegment(sketch, "E3704", {"start": v(227.33, 93.63) * mm, "end": v(231.8, 96.81) * mm});
            skLineSegment(sketch, "E3705", {"start": v(231.8, 96.81) * mm, "end": v(233.35, 97.78) * mm});
            skLineSegment(sketch, "E3706", {"start": v(233.35, 97.78) * mm, "end": v(235.73, 99.25) * mm});
            skLineSegment(sketch, "E3707", {"start": v(235.73, 99.25) * mm, "end": v(243.01, 103.46) * mm});
            skLineSegment(sketch, "E3708", {"start": v(243.01, 103.46) * mm, "end": v(252.86, 108.79) * mm});
            skLineSegment(sketch, "E3709", {"start": v(252.86, 108.79) * mm, "end": v(262.8, 113.96) * mm});
            skLineSegment(sketch, "E3710", {"start": v(262.8, 113.96) * mm, "end": v(270.25, 117.84) * mm});
            skLineSegment(sketch, "E3711", {"start": v(270.25, 117.84) * mm, "end": v(272.73, 119.16) * mm});
            skLineSegment(sketch, "E3712", {"start": v(272.73, 119.16) * mm, "end": v(272.94, 119.2) * mm});
            skLineSegment(sketch, "E3713", {"start": v(272.94, 119.2) * mm, "end": v(274, 119.32) * mm});
            skLineSegment(sketch, "E3714", {"start": v(274, 119.32) * mm, "end": v(275.04, 119.43) * mm});
            skLineSegment(sketch, "E3715", {"start": v(275.04, 119.43) * mm, "end": v(275.26, 119.48) * mm});
            skLineSegment(sketch, "E3716", {"start": v(275.26, 119.48) * mm, "end": v(275.43, 119.52) * mm});
            skLineSegment(sketch, "E3717", {"start": v(275.43, 119.52) * mm, "end": v(275.59, 119.6) * mm});
            skLineSegment(sketch, "E3718", {"start": v(275.59, 119.6) * mm, "end": v(276, 119.86) * mm});
            skLineSegment(sketch, "E3719", {"start": v(276, 119.86) * mm, "end": v(277.32, 120.5) * mm});
            skLineSegment(sketch, "E3720", {"start": v(277.32, 120.5) * mm, "end": v(279.34, 121.23) * mm});
            skLineSegment(sketch, "E3721", {"start": v(279.34, 121.23) * mm, "end": v(281.45, 121.57) * mm});
            skLineSegment(sketch, "E3722", {"start": v(281.45, 121.57) * mm, "end": v(282.97, 121.48) * mm});
            skLineSegment(sketch, "E3723", {"start": v(282.97, 121.48) * mm, "end": v(283.44, 121.34) * mm});
            skLineSegment(sketch, "E3724", {"start": v(283.44, 121.34) * mm, "end": v(283.25, 120.8) * mm});
            skLineSegment(sketch, "E3725", {"start": v(283.25, 120.8) * mm, "end": v(282.43, 119.3) * mm});
            skLineSegment(sketch, "E3726", {"start": v(282.43, 119.3) * mm, "end": v(281.07, 117.58) * mm});
            skLineSegment(sketch, "E3727", {"start": v(281.07, 117.58) * mm, "end": v(279.46, 116.07) * mm});
            skLineSegment(sketch, "E3728", {"start": v(279.46, 116.07) * mm, "end": v(277.69, 114.68) * mm});
            skLineSegment(sketch, "E3729", {"start": v(277.69, 114.68) * mm, "end": v(275.86, 113.34) * mm});
            skLineSegment(sketch, "E3730", {"start": v(275.86, 113.34) * mm, "end": v(274.05, 111.94) * mm});
            skLineSegment(sketch, "E3731", {"start": v(274.05, 111.94) * mm, "end": v(272.37, 110.4) * mm});
            skLineSegment(sketch, "E3732", {"start": v(272.37, 110.4) * mm, "end": v(271.23, 109.1) * mm});
            skLineSegment(sketch, "E3733", {"start": v(271.23, 109.1) * mm, "end": v(270.9, 108.63) * mm});
            skLineSegment(sketch, "E3734", {"start": v(270.9, 108.63) * mm, "end": v(267.5, 106.55) * mm});
            skLineSegment(sketch, "E3735", {"start": v(267.5, 106.55) * mm, "end": v(250.73, 95.68) * mm});
            skLineSegment(sketch, "E3736", {"start": v(250.73, 95.68) * mm, "end": v(233.97, 84.79) * mm});
            skLineSegment(sketch, "E3737", {"start": v(233.97, 84.79) * mm, "end": v(230.57, 82.7) * mm});
            skLineSegment(sketch, "E3738", {"start": v(230.57, 82.7) * mm, "end": v(230.26, 82.5) * mm});
            skLineSegment(sketch, "E3739", {"start": v(230.26, 82.5) * mm, "end": v(228.58, 81.84) * mm});
            skLineSegment(sketch, "E3740", {"start": v(228.58, 81.84) * mm, "end": v(226.88, 81.17) * mm});
            skLineSegment(sketch, "E3741", {"start": v(226.88, 81.17) * mm, "end": v(226.56, 80.98) * mm});
            skLineSegment(sketch, "E3742", {"start": v(226.56, 80.98) * mm, "end": v(225.68, 80.45) * mm});
            skLineSegment(sketch, "E3743", {"start": v(225.68, 80.45) * mm, "end": v(223.26, 78.5) * mm});
            skLineSegment(sketch, "E3744", {"start": v(223.26, 78.5) * mm, "end": v(220.07, 75.7) * mm});
            skLineSegment(sketch, "E3745", {"start": v(220.07, 75.7) * mm, "end": v(216.7, 73.27) * mm});
            skLineSegment(sketch, "E3746", {"start": v(216.7, 73.27) * mm, "end": v(213.86, 72.07) * mm});
            skLineSegment(sketch, "E3747", {"start": v(213.86, 72.07) * mm, "end": v(212.88, 71.94) * mm});
            skLineSegment(sketch, "E3748", {"start": v(212.88, 71.94) * mm, "end": v(211.97, 71.83) * mm});
            skLineSegment(sketch, "E3749", {"start": v(211.97, 71.83) * mm, "end": v(211.94, 70.92) * mm});
            skLineSegment(sketch, "E3750", {"start": v(211.94, 70.92) * mm, "end": v(211.93, 70.7) * mm});
            skLineSegment(sketch, "E3751", {"start": v(211.93, 70.7) * mm, "end": v(211.86, 70.01) * mm});
            skLineSegment(sketch, "E3752", {"start": v(211.86, 70.01) * mm, "end": v(211.67, 69.35) * mm});
            skLineSegment(sketch, "E3753", {"start": v(211.67, 69.35) * mm, "end": v(211.32, 68.74) * mm});
            skLineSegment(sketch, "E3754", {"start": v(211.32, 68.74) * mm, "end": v(210.93, 68.18) * mm});
            skLineSegment(sketch, "E3755", {"start": v(210.93, 68.18) * mm, "end": v(210.8, 68) * mm});
            skLineSegment(sketch, "E3756", {"start": v(210.8, 68) * mm, "end": v(210.16, 67.12) * mm});
            skLineSegment(sketch, "E3757", {"start": v(210.16, 67.12) * mm, "end": v(211.04, 66.5) * mm});
            skLineSegment(sketch, "E3758", {"start": v(211.04, 66.5) * mm, "end": v(211.63, 66.08) * mm});
            skLineSegment(sketch, "E3759", {"start": v(211.63, 66.08) * mm, "end": v(213.9, 65.56) * mm});
            skLineSegment(sketch, "E3760", {"start": v(213.9, 65.56) * mm, "end": v(216.58, 66.38) * mm});
            skLineSegment(sketch, "E3761", {"start": v(216.58, 66.38) * mm, "end": v(219.08, 68.14) * mm});
            skLineSegment(sketch, "E3762", {"start": v(219.08, 68.14) * mm, "end": v(220.79, 69.58) * mm});
            skLineSegment(sketch, "E3763", {"start": v(220.79, 69.58) * mm, "end": v(221.38, 70.04) * mm});
            skLineSegment(sketch, "E3764", {"start": v(221.38, 70.04) * mm, "end": v(222.83, 71.14) * mm});
            skLineSegment(sketch, "E3765", {"start": v(222.83, 71.14) * mm, "end": v(230.3, 76.49) * mm});
            skLineSegment(sketch, "E3766", {"start": v(230.3, 76.49) * mm, "end": v(238.07, 81.38) * mm});
            skLineSegment(sketch, "E3767", {"start": v(238.07, 81.38) * mm, "end": v(239.66, 82.26) * mm});
            skLineSegment(sketch, "E3768", {"start": v(239.66, 82.26) * mm, "end": v(240.88, 82.93) * mm});
            skLineSegment(sketch, "E3769", {"start": v(240.88, 82.93) * mm, "end": v(246.85, 86.54) * mm});
            skLineSegment(sketch, "E3770", {"start": v(246.85, 86.54) * mm, "end": v(252.68, 90.36) * mm});
            skLineSegment(sketch, "E3771", {"start": v(252.68, 90.36) * mm, "end": v(253.83, 91.13) * mm});
            skLineSegment(sketch, "E3772", {"start": v(253.83, 91.13) * mm, "end": v(254.66, 91.7) * mm});
            skLineSegment(sketch, "E3773", {"start": v(254.66, 91.7) * mm, "end": v(257.07, 93.48) * mm});
            skLineSegment(sketch, "E3774", {"start": v(257.07, 93.48) * mm, "end": v(260.32, 95.95) * mm});
            skLineSegment(sketch, "E3775", {"start": v(260.32, 95.95) * mm, "end": v(263.64, 98.27) * mm});
            skLineSegment(sketch, "E3776", {"start": v(263.64, 98.27) * mm, "end": v(266.2, 99.79) * mm});
            skLineSegment(sketch, "E3777", {"start": v(266.2, 99.79) * mm, "end": v(267.11, 100.2) * mm});
            skLineSegment(sketch, "E3778", {"start": v(267.11, 100.2) * mm, "end": v(267.47, 100.37) * mm});
            skLineSegment(sketch, "E3779", {"start": v(267.47, 100.37) * mm, "end": v(269.4, 100.89) * mm});
            skLineSegment(sketch, "E3780", {"start": v(269.4, 100.89) * mm, "end": v(271.4, 101.4) * mm});
            skLineSegment(sketch, "E3781", {"start": v(271.4, 101.4) * mm, "end": v(271.78, 101.57) * mm});
            skLineSegment(sketch, "E3782", {"start": v(271.78, 101.57) * mm, "end": v(272.8, 102.03) * mm});
            skLineSegment(sketch, "E3783", {"start": v(272.8, 102.03) * mm, "end": v(275.77, 103.62) * mm});
            skLineSegment(sketch, "E3784", {"start": v(275.77, 103.62) * mm, "end": v(279.57, 105.93) * mm});
            skLineSegment(sketch, "E3785", {"start": v(279.57, 105.93) * mm, "end": v(283.26, 108.37) * mm});
            skLineSegment(sketch, "E3786", {"start": v(283.26, 108.37) * mm, "end": v(286.93, 110.77) * mm});
            skLineSegment(sketch, "E3787", {"start": v(286.93, 110.77) * mm, "end": v(290.67, 112.98) * mm});
            skLineSegment(sketch, "E3788", {"start": v(290.67, 112.98) * mm, "end": v(294.6, 114.85) * mm});
            skLineSegment(sketch, "E3789", {"start": v(294.6, 114.85) * mm, "end": v(298.76, 116.22) * mm});
            skLineSegment(sketch, "E3790", {"start": v(298.76, 116.22) * mm, "end": v(302.15, 116.86) * mm});
            skLineSegment(sketch, "E3791", {"start": v(302.15, 116.86) * mm, "end": v(303.3, 116.94) * mm});
            skLineSegment(sketch, "E3792", {"start": v(303.3, 116.94) * mm, "end": v(302.88, 116.05) * mm});
            skLineSegment(sketch, "E3793", {"start": v(302.88, 116.05) * mm, "end": v(300.96, 113.68) * mm});
            skLineSegment(sketch, "E3794", {"start": v(300.96, 113.68) * mm, "end": v(297.75, 111.1) * mm});
            skLineSegment(sketch, "E3795", {"start": v(297.75, 111.1) * mm, "end": v(294.18, 108.85) * mm});
            skLineSegment(sketch, "E3796", {"start": v(294.18, 108.85) * mm, "end": v(291.6, 107.21) * mm});
            skLineSegment(sketch, "E3797", {"start": v(291.6, 107.21) * mm, "end": v(290.8, 106.6) * mm});
            skLineSegment(sketch, "E3798", {"start": v(290.8, 106.6) * mm, "end": v(290.53, 106.39) * mm});
            skLineSegment(sketch, "E3799", {"start": v(290.53, 106.39) * mm, "end": v(289.42, 105.16) * mm});
            skLineSegment(sketch, "E3800", {"start": v(289.42, 105.16) * mm, "end": v(288.35, 103.96) * mm});
            skLineSegment(sketch, "E3801", {"start": v(288.35, 103.96) * mm, "end": v(288.1, 103.77) * mm});
            skLineSegment(sketch, "E3802", {"start": v(288.1, 103.77) * mm, "end": v(286.02, 102.12) * mm});
            skLineSegment(sketch, "E3803", {"start": v(286.02, 102.12) * mm, "end": v(279.51, 97.54) * mm});
            skLineSegment(sketch, "E3804", {"start": v(279.51, 97.54) * mm, "end": v(270.62, 91.62) * mm});
            skLineSegment(sketch, "E3805", {"start": v(270.62, 91.62) * mm, "end": v(261.93, 85.45) * mm});
            skLineSegment(sketch, "E3806", {"start": v(261.93, 85.45) * mm, "end": v(255.82, 80.37) * mm});
            skLineSegment(sketch, "E3807", {"start": v(255.82, 80.37) * mm, "end": v(253.97, 78.48) * mm});
            skLineSegment(sketch, "E3808", {"start": v(253.97, 78.48) * mm, "end": v(253.24, 78.2) * mm});
            skLineSegment(sketch, "E3809", {"start": v(253.24, 78.2) * mm, "end": v(251.17, 77.08) * mm});
            skLineSegment(sketch, "E3810", {"start": v(251.17, 77.08) * mm, "end": v(248.69, 75.36) * mm});
            skLineSegment(sketch, "E3811", {"start": v(248.69, 75.36) * mm, "end": v(246.35, 73.44) * mm});
            skLineSegment(sketch, "E3812", {"start": v(246.35, 73.44) * mm, "end": v(244.57, 71.94) * mm});
            skLineSegment(sketch, "E3813", {"start": v(244.57, 71.94) * mm, "end": v(243.96, 71.45) * mm});
            skLineSegment(sketch, "E3814", {"start": v(243.96, 71.45) * mm, "end": v(243.68, 71.33) * mm});
            skLineSegment(sketch, "E3815", {"start": v(243.68, 71.33) * mm, "end": v(242.83, 70.97) * mm});
            skLineSegment(sketch, "E3816", {"start": v(242.83, 70.97) * mm, "end": v(241.56, 70.43) * mm});
            skLineSegment(sketch, "E3817", {"start": v(241.56, 70.43) * mm, "end": v(240.25, 69.8) * mm});
            skLineSegment(sketch, "E3818", {"start": v(240.25, 69.8) * mm, "end": v(239.01, 69.07) * mm});
            skLineSegment(sketch, "E3819", {"start": v(239.01, 69.07) * mm, "end": v(237.94, 68.22) * mm});
            skLineSegment(sketch, "E3820", {"start": v(237.94, 68.22) * mm, "end": v(237.14, 67.22) * mm});
            skLineSegment(sketch, "E3821", {"start": v(237.14, 67.22) * mm, "end": v(236.71, 66.04) * mm});
            skLineSegment(sketch, "E3822", {"start": v(236.71, 66.04) * mm, "end": v(236.7, 65) * mm});
            skLineSegment(sketch, "E3823", {"start": v(236.7, 65) * mm, "end": v(236.77, 64.67) * mm});
            skLineSegment(sketch, "E3824", {"start": v(236.77, 64.67) * mm, "end": v(236.84, 64.35) * mm});
            skLineSegment(sketch, "E3825", {"start": v(236.84, 64.35) * mm, "end": v(237.32, 63.45) * mm});
            skLineSegment(sketch, "E3826", {"start": v(237.32, 63.45) * mm, "end": v(238.26, 62.6) * mm});
            skLineSegment(sketch, "E3827", {"start": v(238.26, 62.6) * mm, "end": v(239.44, 62.12) * mm});
            skLineSegment(sketch, "E3828", {"start": v(239.44, 62.12) * mm, "end": v(240.75, 62.03) * mm});
            skLineSegment(sketch, "E3829", {"start": v(240.75, 62.03) * mm, "end": v(242.04, 62.34) * mm});
            skLineSegment(sketch, "E3830", {"start": v(242.04, 62.34) * mm, "end": v(243.2, 63.06) * mm});
            skLineSegment(sketch, "E3831", {"start": v(243.2, 63.06) * mm, "end": v(244.06, 64.18) * mm});
            skLineSegment(sketch, "E3832", {"start": v(244.06, 64.18) * mm, "end": v(244.47, 65.33) * mm});
            skLineSegment(sketch, "E3833", {"start": v(244.47, 65.33) * mm, "end": v(244.52, 65.72) * mm});
            skLineSegment(sketch, "E3834", {"start": v(244.52, 65.72) * mm, "end": v(246.79, 67.37) * mm});
            skLineSegment(sketch, "E3835", {"start": v(246.79, 67.37) * mm, "end": v(258.16, 75.53) * mm});
            skLineSegment(sketch, "E3836", {"start": v(258.16, 75.53) * mm, "end": v(269.44, 83.83) * mm});
            skLineSegment(sketch, "E3837", {"start": v(269.44, 83.83) * mm, "end": v(271.65, 85.55) * mm});
            skLineSegment(sketch, "E3838", {"start": v(271.65, 85.55) * mm, "end": v(272.83, 86.45) * mm});
            skLineSegment(sketch, "E3839", {"start": v(272.83, 86.45) * mm, "end": v(276.44, 89) * mm});
            skLineSegment(sketch, "E3840", {"start": v(276.44, 89) * mm, "end": v(281.32, 92.33) * mm});
            skLineSegment(sketch, "E3841", {"start": v(281.32, 92.33) * mm, "end": v(286.11, 95.76) * mm});
            skLineSegment(sketch, "E3842", {"start": v(286.11, 95.76) * mm, "end": v(289.58, 98.52) * mm});
            skLineSegment(sketch, "E3843", {"start": v(289.58, 98.52) * mm, "end": v(290.67, 99.51) * mm});
            skLineSegment(sketch, "E3844", {"start": v(290.67, 99.51) * mm, "end": v(291.42, 99.79) * mm});
            skLineSegment(sketch, "E3845", {"start": v(291.42, 99.79) * mm, "end": v(293.61, 100.78) * mm});
            skLineSegment(sketch, "E3846", {"start": v(293.61, 100.78) * mm, "end": v(296.4, 102.25) * mm});
            skLineSegment(sketch, "E3847", {"start": v(296.4, 102.25) * mm, "end": v(299.07, 103.81) * mm});
            skLineSegment(sketch, "E3848", {"start": v(299.07, 103.81) * mm, "end": v(301.74, 105.35) * mm});
            skLineSegment(sketch, "E3849", {"start": v(301.74, 105.35) * mm, "end": v(304.45, 106.74) * mm});
            skLineSegment(sketch, "E3850", {"start": v(304.45, 106.74) * mm, "end": v(307.29, 107.88) * mm});
            skLineSegment(sketch, "E3851", {"start": v(307.29, 107.88) * mm, "end": v(310.32, 108.65) * mm});
            skLineSegment(sketch, "E3852", {"start": v(310.32, 108.65) * mm, "end": v(312.8, 108.92) * mm});
            skLineSegment(sketch, "E3853", {"start": v(312.8, 108.92) * mm, "end": v(313.63, 108.92) * mm});
            skLineSegment(sketch, "E3854", {"start": v(313.63, 108.92) * mm, "end": v(313.44, 108.22) * mm});
            skLineSegment(sketch, "E3855", {"start": v(313.44, 108.22) * mm, "end": v(312.2, 106.3) * mm});
            skLineSegment(sketch, "E3856", {"start": v(312.2, 106.3) * mm, "end": v(309.92, 104.18) * mm});
            skLineSegment(sketch, "E3857", {"start": v(309.92, 104.18) * mm, "end": v(307.3, 102.35) * mm});
            skLineSegment(sketch, "E3858", {"start": v(307.3, 102.35) * mm, "end": v(305.42, 101.06) * mm});
            skLineSegment(sketch, "E3859", {"start": v(305.42, 101.06) * mm, "end": v(304.84, 100.58) * mm});
            skLineSegment(sketch, "E3860", {"start": v(304.84, 100.58) * mm, "end": v(303.96, 99.86) * mm});
            skLineSegment(sketch, "E3861", {"start": v(303.96, 99.86) * mm, "end": v(299.67, 96.16) * mm});
            skLineSegment(sketch, "E3862", {"start": v(299.67, 96.16) * mm, "end": v(295.36, 92.48) * mm});
            skLineSegment(sketch, "E3863", {"start": v(295.36, 92.48) * mm, "end": v(294.48, 91.77) * mm});
            skLineSegment(sketch, "E3864", {"start": v(294.48, 91.77) * mm, "end": v(292.73, 90.39) * mm});
            skLineSegment(sketch, "E3865", {"start": v(292.73, 90.39) * mm, "end": v(287.4, 86.34) * mm});
            skLineSegment(sketch, "E3866", {"start": v(287.4, 86.34) * mm, "end": v(280.27, 80.96) * mm});
            skLineSegment(sketch, "E3867", {"start": v(280.27, 80.96) * mm, "end": v(273.32, 75.37) * mm});
            skLineSegment(sketch, "E3868", {"start": v(273.32, 75.37) * mm, "end": v(268.31, 70.92) * mm});
            skLineSegment(sketch, "E3869", {"start": v(268.31, 70.92) * mm, "end": v(266.74, 69.34) * mm});
            skLineSegment(sketch, "E3870", {"start": v(266.74, 69.34) * mm, "end": v(265.9, 69.01) * mm});
            skLineSegment(sketch, "E3871", {"start": v(265.9, 69.01) * mm, "end": v(263.5, 67.64) * mm});
            skLineSegment(sketch, "E3872", {"start": v(263.5, 67.64) * mm, "end": v(260.66, 65.53) * mm});
            skLineSegment(sketch, "E3873", {"start": v(260.66, 65.53) * mm, "end": v(257.88, 63.4) * mm});
            skLineSegment(sketch, "E3874", {"start": v(257.88, 63.4) * mm, "end": v(255.62, 62) * mm});
            skLineSegment(sketch, "E3875", {"start": v(255.62, 62) * mm, "end": v(254.82, 61.66) * mm});
            skLineSegment(sketch, "E3876", {"start": v(254.82, 61.66) * mm, "end": v(254, 61.3) * mm});
            skLineSegment(sketch, "E3877", {"start": v(254, 61.3) * mm, "end": v(254.21, 60.42) * mm});
            skLineSegment(sketch, "E3878", {"start": v(254.21, 60.42) * mm, "end": v(254.25, 60.24) * mm});
            skLineSegment(sketch, "E3879", {"start": v(254.25, 60.24) * mm, "end": v(254.18, 59.66) * mm});
            skLineSegment(sketch, "E3880", {"start": v(254.18, 59.66) * mm, "end": v(253.84, 59) * mm});
            skLineSegment(sketch, "E3881", {"start": v(253.84, 59) * mm, "end": v(253.52, 58.19) * mm});
            skLineSegment(sketch, "E3882", {"start": v(253.52, 58.19) * mm, "end": v(253.46, 57.27) * mm});
            skLineSegment(sketch, "E3883", {"start": v(253.46, 57.27) * mm, "end": v(253.52, 56.97) * mm});
            skLineSegment(sketch, "E3884", {"start": v(253.52, 56.97) * mm, "end": v(253.6, 56.47) * mm});
            skLineSegment(sketch, "E3885", {"start": v(253.6, 56.47) * mm, "end": v(254.05, 56.22) * mm});
            skLineSegment(sketch, "E3886", {"start": v(254.05, 56.22) * mm, "end": v(254.5, 55.97) * mm});
            skLineSegment(sketch, "E3887", {"start": v(254.5, 55.97) * mm, "end": v(256.05, 55.53) * mm});
            skLineSegment(sketch, "E3888", {"start": v(256.05, 55.53) * mm, "end": v(257.79, 55.75) * mm});
            skLineSegment(sketch, "E3889", {"start": v(257.79, 55.75) * mm, "end": v(259.34, 56.7) * mm});
            skLineSegment(sketch, "E3890", {"start": v(259.34, 56.7) * mm, "end": v(260.45, 57.77) * mm});
            skLineSegment(sketch, "E3891", {"start": v(260.45, 57.77) * mm, "end": v(260.79, 58.16) * mm});
            skLineSegment(sketch, "E3892", {"start": v(260.79, 58.16) * mm, "end": v(260.9, 58.3) * mm});
            skLineSegment(sketch, "E3893", {"start": v(260.9, 58.3) * mm, "end": v(262.2, 59.75) * mm});
            skLineSegment(sketch, "E3894", {"start": v(262.2, 59.75) * mm, "end": v(262.34, 59.87) * mm});
            skLineSegment(sketch, "E3895", {"start": v(262.34, 59.87) * mm, "end": v(263.06, 60.5) * mm});
            skLineSegment(sketch, "E3896", {"start": v(263.06, 60.5) * mm, "end": v(266.97, 63.39) * mm});
            skLineSegment(sketch, "E3897", {"start": v(266.97, 63.39) * mm, "end": v(270.93, 66.25) * mm});
            skLineSegment(sketch, "E3898", {"start": v(270.93, 66.25) * mm, "end": v(271.68, 66.87) * mm});
            skLineSegment(sketch, "E3899", {"start": v(271.68, 66.87) * mm, "end": v(273.18, 68.12) * mm});
            skLineSegment(sketch, "E3900", {"start": v(273.18, 68.12) * mm, "end": v(280.86, 74.15) * mm});
            skLineSegment(sketch, "E3901", {"start": v(280.86, 74.15) * mm, "end": v(288.6, 80.11) * mm});
            skLineSegment(sketch, "E3902", {"start": v(288.6, 80.11) * mm, "end": v(290.13, 81.32) * mm});
            skLineSegment(sketch, "E3903", {"start": v(290.13, 81.32) * mm, "end": v(290.82, 81.87) * mm});
            skLineSegment(sketch, "E3904", {"start": v(290.82, 81.87) * mm, "end": v(292.86, 83.52) * mm});
            skLineSegment(sketch, "E3905", {"start": v(292.86, 83.52) * mm, "end": v(295.44, 85.47) * mm});
            skLineSegment(sketch, "E3906", {"start": v(295.44, 85.47) * mm, "end": v(298.2, 87.15) * mm});
            skLineSegment(sketch, "E3907", {"start": v(298.2, 87.15) * mm, "end": v(300.63, 88.25) * mm});
            skLineSegment(sketch, "E3908", {"start": v(300.63, 88.25) * mm, "end": v(301.47, 88.53) * mm});
            skLineSegment(sketch, "E3909", {"start": v(301.47, 88.53) * mm, "end": v(302.31, 88.8) * mm});
            skLineSegment(sketch, "E3910", {"start": v(302.31, 88.8) * mm, "end": v(304.69, 90.07) * mm});
            skLineSegment(sketch, "E3911", {"start": v(304.69, 90.07) * mm, "end": v(307.82, 92.3) * mm});
            skLineSegment(sketch, "E3912", {"start": v(307.82, 92.3) * mm, "end": v(310.8, 94.8) * mm});
            skLineSegment(sketch, "E3913", {"start": v(310.8, 94.8) * mm, "end": v(312.85, 96.56) * mm});
            skLineSegment(sketch, "E3914", {"start": v(312.85, 96.56) * mm, "end": v(313.56, 97.13) * mm});
            skLineSegment(sketch, "E3915", {"start": v(313.56, 97.13) * mm, "end": v(314.43, 97.83) * mm});
            skLineSegment(sketch, "E3916", {"start": v(314.43, 97.83) * mm, "end": v(317.21, 99.7) * mm});
            skLineSegment(sketch, "E3917", {"start": v(317.21, 99.7) * mm, "end": v(321.12, 101.71) * mm});
            skLineSegment(sketch, "E3918", {"start": v(321.12, 101.71) * mm, "end": v(325.27, 103.12) * mm});
            skLineSegment(sketch, "E3919", {"start": v(325.27, 103.12) * mm, "end": v(328.54, 103.75) * mm});
            skLineSegment(sketch, "E3920", {"start": v(328.54, 103.75) * mm, "end": v(329.64, 103.85) * mm});
            skLineSegment(sketch, "E3921", {"start": v(329.64, 103.85) * mm, "end": v(329.23, 103.03) * mm});
            skLineSegment(sketch, "E3922", {"start": v(329.23, 103.03) * mm, "end": v(327.74, 100.7) * mm});
            skLineSegment(sketch, "E3923", {"start": v(327.74, 100.7) * mm, "end": v(325.44, 97.92) * mm});
            skLineSegment(sketch, "E3924", {"start": v(325.44, 97.92) * mm, "end": v(322.83, 95.42) * mm});
            skLineSegment(sketch, "E3925", {"start": v(322.83, 95.42) * mm, "end": v(319.98, 93.13) * mm});
            skLineSegment(sketch, "E3926", {"start": v(319.98, 93.13) * mm, "end": v(316.98, 91) * mm});
            skLineSegment(sketch, "E3927", {"start": v(316.98, 91) * mm, "end": v(313.9, 88.94) * mm});
            skLineSegment(sketch, "E3928", {"start": v(313.9, 88.94) * mm, "end": v(310.85, 86.9) * mm});
            skLineSegment(sketch, "E3929", {"start": v(310.85, 86.9) * mm, "end": v(308.62, 85.34) * mm});
            skLineSegment(sketch, "E3930", {"start": v(308.62, 85.34) * mm, "end": v(307.89, 84.8) * mm});
            skLineSegment(sketch, "E3931", {"start": v(307.89, 84.8) * mm, "end": v(306.85, 84) * mm});
            skLineSegment(sketch, "E3932", {"start": v(306.85, 84) * mm, "end": v(296.5, 76.05) * mm});
            skLineSegment(sketch, "E3933", {"start": v(296.5, 76.05) * mm, "end": v(295.48, 75.24) * mm});
            skLineSegment(sketch, "E3934", {"start": v(295.48, 75.24) * mm, "end": v(293.7, 73.84) * mm});
            skLineSegment(sketch, "E3935", {"start": v(293.7, 73.84) * mm, "end": v(288.48, 69.55) * mm});
            skLineSegment(sketch, "E3936", {"start": v(288.48, 69.55) * mm, "end": v(281.5, 63.86) * mm});
            skLineSegment(sketch, "E3937", {"start": v(281.5, 63.86) * mm, "end": v(274.34, 58.43) * mm});
            skLineSegment(sketch, "E3938", {"start": v(274.34, 58.43) * mm, "end": v(268.73, 54.63) * mm});
            skLineSegment(sketch, "E3939", {"start": v(268.73, 54.63) * mm, "end": v(266.79, 53.49) * mm});
            skLineSegment(sketch, "E3940", {"start": v(266.79, 53.49) * mm, "end": v(266.36, 53.24) * mm});
            skLineSegment(sketch, "E3941", {"start": v(266.36, 53.24) * mm, "end": v(266.27, 52.75) * mm});
            skLineSegment(sketch, "E3942", {"start": v(266.27, 52.75) * mm, "end": v(266.2, 52.35) * mm});
            skLineSegment(sketch, "E3943", {"start": v(266.2, 52.35) * mm, "end": v(265.94, 51.16) * mm});
            skLineSegment(sketch, "E3944", {"start": v(265.94, 51.16) * mm, "end": v(265.72, 49.58) * mm});
            skLineSegment(sketch, "E3945", {"start": v(265.72, 49.58) * mm, "end": v(265.96, 48.09) * mm});
            skLineSegment(sketch, "E3946", {"start": v(265.96, 48.09) * mm, "end": v(266.7, 47.03) * mm});
            skLineSegment(sketch, "E3947", {"start": v(266.7, 47.03) * mm, "end": v(267.02, 46.78) * mm});
            skLineSegment(sketch, "E3948", {"start": v(267.02, 46.78) * mm, "end": v(267.27, 46.6) * mm});
            skLineSegment(sketch, "E3949", {"start": v(267.27, 46.6) * mm, "end": v(267.58, 46.58) * mm});
            skLineSegment(sketch, "E3950", {"start": v(267.58, 46.58) * mm, "end": v(267.9, 46.56) * mm});
            skLineSegment(sketch, "E3951", {"start": v(267.9, 46.56) * mm, "end": v(268.88, 46.7) * mm});
            skLineSegment(sketch, "E3952", {"start": v(268.88, 46.7) * mm, "end": v(269.94, 47.21) * mm});
            skLineSegment(sketch, "E3953", {"start": v(269.94, 47.21) * mm, "end": v(270.83, 48.02) * mm});
            skLineSegment(sketch, "E3954", {"start": v(270.83, 48.02) * mm, "end": v(271.44, 48.77) * mm});
            skLineSegment(sketch, "E3955", {"start": v(271.44, 48.77) * mm, "end": v(271.62, 49.03) * mm});
            skLineSegment(sketch, "E3956", {"start": v(271.62, 49.03) * mm, "end": v(271.7, 49.14) * mm});
            skLineSegment(sketch, "E3957", {"start": v(271.7, 49.14) * mm, "end": v(272.12, 49.73) * mm});
            skLineSegment(sketch, "E3958", {"start": v(272.12, 49.73) * mm, "end": v(272.59, 50.26) * mm});
            skLineSegment(sketch, "E3959", {"start": v(272.59, 50.26) * mm, "end": v(272.7, 50.35) * mm});
            skLineSegment(sketch, "E3960", {"start": v(272.7, 50.35) * mm, "end": v(274.73, 52.06) * mm});
            skLineSegment(sketch, "E3961", {"start": v(274.73, 52.06) * mm, "end": v(281.01, 57) * mm});
            skLineSegment(sketch, "E3962", {"start": v(281.01, 57) * mm, "end": v(289.5, 63.44) * mm});
            skLineSegment(sketch, "E3963", {"start": v(289.5, 63.44) * mm, "end": v(297.9, 69.99) * mm});
            skLineSegment(sketch, "E3964", {"start": v(297.9, 69.99) * mm, "end": v(304.04, 75.12) * mm});
            skLineSegment(sketch, "E3965", {"start": v(304.04, 75.12) * mm, "end": v(306, 76.93) * mm});
            skLineSegment(sketch, "E3966", {"start": v(306, 76.93) * mm, "end": v(306.2, 76.94) * mm});
            skLineSegment(sketch, "E3967", {"start": v(306.2, 76.94) * mm, "end": v(306.83, 76.86) * mm});
            skLineSegment(sketch, "E3968", {"start": v(306.83, 76.86) * mm, "end": v(307.67, 76.71) * mm});
            skLineSegment(sketch, "E3969", {"start": v(307.67, 76.71) * mm, "end": v(308.5, 76.74) * mm});
            skLineSegment(sketch, "E3970", {"start": v(308.5, 76.74) * mm, "end": v(309.12, 77.02) * mm});
            skLineSegment(sketch, "E3971", {"start": v(309.12, 77.02) * mm, "end": v(309.28, 77.17) * mm});
            skLineSegment(sketch, "E3972", {"start": v(309.28, 77.17) * mm, "end": v(309.67, 77.56) * mm});
            skLineSegment(sketch, "E3973", {"start": v(309.67, 77.56) * mm, "end": v(311.7, 79.37) * mm});
            skLineSegment(sketch, "E3974", {"start": v(311.7, 79.37) * mm, "end": v(313.75, 81.18) * mm});
            skLineSegment(sketch, "E3975", {"start": v(313.75, 81.18) * mm, "end": v(314.14, 81.56) * mm});
            skLineSegment(sketch, "E3976", {"start": v(314.14, 81.56) * mm, "end": v(315.14, 81.91) * mm});
            skLineSegment(sketch, "E3977", {"start": v(315.14, 81.91) * mm, "end": v(318.04, 83.26) * mm});
            skLineSegment(sketch, "E3978", {"start": v(318.04, 83.26) * mm, "end": v(321.55, 85.33) * mm});
            skLineSegment(sketch, "E3979", {"start": v(321.55, 85.33) * mm, "end": v(324.82, 87.61) * mm});
            skLineSegment(sketch, "E3980", {"start": v(324.82, 87.61) * mm, "end": v(328, 89.94) * mm});
            skLineSegment(sketch, "E3981", {"start": v(328, 89.94) * mm, "end": v(331.23, 92.17) * mm});
            skLineSegment(sketch, "E3982", {"start": v(331.23, 92.17) * mm, "end": v(334.67, 94.14) * mm});
            skLineSegment(sketch, "E3983", {"start": v(334.67, 94.14) * mm, "end": v(338.47, 95.7) * mm});
            skLineSegment(sketch, "E3984", {"start": v(338.47, 95.7) * mm, "end": v(341.69, 96.53) * mm});
            skLineSegment(sketch, "E3985", {"start": v(341.69, 96.53) * mm, "end": v(342.78, 96.68) * mm});
            skLineSegment(sketch, "E3986", {"start": v(342.78, 96.68) * mm, "end": v(342.3, 95.91) * mm});
            skLineSegment(sketch, "E3987", {"start": v(342.3, 95.91) * mm, "end": v(340.63, 93.73) * mm});
            skLineSegment(sketch, "E3988", {"start": v(340.63, 93.73) * mm, "end": v(338.16, 91.1) * mm});
            skLineSegment(sketch, "E3989", {"start": v(338.16, 91.1) * mm, "end": v(335.45, 88.7) * mm});
            skLineSegment(sketch, "E3990", {"start": v(335.45, 88.7) * mm, "end": v(332.57, 86.48) * mm});
            skLineSegment(sketch, "E3991", {"start": v(332.57, 86.48) * mm, "end": v(329.58, 84.38) * mm});
            skLineSegment(sketch, "E3992", {"start": v(329.58, 84.38) * mm, "end": v(326.54, 82.32) * mm});
            skLineSegment(sketch, "E3993", {"start": v(326.54, 82.32) * mm, "end": v(323.54, 80.24) * mm});
            skLineSegment(sketch, "E3994", {"start": v(323.54, 80.24) * mm, "end": v(321.33, 78.63) * mm});
            skLineSegment(sketch, "E3995", {"start": v(321.33, 78.63) * mm, "end": v(320.62, 78.07) * mm});
            skLineSegment(sketch, "E3996", {"start": v(320.62, 78.07) * mm, "end": v(319.87, 77.47) * mm});
            skLineSegment(sketch, "E3997", {"start": v(319.87, 77.47) * mm, "end": v(317.81, 75.45) * mm});
            skLineSegment(sketch, "E3998", {"start": v(317.81, 75.45) * mm, "end": v(315.27, 72.57) * mm});
            skLineSegment(sketch, "E3999", {"start": v(315.27, 72.57) * mm, "end": v(312.72, 69.71) * mm});
            skLineSegment(sketch, "E4000", {"start": v(312.72, 69.71) * mm, "end": v(310.67, 67.72) * mm});
            skLineSegment(sketch, "E4001", {"start": v(310.67, 67.72) * mm, "end": v(309.92, 67.14) * mm});
            skLineSegment(sketch, "E4002", {"start": v(309.92, 67.14) * mm, "end": v(309.74, 67) * mm});
            skLineSegment(sketch, "E4003", {"start": v(309.74, 67) * mm, "end": v(309.13, 66.67) * mm});
            skLineSegment(sketch, "E4004", {"start": v(309.13, 66.67) * mm, "end": v(308.27, 66.3) * mm});
            skLineSegment(sketch, "E4005", {"start": v(308.27, 66.3) * mm, "end": v(307.38, 65.92) * mm});
            skLineSegment(sketch, "E4006", {"start": v(307.38, 65.92) * mm, "end": v(306.72, 65.53) * mm});
            skLineSegment(sketch, "E4007", {"start": v(306.72, 65.53) * mm, "end": v(306.52, 65.37) * mm});
            skLineSegment(sketch, "E4008", {"start": v(306.52, 65.37) * mm, "end": v(306.24, 65.15) * mm});
            skLineSegment(sketch, "E4009", {"start": v(306.24, 65.15) * mm, "end": v(305.48, 64.37) * mm});
            skLineSegment(sketch, "E4010", {"start": v(305.48, 64.37) * mm, "end": v(304.6, 63.25) * mm});
            skLineSegment(sketch, "E4011", {"start": v(304.6, 63.25) * mm, "end": v(303.76, 62.14) * mm});
            skLineSegment(sketch, "E4012", {"start": v(303.76, 62.14) * mm, "end": v(303.06, 61.35) * mm});
            skLineSegment(sketch, "E4013", {"start": v(303.06, 61.35) * mm, "end": v(302.8, 61.12) * mm});
            skLineSegment(sketch, "E4014", {"start": v(302.8, 61.12) * mm, "end": v(302.21, 60.6) * mm});
            skLineSegment(sketch, "E4015", {"start": v(302.21, 60.6) * mm, "end": v(300.33, 59.17) * mm});
            skLineSegment(sketch, "E4016", {"start": v(300.33, 59.17) * mm, "end": v(297.78, 57.35) * mm});
            skLineSegment(sketch, "E4017", {"start": v(297.78, 57.35) * mm, "end": v(295.33, 55.41) * mm});
            skLineSegment(sketch, "E4018", {"start": v(295.33, 55.41) * mm, "end": v(293.62, 53.74) * mm});
            skLineSegment(sketch, "E4019", {"start": v(293.62, 53.74) * mm, "end": v(293.13, 53.12) * mm});
            skLineSegment(sketch, "E4020", {"start": v(293.13, 53.12) * mm, "end": v(292.2, 52.75) * mm});
            skLineSegment(sketch, "E4021", {"start": v(292.2, 52.75) * mm, "end": v(289.66, 51.05) * mm});
            skLineSegment(sketch, "E4022", {"start": v(289.66, 51.05) * mm, "end": v(286.74, 48.4) * mm});
            skLineSegment(sketch, "E4023", {"start": v(286.74, 48.4) * mm, "end": v(283.85, 45.85) * mm});
            skLineSegment(sketch, "E4024", {"start": v(283.85, 45.85) * mm, "end": v(281.34, 44.36) * mm});
            skLineSegment(sketch, "E4025", {"start": v(281.34, 44.36) * mm, "end": v(280.45, 44.1) * mm});
            skLineSegment(sketch, "E4026", {"start": v(280.45, 44.1) * mm, "end": v(279.94, 43.96) * mm});
            skLineSegment(sketch, "E4027", {"start": v(279.94, 43.96) * mm, "end": v(279.75, 43.47) * mm});
            skLineSegment(sketch, "E4028", {"start": v(279.75, 43.47) * mm, "end": v(279.7, 43.35) * mm});
            skLineSegment(sketch, "E4029", {"start": v(279.7, 43.35) * mm, "end": v(279.57, 42.13) * mm});
            skLineSegment(sketch, "E4030", {"start": v(279.57, 42.13) * mm, "end": v(279.58, 42) * mm});
            skLineSegment(sketch, "E4031", {"start": v(279.58, 42) * mm, "end": v(279.59, 41.95) * mm});
            skLineSegment(sketch, "E4032", {"start": v(279.59, 41.95) * mm, "end": v(279.66, 41.55) * mm});
            skLineSegment(sketch, "E4033", {"start": v(279.66, 41.55) * mm, "end": v(279.73, 41.1) * mm});
            skLineSegment(sketch, "E4034", {"start": v(279.73, 41.1) * mm, "end": v(279.74, 41.03) * mm});
            skLineSegment(sketch, "E4035", {"start": v(279.74, 41.03) * mm, "end": v(279.7, 41.02) * mm});
            skLineSegment(sketch, "E4036", {"start": v(279.7, 41.02) * mm, "end": v(279.35, 40.99) * mm});
            skLineSegment(sketch, "E4037", {"start": v(279.35, 40.99) * mm, "end": v(279.33, 40.98) * mm});
            skLineSegment(sketch, "E4038", {"start": v(279.33, 40.98) * mm, "end": v(276.85, 40.84) * mm});
            skLineSegment(sketch, "E4039", {"start": v(276.85, 40.84) * mm, "end": v(278.65, 39.14) * mm});
            skLineSegment(sketch, "E4040", {"start": v(278.65, 39.14) * mm, "end": v(278.95, 38.85) * mm});
            skLineSegment(sketch, "E4041", {"start": v(278.95, 38.85) * mm, "end": v(280.05, 38.17) * mm});
            skLineSegment(sketch, "E4042", {"start": v(280.05, 38.17) * mm, "end": v(281.43, 37.81) * mm});
            skLineSegment(sketch, "E4043", {"start": v(281.43, 37.81) * mm, "end": v(282.79, 37.97) * mm});
            skLineSegment(sketch, "E4044", {"start": v(282.79, 37.97) * mm, "end": v(284.1, 38.51) * mm});
            skLineSegment(sketch, "E4045", {"start": v(284.1, 38.51) * mm, "end": v(285.38, 39.33) * mm});
            skLineSegment(sketch, "E4046", {"start": v(285.38, 39.33) * mm, "end": v(286.6, 40.3) * mm});
            skLineSegment(sketch, "E4047", {"start": v(286.6, 40.3) * mm, "end": v(287.74, 41.32) * mm});
            skLineSegment(sketch, "E4048", {"start": v(287.74, 41.32) * mm, "end": v(288.54, 42.04) * mm});
            skLineSegment(sketch, "E4049", {"start": v(288.54, 42.04) * mm, "end": v(288.8, 42.27) * mm});
            skLineSegment(sketch, "E4050", {"start": v(288.8, 42.27) * mm, "end": v(289.46, 42.84) * mm});
            skLineSegment(sketch, "E4051", {"start": v(289.46, 42.84) * mm, "end": v(292.52, 45.87) * mm});
            skLineSegment(sketch, "E4052", {"start": v(292.52, 45.87) * mm, "end": v(295.5, 48.97) * mm});
            skLineSegment(sketch, "E4053", {"start": v(295.5, 48.97) * mm, "end": v(296.11, 49.58) * mm});
            skLineSegment(sketch, "E4054", {"start": v(296.11, 49.58) * mm, "end": v(297.49, 50.37) * mm});
            skLineSegment(sketch, "E4055", {"start": v(297.49, 50.37) * mm, "end": v(301.39, 53.12) * mm});
            skLineSegment(sketch, "E4056", {"start": v(301.39, 53.12) * mm, "end": v(306.36, 57.24) * mm});
            skLineSegment(sketch, "E4057", {"start": v(306.36, 57.24) * mm, "end": v(311.15, 61.6) * mm});
            skLineSegment(sketch, "E4058", {"start": v(311.15, 61.6) * mm, "end": v(314.7, 64.8) * mm});
            skLineSegment(sketch, "E4059", {"start": v(314.7, 64.8) * mm, "end": v(315.93, 65.82) * mm});
            skLineSegment(sketch, "E4060", {"start": v(315.93, 65.82) * mm, "end": v(317.36, 67.04) * mm});
            skLineSegment(sketch, "E4061", {"start": v(317.36, 67.04) * mm, "end": v(324.7, 72.8) * mm});
            skLineSegment(sketch, "E4062", {"start": v(324.7, 72.8) * mm, "end": v(332.33, 78.15) * mm});
            skLineSegment(sketch, "E4063", {"start": v(332.33, 78.15) * mm, "end": v(333.91, 79.16) * mm});
            skLineSegment(sketch, "E4064", {"start": v(333.91, 79.16) * mm, "end": v(334.13, 79.3) * mm});
            skLineSegment(sketch, "E4065", {"start": v(334.13, 79.3) * mm, "end": v(334.75, 79.82) * mm});
            skLineSegment(sketch, "E4066", {"start": v(334.75, 79.82) * mm, "end": v(335.48, 80.58) * mm});
            skLineSegment(sketch, "E4067", {"start": v(335.48, 80.58) * mm, "end": v(336.18, 81.32) * mm});
            skLineSegment(sketch, "E4068", {"start": v(336.18, 81.32) * mm, "end": v(336.74, 81.81) * mm});
            skLineSegment(sketch, "E4069", {"start": v(336.74, 81.81) * mm, "end": v(336.94, 81.95) * mm});
            skLineSegment(sketch, "E4070", {"start": v(336.94, 81.95) * mm, "end": v(337.57, 82.37) * mm});
            skLineSegment(sketch, "E4071", {"start": v(337.57, 82.37) * mm, "end": v(340.82, 84.2) * mm});
            skLineSegment(sketch, "E4072", {"start": v(340.82, 84.2) * mm, "end": v(344.05, 86.12) * mm});
            skLineSegment(sketch, "E4073", {"start": v(344.05, 86.12) * mm, "end": v(344.67, 86.57) * mm});
            skLineSegment(sketch, "E4074", {"start": v(344.67, 86.57) * mm, "end": v(345.28, 87) * mm});
            skLineSegment(sketch, "E4075", {"start": v(345.28, 87) * mm, "end": v(347.11, 88.3) * mm});
            skLineSegment(sketch, "E4076", {"start": v(347.11, 88.3) * mm, "end": v(349.83, 89.84) * mm});
            skLineSegment(sketch, "E4077", {"start": v(349.83, 89.84) * mm, "end": v(352.68, 90.63) * mm});
            skLineSegment(sketch, "E4078", {"start": v(352.68, 90.63) * mm, "end": v(354.9, 90.4) * mm});
            skLineSegment(sketch, "E4079", {"start": v(354.9, 90.4) * mm, "end": v(355.54, 90.1) * mm});
            skLineSegment(sketch, "E4080", {"start": v(355.54, 90.1) * mm, "end": v(355.12, 88.77) * mm});
            skLineSegment(sketch, "E4081", {"start": v(355.12, 88.77) * mm, "end": v(353.27, 84.97) * mm});
            skLineSegment(sketch, "E4082", {"start": v(353.27, 84.97) * mm, "end": v(350.17, 80.7) * mm});
            skLineSegment(sketch, "E4083", {"start": v(350.17, 80.7) * mm, "end": v(346.45, 77.05) * mm});
            skLineSegment(sketch, "E4084", {"start": v(346.45, 77.05) * mm, "end": v(342.3, 73.8) * mm});
            skLineSegment(sketch, "E4085", {"start": v(342.3, 73.8) * mm, "end": v(337.95, 70.75) * mm});
            skLineSegment(sketch, "E4086", {"start": v(337.95, 70.75) * mm, "end": v(333.58, 67.65) * mm});
            skLineSegment(sketch, "E4087", {"start": v(333.58, 67.65) * mm, "end": v(329.4, 64.3) * mm});
            skLineSegment(sketch, "E4088", {"start": v(329.4, 64.3) * mm, "end": v(326.48, 61.48) * mm});
            skLineSegment(sketch, "E4089", {"start": v(326.48, 61.48) * mm, "end": v(325.61, 60.46) * mm});
            skLineSegment(sketch, "E4090", {"start": v(325.61, 60.46) * mm, "end": v(324.31, 59.72) * mm});
            skLineSegment(sketch, "E4091", {"start": v(324.31, 59.72) * mm, "end": v(318.07, 55.63) * mm});
            skLineSegment(sketch, "E4092", {"start": v(318.07, 55.63) * mm, "end": v(312.06, 51.19) * mm});
            skLineSegment(sketch, "E4093", {"start": v(312.06, 51.19) * mm, "end": v(310.88, 50.26) * mm});
            skLineSegment(sketch, "E4094", {"start": v(310.88, 50.26) * mm, "end": v(309.33, 49.03) * mm});
            skLineSegment(sketch, "E4095", {"start": v(309.33, 49.03) * mm, "end": v(294, 36.34) * mm});
            skLineSegment(sketch, "E4096", {"start": v(294, 36.34) * mm, "end": v(292.45, 35.09) * mm});
            skLineSegment(sketch, "E4097", {"start": v(292.45, 35.09) * mm, "end": v(291.92, 34.68) * mm});
            skLineSegment(sketch, "E4098", {"start": v(291.92, 34.68) * mm, "end": v(292.07, 34.03) * mm});
            skLineSegment(sketch, "E4099", {"start": v(292.07, 34.03) * mm, "end": v(292.13, 33.77) * mm});
            skLineSegment(sketch, "E4100", {"start": v(292.13, 33.77) * mm, "end": v(292.07, 32.93) * mm});
            skLineSegment(sketch, "E4101", {"start": v(292.07, 32.93) * mm, "end": v(291.78, 32.02) * mm});
            skLineSegment(sketch, "E4102", {"start": v(291.78, 32.02) * mm, "end": v(291.56, 31.1) * mm});
            skLineSegment(sketch, "E4103", {"start": v(291.56, 31.1) * mm, "end": v(291.7, 30.2) * mm});
            skLineSegment(sketch, "E4104", {"start": v(291.7, 30.2) * mm, "end": v(291.82, 29.95) * mm});
            skLineSegment(sketch, "E4105", {"start": v(291.82, 29.95) * mm, "end": v(292.02, 29.53) * mm});
            skLineSegment(sketch, "E4106", {"start": v(292.02, 29.53) * mm, "end": v(292.47, 29.39) * mm});
            skLineSegment(sketch, "E4107", {"start": v(292.47, 29.39) * mm, "end": v(293.07, 29.2) * mm});
            skLineSegment(sketch, "E4108", {"start": v(293.07, 29.2) * mm, "end": v(295.08, 29.32) * mm});
            skLineSegment(sketch, "E4109", {"start": v(295.08, 29.32) * mm, "end": v(297.18, 30.5) * mm});
            skLineSegment(sketch, "E4110", {"start": v(297.18, 30.5) * mm, "end": v(298.96, 32.34) * mm});
            skLineSegment(sketch, "E4111", {"start": v(298.96, 32.34) * mm, "end": v(300.17, 33.77) * mm});
            skLineSegment(sketch, "E4112", {"start": v(300.17, 33.77) * mm, "end": v(300.6, 34.22) * mm});
            skLineSegment(sketch, "E4113", {"start": v(300.6, 34.22) * mm, "end": v(301.1, 34.73) * mm});
            skLineSegment(sketch, "E4114", {"start": v(301.1, 34.73) * mm, "end": v(306.27, 39.33) * mm});
            skLineSegment(sketch, "E4115", {"start": v(306.27, 39.33) * mm, "end": v(306.83, 39.76) * mm});
            skLineSegment(sketch, "E4116", {"start": v(306.83, 39.76) * mm, "end": v(309.85, 42.08) * mm});
            skLineSegment(sketch, "E4117", {"start": v(309.85, 42.08) * mm, "end": v(324.86, 53.81) * mm});
            skLineSegment(sketch, "E4118", {"start": v(324.86, 53.81) * mm, "end": v(339.89, 65.52) * mm});
            skLineSegment(sketch, "E4119", {"start": v(339.89, 65.52) * mm, "end": v(342.92, 67.83) * mm});
            skLineSegment(sketch, "E4120", {"start": v(342.92, 67.83) * mm, "end": v(344.72, 68.55) * mm});
            skLineSegment(sketch, "E4121", {"start": v(344.72, 68.55) * mm, "end": v(349.95, 71.1) * mm});
            skLineSegment(sketch, "E4122", {"start": v(349.95, 71.1) * mm, "end": v(356.75, 74.75) * mm});
            skLineSegment(sketch, "E4123", {"start": v(356.75, 74.75) * mm, "end": v(363.63, 78.25) * mm});
            skLineSegment(sketch, "E4124", {"start": v(363.63, 78.25) * mm, "end": v(369.04, 80.5) * mm});
            skLineSegment(sketch, "E4125", {"start": v(369.04, 80.5) * mm, "end": v(370.9, 81.05) * mm});
            skLineSegment(sketch, "E4126", {"start": v(370.9, 81.05) * mm, "end": v(371.2, 80.97) * mm});
            skLineSegment(sketch, "E4127", {"start": v(371.2, 80.97) * mm, "end": v(372.05, 80.59) * mm});
            skLineSegment(sketch, "E4128", {"start": v(372.05, 80.59) * mm, "end": v(373.03, 79.93) * mm});
            skLineSegment(sketch, "E4129", {"start": v(373.03, 79.93) * mm, "end": v(373.9, 79.12) * mm});
            skLineSegment(sketch, "E4130", {"start": v(373.9, 79.12) * mm, "end": v(374.49, 78.41) * mm});
            skLineSegment(sketch, "E4131", {"start": v(374.49, 78.41) * mm, "end": v(374.67, 78.17) * mm});
            skLineSegment(sketch, "E4132", {"start": v(374.67, 78.17) * mm, "end": v(374.34, 77.5) * mm});
            skLineSegment(sketch, "E4133", {"start": v(374.34, 77.5) * mm, "end": v(373.08, 75.65) * mm});
            skLineSegment(sketch, "E4134", {"start": v(373.08, 75.65) * mm, "end": v(371.1, 73.52) * mm});
            skLineSegment(sketch, "E4135", {"start": v(371.1, 73.52) * mm, "end": v(368.81, 71.69) * mm});
            skLineSegment(sketch, "E4136", {"start": v(368.81, 71.69) * mm, "end": v(366.94, 70.43) * mm});
            skLineSegment(sketch, "E4137", {"start": v(366.94, 70.43) * mm, "end": v(366.3, 70.04) * mm});
            skLineSegment(sketch, "E4138", {"start": v(366.3, 70.04) * mm, "end": v(366.24, 70) * mm});
            skLineSegment(sketch, "E4139", {"start": v(366.24, 70) * mm, "end": v(366.19, 69.96) * mm});
            skLineSegment(sketch, "E4140", {"start": v(366.19, 69.96) * mm, "end": v(363.01, 67.4) * mm});
            skLineSegment(sketch, "E4141", {"start": v(363.01, 67.4) * mm, "end": v(353.64, 59.51) * mm});
            skLineSegment(sketch, "E4142", {"start": v(353.64, 59.51) * mm, "end": v(341.29, 48.83) * mm});
            skLineSegment(sketch, "E4143", {"start": v(341.29, 48.83) * mm, "end": v(329, 38.07) * mm});
            skLineSegment(sketch, "E4144", {"start": v(329, 38.07) * mm, "end": v(319.74, 30.05) * mm});
            skLineSegment(sketch, "E4145", {"start": v(319.74, 30.05) * mm, "end": v(316.63, 27.41) * mm});
            skLineSegment(sketch, "E4146", {"start": v(316.63, 27.41) * mm, "end": v(316.15, 27.12) * mm});
            skLineSegment(sketch, "E4147", {"start": v(316.15, 27.12) * mm, "end": v(314.67, 26.3) * mm});
            skLineSegment(sketch, "E4148", {"start": v(314.67, 26.3) * mm, "end": v(312.87, 25.16) * mm});
            skLineSegment(sketch, "E4149", {"start": v(312.87, 25.16) * mm, "end": v(311.4, 23.68) * mm});
            skLineSegment(sketch, "E4150", {"start": v(311.4, 23.68) * mm, "end": v(310.6, 22.12) * mm});
            skLineSegment(sketch, "E4151", {"start": v(310.6, 22.12) * mm, "end": v(310.46, 21.57) * mm});
            skLineSegment(sketch, "E4152", {"start": v(310.46, 21.57) * mm, "end": v(310.26, 20.8) * mm});
            skLineSegment(sketch, "E4153", {"start": v(310.26, 20.8) * mm, "end": v(310.94, 20.39) * mm});
            skLineSegment(sketch, "E4154", {"start": v(310.94, 20.39) * mm, "end": v(311.1, 20.3) * mm});
            skLineSegment(sketch, "E4155", {"start": v(311.1, 20.3) * mm, "end": v(312.56, 19.23) * mm});
            skLineSegment(sketch, "E4156", {"start": v(312.56, 19.23) * mm, "end": v(312.71, 19.12) * mm});
            skLineSegment(sketch, "E4157", {"start": v(312.71, 19.12) * mm, "end": v(313, 18.93) * mm});
            skLineSegment(sketch, "E4158", {"start": v(313, 18.93) * mm, "end": v(313.37, 18.94) * mm});
            skLineSegment(sketch, "E4159", {"start": v(313.37, 18.94) * mm, "end": v(313.6, 18.95) * mm});
            skLineSegment(sketch, "E4160", {"start": v(313.6, 18.95) * mm, "end": v(315.96, 19.06) * mm});
            skLineSegment(sketch, "E4161", {"start": v(315.96, 19.06) * mm, "end": v(316.2, 19.07) * mm});
            skLineSegment(sketch, "E4162", {"start": v(316.2, 19.07) * mm, "end": v(316.56, 19.07) * mm});
            skLineSegment(sketch, "E4163", {"start": v(316.56, 19.07) * mm, "end": v(316.84, 19.32) * mm});
            skLineSegment(sketch, "E4164", {"start": v(316.84, 19.32) * mm, "end": v(317.18, 19.59) * mm});
            skLineSegment(sketch, "E4165", {"start": v(317.18, 19.59) * mm, "end": v(318.1, 20.5) * mm});
            skLineSegment(sketch, "E4166", {"start": v(318.1, 20.5) * mm, "end": v(319.26, 21.8) * mm});
            skLineSegment(sketch, "E4167", {"start": v(319.26, 21.8) * mm, "end": v(320.4, 23.1) * mm});
            skLineSegment(sketch, "E4168", {"start": v(320.4, 23.1) * mm, "end": v(321.32, 24.04) * mm});
            skLineSegment(sketch, "E4169", {"start": v(321.32, 24.04) * mm, "end": v(321.64, 24.33) * mm});
            skLineSegment(sketch, "E4170", {"start": v(321.64, 24.33) * mm, "end": v(322.74, 25.26) * mm});
            skLineSegment(sketch, "E4171", {"start": v(322.74, 25.26) * mm, "end": v(333.68, 34.63) * mm});
            skLineSegment(sketch, "E4172", {"start": v(333.68, 34.63) * mm, "end": v(334.75, 35.6) * mm});
            skLineSegment(sketch, "E4173", {"start": v(334.75, 35.6) * mm, "end": v(335.1, 35.92) * mm});
            skLineSegment(sketch, "E4174", {"start": v(335.1, 35.92) * mm, "end": v(336.12, 36.93) * mm});
            skLineSegment(sketch, "E4175", {"start": v(336.12, 36.93) * mm, "end": v(337.74, 38.53) * mm});
            skLineSegment(sketch, "E4176", {"start": v(337.74, 38.53) * mm, "end": v(339.4, 40.03) * mm});
            skLineSegment(sketch, "E4177", {"start": v(339.4, 40.03) * mm, "end": v(340.48, 40.85) * mm});
            skLineSegment(sketch, "E4178", {"start": v(340.48, 40.85) * mm, "end": v(340.87, 41.05) * mm});
            skLineSegment(sketch, "E4179", {"start": v(340.87, 41.05) * mm, "end": v(341.1, 41.17) * mm});
            skLineSegment(sketch, "E4180", {"start": v(341.1, 41.17) * mm, "end": v(341.85, 41.4) * mm});
            skLineSegment(sketch, "E4181", {"start": v(341.85, 41.4) * mm, "end": v(342.9, 41.59) * mm});
            skLineSegment(sketch, "E4182", {"start": v(342.9, 41.59) * mm, "end": v(343.96, 41.78) * mm});
            skLineSegment(sketch, "E4183", {"start": v(343.96, 41.78) * mm, "end": v(344.7, 42.02) * mm});
            skLineSegment(sketch, "E4184", {"start": v(344.7, 42.02) * mm, "end": v(344.92, 42.14) * mm});
            skLineSegment(sketch, "E4185", {"start": v(344.92, 42.14) * mm, "end": v(345.19, 42.3) * mm});
            skLineSegment(sketch, "E4186", {"start": v(345.19, 42.3) * mm, "end": v(345.93, 42.88) * mm});
            skLineSegment(sketch, "E4187", {"start": v(345.93, 42.88) * mm, "end": v(346.67, 43.71) * mm});
            skLineSegment(sketch, "E4188", {"start": v(346.67, 43.71) * mm, "end": v(347.33, 44.58) * mm});
            skLineSegment(sketch, "E4189", {"start": v(347.33, 44.58) * mm, "end": v(347.9, 45.25) * mm});
            skLineSegment(sketch, "E4190", {"start": v(347.9, 45.25) * mm, "end": v(348.12, 45.44) * mm});
            skLineSegment(sketch, "E4191", {"start": v(348.12, 45.44) * mm, "end": v(348.97, 46.23) * mm});
            skLineSegment(sketch, "E4192", {"start": v(348.97, 46.23) * mm, "end": v(353.91, 49.84) * mm});
            skLineSegment(sketch, "E4193", {"start": v(353.91, 49.84) * mm, "end": v(359.1, 53.15) * mm});
            skLineSegment(sketch, "E4194", {"start": v(359.1, 53.15) * mm, "end": v(360.07, 53.8) * mm});
            skLineSegment(sketch, "E4195", {"start": v(360.07, 53.8) * mm, "end": v(360.58, 54.14) * mm});
            skLineSegment(sketch, "E4196", {"start": v(360.58, 54.14) * mm, "end": v(363.3, 55.62) * mm});
            skLineSegment(sketch, "E4197", {"start": v(363.3, 55.62) * mm, "end": v(366.11, 56.98) * mm});
            skLineSegment(sketch, "E4198", {"start": v(366.11, 56.98) * mm, "end": v(366.66, 57.26) * mm});
            skLineSegment(sketch, "E4199", {"start": v(366.66, 57.26) * mm, "end": v(367.46, 57.66) * mm});
            skLineSegment(sketch, "E4200", {"start": v(367.46, 57.66) * mm, "end": v(369.75, 59.06) * mm});
            skLineSegment(sketch, "E4201", {"start": v(369.75, 59.06) * mm, "end": v(372.76, 60.8) * mm});
            skLineSegment(sketch, "E4202", {"start": v(372.76, 60.8) * mm, "end": v(375.93, 61.76) * mm});
            skLineSegment(sketch, "E4203", {"start": v(375.93, 61.76) * mm, "end": v(378.65, 61.57) * mm});
            skLineSegment(sketch, "E4204", {"start": v(378.65, 61.57) * mm, "end": v(379.46, 61.25) * mm});
            skLineSegment(sketch, "E4205", {"start": v(379.46, 61.25) * mm, "end": v(379.64, 60.8) * mm});
            skLineSegment(sketch, "E4206", {"start": v(379.64, 60.8) * mm, "end": v(379.98, 59.39) * mm});
            skLineSegment(sketch, "E4207", {"start": v(379.98, 59.39) * mm, "end": v(379.98, 57.74) * mm});
            skLineSegment(sketch, "E4208", {"start": v(379.98, 57.74) * mm, "end": v(379.57, 56.24) * mm});
            skLineSegment(sketch, "E4209", {"start": v(379.57, 56.24) * mm, "end": v(378.84, 54.86) * mm});
            skLineSegment(sketch, "E4210", {"start": v(378.84, 54.86) * mm, "end": v(377.9, 53.54) * mm});
            skLineSegment(sketch, "E4211", {"start": v(377.9, 53.54) * mm, "end": v(376.84, 52.23) * mm});
            skLineSegment(sketch, "E4212", {"start": v(376.84, 52.23) * mm, "end": v(375.76, 50.89) * mm});
            skLineSegment(sketch, "E4213", {"start": v(375.76, 50.89) * mm, "end": v(375, 49.83) * mm});
            skLineSegment(sketch, "E4214", {"start": v(375, 49.83) * mm, "end": v(374.78, 49.46) * mm});
            skLineSegment(sketch, "E4215", {"start": v(374.78, 49.46) * mm, "end": v(373.35, 48.46) * mm});
            skLineSegment(sketch, "E4216", {"start": v(373.35, 48.46) * mm, "end": v(369.23, 45.23) * mm});
            skLineSegment(sketch, "E4217", {"start": v(369.23, 45.23) * mm, "end": v(363.96, 40.68) * mm});
            skLineSegment(sketch, "E4218", {"start": v(363.96, 40.68) * mm, "end": v(358.83, 35.95) * mm});
            skLineSegment(sketch, "E4219", {"start": v(358.83, 35.95) * mm, "end": v(355.01, 32.38) * mm});
            skLineSegment(sketch, "E4220", {"start": v(355.01, 32.38) * mm, "end": v(353.72, 31.2) * mm});
            skLineSegment(sketch, "E4221", {"start": v(353.72, 31.2) * mm, "end": v(352.88, 30.43) * mm});
            skLineSegment(sketch, "E4222", {"start": v(352.88, 30.43) * mm, "end": v(348.44, 26.76) * mm});
            skLineSegment(sketch, "E4223", {"start": v(348.44, 26.76) * mm, "end": v(343.92, 23.16) * mm});
            skLineSegment(sketch, "E4224", {"start": v(343.92, 23.16) * mm, "end": v(343.04, 22.42) * mm});
            skLineSegment(sketch, "E4225", {"start": v(343.04, 22.42) * mm, "end": v(342.66, 22.1) * mm});
            skLineSegment(sketch, "E4226", {"start": v(342.66, 22.1) * mm, "end": v(338.71, 19) * mm});
            skLineSegment(sketch, "E4227", {"start": v(338.71, 19) * mm, "end": v(338.32, 18.67) * mm});
            skLineSegment(sketch, "E4228", {"start": v(338.32, 18.67) * mm, "end": v(336.89, 17.5) * mm});
            skLineSegment(sketch, "E4229", {"start": v(336.89, 17.5) * mm, "end": v(338.62, 16.84) * mm});
            skLineSegment(sketch, "E4230", {"start": v(338.62, 16.84) * mm, "end": v(338.91, 16.74) * mm});
            skLineSegment(sketch, "E4231", {"start": v(338.91, 16.74) * mm, "end": v(341.77, 15.53) * mm});
            skLineSegment(sketch, "E4232", {"start": v(341.77, 15.53) * mm, "end": v(342.05, 15.4) * mm});
            skLineSegment(sketch, "E4233", {"start": v(342.05, 15.4) * mm, "end": v(342.26, 15.3) * mm});
            skLineSegment(sketch, "E4234", {"start": v(342.26, 15.3) * mm, "end": v(343.21, 15.3) * mm});
            skLineSegment(sketch, "E4235", {"start": v(343.21, 15.3) * mm, "end": v(343.51, 15.54) * mm});
            skLineSegment(sketch, "E4236", {"start": v(343.51, 15.54) * mm, "end": v(345.87, 17.4) * mm});
            skLineSegment(sketch, "E4237", {"start": v(345.87, 17.4) * mm, "end": v(352.8, 23.17) * mm});
            skLineSegment(sketch, "E4238", {"start": v(352.8, 23.17) * mm, "end": v(362, 30.81) * mm});
            skLineSegment(sketch, "E4239", {"start": v(362, 30.81) * mm, "end": v(371.56, 37.97) * mm});
            skLineSegment(sketch, "E4240", {"start": v(371.56, 37.97) * mm, "end": v(379.23, 42.8) * mm});
            skLineSegment(sketch, "E4241", {"start": v(379.23, 42.8) * mm, "end": v(381.9, 44.16) * mm});
            skLineSegment(sketch, "E4242", {"start": v(381.9, 44.16) * mm, "end": v(382.44, 44.2) * mm});
            skLineSegment(sketch, "E4243", {"start": v(382.44, 44.2) * mm, "end": v(384.06, 44.27) * mm});
            skLineSegment(sketch, "E4244", {"start": v(384.06, 44.27) * mm, "end": v(386.7, 44.14) * mm});
            skLineSegment(sketch, "E4245", {"start": v(386.7, 44.14) * mm, "end": v(389.13, 43.56) * mm});
            skLineSegment(sketch, "E4246", {"start": v(389.13, 43.56) * mm, "end": v(390.5, 42.7) * mm});
            skLineSegment(sketch, "E4247", {"start": v(390.5, 42.7) * mm, "end": v(390.72, 42.3) * mm});
            skLineSegment(sketch, "E4248", {"start": v(390.72, 42.3) * mm, "end": v(390.87, 42.04) * mm});
            skLineSegment(sketch, "E4249", {"start": v(390.87, 42.04) * mm, "end": v(391, 41.06) * mm});
            skLineSegment(sketch, "E4250", {"start": v(391, 41.06) * mm, "end": v(390.7, 39.7) * mm});
            skLineSegment(sketch, "E4251", {"start": v(390.7, 39.7) * mm, "end": v(390.08, 38.4) * mm});
            skLineSegment(sketch, "E4252", {"start": v(390.08, 38.4) * mm, "end": v(389.59, 37.58) * mm});
            skLineSegment(sketch, "E4253", {"start": v(389.59, 37.58) * mm, "end": v(389.41, 37.32) * mm});
            skLineSegment(sketch, "E4254", {"start": v(389.41, 37.32) * mm, "end": v(389.27, 37.1) * mm});
            skLineSegment(sketch, "E4255", {"start": v(389.27, 37.1) * mm, "end": v(388.75, 36.5) * mm});
            skLineSegment(sketch, "E4256", {"start": v(388.75, 36.5) * mm, "end": v(387.89, 35.6) * mm});
            skLineSegment(sketch, "E4257", {"start": v(387.89, 35.6) * mm, "end": v(386.98, 34.74) * mm});
            skLineSegment(sketch, "E4258", {"start": v(386.98, 34.74) * mm, "end": v(386.4, 34.17) * mm});
            skLineSegment(sketch, "E4259", {"start": v(386.4, 34.17) * mm, "end": v(386.2, 33.98) * mm});
            skLineSegment(sketch, "E4260", {"start": v(386.2, 33.98) * mm, "end": v(385.63, 33.38) * mm});
            skLineSegment(sketch, "E4261", {"start": v(385.63, 33.38) * mm, "end": v(382.57, 30.6) * mm});
            skLineSegment(sketch, "E4262", {"start": v(382.57, 30.6) * mm, "end": v(379.46, 27.88) * mm});
            skLineSegment(sketch, "E4263", {"start": v(379.46, 27.88) * mm, "end": v(378.87, 27.3) * mm});
            skLineSegment(sketch, "E4264", {"start": v(378.87, 27.3) * mm, "end": v(378.31, 26.78) * mm});
            skLineSegment(sketch, "E4265", {"start": v(378.31, 26.78) * mm, "end": v(375.65, 24.42) * mm});
            skLineSegment(sketch, "E4266", {"start": v(375.65, 24.42) * mm, "end": v(372.88, 22.21) * mm});
            skLineSegment(sketch, "E4267", {"start": v(372.88, 22.21) * mm, "end": v(372.27, 21.75) * mm});
            skLineSegment(sketch, "E4268", {"start": v(372.27, 21.75) * mm, "end": v(371.62, 21.28) * mm});
            skLineSegment(sketch, "E4269", {"start": v(371.62, 21.28) * mm, "end": v(368.69, 18.3) * mm});
            skLineSegment(sketch, "E4270", {"start": v(368.69, 18.3) * mm, "end": v(365.78, 15.2) * mm});
            skLineSegment(sketch, "E4271", {"start": v(365.78, 15.2) * mm, "end": v(365.16, 14.66) * mm});
            skLineSegment(sketch, "E4272", {"start": v(365.16, 14.66) * mm, "end": v(364.95, 14.49) * mm});
            skLineSegment(sketch, "E4273", {"start": v(364.95, 14.49) * mm, "end": v(362.72, 12.86) * mm});
            skLineSegment(sketch, "E4274", {"start": v(362.72, 12.86) * mm, "end": v(362.5, 12.7) * mm});
            skLineSegment(sketch, "E4275", {"start": v(362.5, 12.7) * mm, "end": v(361.34, 11.9) * mm});
            skLineSegment(sketch, "E4276", {"start": v(361.34, 11.9) * mm, "end": v(362.43, 11) * mm});
            skLineSegment(sketch, "E4277", {"start": v(362.43, 11) * mm, "end": v(362.61, 10.85) * mm});
            skLineSegment(sketch, "E4278", {"start": v(362.61, 10.85) * mm, "end": v(364.37, 9.16) * mm});
            skLineSegment(sketch, "E4279", {"start": v(364.37, 9.16) * mm, "end": v(364.52, 8.97) * mm});
            skLineSegment(sketch, "E4280", {"start": v(364.52, 8.97) * mm, "end": v(364.83, 8.62) * mm});
            skLineSegment(sketch, "E4281", {"start": v(364.83, 8.62) * mm, "end": v(365.3, 8.6) * mm});
            skLineSegment(sketch, "E4282", {"start": v(365.3, 8.6) * mm, "end": v(365.35, 8.6) * mm});
            skLineSegment(sketch, "E4283", {"start": v(365.35, 8.6) * mm, "end": v(365.98, 8.55) * mm});
            skLineSegment(sketch, "E4284", {"start": v(365.98, 8.55) * mm, "end": v(366.05, 8.55) * mm});
            skLineSegment(sketch, "E4285", {"start": v(366.05, 8.55) * mm, "end": v(366.55, 8.5) * mm});
            skLineSegment(sketch, "E4286", {"start": v(366.55, 8.5) * mm, "end": v(366.9, 8.86) * mm});
            skLineSegment(sketch, "E4287", {"start": v(366.9, 8.86) * mm, "end": v(366.95, 8.92) * mm});
            skLineSegment(sketch, "E4288", {"start": v(366.95, 8.92) * mm, "end": v(367.52, 9.48) * mm});
            skLineSegment(sketch, "E4289", {"start": v(367.52, 9.48) * mm, "end": v(367.58, 9.53) * mm});
            skLineSegment(sketch, "E4290", {"start": v(367.58, 9.53) * mm, "end": v(368.81, 10.67) * mm});
            skLineSegment(sketch, "E4291", {"start": v(368.81, 10.67) * mm, "end": v(372.48, 14.12) * mm});
            skLineSegment(sketch, "E4292", {"start": v(372.48, 14.12) * mm, "end": v(377.61, 18.7) * mm});
            skLineSegment(sketch, "E4293", {"start": v(377.61, 18.7) * mm, "end": v(383.09, 22.78) * mm});
            skLineSegment(sketch, "E4294", {"start": v(383.09, 22.78) * mm, "end": v(387.48, 25.27) * mm});
            skLineSegment(sketch, "E4295", {"start": v(387.48, 25.27) * mm, "end": v(389.03, 25.9) * mm});
            skLineSegment(sketch, "E4296", {"start": v(389.03, 25.9) * mm, "end": v(389.56, 26.1) * mm});
            skLineSegment(sketch, "E4297", {"start": v(389.56, 26.1) * mm, "end": v(391.23, 26.6) * mm});
            skLineSegment(sketch, "E4298", {"start": v(391.23, 26.6) * mm, "end": v(393.99, 27.11) * mm});
            skLineSegment(sketch, "E4299", {"start": v(393.99, 27.11) * mm, "end": v(396.7, 27.1) * mm});
            skLineSegment(sketch, "E4300", {"start": v(396.7, 27.1) * mm, "end": v(398.39, 26.6) * mm});
            skLineSegment(sketch, "E4301", {"start": v(398.39, 26.6) * mm, "end": v(398.78, 26.24) * mm});
            skLineSegment(sketch, "E4302", {"start": v(398.78, 26.24) * mm, "end": v(398.96, 26.08) * mm});
            skLineSegment(sketch, "E4303", {"start": v(398.96, 26.08) * mm, "end": v(399.48, 25.1) * mm});
            skLineSegment(sketch, "E4304", {"start": v(399.48, 25.1) * mm, "end": v(399.64, 23.98) * mm});
            skLineSegment(sketch, "E4305", {"start": v(399.64, 23.98) * mm, "end": v(399.63, 23.75) * mm});
            skLineSegment(sketch, "E4306", {"start": v(399.63, 23.75) * mm, "end": v(399.62, 23.4) * mm});
            skLineSegment(sketch, "E4307", {"start": v(399.62, 23.4) * mm, "end": v(399.27, 22.35) * mm});
            skLineSegment(sketch, "E4308", {"start": v(399.27, 22.35) * mm, "end": v(398.37, 20.86) * mm});
            skLineSegment(sketch, "E4309", {"start": v(398.37, 20.86) * mm, "end": v(397.06, 19.34) * mm});
            skLineSegment(sketch, "E4310", {"start": v(397.06, 19.34) * mm, "end": v(395.5, 17.83) * mm});
            skLineSegment(sketch, "E4311", {"start": v(395.5, 17.83) * mm, "end": v(393.82, 16.38) * mm});
            skLineSegment(sketch, "E4312", {"start": v(393.82, 16.38) * mm, "end": v(392.17, 15.04) * mm});
            skLineSegment(sketch, "E4313", {"start": v(392.17, 15.04) * mm, "end": v(390.7, 13.86) * mm});
            skLineSegment(sketch, "E4314", {"start": v(390.7, 13.86) * mm, "end": v(389.84, 13.14) * mm});
            skLineSegment(sketch, "E4315", {"start": v(389.84, 13.14) * mm, "end": v(389.57, 12.88) * mm});
            skLineSegment(sketch, "E4316", {"start": v(389.57, 12.88) * mm, "end": v(388.98, 12.32) * mm});
            skLineSegment(sketch, "E4317", {"start": v(388.98, 12.32) * mm, "end": v(383.06, 6.84) * mm});
            skLineSegment(sketch, "E4318", {"start": v(383.06, 6.84) * mm, "end": v(382.48, 6.28) * mm});
            skLineSegment(sketch, "E4319", {"start": v(382.48, 6.28) * mm, "end": v(381.48, 5.3) * mm});
            skLineSegment(sketch, "E4320", {"start": v(381.48, 5.3) * mm, "end": v(382.67, 4.59) * mm});
            skLineSegment(sketch, "E4321", {"start": v(382.67, 4.59) * mm, "end": v(382.94, 4.42) * mm});
            skLineSegment(sketch, "E4322", {"start": v(382.94, 4.42) * mm, "end": v(385.46, 2.49) * mm});
            skLineSegment(sketch, "E4323", {"start": v(385.46, 2.49) * mm, "end": v(385.7, 2.27) * mm});
            skLineSegment(sketch, "E4324", {"start": v(385.7, 2.27) * mm, "end": v(386.32, 1.74) * mm});
            skLineSegment(sketch, "E4325", {"start": v(386.32, 1.74) * mm, "end": v(387.02, 2.2) * mm});
            skLineSegment(sketch, "E4326", {"start": v(387.02, 2.2) * mm, "end": v(387.58, 2.59) * mm});
            skLineSegment(sketch, "E4327", {"start": v(387.58, 2.59) * mm, "end": v(393.34, 6.26) * mm});
            skLineSegment(sketch, "E4328", {"start": v(393.34, 6.26) * mm, "end": v(393.91, 6.63) * mm});
            skLineSegment(sketch, "E4329", {"start": v(393.91, 6.63) * mm, "end": v(394.21, 6.82) * mm});
            skLineSegment(sketch, "E4330", {"start": v(394.21, 6.82) * mm, "end": v(395.6, 7.95) * mm});
            skLineSegment(sketch, "E4331", {"start": v(395.6, 7.95) * mm, "end": v(396.86, 9.21) * mm});
            skLineSegment(sketch, "E4332", {"start": v(396.86, 9.21) * mm, "end": v(397.1, 9.47) * mm});
            skLineSegment(sketch, "E4333", {"start": v(397.1, 9.47) * mm, "end": v(397.34, 9.72) * mm});
            skLineSegment(sketch, "E4334", {"start": v(397.34, 9.72) * mm, "end": v(398.05, 10.49) * mm});
            skLineSegment(sketch, "E4335", {"start": v(398.05, 10.49) * mm, "end": v(399.17, 11.62) * mm});
            skLineSegment(sketch, "E4336", {"start": v(399.17, 11.62) * mm, "end": v(400.4, 12.6) * mm});
            skLineSegment(sketch, "E4337", {"start": v(400.4, 12.6) * mm, "end": v(401.3, 13.1) * mm});
            skLineSegment(sketch, "E4338", {"start": v(401.3, 13.1) * mm, "end": v(401.63, 13.17) * mm});
            skLineSegment(sketch, "E4339", {"start": v(401.63, 13.17) * mm, "end": v(401.87, 13.23) * mm});
            skLineSegment(sketch, "E4340", {"start": v(401.87, 13.23) * mm, "end": v(402.62, 13.3) * mm});
            skLineSegment(sketch, "E4341", {"start": v(402.62, 13.3) * mm, "end": v(403.73, 13.3) * mm});
            skLineSegment(sketch, "E4342", {"start": v(403.73, 13.3) * mm, "end": v(404.85, 13.2) * mm});
            skLineSegment(sketch, "E4343", {"start": v(404.85, 13.2) * mm, "end": v(405.6, 13.1) * mm});
            skLineSegment(sketch, "E4344", {"start": v(405.6, 13.1) * mm, "end": v(405.85, 13.06) * mm});
            skLineSegment(sketch, "E4345", {"start": v(405.85, 13.06) * mm, "end": v(406.06, 13.02) * mm});
            skLineSegment(sketch, "E4346", {"start": v(406.06, 13.02) * mm, "end": v(406.83, 12.84) * mm});
            skLineSegment(sketch, "E4347", {"start": v(406.83, 12.84) * mm, "end": v(408.19, 12.43) * mm});
            skLineSegment(sketch, "E4348", {"start": v(408.19, 12.43) * mm, "end": v(409.43, 11.85) * mm});
            skLineSegment(sketch, "E4349", {"start": v(409.43, 11.85) * mm, "end": v(410.02, 11.35) * mm});
            skLineSegment(sketch, "E4350", {"start": v(410.02, 11.35) * mm, "end": v(410.06, 11.15) * mm});
            skLineSegment(sketch, "E4351", {"start": v(410.06, 11.15) * mm, "end": v(410.11, 10.9) * mm});
            skLineSegment(sketch, "E4352", {"start": v(410.11, 10.9) * mm, "end": v(410.02, 10.08) * mm});
            skLineSegment(sketch, "E4353", {"start": v(410.02, 10.08) * mm, "end": v(409.52, 9.01) * mm});
            skLineSegment(sketch, "E4354", {"start": v(409.52, 9.01) * mm, "end": v(408.68, 7.96) * mm});
            skLineSegment(sketch, "E4355", {"start": v(408.68, 7.96) * mm, "end": v(407.62, 6.96) * mm});
            skLineSegment(sketch, "E4356", {"start": v(407.62, 6.96) * mm, "end": v(406.43, 6) * mm});
            skLineSegment(sketch, "E4357", {"start": v(406.43, 6) * mm, "end": v(405.26, 5.15) * mm});
            skLineSegment(sketch, "E4358", {"start": v(405.26, 5.15) * mm, "end": v(404.2, 4.38) * mm});
            skLineSegment(sketch, "E4359", {"start": v(404.2, 4.38) * mm, "end": v(403.58, 3.91) * mm});
            skLineSegment(sketch, "E4360", {"start": v(403.58, 3.91) * mm, "end": v(403.38, 3.74) * mm});
            skLineSegment(sketch, "E4361", {"start": v(403.38, 3.74) * mm, "end": v(403.07, 3.48) * mm});
            skLineSegment(sketch, "E4362", {"start": v(403.07, 3.48) * mm, "end": v(399.86, 0.98) * mm});
            skLineSegment(sketch, "E4363", {"start": v(399.86, 0.98) * mm, "end": v(399.54, 0.73) * mm});
            skLineSegment(sketch, "E4364", {"start": v(399.54, 0.73) * mm, "end": v(397.24, -1.1) * mm});
            skLineSegment(sketch, "E4365", {"start": v(397.24, -1.1) * mm, "end": v(400.16, -1.18) * mm});
            skLineSegment(sketch, "E4366", {"start": v(400.16, -1.18) * mm, "end": v(400.62, -1.19) * mm});
            skLineSegment(sketch, "E4367", {"start": v(400.62, -1.19) * mm, "end": v(402.86, -1.42) * mm});
            skLineSegment(sketch, "E4368", {"start": v(402.86, -1.42) * mm, "end": v(405.06, -1.82) * mm});
            skLineSegment(sketch, "E4369", {"start": v(405.06, -1.82) * mm, "end": v(405.5, -1.92) * mm});
            skLineSegment(sketch, "E4370", {"start": v(405.5, -1.92) * mm, "end": v(405.9, -2) * mm});
            skLineSegment(sketch, "E4371", {"start": v(405.9, -2) * mm, "end": v(406.24, -1.82) * mm});
            skLineSegment(sketch, "E4372", {"start": v(406.24, -1.82) * mm, "end": v(406.52, -1.67) * mm});
            skLineSegment(sketch, "E4373", {"start": v(406.52, -1.67) * mm, "end": v(407.38, -1.25) * mm});
            skLineSegment(sketch, "E4374", {"start": v(407.38, -1.25) * mm, "end": v(408.6, -0.74) * mm});
            skLineSegment(sketch, "E4375", {"start": v(408.6, -0.74) * mm, "end": v(409.87, -0.38) * mm});
            skLineSegment(sketch, "E4376", {"start": v(409.87, -0.38) * mm, "end": v(410.81, -0.24) * mm});
            skLineSegment(sketch, "E4377", {"start": v(410.81, -0.24) * mm, "end": v(411.12, -0.23) * mm});
            skLineSegment(sketch, "E4378", {"start": v(411.12, -0.23) * mm, "end": v(411.44, -0.23) * mm});
            skLineSegment(sketch, "E4379", {"start": v(411.44, -0.23) * mm, "end": v(412.4, -0.36) * mm});
            skLineSegment(sketch, "E4380", {"start": v(412.4, -0.36) * mm, "end": v(413.72, -0.68) * mm});
            skLineSegment(sketch, "E4381", {"start": v(413.72, -0.68) * mm, "end": v(415.05, -1.13) * mm});
            skLineSegment(sketch, "E4382", {"start": v(415.05, -1.13) * mm, "end": v(416, -1.5) * mm});
            skLineSegment(sketch, "E4383", {"start": v(416, -1.5) * mm, "end": v(416.3, -1.63) * mm});
            skLineSegment(sketch, "E4384", {"start": v(416.3, -1.63) * mm, "end": v(416.3, -2.02) * mm});
            skLineSegment(sketch, "E4385", {"start": v(416.3, -2.02) * mm, "end": v(416.54, -3.18) * mm});
            skLineSegment(sketch, "E4386", {"start": v(416.54, -3.18) * mm, "end": v(417.07, -4.58) * mm});
            skLineSegment(sketch, "E4387", {"start": v(417.07, -4.58) * mm, "end": v(417.57, -5.88) * mm});
            skLineSegment(sketch, "E4388", {"start": v(417.57, -5.88) * mm, "end": v(417.75, -6.84) * mm});
            skLineSegment(sketch, "E4389", {"start": v(417.75, -6.84) * mm, "end": v(417.72, -7.15) * mm});
            skLineSegment(sketch, "E4390", {"start": v(417.72, -7.15) * mm, "end": v(417.72, -7.18) * mm});
            skLineSegment(sketch, "E4391", {"start": v(417.72, -7.18) * mm, "end": v(417.72, -7.2) * mm});
            skLineSegment(sketch, "E4392", {"start": v(417.72, -7.2) * mm, "end": v(417.7, -7.24) * mm});
            skLineSegment(sketch, "E4393", {"start": v(417.7, -7.24) * mm, "end": v(417.55, -7.6) * mm});
            skLineSegment(sketch, "E4394", {"start": v(417.55, -7.6) * mm, "end": v(417.35, -7.98) * mm});
            skLineSegment(sketch, "E4395", {"start": v(417.35, -7.98) * mm, "end": v(417.33, -8.02) * mm});
            skLineSegment(sketch, "E4396", {"start": v(417.33, -8.02) * mm, "end": v(417.05, -8.6) * mm});
            skLineSegment(sketch, "E4397", {"start": v(417.05, -8.6) * mm, "end": v(417.46, -9.12) * mm});
            skLineSegment(sketch, "E4398", {"start": v(417.46, -9.12) * mm, "end": v(417.58, -9.29) * mm});
            skLineSegment(sketch, "E4399", {"start": v(417.58, -9.29) * mm, "end": v(418.78, -11.03) * mm});
            skLineSegment(sketch, "E4400", {"start": v(418.78, -11.03) * mm, "end": v(418.88, -11.21) * mm});
            skLineSegment(sketch, "E4401", {"start": v(418.88, -11.21) * mm, "end": v(419.16, -11.7) * mm});
            skLineSegment(sketch, "E4402", {"start": v(419.16, -11.7) * mm, "end": v(419.72, -11.74) * mm});
            skLineSegment(sketch, "E4403", {"start": v(419.72, -11.74) * mm, "end": v(420.75, -11.83) * mm});
            skLineSegment(sketch, "E4404", {"start": v(420.75, -11.83) * mm, "end": v(423.81, -12.47) * mm});
            skLineSegment(sketch, "E4405", {"start": v(423.81, -12.47) * mm, "end": v(427.54, -14.02) * mm});
            skLineSegment(sketch, "E4406", {"start": v(427.54, -14.02) * mm, "end": v(430.71, -16.45) * mm});
            skLineSegment(sketch, "E4407", {"start": v(430.71, -16.45) * mm, "end": v(432.68, -18.9) * mm});
            skLineSegment(sketch, "E4408", {"start": v(432.68, -18.9) * mm, "end": v(433.16, -19.8) * mm});
            skLineSegment(sketch, "E4409", {"start": v(433.16, -19.8) * mm, "end": v(433.35, -20.2) * mm});
            skLineSegment(sketch, "E4410", {"start": v(433.35, -20.2) * mm, "end": v(433.76, -20.32) * mm});
            skLineSegment(sketch, "E4411", {"start": v(433.76, -20.32) * mm, "end": v(434.95, -20.73) * mm});
            skLineSegment(sketch, "E4412", {"start": v(434.95, -20.73) * mm, "end": v(438.46, -22.2) * mm});
            skLineSegment(sketch, "E4413", {"start": v(438.46, -22.2) * mm, "end": v(443.01, -24.69) * mm});
            skLineSegment(sketch, "E4414", {"start": v(443.01, -24.69) * mm, "end": v(447.02, -27.9) * mm});
            skLineSegment(sketch, "E4415", {"start": v(447.02, -27.9) * mm, "end": v(449.5, -30.82) * mm});
            skLineSegment(sketch, "E4416", {"start": v(449.5, -30.82) * mm, "end": v(450.1, -31.91) * mm});
            skLineSegment(sketch, "E4417", {"start": v(450.1, -31.91) * mm, "end": v(450.37, -32.38) * mm});
            skLineSegment(sketch, "E4418", {"start": v(450.37, -32.38) * mm, "end": v(450.92, -32.45) * mm});
            skLineSegment(sketch, "E4419", {"start": v(450.92, -32.45) * mm, "end": v(451.26, -32.5) * mm});
            skLineSegment(sketch, "E4420", {"start": v(451.26, -32.5) * mm, "end": v(454.72, -32.93) * mm});
            skLineSegment(sketch, "E4421", {"start": v(454.72, -32.93) * mm, "end": v(455.07, -32.97) * mm});
            skLineSegment(sketch, "E4422", {"start": v(455.07, -32.97) * mm, "end": v(456.3, -33.4) * mm});
            skLineSegment(sketch, "E4423", {"start": v(456.3, -33.4) * mm, "end": v(456.69, -33.24) * mm});
            skLineSegment(sketch, "E4424", {"start": v(456.69, -33.24) * mm, "end": v(456.73, -33.22) * mm});
            skLineSegment(sketch, "E4425", {"start": v(456.73, -33.22) * mm, "end": v(457.25, -32.97) * mm});
            skLineSegment(sketch, "E4426", {"start": v(457.25, -32.97) * mm, "end": v(457.3, -32.95) * mm});
            skLineSegment(sketch, "E4427", {"start": v(457.3, -32.95) * mm, "end": v(457.95, -32.75) * mm});
            skLineSegment(sketch, "E4428", {"start": v(457.95, -32.75) * mm, "end": v(459.95, -32.3) * mm});
            skLineSegment(sketch, "E4429", {"start": v(459.95, -32.3) * mm, "end": v(463, -31.88) * mm});
            skLineSegment(sketch, "E4430", {"start": v(463, -31.88) * mm, "end": v(466.08, -31.82) * mm});
            skLineSegment(sketch, "E4431", {"start": v(466.08, -31.82) * mm, "end": v(468.2, -32.08) * mm});
            skLineSegment(sketch, "E4432", {"start": v(468.2, -32.08) * mm, "end": v(468.89, -32.27) * mm});
            skLineSegment(sketch, "E4433", {"start": v(468.89, -32.27) * mm, "end": v(468.78, -32.75) * mm});
            skLineSegment(sketch, "E4434", {"start": v(468.78, -32.75) * mm, "end": v(467.83, -35.01) * mm});
            skLineSegment(sketch, "E4435", {"start": v(467.83, -35.01) * mm, "end": v(466.5, -37.09) * mm});
            skLineSegment(sketch, "E4436", {"start": v(466.5, -37.09) * mm, "end": v(466.2, -37.47) * mm});
            skLineSegment(sketch, "E4437", {"start": v(466.2, -37.47) * mm, "end": v(465.57, -38.3) * mm});
            skLineSegment(sketch, "E4438", {"start": v(465.57, -38.3) * mm, "end": v(466.37, -38.95) * mm});
            skLineSegment(sketch, "E4439", {"start": v(466.37, -38.95) * mm, "end": v(466.57, -39.12) * mm});
            skLineSegment(sketch, "E4440", {"start": v(466.57, -39.12) * mm, "end": v(468.5, -40.86) * mm});
            skLineSegment(sketch, "E4441", {"start": v(468.5, -40.86) * mm, "end": v(468.68, -41.05) * mm});
            skLineSegment(sketch, "E4442", {"start": v(468.68, -41.05) * mm, "end": v(468.87, -41.24) * mm});
            skLineSegment(sketch, "E4443", {"start": v(468.87, -41.24) * mm, "end": v(469.13, -41.32) * mm});
            skLineSegment(sketch, "E4444", {"start": v(469.13, -41.32) * mm, "end": v(469.29, -41.37) * mm});
            skLineSegment(sketch, "E4445", {"start": v(469.29, -41.37) * mm, "end": v(470.88, -41.9) * mm});
            skLineSegment(sketch, "E4446", {"start": v(470.88, -41.9) * mm, "end": v(471.04, -41.96) * mm});
            skLineSegment(sketch, "E4447", {"start": v(471.04, -41.96) * mm, "end": v(471.55, -42.14) * mm});
            skLineSegment(sketch, "E4448", {"start": v(471.55, -42.14) * mm, "end": v(472, -41.84) * mm});
            skLineSegment(sketch, "E4449", {"start": v(472, -41.84) * mm, "end": v(472.83, -41.28) * mm});
            skLineSegment(sketch, "E4450", {"start": v(472.83, -41.28) * mm, "end": v(477.14, -38.85) * mm});
            skLineSegment(sketch, "E4451", {"start": v(477.14, -38.85) * mm, "end": v(481.75, -37.07) * mm});
            skLineSegment(sketch, "E4452", {"start": v(481.75, -37.07) * mm, "end": v(482.73, -36.83) * mm});
            skLineSegment(sketch, "E4453", {"start": v(482.73, -36.83) * mm, "end": v(483.28, -36.7) * mm});
            skLineSegment(sketch, "E4454", {"start": v(483.28, -36.7) * mm, "end": v(489.02, -35.75) * mm});
            skLineSegment(sketch, "E4455", {"start": v(489.02, -35.75) * mm, "end": v(489.6, -35.7) * mm});
            skLineSegment(sketch, "E4456", {"start": v(489.6, -35.7) * mm, "end": v(489.81, -35.67) * mm});
            skLineSegment(sketch, "E4457", {"start": v(489.81, -35.67) * mm, "end": v(491.01, -35.6) * mm});
            skLineSegment(sketch, "E4458", {"start": v(491.01, -35.6) * mm, "end": v(493.28, -35.55) * mm});
            skLineSegment(sketch, "E4459", {"start": v(493.28, -35.55) * mm, "end": v(495.45, -35.76) * mm});
            skLineSegment(sketch, "E4460", {"start": v(495.45, -35.76) * mm, "end": v(496.48, -36.18) * mm});
            skLineSegment(sketch, "E4461", {"start": v(496.48, -36.18) * mm, "end": v(496.54, -36.4) * mm});
            skLineSegment(sketch, "E4462", {"start": v(496.54, -36.4) * mm, "end": v(496.6, -36.67) * mm});
            skLineSegment(sketch, "E4463", {"start": v(496.6, -36.67) * mm, "end": v(496.15, -37.77) * mm});
            skLineSegment(sketch, "E4464", {"start": v(496.15, -37.77) * mm, "end": v(495.04, -39.8) * mm});
            skLineSegment(sketch, "E4465", {"start": v(495.04, -39.8) * mm, "end": v(493.75, -41.8) * mm});
            skLineSegment(sketch, "E4466", {"start": v(493.75, -41.8) * mm, "end": v(493.03, -42.85) * mm});
            skLineSegment(sketch, "E4467", {"start": v(493.03, -42.85) * mm, "end": v(492.86, -43.1) * mm});
            skLineSegment(sketch, "E4468", {"start": v(492.86, -43.1) * mm, "end": v(492.5, -43.58) * mm});
            skLineSegment(sketch, "E4469", {"start": v(492.5, -43.58) * mm, "end": v(488.75, -48.35) * mm});
            skLineSegment(sketch, "E4470", {"start": v(488.75, -48.35) * mm, "end": v(488.36, -48.8) * mm});
            skLineSegment(sketch, "E4471", {"start": v(488.36, -48.8) * mm, "end": v(488.1, -49.13) * mm});
            skLineSegment(sketch, "E4472", {"start": v(488.1, -49.13) * mm, "end": v(485.23, -52.23) * mm});
            skLineSegment(sketch, "E4473", {"start": v(485.23, -52.23) * mm, "end": v(484.94, -52.54) * mm});
            skLineSegment(sketch, "E4474", {"start": v(484.94, -52.54) * mm, "end": v(484.47, -53.04) * mm});
            skLineSegment(sketch, "E4475", {"start": v(484.47, -53.04) * mm, "end": v(484.73, -53.68) * mm});
            skLineSegment(sketch, "E4476", {"start": v(484.73, -53.68) * mm, "end": v(484.78, -53.8) * mm});
            skLineSegment(sketch, "E4477", {"start": v(484.78, -53.8) * mm, "end": v(485.32, -55.1) * mm});
            skLineSegment(sketch, "E4478", {"start": v(485.32, -55.1) * mm, "end": v(485.36, -55.23) * mm});
            skLineSegment(sketch, "E4479", {"start": v(485.36, -55.23) * mm, "end": v(485.41, -55.42) * mm});
            skLineSegment(sketch, "E4480", {"start": v(485.41, -55.42) * mm, "end": v(485.57, -56.42) * mm});
            skLineSegment(sketch, "E4481", {"start": v(485.57, -56.42) * mm, "end": v(485.68, -57.44) * mm});
            skLineSegment(sketch, "E4482", {"start": v(485.68, -57.44) * mm, "end": v(485.72, -57.64) * mm});
            skLineSegment(sketch, "E4483", {"start": v(485.72, -57.64) * mm, "end": v(486.06, -59.79) * mm});
            skLineSegment(sketch, "E4484", {"start": v(486.06, -59.79) * mm, "end": v(487.55, -58.2) * mm});
            skLineSegment(sketch, "E4485", {"start": v(487.55, -58.2) * mm, "end": v(488.24, -57.45) * mm});
            skLineSegment(sketch, "E4486", {"start": v(488.24, -57.45) * mm, "end": v(491.76, -53.78) * mm});
            skLineSegment(sketch, "E4487", {"start": v(491.76, -53.78) * mm, "end": v(495.45, -50.28) * mm});
            skLineSegment(sketch, "E4488", {"start": v(495.45, -50.28) * mm, "end": v(496.22, -49.62) * mm});
            skLineSegment(sketch, "E4489", {"start": v(496.22, -49.62) * mm, "end": v(497.15, -48.85) * mm});
            skLineSegment(sketch, "E4490", {"start": v(497.15, -48.85) * mm, "end": v(500.14, -46.77) * mm});
            skLineSegment(sketch, "E4491", {"start": v(500.14, -46.77) * mm, "end": v(504.38, -44.3) * mm});
            skLineSegment(sketch, "E4492", {"start": v(504.38, -44.3) * mm, "end": v(508.78, -42.07) * mm});
            skLineSegment(sketch, "E4493", {"start": v(508.78, -42.07) * mm, "end": v(512.06, -40.47) * mm});
            skLineSegment(sketch, "E4494", {"start": v(512.06, -40.47) * mm, "end": v(513.15, -39.93) * mm});
            skLineSegment(sketch, "E4495", {"start": v(513.15, -39.93) * mm, "end": v(513.5, -39.75) * mm});
            skLineSegment(sketch, "E4496", {"start": v(513.5, -39.75) * mm, "end": v(514.5, -39.14) * mm});
            skLineSegment(sketch, "E4497", {"start": v(514.5, -39.14) * mm, "end": v(516.02, -38.2) * mm});
            skLineSegment(sketch, "E4498", {"start": v(516.02, -38.2) * mm, "end": v(517.54, -37.34) * mm});
            skLineSegment(sketch, "E4499", {"start": v(517.54, -37.34) * mm, "end": v(518.54, -36.91) * mm});
            skLineSegment(sketch, "E4500", {"start": v(518.54, -36.91) * mm, "end": v(518.9, -36.84) * mm});
            skLineSegment(sketch, "E4501", {"start": v(518.9, -36.84) * mm, "end": v(519.42, -36.74) * mm});
            skLineSegment(sketch, "E4502", {"start": v(519.42, -36.74) * mm, "end": v(521.03, -36.65) * mm});
            skLineSegment(sketch, "E4503", {"start": v(521.03, -36.65) * mm, "end": v(523.53, -36.87) * mm});
            skLineSegment(sketch, "E4504", {"start": v(523.53, -36.87) * mm, "end": v(525.78, -37.68) * mm});
            skLineSegment(sketch, "E4505", {"start": v(525.78, -37.68) * mm, "end": v(527.02, -38.8) * mm});
            skLineSegment(sketch, "E4506", {"start": v(527.02, -38.8) * mm, "end": v(527.2, -39.28) * mm});
            skLineSegment(sketch, "E4507", {"start": v(527.2, -39.28) * mm, "end": v(527.22, -39.32) * mm});
            skLineSegment(sketch, "E4508", {"start": v(527.22, -39.32) * mm, "end": v(527.34, -39.75) * mm});
            skLineSegment(sketch, "E4509", {"start": v(527.34, -39.75) * mm, "end": v(527.35, -39.8) * mm});
            skLineSegment(sketch, "E4510", {"start": v(527.35, -39.8) * mm, "end": v(527.38, -40.07) * mm});
            skLineSegment(sketch, "E4511", {"start": v(527.38, -40.07) * mm, "end": v(527.25, -40.93) * mm});
            skLineSegment(sketch, "E4512", {"start": v(527.25, -40.93) * mm, "end": v(526.8, -42.16) * mm});
            skLineSegment(sketch, "E4513", {"start": v(526.8, -42.16) * mm, "end": v(526.16, -43.32) * mm});
            skLineSegment(sketch, "E4514", {"start": v(526.16, -43.32) * mm, "end": v(525.69, -44.05) * mm});
            skLineSegment(sketch, "E4515", {"start": v(525.69, -44.05) * mm, "end": v(525.52, -44.28) * mm});
            skLineSegment(sketch, "E4516", {"start": v(525.52, -44.28) * mm, "end": v(525.05, -44.95) * mm});
            skLineSegment(sketch, "E4517", {"start": v(525.05, -44.95) * mm, "end": v(522.01, -48.04) * mm});
            skLineSegment(sketch, "E4518", {"start": v(522.01, -48.04) * mm, "end": v(518.78, -51.01) * mm});
            skLineSegment(sketch, "E4519", {"start": v(518.78, -51.01) * mm, "end": v(518.22, -51.64) * mm});
            skLineSegment(sketch, "E4520", {"start": v(518.22, -51.64) * mm, "end": v(517.02, -52.96) * mm});
            skLineSegment(sketch, "E4521", {"start": v(517.02, -52.96) * mm, "end": v(513.47, -57) * mm});
            skLineSegment(sketch, "E4522", {"start": v(513.47, -57) * mm, "end": v(508.7, -62.37) * mm});
            skLineSegment(sketch, "E4523", {"start": v(508.7, -62.37) * mm, "end": v(503.78, -67.6) * mm});
            skLineSegment(sketch, "E4524", {"start": v(503.78, -67.6) * mm, "end": v(499.94, -71.35) * mm});
            skLineSegment(sketch, "E4525", {"start": v(499.94, -71.35) * mm, "end": v(498.6, -72.54) * mm});
            skLineSegment(sketch, "E4526", {"start": v(498.6, -72.54) * mm, "end": v(497.5, -73.49) * mm});
            skLineSegment(sketch, "E4527", {"start": v(497.5, -73.49) * mm, "end": v(498.75, -74.24) * mm});
            skLineSegment(sketch, "E4528", {"start": v(498.75, -74.24) * mm, "end": v(499.03, -74.41) * mm});
            skLineSegment(sketch, "E4529", {"start": v(499.03, -74.41) * mm, "end": v(501.81, -76.13) * mm});
            skLineSegment(sketch, "E4530", {"start": v(501.81, -76.13) * mm, "end": v(502.1, -76.3) * mm});
            skLineSegment(sketch, "E4531", {"start": v(502.1, -76.3) * mm, "end": v(502.8, -76.75) * mm});
            skLineSegment(sketch, "E4532", {"start": v(502.8, -76.75) * mm, "end": v(503.4, -76.15) * mm});
            skLineSegment(sketch, "E4533", {"start": v(503.4, -76.15) * mm, "end": v(504.4, -75.17) * mm});
            skLineSegment(sketch, "E4534", {"start": v(504.4, -75.17) * mm, "end": v(514.32, -65.44) * mm});
            skLineSegment(sketch, "E4535", {"start": v(514.32, -65.44) * mm, "end": v(515.29, -64.45) * mm});
            skLineSegment(sketch, "E4536", {"start": v(515.29, -64.45) * mm, "end": v(516.41, -63.86) * mm});
            skLineSegment(sketch, "E4537", {"start": v(516.41, -63.86) * mm, "end": v(519.46, -61.5) * mm});
            skLineSegment(sketch, "E4538", {"start": v(519.46, -61.5) * mm, "end": v(523.2, -57.8) * mm});
            skLineSegment(sketch, "E4539", {"start": v(523.2, -57.8) * mm, "end": v(526.9, -54.02) * mm});
            skLineSegment(sketch, "E4540", {"start": v(526.9, -54.02) * mm, "end": v(529.9, -51.47) * mm});
            skLineSegment(sketch, "E4541", {"start": v(529.9, -51.47) * mm, "end": v(531, -50.78) * mm});
            skLineSegment(sketch, "E4542", {"start": v(531, -50.78) * mm, "end": v(531.77, -50.3) * mm});
            skLineSegment(sketch, "E4543", {"start": v(531.77, -50.3) * mm, "end": v(535.87, -48.17) * mm});
            skLineSegment(sketch, "E4544", {"start": v(535.87, -48.17) * mm, "end": v(540.1, -46.26) * mm});
            skLineSegment(sketch, "E4545", {"start": v(540.1, -46.26) * mm, "end": v(540.92, -45.88) * mm});
            skLineSegment(sketch, "E4546", {"start": v(540.92, -45.88) * mm, "end": v(541.47, -45.64) * mm});
            skLineSegment(sketch, "E4547", {"start": v(541.47, -45.64) * mm, "end": v(543.06, -44.77) * mm});
            skLineSegment(sketch, "E4548", {"start": v(543.06, -44.77) * mm, "end": v(545.4, -43.62) * mm});
            skLineSegment(sketch, "E4549", {"start": v(545.4, -43.62) * mm, "end": v(547.76, -43.09) * mm});
            skLineSegment(sketch, "E4550", {"start": v(547.76, -43.09) * mm, "end": v(549.53, -43.5) * mm});
            skLineSegment(sketch, "E4551", {"start": v(549.53, -43.5) * mm, "end": v(549.97, -43.84) * mm});
            skLineSegment(sketch, "E4552", {"start": v(549.97, -43.84) * mm, "end": v(549.59, -44.94) * mm});
            skLineSegment(sketch, "E4553", {"start": v(549.59, -44.94) * mm, "end": v(548.2, -48.16) * mm});
            skLineSegment(sketch, "E4554", {"start": v(548.2, -48.16) * mm, "end": v(546.03, -52.21) * mm});
            skLineSegment(sketch, "E4555", {"start": v(546.03, -52.21) * mm, "end": v(543.53, -56.05) * mm});
            skLineSegment(sketch, "E4556", {"start": v(543.53, -56.05) * mm, "end": v(540.78, -59.72) * mm});
            skLineSegment(sketch, "E4557", {"start": v(540.78, -59.72) * mm, "end": v(537.86, -63.29) * mm});
            skLineSegment(sketch, "E4558", {"start": v(537.86, -63.29) * mm, "end": v(534.86, -66.8) * mm});
            skLineSegment(sketch, "E4559", {"start": v(534.86, -66.8) * mm, "end": v(531.85, -70.3) * mm});
            skLineSegment(sketch, "E4560", {"start": v(531.85, -70.3) * mm, "end": v(529.63, -72.97) * mm});
            skLineSegment(sketch, "E4561", {"start": v(529.63, -72.97) * mm, "end": v(528.92, -73.87) * mm});
            skLineSegment(sketch, "E4562", {"start": v(528.92, -73.87) * mm, "end": v(528.14, -74.85) * mm});
            skLineSegment(sketch, "E4563", {"start": v(528.14, -74.85) * mm, "end": v(524.05, -79.57) * mm});
            skLineSegment(sketch, "E4564", {"start": v(524.05, -79.57) * mm, "end": v(519.83, -84.18) * mm});
            skLineSegment(sketch, "E4565", {"start": v(519.83, -84.18) * mm, "end": v(518.97, -85.09) * mm});
            skLineSegment(sketch, "E4566", {"start": v(518.97, -85.09) * mm, "end": v(518.08, -86.05) * mm});
            skLineSegment(sketch, "E4567", {"start": v(518.08, -86.05) * mm, "end": v(519.2, -86.73) * mm});
            skLineSegment(sketch, "E4568", {"start": v(519.2, -86.73) * mm, "end": v(519.45, -86.89) * mm});
            skLineSegment(sketch, "E4569", {"start": v(519.45, -86.89) * mm, "end": v(522, -88.44) * mm});
            skLineSegment(sketch, "E4570", {"start": v(522, -88.44) * mm, "end": v(522.26, -88.6) * mm});
            skLineSegment(sketch, "E4571", {"start": v(522.26, -88.6) * mm, "end": v(523.02, -89.07) * mm});
            skLineSegment(sketch, "E4572", {"start": v(523.02, -89.07) * mm, "end": v(523.6, -88.41) * mm});
            skLineSegment(sketch, "E4573", {"start": v(523.6, -88.41) * mm, "end": v(524.67, -87.26) * mm});
            skLineSegment(sketch, "E4574", {"start": v(524.67, -87.26) * mm, "end": v(527.77, -83.75) * mm});
            skLineSegment(sketch, "E4575", {"start": v(527.77, -83.75) * mm, "end": v(531.89, -79.02) * mm});
            skLineSegment(sketch, "E4576", {"start": v(531.89, -79.02) * mm, "end": v(536.02, -74.27) * mm});
            skLineSegment(sketch, "E4577", {"start": v(536.02, -74.27) * mm, "end": v(540.22, -69.59) * mm});
            skLineSegment(sketch, "E4578", {"start": v(540.22, -69.59) * mm, "end": v(544.54, -65.04) * mm});
            skLineSegment(sketch, "E4579", {"start": v(544.54, -65.04) * mm, "end": v(549.05, -60.68) * mm});
            skLineSegment(sketch, "E4580", {"start": v(549.05, -60.68) * mm, "end": v(553.78, -56.6) * mm});
            skLineSegment(sketch, "E4581", {"start": v(553.78, -56.6) * mm, "end": v(557.53, -53.74) * mm});
            skLineSegment(sketch, "E4582", {"start": v(557.53, -53.74) * mm, "end": v(558.82, -52.86) * mm});
            skLineSegment(sketch, "E4583", {"start": v(558.82, -52.86) * mm, "end": v(558.9, -52.82) * mm});
            skLineSegment(sketch, "E4584", {"start": v(558.9, -52.82) * mm, "end": v(558.97, -52.75) * mm});
            skLineSegment(sketch, "E4585", {"start": v(558.97, -52.75) * mm, "end": v(559.24, -52.49) * mm});
            skLineSegment(sketch, "E4586", {"start": v(559.24, -52.49) * mm, "end": v(560.21, -51.84) * mm});
            skLineSegment(sketch, "E4587", {"start": v(560.21, -51.84) * mm, "end": v(561.98, -50.96) * mm});
            skLineSegment(sketch, "E4588", {"start": v(561.98, -50.96) * mm, "end": v(564.06, -50.22) * mm});
            skLineSegment(sketch, "E4589", {"start": v(564.06, -50.22) * mm, "end": v(566.26, -49.74) * mm});
            skLineSegment(sketch, "E4590", {"start": v(566.26, -49.74) * mm, "end": v(568.38, -49.62) * mm});
            skLineSegment(sketch, "E4591", {"start": v(568.38, -49.62) * mm, "end": v(570.22, -49.96) * mm});
            skLineSegment(sketch, "E4592", {"start": v(570.22, -49.96) * mm, "end": v(571.59, -50.89) * mm});
            skLineSegment(sketch, "E4593", {"start": v(571.59, -50.89) * mm, "end": v(572.22, -52.08) * mm});
            skLineSegment(sketch, "E4594", {"start": v(572.22, -52.08) * mm, "end": v(572.28, -52.5) * mm});
            skLineSegment(sketch, "E4595", {"start": v(572.28, -52.5) * mm, "end": v(572.34, -52.97) * mm});
            skLineSegment(sketch, "E4596", {"start": v(572.34, -52.97) * mm, "end": v(572.16, -54.42) * mm});
            skLineSegment(sketch, "E4597", {"start": v(572.16, -54.42) * mm, "end": v(571.43, -56.52) * mm});
            skLineSegment(sketch, "E4598", {"start": v(571.43, -56.52) * mm, "end": v(570.24, -58.72) * mm});
            skLineSegment(sketch, "E4599", {"start": v(570.24, -58.72) * mm, "end": v(568.74, -60.95) * mm});
            skLineSegment(sketch, "E4600", {"start": v(568.74, -60.95) * mm, "end": v(567.08, -63.13) * mm});
            skLineSegment(sketch, "E4601", {"start": v(567.08, -63.13) * mm, "end": v(565.42, -65.2) * mm});
            skLineSegment(sketch, "E4602", {"start": v(565.42, -65.2) * mm, "end": v(563.92, -67.05) * mm});
            skLineSegment(sketch, "E4603", {"start": v(563.92, -67.05) * mm, "end": v(563.01, -68.23) * mm});
            skLineSegment(sketch, "E4604", {"start": v(563.01, -68.23) * mm, "end": v(562.73, -68.64) * mm});
            skLineSegment(sketch, "E4605", {"start": v(562.73, -68.64) * mm, "end": v(561.8, -69.95) * mm});
            skLineSegment(sketch, "E4606", {"start": v(561.8, -69.95) * mm, "end": v(553.12, -83.42) * mm});
            skLineSegment(sketch, "E4607", {"start": v(553.12, -83.42) * mm, "end": v(552.32, -84.81) * mm});
            skLineSegment(sketch, "E4608", {"start": v(552.32, -84.81) * mm, "end": v(551.32, -86.13) * mm});
            skLineSegment(sketch, "E4609", {"start": v(551.32, -86.13) * mm, "end": v(546.12, -92.47) * mm});
            skLineSegment(sketch, "E4610", {"start": v(546.12, -92.47) * mm, "end": v(540.68, -98.62) * mm});
            skLineSegment(sketch, "E4611", {"start": v(540.68, -98.62) * mm, "end": v(539.57, -99.83) * mm});
            skLineSegment(sketch, "E4612", {"start": v(539.57, -99.83) * mm, "end": v(538.98, -100.48) * mm});
            skLineSegment(sketch, "E4613", {"start": v(538.98, -100.48) * mm, "end": v(539.48, -101.18) * mm});
            skLineSegment(sketch, "E4614", {"start": v(539.48, -101.18) * mm, "end": v(539.63, -101.39) * mm});
            skLineSegment(sketch, "E4615", {"start": v(539.63, -101.39) * mm, "end": v(540.9, -103.57) * mm});
            skLineSegment(sketch, "E4616", {"start": v(540.9, -103.57) * mm, "end": v(541, -103.79) * mm});
            skLineSegment(sketch, "E4617", {"start": v(541, -103.79) * mm, "end": v(541.7, -105.19) * mm});
            skLineSegment(sketch, "E4618", {"start": v(541.7, -105.19) * mm, "end": v(542.75, -104.03) * mm});
            skLineSegment(sketch, "E4619", {"start": v(542.75, -104.03) * mm, "end": v(544.5, -102.1) * mm});
            skLineSegment(sketch, "E4620", {"start": v(544.5, -102.1) * mm, "end": v(553.02, -92.25) * mm});
            skLineSegment(sketch, "E4621", {"start": v(553.02, -92.25) * mm, "end": v(561.1, -82.04) * mm});
            skLineSegment(sketch, "E4622", {"start": v(561.1, -82.04) * mm, "end": v(562.63, -79.93) * mm});
            skLineSegment(sketch, "E4623", {"start": v(562.63, -79.93) * mm, "end": v(563.88, -79.25) * mm});
            skLineSegment(sketch, "E4624", {"start": v(563.88, -79.25) * mm, "end": v(567.35, -76.7) * mm});
            skLineSegment(sketch, "E4625", {"start": v(567.35, -76.7) * mm, "end": v(571.36, -72.8) * mm});
            skLineSegment(sketch, "E4626", {"start": v(571.36, -72.8) * mm, "end": v(574.97, -68.47) * mm});
            skLineSegment(sketch, "E4627", {"start": v(574.97, -68.47) * mm, "end": v(577.6, -65.1) * mm});
            skLineSegment(sketch, "E4628", {"start": v(577.6, -65.1) * mm, "end": v(578.5, -64) * mm});
            skLineSegment(sketch, "E4629", {"start": v(578.5, -64) * mm, "end": v(579.1, -63.97) * mm});
            skLineSegment(sketch, "E4630", {"start": v(579.1, -63.97) * mm, "end": v(580.86, -63.41) * mm});
            skLineSegment(sketch, "E4631", {"start": v(580.86, -63.41) * mm, "end": v(582.49, -62.2) * mm});
            skLineSegment(sketch, "E4632", {"start": v(582.49, -62.2) * mm, "end": v(583.83, -60.87) * mm});
            skLineSegment(sketch, "E4633", {"start": v(583.83, -60.87) * mm, "end": v(584.9, -60.04) * mm});
            skLineSegment(sketch, "E4634", {"start": v(584.9, -60.04) * mm, "end": v(585.32, -59.89) * mm});
            skLineSegment(sketch, "E4635", {"start": v(585.32, -59.89) * mm, "end": v(585.63, -60.35) * mm});
            skLineSegment(sketch, "E4636", {"start": v(585.63, -60.35) * mm, "end": v(585.95, -62.18) * mm});
            skLineSegment(sketch, "E4637", {"start": v(585.95, -62.18) * mm, "end": v(585.32, -64.62) * mm});
            skLineSegment(sketch, "E4638", {"start": v(585.32, -64.62) * mm, "end": v(584.05, -66.99) * mm});
            skLineSegment(sketch, "E4639", {"start": v(584.05, -66.99) * mm, "end": v(583.07, -68.52) * mm});
            skLineSegment(sketch, "E4640", {"start": v(583.07, -68.52) * mm, "end": v(582.76, -69.04) * mm});
            skLineSegment(sketch, "E4641", {"start": v(582.76, -69.04) * mm, "end": v(582.27, -69.86) * mm});
            skLineSegment(sketch, "E4642", {"start": v(582.27, -69.86) * mm, "end": v(579.3, -73.52) * mm});
            skLineSegment(sketch, "E4643", {"start": v(579.3, -73.52) * mm, "end": v(576.1, -77) * mm});
            skLineSegment(sketch, "E4644", {"start": v(576.1, -77) * mm, "end": v(575.5, -77.72) * mm});
            skLineSegment(sketch, "E4645", {"start": v(575.5, -77.72) * mm, "end": v(575.24, -78.05) * mm});
            skLineSegment(sketch, "E4646", {"start": v(575.24, -78.05) * mm, "end": v(572.67, -81.33) * mm});
            skLineSegment(sketch, "E4647", {"start": v(572.67, -81.33) * mm, "end": v(572.42, -81.67) * mm});
            skLineSegment(sketch, "E4648", {"start": v(572.42, -81.67) * mm, "end": v(571.53, -82.85) * mm});
            skLineSegment(sketch, "E4649", {"start": v(571.53, -82.85) * mm, "end": v(567.05, -88.95) * mm});
            skLineSegment(sketch, "E4650", {"start": v(567.05, -88.95) * mm, "end": v(562.29, -94.8) * mm});
            skLineSegment(sketch, "E4651", {"start": v(562.29, -94.8) * mm, "end": v(561.25, -95.85) * mm});
            skLineSegment(sketch, "E4652", {"start": v(561.25, -95.85) * mm, "end": v(561.07, -95.97) * mm});
            skLineSegment(sketch, "E4653", {"start": v(561.07, -95.97) * mm, "end": v(560.6, -96.5) * mm});
            skLineSegment(sketch, "E4654", {"start": v(560.6, -96.5) * mm, "end": v(560.3, -97.27) * mm});
            skLineSegment(sketch, "E4655", {"start": v(560.3, -97.27) * mm, "end": v(560.16, -98.1) * mm});
            skLineSegment(sketch, "E4656", {"start": v(560.16, -98.1) * mm, "end": v(560.05, -98.71) * mm});
            skLineSegment(sketch, "E4657", {"start": v(560.05, -98.71) * mm, "end": v(560, -98.91) * mm});
            skLineSegment(sketch, "E4658", {"start": v(560, -98.91) * mm, "end": v(558.84, -100.02) * mm});
            skLineSegment(sketch, "E4659", {"start": v(558.84, -100.02) * mm, "end": v(553.3, -105.76) * mm});
            skLineSegment(sketch, "E4660", {"start": v(553.3, -105.76) * mm, "end": v(547.95, -111.67) * mm});
            skLineSegment(sketch, "E4661", {"start": v(547.95, -111.67) * mm, "end": v(546.9, -112.88) * mm});
            skLineSegment(sketch, "E4662", {"start": v(546.9, -112.88) * mm, "end": v(546.09, -113.8) * mm});
            skLineSegment(sketch, "E4663", {"start": v(546.09, -113.8) * mm, "end": v(547.11, -114.47) * mm});
            skLineSegment(sketch, "E4664", {"start": v(547.11, -114.47) * mm, "end": v(547.33, -114.62) * mm});
            skLineSegment(sketch, "E4665", {"start": v(547.33, -114.62) * mm, "end": v(549.5, -116.15) * mm});
            skLineSegment(sketch, "E4666", {"start": v(549.5, -116.15) * mm, "end": v(549.73, -116.31) * mm});
            skLineSegment(sketch, "E4667", {"start": v(549.73, -116.31) * mm, "end": v(550.51, -116.88) * mm});
            skLineSegment(sketch, "E4668", {"start": v(550.51, -116.88) * mm, "end": v(551.16, -116.16) * mm});
            skLineSegment(sketch, "E4669", {"start": v(551.16, -116.16) * mm, "end": v(552.06, -115.17) * mm});
            skLineSegment(sketch, "E4670", {"start": v(552.06, -115.17) * mm, "end": v(560.9, -105.12) * mm});
            skLineSegment(sketch, "E4671", {"start": v(560.9, -105.12) * mm, "end": v(561.75, -104.08) * mm});
            skLineSegment(sketch, "E4672", {"start": v(561.75, -104.08) * mm, "end": v(563.55, -101.87) * mm});
            skLineSegment(sketch, "E4673", {"start": v(563.55, -101.87) * mm, "end": v(572.98, -91.16) * mm});
            skLineSegment(sketch, "E4674", {"start": v(572.98, -91.16) * mm, "end": v(582.8, -80.8) * mm});
            skLineSegment(sketch, "E4675", {"start": v(582.8, -80.8) * mm, "end": v(584.8, -78.78) * mm});
            skLineSegment(sketch, "E4676", {"start": v(584.8, -78.78) * mm, "end": v(585.43, -78.14) * mm});
            skLineSegment(sketch, "E4677", {"start": v(585.43, -78.14) * mm, "end": v(587.2, -76.09) * mm});
            skLineSegment(sketch, "E4678", {"start": v(587.2, -76.09) * mm, "end": v(589.6, -73.2) * mm});
            skLineSegment(sketch, "E4679", {"start": v(589.6, -73.2) * mm, "end": v(592.17, -70.5) * mm});
            skLineSegment(sketch, "E4680", {"start": v(592.17, -70.5) * mm, "end": v(594.23, -68.82) * mm});
            skLineSegment(sketch, "E4681", {"start": v(594.23, -68.82) * mm, "end": v(595, -68.4) * mm});
            skLineSegment(sketch, "E4682", {"start": v(595, -68.4) * mm, "end": v(595.26, -68.24) * mm});
            skLineSegment(sketch, "E4683", {"start": v(595.26, -68.24) * mm, "end": v(595.41, -67.98) * mm});
            skLineSegment(sketch, "E4684", {"start": v(595.41, -67.98) * mm, "end": v(595.87, -67.12) * mm});
            skLineSegment(sketch, "E4685", {"start": v(595.87, -67.12) * mm, "end": v(597.48, -64.67) * mm});
            skLineSegment(sketch, "E4686", {"start": v(597.48, -64.67) * mm, "end": v(599.96, -61.99) * mm});
            skLineSegment(sketch, "E4687", {"start": v(599.96, -61.99) * mm, "end": v(602.98, -60) * mm});
            skLineSegment(sketch, "E4688", {"start": v(602.98, -60) * mm, "end": v(605.7, -58.98) * mm});
            skLineSegment(sketch, "E4689", {"start": v(605.7, -58.98) * mm, "end": v(606.65, -58.79) * mm});
            skLineSegment(sketch, "E4690", {"start": v(606.65, -58.79) * mm, "end": v(606.7, -58.94) * mm});
            skLineSegment(sketch, "E4691", {"start": v(606.7, -58.94) * mm, "end": v(606.75, -59.41) * mm});
            skLineSegment(sketch, "E4692", {"start": v(606.75, -59.41) * mm, "end": v(606.8, -60.12) * mm});
            skLineSegment(sketch, "E4693", {"start": v(606.8, -60.12) * mm, "end": v(606.8, -60.79) * mm});
            skLineSegment(sketch, "E4694", {"start": v(606.8, -60.79) * mm, "end": v(606.79, -61.14) * mm});
            skLineSegment(sketch, "E4695", {"start": v(606.79, -61.14) * mm, "end": v(606.79, -61.25) * mm});
            skLineSegment(sketch, "E4696", {"start": v(606.79, -61.25) * mm, "end": v(606.78, -61.49) * mm});
            skLineSegment(sketch, "E4697", {"start": v(606.78, -61.49) * mm, "end": v(606.8, -62.76) * mm});
            skLineSegment(sketch, "E4698", {"start": v(606.8, -62.76) * mm, "end": v(606.95, -64.03) * mm});
            skLineSegment(sketch, "E4699", {"start": v(606.95, -64.03) * mm, "end": v(607.02, -64.26) * mm});
            skLineSegment(sketch, "E4700", {"start": v(607.02, -64.26) * mm, "end": v(606.46, -65.37) * mm});
            skLineSegment(sketch, "E4701", {"start": v(606.46, -65.37) * mm, "end": v(603.28, -70.65) * mm});
            skLineSegment(sketch, "E4702", {"start": v(603.28, -70.65) * mm, "end": v(600.12, -75.94) * mm});
            skLineSegment(sketch, "E4703", {"start": v(600.12, -75.94) * mm, "end": v(599.58, -77.06) * mm});
            skLineSegment(sketch, "E4704", {"start": v(599.58, -77.06) * mm, "end": v(597.5, -79.25) * mm});
            skLineSegment(sketch, "E4705", {"start": v(597.5, -79.25) * mm, "end": v(591.7, -86.25) * mm});
            skLineSegment(sketch, "E4706", {"start": v(591.7, -86.25) * mm, "end": v(584.55, -96.07) * mm});
            skLineSegment(sketch, "E4707", {"start": v(584.55, -96.07) * mm, "end": v(577.88, -106.24) * mm});
            skLineSegment(sketch, "E4708", {"start": v(577.88, -106.24) * mm, "end": v(573.05, -113.93) * mm});
            skLineSegment(sketch, "E4709", {"start": v(573.05, -113.93) * mm, "end": v(571.44, -116.49) * mm});
            skLineSegment(sketch, "E4710", {"start": v(571.44, -116.49) * mm, "end": v(570.73, -117.35) * mm});
            skLineSegment(sketch, "E4711", {"start": v(570.73, -117.35) * mm, "end": v(563.55, -125.84) * mm});
            skLineSegment(sketch, "E4712", {"start": v(563.55, -125.84) * mm, "end": v(562.83, -126.7) * mm});
            skLineSegment(sketch, "E4713", {"start": v(562.83, -126.7) * mm, "end": v(562.23, -127.4) * mm});
            skLineSegment(sketch, "E4714", {"start": v(562.23, -127.4) * mm, "end": v(562.87, -128.1) * mm});
            skLineSegment(sketch, "E4715", {"start": v(562.87, -128.1) * mm, "end": v(563.1, -128.35) * mm});
            skLineSegment(sketch, "E4716", {"start": v(563.1, -128.35) * mm, "end": v(565.34, -130.91) * mm});
            skLineSegment(sketch, "E4717", {"start": v(565.34, -130.91) * mm, "end": v(565.56, -131.17) * mm});
            skLineSegment(sketch, "E4718", {"start": v(565.56, -131.17) * mm, "end": v(566.4, -132.18) * mm});
            skLineSegment(sketch, "E4719", {"start": v(566.4, -132.18) * mm, "end": v(567.21, -131.13) * mm});
            skLineSegment(sketch, "E4720", {"start": v(567.21, -131.13) * mm, "end": v(567.49, -130.78) * mm});
            skLineSegment(sketch, "E4721", {"start": v(567.49, -130.78) * mm, "end": v(568.88, -129.03) * mm});
            skLineSegment(sketch, "E4722", {"start": v(568.88, -129.03) * mm, "end": v(570.37, -127.35) * mm});
            skLineSegment(sketch, "E4723", {"start": v(570.37, -127.35) * mm, "end": v(570.7, -127.04) * mm});
            skLineSegment(sketch, "E4724", {"start": v(570.7, -127.04) * mm, "end": v(571.35, -126.4) * mm});
            skLineSegment(sketch, "E4725", {"start": v(571.35, -126.4) * mm, "end": v(573.3, -124.45) * mm});
            skLineSegment(sketch, "E4726", {"start": v(573.3, -124.45) * mm, "end": v(575.75, -121.81) * mm});
            skLineSegment(sketch, "E4727", {"start": v(575.75, -121.81) * mm, "end": v(577.97, -119) * mm});
            skLineSegment(sketch, "E4728", {"start": v(577.97, -119) * mm, "end": v(579.5, -116.69) * mm});
            skLineSegment(sketch, "E4729", {"start": v(579.5, -116.69) * mm, "end": v(579.94, -115.88) * mm});
            skLineSegment(sketch, "E4730", {"start": v(579.94, -115.88) * mm, "end": v(580.58, -114.71) * mm});
            skLineSegment(sketch, "E4731", {"start": v(580.58, -114.71) * mm, "end": v(583.83, -109.26) * mm});
            skLineSegment(sketch, "E4732", {"start": v(583.83, -109.26) * mm, "end": v(587.44, -104.02) * mm});
            skLineSegment(sketch, "E4733", {"start": v(587.44, -104.02) * mm, "end": v(588.26, -102.97) * mm});
            skLineSegment(sketch, "E4734", {"start": v(588.26, -102.97) * mm, "end": v(589.08, -101.9) * mm});
            skLineSegment(sketch, "E4735", {"start": v(589.08, -101.9) * mm, "end": v(591.45, -98.63) * mm});
            skLineSegment(sketch, "E4736", {"start": v(591.45, -98.63) * mm, "end": v(594.53, -94.4) * mm});
            skLineSegment(sketch, "E4737", {"start": v(594.53, -94.4) * mm, "end": v(597.86, -90.35) * mm});
            skLineSegment(sketch, "E4738", {"start": v(597.86, -90.35) * mm, "end": v(600.74, -87.46) * mm});
            skLineSegment(sketch, "E4739", {"start": v(600.74, -87.46) * mm, "end": v(601.79, -86.6) * mm});
            skLineSegment(sketch, "E4740", {"start": v(601.79, -86.6) * mm, "end": v(602.21, -86.26) * mm});
            skLineSegment(sketch, "E4741", {"start": v(602.21, -86.26) * mm, "end": v(603.54, -85.14) * mm});
            skLineSegment(sketch, "E4742", {"start": v(603.54, -85.14) * mm, "end": v(605.9, -83.3) * mm});
            skLineSegment(sketch, "E4743", {"start": v(605.9, -83.3) * mm, "end": v(608.35, -81.75) * mm});
            skLineSegment(sketch, "E4744", {"start": v(608.35, -81.75) * mm, "end": v(609.9, -81.16) * mm});
            skLineSegment(sketch, "E4745", {"start": v(609.9, -81.16) * mm, "end": v(610.4, -81.22) * mm});
            skLineSegment(sketch, "E4746", {"start": v(610.4, -81.22) * mm, "end": v(610.69, -81.26) * mm});
            skLineSegment(sketch, "E4747", {"start": v(610.69, -81.26) * mm, "end": v(611.55, -81.66) * mm});
            skLineSegment(sketch, "E4748", {"start": v(611.55, -81.66) * mm, "end": v(612.27, -82.57) * mm});
            skLineSegment(sketch, "E4749", {"start": v(612.27, -82.57) * mm, "end": v(612.62, -83.82) * mm});
            skLineSegment(sketch, "E4750", {"start": v(612.62, -83.82) * mm, "end": v(612.68, -85.27) * mm});
            skLineSegment(sketch, "E4751", {"start": v(612.68, -85.27) * mm, "end": v(612.52, -86.81) * mm});
            skLineSegment(sketch, "E4752", {"start": v(612.52, -86.81) * mm, "end": v(612.23, -88.3) * mm});
            skLineSegment(sketch, "E4753", {"start": v(612.23, -88.3) * mm, "end": v(611.87, -89.63) * mm});
            skLineSegment(sketch, "E4754", {"start": v(611.87, -89.63) * mm, "end": v(611.62, -90.4) * mm});
            skLineSegment(sketch, "E4755", {"start": v(611.62, -90.4) * mm, "end": v(611.53, -90.66) * mm});
            skLineSegment(sketch, "E4756", {"start": v(611.53, -90.66) * mm, "end": v(610.95, -92.17) * mm});
            skLineSegment(sketch, "E4757", {"start": v(610.95, -92.17) * mm, "end": v(608.53, -96.45) * mm});
            skLineSegment(sketch, "E4758", {"start": v(608.53, -96.45) * mm, "end": v(604.66, -101.86) * mm});
            skLineSegment(sketch, "E4759", {"start": v(604.66, -101.86) * mm, "end": v(600.63, -107.19) * mm});
            skLineSegment(sketch, "E4760", {"start": v(600.63, -107.19) * mm, "end": v(597.9, -111.28) * mm});
            skLineSegment(sketch, "E4761", {"start": v(597.9, -111.28) * mm, "end": v(597.17, -112.73) * mm});
            skLineSegment(sketch, "E4762", {"start": v(597.17, -112.73) * mm, "end": v(597.01, -112.97) * mm});
            skLineSegment(sketch, "E4763", {"start": v(597.01, -112.97) * mm, "end": v(596.55, -114.28) * mm});
            skLineSegment(sketch, "E4764", {"start": v(596.55, -114.28) * mm, "end": v(596.24, -115.63) * mm});
            skLineSegment(sketch, "E4765", {"start": v(596.24, -115.63) * mm, "end": v(596.16, -115.9) * mm});
            skLineSegment(sketch, "E4766", {"start": v(596.16, -115.9) * mm, "end": v(595.32, -116.9) * mm});
            skLineSegment(sketch, "E4767", {"start": v(595.32, -116.9) * mm, "end": v(591.46, -122.1) * mm});
            skLineSegment(sketch, "E4768", {"start": v(591.46, -122.1) * mm, "end": v(587.67, -127.38) * mm});
            skLineSegment(sketch, "E4769", {"start": v(587.67, -127.38) * mm, "end": v(586.87, -128.4) * mm});
            skLineSegment(sketch, "E4770", {"start": v(586.87, -128.4) * mm, "end": v(586.05, -129.46) * mm});
            skLineSegment(sketch, "E4771", {"start": v(586.05, -129.46) * mm, "end": v(582.15, -134.92) * mm});
            skLineSegment(sketch, "E4772", {"start": v(582.15, -134.92) * mm, "end": v(578.3, -140.4) * mm});
            skLineSegment(sketch, "E4773", {"start": v(578.3, -140.4) * mm, "end": v(577.5, -141.48) * mm});
            skLineSegment(sketch, "E4774", {"start": v(577.5, -141.48) * mm, "end": v(577.17, -141.91) * mm});
            skLineSegment(sketch, "E4775", {"start": v(577.17, -141.91) * mm, "end": v(573.86, -146.14) * mm});
            skLineSegment(sketch, "E4776", {"start": v(573.86, -146.14) * mm, "end": v(573.52, -146.56) * mm});
            skLineSegment(sketch, "E4777", {"start": v(573.52, -146.56) * mm, "end": v(573.38, -146.73) * mm});
            skLineSegment(sketch, "E4778", {"start": v(573.38, -146.73) * mm, "end": v(573.32, -146.96) * mm});
            skLineSegment(sketch, "E4779", {"start": v(573.32, -146.96) * mm, "end": v(573.3, -147.04) * mm});
            skLineSegment(sketch, "E4780", {"start": v(573.3, -147.04) * mm, "end": v(573.14, -147.84) * mm});
            skLineSegment(sketch, "E4781", {"start": v(573.14, -147.84) * mm, "end": v(573.14, -147.93) * mm});
            skLineSegment(sketch, "E4782", {"start": v(573.14, -147.93) * mm, "end": v(573.14, -148.42) * mm});
            skLineSegment(sketch, "E4783", {"start": v(573.14, -148.42) * mm, "end": v(573.52, -148.76) * mm});
            skLineSegment(sketch, "E4784", {"start": v(573.52, -148.76) * mm, "end": v(573.68, -148.9) * mm});
            skLineSegment(sketch, "E4785", {"start": v(573.68, -148.9) * mm, "end": v(575.36, -150.38) * mm});
            skLineSegment(sketch, "E4786", {"start": v(575.36, -150.38) * mm, "end": v(575.52, -150.52) * mm});
            skLineSegment(sketch, "E4787", {"start": v(575.52, -150.52) * mm, "end": v(576.39, -151.29) * mm});
            skLineSegment(sketch, "E4788", {"start": v(576.39, -151.29) * mm, "end": v(577.1, -150.37) * mm});
            skLineSegment(sketch, "E4789", {"start": v(577.1, -150.37) * mm, "end": v(577.9, -149.3) * mm});
            skLineSegment(sketch, "E4790", {"start": v(577.9, -149.3) * mm, "end": v(585.82, -138.55) * mm});
            skLineSegment(sketch, "E4791", {"start": v(585.82, -138.55) * mm, "end": v(586.58, -137.46) * mm});
            skLineSegment(sketch, "E4792", {"start": v(586.58, -137.46) * mm, "end": v(587.42, -136.28) * mm});
            skLineSegment(sketch, "E4793", {"start": v(587.42, -136.28) * mm, "end": v(590.13, -132.88) * mm});
            skLineSegment(sketch, "E4794", {"start": v(590.13, -132.88) * mm, "end": v(593.88, -128.85) * mm});
            skLineSegment(sketch, "E4795", {"start": v(593.88, -128.85) * mm, "end": v(597.94, -125.14) * mm});
            skLineSegment(sketch, "E4796", {"start": v(597.94, -125.14) * mm, "end": v(601.29, -122.38) * mm});
            skLineSegment(sketch, "E4797", {"start": v(601.29, -122.38) * mm, "end": v(602.42, -121.5) * mm});
            skLineSegment(sketch, "E4798", {"start": v(602.42, -121.5) * mm, "end": v(603.29, -120.83) * mm});
            skLineSegment(sketch, "E4799", {"start": v(603.29, -120.83) * mm, "end": v(605.83, -118.77) * mm});
            skLineSegment(sketch, "E4800", {"start": v(605.83, -118.77) * mm, "end": v(609.05, -116.44) * mm});
            skLineSegment(sketch, "E4801", {"start": v(609.05, -116.44) * mm, "end": v(612.59, -114.84) * mm});
            skLineSegment(sketch, "E4802", {"start": v(612.59, -114.84) * mm, "end": v(615.84, -114.28) * mm});
            skLineSegment(sketch, "E4803", {"start": v(615.84, -114.28) * mm, "end": v(616.92, -114.3) * mm});
            skLineSegment(sketch, "E4804", {"start": v(616.92, -114.3) * mm, "end": v(617.17, -114.8) * mm});
            skLineSegment(sketch, "E4805", {"start": v(617.17, -114.8) * mm, "end": v(617.53, -116.47) * mm});
            skLineSegment(sketch, "E4806", {"start": v(617.53, -116.47) * mm, "end": v(617.42, -118.73) * mm});
            skLineSegment(sketch, "E4807", {"start": v(617.42, -118.73) * mm, "end": v(616.89, -120.98) * mm});
            skLineSegment(sketch, "E4808", {"start": v(616.89, -120.98) * mm, "end": v(616.37, -122.6) * mm});
            skLineSegment(sketch, "E4809", {"start": v(616.37, -122.6) * mm, "end": v(616.2, -123.13) * mm});
            skLineSegment(sketch, "E4810", {"start": v(616.2, -123.13) * mm, "end": v(615.82, -124.28) * mm});
            skLineSegment(sketch, "E4811", {"start": v(615.82, -124.28) * mm, "end": v(614.51, -127.67) * mm});
            skLineSegment(sketch, "E4812", {"start": v(614.51, -127.67) * mm, "end": v(612.46, -132.12) * mm});
            skLineSegment(sketch, "E4813", {"start": v(612.46, -132.12) * mm, "end": v(610.06, -136.4) * mm});
            skLineSegment(sketch, "E4814", {"start": v(610.06, -136.4) * mm, "end": v(608.06, -139.44) * mm});
            skLineSegment(sketch, "E4815", {"start": v(608.06, -139.44) * mm, "end": v(607.33, -140.4) * mm});
            skLineSegment(sketch, "E4816", {"start": v(607.33, -140.4) * mm, "end": v(606.85, -141.04) * mm});
            skLineSegment(sketch, "E4817", {"start": v(606.85, -141.04) * mm, "end": v(604.07, -143.9) * mm});
            skLineSegment(sketch, "E4818", {"start": v(604.07, -143.9) * mm, "end": v(601.35, -146.82) * mm});
            skLineSegment(sketch, "E4819", {"start": v(601.35, -146.82) * mm, "end": v(600.9, -147.48) * mm});
            skLineSegment(sketch, "E4820", {"start": v(600.9, -147.48) * mm, "end": v(600.24, -148.44) * mm});
            skLineSegment(sketch, "E4821", {"start": v(600.24, -148.44) * mm, "end": v(597.47, -153.5) * mm});
            skLineSegment(sketch, "E4822", {"start": v(597.47, -153.5) * mm, "end": v(594.61, -158.49) * mm});
            skLineSegment(sketch, "E4823", {"start": v(594.61, -158.49) * mm, "end": v(593.93, -159.41) * mm});
            skLineSegment(sketch, "E4824", {"start": v(593.93, -159.41) * mm, "end": v(593.64, -159.8) * mm});
            skLineSegment(sketch, "E4825", {"start": v(593.64, -159.8) * mm, "end": v(590.88, -163.68) * mm});
            skLineSegment(sketch, "E4826", {"start": v(590.88, -163.68) * mm, "end": v(590.6, -164.07) * mm});
            skLineSegment(sketch, "E4827", {"start": v(590.6, -164.07) * mm, "end": v(590.17, -164.7) * mm});
            skLineSegment(sketch, "E4828", {"start": v(590.17, -164.7) * mm, "end": v(593.86, -170.07) * mm});
            skLineSegment(sketch, "E4829", {"start": v(593.86, -170.07) * mm, "end": v(594.75, -168.92) * mm});
            skLineSegment(sketch, "E4830", {"start": v(594.75, -168.92) * mm, "end": v(596.68, -166.47) * mm});
            skLineSegment(sketch, "E4831", {"start": v(596.68, -166.47) * mm, "end": v(606.08, -154.01) * mm});
            skLineSegment(sketch, "E4832", {"start": v(606.08, -154.01) * mm, "end": v(615, -141.23) * mm});
            skLineSegment(sketch, "E4833", {"start": v(615, -141.23) * mm, "end": v(616.7, -138.6) * mm});
            skLineSegment(sketch, "E4834", {"start": v(616.7, -138.6) * mm, "end": v(617.84, -137.63) * mm});
            skLineSegment(sketch, "E4835", {"start": v(617.84, -137.63) * mm, "end": v(629.44, -128.04) * mm});
            skLineSegment(sketch, "E4836", {"start": v(629.44, -128.04) * mm, "end": v(630.62, -127.1) * mm});
            skLineSegment(sketch, "E4837", {"start": v(630.62, -127.1) * mm, "end": v(631.16, -126.67) * mm});
            skLineSegment(sketch, "E4838", {"start": v(631.16, -126.67) * mm, "end": v(632.88, -125.47) * mm});
            skLineSegment(sketch, "E4839", {"start": v(632.88, -125.47) * mm, "end": v(635.2, -124.22) * mm});
            skLineSegment(sketch, "E4840", {"start": v(635.2, -124.22) * mm, "end": v(637.67, -123.42) * mm});
            skLineSegment(sketch, "E4841", {"start": v(637.67, -123.42) * mm, "end": v(639.73, -123.11) * mm});
            skLineSegment(sketch, "E4842", {"start": v(639.73, -123.11) * mm, "end": v(640.41, -123.1) * mm});
            skLineSegment(sketch, "E4843", {"start": v(640.41, -123.1) * mm, "end": v(640.72, -123.65) * mm});
            skLineSegment(sketch, "E4844", {"start": v(640.72, -123.65) * mm, "end": v(641.33, -125.5) * mm});
            skLineSegment(sketch, "E4845", {"start": v(641.33, -125.5) * mm, "end": v(641.46, -127.82) * mm});
            skLineSegment(sketch, "E4846", {"start": v(641.46, -127.82) * mm, "end": v(640.95, -130.06) * mm});
            skLineSegment(sketch, "E4847", {"start": v(640.95, -130.06) * mm, "end": v(639.98, -132.25) * mm});
            skLineSegment(sketch, "E4848", {"start": v(639.98, -132.25) * mm, "end": v(638.7, -134.38) * mm});
            skLineSegment(sketch, "E4849", {"start": v(638.7, -134.38) * mm, "end": v(637.3, -136.47) * mm});
            skLineSegment(sketch, "E4850", {"start": v(637.3, -136.47) * mm, "end": v(635.9, -138.52) * mm});
            skLineSegment(sketch, "E4851", {"start": v(635.9, -138.52) * mm, "end": v(634.98, -140.03) * mm});
            skLineSegment(sketch, "E4852", {"start": v(634.98, -140.03) * mm, "end": v(634.71, -140.55) * mm});
            skLineSegment(sketch, "E4853", {"start": v(634.71, -140.55) * mm, "end": v(634.58, -140.8) * mm});
            skLineSegment(sketch, "E4854", {"start": v(634.58, -140.8) * mm, "end": v(634.3, -141.61) * mm});
            skLineSegment(sketch, "E4855", {"start": v(634.3, -141.61) * mm, "end": v(634.03, -142.7) * mm});
            skLineSegment(sketch, "E4856", {"start": v(634.03, -142.7) * mm, "end": v(633.77, -143.78) * mm});
            skLineSegment(sketch, "E4857", {"start": v(633.77, -143.78) * mm, "end": v(633.5, -144.53) * mm});
            skLineSegment(sketch, "E4858", {"start": v(633.5, -144.53) * mm, "end": v(633.38, -144.76) * mm});
            skLineSegment(sketch, "E4859", {"start": v(633.38, -144.76) * mm, "end": v(633.23, -145.03) * mm});
            skLineSegment(sketch, "E4860", {"start": v(633.23, -145.03) * mm, "end": v(632.63, -145.78) * mm});
            skLineSegment(sketch, "E4861", {"start": v(632.63, -145.78) * mm, "end": v(631.66, -146.8) * mm});
            skLineSegment(sketch, "E4862", {"start": v(631.66, -146.8) * mm, "end": v(630.64, -147.81) * mm});
            skLineSegment(sketch, "E4863", {"start": v(630.64, -147.81) * mm, "end": v(629.95, -148.57) * mm});
            skLineSegment(sketch, "E4864", {"start": v(629.95, -148.57) * mm, "end": v(629.75, -148.84) * mm});
            skLineSegment(sketch, "E4865", {"start": v(629.75, -148.84) * mm, "end": v(628.33, -150.8) * mm});
            skLineSegment(sketch, "E4866", {"start": v(628.33, -150.8) * mm, "end": v(621.52, -160.8) * mm});
            skLineSegment(sketch, "E4867", {"start": v(621.52, -160.8) * mm, "end": v(614.73, -170.8) * mm});
            skLineSegment(sketch, "E4868", {"start": v(614.73, -170.8) * mm, "end": v(613.32, -172.77) * mm});
            skLineSegment(sketch, "E4869", {"start": v(613.32, -172.77) * mm, "end": v(612.76, -173.55) * mm});
            skLineSegment(sketch, "E4870", {"start": v(612.76, -173.55) * mm, "end": v(609.63, -177.2) * mm});
            skLineSegment(sketch, "E4871", {"start": v(609.63, -177.2) * mm, "end": v(606.51, -180.84) * mm});
            skLineSegment(sketch, "E4872", {"start": v(606.51, -180.84) * mm, "end": v(605.96, -181.62) * mm});
            skLineSegment(sketch, "E4873", {"start": v(605.96, -181.62) * mm, "end": v(605.81, -181.83) * mm});
            skLineSegment(sketch, "E4874", {"start": v(605.81, -181.83) * mm, "end": v(605.45, -182.5) * mm});
            skLineSegment(sketch, "E4875", {"start": v(605.45, -182.5) * mm, "end": v(605.08, -183.43) * mm});
            skLineSegment(sketch, "E4876", {"start": v(605.08, -183.43) * mm, "end": v(604.72, -184.33) * mm});
            skLineSegment(sketch, "E4877", {"start": v(604.72, -184.33) * mm, "end": v(604.4, -184.97) * mm});
            skLineSegment(sketch, "E4878", {"start": v(604.4, -184.97) * mm, "end": v(604.28, -185.16) * mm});
            skLineSegment(sketch, "E4879", {"start": v(604.28, -185.16) * mm, "end": v(604.25, -185.19) * mm});
            skLineSegment(sketch, "E4880", {"start": v(604.25, -185.19) * mm, "end": v(603.93, -185.52) * mm});
            skLineSegment(sketch, "E4881", {"start": v(603.93, -185.52) * mm, "end": v(603.9, -185.55) * mm});
            skLineSegment(sketch, "E4882", {"start": v(603.9, -185.55) * mm, "end": v(603.24, -186.18) * mm});
            skLineSegment(sketch, "E4883", {"start": v(603.24, -186.18) * mm, "end": v(603.75, -186.94) * mm});
            skLineSegment(sketch, "E4884", {"start": v(603.75, -186.94) * mm, "end": v(603.76, -186.96) * mm});
            skLineSegment(sketch, "E4885", {"start": v(603.76, -186.96) * mm, "end": v(603.92, -187.2) * mm});
            skLineSegment(sketch, "E4886", {"start": v(603.92, -187.2) * mm, "end": v(603.93, -187.22) * mm});
            skLineSegment(sketch, "E4887", {"start": v(603.93, -187.22) * mm, "end": v(604.43, -188.12) * mm});
            skLineSegment(sketch, "E4888", {"start": v(604.43, -188.12) * mm, "end": v(605.35, -187.65) * mm});
            skLineSegment(sketch, "E4889", {"start": v(605.35, -187.65) * mm, "end": v(605.82, -187.41) * mm});
            skLineSegment(sketch, "E4890", {"start": v(605.82, -187.41) * mm, "end": v(610.5, -185.09) * mm});
            skLineSegment(sketch, "E4891", {"start": v(610.5, -185.09) * mm, "end": v(610.98, -184.86) * mm});
            skLineSegment(sketch, "E4892", {"start": v(610.98, -184.86) * mm, "end": v(611.2, -184.73) * mm});
            skLineSegment(sketch, "E4893", {"start": v(611.2, -184.73) * mm, "end": v(611.37, -184.52) * mm});
            skLineSegment(sketch, "E4894", {"start": v(611.37, -184.52) * mm, "end": v(612.8, -182.54) * mm});
            skLineSegment(sketch, "E4895", {"start": v(612.8, -182.54) * mm, "end": v(620.46, -173.06) * mm});
            skLineSegment(sketch, "E4896", {"start": v(620.46, -173.06) * mm, "end": v(628.27, -163.7) * mm});
            skLineSegment(sketch, "E4897", {"start": v(628.27, -163.7) * mm, "end": v(629.78, -161.79) * mm});
            skLineSegment(sketch, "E4898", {"start": v(629.78, -161.79) * mm, "end": v(630.97, -160.27) * mm});
            skLineSegment(sketch, "E4899", {"start": v(630.97, -160.27) * mm, "end": v(634.3, -155.5) * mm});
            skLineSegment(sketch, "E4900", {"start": v(634.3, -155.5) * mm, "end": v(638.8, -148.92) * mm});
            skLineSegment(sketch, "E4901", {"start": v(638.8, -148.92) * mm, "end": v(643.6, -142.65) * mm});
            skLineSegment(sketch, "E4902", {"start": v(643.6, -142.65) * mm, "end": v(647.58, -138.48) * mm});
            skLineSegment(sketch, "E4903", {"start": v(647.58, -138.48) * mm, "end": v(649.07, -137.3) * mm});
            skLineSegment(sketch, "E4904", {"start": v(649.07, -137.3) * mm, "end": v(649.42, -137.02) * mm});
            skLineSegment(sketch, "E4905", {"start": v(649.42, -137.02) * mm, "end": v(649.47, -136.58) * mm});
            skLineSegment(sketch, "E4906", {"start": v(649.47, -136.58) * mm, "end": v(649.54, -135.98) * mm});
            skLineSegment(sketch, "E4907", {"start": v(649.54, -135.98) * mm, "end": v(650.4, -134.25) * mm});
            skLineSegment(sketch, "E4908", {"start": v(650.4, -134.25) * mm, "end": v(652.16, -132.55) * mm});
            skLineSegment(sketch, "E4909", {"start": v(652.16, -132.55) * mm, "end": v(654.18, -130.93) * mm});
            skLineSegment(sketch, "E4910", {"start": v(654.18, -130.93) * mm, "end": v(655.56, -129.43) * mm});
            skLineSegment(sketch, "E4911", {"start": v(655.56, -129.43) * mm, "end": v(655.87, -128.85) * mm});
            skLineSegment(sketch, "E4912", {"start": v(655.87, -128.85) * mm, "end": v(656.65, -128.55) * mm});
            skLineSegment(sketch, "E4913", {"start": v(656.65, -128.55) * mm, "end": v(658.8, -127.14) * mm});
            skLineSegment(sketch, "E4914", {"start": v(658.8, -127.14) * mm, "end": v(661.74, -124.81) * mm});
            skLineSegment(sketch, "E4915", {"start": v(661.74, -124.81) * mm, "end": v(664.58, -122.76) * mm});
            skLineSegment(sketch, "E4916", {"start": v(664.58, -122.76) * mm, "end": v(666.54, -121.88) * mm});
            skLineSegment(sketch, "E4917", {"start": v(666.54, -121.88) * mm, "end": v(667.2, -121.89) * mm});
            skLineSegment(sketch, "E4918", {"start": v(667.2, -121.89) * mm, "end": v(667.48, -121.89) * mm});
            skLineSegment(sketch, "E4919", {"start": v(667.48, -121.89) * mm, "end": v(668.36, -122.14) * mm});
            skLineSegment(sketch, "E4920", {"start": v(668.36, -122.14) * mm, "end": v(669.2, -122.66) * mm});
            skLineSegment(sketch, "E4921", {"start": v(669.2, -122.66) * mm, "end": v(669.36, -122.8) * mm});
            skLineSegment(sketch, "E4922", {"start": v(669.36, -122.8) * mm, "end": v(669.2, -124.02) * mm});
            skLineSegment(sketch, "E4923", {"start": v(669.2, -124.02) * mm, "end": v(668.26, -127.64) * mm});
            skLineSegment(sketch, "E4924", {"start": v(668.26, -127.64) * mm, "end": v(666.46, -131.9) * mm});
            skLineSegment(sketch, "E4925", {"start": v(666.46, -131.9) * mm, "end": v(664.16, -135.94) * mm});
            skLineSegment(sketch, "E4926", {"start": v(664.16, -135.94) * mm, "end": v(662.2, -139.1) * mm});
            skLineSegment(sketch, "E4927", {"start": v(662.2, -139.1) * mm, "end": v(661.55, -140.15) * mm});
            skLineSegment(sketch, "E4928", {"start": v(661.55, -140.15) * mm, "end": v(660.24, -142.3) * mm});
            skLineSegment(sketch, "E4929", {"start": v(660.24, -142.3) * mm, "end": v(653.43, -152.79) * mm});
            skLineSegment(sketch, "E4930", {"start": v(653.43, -152.79) * mm, "end": v(646.3, -163.1) * mm});
            skLineSegment(sketch, "E4931", {"start": v(646.3, -163.1) * mm, "end": v(644.86, -165.15) * mm});
            skLineSegment(sketch, "E4932", {"start": v(644.86, -165.15) * mm, "end": v(642.2, -168.89) * mm});
            skLineSegment(sketch, "E4933", {"start": v(642.2, -168.89) * mm, "end": v(646.24, -166.7) * mm});
            skLineSegment(sketch, "E4934", {"start": v(646.24, -166.7) * mm, "end": v(646.7, -166.45) * mm});
            skLineSegment(sketch, "E4935", {"start": v(646.7, -166.45) * mm, "end": v(651.3, -164) * mm});
            skLineSegment(sketch, "E4936", {"start": v(651.3, -164) * mm, "end": v(651.77, -163.76) * mm});
            skLineSegment(sketch, "E4937", {"start": v(651.77, -163.76) * mm, "end": v(651.99, -163.63) * mm});
            skLineSegment(sketch, "E4938", {"start": v(651.99, -163.63) * mm, "end": v(652.14, -163.43) * mm});
            skLineSegment(sketch, "E4939", {"start": v(652.14, -163.43) * mm, "end": v(654.85, -159.57) * mm});
            skLineSegment(sketch, "E4940", {"start": v(654.85, -159.57) * mm, "end": v(682.22, -121.16) * mm});
            skLineSegment(sketch, "E4941", {"start": v(682.22, -121.16) * mm, "end": v(684.94, -117.3) * mm});
            skLineSegment(sketch, "E4942", {"start": v(684.94, -117.3) * mm, "end": v(685.6, -117.03) * mm});
            skLineSegment(sketch, "E4943", {"start": v(685.6, -117.03) * mm, "end": v(687.4, -115.77) * mm});
            skLineSegment(sketch, "E4944", {"start": v(687.4, -115.77) * mm, "end": v(689.32, -113.75) * mm});
            skLineSegment(sketch, "E4945", {"start": v(689.32, -113.75) * mm, "end": v(691.06, -111.54) * mm});
            skLineSegment(sketch, "E4946", {"start": v(691.06, -111.54) * mm, "end": v(692.47, -109.92) * mm});
            skLineSegment(sketch, "E4947", {"start": v(692.47, -109.92) * mm, "end": v(693, -109.45) * mm});
            skLineSegment(sketch, "E4948", {"start": v(693, -109.45) * mm, "end": v(693.8, -108.76) * mm});
            skLineSegment(sketch, "E4949", {"start": v(693.8, -108.76) * mm, "end": v(698.02, -105.62) * mm});
            skLineSegment(sketch, "E4950", {"start": v(698.02, -105.62) * mm, "end": v(702.25, -102.46) * mm});
            skLineSegment(sketch, "E4951", {"start": v(702.25, -102.46) * mm, "end": v(703.03, -101.74) * mm});
            skLineSegment(sketch, "E4952", {"start": v(703.03, -101.74) * mm, "end": v(703.7, -101.14) * mm});
            skLineSegment(sketch, "E4953", {"start": v(703.7, -101.14) * mm, "end": v(707.14, -97.96) * mm});
            skLineSegment(sketch, "E4954", {"start": v(707.14, -97.96) * mm, "end": v(710.86, -95.13) * mm});
            skLineSegment(sketch, "E4955", {"start": v(710.86, -95.13) * mm, "end": v(711.67, -94.7) * mm});
            skLineSegment(sketch, "E4956", {"start": v(711.67, -94.7) * mm, "end": v(711.85, -95.71) * mm});
            skLineSegment(sketch, "E4957", {"start": v(711.85, -95.71) * mm, "end": v(711.74, -98.84) * mm});
            skLineSegment(sketch, "E4958", {"start": v(711.74, -98.84) * mm, "end": v(710.7, -102.4) * mm});
            skLineSegment(sketch, "E4959", {"start": v(710.7, -102.4) * mm, "end": v(709.1, -105.86) * mm});
            skLineSegment(sketch, "E4960", {"start": v(709.1, -105.86) * mm, "end": v(707.77, -108.7) * mm});
            skLineSegment(sketch, "E4961", {"start": v(707.77, -108.7) * mm, "end": v(707.4, -109.67) * mm});
            skLineSegment(sketch, "E4962", {"start": v(707.4, -109.67) * mm, "end": v(707.11, -110.42) * mm});
            skLineSegment(sketch, "E4963", {"start": v(707.11, -110.42) * mm, "end": v(705.6, -114.26) * mm});
            skLineSegment(sketch, "E4964", {"start": v(705.6, -114.26) * mm, "end": v(703.86, -117.99) * mm});
            skLineSegment(sketch, "E4965", {"start": v(703.86, -117.99) * mm, "end": v(703.46, -118.69) * mm});
            skLineSegment(sketch, "E4966", {"start": v(703.46, -118.69) * mm, "end": v(702.63, -120.1) * mm});
            skLineSegment(sketch, "E4967", {"start": v(702.63, -120.1) * mm, "end": v(698.86, -127.29) * mm});
            skLineSegment(sketch, "E4968", {"start": v(698.86, -127.29) * mm, "end": v(695.15, -134.52) * mm});
            skLineSegment(sketch, "E4969", {"start": v(695.15, -134.52) * mm, "end": v(694.36, -135.94) * mm});
            skLineSegment(sketch, "E4970", {"start": v(694.36, -135.94) * mm, "end": v(694.2, -136.23) * mm});
            skLineSegment(sketch, "E4971", {"start": v(694.2, -136.23) * mm, "end": v(692.37, -139.03) * mm});
            skLineSegment(sketch, "E4972", {"start": v(692.37, -139.03) * mm, "end": v(692.18, -139.3) * mm});
            skLineSegment(sketch, "E4973", {"start": v(692.18, -139.3) * mm, "end": v(689.58, -143.07) * mm});
            skLineSegment(sketch, "E4974", {"start": v(689.58, -143.07) * mm, "end": v(693.58, -140.85) * mm});
            skLineSegment(sketch, "E4975", {"start": v(693.58, -140.85) * mm, "end": v(694.02, -140.6) * mm});
            skLineSegment(sketch, "E4976", {"start": v(694.02, -140.6) * mm, "end": v(698.41, -138.12) * mm});
            skLineSegment(sketch, "E4977", {"start": v(698.41, -138.12) * mm, "end": v(698.85, -137.86) * mm});
            skLineSegment(sketch, "E4978", {"start": v(698.85, -137.86) * mm, "end": v(699.08, -137.73) * mm});
            skLineSegment(sketch, "E4979", {"start": v(699.08, -137.73) * mm, "end": v(699.21, -137.52) * mm});
            skLineSegment(sketch, "E4980", {"start": v(699.21, -137.52) * mm, "end": v(699.65, -136.83) * mm});
            skLineSegment(sketch, "E4981", {"start": v(699.65, -136.83) * mm, "end": v(703.98, -129.92) * mm});
            skLineSegment(sketch, "E4982", {"start": v(703.98, -129.92) * mm, "end": v(704.42, -129.23) * mm});
            skLineSegment(sketch, "E4983", {"start": v(704.42, -129.23) * mm, "end": v(705.27, -128.82) * mm});
            skLineSegment(sketch, "E4984", {"start": v(705.27, -128.82) * mm, "end": v(707.52, -126.94) * mm});
            skLineSegment(sketch, "E4985", {"start": v(707.52, -126.94) * mm, "end": v(709.89, -123.84) * mm});
            skLineSegment(sketch, "E4986", {"start": v(709.89, -123.84) * mm, "end": v(711.84, -120.37) * mm});
            skLineSegment(sketch, "E4987", {"start": v(711.84, -120.37) * mm, "end": v(713.2, -117.8) * mm});
            skLineSegment(sketch, "E4988", {"start": v(713.2, -117.8) * mm, "end": v(713.68, -116.96) * mm});
            skLineSegment(sketch, "E4989", {"start": v(713.68, -116.96) * mm, "end": v(714.18, -116.1) * mm});
            skLineSegment(sketch, "E4990", {"start": v(714.18, -116.1) * mm, "end": v(717.15, -112.18) * mm});
            skLineSegment(sketch, "E4991", {"start": v(717.15, -112.18) * mm, "end": v(720.16, -108.3) * mm});
            skLineSegment(sketch, "E4992", {"start": v(720.16, -108.3) * mm, "end": v(720.68, -107.46) * mm});
            skLineSegment(sketch, "E4993", {"start": v(720.68, -107.46) * mm, "end": v(721.43, -106.25) * mm});
            skLineSegment(sketch, "E4994", {"start": v(721.43, -106.25) * mm, "end": v(725.07, -100.2) * mm});
            skLineSegment(sketch, "E4995", {"start": v(725.07, -100.2) * mm, "end": v(728.87, -94.24) * mm});
            skLineSegment(sketch, "E4996", {"start": v(728.87, -94.24) * mm, "end": v(729.7, -93.08) * mm});
            skLineSegment(sketch, "E4997", {"start": v(729.7, -93.08) * mm, "end": v(730.36, -92.14) * mm});
            skLineSegment(sketch, "E4998", {"start": v(730.36, -92.14) * mm, "end": v(733.4, -87.27) * mm});
            skLineSegment(sketch, "E4999", {"start": v(733.4, -87.27) * mm, "end": v(736.43, -82.4) * mm});
            skLineSegment(sketch, "E5000", {"start": v(736.43, -82.4) * mm, "end": v(737.09, -81.46) * mm});
            skLineSegment(sketch, "E5001", {"start": v(737.09, -81.46) * mm, "end": v(737.41, -81) * mm});
            skLineSegment(sketch, "E5002", {"start": v(737.41, -81) * mm, "end": v(738.38, -79.6) * mm});
            skLineSegment(sketch, "E5003", {"start": v(738.38, -79.6) * mm, "end": v(739.75, -77.72) * mm});
            skLineSegment(sketch, "E5004", {"start": v(739.75, -77.72) * mm, "end": v(741.21, -75.9) * mm});
            skLineSegment(sketch, "E5005", {"start": v(741.21, -75.9) * mm, "end": v(742.79, -74.22) * mm});
            skLineSegment(sketch, "E5006", {"start": v(742.79, -74.22) * mm, "end": v(744.5, -72.74) * mm});
            skLineSegment(sketch, "E5007", {"start": v(744.5, -72.74) * mm, "end": v(746.38, -71.55) * mm});
            skLineSegment(sketch, "E5008", {"start": v(746.38, -71.55) * mm, "end": v(748.45, -70.72) * mm});
            skLineSegment(sketch, "E5009", {"start": v(748.45, -70.72) * mm, "end": v(750.15, -70.37) * mm});
            skLineSegment(sketch, "E5010", {"start": v(750.15, -70.37) * mm, "end": v(750.73, -70.34) * mm});
            skLineSegment(sketch, "E5011", {"start": v(750.73, -70.34) * mm, "end": v(750.48, -71.68) * mm});
            skLineSegment(sketch, "E5012", {"start": v(750.48, -71.68) * mm, "end": v(749.43, -75.67) * mm});
            skLineSegment(sketch, "E5013", {"start": v(749.43, -75.67) * mm, "end": v(747.57, -80.72) * mm});
            skLineSegment(sketch, "E5014", {"start": v(747.57, -80.72) * mm, "end": v(745.25, -85.6) * mm});
            skLineSegment(sketch, "E5015", {"start": v(745.25, -85.6) * mm, "end": v(743.26, -89.22) * mm});
            skLineSegment(sketch, "E5016", {"start": v(743.26, -89.22) * mm, "end": v(742.56, -90.41) * mm});
            skLineSegment(sketch, "E5017", {"start": v(742.56, -90.41) * mm, "end": v(741.86, -91.6) * mm});
            skLineSegment(sketch, "E5018", {"start": v(741.86, -91.6) * mm, "end": v(739.7, -95.11) * mm});
            skLineSegment(sketch, "E5019", {"start": v(739.7, -95.11) * mm, "end": v(736.82, -99.84) * mm});
            skLineSegment(sketch, "E5020", {"start": v(736.82, -99.84) * mm, "end": v(734.15, -104.66) * mm});
            skLineSegment(sketch, "E5021", {"start": v(734.15, -104.66) * mm, "end": v(732.36, -108.38) * mm});
            skLineSegment(sketch, "E5022", {"start": v(732.36, -108.38) * mm, "end": v(731.85, -109.66) * mm});
            skLineSegment(sketch, "E5023", {"start": v(731.85, -109.66) * mm, "end": v(731.63, -110.23) * mm});
            skLineSegment(sketch, "E5024", {"start": v(731.63, -110.23) * mm, "end": v(730.9, -113.2) * mm});
            skLineSegment(sketch, "E5025", {"start": v(730.9, -113.2) * mm, "end": v(730.12, -116.13) * mm});
            skLineSegment(sketch, "E5026", {"start": v(730.12, -116.13) * mm, "end": v(729.87, -116.67) * mm});
            skLineSegment(sketch, "E5027", {"start": v(729.87, -116.67) * mm, "end": v(729.8, -116.8) * mm});
            skLineSegment(sketch, "E5028", {"start": v(729.8, -116.8) * mm, "end": v(729.06, -118.11) * mm});
            skLineSegment(sketch, "E5029", {"start": v(729.06, -118.11) * mm, "end": v(729, -118.25) * mm});
            skLineSegment(sketch, "E5030", {"start": v(729, -118.25) * mm, "end": v(727.58, -121.3) * mm});
            skLineSegment(sketch, "E5031", {"start": v(727.58, -121.3) * mm, "end": v(730.5, -119.64) * mm});
            skLineSegment(sketch, "E5032", {"start": v(730.5, -119.64) * mm, "end": v(730.9, -119.41) * mm});
            skLineSegment(sketch, "E5033", {"start": v(730.9, -119.41) * mm, "end": v(734.75, -117.08) * mm});
            skLineSegment(sketch, "E5034", {"start": v(734.75, -117.08) * mm, "end": v(735.13, -116.85) * mm});
            skLineSegment(sketch, "E5035", {"start": v(735.13, -116.85) * mm, "end": v(735.4, -116.7) * mm});
            skLineSegment(sketch, "E5036", {"start": v(735.4, -116.7) * mm, "end": v(735.54, -116.4) * mm});
            skLineSegment(sketch, "E5037", {"start": v(735.54, -116.4) * mm, "end": v(736.86, -113.7) * mm});
            skLineSegment(sketch, "E5038", {"start": v(736.86, -113.7) * mm, "end": v(741.05, -105.67) * mm});
            skLineSegment(sketch, "E5039", {"start": v(741.05, -105.67) * mm, "end": v(746.94, -95.15) * mm});
            skLineSegment(sketch, "E5040", {"start": v(746.94, -95.15) * mm, "end": v(753.08, -84.76) * mm});
            skLineSegment(sketch, "E5041", {"start": v(753.08, -84.76) * mm, "end": v(757.76, -77.02) * mm});
            skLineSegment(sketch, "E5042", {"start": v(757.76, -77.02) * mm, "end": v(759.33, -74.44) * mm});
            skLineSegment(sketch, "E5043", {"start": v(759.33, -74.44) * mm, "end": v(759.75, -74.35) * mm});
            skLineSegment(sketch, "E5044", {"start": v(759.75, -74.35) * mm, "end": v(760.97, -73.86) * mm});
            skLineSegment(sketch, "E5045", {"start": v(760.97, -73.86) * mm, "end": v(762.24, -72.98) * mm});
            skLineSegment(sketch, "E5046", {"start": v(762.24, -72.98) * mm, "end": v(763.4, -71.92) * mm});
            skLineSegment(sketch, "E5047", {"start": v(763.4, -71.92) * mm, "end": v(764.35, -71.04) * mm});
            skLineSegment(sketch, "E5048", {"start": v(764.35, -71.04) * mm, "end": v(764.69, -70.77) * mm});
            skLineSegment(sketch, "E5049", {"start": v(764.69, -70.77) * mm, "end": v(765.1, -70.46) * mm});
            skLineSegment(sketch, "E5050", {"start": v(765.1, -70.46) * mm, "end": v(765.1, -46.1) * mm});
            skLineSegment(sketch, "E5051", {"start": v(765.1, -46.1) * mm, "end": v(764.16, -45.99) * mm});
            skLineSegment(sketch, "E5052", {"start": v(764.16, -45.99) * mm, "end": v(763.56, -45.9) * mm});
            skLineSegment(sketch, "E5053", {"start": v(763.56, -45.9) * mm, "end": v(760.77, -46.13) * mm});
            skLineSegment(sketch, "E5054", {"start": v(760.77, -46.13) * mm, "end": v(758.3, -47.35) * mm});
            skLineSegment(sketch, "E5055", {"start": v(758.3, -47.35) * mm, "end": v(757.84, -47.78) * mm});
            skLineSegment(sketch, "E5056", {"start": v(757.84, -47.78) * mm, "end": v(757.57, -48.03) * mm});
            skLineSegment(sketch, "E5057", {"start": v(757.57, -48.03) * mm, "end": v(756.37, -49.45) * mm});
            skLineSegment(sketch, "E5058", {"start": v(756.37, -49.45) * mm, "end": v(755.2, -50.89) * mm});
            skLineSegment(sketch, "E5059", {"start": v(755.2, -50.89) * mm, "end": v(754.95, -51.15) * mm});
            skLineSegment(sketch, "E5060", {"start": v(754.95, -51.15) * mm, "end": v(754.83, -51.2) * mm});
            skLineSegment(sketch, "E5061", {"start": v(754.83, -51.2) * mm, "end": v(754.45, -51.28) * mm});
            skLineSegment(sketch, "E5062", {"start": v(754.45, -51.28) * mm, "end": v(753.98, -51.36) * mm});
            skLineSegment(sketch, "E5063", {"start": v(753.98, -51.36) * mm, "end": v(753.49, -51.5) * mm});
            skLineSegment(sketch, "E5064", {"start": v(753.49, -51.5) * mm, "end": v(753.06, -51.77) * mm});
            skLineSegment(sketch, "E5065", {"start": v(753.06, -51.77) * mm, "end": v(752.94, -51.88) * mm});
            skLineSegment(sketch, "E5066", {"start": v(752.94, -51.88) * mm, "end": v(752.54, -52.22) * mm});
            skLineSegment(sketch, "E5067", {"start": v(752.54, -52.22) * mm, "end": v(750.63, -54.05) * mm});
            skLineSegment(sketch, "E5068", {"start": v(750.63, -54.05) * mm, "end": v(748.78, -55.95) * mm});
            skLineSegment(sketch, "E5069", {"start": v(748.78, -55.95) * mm, "end": v(748.4, -56.33) * mm});
            skLineSegment(sketch, "E5070", {"start": v(748.4, -56.33) * mm, "end": v(748, -56.77) * mm});
            skLineSegment(sketch, "E5071", {"start": v(748, -56.77) * mm, "end": v(745.76, -59.12) * mm});
            skLineSegment(sketch, "E5072", {"start": v(745.76, -59.12) * mm, "end": v(743.4, -61.34) * mm});
            skLineSegment(sketch, "E5073", {"start": v(743.4, -61.34) * mm, "end": v(742.93, -61.72) * mm});
            skLineSegment(sketch, "E5074", {"start": v(742.93, -61.72) * mm, "end": v(741.87, -62.53) * mm});
            skLineSegment(sketch, "E5075", {"start": v(741.87, -62.53) * mm, "end": v(738.63, -64.86) * mm});
            skLineSegment(sketch, "E5076", {"start": v(738.63, -64.86) * mm, "end": v(734.23, -67.92) * mm});
            skLineSegment(sketch, "E5077", {"start": v(734.23, -67.92) * mm, "end": v(729.93, -71.1) * mm});
            skLineSegment(sketch, "E5078", {"start": v(729.93, -71.1) * mm, "end": v(726.88, -73.68) * mm});
            skLineSegment(sketch, "E5079", {"start": v(726.88, -73.68) * mm, "end": v(725.93, -74.6) * mm});
            skLineSegment(sketch, "E5080", {"start": v(725.93, -74.6) * mm, "end": v(724.46, -74.98) * mm});
            skLineSegment(sketch, "E5081", {"start": v(724.46, -74.98) * mm, "end": v(720.19, -76.67) * mm});
            skLineSegment(sketch, "E5082", {"start": v(720.19, -76.67) * mm, "end": v(714.95, -79.66) * mm});
            skLineSegment(sketch, "E5083", {"start": v(714.95, -79.66) * mm, "end": v(710.13, -83.34) * mm});
            skLineSegment(sketch, "E5084", {"start": v(710.13, -83.34) * mm, "end": v(706.72, -86.4) * mm});
            skLineSegment(sketch, "E5085", {"start": v(706.72, -86.4) * mm, "end": v(705.63, -87.47) * mm});
            skLineSegment(sketch, "E5086", {"start": v(705.63, -87.47) * mm, "end": v(705.39, -87.7) * mm});
            skLineSegment(sketch, "E5087", {"start": v(705.39, -87.7) * mm, "end": v(704.75, -88.5) * mm});
            skLineSegment(sketch, "E5088", {"start": v(704.75, -88.5) * mm, "end": v(703.91, -89.63) * mm});
            skLineSegment(sketch, "E5089", {"start": v(703.91, -89.63) * mm, "end": v(703.05, -90.71) * mm});
            skLineSegment(sketch, "E5090", {"start": v(703.05, -90.71) * mm, "end": v(702.35, -91.39) * mm});
            skLineSegment(sketch, "E5091", {"start": v(702.35, -91.39) * mm, "end": v(702.09, -91.56) * mm});
            skLineSegment(sketch, "E5092", {"start": v(702.09, -91.56) * mm, "end": v(702.07, -91.58) * mm});
            skLineSegment(sketch, "E5093", {"start": v(702.07, -91.58) * mm, "end": v(702.05, -91.59) * mm});
            skLineSegment(sketch, "E5094", {"start": v(702.05, -91.59) * mm, "end": v(701.87, -91.7) * mm});
            skLineSegment(sketch, "E5095", {"start": v(701.87, -91.7) * mm, "end": v(701.27, -91.98) * mm});
            skLineSegment(sketch, "E5096", {"start": v(701.27, -91.98) * mm, "end": v(700.35, -92.26) * mm});
            skLineSegment(sketch, "E5097", {"start": v(700.35, -92.26) * mm, "end": v(699.4, -92.55) * mm});
            skLineSegment(sketch, "E5098", {"start": v(699.4, -92.55) * mm, "end": v(698.7, -92.83) * mm});
            skLineSegment(sketch, "E5099", {"start": v(698.7, -92.83) * mm, "end": v(698.49, -92.95) * mm});
            skLineSegment(sketch, "E5100", {"start": v(698.49, -92.95) * mm, "end": v(697.83, -93.33) * mm});
            skLineSegment(sketch, "E5101", {"start": v(697.83, -93.33) * mm, "end": v(694.78, -95.58) * mm});
            skLineSegment(sketch, "E5102", {"start": v(694.78, -95.58) * mm, "end": v(691.73, -97.86) * mm});
            skLineSegment(sketch, "E5103", {"start": v(691.73, -97.86) * mm, "end": v(691.08, -98.25) * mm});
            skLineSegment(sketch, "E5104", {"start": v(691.08, -98.25) * mm, "end": v(690.82, -98.4) * mm});
            skLineSegment(sketch, "E5105", {"start": v(690.82, -98.4) * mm, "end": v(690.02, -98.8) * mm});
            skLineSegment(sketch, "E5106", {"start": v(690.02, -98.8) * mm, "end": v(688.97, -99.25) * mm});
            skLineSegment(sketch, "E5107", {"start": v(688.97, -99.25) * mm, "end": v(687.94, -99.77) * mm});
            skLineSegment(sketch, "E5108", {"start": v(687.94, -99.77) * mm, "end": v(687.17, -100.28) * mm});
            skLineSegment(sketch, "E5109", {"start": v(687.17, -100.28) * mm, "end": v(686.94, -100.48) * mm});
            skLineSegment(sketch, "E5110", {"start": v(686.94, -100.48) * mm, "end": v(686.72, -100.65) * mm});
            skLineSegment(sketch, "E5111", {"start": v(686.72, -100.65) * mm, "end": v(686.13, -101.23) * mm});
            skLineSegment(sketch, "E5112", {"start": v(686.13, -101.23) * mm, "end": v(685.35, -102.09) * mm});
            skLineSegment(sketch, "E5113", {"start": v(685.35, -102.09) * mm, "end": v(684.58, -102.89) * mm});
            skLineSegment(sketch, "E5114", {"start": v(684.58, -102.89) * mm, "end": v(683.99, -103.36) * mm});
            skLineSegment(sketch, "E5115", {"start": v(683.99, -103.36) * mm, "end": v(683.77, -103.48) * mm});
            skLineSegment(sketch, "E5116", {"start": v(683.77, -103.48) * mm, "end": v(683.49, -103.62) * mm});
            skLineSegment(sketch, "E5117", {"start": v(683.49, -103.62) * mm, "end": v(682.6, -103.9) * mm});
            skLineSegment(sketch, "E5118", {"start": v(682.6, -103.9) * mm, "end": v(681.32, -104.16) * mm});
            skLineSegment(sketch, "E5119", {"start": v(681.32, -104.16) * mm, "end": v(680.02, -104.44) * mm});
            skLineSegment(sketch, "E5120", {"start": v(680.02, -104.44) * mm, "end": v(679.06, -104.75) * mm});
            skLineSegment(sketch, "E5121", {"start": v(679.06, -104.75) * mm, "end": v(678.77, -104.9) * mm});
            skLineSegment(sketch, "E5122", {"start": v(678.77, -104.9) * mm, "end": v(677.81, -105.36) * mm});
            skLineSegment(sketch, "E5123", {"start": v(677.81, -105.36) * mm, "end": v(673.34, -108.18) * mm});
            skLineSegment(sketch, "E5124", {"start": v(673.34, -108.18) * mm, "end": v(668.93, -111.08) * mm});
            skLineSegment(sketch, "E5125", {"start": v(668.93, -111.08) * mm, "end": v(668, -111.58) * mm});
            skLineSegment(sketch, "E5126", {"start": v(668, -111.58) * mm, "end": v(667.1, -112.07) * mm});
            skLineSegment(sketch, "E5127", {"start": v(667.1, -112.07) * mm, "end": v(657.86, -116.48) * mm});
            skLineSegment(sketch, "E5128", {"start": v(657.86, -116.48) * mm, "end": v(656.94, -116.92) * mm});
            skLineSegment(sketch, "E5129", {"start": v(656.94, -116.92) * mm, "end": v(656.2, -116.34) * mm});
            skLineSegment(sketch, "E5130", {"start": v(656.2, -116.34) * mm, "end": v(653.58, -115.12) * mm});
            skLineSegment(sketch, "E5131", {"start": v(653.58, -115.12) * mm, "end": v(649.8, -114.28) * mm});
            skLineSegment(sketch, "E5132", {"start": v(649.8, -114.28) * mm, "end": v(645.86, -114.17) * mm});
            skLineSegment(sketch, "E5133", {"start": v(645.86, -114.17) * mm, "end": v(642.99, -114.42) * mm});
            skLineSegment(sketch, "E5134", {"start": v(642.99, -114.42) * mm, "end": v(642.04, -114.57) * mm});
            skLineSegment(sketch, "E5135", {"start": v(642.04, -114.57) * mm, "end": v(641.71, -114.26) * mm});
            skLineSegment(sketch, "E5136", {"start": v(641.71, -114.26) * mm, "end": v(640.02, -112.77) * mm});
            skLineSegment(sketch, "E5137", {"start": v(640.02, -112.77) * mm, "end": v(638.45, -111.17) * mm});
            skLineSegment(sketch, "E5138", {"start": v(638.45, -111.17) * mm, "end": v(638.17, -110.81) * mm});
            skLineSegment(sketch, "E5139", {"start": v(638.17, -110.81) * mm, "end": v(638, -110.6) * mm});
            skLineSegment(sketch, "E5140", {"start": v(638, -110.6) * mm, "end": v(637.74, -110.48) * mm});
            skLineSegment(sketch, "E5141", {"start": v(637.74, -110.48) * mm, "end": v(636.42, -109.94) * mm});
            skLineSegment(sketch, "E5142", {"start": v(636.42, -109.94) * mm, "end": v(632.4, -108.52) * mm});
            skLineSegment(sketch, "E5143", {"start": v(632.4, -108.52) * mm, "end": v(626.84, -106.63) * mm});
            skLineSegment(sketch, "E5144", {"start": v(626.84, -106.63) * mm, "end": v(621.42, -104.49) * mm});
            skLineSegment(sketch, "E5145", {"start": v(621.42, -104.49) * mm, "end": v(617.64, -102.57) * mm});
            skLineSegment(sketch, "E5146", {"start": v(617.64, -102.57) * mm, "end": v(616.48, -101.79) * mm});
            skLineSegment(sketch, "E5147", {"start": v(616.48, -101.79) * mm, "end": v(616.28, -101.66) * mm});
            skLineSegment(sketch, "E5148", {"start": v(616.28, -101.66) * mm, "end": v(616.05, -101.62) * mm});
            skLineSegment(sketch, "E5149", {"start": v(616.05, -101.62) * mm, "end": v(615.84, -101.59) * mm});
            skLineSegment(sketch, "E5150", {"start": v(615.84, -101.59) * mm, "end": v(614.82, -101.55) * mm});
            skLineSegment(sketch, "E5151", {"start": v(614.82, -101.55) * mm, "end": v(613.82, -101.63) * mm});
            skLineSegment(sketch, "E5152", {"start": v(613.82, -101.63) * mm, "end": v(613.6, -101.66) * mm});
            skLineSegment(sketch, "E5153", {"start": v(613.6, -101.66) * mm, "end": v(614.47, -100.98) * mm});
            skLineSegment(sketch, "E5154", {"start": v(614.47, -100.98) * mm, "end": v(616.7, -98.52) * mm});
            skLineSegment(sketch, "E5155", {"start": v(616.7, -98.52) * mm, "end": v(619.28, -94.95) * mm});
            skLineSegment(sketch, "E5156", {"start": v(619.28, -94.95) * mm, "end": v(621.84, -91.43) * mm});
            skLineSegment(sketch, "E5157", {"start": v(621.84, -91.43) * mm, "end": v(624.06, -89.05) * mm});
            skLineSegment(sketch, "E5158", {"start": v(624.06, -89.05) * mm, "end": v(624.91, -88.41) * mm});
            skLineSegment(sketch, "E5159", {"start": v(624.91, -88.41) * mm, "end": v(625.39, -88.05) * mm});
            skLineSegment(sketch, "E5160", {"start": v(625.39, -88.05) * mm, "end": v(625.33, -87.45) * mm});
            skLineSegment(sketch, "E5161", {"start": v(625.33, -87.45) * mm, "end": v(625.25, -86.49) * mm});
            skLineSegment(sketch, "E5162", {"start": v(625.25, -86.49) * mm, "end": v(625.2, -83.59) * mm});
            skLineSegment(sketch, "E5163", {"start": v(625.2, -83.59) * mm, "end": v(625.25, -79.69) * mm});
            skLineSegment(sketch, "E5164", {"start": v(625.25, -79.69) * mm, "end": v(625.19, -75.79) * mm});
            skLineSegment(sketch, "E5165", {"start": v(625.19, -75.79) * mm, "end": v(624.91, -72.89) * mm});
            skLineSegment(sketch, "E5166", {"start": v(624.91, -72.89) * mm, "end": v(624.73, -71.94) * mm});
            skLineSegment(sketch, "E5167", {"start": v(624.73, -71.94) * mm, "end": v(625.35, -71.11) * mm});
            skLineSegment(sketch, "E5168", {"start": v(625.35, -71.11) * mm, "end": v(627.14, -68.55) * mm});
            skLineSegment(sketch, "E5169", {"start": v(627.14, -68.55) * mm, "end": v(629.64, -65.07) * mm});
            skLineSegment(sketch, "E5170", {"start": v(629.64, -65.07) * mm, "end": v(632.4, -61.85) * mm});
            skLineSegment(sketch, "E5171", {"start": v(632.4, -61.85) * mm, "end": v(634.7, -59.78) * mm});
            skLineSegment(sketch, "E5172", {"start": v(634.7, -59.78) * mm, "end": v(635.57, -59.24) * mm});
            skLineSegment(sketch, "E5173", {"start": v(635.57, -59.24) * mm, "end": v(635.75, -59.12) * mm});
            skLineSegment(sketch, "E5174", {"start": v(635.75, -59.12) * mm, "end": v(636.87, -58.57) * mm});
            skLineSegment(sketch, "E5175", {"start": v(636.87, -58.57) * mm, "end": v(638.02, -58.09) * mm});
            skLineSegment(sketch, "E5176", {"start": v(638.02, -58.09) * mm, "end": v(638.22, -58) * mm});
            skLineSegment(sketch, "E5177", {"start": v(638.22, -58) * mm, "end": v(638.57, -57.86) * mm});
            skLineSegment(sketch, "E5178", {"start": v(638.57, -57.86) * mm, "end": v(642.05, -56.38) * mm});
            skLineSegment(sketch, "E5179", {"start": v(642.05, -56.38) * mm, "end": v(642.4, -56.22) * mm});
            skLineSegment(sketch, "E5180", {"start": v(642.4, -56.22) * mm, "end": v(642.92, -55.98) * mm});
            skLineSegment(sketch, "E5181", {"start": v(642.92, -55.98) * mm, "end": v(644.5, -55.2) * mm});
            skLineSegment(sketch, "E5182", {"start": v(644.5, -55.2) * mm, "end": v(646.86, -53.78) * mm});
            skLineSegment(sketch, "E5183", {"start": v(646.86, -53.78) * mm, "end": v(648.75, -51.97) * mm});
            skLineSegment(sketch, "E5184", {"start": v(648.75, -51.97) * mm, "end": v(649.5, -50.35) * mm});
            skLineSegment(sketch, "E5185", {"start": v(649.5, -50.35) * mm, "end": v(649.47, -49.82) * mm});
            skLineSegment(sketch, "E5186", {"start": v(649.47, -49.82) * mm, "end": v(649.46, -49.62) * mm});
            skLineSegment(sketch, "E5187", {"start": v(649.46, -49.62) * mm, "end": v(649.27, -49.02) * mm});
            skLineSegment(sketch, "E5188", {"start": v(649.27, -49.02) * mm, "end": v(648.82, -48.22) * mm});
            skLineSegment(sketch, "E5189", {"start": v(648.82, -48.22) * mm, "end": v(648.16, -47.45) * mm});
            skLineSegment(sketch, "E5190", {"start": v(648.16, -47.45) * mm, "end": v(647.35, -46.73) * mm});
            skLineSegment(sketch, "E5191", {"start": v(647.35, -46.73) * mm, "end": v(646.47, -46.09) * mm});
            skLineSegment(sketch, "E5192", {"start": v(646.47, -46.09) * mm, "end": v(645.56, -45.56) * mm});
            skLineSegment(sketch, "E5193", {"start": v(645.56, -45.56) * mm, "end": v(644.69, -45.17) * mm});
            skLineSegment(sketch, "E5194", {"start": v(644.69, -45.17) * mm, "end": v(644.1, -44.98) * mm});
            skLineSegment(sketch, "E5195", {"start": v(644.1, -44.98) * mm, "end": v(643.91, -44.94) * mm});
            skLineSegment(sketch, "E5196", {"start": v(643.91, -44.94) * mm, "end": v(643.37, -44.84) * mm});
            skLineSegment(sketch, "E5197", {"start": v(643.37, -44.84) * mm, "end": v(641.67, -44.88) * mm});
            skLineSegment(sketch, "E5198", {"start": v(641.67, -44.88) * mm, "end": v(639.65, -45.36) * mm});
            skLineSegment(sketch, "E5199", {"start": v(639.65, -45.36) * mm, "end": v(637.68, -45.98) * mm});
            skLineSegment(sketch, "E5200", {"start": v(637.68, -45.98) * mm, "end": v(636.13, -46.32) * mm});
            skLineSegment(sketch, "E5201", {"start": v(636.13, -46.32) * mm, "end": v(635.61, -46.35) * mm});
            skLineSegment(sketch, "E5202", {"start": v(635.61, -46.35) * mm, "end": v(634.82, -46.38) * mm});
            skLineSegment(sketch, "E5203", {"start": v(634.82, -46.38) * mm, "end": v(630.94, -46.04) * mm});
            skLineSegment(sketch, "E5204", {"start": v(630.94, -46.04) * mm, "end": v(627.1, -45.95) * mm});
            skLineSegment(sketch, "E5205", {"start": v(627.1, -45.95) * mm, "end": v(626.31, -46.11) * mm});
            skLineSegment(sketch, "E5206", {"start": v(626.31, -46.11) * mm, "end": v(626.18, -45.66) * mm});
            skLineSegment(sketch, "E5207", {"start": v(626.18, -45.66) * mm, "end": v(625.63, -43.35) * mm});
            skLineSegment(sketch, "E5208", {"start": v(625.63, -43.35) * mm, "end": v(625, -41.07) * mm});
            skLineSegment(sketch, "E5209", {"start": v(625, -41.07) * mm, "end": v(624.83, -40.62) * mm});
            skLineSegment(sketch, "E5210", {"start": v(624.83, -40.62) * mm, "end": v(625.23, -40.18) * mm});
            skLineSegment(sketch, "E5211", {"start": v(625.23, -40.18) * mm, "end": v(626.76, -37.58) * mm});
            skLineSegment(sketch, "E5212", {"start": v(626.76, -37.58) * mm, "end": v(627.97, -34.8) * mm});
            skLineSegment(sketch, "E5213", {"start": v(627.97, -34.8) * mm, "end": v(628.21, -34.27) * mm});
            skLineSegment(sketch, "E5214", {"start": v(628.21, -34.27) * mm, "end": v(628.43, -34.02) * mm});
            skLineSegment(sketch, "E5215", {"start": v(628.43, -34.02) * mm, "end": v(629.2, -33.4) * mm});
            skLineSegment(sketch, "E5216", {"start": v(629.2, -33.4) * mm, "end": v(630.09, -32.72) * mm});
            skLineSegment(sketch, "E5217", {"start": v(630.09, -32.72) * mm, "end": v(630.83, -31.84) * mm});
            skLineSegment(sketch, "E5218", {"start": v(630.83, -31.84) * mm, "end": v(631.27, -30.72) * mm});
            skLineSegment(sketch, "E5219", {"start": v(631.27, -30.72) * mm, "end": v(631.35, -30.33) * mm});
            skLineSegment(sketch, "E5220", {"start": v(631.35, -30.33) * mm, "end": v(631.4, -30.08) * mm});
            skLineSegment(sketch, "E5221", {"start": v(631.4, -30.08) * mm, "end": v(631.4, -29.28) * mm});
            skLineSegment(sketch, "E5222", {"start": v(631.4, -29.28) * mm, "end": v(631.24, -27.92) * mm});
            skLineSegment(sketch, "E5223", {"start": v(631.24, -27.92) * mm, "end": v(630.9, -26.35) * mm});
            skLineSegment(sketch, "E5224", {"start": v(630.9, -26.35) * mm, "end": v(630.45, -24.68) * mm});
            skLineSegment(sketch, "E5225", {"start": v(630.45, -24.68) * mm, "end": v(629.9, -23.04) * mm});
            skLineSegment(sketch, "E5226", {"start": v(629.9, -23.04) * mm, "end": v(629.31, -21.52) * mm});
            skLineSegment(sketch, "E5227", {"start": v(629.31, -21.52) * mm, "end": v(628.72, -20.25) * mm});
            skLineSegment(sketch, "E5228", {"start": v(628.72, -20.25) * mm, "end": v(628.33, -19.54) * mm});
            skLineSegment(sketch, "E5229", {"start": v(628.33, -19.54) * mm, "end": v(628.17, -19.32) * mm});
            skLineSegment(sketch, "E5230", {"start": v(628.17, -19.32) * mm, "end": v(627.93, -19) * mm});
            skLineSegment(sketch, "E5231", {"start": v(627.93, -19) * mm, "end": v(626.5, -17.73) * mm});
            skLineSegment(sketch, "E5232", {"start": v(626.5, -17.73) * mm, "end": v(624.81, -16.8) * mm});
            skLineSegment(sketch, "E5233", {"start": v(624.81, -16.8) * mm, "end": v(624.45, -16.66) * mm});
            skLineSegment(sketch, "E5234", {"start": v(624.45, -16.66) * mm, "end": v(624.04, -16.5) * mm});
            skLineSegment(sketch, "E5235", {"start": v(624.04, -16.5) * mm, "end": v(621.83, -15.88) * mm});
            skLineSegment(sketch, "E5236", {"start": v(621.83, -15.88) * mm, "end": v(619.71, -15.26) * mm});
            skLineSegment(sketch, "E5237", {"start": v(619.71, -15.26) * mm, "end": v(619.34, -15.1) * mm});
            skLineSegment(sketch, "E5238", {"start": v(619.34, -15.1) * mm, "end": v(618.63, -14.78) * mm});
            skLineSegment(sketch, "E5239", {"start": v(618.63, -14.78) * mm, "end": v(618.11, -15.36) * mm});
            skLineSegment(sketch, "E5240", {"start": v(618.11, -15.36) * mm, "end": v(617.77, -15.75) * mm});
            skLineSegment(sketch, "E5241", {"start": v(617.77, -15.75) * mm, "end": v(616.86, -17) * mm});
            skLineSegment(sketch, "E5242", {"start": v(616.86, -17) * mm, "end": v(615.62, -18.88) * mm});
            skLineSegment(sketch, "E5243", {"start": v(615.62, -18.88) * mm, "end": v(614.35, -20.65) * mm});
            skLineSegment(sketch, "E5244", {"start": v(614.35, -20.65) * mm, "end": v(613.38, -21.72) * mm});
            skLineSegment(sketch, "E5245", {"start": v(613.38, -21.72) * mm, "end": v(613, -22) * mm});
            skLineSegment(sketch, "E5246", {"start": v(613, -22) * mm, "end": v(612.74, -22.18) * mm});
            skLineSegment(sketch, "E5247", {"start": v(612.74, -22.18) * mm, "end": v(611.37, -22.7) * mm});
            skLineSegment(sketch, "E5248", {"start": v(611.37, -22.7) * mm, "end": v(609.9, -22.8) * mm});
            skLineSegment(sketch, "E5249", {"start": v(609.9, -22.8) * mm, "end": v(609.6, -22.76) * mm});
            skLineSegment(sketch, "E5250", {"start": v(609.6, -22.76) * mm, "end": v(609.39, -22.74) * mm});
            skLineSegment(sketch, "E5251", {"start": v(609.39, -22.74) * mm, "end": v(608.76, -22.56) * mm});
            skLineSegment(sketch, "E5252", {"start": v(608.76, -22.56) * mm, "end": v(608.02, -22.16) * mm});
            skLineSegment(sketch, "E5253", {"start": v(608.02, -22.16) * mm, "end": v(607.37, -21.62) * mm});
            skLineSegment(sketch, "E5254", {"start": v(607.37, -21.62) * mm, "end": v(606.77, -20.97) * mm});
            skLineSegment(sketch, "E5255", {"start": v(606.77, -20.97) * mm, "end": v(606.22, -20.25) * mm});
            skLineSegment(sketch, "E5256", {"start": v(606.22, -20.25) * mm, "end": v(605.68, -19.51) * mm});
            skLineSegment(sketch, "E5257", {"start": v(605.68, -19.51) * mm, "end": v(605.15, -18.8) * mm});
            skLineSegment(sketch, "E5258", {"start": v(605.15, -18.8) * mm, "end": v(604.73, -18.3) * mm});
            skLineSegment(sketch, "E5259", {"start": v(604.73, -18.3) * mm, "end": v(604.59, -18.15) * mm});
            skLineSegment(sketch, "E5260", {"start": v(604.59, -18.15) * mm, "end": v(604.4, -17.97) * mm});
            skLineSegment(sketch, "E5261", {"start": v(604.4, -17.97) * mm, "end": v(603.8, -17.5) * mm});
            skLineSegment(sketch, "E5262", {"start": v(603.8, -17.5) * mm, "end": v(602.9, -16.9) * mm});
            skLineSegment(sketch, "E5263", {"start": v(602.9, -16.9) * mm, "end": v(602.04, -16.29) * mm});
            skLineSegment(sketch, "E5264", {"start": v(602.04, -16.29) * mm, "end": v(601.49, -15.8) * mm});
            skLineSegment(sketch, "E5265", {"start": v(601.49, -15.8) * mm, "end": v(601.33, -15.62) * mm});
            skLineSegment(sketch, "E5266", {"start": v(601.33, -15.62) * mm, "end": v(601.5, -15.29) * mm});
            skLineSegment(sketch, "E5267", {"start": v(601.5, -15.29) * mm, "end": v(602.12, -14.32) * mm});
            skLineSegment(sketch, "E5268", {"start": v(602.12, -14.32) * mm, "end": v(603.07, -13.04) * mm});
            skLineSegment(sketch, "E5269", {"start": v(603.07, -13.04) * mm, "end": v(604.07, -11.8) * mm});
            skLineSegment(sketch, "E5270", {"start": v(604.07, -11.8) * mm, "end": v(604.8, -10.95) * mm});
            skLineSegment(sketch, "E5271", {"start": v(604.8, -10.95) * mm, "end": v(605.03, -10.66) * mm});
            skLineSegment(sketch, "E5272", {"start": v(605.03, -10.66) * mm, "end": v(605.4, -10.21) * mm});
            skLineSegment(sketch, "E5273", {"start": v(605.4, -10.21) * mm, "end": v(606.5, -8.83) * mm});
            skLineSegment(sketch, "E5274", {"start": v(606.5, -8.83) * mm, "end": v(607.84, -6.83) * mm});
            skLineSegment(sketch, "E5275", {"start": v(607.84, -6.83) * mm, "end": v(608.83, -4.68) * mm});
            skLineSegment(sketch, "E5276", {"start": v(608.83, -4.68) * mm, "end": v(609.24, -2.95) * mm});
            skLineSegment(sketch, "E5277", {"start": v(609.24, -2.95) * mm, "end": v(609.25, -2.37) * mm});
            skLineSegment(sketch, "E5278", {"start": v(609.25, -2.37) * mm, "end": v(609.27, -1.8) * mm});
            skLineSegment(sketch, "E5279", {"start": v(609.27, -1.8) * mm, "end": v(608.82, -0.06) * mm});
            skLineSegment(sketch, "E5280", {"start": v(608.82, -0.06) * mm, "end": v(607.6, 1.61) * mm});
            skLineSegment(sketch, "E5281", {"start": v(607.6, 1.61) * mm, "end": v(605.96, 3) * mm});
            skLineSegment(sketch, "E5282", {"start": v(605.96, 3) * mm, "end": v(604.63, 4.04) * mm});
            skLineSegment(sketch, "E5283", {"start": v(604.63, 4.04) * mm, "end": v(604.22, 4.42) * mm});
            skLineSegment(sketch, "E5284", {"start": v(604.22, 4.42) * mm, "end": v(603.98, 4.65) * mm});
            skLineSegment(sketch, "E5285", {"start": v(603.98, 4.65) * mm, "end": v(603.24, 5.31) * mm});
            skLineSegment(sketch, "E5286", {"start": v(603.24, 5.31) * mm, "end": v(602.16, 6.32) * mm});
            skLineSegment(sketch, "E5287", {"start": v(602.16, 6.32) * mm, "end": v(601.15, 7.37) * mm});
            skLineSegment(sketch, "E5288", {"start": v(601.15, 7.37) * mm, "end": v(600.55, 8.13) * mm});
            skLineSegment(sketch, "E5289", {"start": v(600.55, 8.13) * mm, "end": v(600.38, 8.4) * mm});
            skLineSegment(sketch, "E5290", {"start": v(600.38, 8.4) * mm, "end": v(599.96, 9.08) * mm});
            skLineSegment(sketch, "E5291", {"start": v(599.96, 9.08) * mm, "end": v(598.85, 11.2) * mm});
            skLineSegment(sketch, "E5292", {"start": v(598.85, 11.2) * mm, "end": v(597.3, 14.2) * mm});
            skLineSegment(sketch, "E5293", {"start": v(597.3, 14.2) * mm, "end": v(595.54, 17.02) * mm});
            skLineSegment(sketch, "E5294", {"start": v(595.54, 17.02) * mm, "end": v(594.02, 18.82) * mm});
            skLineSegment(sketch, "E5295", {"start": v(594.02, 18.82) * mm, "end": v(593.41, 19.29) * mm});
            skLineSegment(sketch, "E5296", {"start": v(593.41, 19.29) * mm, "end": v(593.19, 19.46) * mm});
            skLineSegment(sketch, "E5297", {"start": v(593.19, 19.46) * mm, "end": v(592.4, 19.85) * mm});
            skLineSegment(sketch, "E5298", {"start": v(592.4, 19.85) * mm, "end": v(591.3, 20.2) * mm});
            skLineSegment(sketch, "E5299", {"start": v(591.3, 20.2) * mm, "end": v(590.27, 20.52) * mm});
            skLineSegment(sketch, "E5300", {"start": v(590.27, 20.52) * mm, "end": v(589.64, 20.8) * mm});
            skLineSegment(sketch, "E5301", {"start": v(589.64, 20.8) * mm, "end": v(589.47, 20.94) * mm});
            skLineSegment(sketch, "E5302", {"start": v(589.47, 20.94) * mm, "end": v(589.14, 21.3) * mm});
            skLineSegment(sketch, "E5303", {"start": v(589.14, 21.3) * mm, "end": v(588.34, 22.53) * mm});
            skLineSegment(sketch, "E5304", {"start": v(588.34, 22.53) * mm, "end": v(587.44, 24.24) * mm});
            skLineSegment(sketch, "E5305", {"start": v(587.44, 24.24) * mm, "end": v(586.47, 25.98) * mm});
            skLineSegment(sketch, "E5306", {"start": v(586.47, 25.98) * mm, "end": v(585.5, 27.28) * mm});
            skLineSegment(sketch, "E5307", {"start": v(585.5, 27.28) * mm, "end": v(585.12, 27.65) * mm});
            skLineSegment(sketch, "E5308", {"start": v(585.12, 27.65) * mm, "end": v(584.74, 28.02) * mm});
            skLineSegment(sketch, "E5309", {"start": v(584.74, 28.02) * mm, "end": v(583.39, 28.92) * mm});
            skLineSegment(sketch, "E5310", {"start": v(583.39, 28.92) * mm, "end": v(581.44, 29.93) * mm});
            skLineSegment(sketch, "E5311", {"start": v(581.44, 29.93) * mm, "end": v(579.61, 31) * mm});
            skLineSegment(sketch, "E5312", {"start": v(579.61, 31) * mm, "end": v(578.5, 31.97) * mm});
            skLineSegment(sketch, "E5313", {"start": v(578.5, 31.97) * mm, "end": v(578.25, 32.37) * mm});
            skLineSegment(sketch, "E5314", {"start": v(578.25, 32.37) * mm, "end": v(577.84, 33.02) * mm});
            skLineSegment(sketch, "E5315", {"start": v(577.84, 33.02) * mm, "end": v(577, 35.18) * mm});
            skLineSegment(sketch, "E5316", {"start": v(577, 35.18) * mm, "end": v(576.2, 38.23) * mm});
            skLineSegment(sketch, "E5317", {"start": v(576.2, 38.23) * mm, "end": v(575.32, 41.27) * mm});
            skLineSegment(sketch, "E5318", {"start": v(575.32, 41.27) * mm, "end": v(574.32, 43.46) * mm});
            skLineSegment(sketch, "E5319", {"start": v(574.32, 43.46) * mm, "end": v(573.86, 44.09) * mm});
            skLineSegment(sketch, "E5320", {"start": v(573.86, 44.09) * mm, "end": v(573.64, 44.38) * mm});
            skLineSegment(sketch, "E5321", {"start": v(573.64, 44.38) * mm, "end": v(572.83, 45.12) * mm});
            skLineSegment(sketch, "E5322", {"start": v(572.83, 45.12) * mm, "end": v(571.66, 45.94) * mm});
            skLineSegment(sketch, "E5323", {"start": v(571.66, 45.94) * mm, "end": v(570.5, 46.73) * mm});
            skLineSegment(sketch, "E5324", {"start": v(570.5, 46.73) * mm, "end": v(569.68, 47.4) * mm});
            skLineSegment(sketch, "E5325", {"start": v(569.68, 47.4) * mm, "end": v(569.45, 47.65) * mm});
            skLineSegment(sketch, "E5326", {"start": v(569.45, 47.65) * mm, "end": v(569.27, 47.85) * mm});
            skLineSegment(sketch, "E5327", {"start": v(569.27, 47.85) * mm, "end": v(568.8, 48.51) * mm});
            skLineSegment(sketch, "E5328", {"start": v(568.8, 48.51) * mm, "end": v(568.27, 49.45) * mm});
            skLineSegment(sketch, "E5329", {"start": v(568.27, 49.45) * mm, "end": v(567.71, 50.38) * mm});
            skLineSegment(sketch, "E5330", {"start": v(567.71, 50.38) * mm, "end": v(567.21, 51.03) * mm});
            skLineSegment(sketch, "E5331", {"start": v(567.21, 51.03) * mm, "end": v(567.02, 51.21) * mm});
            skLineSegment(sketch, "E5332", {"start": v(567.02, 51.21) * mm, "end": v(566.64, 51.6) * mm});
            skLineSegment(sketch, "E5333", {"start": v(566.64, 51.6) * mm, "end": v(565.37, 52.57) * mm});
            skLineSegment(sketch, "E5334", {"start": v(565.37, 52.57) * mm, "end": v(563.64, 53.83) * mm});
            skLineSegment(sketch, "E5335", {"start": v(563.64, 53.83) * mm, "end": v(562.2, 55.26) * mm});
            skLineSegment(sketch, "E5336", {"start": v(562.2, 55.26) * mm, "end": v(561.47, 56.66) * mm});
            skLineSegment(sketch, "E5337", {"start": v(561.47, 56.66) * mm, "end": v(561.4, 57.16) * mm});
            skLineSegment(sketch, "E5338", {"start": v(561.4, 57.16) * mm, "end": v(562.12, 57.15) * mm});
            skLineSegment(sketch, "E5339", {"start": v(562.12, 57.15) * mm, "end": v(564.28, 56.82) * mm});
            skLineSegment(sketch, "E5340", {"start": v(564.28, 56.82) * mm, "end": v(566.86, 55.97) * mm});
            skLineSegment(sketch, "E5341", {"start": v(566.86, 55.97) * mm, "end": v(569.21, 54.77) * mm});
            skLineSegment(sketch, "E5342", {"start": v(569.21, 54.77) * mm, "end": v(571.43, 53.32) * mm});
            skLineSegment(sketch, "E5343", {"start": v(571.43, 53.32) * mm, "end": v(573.6, 51.76) * mm});
            skLineSegment(sketch, "E5344", {"start": v(573.6, 51.76) * mm, "end": v(575.8, 50.22) * mm});
            skLineSegment(sketch, "E5345", {"start": v(575.8, 50.22) * mm, "end": v(578.14, 48.82) * mm});
            skLineSegment(sketch, "E5346", {"start": v(578.14, 48.82) * mm, "end": v(580.03, 47.94) * mm});
            skLineSegment(sketch, "E5347", {"start": v(580.03, 47.94) * mm, "end": v(580.68, 47.7) * mm});
            skLineSegment(sketch, "E5348", {"start": v(580.68, 47.7) * mm, "end": v(582.02, 47.23) * mm});
            skLineSegment(sketch, "E5349", {"start": v(582.02, 47.23) * mm, "end": v(586, 45.68) * mm});
            skLineSegment(sketch, "E5350", {"start": v(586, 45.68) * mm, "end": v(591.13, 43.25) * mm});
            skLineSegment(sketch, "E5351", {"start": v(591.13, 43.25) * mm, "end": v(595.79, 40.12) * mm});
            skLineSegment(sketch, "E5352", {"start": v(595.79, 40.12) * mm, "end": v(598.89, 37.15) * mm});
            skLineSegment(sketch, "E5353", {"start": v(598.89, 37.15) * mm, "end": v(599.73, 36.02) * mm});
            skLineSegment(sketch, "E5354", {"start": v(599.73, 36.02) * mm, "end": v(599.73, 35.5) * mm});
            skLineSegment(sketch, "E5355", {"start": v(599.73, 35.5) * mm, "end": v(599.23, 33.9) * mm});
            skLineSegment(sketch, "E5356", {"start": v(599.23, 33.9) * mm, "end": v(598.31, 31.7) * mm});
            skLineSegment(sketch, "E5357", {"start": v(598.31, 31.7) * mm, "end": v(597.9, 29.39) * mm});
            skLineSegment(sketch, "E5358", {"start": v(597.9, 29.39) * mm, "end": v(598.52, 27.41) * mm});
            skLineSegment(sketch, "E5359", {"start": v(598.52, 27.41) * mm, "end": v(598.92, 26.9) * mm});
            skLineSegment(sketch, "E5360", {"start": v(598.92, 26.9) * mm, "end": v(599.3, 26.44) * mm});
            skLineSegment(sketch, "E5361", {"start": v(599.3, 26.44) * mm, "end": v(599.9, 26.53) * mm});
            skLineSegment(sketch, "E5362", {"start": v(599.9, 26.53) * mm, "end": v(600.47, 26.6) * mm});
            skLineSegment(sketch, "E5363", {"start": v(600.47, 26.6) * mm, "end": v(602.1, 27.34) * mm});
            skLineSegment(sketch, "E5364", {"start": v(602.1, 27.34) * mm, "end": v(603.77, 28.77) * mm});
            skLineSegment(sketch, "E5365", {"start": v(603.77, 28.77) * mm, "end": v(605.25, 30.27) * mm});
            skLineSegment(sketch, "E5366", {"start": v(605.25, 30.27) * mm, "end": v(606.42, 31.16) * mm});
            skLineSegment(sketch, "E5367", {"start": v(606.42, 31.16) * mm, "end": v(606.86, 31.31) * mm});
            skLineSegment(sketch, "E5368", {"start": v(606.86, 31.31) * mm, "end": v(607.03, 31.37) * mm});
            skLineSegment(sketch, "E5369", {"start": v(607.03, 31.37) * mm, "end": v(607.83, 31.43) * mm});
            skLineSegment(sketch, "E5370", {"start": v(607.83, 31.43) * mm, "end": v(608.6, 31.24) * mm});
            skLineSegment(sketch, "E5371", {"start": v(608.6, 31.24) * mm, "end": v(608.76, 31.17) * mm});
            skLineSegment(sketch, "E5372", {"start": v(608.76, 31.17) * mm, "end": v(608.71, 30.8) * mm});
            skLineSegment(sketch, "E5373", {"start": v(608.71, 30.8) * mm, "end": v(608.4, 29.75) * mm});
            skLineSegment(sketch, "E5374", {"start": v(608.4, 29.75) * mm, "end": v(607.74, 28.5) * mm});
            skLineSegment(sketch, "E5375", {"start": v(607.74, 28.5) * mm, "end": v(606.93, 27.33) * mm});
            skLineSegment(sketch, "E5376", {"start": v(606.93, 27.33) * mm, "end": v(606.05, 26.18) * mm});
            skLineSegment(sketch, "E5377", {"start": v(606.05, 26.18) * mm, "end": v(605.24, 24.98) * mm});
            skLineSegment(sketch, "E5378", {"start": v(605.24, 24.98) * mm, "end": v(604.63, 23.66) * mm});
            skLineSegment(sketch, "E5379", {"start": v(604.63, 23.66) * mm, "end": v(604.31, 22.13) * mm});
            skLineSegment(sketch, "E5380", {"start": v(604.31, 22.13) * mm, "end": v(604.34, 20.77) * mm});
            skLineSegment(sketch, "E5381", {"start": v(604.34, 20.77) * mm, "end": v(604.42, 20.32) * mm});
            skLineSegment(sketch, "E5382", {"start": v(604.42, 20.32) * mm, "end": v(604.55, 19.65) * mm});
            skLineSegment(sketch, "E5383", {"start": v(604.55, 19.65) * mm, "end": v(605.22, 19.48) * mm});
            skLineSegment(sketch, "E5384", {"start": v(605.22, 19.48) * mm, "end": v(605.64, 19.38) * mm});
            skLineSegment(sketch, "E5385", {"start": v(605.64, 19.38) * mm, "end": v(606.95, 19.36) * mm});
            skLineSegment(sketch, "E5386", {"start": v(606.95, 19.36) * mm, "end": v(608.48, 19.8) * mm});
            skLineSegment(sketch, "E5387", {"start": v(608.48, 19.8) * mm, "end": v(609.86, 20.65) * mm});
            skLineSegment(sketch, "E5388", {"start": v(609.86, 20.65) * mm, "end": v(610.84, 21.49) * mm});
            skLineSegment(sketch, "E5389", {"start": v(610.84, 21.49) * mm, "end": v(611.14, 21.79) * mm});
            skLineSegment(sketch, "E5390", {"start": v(611.14, 21.79) * mm, "end": v(611.3, 21.95) * mm});
            skLineSegment(sketch, "E5391", {"start": v(611.3, 21.95) * mm, "end": v(612.22, 22.88) * mm});
            skLineSegment(sketch, "E5392", {"start": v(612.22, 22.88) * mm, "end": v(613.2, 23.72) * mm});
            skLineSegment(sketch, "E5393", {"start": v(613.2, 23.72) * mm, "end": v(613.4, 23.85) * mm});
            skLineSegment(sketch, "E5394", {"start": v(613.4, 23.85) * mm, "end": v(614.06, 24.26) * mm});
            skLineSegment(sketch, "E5395", {"start": v(614.06, 24.26) * mm, "end": v(616.05, 25.4) * mm});
            skLineSegment(sketch, "E5396", {"start": v(616.05, 25.4) * mm, "end": v(619.04, 26.77) * mm});
            skLineSegment(sketch, "E5397", {"start": v(619.04, 26.77) * mm, "end": v(622.17, 27.61) * mm});
            skLineSegment(sketch, "E5398", {"start": v(622.17, 27.61) * mm, "end": v(624.5, 27.72) * mm});
            skLineSegment(sketch, "E5399", {"start": v(624.5, 27.72) * mm, "end": v(625.25, 27.56) * mm});
            skLineSegment(sketch, "E5400", {"start": v(625.25, 27.56) * mm, "end": v(625, 26.9) * mm});
            skLineSegment(sketch, "E5401", {"start": v(625, 26.9) * mm, "end": v(624.02, 24.99) * mm});
            skLineSegment(sketch, "E5402", {"start": v(624.02, 24.99) * mm, "end": v(622.44, 22.72) * mm});
            skLineSegment(sketch, "E5403", {"start": v(622.44, 22.72) * mm, "end": v(620.65, 20.59) * mm});
            skLineSegment(sketch, "E5404", {"start": v(620.65, 20.59) * mm, "end": v(619.21, 18.96) * mm});
            skLineSegment(sketch, "E5405", {"start": v(619.21, 18.96) * mm, "end": v(618.75, 18.4) * mm});
            skLineSegment(sketch, "E5406", {"start": v(618.75, 18.4) * mm, "end": v(618.18, 17.74) * mm});
            skLineSegment(sketch, "E5407", {"start": v(618.18, 17.74) * mm, "end": v(616.32, 15.88) * mm});
            skLineSegment(sketch, "E5408", {"start": v(616.32, 15.88) * mm, "end": v(614, 13.5) * mm});
            skLineSegment(sketch, "E5409", {"start": v(614, 13.5) * mm, "end": v(612.15, 10.8) * mm});
            skLineSegment(sketch, "E5410", {"start": v(612.15, 10.8) * mm, "end": v(611.23, 8.19) * mm});
            skLineSegment(sketch, "E5411", {"start": v(611.23, 8.19) * mm, "end": v(611.12, 7.3) * mm});
            skLineSegment(sketch, "E5412", {"start": v(611.12, 7.3) * mm, "end": v(611, 6.22) * mm});
            skLineSegment(sketch, "E5413", {"start": v(611, 6.22) * mm, "end": v(612.08, 6.1) * mm});
            skLineSegment(sketch, "E5414", {"start": v(612.08, 6.1) * mm, "end": v(612.69, 6.04) * mm});
            skLineSegment(sketch, "E5415", {"start": v(612.69, 6.04) * mm, "end": v(614.55, 6.2) * mm});
            skLineSegment(sketch, "E5416", {"start": v(614.55, 6.2) * mm, "end": v(616.4, 7.04) * mm});
            skLineSegment(sketch, "E5417", {"start": v(616.4, 7.04) * mm, "end": v(617.88, 8.5) * mm});
            skLineSegment(sketch, "E5418", {"start": v(617.88, 8.5) * mm, "end": v(618.87, 9.97) * mm});
            skLineSegment(sketch, "E5419", {"start": v(618.87, 9.97) * mm, "end": v(619.16, 10.48) * mm});
            skLineSegment(sketch, "E5420", {"start": v(619.16, 10.48) * mm, "end": v(619.24, 10.64) * mm});
            skLineSegment(sketch, "E5421", {"start": v(619.24, 10.64) * mm, "end": v(620.2, 12.2) * mm});
            skLineSegment(sketch, "E5422", {"start": v(620.2, 12.2) * mm, "end": v(620.3, 12.34) * mm});
            skLineSegment(sketch, "E5423", {"start": v(620.3, 12.34) * mm, "end": v(621.25, 12.97) * mm});
            skLineSegment(sketch, "E5424", {"start": v(621.25, 12.97) * mm, "end": v(623.84, 15.25) * mm});
            skLineSegment(sketch, "E5425", {"start": v(623.84, 15.25) * mm, "end": v(627.34, 18.6) * mm});
            skLineSegment(sketch, "E5426", {"start": v(627.34, 18.6) * mm, "end": v(631.06, 21.58) * mm});
            skLineSegment(sketch, "E5427", {"start": v(631.06, 21.58) * mm, "end": v(634.12, 23.14) * mm});
            skLineSegment(sketch, "E5428", {"start": v(634.12, 23.14) * mm, "end": v(635.21, 23.36) * mm});
            skLineSegment(sketch, "E5429", {"start": v(635.21, 23.36) * mm, "end": v(635.79, 23.48) * mm});
            skLineSegment(sketch, "E5430", {"start": v(635.79, 23.48) * mm, "end": v(637.55, 23.7) * mm});
            skLineSegment(sketch, "E5431", {"start": v(637.55, 23.7) * mm, "end": v(639.99, 23.62) * mm});
            skLineSegment(sketch, "E5432", {"start": v(639.99, 23.62) * mm, "end": v(642.2, 22.9) * mm});
            skLineSegment(sketch, "E5433", {"start": v(642.2, 22.9) * mm, "end": v(643.57, 21.73) * mm});
            skLineSegment(sketch, "E5434", {"start": v(643.57, 21.73) * mm, "end": v(643.84, 21.25) * mm});
            skLineSegment(sketch, "E5435", {"start": v(643.84, 21.25) * mm, "end": v(643.5, 20.55) * mm});
            skLineSegment(sketch, "E5436", {"start": v(643.5, 20.55) * mm, "end": v(642.2, 18.6) * mm});
            skLineSegment(sketch, "E5437", {"start": v(642.2, 18.6) * mm, "end": v(640.25, 16.37) * mm});
            skLineSegment(sketch, "E5438", {"start": v(640.25, 16.37) * mm, "end": v(638.1, 14.3) * mm});
            skLineSegment(sketch, "E5439", {"start": v(638.1, 14.3) * mm, "end": v(636.43, 12.68) * mm});
            skLineSegment(sketch, "E5440", {"start": v(636.43, 12.68) * mm, "end": v(635.89, 12.11) * mm});
            skLineSegment(sketch, "E5441", {"start": v(635.89, 12.11) * mm, "end": v(635.44, 11.64) * mm});
            skLineSegment(sketch, "E5442", {"start": v(635.44, 11.64) * mm, "end": v(633.39, 9.1) * mm});
            skLineSegment(sketch, "E5443", {"start": v(633.39, 9.1) * mm, "end": v(631.32, 6.6) * mm});
            skLineSegment(sketch, "E5444", {"start": v(631.32, 6.6) * mm, "end": v(630.87, 6.16) * mm});
            skLineSegment(sketch, "E5445", {"start": v(630.87, 6.16) * mm, "end": v(630.55, 5.83) * mm});
            skLineSegment(sketch, "E5446", {"start": v(630.55, 5.83) * mm, "end": v(629.46, 4.98) * mm});
            skLineSegment(sketch, "E5447", {"start": v(629.46, 4.98) * mm, "end": v(627.97, 3.94) * mm});
            skLineSegment(sketch, "E5448", {"start": v(627.97, 3.94) * mm, "end": v(626.57, 2.78) * mm});
            skLineSegment(sketch, "E5449", {"start": v(626.57, 2.78) * mm, "end": v(625.63, 1.67) * mm});
            skLineSegment(sketch, "E5450", {"start": v(625.63, 1.67) * mm, "end": v(625.4, 1.26) * mm});
            skLineSegment(sketch, "E5451", {"start": v(625.4, 1.26) * mm, "end": v(625.26, 0.99) * mm});
            skLineSegment(sketch, "E5452", {"start": v(625.26, 0.99) * mm, "end": v(624.84, -0.42) * mm});
            skLineSegment(sketch, "E5453", {"start": v(624.84, -0.42) * mm, "end": v(624.82, -1.88) * mm});
            skLineSegment(sketch, "E5454", {"start": v(624.82, -1.88) * mm, "end": v(624.87, -2.18) * mm});
            skLineSegment(sketch, "E5455", {"start": v(624.87, -2.18) * mm, "end": v(625.02, -2.98) * mm});
            skLineSegment(sketch, "E5456", {"start": v(625.02, -2.98) * mm, "end": v(625.82, -3.06) * mm});
            skLineSegment(sketch, "E5457", {"start": v(625.82, -3.06) * mm, "end": v(626.6, -3.13) * mm});
            skLineSegment(sketch, "E5458", {"start": v(626.6, -3.13) * mm, "end": v(628.98, -2.55) * mm});
            skLineSegment(sketch, "E5459", {"start": v(628.98, -2.55) * mm, "end": v(631.63, -0.8) * mm});
            skLineSegment(sketch, "E5460", {"start": v(631.63, -0.8) * mm, "end": v(633.94, 1.58) * mm});
            skLineSegment(sketch, "E5461", {"start": v(633.94, 1.58) * mm, "end": v(635.53, 3.36) * mm});
            skLineSegment(sketch, "E5462", {"start": v(635.53, 3.36) * mm, "end": v(636.1, 3.92) * mm});
            skLineSegment(sketch, "E5463", {"start": v(636.1, 3.92) * mm, "end": v(636.76, 4.61) * mm});
            skLineSegment(sketch, "E5464", {"start": v(636.76, 4.61) * mm, "end": v(640.32, 7.97) * mm});
            skLineSegment(sketch, "E5465", {"start": v(640.32, 7.97) * mm, "end": v(644.15, 11.03) * mm});
            skLineSegment(sketch, "E5466", {"start": v(644.15, 11.03) * mm, "end": v(644.95, 11.56) * mm});
            skLineSegment(sketch, "E5467", {"start": v(644.95, 11.56) * mm, "end": v(645.24, 11.75) * mm});
            skLineSegment(sketch, "E5468", {"start": v(645.24, 11.75) * mm, "end": v(646.13, 12.32) * mm});
            skLineSegment(sketch, "E5469", {"start": v(646.13, 12.32) * mm, "end": v(647.51, 13.15) * mm});
            skLineSegment(sketch, "E5470", {"start": v(647.51, 13.15) * mm, "end": v(649.04, 13.95) * mm});
            skLineSegment(sketch, "E5471", {"start": v(649.04, 13.95) * mm, "end": v(650.66, 14.66) * mm});
            skLineSegment(sketch, "E5472", {"start": v(650.66, 14.66) * mm, "end": v(652.3, 15.2) * mm});
            skLineSegment(sketch, "E5473", {"start": v(652.3, 15.2) * mm, "end": v(653.93, 15.48) * mm});
            skLineSegment(sketch, "E5474", {"start": v(653.93, 15.48) * mm, "end": v(655.5, 15.43) * mm});
            skLineSegment(sketch, "E5475", {"start": v(655.5, 15.43) * mm, "end": v(656.59, 15.14) * mm});
            skLineSegment(sketch, "E5476", {"start": v(656.59, 15.14) * mm, "end": v(656.92, 14.97) * mm});
            skLineSegment(sketch, "E5477", {"start": v(656.92, 14.97) * mm, "end": v(655.5, 12.84) * mm});
            skLineSegment(sketch, "E5478", {"start": v(655.5, 12.84) * mm, "end": v(647.9, 2.4) * mm});
            skLineSegment(sketch, "E5479", {"start": v(647.9, 2.4) * mm, "end": v(639.65, -7.5) * mm});
            skLineSegment(sketch, "E5480", {"start": v(639.65, -7.5) * mm, "end": v(637.9, -9.36) * mm});
            skLineSegment(sketch, "E5481", {"start": v(637.9, -9.36) * mm, "end": v(637.55, -9.73) * mm});
            skLineSegment(sketch, "E5482", {"start": v(637.55, -9.73) * mm, "end": v(636.4, -10.71) * mm});
            skLineSegment(sketch, "E5483", {"start": v(636.4, -10.71) * mm, "end": v(634.87, -11.95) * mm});
            skLineSegment(sketch, "E5484", {"start": v(634.87, -11.95) * mm, "end": v(633.44, -13.31) * mm});
            skLineSegment(sketch, "E5485", {"start": v(633.44, -13.31) * mm, "end": v(632.51, -14.58) * mm});
            skLineSegment(sketch, "E5486", {"start": v(632.51, -14.58) * mm, "end": v(632.29, -15.05) * mm});
            skLineSegment(sketch, "E5487", {"start": v(632.29, -15.05) * mm, "end": v(632.13, -15.37) * mm});
            skLineSegment(sketch, "E5488", {"start": v(632.13, -15.37) * mm, "end": v(631.73, -17.06) * mm});
            skLineSegment(sketch, "E5489", {"start": v(631.73, -17.06) * mm, "end": v(631.82, -18.8) * mm});
            skLineSegment(sketch, "E5490", {"start": v(631.82, -18.8) * mm, "end": v(631.91, -19.16) * mm});
            skLineSegment(sketch, "E5491", {"start": v(631.91, -19.16) * mm, "end": v(632.1, -19.88) * mm});
            skLineSegment(sketch, "E5492", {"start": v(632.1, -19.88) * mm, "end": v(632.83, -19.96) * mm});
            skLineSegment(sketch, "E5493", {"start": v(632.83, -19.96) * mm, "end": v(633.4, -20.02) * mm});
            skLineSegment(sketch, "E5494", {"start": v(633.4, -20.02) * mm, "end": v(635.21, -19.62) * mm});
            skLineSegment(sketch, "E5495", {"start": v(635.21, -19.62) * mm, "end": v(637.1, -18.33) * mm});
            skLineSegment(sketch, "E5496", {"start": v(637.1, -18.33) * mm, "end": v(638.67, -16.52) * mm});
            skLineSegment(sketch, "E5497", {"start": v(638.67, -16.52) * mm, "end": v(639.76, -15.11) * mm});
            skLineSegment(sketch, "E5498", {"start": v(639.76, -15.11) * mm, "end": v(640.14, -14.66) * mm});
            skLineSegment(sketch, "E5499", {"start": v(640.14, -14.66) * mm, "end": v(640.57, -14.15) * mm});
            skLineSegment(sketch, "E5500", {"start": v(640.57, -14.15) * mm, "end": v(645.08, -9.2) * mm});
            skLineSegment(sketch, "E5501", {"start": v(645.08, -9.2) * mm, "end": v(645.53, -8.71) * mm});
            skLineSegment(sketch, "E5502", {"start": v(645.53, -8.71) * mm, "end": v(646.12, -8.04) * mm});
            skLineSegment(sketch, "E5503", {"start": v(646.12, -8.04) * mm, "end": v(647.86, -5.98) * mm});
            skLineSegment(sketch, "E5504", {"start": v(647.86, -5.98) * mm, "end": v(650.06, -3.33) * mm});
            skLineSegment(sketch, "E5505", {"start": v(650.06, -3.33) * mm, "end": v(652.23, -0.8) * mm});
            skLineSegment(sketch, "E5506", {"start": v(652.23, -0.8) * mm, "end": v(654.46, 1.6) * mm});
            skLineSegment(sketch, "E5507", {"start": v(654.46, 1.6) * mm, "end": v(656.84, 3.8) * mm});
            skLineSegment(sketch, "E5508", {"start": v(656.84, 3.8) * mm, "end": v(659.47, 5.78) * mm});
            skLineSegment(sketch, "E5509", {"start": v(659.47, 5.78) * mm, "end": v(662.44, 7.51) * mm});
            skLineSegment(sketch, "E5510", {"start": v(662.44, 7.51) * mm, "end": v(664.97, 8.66) * mm});
            skLineSegment(sketch, "E5511", {"start": v(664.97, 8.66) * mm, "end": v(665.84, 8.97) * mm});
            skLineSegment(sketch, "E5512", {"start": v(665.84, 8.97) * mm, "end": v(666.46, 9.2) * mm});
            skLineSegment(sketch, "E5513", {"start": v(666.46, 9.2) * mm, "end": v(668.28, 9.98) * mm});
            skLineSegment(sketch, "E5514", {"start": v(668.28, 9.98) * mm, "end": v(670.93, 11.05) * mm});
            skLineSegment(sketch, "E5515", {"start": v(670.93, 11.05) * mm, "end": v(673.63, 11.7) * mm});
            skLineSegment(sketch, "E5516", {"start": v(673.63, 11.7) * mm, "end": v(675.64, 11.69) * mm});
            skLineSegment(sketch, "E5517", {"start": v(675.64, 11.69) * mm, "end": v(676.25, 11.49) * mm});
            skLineSegment(sketch, "E5518", {"start": v(676.25, 11.49) * mm, "end": v(675.89, 10.4) * mm});
            skLineSegment(sketch, "E5519", {"start": v(675.89, 10.4) * mm, "end": v(674.38, 7.24) * mm});
            skLineSegment(sketch, "E5520", {"start": v(674.38, 7.24) * mm, "end": v(671.9, 3.4) * mm});
            skLineSegment(sketch, "E5521", {"start": v(671.9, 3.4) * mm, "end": v(669.04, -0.21) * mm});
            skLineSegment(sketch, "E5522", {"start": v(669.04, -0.21) * mm, "end": v(666.78, -2.87) * mm});
            skLineSegment(sketch, "E5523", {"start": v(666.78, -2.87) * mm, "end": v(666.03, -3.76) * mm});
            skLineSegment(sketch, "E5524", {"start": v(666.03, -3.76) * mm, "end": v(664.99, -4.97) * mm});
            skLineSegment(sketch, "E5525", {"start": v(664.99, -4.97) * mm, "end": v(659.53, -10.81) * mm});
            skLineSegment(sketch, "E5526", {"start": v(659.53, -10.81) * mm, "end": v(654.15, -16.71) * mm});
            skLineSegment(sketch, "E5527", {"start": v(654.15, -16.71) * mm, "end": v(653.15, -17.97) * mm});
            skLineSegment(sketch, "E5528", {"start": v(653.15, -17.97) * mm, "end": v(652.9, -18.04) * mm});
            skLineSegment(sketch, "E5529", {"start": v(652.9, -18.04) * mm, "end": v(652.17, -18.28) * mm});
            skLineSegment(sketch, "E5530", {"start": v(652.17, -18.28) * mm, "end": v(651.3, -18.65) * mm});
            skLineSegment(sketch, "E5531", {"start": v(651.3, -18.65) * mm, "end": v(650.54, -19.1) * mm});
            skLineSegment(sketch, "E5532", {"start": v(650.54, -19.1) * mm, "end": v(649.92, -19.64) * mm});
            skLineSegment(sketch, "E5533", {"start": v(649.92, -19.64) * mm, "end": v(649.43, -20.3) * mm});
            skLineSegment(sketch, "E5534", {"start": v(649.43, -20.3) * mm, "end": v(649.1, -21.1) * mm});
            skLineSegment(sketch, "E5535", {"start": v(649.1, -21.1) * mm, "end": v(648.96, -22.07) * mm});
            skLineSegment(sketch, "E5536", {"start": v(648.96, -22.07) * mm, "end": v(648.96, -22.94) * mm});
            skLineSegment(sketch, "E5537", {"start": v(648.96, -22.94) * mm, "end": v(649, -23.22) * mm});
            skLineSegment(sketch, "E5538", {"start": v(649, -23.22) * mm, "end": v(649.07, -24) * mm});
            skLineSegment(sketch, "E5539", {"start": v(649.07, -24) * mm, "end": v(649.83, -24.16) * mm});
            skLineSegment(sketch, "E5540", {"start": v(649.83, -24.16) * mm, "end": v(650.38, -24.28) * mm});
            skLineSegment(sketch, "E5541", {"start": v(650.38, -24.28) * mm, "end": v(652.11, -24.34) * mm});
            skLineSegment(sketch, "E5542", {"start": v(652.11, -24.34) * mm, "end": v(654.15, -23.93) * mm});
            skLineSegment(sketch, "E5543", {"start": v(654.15, -23.93) * mm, "end": v(655.97, -23.04) * mm});
            skLineSegment(sketch, "E5544", {"start": v(655.97, -23.04) * mm, "end": v(657.62, -21.8) * mm});
            skLineSegment(sketch, "E5545", {"start": v(657.62, -21.8) * mm, "end": v(659.14, -20.3) * mm});
            skLineSegment(sketch, "E5546", {"start": v(659.14, -20.3) * mm, "end": v(660.56, -18.65) * mm});
            skLineSegment(sketch, "E5547", {"start": v(660.56, -18.65) * mm, "end": v(661.92, -16.98) * mm});
            skLineSegment(sketch, "E5548", {"start": v(661.92, -16.98) * mm, "end": v(662.92, -15.79) * mm});
            skLineSegment(sketch, "E5549", {"start": v(662.92, -15.79) * mm, "end": v(663.26, -15.4) * mm});
            skLineSegment(sketch, "E5550", {"start": v(663.26, -15.4) * mm, "end": v(663.9, -14.67) * mm});
            skLineSegment(sketch, "E5551", {"start": v(663.9, -14.67) * mm, "end": v(665.68, -12.34) * mm});
            skLineSegment(sketch, "E5552", {"start": v(665.68, -12.34) * mm, "end": v(668.04, -9.04) * mm});
            skLineSegment(sketch, "E5553", {"start": v(668.04, -9.04) * mm, "end": v(670.48, -5.87) * mm});
            skLineSegment(sketch, "E5554", {"start": v(670.48, -5.87) * mm, "end": v(672.43, -3.77) * mm});
            skLineSegment(sketch, "E5555", {"start": v(672.43, -3.77) * mm, "end": v(673.17, -3.17) * mm});
            skLineSegment(sketch, "E5556", {"start": v(673.17, -3.17) * mm, "end": v(673.31, -3.06) * mm});
            skLineSegment(sketch, "E5557", {"start": v(673.31, -3.06) * mm, "end": v(673.82, -2.83) * mm});
            skLineSegment(sketch, "E5558", {"start": v(673.82, -2.83) * mm, "end": v(674.6, -2.56) * mm});
            skLineSegment(sketch, "E5559", {"start": v(674.6, -2.56) * mm, "end": v(675.42, -2.25) * mm});
            skLineSegment(sketch, "E5560", {"start": v(675.42, -2.25) * mm, "end": v(676.02, -1.94) * mm});
            skLineSegment(sketch, "E5561", {"start": v(676.02, -1.94) * mm, "end": v(676.2, -1.8) * mm});
            skLineSegment(sketch, "E5562", {"start": v(676.2, -1.8) * mm, "end": v(676.69, -1.4) * mm});
            skLineSegment(sketch, "E5563", {"start": v(676.69, -1.4) * mm, "end": v(679.03, 0.98) * mm});
            skLineSegment(sketch, "E5564", {"start": v(679.03, 0.98) * mm, "end": v(681.51, 3.11) * mm});
            skLineSegment(sketch, "E5565", {"start": v(681.51, 3.11) * mm, "end": v(682.07, 3.4) * mm});
            skLineSegment(sketch, "E5566", {"start": v(682.07, 3.4) * mm, "end": v(682.73, 3.73) * mm});
            skLineSegment(sketch, "E5567", {"start": v(682.73, 3.73) * mm, "end": v(684.8, 4.6) * mm});
            skLineSegment(sketch, "E5568", {"start": v(684.8, 4.6) * mm, "end": v(687.7, 5.48) * mm});
            skLineSegment(sketch, "E5569", {"start": v(687.7, 5.48) * mm, "end": v(690.7, 5.87) * mm});
            skLineSegment(sketch, "E5570", {"start": v(690.7, 5.87) * mm, "end": v(692.94, 5.77) * mm});
            skLineSegment(sketch, "E5571", {"start": v(692.94, 5.77) * mm, "end": v(693.66, 5.61) * mm});
            skLineSegment(sketch, "E5572", {"start": v(693.66, 5.61) * mm, "end": v(693.7, 5) * mm});
            skLineSegment(sketch, "E5573", {"start": v(693.7, 5) * mm, "end": v(693.6, 3.17) * mm});
            skLineSegment(sketch, "E5574", {"start": v(693.6, 3.17) * mm, "end": v(693.1, 1.02) * mm});
            skLineSegment(sketch, "E5575", {"start": v(693.1, 1.02) * mm, "end": v(692.26, -0.92) * mm});
            skLineSegment(sketch, "E5576", {"start": v(692.26, -0.92) * mm, "end": v(691.12, -2.69) * mm});
            skLineSegment(sketch, "E5577", {"start": v(691.12, -2.69) * mm, "end": v(689.76, -4.36) * mm});
            skLineSegment(sketch, "E5578", {"start": v(689.76, -4.36) * mm, "end": v(688.25, -6) * mm});
            skLineSegment(sketch, "E5579", {"start": v(688.25, -6) * mm, "end": v(686.68, -7.65) * mm});
            skLineSegment(sketch, "E5580", {"start": v(686.68, -7.65) * mm, "end": v(685.48, -8.95) * mm});
            skLineSegment(sketch, "E5581", {"start": v(685.48, -8.95) * mm, "end": v(685.1, -9.4) * mm});
            skLineSegment(sketch, "E5582", {"start": v(685.1, -9.4) * mm, "end": v(683.75, -10.96) * mm});
            skLineSegment(sketch, "E5583", {"start": v(683.75, -10.96) * mm, "end": v(677.02, -18.8) * mm});
            skLineSegment(sketch, "E5584", {"start": v(677.02, -18.8) * mm, "end": v(670.15, -26.5) * mm});
            skLineSegment(sketch, "E5585", {"start": v(670.15, -26.5) * mm, "end": v(668.72, -28) * mm});
            skLineSegment(sketch, "E5586", {"start": v(668.72, -28) * mm, "end": v(668, -28.77) * mm});
            skLineSegment(sketch, "E5587", {"start": v(668, -28.77) * mm, "end": v(664.65, -32.76) * mm});
            skLineSegment(sketch, "E5588", {"start": v(664.65, -32.76) * mm, "end": v(661.35, -36.77) * mm});
            skLineSegment(sketch, "E5589", {"start": v(661.35, -36.77) * mm, "end": v(660.65, -37.54) * mm});
            skLineSegment(sketch, "E5590", {"start": v(660.65, -37.54) * mm, "end": v(660.34, -37.9) * mm});
            skLineSegment(sketch, "E5591", {"start": v(660.34, -37.9) * mm, "end": v(659.3, -38.84) * mm});
            skLineSegment(sketch, "E5592", {"start": v(659.3, -38.84) * mm, "end": v(657.87, -40.03) * mm});
            skLineSegment(sketch, "E5593", {"start": v(657.87, -40.03) * mm, "end": v(656.52, -41.31) * mm});
            skLineSegment(sketch, "E5594", {"start": v(656.52, -41.31) * mm, "end": v(655.61, -42.46) * mm});
            skLineSegment(sketch, "E5595", {"start": v(655.61, -42.46) * mm, "end": v(655.38, -42.89) * mm});
            skLineSegment(sketch, "E5596", {"start": v(655.38, -42.89) * mm, "end": v(655.23, -43.17) * mm});
            skLineSegment(sketch, "E5597", {"start": v(655.23, -43.17) * mm, "end": v(654.75, -44.64) * mm});
            skLineSegment(sketch, "E5598", {"start": v(654.75, -44.64) * mm, "end": v(654.66, -46.19) * mm});
            skLineSegment(sketch, "E5599", {"start": v(654.66, -46.19) * mm, "end": v(654.7, -46.5) * mm});
            skLineSegment(sketch, "E5600", {"start": v(654.7, -46.5) * mm, "end": v(654.78, -47.21) * mm});
            skLineSegment(sketch, "E5601", {"start": v(654.78, -47.21) * mm, "end": v(655.46, -47.4) * mm});
            skLineSegment(sketch, "E5602", {"start": v(655.46, -47.4) * mm, "end": v(655.94, -47.54) * mm});
            skLineSegment(sketch, "E5603", {"start": v(655.94, -47.54) * mm, "end": v(657.5, -47.58) * mm});
            skLineSegment(sketch, "E5604", {"start": v(657.5, -47.58) * mm, "end": v(659.22, -46.95) * mm});
            skLineSegment(sketch, "E5605", {"start": v(659.22, -46.95) * mm, "end": v(660.67, -45.73) * mm});
            skLineSegment(sketch, "E5606", {"start": v(660.67, -45.73) * mm, "end": v(661.62, -44.55) * mm});
            skLineSegment(sketch, "E5607", {"start": v(661.62, -44.55) * mm, "end": v(661.9, -44.13) * mm});
            skLineSegment(sketch, "E5608", {"start": v(661.9, -44.13) * mm, "end": v(662.04, -43.9) * mm});
            skLineSegment(sketch, "E5609", {"start": v(662.04, -43.9) * mm, "end": v(662.76, -42.73) * mm});
            skLineSegment(sketch, "E5610", {"start": v(662.76, -42.73) * mm, "end": v(663.5, -41.59) * mm});
            skLineSegment(sketch, "E5611", {"start": v(663.5, -41.59) * mm, "end": v(663.67, -41.38) * mm});
            skLineSegment(sketch, "E5612", {"start": v(663.67, -41.38) * mm, "end": v(664.03, -40.88) * mm});
            skLineSegment(sketch, "E5613", {"start": v(664.03, -40.88) * mm, "end": v(665.21, -39.48) * mm});
            skLineSegment(sketch, "E5614", {"start": v(665.21, -39.48) * mm, "end": v(666.86, -37.64) * mm});
            skLineSegment(sketch, "E5615", {"start": v(666.86, -37.64) * mm, "end": v(668.4, -35.73) * mm});
            skLineSegment(sketch, "E5616", {"start": v(668.4, -35.73) * mm, "end": v(669.42, -34.2) * mm});
            skLineSegment(sketch, "E5617", {"start": v(669.42, -34.2) * mm, "end": v(669.69, -33.66) * mm});
            skLineSegment(sketch, "E5618", {"start": v(669.69, -33.66) * mm, "end": v(670.73, -32.92) * mm});
            skLineSegment(sketch, "E5619", {"start": v(670.73, -32.92) * mm, "end": v(673.54, -30.24) * mm});
            skLineSegment(sketch, "E5620", {"start": v(673.54, -30.24) * mm, "end": v(676.92, -26.27) * mm});
            skLineSegment(sketch, "E5621", {"start": v(676.92, -26.27) * mm, "end": v(680.18, -22.13) * mm});
            skLineSegment(sketch, "E5622", {"start": v(680.18, -22.13) * mm, "end": v(682.72, -19.16) * mm});
            skLineSegment(sketch, "E5623", {"start": v(682.72, -19.16) * mm, "end": v(683.65, -18.25) * mm});
            skLineSegment(sketch, "E5624", {"start": v(683.65, -18.25) * mm, "end": v(683.84, -18.07) * mm});
            skLineSegment(sketch, "E5625", {"start": v(683.84, -18.07) * mm, "end": v(685.6, -16.23) * mm});
            skLineSegment(sketch, "E5626", {"start": v(685.6, -16.23) * mm, "end": v(685.77, -16.04) * mm});
            skLineSegment(sketch, "E5627", {"start": v(685.77, -16.04) * mm, "end": v(686.18, -15.58) * mm});
            skLineSegment(sketch, "E5628", {"start": v(686.18, -15.58) * mm, "end": v(690.18, -10.88) * mm});
            skLineSegment(sketch, "E5629", {"start": v(690.18, -10.88) * mm, "end": v(690.58, -10.4) * mm});
            skLineSegment(sketch, "E5630", {"start": v(690.58, -10.4) * mm, "end": v(690.91, -10.02) * mm});
            skLineSegment(sketch, "E5631", {"start": v(690.91, -10.02) * mm, "end": v(692.66, -8.09) * mm});
            skLineSegment(sketch, "E5632", {"start": v(692.66, -8.09) * mm, "end": v(694.56, -6.3) * mm});
            skLineSegment(sketch, "E5633", {"start": v(694.56, -6.3) * mm, "end": v(694.96, -5.98) * mm});
            skLineSegment(sketch, "E5634", {"start": v(694.96, -5.98) * mm, "end": v(695.27, -5.74) * mm});
            skLineSegment(sketch, "E5635", {"start": v(695.27, -5.74) * mm, "end": v(696.24, -5.04) * mm});
            skLineSegment(sketch, "E5636", {"start": v(696.24, -5.04) * mm, "end": v(697.94, -3.92) * mm});
            skLineSegment(sketch, "E5637", {"start": v(697.94, -3.92) * mm, "end": v(699.94, -2.75) * mm});
            skLineSegment(sketch, "E5638", {"start": v(699.94, -2.75) * mm, "end": v(702.08, -1.71) * mm});
            skLineSegment(sketch, "E5639", {"start": v(702.08, -1.71) * mm, "end": v(704.24, -0.94) * mm});
            skLineSegment(sketch, "E5640", {"start": v(704.24, -0.94) * mm, "end": v(706.3, -0.6) * mm});
            skLineSegment(sketch, "E5641", {"start": v(706.3, -0.6) * mm, "end": v(708.1, -0.85) * mm});
            skLineSegment(sketch, "E5642", {"start": v(708.1, -0.85) * mm, "end": v(709.27, -1.5) * mm});
            skLineSegment(sketch, "E5643", {"start": v(709.27, -1.5) * mm, "end": v(709.54, -1.83) * mm});
            skLineSegment(sketch, "E5644", {"start": v(709.54, -1.83) * mm, "end": v(709.1, -3.13) * mm});
            skLineSegment(sketch, "E5645", {"start": v(709.1, -3.13) * mm, "end": v(707.34, -6.9) * mm});
            skLineSegment(sketch, "E5646", {"start": v(707.34, -6.9) * mm, "end": v(704.51, -11.4) * mm});
            skLineSegment(sketch, "E5647", {"start": v(704.51, -11.4) * mm, "end": v(701.27, -15.66) * mm});
            skLineSegment(sketch, "E5648", {"start": v(701.27, -15.66) * mm, "end": v(698.69, -18.9) * mm});
            skLineSegment(sketch, "E5649", {"start": v(698.69, -18.9) * mm, "end": v(697.84, -19.98) * mm});
            skLineSegment(sketch, "E5650", {"start": v(697.84, -19.98) * mm, "end": v(697.3, -20.7) * mm});
            skLineSegment(sketch, "E5651", {"start": v(697.3, -20.7) * mm, "end": v(691.48, -27.71) * mm});
            skLineSegment(sketch, "E5652", {"start": v(691.48, -27.71) * mm, "end": v(690.85, -28.37) * mm});
            skLineSegment(sketch, "E5653", {"start": v(690.85, -28.37) * mm, "end": v(690.33, -28.92) * mm});
            skLineSegment(sketch, "E5654", {"start": v(690.33, -28.92) * mm, "end": v(688.6, -30.4) * mm});
            skLineSegment(sketch, "E5655", {"start": v(688.6, -30.4) * mm, "end": v(686.35, -32.48) * mm});
            skLineSegment(sketch, "E5656", {"start": v(686.35, -32.48) * mm, "end": v(684.68, -34.9) * mm});
            skLineSegment(sketch, "E5657", {"start": v(684.68, -34.9) * mm, "end": v(684.14, -37.24) * mm});
            skLineSegment(sketch, "E5658", {"start": v(684.14, -37.24) * mm, "end": v(684.2, -38) * mm});
            skLineSegment(sketch, "E5659", {"start": v(684.2, -38) * mm, "end": v(684.28, -38.78) * mm});
            skLineSegment(sketch, "E5660", {"start": v(684.28, -38.78) * mm, "end": v(685.05, -38.94) * mm});
            skLineSegment(sketch, "E5661", {"start": v(685.05, -38.94) * mm, "end": v(685.44, -39.02) * mm});
            skLineSegment(sketch, "E5662", {"start": v(685.44, -39.02) * mm, "end": v(686.65, -39.05) * mm});
            skLineSegment(sketch, "E5663", {"start": v(686.65, -39.05) * mm, "end": v(688.04, -38.73) * mm});
            skLineSegment(sketch, "E5664", {"start": v(688.04, -38.73) * mm, "end": v(689.25, -38.06) * mm});
            skLineSegment(sketch, "E5665", {"start": v(689.25, -38.06) * mm, "end": v(690.33, -37.14) * mm});
            skLineSegment(sketch, "E5666", {"start": v(690.33, -37.14) * mm, "end": v(691.31, -36.05) * mm});
            skLineSegment(sketch, "E5667", {"start": v(691.31, -36.05) * mm, "end": v(692.24, -34.88) * mm});
            skLineSegment(sketch, "E5668", {"start": v(692.24, -34.88) * mm, "end": v(693.14, -33.72) * mm});
            skLineSegment(sketch, "E5669", {"start": v(693.14, -33.72) * mm, "end": v(693.82, -32.92) * mm});
            skLineSegment(sketch, "E5670", {"start": v(693.82, -32.92) * mm, "end": v(694.06, -32.67) * mm});
            skLineSegment(sketch, "E5671", {"start": v(694.06, -32.67) * mm, "end": v(695, -31.7) * mm});
            skLineSegment(sketch, "E5672", {"start": v(695, -31.7) * mm, "end": v(697.62, -28.68) * mm});
            skLineSegment(sketch, "E5673", {"start": v(697.62, -28.68) * mm, "end": v(701.02, -24.59) * mm});
            skLineSegment(sketch, "E5674", {"start": v(701.02, -24.59) * mm, "end": v(704.52, -20.6) * mm});
            skLineSegment(sketch, "E5675", {"start": v(704.52, -20.6) * mm, "end": v(707.38, -17.75) * mm});
            skLineSegment(sketch, "E5676", {"start": v(707.38, -17.75) * mm, "end": v(708.4, -16.9) * mm});
            skLineSegment(sketch, "E5677", {"start": v(708.4, -16.9) * mm, "end": v(708.86, -16.51) * mm});
            skLineSegment(sketch, "E5678", {"start": v(708.86, -16.51) * mm, "end": v(710.2, -15.35) * mm});
            skLineSegment(sketch, "E5679", {"start": v(710.2, -15.35) * mm, "end": v(712.01, -13.84) * mm});
            skLineSegment(sketch, "E5680", {"start": v(712.01, -13.84) * mm, "end": v(713.87, -12.46) * mm});
            skLineSegment(sketch, "E5681", {"start": v(713.87, -12.46) * mm, "end": v(715.79, -11.3) * mm});
            skLineSegment(sketch, "E5682", {"start": v(715.79, -11.3) * mm, "end": v(717.8, -10.48) * mm});
            skLineSegment(sketch, "E5683", {"start": v(717.8, -10.48) * mm, "end": v(719.9, -10.08) * mm});
            skLineSegment(sketch, "E5684", {"start": v(719.9, -10.08) * mm, "end": v(722.11, -10.2) * mm});
            skLineSegment(sketch, "E5685", {"start": v(722.11, -10.2) * mm, "end": v(723.91, -10.7) * mm});
            skLineSegment(sketch, "E5686", {"start": v(723.91, -10.7) * mm, "end": v(724.47, -10.96) * mm});
            skLineSegment(sketch, "E5687", {"start": v(724.47, -10.96) * mm, "end": v(723.85, -12.54) * mm});
            skLineSegment(sketch, "E5688", {"start": v(723.85, -12.54) * mm, "end": v(721.38, -17.04) * mm});
            skLineSegment(sketch, "E5689", {"start": v(721.38, -17.04) * mm, "end": v(717.45, -22.35) * mm});
            skLineSegment(sketch, "E5690", {"start": v(717.45, -22.35) * mm, "end": v(713, -27.28) * mm});
            skLineSegment(sketch, "E5691", {"start": v(713, -27.28) * mm, "end": v(709.46, -30.98) * mm});
            skLineSegment(sketch, "E5692", {"start": v(709.46, -30.98) * mm, "end": v(708.3, -32.23) * mm});
            skLineSegment(sketch, "E5693", {"start": v(708.3, -32.23) * mm, "end": v(707.82, -32.74) * mm});
            skLineSegment(sketch, "E5694", {"start": v(707.82, -32.74) * mm, "end": v(706.33, -34.23) * mm});
            skLineSegment(sketch, "E5695", {"start": v(706.33, -34.23) * mm, "end": v(704.53, -36.31) * mm});
            skLineSegment(sketch, "E5696", {"start": v(704.53, -36.31) * mm, "end": v(703.26, -38.67) * mm});
            skLineSegment(sketch, "E5697", {"start": v(703.26, -38.67) * mm, "end": v(702.88, -40.82) * mm});
            skLineSegment(sketch, "E5698", {"start": v(702.88, -40.82) * mm, "end": v(702.93, -41.51) * mm});
            skLineSegment(sketch, "E5699", {"start": v(702.93, -41.51) * mm, "end": v(703.01, -42.48) * mm});
            skLineSegment(sketch, "E5700", {"start": v(703.01, -42.48) * mm, "end": v(704, -42.5) * mm});
            skLineSegment(sketch, "E5701", {"start": v(704, -42.5) * mm, "end": v(704.43, -42.5) * mm});
            skLineSegment(sketch, "E5702", {"start": v(704.43, -42.5) * mm, "end": v(705.75, -42.28) * mm});
            skLineSegment(sketch, "E5703", {"start": v(705.75, -42.28) * mm, "end": v(707.23, -41.69) * mm});
            skLineSegment(sketch, "E5704", {"start": v(707.23, -41.69) * mm, "end": v(708.48, -40.78) * mm});
            skLineSegment(sketch, "E5705", {"start": v(708.48, -40.78) * mm, "end": v(709.57, -39.64) * mm});
            skLineSegment(sketch, "E5706", {"start": v(709.57, -39.64) * mm, "end": v(710.53, -38.35) * mm});
            skLineSegment(sketch, "E5707", {"start": v(710.53, -38.35) * mm, "end": v(711.43, -36.98) * mm});
            skLineSegment(sketch, "E5708", {"start": v(711.43, -36.98) * mm, "end": v(712.32, -35.62) * mm});
            skLineSegment(sketch, "E5709", {"start": v(712.32, -35.62) * mm, "end": v(713, -34.65) * mm});
            skLineSegment(sketch, "E5710", {"start": v(713, -34.65) * mm, "end": v(713.26, -34.34) * mm});
            skLineSegment(sketch, "E5711", {"start": v(713.26, -34.34) * mm, "end": v(714.53, -32.76) * mm});
            skLineSegment(sketch, "E5712", {"start": v(714.53, -32.76) * mm, "end": v(721.2, -25.13) * mm});
            skLineSegment(sketch, "E5713", {"start": v(721.2, -25.13) * mm, "end": v(728.32, -17.92) * mm});
            skLineSegment(sketch, "E5714", {"start": v(728.32, -17.92) * mm, "end": v(729.81, -16.55) * mm});
            skLineSegment(sketch, "E5715", {"start": v(729.81, -16.55) * mm, "end": v(730.35, -16.65) * mm});
            skLineSegment(sketch, "E5716", {"start": v(730.35, -16.65) * mm, "end": v(732.03, -16.64) * mm});
            skLineSegment(sketch, "E5717", {"start": v(732.03, -16.64) * mm, "end": v(734.23, -16.33) * mm});
            skLineSegment(sketch, "E5718", {"start": v(734.23, -16.33) * mm, "end": v(736.38, -16.07) * mm});
            skLineSegment(sketch, "E5719", {"start": v(736.38, -16.07) * mm, "end": v(737.97, -16.13) * mm});
            skLineSegment(sketch, "E5720", {"start": v(737.97, -16.13) * mm, "end": v(738.47, -16.27) * mm});
            skLineSegment(sketch, "E5721", {"start": v(738.47, -16.27) * mm, "end": v(738.7, -16.73) * mm});
            skLineSegment(sketch, "E5722", {"start": v(738.7, -16.73) * mm, "end": v(739.2, -18.23) * mm});
            skLineSegment(sketch, "E5723", {"start": v(739.2, -18.23) * mm, "end": v(739.34, -20.06) * mm});
            skLineSegment(sketch, "E5724", {"start": v(739.34, -20.06) * mm, "end": v(738.99, -21.77) * mm});
            skLineSegment(sketch, "E5725", {"start": v(738.99, -21.77) * mm, "end": v(738.24, -23.38) * mm});
            skLineSegment(sketch, "E5726", {"start": v(738.24, -23.38) * mm, "end": v(737.2, -24.9) * mm});
            skLineSegment(sketch, "E5727", {"start": v(737.2, -24.9) * mm, "end": v(735.94, -26.35) * mm});
            skLineSegment(sketch, "E5728", {"start": v(735.94, -26.35) * mm, "end": v(734.56, -27.76) * mm});
            skLineSegment(sketch, "E5729", {"start": v(734.56, -27.76) * mm, "end": v(733.51, -28.78) * mm});
            skLineSegment(sketch, "E5730", {"start": v(733.51, -28.78) * mm, "end": v(733.16, -29.13) * mm});
            skLineSegment(sketch, "E5731", {"start": v(733.16, -29.13) * mm, "end": v(732.73, -29.55) * mm});
            skLineSegment(sketch, "E5732", {"start": v(732.73, -29.55) * mm, "end": v(731.47, -30.83) * mm});
            skLineSegment(sketch, "E5733", {"start": v(731.47, -30.83) * mm, "end": v(729.82, -32.67) * mm});
            skLineSegment(sketch, "E5734", {"start": v(729.82, -32.67) * mm, "end": v(728.37, -34.65) * mm});
            skLineSegment(sketch, "E5735", {"start": v(728.37, -34.65) * mm, "end": v(727.5, -36.25) * mm});
            skLineSegment(sketch, "E5736", {"start": v(727.5, -36.25) * mm, "end": v(727.3, -36.8) * mm});
            skLineSegment(sketch, "E5737", {"start": v(727.3, -36.8) * mm, "end": v(726.86, -37.04) * mm});
            skLineSegment(sketch, "E5738", {"start": v(726.86, -37.04) * mm, "end": v(725.65, -37.94) * mm});
            skLineSegment(sketch, "E5739", {"start": v(725.65, -37.94) * mm, "end": v(724.33, -39.42) * mm});
            skLineSegment(sketch, "E5740", {"start": v(724.33, -39.42) * mm, "end": v(723.62, -41.2) * mm});
            skLineSegment(sketch, "E5741", {"start": v(723.62, -41.2) * mm, "end": v(723.64, -42.73) * mm});
            skLineSegment(sketch, "E5742", {"start": v(723.64, -42.73) * mm, "end": v(723.8, -43.2) * mm});
            skLineSegment(sketch, "E5743", {"start": v(723.8, -43.2) * mm, "end": v(723.96, -43.68) * mm});
            skLineSegment(sketch, "E5744", {"start": v(723.96, -43.68) * mm, "end": v(724.44, -43.86) * mm});
            skLineSegment(sketch, "E5745", {"start": v(724.44, -43.86) * mm, "end": v(724.95, -44.04) * mm});
            skLineSegment(sketch, "E5746", {"start": v(724.95, -44.04) * mm, "end": v(726.62, -44.2) * mm});
            skLineSegment(sketch, "E5747", {"start": v(726.62, -44.2) * mm, "end": v(728.38, -43.62) * mm});
            skLineSegment(sketch, "E5748", {"start": v(728.38, -43.62) * mm, "end": v(729.81, -42.33) * mm});
            skLineSegment(sketch, "E5749", {"start": v(729.81, -42.33) * mm, "end": v(730.75, -41.03) * mm});
            skLineSegment(sketch, "E5750", {"start": v(730.75, -41.03) * mm, "end": v(731.02, -40.56) * mm});
            skLineSegment(sketch, "E5751", {"start": v(731.02, -40.56) * mm, "end": v(731.14, -40.35) * mm});
            skLineSegment(sketch, "E5752", {"start": v(731.14, -40.35) * mm, "end": v(731.79, -39.2) * mm});
            skLineSegment(sketch, "E5753", {"start": v(731.79, -39.2) * mm, "end": v(732.5, -38.09) * mm});
            skLineSegment(sketch, "E5754", {"start": v(732.5, -38.09) * mm, "end": v(732.65, -37.9) * mm});
            skLineSegment(sketch, "E5755", {"start": v(732.65, -37.9) * mm, "end": v(733.7, -36.67) * mm});
            skLineSegment(sketch, "E5756", {"start": v(733.7, -36.67) * mm, "end": v(739.55, -30.85) * mm});
            skLineSegment(sketch, "E5757", {"start": v(739.55, -30.85) * mm, "end": v(745.93, -25.63) * mm});
            skLineSegment(sketch, "E5758", {"start": v(745.93, -25.63) * mm, "end": v(747.25, -24.7) * mm});
            skLineSegment(sketch, "E5759", {"start": v(747.25, -24.7) * mm, "end": v(747.66, -24.4) * mm});
            skLineSegment(sketch, "E5760", {"start": v(747.66, -24.4) * mm, "end": v(747.7, -23.9) * mm});
            skLineSegment(sketch, "E5761", {"start": v(747.7, -23.9) * mm, "end": v(747.72, -23.6) * mm});
            skLineSegment(sketch, "E5762", {"start": v(747.72, -23.6) * mm, "end": v(748.18, -22.7) * mm});
            skLineSegment(sketch, "E5763", {"start": v(748.18, -22.7) * mm, "end": v(749.29, -22.07) * mm});
            skLineSegment(sketch, "E5764", {"start": v(749.29, -22.07) * mm, "end": v(750.81, -21.91) * mm});
            skLineSegment(sketch, "E5765", {"start": v(750.81, -21.91) * mm, "end": v(752.55, -22.14) * mm});
            skLineSegment(sketch, "E5766", {"start": v(752.55, -22.14) * mm, "end": v(754.3, -22.67) * mm});
            skLineSegment(sketch, "E5767", {"start": v(754.3, -22.67) * mm, "end": v(755.87, -23.4) * mm});
            skLineSegment(sketch, "E5768", {"start": v(755.87, -23.4) * mm, "end": v(757.04, -24.26) * mm});
            skLineSegment(sketch, "E5769", {"start": v(757.04, -24.26) * mm, "end": v(757.57, -24.9) * mm});
            skLineSegment(sketch, "E5770", {"start": v(757.57, -24.9) * mm, "end": v(757.63, -25.15) * mm});
            skLineSegment(sketch, "E5771", {"start": v(757.63, -25.15) * mm, "end": v(757.73, -25.55) * mm});
            skLineSegment(sketch, "E5772", {"start": v(757.73, -25.55) * mm, "end": v(757.7, -26.85) * mm});
            skLineSegment(sketch, "E5773", {"start": v(757.7, -26.85) * mm, "end": v(757.32, -29.05) * mm});
            skLineSegment(sketch, "E5774", {"start": v(757.32, -29.05) * mm, "end": v(756.64, -31.26) * mm});
            skLineSegment(sketch, "E5775", {"start": v(756.64, -31.26) * mm, "end": v(756.06, -32.57) * mm});
            skLineSegment(sketch, "E5776", {"start": v(756.06, -32.57) * mm, "end": v(755.8, -32.96) * mm});
            skLineSegment(sketch, "E5777", {"start": v(755.8, -32.96) * mm, "end": v(755.76, -32.97) * mm});
            skLineSegment(sketch, "E5778", {"start": v(755.76, -32.97) * mm, "end": v(755.4, -33.12) * mm});
            skLineSegment(sketch, "E5779", {"start": v(755.4, -33.12) * mm, "end": v(755.36, -33.15) * mm});
            skLineSegment(sketch, "E5780", {"start": v(755.36, -33.15) * mm, "end": v(754.91, -33.46) * mm});
            skLineSegment(sketch, "E5781", {"start": v(754.91, -33.46) * mm, "end": v(754.91, -36.1) * mm});
            skLineSegment(sketch, "E5782", {"start": v(754.91, -36.1) * mm, "end": v(756.24, -35.77) * mm});
            skLineSegment(sketch, "E5783", {"start": v(756.24, -35.77) * mm, "end": v(756.8, -35.63) * mm});
            skLineSegment(sketch, "E5784", {"start": v(756.8, -35.63) * mm, "end": v(758.32, -34.48) * mm});
            skLineSegment(sketch, "E5785", {"start": v(758.32, -34.48) * mm, "end": v(760.63, -32.1) * mm});
            skLineSegment(sketch, "E5786", {"start": v(760.63, -32.1) * mm, "end": v(762.86, -29.48) * mm});
            skLineSegment(sketch, "E5787", {"start": v(762.86, -29.48) * mm, "end": v(764.23, -27.9) * mm});
            skLineSegment(sketch, "E5788", {"start": v(764.23, -27.9) * mm, "end": v(764.73, -27.43) * mm});
            skLineSegment(sketch, "E5789", {"start": v(764.73, -27.43) * mm, "end": v(765.1, -27.11) * mm});
            skLineSegment(sketch, "E5790", {"start": v(765.1, -27.11) * mm, "end": v(765.1, -21.45) * mm});
            skLineSegment(sketch, "E5791", {"start": v(765.1, -21.45) * mm, "end": v(764.58, -21.14) * mm});
            skLineSegment(sketch, "E5792", {"start": v(764.58, -21.14) * mm, "end": v(762.74, -20.07) * mm});
            skLineSegment(sketch, "E5793", {"start": v(762.74, -20.07) * mm, "end": v(757.06, -17.1) * mm});
            skLineSegment(sketch, "E5794", {"start": v(757.06, -17.1) * mm, "end": v(749.3, -13.46) * mm});
            skLineSegment(sketch, "E5795", {"start": v(749.3, -13.46) * mm, "end": v(741.44, -10.04) * mm});
            skLineSegment(sketch, "E5796", {"start": v(741.44, -10.04) * mm, "end": v(735.56, -7.51) * mm});
            skLineSegment(sketch, "E5797", {"start": v(735.56, -7.51) * mm, "end": v(733.61, -6.65) * mm});
            skLineSegment(sketch, "E5798", {"start": v(733.61, -6.65) * mm, "end": v(732.7, -6.25) * mm});
            skLineSegment(sketch, "E5799", {"start": v(732.7, -6.25) * mm, "end": v(730.04, -4.79) * mm});
            skLineSegment(sketch, "E5800", {"start": v(730.04, -4.79) * mm, "end": v(726.65, -2.58) * mm});
            skLineSegment(sketch, "E5801", {"start": v(726.65, -2.58) * mm, "end": v(723.35, -0.22) * mm});
            skLineSegment(sketch, "E5802", {"start": v(723.35, -0.22) * mm, "end": v(720.88, 1.52) * mm});
            skLineSegment(sketch, "E5803", {"start": v(720.88, 1.52) * mm, "end": v(720.04, 2.07) * mm});
            skLineSegment(sketch, "E5804", {"start": v(720.04, 2.07) * mm, "end": v(719.16, 2.65) * mm});
            skLineSegment(sketch, "E5805", {"start": v(719.16, 2.65) * mm, "end": v(716.5, 4.35) * mm});
            skLineSegment(sketch, "E5806", {"start": v(716.5, 4.35) * mm, "end": v(712.6, 6.66) * mm});
            skLineSegment(sketch, "E5807", {"start": v(712.6, 6.66) * mm, "end": v(708.56, 8.65) * mm});
            skLineSegment(sketch, "E5808", {"start": v(708.56, 8.65) * mm, "end": v(705.64, 9.75) * mm});
            skLineSegment(sketch, "E5809", {"start": v(705.64, 9.75) * mm, "end": v(704.63, 9.99) * mm});
            skLineSegment(sketch, "E5810", {"start": v(704.63, 9.99) * mm, "end": v(704.23, 10.08) * mm});
            skLineSegment(sketch, "E5811", {"start": v(704.23, 10.08) * mm, "end": v(702.23, 10.38) * mm});
            skLineSegment(sketch, "E5812", {"start": v(702.23, 10.38) * mm, "end": v(700.23, 10.55) * mm});
            skLineSegment(sketch, "E5813", {"start": v(700.23, 10.55) * mm, "end": v(699.82, 10.58) * mm});
            skLineSegment(sketch, "E5814", {"start": v(699.82, 10.58) * mm, "end": v(699.5, 10.6) * mm});
            skLineSegment(sketch, "E5815", {"start": v(699.5, 10.6) * mm, "end": v(697.89, 10.73) * mm});
            skLineSegment(sketch, "E5816", {"start": v(697.89, 10.73) * mm, "end": v(696.3, 11.01) * mm});
            skLineSegment(sketch, "E5817", {"start": v(696.3, 11.01) * mm, "end": v(696, 11.1) * mm});
            skLineSegment(sketch, "E5818", {"start": v(696, 11.1) * mm, "end": v(695.94, 11.12) * mm});
            skLineSegment(sketch, "E5819", {"start": v(695.94, 11.12) * mm, "end": v(695.44, 11.3) * mm});
            skLineSegment(sketch, "E5820", {"start": v(695.44, 11.3) * mm, "end": v(695.39, 11.31) * mm});
            skLineSegment(sketch, "E5821", {"start": v(695.39, 11.31) * mm, "end": v(694.45, 11.7) * mm});
            skLineSegment(sketch, "E5822", {"start": v(694.45, 11.7) * mm, "end": v(689.88, 14.27) * mm});
            skLineSegment(sketch, "E5823", {"start": v(689.88, 14.27) * mm, "end": v(685.4, 17.06) * mm});
            skLineSegment(sketch, "E5824", {"start": v(685.4, 17.06) * mm, "end": v(684.52, 17.57) * mm});
            skLineSegment(sketch, "E5825", {"start": v(684.52, 17.57) * mm, "end": v(683.98, 17.88) * mm});
            skLineSegment(sketch, "E5826", {"start": v(683.98, 17.88) * mm, "end": v(681.18, 19.32) * mm});
            skLineSegment(sketch, "E5827", {"start": v(681.18, 19.32) * mm, "end": v(678.27, 20.49) * mm});
            skLineSegment(sketch, "E5828", {"start": v(678.27, 20.49) * mm, "end": v(677.67, 20.67) * mm});
            skLineSegment(sketch, "E5829", {"start": v(677.67, 20.67) * mm, "end": v(677.48, 20.73) * mm});
            skLineSegment(sketch, "E5830", {"start": v(677.48, 20.73) * mm, "end": v(675.57, 21.18) * mm});
            skLineSegment(sketch, "E5831", {"start": v(675.57, 21.18) * mm, "end": v(675.37, 21.22) * mm});
            skLineSegment(sketch, "E5832", {"start": v(675.37, 21.22) * mm, "end": v(674.47, 21.39) * mm});
            skLineSegment(sketch, "E5833", {"start": v(674.47, 21.39) * mm, "end": v(669.99, 21.47) * mm});
            skLineSegment(sketch, "E5834", {"start": v(669.99, 21.47) * mm, "end": v(665.51, 21.46) * mm});
            skLineSegment(sketch, "E5835", {"start": v(665.51, 21.46) * mm, "end": v(664.6, 21.58) * mm});
            skLineSegment(sketch, "E5836", {"start": v(664.6, 21.58) * mm, "end": v(664, 21.67) * mm});
            skLineSegment(sketch, "E5837", {"start": v(664, 21.67) * mm, "end": v(662.24, 22.16) * mm});
            skLineSegment(sketch, "E5838", {"start": v(662.24, 22.16) * mm, "end": v(659.82, 23.09) * mm});
            skLineSegment(sketch, "E5839", {"start": v(659.82, 23.09) * mm, "end": v(657.46, 24.21) * mm});
            skLineSegment(sketch, "E5840", {"start": v(657.46, 24.21) * mm, "end": v(655.82, 25.07) * mm});
            skLineSegment(sketch, "E5841", {"start": v(655.82, 25.07) * mm, "end": v(655.28, 25.36) * mm});
            skLineSegment(sketch, "E5842", {"start": v(655.28, 25.36) * mm, "end": v(654.92, 25.55) * mm});
            skLineSegment(sketch, "E5843", {"start": v(654.92, 25.55) * mm, "end": v(653.27, 26.72) * mm});
            skLineSegment(sketch, "E5844", {"start": v(653.27, 26.72) * mm, "end": v(651.64, 27.93) * mm});
            skLineSegment(sketch, "E5845", {"start": v(651.64, 27.93) * mm, "end": v(651.29, 28.14) * mm});
            skLineSegment(sketch, "E5846", {"start": v(651.29, 28.14) * mm, "end": v(650.96, 28.34) * mm});
            skLineSegment(sketch, "E5847", {"start": v(650.96, 28.34) * mm, "end": v(649.9, 28.79) * mm});
            skLineSegment(sketch, "E5848", {"start": v(649.9, 28.79) * mm, "end": v(648.51, 29.17) * mm});
            skLineSegment(sketch, "E5849", {"start": v(648.51, 29.17) * mm, "end": v(647.15, 29.49) * mm});
            skLineSegment(sketch, "E5850", {"start": v(647.15, 29.49) * mm, "end": v(646.13, 29.81) * mm});
            skLineSegment(sketch, "E5851", {"start": v(646.13, 29.81) * mm, "end": v(645.81, 29.97) * mm});
            skLineSegment(sketch, "E5852", {"start": v(645.81, 29.97) * mm, "end": v(645.54, 30.1) * mm});
            skLineSegment(sketch, "E5853", {"start": v(645.54, 30.1) * mm, "end": v(644.8, 30.6) * mm});
            skLineSegment(sketch, "E5854", {"start": v(644.8, 30.6) * mm, "end": v(643.87, 31.38) * mm});
            skLineSegment(sketch, "E5855", {"start": v(643.87, 31.38) * mm, "end": v(642.89, 32.16) * mm});
            skLineSegment(sketch, "E5856", {"start": v(642.89, 32.16) * mm, "end": v(642.06, 32.67) * mm});
            skLineSegment(sketch, "E5857", {"start": v(642.06, 32.67) * mm, "end": v(641.76, 32.8) * mm});
            skLineSegment(sketch, "E5858", {"start": v(641.76, 32.8) * mm, "end": v(641.13, 33.06) * mm});
            skLineSegment(sketch, "E5859", {"start": v(641.13, 33.06) * mm, "end": v(637.84, 33.68) * mm});
            skLineSegment(sketch, "E5860", {"start": v(637.84, 33.68) * mm, "end": v(634.52, 34.1) * mm});
            skLineSegment(sketch, "E5861", {"start": v(634.52, 34.1) * mm, "end": v(633.87, 34.27) * mm});
            skLineSegment(sketch, "E5862", {"start": v(633.87, 34.27) * mm, "end": v(632.56, 34.6) * mm});
            skLineSegment(sketch, "E5863", {"start": v(632.56, 34.6) * mm, "end": v(628.74, 35.95) * mm});
            skLineSegment(sketch, "E5864", {"start": v(628.74, 35.95) * mm, "end": v(623.73, 38) * mm});
            skLineSegment(sketch, "E5865", {"start": v(623.73, 38) * mm, "end": v(618.66, 39.86) * mm});
            skLineSegment(sketch, "E5866", {"start": v(618.66, 39.86) * mm, "end": v(614.67, 40.82) * mm});
            skLineSegment(sketch, "E5867", {"start": v(614.67, 40.82) * mm, "end": v(613.32, 40.95) * mm});
            skLineSegment(sketch, "E5868", {"start": v(613.32, 40.95) * mm, "end": v(612.7, 41.56) * mm});
            skLineSegment(sketch, "E5869", {"start": v(612.7, 41.56) * mm, "end": v(610.47, 43.04) * mm});
            skLineSegment(sketch, "E5870", {"start": v(610.47, 43.04) * mm, "end": v(607.36, 44.36) * mm});
            skLineSegment(sketch, "E5871", {"start": v(607.36, 44.36) * mm, "end": v(604.16, 45.44) * mm});
            skLineSegment(sketch, "E5872", {"start": v(604.16, 45.44) * mm, "end": v(601.74, 46.4) * mm});
            skLineSegment(sketch, "E5873", {"start": v(601.74, 46.4) * mm, "end": v(600.99, 46.82) * mm});
            skLineSegment(sketch, "E5874", {"start": v(600.99, 46.82) * mm, "end": v(600.4, 47.16) * mm});
            skLineSegment(sketch, "E5875", {"start": v(600.4, 47.16) * mm, "end": v(598.76, 48.4) * mm});
            skLineSegment(sketch, "E5876", {"start": v(598.76, 48.4) * mm, "end": v(596.65, 50.34) * mm});
            skLineSegment(sketch, "E5877", {"start": v(596.65, 50.34) * mm, "end": v(594.55, 52.36) * mm});
            skLineSegment(sketch, "E5878", {"start": v(594.55, 52.36) * mm, "end": v(592.95, 53.75) * mm});
            skLineSegment(sketch, "E5879", {"start": v(592.95, 53.75) * mm, "end": v(592.37, 54.15) * mm});
            skLineSegment(sketch, "E5880", {"start": v(592.37, 54.15) * mm, "end": v(591.92, 54.47) * mm});
            skLineSegment(sketch, "E5881", {"start": v(591.92, 54.47) * mm, "end": v(589.5, 55.73) * mm});
            skLineSegment(sketch, "E5882", {"start": v(589.5, 55.73) * mm, "end": v(587.13, 57) * mm});
            skLineSegment(sketch, "E5883", {"start": v(587.13, 57) * mm, "end": v(586.7, 57.3) * mm});
            skLineSegment(sketch, "E5884", {"start": v(586.7, 57.3) * mm, "end": v(585.44, 58.23) * mm});
            skLineSegment(sketch, "E5885", {"start": v(585.44, 58.23) * mm, "end": v(581.7, 61.03) * mm});
            skLineSegment(sketch, "E5886", {"start": v(581.7, 61.03) * mm, "end": v(576.66, 65.05) * mm});
            skLineSegment(sketch, "E5887", {"start": v(576.66, 65.05) * mm, "end": v(571.92, 69.37) * mm});
            skLineSegment(sketch, "E5888", {"start": v(571.92, 69.37) * mm, "end": v(568.75, 72.78) * mm});
            skLineSegment(sketch, "E5889", {"start": v(568.75, 72.78) * mm, "end": v(567.81, 74) * mm});
            skLineSegment(sketch, "E5890", {"start": v(567.81, 74) * mm, "end": v(566.7, 75.45) * mm});
            skLineSegment(sketch, "E5891", {"start": v(566.7, 75.45) * mm, "end": v(565.98, 73.78) * mm});
            skLineSegment(sketch, "E5892", {"start": v(565.98, 73.78) * mm, "end": v(565.9, 73.57) * mm});
            skLineSegment(sketch, "E5893", {"start": v(565.9, 73.57) * mm, "end": v(565.34, 73.06) * mm});
            skLineSegment(sketch, "E5894", {"start": v(565.34, 73.06) * mm, "end": v(564.36, 72.7) * mm});
            skLineSegment(sketch, "E5895", {"start": v(564.36, 72.7) * mm, "end": v(563.28, 72.6) * mm});
            skLineSegment(sketch, "E5896", {"start": v(563.28, 72.6) * mm, "end": v(562.56, 72.6) * mm});
            skLineSegment(sketch, "E5897", {"start": v(562.56, 72.6) * mm, "end": v(562.32, 72.62) * mm});
            skLineSegment(sketch, "E5898", {"start": v(562.32, 72.62) * mm, "end": v(561.81, 72.65) * mm});
            skLineSegment(sketch, "E5899", {"start": v(561.81, 72.65) * mm, "end": v(561.47, 72.28) * mm});
            skLineSegment(sketch, "E5900", {"start": v(561.47, 72.28) * mm, "end": v(560.9, 71.68) * mm});
            skLineSegment(sketch, "E5901", {"start": v(560.9, 71.68) * mm, "end": v(558.97, 70.1) * mm});
            skLineSegment(sketch, "E5902", {"start": v(558.97, 70.1) * mm, "end": v(555.9, 68.23) * mm});
            skLineSegment(sketch, "E5903", {"start": v(555.9, 68.23) * mm, "end": v(552.59, 66.8) * mm});
            skLineSegment(sketch, "E5904", {"start": v(552.59, 66.8) * mm, "end": v(550.18, 66.1) * mm});
            skLineSegment(sketch, "E5905", {"start": v(550.18, 66.1) * mm, "end": v(549.35, 65.96) * mm});
            skLineSegment(sketch, "E5906", {"start": v(549.35, 65.96) * mm, "end": v(549.19, 65.93) * mm});
            skLineSegment(sketch, "E5907", {"start": v(549.19, 65.93) * mm, "end": v(548.68, 65.97) * mm});
            skLineSegment(sketch, "E5908", {"start": v(548.68, 65.97) * mm, "end": v(547.85, 66.13) * mm});
            skLineSegment(sketch, "E5909", {"start": v(547.85, 66.13) * mm, "end": v(546.96, 66.3) * mm});
            skLineSegment(sketch, "E5910", {"start": v(546.96, 66.3) * mm, "end": v(546.32, 66.36) * mm});
            skLineSegment(sketch, "E5911", {"start": v(546.32, 66.36) * mm, "end": v(546.11, 66.34) * mm});
            skLineSegment(sketch, "E5912", {"start": v(546.11, 66.34) * mm, "end": v(545.8, 66.32) * mm});
            skLineSegment(sketch, "E5913", {"start": v(545.8, 66.32) * mm, "end": v(544.85, 66.1) * mm});
            skLineSegment(sketch, "E5914", {"start": v(544.85, 66.1) * mm, "end": v(543.66, 65.68) * mm});
            skLineSegment(sketch, "E5915", {"start": v(543.66, 65.68) * mm, "end": v(542.49, 65.24) * mm});
            skLineSegment(sketch, "E5916", {"start": v(542.49, 65.24) * mm, "end": v(541.6, 64.96) * mm});
            skLineSegment(sketch, "E5917", {"start": v(541.6, 64.96) * mm, "end": v(541.29, 64.9) * mm});
            skLineSegment(sketch, "E5918", {"start": v(541.29, 64.9) * mm, "end": v(539.9, 64.66) * mm});
            skLineSegment(sketch, "E5919", {"start": v(539.9, 64.66) * mm, "end": v(532.94, 63.9) * mm});
            skLineSegment(sketch, "E5920", {"start": v(532.94, 63.9) * mm, "end": v(525.97, 63.3) * mm});
            skLineSegment(sketch, "E5921", {"start": v(525.97, 63.3) * mm, "end": v(524.58, 63.14) * mm});
            skLineSegment(sketch, "E5922", {"start": v(524.58, 63.14) * mm, "end": v(522.67, 62.91) * mm});
            skLineSegment(sketch, "E5923", {"start": v(522.67, 62.91) * mm, "end": v(513.1, 62.27) * mm});
            skLineSegment(sketch, "E5924", {"start": v(513.1, 62.27) * mm, "end": v(503.5, 62.08) * mm});
            skLineSegment(sketch, "E5925", {"start": v(503.5, 62.08) * mm, "end": v(501.6, 62.08) * mm});
            skLineSegment(sketch, "E5926", {"start": v(501.6, 62.08) * mm, "end": v(500.12, 62.1) * mm});
            skLineSegment(sketch, "E5927", {"start": v(500.12, 62.1) * mm, "end": v(495.71, 62.42) * mm});
            skLineSegment(sketch, "E5928", {"start": v(495.71, 62.42) * mm, "end": v(489.86, 63.11) * mm});
            skLineSegment(sketch, "E5929", {"start": v(489.86, 63.11) * mm, "end": v(484.03, 63.82) * mm});
            skLineSegment(sketch, "E5930", {"start": v(484.03, 63.82) * mm, "end": v(479.64, 64.18) * mm});
            skLineSegment(sketch, "E5931", {"start": v(479.64, 64.18) * mm, "end": v(478.18, 64.2) * mm});
            skLineSegment(sketch, "E5932", {"start": v(478.18, 64.2) * mm, "end": v(477.77, 64.22) * mm});
            skLineSegment(sketch, "E5933", {"start": v(477.77, 64.22) * mm, "end": v(476.55, 64.07) * mm});
            skLineSegment(sketch, "E5934", {"start": v(476.55, 64.07) * mm, "end": v(474.78, 63.73) * mm});
            skLineSegment(sketch, "E5935", {"start": v(474.78, 63.73) * mm, "end": v(473.07, 63.46) * mm});
            skLineSegment(sketch, "E5936", {"start": v(473.07, 63.46) * mm, "end": v(471.98, 63.42) * mm});
            skLineSegment(sketch, "E5937", {"start": v(471.98, 63.42) * mm, "end": v(471.64, 63.49) * mm});
            skLineSegment(sketch, "E5938", {"start": v(471.64, 63.49) * mm, "end": v(470.97, 63.63) * mm});
            skLineSegment(sketch, "E5939", {"start": v(470.97, 63.63) * mm, "end": v(469.1, 64.7) * mm});
            skLineSegment(sketch, "E5940", {"start": v(469.1, 64.7) * mm, "end": v(466.83, 66.88) * mm});
            skLineSegment(sketch, "E5941", {"start": v(466.83, 66.88) * mm, "end": v(464.85, 69.44) * mm});
            skLineSegment(sketch, "E5942", {"start": v(464.85, 69.44) * mm, "end": v(463.66, 71.22) * mm});
            skLineSegment(sketch, "E5943", {"start": v(463.66, 71.22) * mm, "end": v(463.26, 71.82) * mm});
            skLineSegment(sketch, "E5944", {"start": v(463.26, 71.82) * mm, "end": v(462.75, 72.6) * mm});
            skLineSegment(sketch, "E5945", {"start": v(462.75, 72.6) * mm, "end": v(461.91, 72.2) * mm});
            skLineSegment(sketch, "E5946", {"start": v(461.91, 72.2) * mm, "end": v(461.44, 71.96) * mm});
            skLineSegment(sketch, "E5947", {"start": v(461.44, 71.96) * mm, "end": v(460.05, 71.27) * mm});
            skLineSegment(sketch, "E5948", {"start": v(460.05, 71.27) * mm, "end": v(457.96, 70.23) * mm});
            skLineSegment(sketch, "E5949", {"start": v(457.96, 70.23) * mm, "end": v(455.69, 69.16) * mm});
            skLineSegment(sketch, "E5950", {"start": v(455.69, 69.16) * mm, "end": v(453.33, 68.12) * mm});
            skLineSegment(sketch, "E5951", {"start": v(453.33, 68.12) * mm, "end": v(450.94, 67.2) * mm});
            skLineSegment(sketch, "E5952", {"start": v(450.94, 67.2) * mm, "end": v(448.6, 66.5) * mm});
            skLineSegment(sketch, "E5953", {"start": v(448.6, 66.5) * mm, "end": v(446.38, 66.05) * mm});
            skLineSegment(sketch, "E5954", {"start": v(446.38, 66.05) * mm, "end": v(444.85, 65.94) * mm});
            skLineSegment(sketch, "E5955", {"start": v(444.85, 65.94) * mm, "end": v(444.35, 65.97) * mm});
            skLineSegment(sketch, "E5956", {"start": v(444.35, 65.97) * mm, "end": v(443.94, 66) * mm});
            skLineSegment(sketch, "E5957", {"start": v(443.94, 66) * mm, "end": v(442.73, 66.38) * mm});
            skLineSegment(sketch, "E5958", {"start": v(442.73, 66.38) * mm, "end": v(440.68, 67.24) * mm});
            skLineSegment(sketch, "E5959", {"start": v(440.68, 67.24) * mm, "end": v(438.65, 68.23) * mm});
            skLineSegment(sketch, "E5960", {"start": v(438.65, 68.23) * mm, "end": v(437.46, 68.83) * mm});
            skLineSegment(sketch, "E5961", {"start": v(437.46, 68.83) * mm, "end": v(437.06, 69.03) * mm});
            skLineSegment(sketch, "E5962", {"start": v(437.06, 69.03) * mm, "end": v(435.1, 69.97) * mm});
            skLineSegment(sketch, "E5963", {"start": v(435.1, 69.97) * mm, "end": v(425.04, 74.07) * mm});
            skLineSegment(sketch, "E5964", {"start": v(425.04, 74.07) * mm, "end": v(414.86, 77.82) * mm});
            skLineSegment(sketch, "E5965", {"start": v(414.86, 77.82) * mm, "end": v(412.83, 78.58) * mm});
            skLineSegment(sketch, "E5966", {"start": v(412.83, 78.58) * mm, "end": v(410.5, 79.46) * mm});
            skLineSegment(sketch, "E5967", {"start": v(410.5, 79.46) * mm, "end": v(403.55, 82.3) * mm});
            skLineSegment(sketch, "E5968", {"start": v(403.55, 82.3) * mm, "end": v(394.43, 86.32) * mm});
            skLineSegment(sketch, "E5969", {"start": v(394.43, 86.32) * mm, "end": v(385.4, 90.52) * mm});
            skLineSegment(sketch, "E5970", {"start": v(385.4, 90.52) * mm, "end": v(378.62, 93.7) * mm});
            skLineSegment(sketch, "E5971", {"start": v(378.62, 93.7) * mm, "end": v(376.35, 94.75) * mm});
            skLineSegment(sketch, "E5972", {"start": v(376.35, 94.75) * mm, "end": v(376.09, 94.88) * mm});
            skLineSegment(sketch, "E5973", {"start": v(376.09, 94.88) * mm, "end": v(375.8, 94.84) * mm});
            skLineSegment(sketch, "E5974", {"start": v(375.8, 94.84) * mm, "end": v(374.77, 94.74) * mm});
            skLineSegment(sketch, "E5975", {"start": v(374.77, 94.74) * mm, "end": v(371.63, 94.99) * mm});
            skLineSegment(sketch, "E5976", {"start": v(371.63, 94.99) * mm, "end": v(367.84, 96.1) * mm});
            skLineSegment(sketch, "E5977", {"start": v(367.84, 96.1) * mm, "end": v(364.27, 97.88) * mm});
            skLineSegment(sketch, "E5978", {"start": v(364.27, 97.88) * mm, "end": v(361.6, 99.45) * mm});
            skLineSegment(sketch, "E5979", {"start": v(361.6, 99.45) * mm, "end": v(360.71, 99.98) * mm});
            skLineSegment(sketch, "E5980", {"start": v(360.71, 99.98) * mm, "end": v(360.01, 100.4) * mm});
            skLineSegment(sketch, "E5981", {"start": v(360.01, 100.4) * mm, "end": v(358.04, 101.88) * mm});
            skLineSegment(sketch, "E5982", {"start": v(358.04, 101.88) * mm, "end": v(355.62, 104.05) * mm});
            skLineSegment(sketch, "E5983", {"start": v(355.62, 104.05) * mm, "end": v(353.25, 106.27) * mm});
            skLineSegment(sketch, "E5984", {"start": v(353.25, 106.27) * mm, "end": v(351.39, 107.86) * mm});
            skLineSegment(sketch, "E5985", {"start": v(351.39, 107.86) * mm, "end": v(350.73, 108.33) * mm});
            skLineSegment(sketch, "E5986", {"start": v(350.73, 108.33) * mm, "end": v(350.18, 108.74) * mm});
            skLineSegment(sketch, "E5987", {"start": v(350.18, 108.74) * mm, "end": v(347.24, 110.58) * mm});
            skLineSegment(sketch, "E5988", {"start": v(347.24, 110.58) * mm, "end": v(344.21, 112.3) * mm});
            skLineSegment(sketch, "E5989", {"start": v(344.21, 112.3) * mm, "end": v(343.62, 112.64) * mm});
            skLineSegment(sketch, "E5990", {"start": v(343.62, 112.64) * mm, "end": v(342.45, 113.33) * mm});
            skLineSegment(sketch, "E5991", {"start": v(342.45, 113.33) * mm, "end": v(338.77, 115.13) * mm});
            skLineSegment(sketch, "E5992", {"start": v(338.77, 115.13) * mm, "end": v(333.75, 117.3) * mm});
            skLineSegment(sketch, "E5993", {"start": v(333.75, 117.3) * mm, "end": v(328.7, 119.42) * mm});
            skLineSegment(sketch, "E5994", {"start": v(328.7, 119.42) * mm, "end": v(324.98, 121.14) * mm});
            skLineSegment(sketch, "E5995", {"start": v(324.98, 121.14) * mm, "end": v(323.78, 121.8) * mm});
            skLineSegment(sketch, "E5996", {"start": v(323.78, 121.8) * mm, "end": v(323.55, 121.92) * mm});
            skLineSegment(sketch, "E5997", {"start": v(323.55, 121.92) * mm, "end": v(322.95, 122.4) * mm});
            skLineSegment(sketch, "E5998", {"start": v(322.95, 122.4) * mm, "end": v(322.18, 123.17) * mm});
            skLineSegment(sketch, "E5999", {"start": v(322.18, 123.17) * mm, "end": v(321.38, 123.95) * mm});
            skLineSegment(sketch, "E6000", {"start": v(321.38, 123.95) * mm, "end": v(320.72, 124.49) * mm});
            skLineSegment(sketch, "E6001", {"start": v(320.72, 124.49) * mm, "end": v(320.48, 124.63) * mm});
            skLineSegment(sketch, "E6002", {"start": v(320.48, 124.63) * mm, "end": v(319.9, 124.96) * mm});
            skLineSegment(sketch, "E6003", {"start": v(319.9, 124.96) * mm, "end": v(318.01, 125.77) * mm});
            skLineSegment(sketch, "E6004", {"start": v(318.01, 125.77) * mm, "end": v(315.43, 126.63) * mm});
            skLineSegment(sketch, "E6005", {"start": v(315.43, 126.63) * mm, "end": v(312.85, 127.46) * mm});
            skLineSegment(sketch, "E6006", {"start": v(312.85, 127.46) * mm, "end": v(310.97, 128.2) * mm});
            skLineSegment(sketch, "E6007", {"start": v(310.97, 128.2) * mm, "end": v(310.38, 128.51) * mm});
            skLineSegment(sketch, "E6008", {"start": v(310.38, 128.51) * mm, "end": v(310.2, 128.6) * mm});
            skLineSegment(sketch, "E6009", {"start": v(310.2, 128.6) * mm, "end": v(309.7, 129) * mm});
            skLineSegment(sketch, "E6010", {"start": v(309.7, 129) * mm, "end": v(309.08, 129.6) * mm});
            skLineSegment(sketch, "E6011", {"start": v(309.08, 129.6) * mm, "end": v(308.41, 130.18) * mm});
            skLineSegment(sketch, "E6012", {"start": v(308.41, 130.18) * mm, "end": v(307.82, 130.57) * mm});
            skLineSegment(sketch, "E6013", {"start": v(307.82, 130.57) * mm, "end": v(307.6, 130.66) * mm});
            skLineSegment(sketch, "E6014", {"start": v(307.6, 130.66) * mm, "end": v(306.33, 131.2) * mm});
            skLineSegment(sketch, "E6015", {"start": v(306.33, 131.2) * mm, "end": v(302.36, 132.54) * mm});
            skLineSegment(sketch, "E6016", {"start": v(302.36, 132.54) * mm, "end": v(296.9, 133.93) * mm});
            skLineSegment(sketch, "E6017", {"start": v(296.9, 133.93) * mm, "end": v(291.38, 135) * mm});
            skLineSegment(sketch, "E6018", {"start": v(291.38, 135) * mm, "end": v(287.25, 135.72) * mm});
            skLineSegment(sketch, "E6019", {"start": v(287.25, 135.72) * mm, "end": v(285.88, 135.96) * mm});
            skLineSegment(sketch, "E6020", {"start": v(285.88, 135.96) * mm, "end": v(285.4, 136.32) * mm});
            skLineSegment(sketch, "E6021", {"start": v(285.4, 136.32) * mm, "end": v(283.76, 137.12) * mm});
            skLineSegment(sketch, "E6022", {"start": v(283.76, 137.12) * mm, "end": v(281.56, 137.62) * mm});
            skLineSegment(sketch, "E6023", {"start": v(281.56, 137.62) * mm, "end": v(279.28, 137.83) * mm});
            skLineSegment(sketch, "E6024", {"start": v(279.28, 137.83) * mm, "end": v(277.5, 138) * mm});
            skLineSegment(sketch, "E6025", {"start": v(277.5, 138) * mm, "end": v(276.9, 138.1) * mm});
            skLineSegment(sketch, "E6026", {"start": v(276.9, 138.1) * mm, "end": v(276.64, 138.11) * mm});
            skLineSegment(sketch, "E6027", {"start": v(276.64, 138.11) * mm, "end": v(275.91, 138.1) * mm});
            skLineSegment(sketch, "E6028", {"start": v(275.91, 138.1) * mm, "end": v(274.83, 138.05) * mm});
            skLineSegment(sketch, "E6029", {"start": v(274.83, 138.05) * mm, "end": v(273.48, 137.92) * mm});
            skLineSegment(sketch, "E6030", {"start": v(273.48, 137.92) * mm, "end": v(271.97, 137.68) * mm});
            skLineSegment(sketch, "E6031", {"start": v(271.97, 137.68) * mm, "end": v(270.4, 137.3) * mm});
            skLineSegment(sketch, "E6032", {"start": v(270.4, 137.3) * mm, "end": v(268.88, 136.72) * mm});
            skLineSegment(sketch, "E6033", {"start": v(268.88, 136.72) * mm, "end": v(267.82, 136.17) * mm});
            skLineSegment(sketch, "E6034", {"start": v(267.82, 136.17) * mm, "end": v(267.5, 135.94) * mm});
            skLineSegment(sketch, "E6035", {"start": v(267.5, 135.94) * mm, "end": v(266.94, 135.55) * mm});
            skLineSegment(sketch, "E6036", {"start": v(266.94, 135.55) * mm, "end": v(265.3, 134.31) * mm});
            skLineSegment(sketch, "E6037", {"start": v(265.3, 134.31) * mm, "end": v(263.77, 133.07) * mm});
            skLineSegment(sketch, "E6038", {"start": v(263.77, 133.07) * mm, "end": v(262.88, 132.27) * mm});
            skLineSegment(sketch, "E6039", {"start": v(262.88, 132.27) * mm, "end": v(262.59, 131.99) * mm});
            skLineSegment(sketch, "E6040", {"start": v(878.18, 4) * mm, "end": v(879.26, 5.32) * mm});
            skLineSegment(sketch, "E6041", {"start": v(879.26, 5.32) * mm, "end": v(882.7, 9.1) * mm});
            skLineSegment(sketch, "E6042", {"start": v(882.7, 9.1) * mm, "end": v(887.61, 14.01) * mm});
            skLineSegment(sketch, "E6043", {"start": v(887.61, 14.01) * mm, "end": v(892.68, 18.77) * mm});
            skLineSegment(sketch, "E6044", {"start": v(892.68, 18.77) * mm, "end": v(896.44, 22.26) * mm});
            skLineSegment(sketch, "E6045", {"start": v(896.44, 22.26) * mm, "end": v(897.69, 23.44) * mm});
            skLineSegment(sketch, "E6046", {"start": v(897.69, 23.44) * mm, "end": v(898, 23.74) * mm});
            skLineSegment(sketch, "E6047", {"start": v(898, 23.74) * mm, "end": v(898.82, 24.75) * mm});
            skLineSegment(sketch, "E6048", {"start": v(898.82, 24.75) * mm, "end": v(899.83, 26.2) * mm});
            skLineSegment(sketch, "E6049", {"start": v(899.83, 26.2) * mm, "end": v(900.85, 27.69) * mm});
            skLineSegment(sketch, "E6050", {"start": v(900.85, 27.69) * mm, "end": v(901.7, 28.75) * mm});
            skLineSegment(sketch, "E6051", {"start": v(901.7, 28.75) * mm, "end": v(902.01, 29.06) * mm});
            skLineSegment(sketch, "E6052", {"start": v(902.01, 29.06) * mm, "end": v(902.44, 29.47) * mm});
            skLineSegment(sketch, "E6053", {"start": v(902.44, 29.47) * mm, "end": v(904.56, 31.46) * mm});
            skLineSegment(sketch, "E6054", {"start": v(904.56, 31.46) * mm, "end": v(906.63, 33.5) * mm});
            skLineSegment(sketch, "E6055", {"start": v(906.63, 33.5) * mm, "end": v(907.02, 33.94) * mm});
            skLineSegment(sketch, "E6056", {"start": v(907.02, 33.94) * mm, "end": v(907.4, 34.36) * mm});
            skLineSegment(sketch, "E6057", {"start": v(907.4, 34.36) * mm, "end": v(909.42, 36.36) * mm});
            skLineSegment(sketch, "E6058", {"start": v(909.42, 36.36) * mm, "end": v(911.5, 38.32) * mm});
            skLineSegment(sketch, "E6059", {"start": v(911.5, 38.32) * mm, "end": v(911.9, 38.73) * mm});
            skLineSegment(sketch, "E6060", {"start": v(911.9, 38.73) * mm, "end": v(912.04, 38.86) * mm});
            skLineSegment(sketch, "E6061", {"start": v(912.04, 38.86) * mm, "end": v(912.44, 39.28) * mm});
            skLineSegment(sketch, "E6062", {"start": v(912.44, 39.28) * mm, "end": v(913.13, 40.03) * mm});
            skLineSegment(sketch, "E6063", {"start": v(913.13, 40.03) * mm, "end": v(913.88, 40.92) * mm});
            skLineSegment(sketch, "E6064", {"start": v(913.88, 40.92) * mm, "end": v(914.6, 41.9) * mm});
            skLineSegment(sketch, "E6065", {"start": v(914.6, 41.9) * mm, "end": v(915.2, 42.9) * mm});
            skLineSegment(sketch, "E6066", {"start": v(915.2, 42.9) * mm, "end": v(915.59, 43.88) * mm});
            skLineSegment(sketch, "E6067", {"start": v(915.59, 43.88) * mm, "end": v(915.67, 44.79) * mm});
            skLineSegment(sketch, "E6068", {"start": v(915.67, 44.79) * mm, "end": v(915.48, 45.41) * mm});
            skLineSegment(sketch, "E6069", {"start": v(915.48, 45.41) * mm, "end": v(915.35, 45.57) * mm});
            skLineSegment(sketch, "E6070", {"start": v(915.35, 45.57) * mm, "end": v(915.1, 45.89) * mm});
            skLineSegment(sketch, "E6071", {"start": v(915.1, 45.89) * mm, "end": v(913.98, 46.53) * mm});
            skLineSegment(sketch, "E6072", {"start": v(913.98, 46.53) * mm, "end": v(912.34, 46.53) * mm});
            skLineSegment(sketch, "E6073", {"start": v(912.34, 46.53) * mm, "end": v(910.52, 45.8) * mm});
            skLineSegment(sketch, "E6074", {"start": v(910.52, 45.8) * mm, "end": v(908.59, 44.6) * mm});
            skLineSegment(sketch, "E6075", {"start": v(908.59, 44.6) * mm, "end": v(906.65, 43.18) * mm});
            skLineSegment(sketch, "E6076", {"start": v(906.65, 43.18) * mm, "end": v(904.78, 41.77) * mm});
            skLineSegment(sketch, "E6077", {"start": v(904.78, 41.77) * mm, "end": v(903.07, 40.61) * mm});
            skLineSegment(sketch, "E6078", {"start": v(903.07, 40.61) * mm, "end": v(901.99, 40.06) * mm});
            skLineSegment(sketch, "E6079", {"start": v(901.99, 40.06) * mm, "end": v(901.6, 39.97) * mm});
            skLineSegment(sketch, "E6080", {"start": v(901.6, 39.97) * mm, "end": v(898.24, 36.5) * mm});
            skLineSegment(sketch, "E6081", {"start": v(898.24, 36.5) * mm, "end": v(864.98, 1.49) * mm});
            skLineSegment(sketch, "E6082", {"start": v(864.98, 1.49) * mm, "end": v(861.66, -2.02) * mm});
            skLineSegment(sketch, "E6083", {"start": v(861.66, -2.02) * mm, "end": v(861.4, -2.3) * mm});
            skLineSegment(sketch, "E6084", {"start": v(861.4, -2.3) * mm, "end": v(860.63, -3.19) * mm});
            skLineSegment(sketch, "E6085", {"start": v(860.63, -3.19) * mm, "end": v(859.51, -4.5) * mm});
            skLineSegment(sketch, "E6086", {"start": v(859.51, -4.5) * mm, "end": v(858.32, -5.8) * mm});
            skLineSegment(sketch, "E6087", {"start": v(858.32, -5.8) * mm, "end": v(857.05, -7) * mm});
            skLineSegment(sketch, "E6088", {"start": v(857.05, -7) * mm, "end": v(855.68, -7.92) * mm});
            skLineSegment(sketch, "E6089", {"start": v(855.68, -7.92) * mm, "end": v(854.2, -8.46) * mm});
            skLineSegment(sketch, "E6090", {"start": v(854.2, -8.46) * mm, "end": v(852.64, -8.48) * mm});
            skLineSegment(sketch, "E6091", {"start": v(852.64, -8.48) * mm, "end": v(851.34, -8.07) * mm});
            skLineSegment(sketch, "E6092", {"start": v(851.34, -8.07) * mm, "end": v(850.96, -7.84) * mm});
            skLineSegment(sketch, "E6093", {"start": v(850.96, -7.84) * mm, "end": v(850.4, -7.52) * mm});
            skLineSegment(sketch, "E6094", {"start": v(850.4, -7.52) * mm, "end": v(850.42, -6.86) * mm});
            skLineSegment(sketch, "E6095", {"start": v(850.42, -6.86) * mm, "end": v(850.46, -6.12) * mm});
            skLineSegment(sketch, "E6096", {"start": v(850.46, -6.12) * mm, "end": v(851.22, -3.92) * mm});
            skLineSegment(sketch, "E6097", {"start": v(851.22, -3.92) * mm, "end": v(852.95, -1.58) * mm});
            skLineSegment(sketch, "E6098", {"start": v(852.95, -1.58) * mm, "end": v(855.19, 0.41) * mm});
            skLineSegment(sketch, "E6099", {"start": v(855.19, 0.41) * mm, "end": v(856.93, 1.82) * mm});
            skLineSegment(sketch, "E6100", {"start": v(856.93, 1.82) * mm, "end": v(857.5, 2.31) * mm});
            skLineSegment(sketch, "E6101", {"start": v(857.5, 2.31) * mm, "end": v(858.91, 3.58) * mm});
            skLineSegment(sketch, "E6102", {"start": v(858.91, 3.58) * mm, "end": v(865.57, 10.35) * mm});
            skLineSegment(sketch, "E6103", {"start": v(865.57, 10.35) * mm, "end": v(872.16, 17.19) * mm});
            skLineSegment(sketch, "E6104", {"start": v(872.16, 17.19) * mm, "end": v(873.55, 18.48) * mm});
            skLineSegment(sketch, "E6105", {"start": v(873.55, 18.48) * mm, "end": v(874.21, 19.11) * mm});
            skLineSegment(sketch, "E6106", {"start": v(874.21, 19.11) * mm, "end": v(877.7, 22.31) * mm});
            skLineSegment(sketch, "E6107", {"start": v(877.7, 22.31) * mm, "end": v(880.94, 25.73) * mm});
            skLineSegment(sketch, "E6108", {"start": v(880.94, 25.73) * mm, "end": v(881.48, 26.46) * mm});
            skLineSegment(sketch, "E6109", {"start": v(881.48, 26.46) * mm, "end": v(881.61, 26.64) * mm});
            skLineSegment(sketch, "E6110", {"start": v(881.61, 26.64) * mm, "end": v(881.92, 27.25) * mm});
            skLineSegment(sketch, "E6111", {"start": v(881.92, 27.25) * mm, "end": v(882.27, 28.16) * mm});
            skLineSegment(sketch, "E6112", {"start": v(882.27, 28.16) * mm, "end": v(882.63, 29.1) * mm});
            skLineSegment(sketch, "E6113", {"start": v(882.63, 29.1) * mm, "end": v(882.98, 29.78) * mm});
            skLineSegment(sketch, "E6114", {"start": v(882.98, 29.78) * mm, "end": v(883.13, 29.98) * mm});
            skLineSegment(sketch, "E6115", {"start": v(883.13, 29.98) * mm, "end": v(883.35, 30.29) * mm});
            skLineSegment(sketch, "E6116", {"start": v(883.35, 30.29) * mm, "end": v(884.14, 31.1) * mm});
            skLineSegment(sketch, "E6117", {"start": v(884.14, 31.1) * mm, "end": v(885.3, 32.04) * mm});
            skLineSegment(sketch, "E6118", {"start": v(885.3, 32.04) * mm, "end": v(886.48, 32.95) * mm});
            skLineSegment(sketch, "E6119", {"start": v(886.48, 32.95) * mm, "end": v(887.33, 33.69) * mm});
            skLineSegment(sketch, "E6120", {"start": v(887.33, 33.69) * mm, "end": v(887.58, 33.96) * mm});
            skLineSegment(sketch, "E6121", {"start": v(887.58, 33.96) * mm, "end": v(887.83, 34.22) * mm});
            skLineSegment(sketch, "E6122", {"start": v(887.83, 34.22) * mm, "end": v(888.48, 35.1) * mm});
            skLineSegment(sketch, "E6123", {"start": v(888.48, 35.1) * mm, "end": v(889.26, 36.36) * mm});
            skLineSegment(sketch, "E6124", {"start": v(889.26, 36.36) * mm, "end": v(890.03, 37.65) * mm});
            skLineSegment(sketch, "E6125", {"start": v(890.03, 37.65) * mm, "end": v(890.66, 38.57) * mm});
            skLineSegment(sketch, "E6126", {"start": v(890.66, 38.57) * mm, "end": v(890.9, 38.86) * mm});
            skLineSegment(sketch, "E6127", {"start": v(890.9, 38.86) * mm, "end": v(891.23, 39.23) * mm});
            skLineSegment(sketch, "E6128", {"start": v(891.23, 39.23) * mm, "end": v(892.27, 40.3) * mm});
            skLineSegment(sketch, "E6129", {"start": v(892.27, 40.3) * mm, "end": v(893.71, 41.67) * mm});
            skLineSegment(sketch, "E6130", {"start": v(893.71, 41.67) * mm, "end": v(895.16, 43.02) * mm});
            skLineSegment(sketch, "E6131", {"start": v(895.16, 43.02) * mm, "end": v(896.55, 44.4) * mm});
            skLineSegment(sketch, "E6132", {"start": v(896.55, 44.4) * mm, "end": v(897.8, 45.86) * mm});
            skLineSegment(sketch, "E6133", {"start": v(897.8, 45.86) * mm, "end": v(898.84, 47.45) * mm});
            skLineSegment(sketch, "E6134", {"start": v(898.84, 47.45) * mm, "end": v(899.59, 49.22) * mm});
            skLineSegment(sketch, "E6135", {"start": v(899.59, 49.22) * mm, "end": v(899.94, 50.72) * mm});
            skLineSegment(sketch, "E6136", {"start": v(899.94, 50.72) * mm, "end": v(899.98, 51.22) * mm});
            skLineSegment(sketch, "E6137", {"start": v(899.98, 51.22) * mm, "end": v(899.04, 51.25) * mm});
            skLineSegment(sketch, "E6138", {"start": v(899.04, 51.25) * mm, "end": v(896.22, 50.74) * mm});
            skLineSegment(sketch, "E6139", {"start": v(896.22, 50.74) * mm, "end": v(893.03, 49.3) * mm});
            skLineSegment(sketch, "E6140", {"start": v(893.03, 49.3) * mm, "end": v(890.07, 47.26) * mm});
            skLineSegment(sketch, "E6141", {"start": v(890.07, 47.26) * mm, "end": v(887.75, 45.55) * mm});
            skLineSegment(sketch, "E6142", {"start": v(887.75, 45.55) * mm, "end": v(886.96, 45) * mm});
            skLineSegment(sketch, "E6143", {"start": v(886.96, 45) * mm, "end": v(885.63, 44.1) * mm});
            skLineSegment(sketch, "E6144", {"start": v(885.63, 44.1) * mm, "end": v(881.8, 41.16) * mm});
            skLineSegment(sketch, "E6145", {"start": v(881.8, 41.16) * mm, "end": v(877.07, 37.08) * mm});
            skLineSegment(sketch, "E6146", {"start": v(877.07, 37.08) * mm, "end": v(872.55, 32.78) * mm});
            skLineSegment(sketch, "E6147", {"start": v(872.55, 32.78) * mm, "end": v(869.14, 29.38) * mm});
            skLineSegment(sketch, "E6148", {"start": v(869.14, 29.38) * mm, "end": v(868, 28.25) * mm});
            skLineSegment(sketch, "E6149", {"start": v(868, 28.25) * mm, "end": v(867, 27.23) * mm});
            skLineSegment(sketch, "E6150", {"start": v(867, 27.23) * mm, "end": v(856.63, 17.28) * mm});
            skLineSegment(sketch, "E6151", {"start": v(856.63, 17.28) * mm, "end": v(855.6, 16.27) * mm});
            skLineSegment(sketch, "E6152", {"start": v(855.6, 16.27) * mm, "end": v(855.09, 15.77) * mm});
            skLineSegment(sketch, "E6153", {"start": v(855.09, 15.77) * mm, "end": v(853.64, 14.19) * mm});
            skLineSegment(sketch, "E6154", {"start": v(853.64, 14.19) * mm, "end": v(851.68, 11.9) * mm});
            skLineSegment(sketch, "E6155", {"start": v(851.68, 11.9) * mm, "end": v(849.7, 9.53) * mm});
            skLineSegment(sketch, "E6156", {"start": v(849.7, 9.53) * mm, "end": v(847.64, 7.2) * mm});
            skLineSegment(sketch, "E6157", {"start": v(847.64, 7.2) * mm, "end": v(845.48, 5) * mm});
            skLineSegment(sketch, "E6158", {"start": v(845.48, 5) * mm, "end": v(843.18, 3.07) * mm});
            skLineSegment(sketch, "E6159", {"start": v(843.18, 3.07) * mm, "end": v(840.71, 1.53) * mm});
            skLineSegment(sketch, "E6160", {"start": v(840.71, 1.53) * mm, "end": v(838.72, 0.66) * mm});
            skLineSegment(sketch, "E6161", {"start": v(838.72, 0.66) * mm, "end": v(838.03, 0.48) * mm});
            skLineSegment(sketch, "E6162", {"start": v(838.03, 0.48) * mm, "end": v(836.85, 0.16) * mm});
            skLineSegment(sketch, "E6163", {"start": v(836.85, 0.16) * mm, "end": v(836.7, 1.36) * mm});
            skLineSegment(sketch, "E6164", {"start": v(836.7, 1.36) * mm, "end": v(836.64, 1.78) * mm});
            skLineSegment(sketch, "E6165", {"start": v(836.64, 1.78) * mm, "end": v(836.74, 3.75) * mm});
            skLineSegment(sketch, "E6166", {"start": v(836.74, 3.75) * mm, "end": v(837.41, 5.62) * mm});
            skLineSegment(sketch, "E6167", {"start": v(837.41, 5.62) * mm, "end": v(837.64, 5.97) * mm});
            skLineSegment(sketch, "E6168", {"start": v(837.64, 5.97) * mm, "end": v(837.96, 6.47) * mm});
            skLineSegment(sketch, "E6169", {"start": v(837.96, 6.47) * mm, "end": v(839.2, 7.79) * mm});
            skLineSegment(sketch, "E6170", {"start": v(839.2, 7.79) * mm, "end": v(841.03, 9.2) * mm});
            skLineSegment(sketch, "E6171", {"start": v(841.03, 9.2) * mm, "end": v(842.91, 10.53) * mm});
            skLineSegment(sketch, "E6172", {"start": v(842.91, 10.53) * mm, "end": v(844.24, 11.61) * mm});
            skLineSegment(sketch, "E6173", {"start": v(844.24, 11.61) * mm, "end": v(844.62, 12.03) * mm});
            skLineSegment(sketch, "E6174", {"start": v(844.62, 12.03) * mm, "end": v(845.25, 13) * mm});
            skLineSegment(sketch, "E6175", {"start": v(845.25, 13) * mm, "end": v(849.01, 17.25) * mm});
            skLineSegment(sketch, "E6176", {"start": v(849.01, 17.25) * mm, "end": v(853.49, 20.73) * mm});
            skLineSegment(sketch, "E6177", {"start": v(853.49, 20.73) * mm, "end": v(854.47, 21.33) * mm});
            skLineSegment(sketch, "E6178", {"start": v(854.47, 21.33) * mm, "end": v(855.88, 23.2) * mm});
            skLineSegment(sketch, "E6179", {"start": v(855.88, 23.2) * mm, "end": v(860.51, 28.48) * mm});
            skLineSegment(sketch, "E6180", {"start": v(860.51, 28.48) * mm, "end": v(867.07, 35.1) * mm});
            skLineSegment(sketch, "E6181", {"start": v(867.07, 35.1) * mm, "end": v(873.82, 41.57) * mm});
            skLineSegment(sketch, "E6182", {"start": v(873.82, 41.57) * mm, "end": v(878.8, 46.5) * mm});
            skLineSegment(sketch, "E6183", {"start": v(878.8, 46.5) * mm, "end": v(880.4, 48.21) * mm});
            skLineSegment(sketch, "E6184", {"start": v(880.4, 48.21) * mm, "end": v(880.48, 48.43) * mm});
            skLineSegment(sketch, "E6185", {"start": v(880.48, 48.43) * mm, "end": v(880.78, 49.08) * mm});
            skLineSegment(sketch, "E6186", {"start": v(880.78, 49.08) * mm, "end": v(881.25, 50.07) * mm});
            skLineSegment(sketch, "E6187", {"start": v(881.25, 50.07) * mm, "end": v(881.7, 51.1) * mm});
            skLineSegment(sketch, "E6188", {"start": v(881.7, 51.1) * mm, "end": v(881.95, 51.8) * mm});
            skLineSegment(sketch, "E6189", {"start": v(881.95, 51.8) * mm, "end": v(882, 52.04) * mm});
            skLineSegment(sketch, "E6190", {"start": v(882, 52.04) * mm, "end": v(880.9, 51.86) * mm});
            skLineSegment(sketch, "E6191", {"start": v(880.9, 51.86) * mm, "end": v(875.88, 50.4) * mm});
            skLineSegment(sketch, "E6192", {"start": v(875.88, 50.4) * mm, "end": v(871.07, 48.28) * mm});
            skLineSegment(sketch, "E6193", {"start": v(871.07, 48.28) * mm, "end": v(870.07, 47.76) * mm});
            skLineSegment(sketch, "E6194", {"start": v(870.07, 47.76) * mm, "end": v(869.46, 47.44) * mm});
            skLineSegment(sketch, "E6195", {"start": v(869.46, 47.44) * mm, "end": v(866.56, 45.3) * mm});
            skLineSegment(sketch, "E6196", {"start": v(866.56, 45.3) * mm, "end": v(863.77, 43) * mm});
            skLineSegment(sketch, "E6197", {"start": v(863.77, 43) * mm, "end": v(863.2, 42.59) * mm});
            skLineSegment(sketch, "E6198", {"start": v(863.2, 42.59) * mm, "end": v(862.6, 42.13) * mm});
            skLineSegment(sketch, "E6199", {"start": v(862.6, 42.13) * mm, "end": v(859.3, 40.11) * mm});
            skLineSegment(sketch, "E6200", {"start": v(859.3, 40.11) * mm, "end": v(856.09, 38.08) * mm});
            skLineSegment(sketch, "E6201", {"start": v(856.09, 38.08) * mm, "end": v(855.5, 37.62) * mm});
            skLineSegment(sketch, "E6202", {"start": v(855.5, 37.62) * mm, "end": v(855.13, 37.33) * mm});
            skLineSegment(sketch, "E6203", {"start": v(855.13, 37.33) * mm, "end": v(854.11, 36.32) * mm});
            skLineSegment(sketch, "E6204", {"start": v(854.11, 36.32) * mm, "end": v(852.85, 34.85) * mm});
            skLineSegment(sketch, "E6205", {"start": v(852.85, 34.85) * mm, "end": v(851.58, 33.37) * mm});
            skLineSegment(sketch, "E6206", {"start": v(851.58, 33.37) * mm, "end": v(850.54, 32.33) * mm});
            skLineSegment(sketch, "E6207", {"start": v(850.54, 32.33) * mm, "end": v(850.15, 32.03) * mm});
            skLineSegment(sketch, "E6208", {"start": v(850.15, 32.03) * mm, "end": v(849.94, 31.86) * mm});
            skLineSegment(sketch, "E6209", {"start": v(849.94, 31.86) * mm, "end": v(849.24, 31.42) * mm});
            skLineSegment(sketch, "E6210", {"start": v(849.24, 31.42) * mm, "end": v(848.27, 30.94) * mm});
            skLineSegment(sketch, "E6211", {"start": v(848.27, 30.94) * mm, "end": v(847.33, 30.48) * mm});
            skLineSegment(sketch, "E6212", {"start": v(847.33, 30.48) * mm, "end": v(846.66, 30.08) * mm});
            skLineSegment(sketch, "E6213", {"start": v(846.66, 30.08) * mm, "end": v(846.46, 29.92) * mm});
            skLineSegment(sketch, "E6214", {"start": v(846.46, 29.92) * mm, "end": v(845.69, 29.3) * mm});
            skLineSegment(sketch, "E6215", {"start": v(845.69, 29.3) * mm, "end": v(842.07, 25.8) * mm});
            skLineSegment(sketch, "E6216", {"start": v(842.07, 25.8) * mm, "end": v(838.55, 22.18) * mm});
            skLineSegment(sketch, "E6217", {"start": v(838.55, 22.18) * mm, "end": v(837.82, 21.5) * mm});
            skLineSegment(sketch, "E6218", {"start": v(837.82, 21.5) * mm, "end": v(837.5, 21.23) * mm});
            skLineSegment(sketch, "E6219", {"start": v(837.5, 21.23) * mm, "end": v(836.63, 20.32) * mm});
            skLineSegment(sketch, "E6220", {"start": v(836.63, 20.32) * mm, "end": v(835.49, 19.04) * mm});
            skLineSegment(sketch, "E6221", {"start": v(835.49, 19.04) * mm, "end": v(834.33, 17.76) * mm});
            skLineSegment(sketch, "E6222", {"start": v(834.33, 17.76) * mm, "end": v(833.12, 16.57) * mm});
            skLineSegment(sketch, "E6223", {"start": v(833.12, 16.57) * mm, "end": v(831.82, 15.56) * mm});
            skLineSegment(sketch, "E6224", {"start": v(831.82, 15.56) * mm, "end": v(830.36, 14.83) * mm});
            skLineSegment(sketch, "E6225", {"start": v(830.36, 14.83) * mm, "end": v(828.71, 14.46) * mm});
            skLineSegment(sketch, "E6226", {"start": v(828.71, 14.46) * mm, "end": v(827.3, 14.47) * mm});
            skLineSegment(sketch, "E6227", {"start": v(827.3, 14.47) * mm, "end": v(826.84, 14.55) * mm});
            skLineSegment(sketch, "E6228", {"start": v(826.84, 14.55) * mm, "end": v(826.1, 14.68) * mm});
            skLineSegment(sketch, "E6229", {"start": v(826.1, 14.68) * mm, "end": v(825.97, 15.42) * mm});
            skLineSegment(sketch, "E6230", {"start": v(825.97, 15.42) * mm, "end": v(825.86, 16.04) * mm});
            skLineSegment(sketch, "E6231", {"start": v(825.86, 16.04) * mm, "end": v(826.1, 18.01) * mm});
            skLineSegment(sketch, "E6232", {"start": v(826.1, 18.01) * mm, "end": v(827.3, 20.1) * mm});
            skLineSegment(sketch, "E6233", {"start": v(827.3, 20.1) * mm, "end": v(829.08, 21.87) * mm});
            skLineSegment(sketch, "E6234", {"start": v(829.08, 21.87) * mm, "end": v(830.54, 23.08) * mm});
            skLineSegment(sketch, "E6235", {"start": v(830.54, 23.08) * mm, "end": v(831.02, 23.49) * mm});
            skLineSegment(sketch, "E6236", {"start": v(831.02, 23.49) * mm, "end": v(831.56, 23.94) * mm});
            skLineSegment(sketch, "E6237", {"start": v(831.56, 23.94) * mm, "end": v(836.83, 28.62) * mm});
            skLineSegment(sketch, "E6238", {"start": v(836.83, 28.62) * mm, "end": v(837.36, 29.1) * mm});
            skLineSegment(sketch, "E6239", {"start": v(837.36, 29.1) * mm, "end": v(838.4, 30.02) * mm});
            skLineSegment(sketch, "E6240", {"start": v(838.4, 30.02) * mm, "end": v(843.39, 34.94) * mm});
            skLineSegment(sketch, "E6241", {"start": v(843.39, 34.94) * mm, "end": v(848.4, 39.82) * mm});
            skLineSegment(sketch, "E6242", {"start": v(848.4, 39.82) * mm, "end": v(849.47, 40.73) * mm});
            skLineSegment(sketch, "E6243", {"start": v(849.47, 40.73) * mm, "end": v(850.3, 41.43) * mm});
            skLineSegment(sketch, "E6244", {"start": v(850.3, 41.43) * mm, "end": v(852.77, 43.55) * mm});
            skLineSegment(sketch, "E6245", {"start": v(852.77, 43.55) * mm, "end": v(855.93, 46.53) * mm});
            skLineSegment(sketch, "E6246", {"start": v(855.93, 46.53) * mm, "end": v(858.66, 49.84) * mm});
            skLineSegment(sketch, "E6247", {"start": v(858.66, 49.84) * mm, "end": v(860.32, 52.64) * mm});
            skLineSegment(sketch, "E6248", {"start": v(860.32, 52.64) * mm, "end": v(860.71, 53.64) * mm});
            skLineSegment(sketch, "E6249", {"start": v(860.71, 53.64) * mm, "end": v(860.2, 53.63) * mm});
            skLineSegment(sketch, "E6250", {"start": v(860.2, 53.63) * mm, "end": v(857.55, 53.36) * mm});
            skLineSegment(sketch, "E6251", {"start": v(857.55, 53.36) * mm, "end": v(855, 52.77) * mm});
            skLineSegment(sketch, "E6252", {"start": v(855, 52.77) * mm, "end": v(854.53, 52.6) * mm});
            skLineSegment(sketch, "E6253", {"start": v(854.53, 52.6) * mm, "end": v(853.4, 52.2) * mm});
            skLineSegment(sketch, "E6254", {"start": v(853.4, 52.2) * mm, "end": v(850.19, 50.55) * mm});
            skLineSegment(sketch, "E6255", {"start": v(850.19, 50.55) * mm, "end": v(847.05, 47.96) * mm});
            skLineSegment(sketch, "E6256", {"start": v(847.05, 47.96) * mm, "end": v(844.42, 44.78) * mm});
            skLineSegment(sketch, "E6257", {"start": v(844.42, 44.78) * mm, "end": v(842.33, 41.94) * mm});
            skLineSegment(sketch, "E6258", {"start": v(842.33, 41.94) * mm, "end": v(841.62, 41) * mm});
            skLineSegment(sketch, "E6259", {"start": v(841.62, 41) * mm, "end": v(841.44, 40.78) * mm});
            skLineSegment(sketch, "E6260", {"start": v(841.44, 40.78) * mm, "end": v(839.8, 38.46) * mm});
            skLineSegment(sketch, "E6261", {"start": v(839.8, 38.46) * mm, "end": v(839.62, 38.24) * mm});
            skLineSegment(sketch, "E6262", {"start": v(839.62, 38.24) * mm, "end": v(839.25, 37.76) * mm});
            skLineSegment(sketch, "E6263", {"start": v(839.25, 37.76) * mm, "end": v(837.95, 36.47) * mm});
            skLineSegment(sketch, "E6264", {"start": v(837.95, 36.47) * mm, "end": v(836.09, 35.36) * mm});
            skLineSegment(sketch, "E6265", {"start": v(836.09, 35.36) * mm, "end": v(834.02, 35.18) * mm});
            skLineSegment(sketch, "E6266", {"start": v(834.02, 35.18) * mm, "end": v(832.24, 35.86) * mm});
            skLineSegment(sketch, "E6267", {"start": v(832.24, 35.86) * mm, "end": v(831.74, 36.22) * mm});
            skLineSegment(sketch, "E6268", {"start": v(831.74, 36.22) * mm, "end": v(831.1, 36.68) * mm});
            skLineSegment(sketch, "E6269", {"start": v(831.1, 36.68) * mm, "end": v(831.35, 37.42) * mm});
            skLineSegment(sketch, "E6270", {"start": v(831.35, 37.42) * mm, "end": v(831.56, 38.02) * mm});
            skLineSegment(sketch, "E6271", {"start": v(831.56, 38.02) * mm, "end": v(832.42, 39.75) * mm});
            skLineSegment(sketch, "E6272", {"start": v(832.42, 39.75) * mm, "end": v(833.84, 41.83) * mm});
            skLineSegment(sketch, "E6273", {"start": v(833.84, 41.83) * mm, "end": v(835.47, 43.74) * mm});
            skLineSegment(sketch, "E6274", {"start": v(835.47, 43.74) * mm, "end": v(837.19, 45.56) * mm});
            skLineSegment(sketch, "E6275", {"start": v(837.19, 45.56) * mm, "end": v(838.83, 47.38) * mm});
            skLineSegment(sketch, "E6276", {"start": v(838.83, 47.38) * mm, "end": v(840.27, 49.29) * mm});
            skLineSegment(sketch, "E6277", {"start": v(840.27, 49.29) * mm, "end": v(841.37, 51.36) * mm});
            skLineSegment(sketch, "E6278", {"start": v(841.37, 51.36) * mm, "end": v(841.9, 53.09) * mm});
            skLineSegment(sketch, "E6279", {"start": v(841.9, 53.09) * mm, "end": v(841.98, 53.68) * mm});
            skLineSegment(sketch, "E6280", {"start": v(841.98, 53.68) * mm, "end": v(841.7, 53.77) * mm});
            skLineSegment(sketch, "E6281", {"start": v(841.7, 53.77) * mm, "end": v(840.87, 53.93) * mm});
            skLineSegment(sketch, "E6282", {"start": v(840.87, 53.93) * mm, "end": v(839.74, 53.96) * mm});
            skLineSegment(sketch, "E6283", {"start": v(839.74, 53.96) * mm, "end": v(838.6, 53.77) * mm});
            skLineSegment(sketch, "E6284", {"start": v(838.6, 53.77) * mm, "end": v(837.8, 53.5) * mm});
            skLineSegment(sketch, "E6285", {"start": v(837.8, 53.5) * mm, "end": v(837.54, 53.39) * mm});
            skLineSegment(sketch, "E6286", {"start": v(837.54, 53.39) * mm, "end": v(837.07, 53.17) * mm});
            skLineSegment(sketch, "E6287", {"start": v(837.07, 53.17) * mm, "end": v(835.8, 52.22) * mm});
            skLineSegment(sketch, "E6288", {"start": v(835.8, 52.22) * mm, "end": v(834.08, 50.54) * mm});
            skLineSegment(sketch, "E6289", {"start": v(834.08, 50.54) * mm, "end": v(832.36, 48.6) * mm});
            skLineSegment(sketch, "E6290", {"start": v(832.36, 48.6) * mm, "end": v(830.64, 46.63) * mm});
            skLineSegment(sketch, "E6291", {"start": v(830.64, 46.63) * mm, "end": v(828.86, 44.86) * mm});
            skLineSegment(sketch, "E6292", {"start": v(828.86, 44.86) * mm, "end": v(827.01, 43.53) * mm});
            skLineSegment(sketch, "E6293", {"start": v(827.01, 43.53) * mm, "end": v(825.07, 42.87) * mm});
            skLineSegment(sketch, "E6294", {"start": v(825.07, 42.87) * mm, "end": v(823.48, 42.94) * mm});
            skLineSegment(sketch, "E6295", {"start": v(823.48, 42.94) * mm, "end": v(823, 43.1) * mm});
            skLineSegment(sketch, "E6296", {"start": v(823, 43.1) * mm, "end": v(822.3, 43.36) * mm});
            skLineSegment(sketch, "E6297", {"start": v(822.3, 43.36) * mm, "end": v(822.29, 44.11) * mm});
            skLineSegment(sketch, "E6298", {"start": v(822.29, 44.11) * mm, "end": v(822.29, 44.54) * mm});
            skLineSegment(sketch, "E6299", {"start": v(822.29, 44.54) * mm, "end": v(822.45, 45.8) * mm});
            skLineSegment(sketch, "E6300", {"start": v(822.45, 45.8) * mm, "end": v(822.9, 47.2) * mm});
            skLineSegment(sketch, "E6301", {"start": v(822.9, 47.2) * mm, "end": v(823.52, 48.36) * mm});
            skLineSegment(sketch, "E6302", {"start": v(823.52, 48.36) * mm, "end": v(824.27, 49.37) * mm});
            skLineSegment(sketch, "E6303", {"start": v(824.27, 49.37) * mm, "end": v(825.05, 50.3) * mm});
            skLineSegment(sketch, "E6304", {"start": v(825.05, 50.3) * mm, "end": v(825.8, 51.24) * mm});
            skLineSegment(sketch, "E6305", {"start": v(825.8, 51.24) * mm, "end": v(826.43, 52.24) * mm});
            skLineSegment(sketch, "E6306", {"start": v(826.43, 52.24) * mm, "end": v(826.8, 53.1) * mm});
            skLineSegment(sketch, "E6307", {"start": v(826.8, 53.1) * mm, "end": v(826.87, 53.4) * mm});
            skLineSegment(sketch, "E6308", {"start": v(826.87, 53.4) * mm, "end": v(826.82, 53.41) * mm});
            skLineSegment(sketch, "E6309", {"start": v(826.82, 53.41) * mm, "end": v(826.32, 53.51) * mm});
            skLineSegment(sketch, "E6310", {"start": v(826.32, 53.51) * mm, "end": v(826.27, 53.52) * mm});
            skLineSegment(sketch, "E6311", {"start": v(826.27, 53.52) * mm, "end": v(826.02, 53.53) * mm});
            skLineSegment(sketch, "E6312", {"start": v(826.02, 53.53) * mm, "end": v(825.3, 53.46) * mm});
            skLineSegment(sketch, "E6313", {"start": v(825.3, 53.46) * mm, "end": v(824.22, 53.25) * mm});
            skLineSegment(sketch, "E6314", {"start": v(824.22, 53.25) * mm, "end": v(823.11, 53.03) * mm});
            skLineSegment(sketch, "E6315", {"start": v(823.11, 53.03) * mm, "end": v(822.3, 52.91) * mm});
            skLineSegment(sketch, "E6316", {"start": v(822.3, 52.91) * mm, "end": v(822.03, 52.9) * mm});
            skLineSegment(sketch, "E6317", {"start": v(822.03, 52.9) * mm, "end": v(821.9, 52.9) * mm});
            skLineSegment(sketch, "E6318", {"start": v(821.9, 52.9) * mm, "end": v(821.78, 52.92) * mm});
            skLineSegment(sketch, "E6319", {"start": v(821.78, 52.92) * mm, "end": v(821.6, 52.97) * mm});
            skLineSegment(sketch, "E6320", {"start": v(821.6, 52.97) * mm, "end": v(821.06, 53.19) * mm});
            skLineSegment(sketch, "E6321", {"start": v(821.06, 53.19) * mm, "end": v(820.52, 53.58) * mm});
            skLineSegment(sketch, "E6322", {"start": v(820.52, 53.58) * mm, "end": v(820.1, 54.05) * mm});
            skLineSegment(sketch, "E6323", {"start": v(820.1, 54.05) * mm, "end": v(819.78, 54.56) * mm});
            skLineSegment(sketch, "E6324", {"start": v(819.78, 54.56) * mm, "end": v(819.52, 55.06) * mm});
            skLineSegment(sketch, "E6325", {"start": v(819.52, 55.06) * mm, "end": v(819.28, 55.5) * mm});
            skLineSegment(sketch, "E6326", {"start": v(819.28, 55.5) * mm, "end": v(819.03, 55.86) * mm});
            skLineSegment(sketch, "E6327", {"start": v(819.03, 55.86) * mm, "end": v(818.81, 56.03) * mm});
            skLineSegment(sketch, "E6328", {"start": v(818.81, 56.03) * mm, "end": v(818.73, 56.05) * mm});
            skLineSegment(sketch, "E6329", {"start": v(818.73, 56.05) * mm, "end": v(817.96, 55.81) * mm});
            skLineSegment(sketch, "E6330", {"start": v(817.96, 55.81) * mm, "end": v(814.08, 54.91) * mm});
            skLineSegment(sketch, "E6331", {"start": v(814.08, 54.91) * mm, "end": v(810.13, 54.41) * mm});
            skLineSegment(sketch, "E6332", {"start": v(810.13, 54.41) * mm, "end": v(809.33, 54.37) * mm});
            skLineSegment(sketch, "E6333", {"start": v(809.33, 54.37) * mm, "end": v(809.26, 54.15) * mm});
            skLineSegment(sketch, "E6334", {"start": v(809.26, 54.15) * mm, "end": v(809.04, 52.86) * mm});
            skLineSegment(sketch, "E6335", {"start": v(809.04, 52.86) * mm, "end": v(808.92, 51.64) * mm});
            skLineSegment(sketch, "E6336", {"start": v(808.92, 51.64) * mm, "end": v(808.9, 51.46) * mm});
            skLineSegment(sketch, "E6337", {"start": v(808.9, 51.46) * mm, "end": v(808.88, 51.25) * mm});
            skLineSegment(sketch, "E6338", {"start": v(808.88, 51.25) * mm, "end": v(808.8, 50.63) * mm});
            skLineSegment(sketch, "E6339", {"start": v(808.8, 50.63) * mm, "end": v(808.68, 49.79) * mm});
            skLineSegment(sketch, "E6340", {"start": v(808.68, 49.79) * mm, "end": v(808.49, 48.95) * mm});
            skLineSegment(sketch, "E6341", {"start": v(808.49, 48.95) * mm, "end": v(808.22, 48.15) * mm});
            skLineSegment(sketch, "E6342", {"start": v(808.22, 48.15) * mm, "end": v(807.84, 47.42) * mm});
            skLineSegment(sketch, "E6343", {"start": v(807.84, 47.42) * mm, "end": v(807.35, 46.78) * mm});
            skLineSegment(sketch, "E6344", {"start": v(807.35, 46.78) * mm, "end": v(806.7, 46.27) * mm});
            skLineSegment(sketch, "E6345", {"start": v(806.7, 46.27) * mm, "end": v(806.1, 45.98) * mm});
            skLineSegment(sketch, "E6346", {"start": v(806.1, 45.98) * mm, "end": v(805.89, 45.91) * mm});
            skLineSegment(sketch, "E6347", {"start": v(805.89, 45.91) * mm, "end": v(805.48, 45.8) * mm});
            skLineSegment(sketch, "E6348", {"start": v(805.48, 45.8) * mm, "end": v(804.13, 45.88) * mm});
            skLineSegment(sketch, "E6349", {"start": v(804.13, 45.88) * mm, "end": v(801.76, 46.34) * mm});
            skLineSegment(sketch, "E6350", {"start": v(801.76, 46.34) * mm, "end": v(799.43, 47.07) * mm});
            skLineSegment(sketch, "E6351", {"start": v(799.43, 47.07) * mm, "end": v(798.17, 47.63) * mm});
            skLineSegment(sketch, "E6352", {"start": v(798.17, 47.63) * mm, "end": v(797.84, 47.9) * mm});
            skLineSegment(sketch, "E6353", {"start": v(797.84, 47.9) * mm, "end": v(797.55, 48.13) * mm});
            skLineSegment(sketch, "E6354", {"start": v(797.55, 48.13) * mm, "end": v(796.9, 49.08) * mm});
            skLineSegment(sketch, "E6355", {"start": v(796.9, 49.08) * mm, "end": v(796.3, 50.54) * mm});
            skLineSegment(sketch, "E6356", {"start": v(796.3, 50.54) * mm, "end": v(795.78, 52.02) * mm});
            skLineSegment(sketch, "E6357", {"start": v(795.78, 52.02) * mm, "end": v(795.28, 53.01) * mm});
            skLineSegment(sketch, "E6358", {"start": v(795.28, 53.01) * mm, "end": v(795.05, 53.29) * mm});
            skLineSegment(sketch, "E6359", {"start": v(795.05, 53.29) * mm, "end": v(794.93, 53.43) * mm});
            skLineSegment(sketch, "E6360", {"start": v(794.93, 53.43) * mm, "end": v(794.28, 54.03) * mm});
            skLineSegment(sketch, "E6361", {"start": v(794.28, 54.03) * mm, "end": v(793.54, 54.5) * mm});
            skLineSegment(sketch, "E6362", {"start": v(793.54, 54.5) * mm, "end": v(793.37, 54.57) * mm});
            skLineSegment(sketch, "E6363", {"start": v(793.37, 54.57) * mm, "end": v(793.18, 54.65) * mm});
            skLineSegment(sketch, "E6364", {"start": v(793.18, 54.65) * mm, "end": v(792.2, 54.98) * mm});
            skLineSegment(sketch, "E6365", {"start": v(792.2, 54.98) * mm, "end": v(791.2, 55.22) * mm});
            skLineSegment(sketch, "E6366", {"start": v(791.2, 55.22) * mm, "end": v(791, 55.26) * mm});
            skLineSegment(sketch, "E6367", {"start": v(791, 55.26) * mm, "end": v(790.73, 55.32) * mm});
            skLineSegment(sketch, "E6368", {"start": v(790.73, 55.32) * mm, "end": v(788.06, 56.05) * mm});
            skLineSegment(sketch, "E6369", {"start": v(788.06, 56.05) * mm, "end": v(787.8, 56.15) * mm});
            skLineSegment(sketch, "E6370", {"start": v(787.8, 56.15) * mm, "end": v(787.19, 56.37) * mm});
            skLineSegment(sketch, "E6371", {"start": v(787.19, 56.37) * mm, "end": v(783.97, 58.14) * mm});
            skLineSegment(sketch, "E6372", {"start": v(783.97, 58.14) * mm, "end": v(780.82, 60.14) * mm});
            skLineSegment(sketch, "E6373", {"start": v(780.82, 60.14) * mm, "end": v(780.25, 60.47) * mm});
            skLineSegment(sketch, "E6374", {"start": v(780.25, 60.47) * mm, "end": v(779.56, 60.86) * mm});
            skLineSegment(sketch, "E6375", {"start": v(779.56, 60.86) * mm, "end": v(777.43, 61.9) * mm});
            skLineSegment(sketch, "E6376", {"start": v(777.43, 61.9) * mm, "end": v(774.52, 63.4) * mm});
            skLineSegment(sketch, "E6377", {"start": v(774.52, 63.4) * mm, "end": v(771.9, 65.23) * mm});
            skLineSegment(sketch, "E6378", {"start": v(771.9, 65.23) * mm, "end": v(770.28, 66.98) * mm});
            skLineSegment(sketch, "E6379", {"start": v(770.28, 66.98) * mm, "end": v(769.91, 67.65) * mm});
            skLineSegment(sketch, "E6380", {"start": v(769.91, 67.65) * mm, "end": v(769.07, 68.14) * mm});
            skLineSegment(sketch, "E6381", {"start": v(769.07, 68.14) * mm, "end": v(766.38, 69.34) * mm});
            skLineSegment(sketch, "E6382", {"start": v(766.38, 69.34) * mm, "end": v(762.57, 70.6) * mm});
            skLineSegment(sketch, "E6383", {"start": v(762.57, 70.6) * mm, "end": v(758.66, 71.63) * mm});
            skLineSegment(sketch, "E6384", {"start": v(758.66, 71.63) * mm, "end": v(755.8, 72.34) * mm});
            skLineSegment(sketch, "E6385", {"start": v(755.8, 72.34) * mm, "end": v(754.85, 72.58) * mm});
            skLineSegment(sketch, "E6386", {"start": v(754.85, 72.58) * mm, "end": v(754.25, 72.74) * mm});
            skLineSegment(sketch, "E6387", {"start": v(754.25, 72.74) * mm, "end": v(748.42, 74.62) * mm});
            skLineSegment(sketch, "E6388", {"start": v(748.42, 74.62) * mm, "end": v(747.85, 74.85) * mm});
            skLineSegment(sketch, "E6389", {"start": v(747.85, 74.85) * mm, "end": v(747.32, 75.07) * mm});
            skLineSegment(sketch, "E6390", {"start": v(747.32, 75.07) * mm, "end": v(745.79, 75.9) * mm});
            skLineSegment(sketch, "E6391", {"start": v(745.79, 75.9) * mm, "end": v(743.57, 77.22) * mm});
            skLineSegment(sketch, "E6392", {"start": v(743.57, 77.22) * mm, "end": v(741.33, 78.45) * mm});
            skLineSegment(sketch, "E6393", {"start": v(741.33, 78.45) * mm, "end": v(739.72, 79.1) * mm});
            skLineSegment(sketch, "E6394", {"start": v(739.72, 79.1) * mm, "end": v(739.16, 79.22) * mm});
            skLineSegment(sketch, "E6395", {"start": v(739.16, 79.22) * mm, "end": v(739.13, 78.66) * mm});
            skLineSegment(sketch, "E6396", {"start": v(739.13, 78.66) * mm, "end": v(739.2, 76.97) * mm});
            skLineSegment(sketch, "E6397", {"start": v(739.2, 76.97) * mm, "end": v(739.56, 74.63) * mm});
            skLineSegment(sketch, "E6398", {"start": v(739.56, 74.63) * mm, "end": v(740.17, 72.37) * mm});
            skLineSegment(sketch, "E6399", {"start": v(740.17, 72.37) * mm, "end": v(740.76, 70.82) * mm});
            skLineSegment(sketch, "E6400", {"start": v(740.76, 70.82) * mm, "end": v(741, 70.33) * mm});
            skLineSegment(sketch, "E6401", {"start": v(741, 70.33) * mm, "end": v(741.2, 70.24) * mm});
            skLineSegment(sketch, "E6402", {"start": v(741.2, 70.24) * mm, "end": v(742.2, 69.93) * mm});
            skLineSegment(sketch, "E6403", {"start": v(742.2, 69.93) * mm, "end": v(743.26, 69.82) * mm});
            skLineSegment(sketch, "E6404", {"start": v(743.26, 69.82) * mm, "end": v(743.5, 69.83) * mm});
            skLineSegment(sketch, "E6405", {"start": v(743.5, 69.83) * mm, "end": v(744.25, 69.88) * mm});
            skLineSegment(sketch, "E6406", {"start": v(744.25, 69.88) * mm, "end": v(744.55, 69.18) * mm});
            skLineSegment(sketch, "E6407", {"start": v(744.55, 69.18) * mm, "end": v(744.74, 68.74) * mm});
            skLineSegment(sketch, "E6408", {"start": v(744.74, 68.74) * mm, "end": v(745.83, 67.62) * mm});
            skLineSegment(sketch, "E6409", {"start": v(745.83, 67.62) * mm, "end": v(747.79, 66.44) * mm});
            skLineSegment(sketch, "E6410", {"start": v(747.79, 66.44) * mm, "end": v(749.98, 65.43) * mm});
            skLineSegment(sketch, "E6411", {"start": v(749.98, 65.43) * mm, "end": v(751.47, 64.68) * mm});
            skLineSegment(sketch, "E6412", {"start": v(751.47, 64.68) * mm, "end": v(751.92, 64.37) * mm});
            skLineSegment(sketch, "E6413", {"start": v(751.92, 64.37) * mm, "end": v(752.2, 64.17) * mm});
            skLineSegment(sketch, "E6414", {"start": v(752.2, 64.17) * mm, "end": v(752.97, 63.43) * mm});
            skLineSegment(sketch, "E6415", {"start": v(752.97, 63.43) * mm, "end": v(754, 62.35) * mm});
            skLineSegment(sketch, "E6416", {"start": v(754, 62.35) * mm, "end": v(755.04, 61.32) * mm});
            skLineSegment(sketch, "E6417", {"start": v(755.04, 61.32) * mm, "end": v(755.83, 60.72) * mm});
            skLineSegment(sketch, "E6418", {"start": v(755.83, 60.72) * mm, "end": v(756.13, 60.58) * mm});
            skLineSegment(sketch, "E6419", {"start": v(756.13, 60.58) * mm, "end": v(756.3, 60.5) * mm});
            skLineSegment(sketch, "E6420", {"start": v(756.3, 60.5) * mm, "end": v(756.85, 60.37) * mm});
            skLineSegment(sketch, "E6421", {"start": v(756.85, 60.37) * mm, "end": v(757.8, 60.25) * mm});
            skLineSegment(sketch, "E6422", {"start": v(757.8, 60.25) * mm, "end": v(758.78, 60.13) * mm});
            skLineSegment(sketch, "E6423", {"start": v(758.78, 60.13) * mm, "end": v(759.45, 60) * mm});
            skLineSegment(sketch, "E6424", {"start": v(759.45, 60) * mm, "end": v(759.66, 59.93) * mm});
            skLineSegment(sketch, "E6425", {"start": v(759.66, 59.93) * mm, "end": v(760.27, 59.72) * mm});
            skLineSegment(sketch, "E6426", {"start": v(760.27, 59.72) * mm, "end": v(763.2, 58.3) * mm});
            skLineSegment(sketch, "E6427", {"start": v(763.2, 58.3) * mm, "end": v(766.09, 56.95) * mm});
            skLineSegment(sketch, "E6428", {"start": v(766.09, 56.95) * mm, "end": v(766.67, 56.77) * mm});
            skLineSegment(sketch, "E6429", {"start": v(766.67, 56.77) * mm, "end": v(766.97, 56.69) * mm});
            skLineSegment(sketch, "E6430", {"start": v(766.97, 56.69) * mm, "end": v(768.52, 56.43) * mm});
            skLineSegment(sketch, "E6431", {"start": v(768.52, 56.43) * mm, "end": v(770.09, 56.16) * mm});
            skLineSegment(sketch, "E6432", {"start": v(770.09, 56.16) * mm, "end": v(770.4, 56.06) * mm});
            skLineSegment(sketch, "E6433", {"start": v(770.4, 56.06) * mm, "end": v(771.4, 55.73) * mm});
            skLineSegment(sketch, "E6434", {"start": v(771.4, 55.73) * mm, "end": v(775.95, 53.49) * mm});
            skLineSegment(sketch, "E6435", {"start": v(775.95, 53.49) * mm, "end": v(780.17, 50.67) * mm});
            skLineSegment(sketch, "E6436", {"start": v(780.17, 50.67) * mm, "end": v(781, 50.04) * mm});
            skLineSegment(sketch, "E6437", {"start": v(781, 50.04) * mm, "end": v(781.73, 49.49) * mm});
            skLineSegment(sketch, "E6438", {"start": v(781.73, 49.49) * mm, "end": v(785.38, 46.68) * mm});
            skLineSegment(sketch, "E6439", {"start": v(785.38, 46.68) * mm, "end": v(789.19, 44.1) * mm});
            skLineSegment(sketch, "E6440", {"start": v(789.19, 44.1) * mm, "end": v(790, 43.66) * mm});
            skLineSegment(sketch, "E6441", {"start": v(790, 43.66) * mm, "end": v(790.13, 43.59) * mm});
            skLineSegment(sketch, "E6442", {"start": v(790.13, 43.59) * mm, "end": v(791.6, 43.01) * mm});
            skLineSegment(sketch, "E6443", {"start": v(791.6, 43.01) * mm, "end": v(791.76, 42.96) * mm});
            skLineSegment(sketch, "E6444", {"start": v(791.76, 42.96) * mm, "end": v(792, 42.88) * mm});
            skLineSegment(sketch, "E6445", {"start": v(792, 42.88) * mm, "end": v(792.7, 42.6) * mm});
            skLineSegment(sketch, "E6446", {"start": v(792.7, 42.6) * mm, "end": v(793.57, 42.2) * mm});
            skLineSegment(sketch, "E6447", {"start": v(793.57, 42.2) * mm, "end": v(794.33, 41.74) * mm});
            skLineSegment(sketch, "E6448", {"start": v(794.33, 41.74) * mm, "end": v(794.96, 41.18) * mm});
            skLineSegment(sketch, "E6449", {"start": v(794.96, 41.18) * mm, "end": v(795.45, 40.53) * mm});
            skLineSegment(sketch, "E6450", {"start": v(795.45, 40.53) * mm, "end": v(795.79, 39.74) * mm});
            skLineSegment(sketch, "E6451", {"start": v(795.79, 39.74) * mm, "end": v(795.95, 38.8) * mm});
            skLineSegment(sketch, "E6452", {"start": v(795.95, 38.8) * mm, "end": v(795.96, 37.97) * mm});
            skLineSegment(sketch, "E6453", {"start": v(795.96, 37.97) * mm, "end": v(795.93, 37.7) * mm});
            skLineSegment(sketch, "E6454", {"start": v(795.93, 37.7) * mm, "end": v(795.89, 37.06) * mm});
            skLineSegment(sketch, "E6455", {"start": v(795.89, 37.06) * mm, "end": v(795.3, 36.82) * mm});
            skLineSegment(sketch, "E6456", {"start": v(795.3, 36.82) * mm, "end": v(795.09, 36.73) * mm});
            skLineSegment(sketch, "E6457", {"start": v(795.09, 36.73) * mm, "end": v(794.4, 36.56) * mm});
            skLineSegment(sketch, "E6458", {"start": v(794.4, 36.56) * mm, "end": v(793.56, 36.47) * mm});
            skLineSegment(sketch, "E6459", {"start": v(793.56, 36.47) * mm, "end": v(792.76, 36.38) * mm});
            skLineSegment(sketch, "E6460", {"start": v(792.76, 36.38) * mm, "end": v(792.16, 36.22) * mm});
            skLineSegment(sketch, "E6461", {"start": v(792.16, 36.22) * mm, "end": v(791.98, 36.12) * mm});
            skLineSegment(sketch, "E6462", {"start": v(791.98, 36.12) * mm, "end": v(791.52, 35.9) * mm});
            skLineSegment(sketch, "E6463", {"start": v(791.52, 35.9) * mm, "end": v(791.04, 36.11) * mm});
            skLineSegment(sketch, "E6464", {"start": v(791.04, 36.11) * mm, "end": v(790.5, 36.37) * mm});
            skLineSegment(sketch, "E6465", {"start": v(790.5, 36.37) * mm, "end": v(788.97, 37.24) * mm});
            skLineSegment(sketch, "E6466", {"start": v(788.97, 37.24) * mm, "end": v(786.78, 38.63) * mm});
            skLineSegment(sketch, "E6467", {"start": v(786.78, 38.63) * mm, "end": v(784.5, 40.16) * mm});
            skLineSegment(sketch, "E6468", {"start": v(784.5, 40.16) * mm, "end": v(782.18, 41.72) * mm});
            skLineSegment(sketch, "E6469", {"start": v(782.18, 41.72) * mm, "end": v(779.83, 43.2) * mm});
            skLineSegment(sketch, "E6470", {"start": v(779.83, 43.2) * mm, "end": v(777.49, 44.46) * mm});
            skLineSegment(sketch, "E6471", {"start": v(777.49, 44.46) * mm, "end": v(775.18, 45.39) * mm});
            skLineSegment(sketch, "E6472", {"start": v(775.18, 45.39) * mm, "end": v(773.5, 45.82) * mm});
            skLineSegment(sketch, "E6473", {"start": v(773.5, 45.82) * mm, "end": v(772.94, 45.88) * mm});
            skLineSegment(sketch, "E6474", {"start": v(772.94, 45.88) * mm, "end": v(772.7, 45.9) * mm});
            skLineSegment(sketch, "E6475", {"start": v(772.7, 45.9) * mm, "end": v(771.96, 45.82) * mm});
            skLineSegment(sketch, "E6476", {"start": v(771.96, 45.82) * mm, "end": v(770.91, 45.54) * mm});
            skLineSegment(sketch, "E6477", {"start": v(770.91, 45.54) * mm, "end": v(769.8, 45.26) * mm});
            skLineSegment(sketch, "E6478", {"start": v(769.8, 45.26) * mm, "end": v(768.94, 45.15) * mm});
            skLineSegment(sketch, "E6479", {"start": v(768.94, 45.15) * mm, "end": v(768.65, 45.17) * mm});
            skLineSegment(sketch, "E6480", {"start": v(768.65, 45.17) * mm, "end": v(767.57, 45.22) * mm});
            skLineSegment(sketch, "E6481", {"start": v(767.57, 45.22) * mm, "end": v(764.35, 45.99) * mm});
            skLineSegment(sketch, "E6482", {"start": v(764.35, 45.99) * mm, "end": v(760.6, 47.7) * mm});
            skLineSegment(sketch, "E6483", {"start": v(760.6, 47.7) * mm, "end": v(757.09, 49.83) * mm});
            skLineSegment(sketch, "E6484", {"start": v(757.09, 49.83) * mm, "end": v(754.39, 51.44) * mm});
            skLineSegment(sketch, "E6485", {"start": v(754.39, 51.44) * mm, "end": v(753.45, 51.9) * mm});
            skLineSegment(sketch, "E6486", {"start": v(753.45, 51.9) * mm, "end": v(753.48, 51.65) * mm});
            skLineSegment(sketch, "E6487", {"start": v(753.48, 51.65) * mm, "end": v(754.01, 49.16) * mm});
            skLineSegment(sketch, "E6488", {"start": v(754.01, 49.16) * mm, "end": v(754.08, 48.91) * mm});
            skLineSegment(sketch, "E6489", {"start": v(754.08, 48.91) * mm, "end": v(754.35, 48.02) * mm});
            skLineSegment(sketch, "E6490", {"start": v(754.35, 48.02) * mm, "end": v(755.32, 45.41) * mm});
            skLineSegment(sketch, "E6491", {"start": v(755.32, 45.41) * mm, "end": v(756.68, 42.06) * mm});
            skLineSegment(sketch, "E6492", {"start": v(756.68, 42.06) * mm, "end": v(757.89, 38.65) * mm});
            skLineSegment(sketch, "E6493", {"start": v(757.89, 38.65) * mm, "end": v(758.56, 35.88) * mm});
            skLineSegment(sketch, "E6494", {"start": v(758.56, 35.88) * mm, "end": v(758.67, 34.95) * mm});
            skLineSegment(sketch, "E6495", {"start": v(758.67, 34.95) * mm, "end": v(759.24, 33.95) * mm});
            skLineSegment(sketch, "E6496", {"start": v(759.24, 33.95) * mm, "end": v(762.47, 29.52) * mm});
            skLineSegment(sketch, "E6497", {"start": v(762.47, 29.52) * mm, "end": v(765.9, 25.26) * mm});
            skLineSegment(sketch, "E6498", {"start": v(765.9, 25.26) * mm, "end": v(766.55, 24.34) * mm});
            skLineSegment(sketch, "E6499", {"start": v(766.55, 24.34) * mm, "end": v(767.2, 23.43) * mm});
            skLineSegment(sketch, "E6500", {"start": v(767.2, 23.43) * mm, "end": v(768.94, 20.53) * mm});
            skLineSegment(sketch, "E6501", {"start": v(768.94, 20.53) * mm, "end": v(771.08, 16.53) * mm});
            skLineSegment(sketch, "E6502", {"start": v(771.08, 16.53) * mm, "end": v(773.3, 12.58) * mm});
            skLineSegment(sketch, "E6503", {"start": v(773.3, 12.58) * mm, "end": v(775.17, 9.75) * mm});
            skLineSegment(sketch, "E6504", {"start": v(775.17, 9.75) * mm, "end": v(775.88, 8.89) * mm});
            skLineSegment(sketch, "E6505", {"start": v(775.88, 8.89) * mm, "end": v(776.36, 8.31) * mm});
            skLineSegment(sketch, "E6506", {"start": v(776.36, 8.31) * mm, "end": v(777.86, 6.63) * mm});
            skLineSegment(sketch, "E6507", {"start": v(777.86, 6.63) * mm, "end": v(779.84, 4.29) * mm});
            skLineSegment(sketch, "E6508", {"start": v(779.84, 4.29) * mm, "end": v(781.56, 1.78) * mm});
            skLineSegment(sketch, "E6509", {"start": v(781.56, 1.78) * mm, "end": v(782.57, -0.26) * mm});
            skLineSegment(sketch, "E6510", {"start": v(782.57, -0.26) * mm, "end": v(782.8, -0.97) * mm});
            skLineSegment(sketch, "E6511", {"start": v(782.8, -0.97) * mm, "end": v(782.88, -1.25) * mm});
            skLineSegment(sketch, "E6512", {"start": v(782.88, -1.25) * mm, "end": v(783.04, -2.12) * mm});
            skLineSegment(sketch, "E6513", {"start": v(783.04, -2.12) * mm, "end": v(783.14, -3.3) * mm});
            skLineSegment(sketch, "E6514", {"start": v(783.14, -3.3) * mm, "end": v(783.24, -4.45) * mm});
            skLineSegment(sketch, "E6515", {"start": v(783.24, -4.45) * mm, "end": v(783.38, -5.25) * mm});
            skLineSegment(sketch, "E6516", {"start": v(783.38, -5.25) * mm, "end": v(783.47, -5.5) * mm});
            skLineSegment(sketch, "E6517", {"start": v(783.47, -5.5) * mm, "end": v(783.62, -5.96) * mm});
            skLineSegment(sketch, "E6518", {"start": v(783.62, -5.96) * mm, "end": v(784.31, -7.24) * mm});
            skLineSegment(sketch, "E6519", {"start": v(784.31, -7.24) * mm, "end": v(785.58, -9.17) * mm});
            skLineSegment(sketch, "E6520", {"start": v(785.58, -9.17) * mm, "end": v(786.99, -11.03) * mm});
            skLineSegment(sketch, "E6521", {"start": v(786.99, -11.03) * mm, "end": v(787.93, -12.18) * mm});
            skLineSegment(sketch, "E6522", {"start": v(787.93, -12.18) * mm, "end": v(788.26, -12.56) * mm});
            skLineSegment(sketch, "E6523", {"start": v(788.26, -12.56) * mm, "end": v(788.42, -12.74) * mm});
            skLineSegment(sketch, "E6524", {"start": v(788.42, -12.74) * mm, "end": v(789.98, -14.57) * mm});
            skLineSegment(sketch, "E6525", {"start": v(789.98, -14.57) * mm, "end": v(790.13, -14.75) * mm});
            skLineSegment(sketch, "E6526", {"start": v(790.13, -14.75) * mm, "end": v(790.37, -15.04) * mm});
            skLineSegment(sketch, "E6527", {"start": v(790.37, -15.04) * mm, "end": v(791.08, -15.92) * mm});
            skLineSegment(sketch, "E6528", {"start": v(791.08, -15.92) * mm, "end": v(792.18, -17.23) * mm});
            skLineSegment(sketch, "E6529", {"start": v(792.18, -17.23) * mm, "end": v(793.33, -18.48) * mm});
            skLineSegment(sketch, "E6530", {"start": v(793.33, -18.48) * mm, "end": v(794.15, -19.22) * mm});
            skLineSegment(sketch, "E6531", {"start": v(794.15, -19.22) * mm, "end": v(794.45, -19.42) * mm});
            skLineSegment(sketch, "E6532", {"start": v(794.45, -19.42) * mm, "end": v(795.03, -19.8) * mm});
            skLineSegment(sketch, "E6533", {"start": v(795.03, -19.8) * mm, "end": v(796.92, -20.74) * mm});
            skLineSegment(sketch, "E6534", {"start": v(796.92, -20.74) * mm, "end": v(799.7, -21.71) * mm});
            skLineSegment(sketch, "E6535", {"start": v(799.7, -21.71) * mm, "end": v(802.69, -22.4) * mm});
            skLineSegment(sketch, "E6536", {"start": v(802.69, -22.4) * mm, "end": v(805.81, -22.84) * mm});
            skLineSegment(sketch, "E6537", {"start": v(805.81, -22.84) * mm, "end": v(808.99, -23.1) * mm});
            skLineSegment(sketch, "E6538", {"start": v(808.99, -23.1) * mm, "end": v(812.13, -23.27) * mm});
            skLineSegment(sketch, "E6539", {"start": v(812.13, -23.27) * mm, "end": v(815.14, -23.38) * mm});
            skLineSegment(sketch, "E6540", {"start": v(815.14, -23.38) * mm, "end": v(817.24, -23.46) * mm});
            skLineSegment(sketch, "E6541", {"start": v(817.24, -23.46) * mm, "end": v(817.95, -23.5) * mm});
            skLineSegment(sketch, "E6542", {"start": v(817.95, -23.5) * mm, "end": v(818.87, -23.55) * mm});
            skLineSegment(sketch, "E6543", {"start": v(818.87, -23.55) * mm, "end": v(823.47, -23.95) * mm});
            skLineSegment(sketch, "E6544", {"start": v(823.47, -23.95) * mm, "end": v(828.02, -24.68) * mm});
            skLineSegment(sketch, "E6545", {"start": v(828.02, -24.68) * mm, "end": v(828.92, -24.9) * mm});
            skLineSegment(sketch, "E6546", {"start": v(828.92, -24.9) * mm, "end": v(829.14, -24.94) * mm});
            skLineSegment(sketch, "E6547", {"start": v(829.14, -24.94) * mm, "end": v(829.8, -25.2) * mm});
            skLineSegment(sketch, "E6548", {"start": v(829.8, -25.2) * mm, "end": v(830.67, -25.64) * mm});
            skLineSegment(sketch, "E6549", {"start": v(830.67, -25.64) * mm, "end": v(831.48, -26.05) * mm});
            skLineSegment(sketch, "E6550", {"start": v(831.48, -26.05) * mm, "end": v(832.02, -26.26) * mm});
            skLineSegment(sketch, "E6551", {"start": v(832.02, -26.26) * mm, "end": v(832.2, -26.28) * mm});
            skLineSegment(sketch, "E6552", {"start": v(832.2, -26.28) * mm, "end": v(832.97, -26.4) * mm});
            skLineSegment(sketch, "E6553", {"start": v(832.97, -26.4) * mm, "end": v(835.3, -26.55) * mm});
            skLineSegment(sketch, "E6554", {"start": v(835.3, -26.55) * mm, "end": v(838.58, -26.53) * mm});
            skLineSegment(sketch, "E6555", {"start": v(838.58, -26.53) * mm, "end": v(841.86, -26.35) * mm});
            skLineSegment(sketch, "E6556", {"start": v(841.86, -26.35) * mm, "end": v(844.22, -26.2) * mm});
            skLineSegment(sketch, "E6557", {"start": v(844.22, -26.2) * mm, "end": v(845, -26.17) * mm});
            skLineSegment(sketch, "E6558", {"start": v(845, -26.17) * mm, "end": v(845.8, -26.14) * mm});
            skLineSegment(sketch, "E6559", {"start": v(845.8, -26.14) * mm, "end": v(849.88, -26.12) * mm});
            skLineSegment(sketch, "E6560", {"start": v(849.88, -26.12) * mm, "end": v(853.93, -26.5) * mm});
            skLineSegment(sketch, "E6561", {"start": v(853.93, -26.5) * mm, "end": v(854.72, -26.65) * mm});
            skLineSegment(sketch, "E6562", {"start": v(854.72, -26.65) * mm, "end": v(854.97, -26.7) * mm});
            skLineSegment(sketch, "E6563", {"start": v(854.97, -26.7) * mm, "end": v(855.7, -26.96) * mm});
            skLineSegment(sketch, "E6564", {"start": v(855.7, -26.96) * mm, "end": v(856.64, -27.4) * mm});
            skLineSegment(sketch, "E6565", {"start": v(856.64, -27.4) * mm, "end": v(857.52, -27.8) * mm});
            skLineSegment(sketch, "E6566", {"start": v(857.52, -27.8) * mm, "end": v(858.14, -28.02) * mm});
            skLineSegment(sketch, "E6567", {"start": v(858.14, -28.02) * mm, "end": v(858.34, -28.05) * mm});
            skLineSegment(sketch, "E6568", {"start": v(858.34, -28.05) * mm, "end": v(859.36, -28.17) * mm});
            skLineSegment(sketch, "E6569", {"start": v(859.36, -28.17) * mm, "end": v(862.47, -27.99) * mm});
            skLineSegment(sketch, "E6570", {"start": v(862.47, -27.99) * mm, "end": v(866.73, -27.2) * mm});
            skLineSegment(sketch, "E6571", {"start": v(866.73, -27.2) * mm, "end": v(871.04, -26.3) * mm});
            skLineSegment(sketch, "E6572", {"start": v(871.04, -26.3) * mm, "end": v(874.26, -25.9) * mm});
            skLineSegment(sketch, "E6573", {"start": v(874.26, -25.9) * mm, "end": v(875.33, -25.92) * mm});
            skLineSegment(sketch, "E6574", {"start": v(875.33, -25.92) * mm, "end": v(876, -25.93) * mm});
            skLineSegment(sketch, "E6575", {"start": v(876, -25.93) * mm, "end": v(878.04, -26.26) * mm});
            skLineSegment(sketch, "E6576", {"start": v(878.04, -26.26) * mm, "end": v(880.5, -27.07) * mm});
            skLineSegment(sketch, "E6577", {"start": v(880.5, -27.07) * mm, "end": v(882.77, -28.2) * mm});
            skLineSegment(sketch, "E6578", {"start": v(882.77, -28.2) * mm, "end": v(884.91, -29.5) * mm});
            skLineSegment(sketch, "E6579", {"start": v(884.91, -29.5) * mm, "end": v(886.98, -30.77) * mm});
            skLineSegment(sketch, "E6580", {"start": v(886.98, -30.77) * mm, "end": v(889.04, -31.88) * mm});
            skLineSegment(sketch, "E6581", {"start": v(889.04, -31.88) * mm, "end": v(891.16, -32.66) * mm});
            skLineSegment(sketch, "E6582", {"start": v(891.16, -32.66) * mm, "end": v(892.82, -32.95) * mm});
            skLineSegment(sketch, "E6583", {"start": v(892.82, -32.95) * mm, "end": v(893.38, -32.94) * mm});
            skLineSegment(sketch, "E6584", {"start": v(893.38, -32.94) * mm, "end": v(893.69, -32.94) * mm});
            skLineSegment(sketch, "E6585", {"start": v(893.69, -32.94) * mm, "end": v(894.63, -32.72) * mm});
            skLineSegment(sketch, "E6586", {"start": v(894.63, -32.72) * mm, "end": v(895.93, -32.23) * mm});
            skLineSegment(sketch, "E6587", {"start": v(895.93, -32.23) * mm, "end": v(897.3, -31.73) * mm});
            skLineSegment(sketch, "E6588", {"start": v(897.3, -31.73) * mm, "end": v(898.4, -31.5) * mm});
            skLineSegment(sketch, "E6589", {"start": v(898.4, -31.5) * mm, "end": v(898.77, -31.5) * mm});
            skLineSegment(sketch, "E6590", {"start": v(898.77, -31.5) * mm, "end": v(898.8, -31.5) * mm});
            skLineSegment(sketch, "E6591", {"start": v(898.8, -31.5) * mm, "end": v(898.82, -31.5) * mm});
            skLineSegment(sketch, "E6592", {"start": v(898.82, -31.5) * mm, "end": v(899.22, -31.53) * mm});
            skLineSegment(sketch, "E6593", {"start": v(899.22, -31.53) * mm, "end": v(900.38, -31.86) * mm});
            skLineSegment(sketch, "E6594", {"start": v(900.38, -31.86) * mm, "end": v(901.64, -32.56) * mm});
            skLineSegment(sketch, "E6595", {"start": v(901.64, -32.56) * mm, "end": v(902.83, -33.37) * mm});
            skLineSegment(sketch, "E6596", {"start": v(902.83, -33.37) * mm, "end": v(903.8, -33.94) * mm});
            skLineSegment(sketch, "E6597", {"start": v(903.8, -33.94) * mm, "end": v(904.16, -34.07) * mm});
            skLineSegment(sketch, "E6598", {"start": v(904.16, -34.07) * mm, "end": v(904.6, -34.24) * mm});
            skLineSegment(sketch, "E6599", {"start": v(904.6, -34.24) * mm, "end": v(905.95, -34.6) * mm});
            skLineSegment(sketch, "E6600", {"start": v(905.95, -34.6) * mm, "end": v(907.9, -34.95) * mm});
            skLineSegment(sketch, "E6601", {"start": v(907.9, -34.95) * mm, "end": v(909.95, -35.21) * mm});
            skLineSegment(sketch, "E6602", {"start": v(909.95, -35.21) * mm, "end": v(912.02, -35.46) * mm});
            skLineSegment(sketch, "E6603", {"start": v(912.02, -35.46) * mm, "end": v(914.05, -35.8) * mm});
            skLineSegment(sketch, "E6604", {"start": v(914.05, -35.8) * mm, "end": v(915.97, -36.3) * mm});
            skLineSegment(sketch, "E6605", {"start": v(915.97, -36.3) * mm, "end": v(917.73, -37.06) * mm});
            skLineSegment(sketch, "E6606", {"start": v(917.73, -37.06) * mm, "end": v(918.91, -37.84) * mm});
            skLineSegment(sketch, "E6607", {"start": v(918.91, -37.84) * mm, "end": v(919.25, -38.16) * mm});
            skLineSegment(sketch, "E6608", {"start": v(919.25, -38.16) * mm, "end": v(919.89, -38.07) * mm});
            skLineSegment(sketch, "E6609", {"start": v(919.89, -38.07) * mm, "end": v(923.15, -37.8) * mm});
            skLineSegment(sketch, "E6610", {"start": v(923.15, -37.8) * mm, "end": v(926.35, -37.39) * mm});
            skLineSegment(sketch, "E6611", {"start": v(926.35, -37.39) * mm, "end": v(926.96, -37.23) * mm});
            skLineSegment(sketch, "E6612", {"start": v(926.96, -37.23) * mm, "end": v(927.54, -37.07) * mm});
            skLineSegment(sketch, "E6613", {"start": v(927.54, -37.07) * mm, "end": v(927.97, -37.5) * mm});
            skLineSegment(sketch, "E6614", {"start": v(927.97, -37.5) * mm, "end": v(928.22, -37.74) * mm});
            skLineSegment(sketch, "E6615", {"start": v(928.22, -37.74) * mm, "end": v(929.3, -38.16) * mm});
            skLineSegment(sketch, "E6616", {"start": v(929.3, -38.16) * mm, "end": v(931, -38.28) * mm});
            skLineSegment(sketch, "E6617", {"start": v(931, -38.28) * mm, "end": v(932.79, -38.2) * mm});
            skLineSegment(sketch, "E6618", {"start": v(932.79, -38.2) * mm, "end": v(934.04, -38.17) * mm});
            skLineSegment(sketch, "E6619", {"start": v(934.04, -38.17) * mm, "end": v(934.44, -38.23) * mm});
            skLineSegment(sketch, "E6620", {"start": v(934.44, -38.23) * mm, "end": v(935.13, -38.34) * mm});
            skLineSegment(sketch, "E6621", {"start": v(935.13, -38.34) * mm, "end": v(937.14, -39.04) * mm});
            skLineSegment(sketch, "E6622", {"start": v(937.14, -39.04) * mm, "end": v(939.84, -40.18) * mm});
            skLineSegment(sketch, "E6623", {"start": v(939.84, -40.18) * mm, "end": v(942.55, -41) * mm});
            skLineSegment(sketch, "E6624", {"start": v(942.55, -41) * mm, "end": v(944.64, -41.06) * mm});
            skLineSegment(sketch, "E6625", {"start": v(944.64, -41.06) * mm, "end": v(945.27, -40.87) * mm});
            skLineSegment(sketch, "E6626", {"start": v(945.27, -40.87) * mm, "end": v(945.31, -40.7) * mm});
            skLineSegment(sketch, "E6627", {"start": v(945.31, -40.7) * mm, "end": v(945.3, -40.16) * mm});
            skLineSegment(sketch, "E6628", {"start": v(945.3, -40.16) * mm, "end": v(945.3, -39.35) * mm});
            skLineSegment(sketch, "E6629", {"start": v(945.3, -39.35) * mm, "end": v(945.44, -38.53) * mm});
            skLineSegment(sketch, "E6630", {"start": v(945.44, -38.53) * mm, "end": v(945.81, -37.94) * mm});
            skLineSegment(sketch, "E6631", {"start": v(945.81, -37.94) * mm, "end": v(945.98, -37.8) * mm});
            skLineSegment(sketch, "E6632", {"start": v(945.98, -37.8) * mm, "end": v(946.08, -37.7) * mm});
            skLineSegment(sketch, "E6633", {"start": v(946.08, -37.7) * mm, "end": v(946.2, -37.66) * mm});
            skLineSegment(sketch, "E6634", {"start": v(946.2, -37.66) * mm, "end": v(946.61, -37.45) * mm});
            skLineSegment(sketch, "E6635", {"start": v(946.61, -37.45) * mm, "end": v(947.78, -36.66) * mm});
            skLineSegment(sketch, "E6636", {"start": v(947.78, -36.66) * mm, "end": v(949.42, -35.3) * mm});
            skLineSegment(sketch, "E6637", {"start": v(949.42, -35.3) * mm, "end": v(950.96, -33.81) * mm});
            skLineSegment(sketch, "E6638", {"start": v(950.96, -33.81) * mm, "end": v(951.92, -32.77) * mm});
            skLineSegment(sketch, "E6639", {"start": v(951.92, -32.77) * mm, "end": v(952.23, -32.41) * mm});
            skLineSegment(sketch, "E6640", {"start": v(952.23, -32.41) * mm, "end": v(952.39, -32.22) * mm});
            skLineSegment(sketch, "E6641", {"start": v(952.39, -32.22) * mm, "end": v(952.86, -31.64) * mm});
            skLineSegment(sketch, "E6642", {"start": v(952.86, -31.64) * mm, "end": v(953.59, -30.66) * mm});
            skLineSegment(sketch, "E6643", {"start": v(953.59, -30.66) * mm, "end": v(954.32, -29.53) * mm});
            skLineSegment(sketch, "E6644", {"start": v(954.32, -29.53) * mm, "end": v(954.97, -28.32) * mm});
            skLineSegment(sketch, "E6645", {"start": v(954.97, -28.32) * mm, "end": v(955.45, -27.09) * mm});
            skLineSegment(sketch, "E6646", {"start": v(955.45, -27.09) * mm, "end": v(955.66, -25.89) * mm});
            skLineSegment(sketch, "E6647", {"start": v(955.66, -25.89) * mm, "end": v(955.52, -24.79) * mm});
            skLineSegment(sketch, "E6648", {"start": v(955.52, -24.79) * mm, "end": v(955.13, -24.03) * mm});
            skLineSegment(sketch, "E6649", {"start": v(955.13, -24.03) * mm, "end": v(954.94, -23.84) * mm});
            skLineSegment(sketch, "E6650", {"start": v(954.94, -23.84) * mm, "end": v(954.05, -23.82) * mm});
            skLineSegment(sketch, "E6651", {"start": v(954.05, -23.82) * mm, "end": v(951.35, -24.34) * mm});
            skLineSegment(sketch, "E6652", {"start": v(951.35, -24.34) * mm, "end": v(948.49, -25.78) * mm});
            skLineSegment(sketch, "E6653", {"start": v(948.49, -25.78) * mm, "end": v(946.13, -27.86) * mm});
            skLineSegment(sketch, "E6654", {"start": v(946.13, -27.86) * mm, "end": v(944.06, -30.28) * mm});
            skLineSegment(sketch, "E6655", {"start": v(944.06, -30.28) * mm, "end": v(942.07, -32.76) * mm});
            skLineSegment(sketch, "E6656", {"start": v(942.07, -32.76) * mm, "end": v(939.94, -35) * mm});
            skLineSegment(sketch, "E6657", {"start": v(939.94, -35) * mm, "end": v(937.45, -36.69) * mm});
            skLineSegment(sketch, "E6658", {"start": v(937.45, -36.69) * mm, "end": v(935.18, -37.47) * mm});
            skLineSegment(sketch, "E6659", {"start": v(935.18, -37.47) * mm, "end": v(934.4, -37.55) * mm});
            skLineSegment(sketch, "E6660", {"start": v(934.4, -37.55) * mm, "end": v(933.28, -37.66) * mm});
            skLineSegment(sketch, "E6661", {"start": v(933.28, -37.66) * mm, "end": v(933.21, -36.54) * mm});
            skLineSegment(sketch, "E6662", {"start": v(933.21, -36.54) * mm, "end": v(933.2, -36.16) * mm});
            skLineSegment(sketch, "E6663", {"start": v(933.2, -36.16) * mm, "end": v(933.28, -35) * mm});
            skLineSegment(sketch, "E6664", {"start": v(933.28, -35) * mm, "end": v(933.62, -33.57) * mm});
            skLineSegment(sketch, "E6665", {"start": v(933.62, -33.57) * mm, "end": v(934.23, -32.23) * mm});
            skLineSegment(sketch, "E6666", {"start": v(934.23, -32.23) * mm, "end": v(934.85, -31.26) * mm});
            skLineSegment(sketch, "E6667", {"start": v(934.85, -31.26) * mm, "end": v(935.1, -30.97) * mm});
            skLineSegment(sketch, "E6668", {"start": v(935.1, -30.97) * mm, "end": v(935.36, -30.65) * mm});
            skLineSegment(sketch, "E6669", {"start": v(935.36, -30.65) * mm, "end": v(936.24, -29.76) * mm});
            skLineSegment(sketch, "E6670", {"start": v(936.24, -29.76) * mm, "end": v(937.45, -28.7) * mm});
            skLineSegment(sketch, "E6671", {"start": v(937.45, -28.7) * mm, "end": v(938.7, -27.68) * mm});
            skLineSegment(sketch, "E6672", {"start": v(938.7, -27.68) * mm, "end": v(939.62, -26.87) * mm});
            skLineSegment(sketch, "E6673", {"start": v(939.62, -26.87) * mm, "end": v(939.91, -26.58) * mm});
            skLineSegment(sketch, "E6674", {"start": v(939.91, -26.58) * mm, "end": v(940.54, -25.94) * mm});
            skLineSegment(sketch, "E6675", {"start": v(940.54, -25.94) * mm, "end": v(943.6, -22.6) * mm});
            skLineSegment(sketch, "E6676", {"start": v(943.6, -22.6) * mm, "end": v(946.7, -19.32) * mm});
            skLineSegment(sketch, "E6677", {"start": v(946.7, -19.32) * mm, "end": v(947.35, -18.7) * mm});
            skLineSegment(sketch, "E6678", {"start": v(947.35, -18.7) * mm, "end": v(947.45, -18.18) * mm});
            skLineSegment(sketch, "E6679", {"start": v(947.45, -18.18) * mm, "end": v(947.94, -16.63) * mm});
            skLineSegment(sketch, "E6680", {"start": v(947.94, -16.63) * mm, "end": v(948.82, -14.8) * mm});
            skLineSegment(sketch, "E6681", {"start": v(948.82, -14.8) * mm, "end": v(949.87, -13.14) * mm});
            skLineSegment(sketch, "E6682", {"start": v(949.87, -13.14) * mm, "end": v(950.99, -11.56) * mm});
            skLineSegment(sketch, "E6683", {"start": v(950.99, -11.56) * mm, "end": v(952.07, -9.98) * mm});
            skLineSegment(sketch, "E6684", {"start": v(952.07, -9.98) * mm, "end": v(953.01, -8.31) * mm});
            skLineSegment(sketch, "E6685", {"start": v(953.01, -8.31) * mm, "end": v(953.7, -6.5) * mm});
            skLineSegment(sketch, "E6686", {"start": v(953.7, -6.5) * mm, "end": v(954, -4.95) * mm});
            skLineSegment(sketch, "E6687", {"start": v(954, -4.95) * mm, "end": v(954.02, -4.43) * mm});
            skLineSegment(sketch, "E6688", {"start": v(954.02, -4.43) * mm, "end": v(953.02, -4.73) * mm});
            skLineSegment(sketch, "E6689", {"start": v(953.02, -4.73) * mm, "end": v(950.16, -6.05) * mm});
            skLineSegment(sketch, "E6690", {"start": v(950.16, -6.05) * mm, "end": v(946.97, -8.24) * mm});
            skLineSegment(sketch, "E6691", {"start": v(946.97, -8.24) * mm, "end": v(944.07, -10.92) * mm});
            skLineSegment(sketch, "E6692", {"start": v(944.07, -10.92) * mm, "end": v(941.84, -13.23) * mm});
            skLineSegment(sketch, "E6693", {"start": v(941.84, -13.23) * mm, "end": v(941.1, -14) * mm});
            skLineSegment(sketch, "E6694", {"start": v(941.1, -14) * mm, "end": v(939.88, -15.25) * mm});
            skLineSegment(sketch, "E6695", {"start": v(939.88, -15.25) * mm, "end": v(927.86, -27.82) * mm});
            skLineSegment(sketch, "E6696", {"start": v(927.86, -27.82) * mm, "end": v(926.7, -29.1) * mm});
            skLineSegment(sketch, "E6697", {"start": v(926.7, -29.1) * mm, "end": v(926.22, -29.64) * mm});
            skLineSegment(sketch, "E6698", {"start": v(926.22, -29.64) * mm, "end": v(924.86, -31.29) * mm});
            skLineSegment(sketch, "E6699", {"start": v(924.86, -31.29) * mm, "end": v(922.94, -33.4) * mm});
            skLineSegment(sketch, "E6700", {"start": v(922.94, -33.4) * mm, "end": v(920.7, -35.05) * mm});
            skLineSegment(sketch, "E6701", {"start": v(920.7, -35.05) * mm, "end": v(918.62, -35.77) * mm});
            skLineSegment(sketch, "E6702", {"start": v(918.62, -35.77) * mm, "end": v(917.92, -35.8) * mm});
            skLineSegment(sketch, "E6703", {"start": v(917.92, -35.8) * mm, "end": v(917.24, -35.85) * mm});
            skLineSegment(sketch, "E6704", {"start": v(917.24, -35.85) * mm, "end": v(916.92, -35.25) * mm});
            skLineSegment(sketch, "E6705", {"start": v(916.92, -35.25) * mm, "end": v(916.77, -34.97) * mm});
            skLineSegment(sketch, "E6706", {"start": v(916.77, -34.97) * mm, "end": v(916.35, -33.56) * mm});
            skLineSegment(sketch, "E6707", {"start": v(916.35, -33.56) * mm, "end": v(916.45, -32.08) * mm});
            skLineSegment(sketch, "E6708", {"start": v(916.45, -32.08) * mm, "end": v(916.56, -31.79) * mm});
            skLineSegment(sketch, "E6709", {"start": v(916.56, -31.79) * mm, "end": v(916.66, -31.49) * mm});
            skLineSegment(sketch, "E6710", {"start": v(916.66, -31.49) * mm, "end": v(917.15, -30.65) * mm});
            skLineSegment(sketch, "E6711", {"start": v(917.15, -30.65) * mm, "end": v(917.95, -29.7) * mm});
            skLineSegment(sketch, "E6712", {"start": v(917.95, -29.7) * mm, "end": v(918.86, -28.85) * mm});
            skLineSegment(sketch, "E6713", {"start": v(918.86, -28.85) * mm, "end": v(919.56, -28.2) * mm});
            skLineSegment(sketch, "E6714", {"start": v(919.56, -28.2) * mm, "end": v(919.78, -27.98) * mm});
            skLineSegment(sketch, "E6715", {"start": v(919.78, -27.98) * mm, "end": v(921.25, -26.52) * mm});
            skLineSegment(sketch, "E6716", {"start": v(921.25, -26.52) * mm, "end": v(925.47, -21.94) * mm});
            skLineSegment(sketch, "E6717", {"start": v(925.47, -21.94) * mm, "end": v(930.82, -15.67) * mm});
            skLineSegment(sketch, "E6718", {"start": v(930.82, -15.67) * mm, "end": v(936, -9.23) * mm});
            skLineSegment(sketch, "E6719", {"start": v(936, -9.23) * mm, "end": v(939.85, -4.36) * mm});
            skLineSegment(sketch, "E6720", {"start": v(939.85, -4.36) * mm, "end": v(941.14, -2.74) * mm});
            skLineSegment(sketch, "E6721", {"start": v(941.14, -2.74) * mm, "end": v(941.5, -2.3) * mm});
            skLineSegment(sketch, "E6722", {"start": v(941.5, -2.3) * mm, "end": v(943.32, -0.16) * mm});
            skLineSegment(sketch, "E6723", {"start": v(943.32, -0.16) * mm, "end": v(945.12, 2.02) * mm});
            skLineSegment(sketch, "E6724", {"start": v(945.12, 2.02) * mm, "end": v(945.47, 2.48) * mm});
            skLineSegment(sketch, "E6725", {"start": v(945.47, 2.48) * mm, "end": v(945.67, 2.74) * mm});
            skLineSegment(sketch, "E6726", {"start": v(945.67, 2.74) * mm, "end": v(946.32, 3.66) * mm});
            skLineSegment(sketch, "E6727", {"start": v(946.32, 3.66) * mm, "end": v(947.36, 5.34) * mm});
            skLineSegment(sketch, "E6728", {"start": v(947.36, 5.34) * mm, "end": v(948.11, 7.08) * mm});
            skLineSegment(sketch, "E6729", {"start": v(948.11, 7.08) * mm, "end": v(948.27, 8.18) * mm});
            skLineSegment(sketch, "E6730", {"start": v(948.27, 8.18) * mm, "end": v(948.14, 8.46) * mm});
            skLineSegment(sketch, "E6731", {"start": v(948.14, 8.46) * mm, "end": v(948.1, 8.56) * mm});
            skLineSegment(sketch, "E6732", {"start": v(948.1, 8.56) * mm, "end": v(947.85, 8.8) * mm});
            skLineSegment(sketch, "E6733", {"start": v(947.85, 8.8) * mm, "end": v(947.43, 9.04) * mm});
            skLineSegment(sketch, "E6734", {"start": v(947.43, 9.04) * mm, "end": v(946.95, 9.18) * mm});
            skLineSegment(sketch, "E6735", {"start": v(946.95, 9.18) * mm, "end": v(946.62, 9.25) * mm});
            skLineSegment(sketch, "E6736", {"start": v(946.62, 9.25) * mm, "end": v(946.5, 9.27) * mm});
            skLineSegment(sketch, "E6737", {"start": v(946.5, 9.27) * mm, "end": v(946.17, 9.32) * mm});
            skLineSegment(sketch, "E6738", {"start": v(946.17, 9.32) * mm, "end": v(945.12, 9.2) * mm});
            skLineSegment(sketch, "E6739", {"start": v(945.12, 9.2) * mm, "end": v(943.9, 8.62) * mm});
            skLineSegment(sketch, "E6740", {"start": v(943.9, 8.62) * mm, "end": v(942.76, 7.7) * mm});
            skLineSegment(sketch, "E6741", {"start": v(942.76, 7.7) * mm, "end": v(941.67, 6.57) * mm});
            skLineSegment(sketch, "E6742", {"start": v(941.67, 6.57) * mm, "end": v(940.57, 5.39) * mm});
            skLineSegment(sketch, "E6743", {"start": v(940.57, 5.39) * mm, "end": v(939.38, 4.3) * mm});
            skLineSegment(sketch, "E6744", {"start": v(939.38, 4.3) * mm, "end": v(938.07, 3.43) * mm});
            skLineSegment(sketch, "E6745", {"start": v(938.07, 3.43) * mm, "end": v(936.95, 3.01) * mm});
            skLineSegment(sketch, "E6746", {"start": v(936.95, 3.01) * mm, "end": v(936.57, 2.96) * mm});
            skLineSegment(sketch, "E6747", {"start": v(936.57, 2.96) * mm, "end": v(936.35, 2.64) * mm});
            skLineSegment(sketch, "E6748", {"start": v(936.35, 2.64) * mm, "end": v(935.06, 1.27) * mm});
            skLineSegment(sketch, "E6749", {"start": v(935.06, 1.27) * mm, "end": v(933.58, 0.08) * mm});
            skLineSegment(sketch, "E6750", {"start": v(933.58, 0.08) * mm, "end": v(933.27, -0.14) * mm});
            skLineSegment(sketch, "E6751", {"start": v(933.27, -0.14) * mm, "end": v(933, -0.33) * mm});
            skLineSegment(sketch, "E6752", {"start": v(933, -0.33) * mm, "end": v(931.59, -1.33) * mm});
            skLineSegment(sketch, "E6753", {"start": v(931.59, -1.33) * mm, "end": v(930.27, -2.45) * mm});
            skLineSegment(sketch, "E6754", {"start": v(930.27, -2.45) * mm, "end": v(930.06, -2.7) * mm});
            skLineSegment(sketch, "E6755", {"start": v(930.06, -2.7) * mm, "end": v(929.01, -3.9) * mm});
            skLineSegment(sketch, "E6756", {"start": v(929.01, -3.9) * mm, "end": v(924.05, -10.1) * mm});
            skLineSegment(sketch, "E6757", {"start": v(924.05, -10.1) * mm, "end": v(919.05, -16.3) * mm});
            skLineSegment(sketch, "E6758", {"start": v(919.05, -16.3) * mm, "end": v(918, -17.48) * mm});
            skLineSegment(sketch, "E6759", {"start": v(918, -17.48) * mm, "end": v(917.46, -18.07) * mm});
            skLineSegment(sketch, "E6760", {"start": v(917.46, -18.07) * mm, "end": v(912.46, -24.18) * mm});
            skLineSegment(sketch, "E6761", {"start": v(912.46, -24.18) * mm, "end": v(912, -24.82) * mm});
            skLineSegment(sketch, "E6762", {"start": v(912, -24.82) * mm, "end": v(911.58, -25.36) * mm});
            skLineSegment(sketch, "E6763", {"start": v(911.58, -25.36) * mm, "end": v(910.47, -27.08) * mm});
            skLineSegment(sketch, "E6764", {"start": v(910.47, -27.08) * mm, "end": v(908.83, -29.33) * mm});
            skLineSegment(sketch, "E6765", {"start": v(908.83, -29.33) * mm, "end": v(906.77, -31.01) * mm});
            skLineSegment(sketch, "E6766", {"start": v(906.77, -31.01) * mm, "end": v(904.7, -31.61) * mm});
            skLineSegment(sketch, "E6767", {"start": v(904.7, -31.61) * mm, "end": v(904.03, -31.57) * mm});
            skLineSegment(sketch, "E6768", {"start": v(904.03, -31.57) * mm, "end": v(903.55, -31.54) * mm});
            skLineSegment(sketch, "E6769", {"start": v(903.55, -31.54) * mm, "end": v(903.25, -31.16) * mm});
            skLineSegment(sketch, "E6770", {"start": v(903.25, -31.16) * mm, "end": v(903.06, -30.92) * mm});
            skLineSegment(sketch, "E6771", {"start": v(903.06, -30.92) * mm, "end": v(902.38, -29.6) * mm});
            skLineSegment(sketch, "E6772", {"start": v(902.38, -29.6) * mm, "end": v(902.2, -28.13) * mm});
            skLineSegment(sketch, "E6773", {"start": v(902.2, -28.13) * mm, "end": v(902.28, -27.82) * mm});
            skLineSegment(sketch, "E6774", {"start": v(902.28, -27.82) * mm, "end": v(902.35, -27.46) * mm});
            skLineSegment(sketch, "E6775", {"start": v(902.35, -27.46) * mm, "end": v(902.9, -26.46) * mm});
            skLineSegment(sketch, "E6776", {"start": v(902.9, -26.46) * mm, "end": v(903.98, -25.23) * mm});
            skLineSegment(sketch, "E6777", {"start": v(903.98, -25.23) * mm, "end": v(905.23, -24.1) * mm});
            skLineSegment(sketch, "E6778", {"start": v(905.23, -24.1) * mm, "end": v(906.11, -23.34) * mm});
            skLineSegment(sketch, "E6779", {"start": v(906.11, -23.34) * mm, "end": v(906.39, -23.07) * mm});
            skLineSegment(sketch, "E6780", {"start": v(906.39, -23.07) * mm, "end": v(907.87, -21.58) * mm});
            skLineSegment(sketch, "E6781", {"start": v(907.87, -21.58) * mm, "end": v(912, -16.8) * mm});
            skLineSegment(sketch, "E6782", {"start": v(912, -16.8) * mm, "end": v(917.12, -10.2) * mm});
            skLineSegment(sketch, "E6783", {"start": v(917.12, -10.2) * mm, "end": v(922.13, -3.54) * mm});
            skLineSegment(sketch, "E6784", {"start": v(922.13, -3.54) * mm, "end": v(926.04, 1.39) * mm});
            skLineSegment(sketch, "E6785", {"start": v(926.04, 1.39) * mm, "end": v(927.42, 2.96) * mm});
            skLineSegment(sketch, "E6786", {"start": v(927.42, 2.96) * mm, "end": v(928.15, 3.77) * mm});
            skLineSegment(sketch, "E6787", {"start": v(928.15, 3.77) * mm, "end": v(930.34, 6.21) * mm});
            skLineSegment(sketch, "E6788", {"start": v(930.34, 6.21) * mm, "end": v(933.08, 9.6) * mm});
            skLineSegment(sketch, "E6789", {"start": v(933.08, 9.6) * mm, "end": v(935.26, 13.31) * mm});
            skLineSegment(sketch, "E6790", {"start": v(935.26, 13.31) * mm, "end": v(936.36, 16.43) * mm});
            skLineSegment(sketch, "E6791", {"start": v(936.36, 16.43) * mm, "end": v(936.51, 17.5) * mm});
            skLineSegment(sketch, "E6792", {"start": v(936.51, 17.5) * mm, "end": v(936.4, 17.7) * mm});
            skLineSegment(sketch, "E6793", {"start": v(936.4, 17.7) * mm, "end": v(935.32, 19.72) * mm});
            skLineSegment(sketch, "E6794", {"start": v(935.32, 19.72) * mm, "end": v(935.22, 19.93) * mm});
            skLineSegment(sketch, "E6795", {"start": v(935.22, 19.93) * mm, "end": v(934.55, 20.03) * mm});
            skLineSegment(sketch, "E6796", {"start": v(934.55, 20.03) * mm, "end": v(932.52, 20.02) * mm});
            skLineSegment(sketch, "E6797", {"start": v(932.52, 20.02) * mm, "end": v(930.23, 19.53) * mm});
            skLineSegment(sketch, "E6798", {"start": v(930.23, 19.53) * mm, "end": v(928.23, 18.58) * mm});
            skLineSegment(sketch, "E6799", {"start": v(928.23, 18.58) * mm, "end": v(926.43, 17.3) * mm});
            skLineSegment(sketch, "E6800", {"start": v(926.43, 17.3) * mm, "end": v(924.74, 15.8) * mm});
            skLineSegment(sketch, "E6801", {"start": v(924.74, 15.8) * mm, "end": v(923.03, 14.22) * mm});
            skLineSegment(sketch, "E6802", {"start": v(923.03, 14.22) * mm, "end": v(921.23, 12.66) * mm});
            skLineSegment(sketch, "E6803", {"start": v(921.23, 12.66) * mm, "end": v(919.75, 11.58) * mm});
            skLineSegment(sketch, "E6804", {"start": v(919.75, 11.58) * mm, "end": v(919.22, 11.27) * mm});
            skLineSegment(sketch, "E6805", {"start": v(919.22, 11.27) * mm, "end": v(917.74, 9.52) * mm});
            skLineSegment(sketch, "E6806", {"start": v(917.74, 9.52) * mm, "end": v(913.12, 4.45) * mm});
            skLineSegment(sketch, "E6807", {"start": v(913.12, 4.45) * mm, "end": v(906.76, -2.13) * mm});
            skLineSegment(sketch, "E6808", {"start": v(906.76, -2.13) * mm, "end": v(900.28, -8.6) * mm});
            skLineSegment(sketch, "E6809", {"start": v(900.28, -8.6) * mm, "end": v(895.41, -13.43) * mm});
            skLineSegment(sketch, "E6810", {"start": v(895.41, -13.43) * mm, "end": v(893.8, -15.06) * mm});
            skLineSegment(sketch, "E6811", {"start": v(893.8, -15.06) * mm, "end": v(893.23, -15.66) * mm});
            skLineSegment(sketch, "E6812", {"start": v(893.23, -15.66) * mm, "end": v(891.63, -17.57) * mm});
            skLineSegment(sketch, "E6813", {"start": v(891.63, -17.57) * mm, "end": v(889.48, -20.08) * mm});
            skLineSegment(sketch, "E6814", {"start": v(889.48, -20.08) * mm, "end": v(887.01, -22.18) * mm});
            skLineSegment(sketch, "E6815", {"start": v(887.01, -22.18) * mm, "end": v(884.7, -23.3) * mm});
            skLineSegment(sketch, "E6816", {"start": v(884.7, -23.3) * mm, "end": v(883.9, -23.47) * mm});
            skLineSegment(sketch, "E6817", {"start": v(883.9, -23.47) * mm, "end": v(883.2, -23.6) * mm});
            skLineSegment(sketch, "E6818", {"start": v(883.2, -23.6) * mm, "end": v(882.8, -23.04) * mm});
            skLineSegment(sketch, "E6819", {"start": v(882.8, -23.04) * mm, "end": v(882.62, -22.79) * mm});
            skLineSegment(sketch, "E6820", {"start": v(882.62, -22.79) * mm, "end": v(882.04, -21.43) * mm});
            skLineSegment(sketch, "E6821", {"start": v(882.04, -21.43) * mm, "end": v(881.96, -19.96) * mm});
            skLineSegment(sketch, "E6822", {"start": v(881.96, -19.96) * mm, "end": v(882.04, -19.65) * mm});
            skLineSegment(sketch, "E6823", {"start": v(882.04, -19.65) * mm, "end": v(882.14, -19.24) * mm});
            skLineSegment(sketch, "E6824", {"start": v(882.14, -19.24) * mm, "end": v(882.77, -18.08) * mm});
            skLineSegment(sketch, "E6825", {"start": v(882.77, -18.08) * mm, "end": v(883.93, -16.81) * mm});
            skLineSegment(sketch, "E6826", {"start": v(883.93, -16.81) * mm, "end": v(885.3, -15.7) * mm});
            skLineSegment(sketch, "E6827", {"start": v(885.3, -15.7) * mm, "end": v(886.31, -14.9) * mm});
            skLineSegment(sketch, "E6828", {"start": v(886.31, -14.9) * mm, "end": v(886.63, -14.6) * mm});
            skLineSegment(sketch, "E6829", {"start": v(886.63, -14.6) * mm, "end": v(887.86, -13.43) * mm});
            skLineSegment(sketch, "E6830", {"start": v(887.86, -13.43) * mm, "end": v(891.41, -9.74) * mm});
            skLineSegment(sketch, "E6831", {"start": v(891.41, -9.74) * mm, "end": v(896.11, -4.7) * mm});
            skLineSegment(sketch, "E6832", {"start": v(896.11, -4.7) * mm, "end": v(900.91, 0.21) * mm});
            skLineSegment(sketch, "E6833", {"start": v(900.91, 0.21) * mm, "end": v(904.67, 3.66) * mm});
            skLineSegment(sketch, "E6834", {"start": v(904.67, 3.66) * mm, "end": v(906, 4.7) * mm});
            skLineSegment(sketch, "E6835", {"start": v(906, 4.7) * mm, "end": v(906.61, 5.63) * mm});
            skLineSegment(sketch, "E6836", {"start": v(906.61, 5.63) * mm, "end": v(908.63, 8.3) * mm});
            skLineSegment(sketch, "E6837", {"start": v(908.63, 8.3) * mm, "end": v(911.41, 11.57) * mm});
            skLineSegment(sketch, "E6838", {"start": v(911.41, 11.57) * mm, "end": v(914.25, 14.68) * mm});
            skLineSegment(sketch, "E6839", {"start": v(914.25, 14.68) * mm, "end": v(917.03, 17.77) * mm});
            skLineSegment(sketch, "E6840", {"start": v(917.03, 17.77) * mm, "end": v(919.64, 20.97) * mm});
            skLineSegment(sketch, "E6841", {"start": v(919.64, 20.97) * mm, "end": v(921.96, 24.44) * mm});
            skLineSegment(sketch, "E6842", {"start": v(921.96, 24.44) * mm, "end": v(923.9, 28.3) * mm});
            skLineSegment(sketch, "E6843", {"start": v(923.9, 28.3) * mm, "end": v(925.07, 31.6) * mm});
            skLineSegment(sketch, "E6844", {"start": v(925.07, 31.6) * mm, "end": v(925.35, 32.72) * mm});
            skLineSegment(sketch, "E6845", {"start": v(925.35, 32.72) * mm, "end": v(925.28, 32.8) * mm});
            skLineSegment(sketch, "E6846", {"start": v(925.28, 32.8) * mm, "end": v(924.93, 33.44) * mm});
            skLineSegment(sketch, "E6847", {"start": v(924.93, 33.44) * mm, "end": v(924.91, 33.5) * mm});
            skLineSegment(sketch, "E6848", {"start": v(924.91, 33.5) * mm, "end": v(923.67, 33.39) * mm});
            skLineSegment(sketch, "E6849", {"start": v(923.67, 33.39) * mm, "end": v(920, 32.29) * mm});
            skLineSegment(sketch, "E6850", {"start": v(920, 32.29) * mm, "end": v(915.52, 29.9) * mm});
            skLineSegment(sketch, "E6851", {"start": v(915.52, 29.9) * mm, "end": v(911.38, 26.85) * mm});
            skLineSegment(sketch, "E6852", {"start": v(911.38, 26.85) * mm, "end": v(908.46, 24.41) * mm});
            skLineSegment(sketch, "E6853", {"start": v(908.46, 24.41) * mm, "end": v(907.49, 23.6) * mm});
            skLineSegment(sketch, "E6854", {"start": v(907.49, 23.6) * mm, "end": v(906.48, 22.75) * mm});
            skLineSegment(sketch, "E6855", {"start": v(906.48, 22.75) * mm, "end": v(903.43, 20.21) * mm});
            skLineSegment(sketch, "E6856", {"start": v(903.43, 20.21) * mm, "end": v(899.37, 16.76) * mm});
            skLineSegment(sketch, "E6857", {"start": v(899.37, 16.76) * mm, "end": v(895.47, 13.15) * mm});
            skLineSegment(sketch, "E6858", {"start": v(895.47, 13.15) * mm, "end": v(892.72, 10.3) * mm});
            skLineSegment(sketch, "E6859", {"start": v(892.72, 10.3) * mm, "end": v(891.87, 9.29) * mm});
            skLineSegment(sketch, "E6860", {"start": v(891.87, 9.29) * mm, "end": v(891.76, 9.16) * mm});
            skLineSegment(sketch, "E6861", {"start": v(891.76, 9.16) * mm, "end": v(891.34, 8.85) * mm});
            skLineSegment(sketch, "E6862", {"start": v(891.34, 8.85) * mm, "end": v(890.81, 8.67) * mm});
            skLineSegment(sketch, "E6863", {"start": v(890.81, 8.67) * mm, "end": v(890.3, 8.6) * mm});
            skLineSegment(sketch, "E6864", {"start": v(890.3, 8.6) * mm, "end": v(889.91, 8.55) * mm});
            skLineSegment(sketch, "E6865", {"start": v(889.91, 8.55) * mm, "end": v(889.8, 8.5) * mm});
            skLineSegment(sketch, "E6866", {"start": v(889.8, 8.5) * mm, "end": v(888.84, 7.25) * mm});
            skLineSegment(sketch, "E6867", {"start": v(888.84, 7.25) * mm, "end": v(885.7, 3.7) * mm});
            skLineSegment(sketch, "E6868", {"start": v(885.7, 3.7) * mm, "end": v(881.22, -0.86) * mm});
            skLineSegment(sketch, "E6869", {"start": v(881.22, -0.86) * mm, "end": v(876.68, -5.39) * mm});
            skLineSegment(sketch, "E6870", {"start": v(876.68, -5.39) * mm, "end": v(873.42, -8.86) * mm});
            skLineSegment(sketch, "E6871", {"start": v(873.42, -8.86) * mm, "end": v(872.4, -10.08) * mm});
            skLineSegment(sketch, "E6872", {"start": v(872.4, -10.08) * mm, "end": v(872.3, -10.22) * mm});
            skLineSegment(sketch, "E6873", {"start": v(872.3, -10.22) * mm, "end": v(871.78, -11.01) * mm});
            skLineSegment(sketch, "E6874", {"start": v(871.78, -11.01) * mm, "end": v(871.32, -11.84) * mm});
            skLineSegment(sketch, "E6875", {"start": v(871.32, -11.84) * mm, "end": v(871.23, -12) * mm});
            skLineSegment(sketch, "E6876", {"start": v(871.23, -12) * mm, "end": v(870.96, -12.47) * mm});
            skLineSegment(sketch, "E6877", {"start": v(870.96, -12.47) * mm, "end": v(870.01, -13.8) * mm});
            skLineSegment(sketch, "E6878", {"start": v(870.01, -13.8) * mm, "end": v(868.58, -14.97) * mm});
            skLineSegment(sketch, "E6879", {"start": v(868.58, -14.97) * mm, "end": v(866.85, -15.29) * mm});
            skLineSegment(sketch, "E6880", {"start": v(866.85, -15.29) * mm, "end": v(865.2, -14.81) * mm});
            skLineSegment(sketch, "E6881", {"start": v(865.2, -14.81) * mm, "end": v(864.71, -14.53) * mm});
            skLineSegment(sketch, "E6882", {"start": v(864.71, -14.53) * mm, "end": v(864.1, -14.2) * mm});
            skLineSegment(sketch, "E6883", {"start": v(864.1, -14.2) * mm, "end": v(864.18, -13.5) * mm});
            skLineSegment(sketch, "E6884", {"start": v(864.18, -13.5) * mm, "end": v(864.25, -12.74) * mm});
            skLineSegment(sketch, "E6885", {"start": v(864.25, -12.74) * mm, "end": v(864.98, -10.48) * mm});
            skLineSegment(sketch, "E6886", {"start": v(864.98, -10.48) * mm, "end": v(866.55, -8.1) * mm});
            skLineSegment(sketch, "E6887", {"start": v(866.55, -8.1) * mm, "end": v(868.6, -6.06) * mm});
            skLineSegment(sketch, "E6888", {"start": v(868.6, -6.06) * mm, "end": v(870.3, -4.54) * mm});
            skLineSegment(sketch, "E6889", {"start": v(870.3, -4.54) * mm, "end": v(870.85, -4.01) * mm});
            skLineSegment(sketch, "E6890", {"start": v(870.85, -4.01) * mm, "end": v(871.5, -3.4) * mm});
            skLineSegment(sketch, "E6891", {"start": v(871.5, -3.4) * mm, "end": v(874.58, -0.07) * mm});
            skLineSegment(sketch, "E6892", {"start": v(874.58, -0.07) * mm, "end": v(877.56, 3.34) * mm});
            skLineSegment(sketch, "E6893", {"start": v(877.56, 3.34) * mm, "end": v(878.17, 4) * mm});
            skLineSegment(sketch, "E6894", {"start": v(878.17, 4) * mm, "end": v(878.18, 4) * mm});
            skLineSegment(sketch, "E6895", {"start": v(536.84, 129.98) * mm, "end": v(537.2, 130.18) * mm});
            skLineSegment(sketch, "E6896", {"start": v(537.2, 130.18) * mm, "end": v(538.93, 131.3) * mm});
            skLineSegment(sketch, "E6897", {"start": v(538.93, 131.3) * mm, "end": v(540.52, 132.62) * mm});
            skLineSegment(sketch, "E6898", {"start": v(540.52, 132.62) * mm, "end": v(540.8, 132.91) * mm});
            skLineSegment(sketch, "E6899", {"start": v(540.8, 132.91) * mm, "end": v(540.56, 133.03) * mm});
            skLineSegment(sketch, "E6900", {"start": v(540.56, 133.03) * mm, "end": v(539.36, 133.35) * mm});
            skLineSegment(sketch, "E6901", {"start": v(539.36, 133.35) * mm, "end": v(538.08, 133.24) * mm});
            skLineSegment(sketch, "E6902", {"start": v(538.08, 133.24) * mm, "end": v(537.8, 133.15) * mm});
            skLineSegment(sketch, "E6903", {"start": v(537.8, 133.15) * mm, "end": v(537.75, 132.85) * mm});
            skLineSegment(sketch, "E6904", {"start": v(537.75, 132.85) * mm, "end": v(537.39, 131.48) * mm});
            skLineSegment(sketch, "E6905", {"start": v(537.39, 131.48) * mm, "end": v(536.93, 130.22) * mm});
            skLineSegment(sketch, "E6906", {"start": v(536.93, 130.22) * mm, "end": v(536.84, 129.97) * mm});
            skLineSegment(sketch, "E6907", {"start": v(536.84, 129.97) * mm, "end": v(536.84, 129.98) * mm});
            skLineSegment(sketch, "E6908", {"start": v(117.04, 68.1) * mm, "end": v(113.56, 66.55) * mm});
            skLineSegment(sketch, "E6909", {"start": v(113.56, 66.55) * mm, "end": v(103.5, 61.07) * mm});
            skLineSegment(sketch, "E6910", {"start": v(103.5, 61.07) * mm, "end": v(91.02, 52.7) * mm});
            skLineSegment(sketch, "E6911", {"start": v(91.02, 52.7) * mm, "end": v(79.43, 43.12) * mm});
            skLineSegment(sketch, "E6912", {"start": v(79.43, 43.12) * mm, "end": v(71.2, 35.24) * mm});
            skLineSegment(sketch, "E6913", {"start": v(71.2, 35.24) * mm, "end": v(68.6, 32.49) * mm});
            skLineSegment(sketch, "E6914", {"start": v(68.6, 32.49) * mm, "end": v(70.51, 33.18) * mm});
            skLineSegment(sketch, "E6915", {"start": v(70.51, 33.18) * mm, "end": v(79.96, 37.19) * mm});
            skLineSegment(sketch, "E6916", {"start": v(79.96, 37.19) * mm, "end": v(89.07, 41.87) * mm});
            skLineSegment(sketch, "E6917", {"start": v(89.07, 41.87) * mm, "end": v(90.83, 42.91) * mm});
            skLineSegment(sketch, "E6918", {"start": v(90.83, 42.91) * mm, "end": v(91.7, 43.43) * mm});
            skLineSegment(sketch, "E6919", {"start": v(91.7, 43.43) * mm, "end": v(95.7, 46.56) * mm});
            skLineSegment(sketch, "E6920", {"start": v(95.7, 46.56) * mm, "end": v(99.65, 49.77) * mm});
            skLineSegment(sketch, "E6921", {"start": v(99.65, 49.77) * mm, "end": v(100.5, 50.33) * mm});
            skLineSegment(sketch, "E6922", {"start": v(100.5, 50.33) * mm, "end": v(101.3, 50.85) * mm});
            skLineSegment(sketch, "E6923", {"start": v(101.3, 50.85) * mm, "end": v(103.55, 52.66) * mm});
            skLineSegment(sketch, "E6924", {"start": v(103.55, 52.66) * mm, "end": v(106.22, 55.25) * mm});
            skLineSegment(sketch, "E6925", {"start": v(106.22, 55.25) * mm, "end": v(108.75, 57.99) * mm});
            skLineSegment(sketch, "E6926", {"start": v(108.75, 57.99) * mm, "end": v(110.71, 60.08) * mm});
            skLineSegment(sketch, "E6927", {"start": v(110.71, 60.08) * mm, "end": v(111.4, 60.76) * mm});
            skLineSegment(sketch, "E6928", {"start": v(111.4, 60.76) * mm, "end": v(111.64, 61) * mm});
            skLineSegment(sketch, "E6929", {"start": v(111.64, 61) * mm, "end": v(113.01, 62.16) * mm});
            skLineSegment(sketch, "E6930", {"start": v(113.01, 62.16) * mm, "end": v(114.42, 63.29) * mm});
            skLineSegment(sketch, "E6931", {"start": v(114.42, 63.29) * mm, "end": v(114.68, 63.52) * mm});
            skLineSegment(sketch, "E6932", {"start": v(114.68, 63.52) * mm, "end": v(114.96, 63.75) * mm});
            skLineSegment(sketch, "E6933", {"start": v(114.96, 63.75) * mm, "end": v(115.75, 64.5) * mm});
            skLineSegment(sketch, "E6934", {"start": v(115.75, 64.5) * mm, "end": v(116.64, 65.59) * mm});
            skLineSegment(sketch, "E6935", {"start": v(116.64, 65.59) * mm, "end": v(117.14, 66.79) * mm});
            skLineSegment(sketch, "E6936", {"start": v(117.14, 66.79) * mm, "end": v(117.15, 67.8) * mm});
            skLineSegment(sketch, "E6937", {"start": v(117.15, 67.8) * mm, "end": v(117.05, 68.1) * mm});
            skLineSegment(sketch, "E6938", {"start": v(117.05, 68.1) * mm, "end": v(117.04, 68.1) * mm});
            skLineSegment(sketch, "E6939", {"start": v(125.66, 50.44) * mm, "end": v(125.93, 51.1) * mm});
            skLineSegment(sketch, "E6940", {"start": v(125.93, 51.1) * mm, "end": v(127.06, 52.94) * mm});
            skLineSegment(sketch, "E6941", {"start": v(127.06, 52.94) * mm, "end": v(128.76, 55.18) * mm});
            skLineSegment(sketch, "E6942", {"start": v(128.76, 55.18) * mm, "end": v(130.46, 57.4) * mm});
            skLineSegment(sketch, "E6943", {"start": v(130.46, 57.4) * mm, "end": v(131.55, 59.17) * mm});
            skLineSegment(sketch, "E6944", {"start": v(131.55, 59.17) * mm, "end": v(131.82, 59.8) * mm});
            skLineSegment(sketch, "E6945", {"start": v(131.82, 59.8) * mm, "end": v(130.85, 59.89) * mm});
            skLineSegment(sketch, "E6946", {"start": v(130.85, 59.89) * mm, "end": v(127.9, 59.4) * mm});
            skLineSegment(sketch, "E6947", {"start": v(127.9, 59.4) * mm, "end": v(124.31, 57.8) * mm});
            skLineSegment(sketch, "E6948", {"start": v(124.31, 57.8) * mm, "end": v(120.98, 55.53) * mm});
            skLineSegment(sketch, "E6949", {"start": v(120.98, 55.53) * mm, "end": v(118.62, 53.7) * mm});
            skLineSegment(sketch, "E6950", {"start": v(118.62, 53.7) * mm, "end": v(117.82, 53.1) * mm});
            skLineSegment(sketch, "E6951", {"start": v(117.82, 53.1) * mm, "end": v(116.67, 52.26) * mm});
            skLineSegment(sketch, "E6952", {"start": v(116.67, 52.26) * mm, "end": v(110.93, 47.95) * mm});
            skLineSegment(sketch, "E6953", {"start": v(110.93, 47.95) * mm, "end": v(105.1, 43.8) * mm});
            skLineSegment(sketch, "E6954", {"start": v(105.1, 43.8) * mm, "end": v(103.88, 43.03) * mm});
            skLineSegment(sketch, "E6955", {"start": v(103.88, 43.03) * mm, "end": v(103.65, 42.64) * mm});
            skLineSegment(sketch, "E6956", {"start": v(103.65, 42.64) * mm, "end": v(102.18, 40.9) * mm});
            skLineSegment(sketch, "E6957", {"start": v(102.18, 40.9) * mm, "end": v(100.47, 39.38) * mm});
            skLineSegment(sketch, "E6958", {"start": v(100.47, 39.38) * mm, "end": v(100.13, 39.1) * mm});
            skLineSegment(sketch, "E6959", {"start": v(100.13, 39.1) * mm, "end": v(99.86, 38.88) * mm});
            skLineSegment(sketch, "E6960", {"start": v(99.86, 38.88) * mm, "end": v(99.07, 38.25) * mm});
            skLineSegment(sketch, "E6961", {"start": v(99.07, 38.25) * mm, "end": v(97.94, 37.3) * mm});
            skLineSegment(sketch, "E6962", {"start": v(97.94, 37.3) * mm, "end": v(96.86, 36.23) * mm});
            skLineSegment(sketch, "E6963", {"start": v(96.86, 36.23) * mm, "end": v(96.17, 35.38) * mm});
            skLineSegment(sketch, "E6964", {"start": v(96.17, 35.38) * mm, "end": v(95.98, 35.07) * mm});
            skLineSegment(sketch, "E6965", {"start": v(95.98, 35.07) * mm, "end": v(97.1, 35.16) * mm});
            skLineSegment(sketch, "E6966", {"start": v(97.1, 35.16) * mm, "end": v(100.44, 35.74) * mm});
            skLineSegment(sketch, "E6967", {"start": v(100.44, 35.74) * mm, "end": v(104.5, 36.93) * mm});
            skLineSegment(sketch, "E6968", {"start": v(104.5, 36.93) * mm, "end": v(108.28, 38.55) * mm});
            skLineSegment(sketch, "E6969", {"start": v(108.28, 38.55) * mm, "end": v(111.84, 40.52) * mm});
            skLineSegment(sketch, "E6970", {"start": v(111.84, 40.52) * mm, "end": v(115.27, 42.78) * mm});
            skLineSegment(sketch, "E6971", {"start": v(115.27, 42.78) * mm, "end": v(118.66, 45.24) * mm});
            skLineSegment(sketch, "E6972", {"start": v(118.66, 45.24) * mm, "end": v(122.09, 47.82) * mm});
            skLineSegment(sketch, "E6973", {"start": v(122.09, 47.82) * mm, "end": v(124.76, 49.8) * mm});
            skLineSegment(sketch, "E6974", {"start": v(124.76, 49.8) * mm, "end": v(125.66, 50.45) * mm});
            skLineSegment(sketch, "E6975", {"start": v(125.66, 50.45) * mm, "end": v(125.66, 50.44) * mm});
            skLineSegment(sketch, "E6976", {"start": v(141.67, 51.27) * mm, "end": v(140.26, 50.94) * mm});
            skLineSegment(sketch, "E6977", {"start": v(140.26, 50.94) * mm, "end": v(136.21, 49.16) * mm});
            skLineSegment(sketch, "E6978", {"start": v(136.21, 49.16) * mm, "end": v(131.37, 45.87) * mm});
            skLineSegment(sketch, "E6979", {"start": v(131.37, 45.87) * mm, "end": v(127.03, 41.81) * mm});
            skLineSegment(sketch, "E6980", {"start": v(127.03, 41.81) * mm, "end": v(124.05, 38.53) * mm});
            skLineSegment(sketch, "E6981", {"start": v(124.05, 38.53) * mm, "end": v(123.1, 37.4) * mm});
            skLineSegment(sketch, "E6982", {"start": v(123.1, 37.4) * mm, "end": v(123.42, 37.5) * mm});
            skLineSegment(sketch, "E6983", {"start": v(123.42, 37.5) * mm, "end": v(124.95, 38.33) * mm});
            skLineSegment(sketch, "E6984", {"start": v(124.95, 38.33) * mm, "end": v(126.46, 39.28) * mm});
            skLineSegment(sketch, "E6985", {"start": v(126.46, 39.28) * mm, "end": v(126.77, 39.43) * mm});
            skLineSegment(sketch, "E6986", {"start": v(126.77, 39.43) * mm, "end": v(127.31, 39.7) * mm});
            skLineSegment(sketch, "E6987", {"start": v(127.31, 39.7) * mm, "end": v(128.97, 40.5) * mm});
            skLineSegment(sketch, "E6988", {"start": v(128.97, 40.5) * mm, "end": v(131.2, 41.59) * mm});
            skLineSegment(sketch, "E6989", {"start": v(131.2, 41.59) * mm, "end": v(133.41, 42.73) * mm});
            skLineSegment(sketch, "E6990", {"start": v(133.41, 42.73) * mm, "end": v(135.52, 43.99) * mm});
            skLineSegment(sketch, "E6991", {"start": v(135.52, 43.99) * mm, "end": v(137.46, 45.42) * mm});
            skLineSegment(sketch, "E6992", {"start": v(137.46, 45.42) * mm, "end": v(139.18, 47.07) * mm});
            skLineSegment(sketch, "E6993", {"start": v(139.18, 47.07) * mm, "end": v(140.6, 49) * mm});
            skLineSegment(sketch, "E6994", {"start": v(140.6, 49) * mm, "end": v(141.46, 50.68) * mm});
            skLineSegment(sketch, "E6995", {"start": v(141.46, 50.68) * mm, "end": v(141.67, 51.27) * mm});
            skLineSegment(sketch, "E6996", {"start": v(141.67, 51.27) * mm, "end": v(141.67, 51.27) * mm});
            skLineSegment(sketch, "E6997", {"start": v(10.12, -18.77) * mm, "end": v(9.54, -18.56) * mm});
            skLineSegment(sketch, "E6998", {"start": v(9.54, -18.56) * mm, "end": v(6.56, -17.94) * mm});
            skLineSegment(sketch, "E6999", {"start": v(6.56, -17.94) * mm, "end": v(3.5, -17.85) * mm});
            skLineSegment(sketch, "E7000", {"start": v(3.5, -17.85) * mm, "end": v(2.89, -17.9) * mm});
            skLineSegment(sketch, "E7001", {"start": v(2.89, -17.9) * mm, "end": v(0.12, -18.15) * mm});
            skLineSegment(sketch, "E7002", {"start": v(0.12, -18.15) * mm, "end": v(2.02, -16.12) * mm});
            skLineSegment(sketch, "E7003", {"start": v(2.02, -16.12) * mm, "end": v(2.1, -16.01) * mm});
            skLineSegment(sketch, "E7004", {"start": v(2.1, -16.01) * mm, "end": v(3.04, -15.03) * mm});
            skLineSegment(sketch, "E7005", {"start": v(3.04, -15.03) * mm, "end": v(3.13, -14.93) * mm});
            skLineSegment(sketch, "E7006", {"start": v(3.13, -14.93) * mm, "end": v(3.94, -14.17) * mm});
            skLineSegment(sketch, "E7007", {"start": v(3.94, -14.17) * mm, "end": v(6.3, -11.78) * mm});
            skLineSegment(sketch, "E7008", {"start": v(6.3, -11.78) * mm, "end": v(9.07, -8.43) * mm});
            skLineSegment(sketch, "E7009", {"start": v(9.07, -8.43) * mm, "end": v(11.24, -4.7) * mm});
            skLineSegment(sketch, "E7010", {"start": v(11.24, -4.7) * mm, "end": v(12.37, -1.5) * mm});
            skLineSegment(sketch, "E7011", {"start": v(12.37, -1.5) * mm, "end": v(12.56, -0.41) * mm});
            skLineSegment(sketch, "E7012", {"start": v(12.56, -0.41) * mm, "end": v(12.58, -0.28) * mm});
            skLineSegment(sketch, "E7013", {"start": v(12.58, -0.28) * mm, "end": v(12.58, 0.5) * mm});
            skLineSegment(sketch, "E7014", {"start": v(12.58, 0.5) * mm, "end": v(12.5, 1.27) * mm});
            skLineSegment(sketch, "E7015", {"start": v(12.5, 1.27) * mm, "end": v(12.5, 1.4) * mm});
            skLineSegment(sketch, "E7016", {"start": v(12.5, 1.4) * mm, "end": v(12.46, 1.76) * mm});
            skLineSegment(sketch, "E7017", {"start": v(12.46, 1.76) * mm, "end": v(12.43, 2.82) * mm});
            skLineSegment(sketch, "E7018", {"start": v(12.43, 2.82) * mm, "end": v(12.64, 4.1) * mm});
            skLineSegment(sketch, "E7019", {"start": v(12.64, 4.1) * mm, "end": v(13.27, 5.2) * mm});
            skLineSegment(sketch, "E7020", {"start": v(13.27, 5.2) * mm, "end": v(14.13, 5.87) * mm});
            skLineSegment(sketch, "E7021", {"start": v(14.13, 5.87) * mm, "end": v(14.45, 6.02) * mm});
            skLineSegment(sketch, "E7022", {"start": v(14.45, 6.02) * mm, "end": v(14.6, 6.1) * mm});
            skLineSegment(sketch, "E7023", {"start": v(14.6, 6.1) * mm, "end": v(15.38, 6.34) * mm});
            skLineSegment(sketch, "E7024", {"start": v(15.38, 6.34) * mm, "end": v(16.21, 6.3) * mm});
            skLineSegment(sketch, "E7025", {"start": v(16.21, 6.3) * mm, "end": v(16.38, 6.25) * mm});
            skLineSegment(sketch, "E7026", {"start": v(16.38, 6.25) * mm, "end": v(16.54, 6.19) * mm});
            skLineSegment(sketch, "E7027", {"start": v(16.54, 6.19) * mm, "end": v(17, 5.9) * mm});
            skLineSegment(sketch, "E7028", {"start": v(17, 5.9) * mm, "end": v(17.51, 5.4) * mm});
            skLineSegment(sketch, "E7029", {"start": v(17.51, 5.4) * mm, "end": v(17.92, 4.82) * mm});
            skLineSegment(sketch, "E7030", {"start": v(17.92, 4.82) * mm, "end": v(18.19, 4.35) * mm});
            skLineSegment(sketch, "E7031", {"start": v(18.19, 4.35) * mm, "end": v(18.27, 4.2) * mm});
            skLineSegment(sketch, "E7032", {"start": v(18.27, 4.2) * mm, "end": v(18.31, 4.13) * mm});
            skLineSegment(sketch, "E7033", {"start": v(18.31, 4.13) * mm, "end": v(18.6, 3.6) * mm});
            skLineSegment(sketch, "E7034", {"start": v(18.6, 3.6) * mm, "end": v(18.93, 3.1) * mm});
            skLineSegment(sketch, "E7035", {"start": v(18.93, 3.1) * mm, "end": v(19, 3.05) * mm});
            skLineSegment(sketch, "E7036", {"start": v(19, 3.05) * mm, "end": v(19.45, 2.65) * mm});
            skLineSegment(sketch, "E7037", {"start": v(19.45, 2.65) * mm, "end": v(19.34, 2.05) * mm});
            skLineSegment(sketch, "E7038", {"start": v(19.34, 2.05) * mm, "end": v(19.15, 1.03) * mm});
            skLineSegment(sketch, "E7039", {"start": v(19.15, 1.03) * mm, "end": v(19.02, -2.13) * mm});
            skLineSegment(sketch, "E7040", {"start": v(19.02, -2.13) * mm, "end": v(19.39, -6.52) * mm});
            skLineSegment(sketch, "E7041", {"start": v(19.39, -6.52) * mm, "end": v(20.22, -10.88) * mm});
            skLineSegment(sketch, "E7042", {"start": v(20.22, -10.88) * mm, "end": v(21, -13.95) * mm});
            skLineSegment(sketch, "E7043", {"start": v(21, -13.95) * mm, "end": v(21.3, -14.96) * mm});
            skLineSegment(sketch, "E7044", {"start": v(21.3, -14.96) * mm, "end": v(21.62, -16.13) * mm});
            skLineSegment(sketch, "E7045", {"start": v(21.62, -16.13) * mm, "end": v(20.43, -16.31) * mm});
            skLineSegment(sketch, "E7046", {"start": v(20.43, -16.31) * mm, "end": v(19.65, -16.44) * mm});
            skLineSegment(sketch, "E7047", {"start": v(19.65, -16.44) * mm, "end": v(15.92, -17.38) * mm});
            skLineSegment(sketch, "E7048", {"start": v(15.92, -17.38) * mm, "end": v(12.35, -18.8) * mm});
            skLineSegment(sketch, "E7049", {"start": v(12.35, -18.8) * mm, "end": v(11.66, -19.18) * mm});
            skLineSegment(sketch, "E7050", {"start": v(11.66, -19.18) * mm, "end": v(11.16, -19.44) * mm});
            skLineSegment(sketch, "E7051", {"start": v(11.16, -19.44) * mm, "end": v(10.66, -19.19) * mm});
            skLineSegment(sketch, "E7052", {"start": v(10.66, -19.19) * mm, "end": v(10.6, -19.15) * mm});
            skLineSegment(sketch, "E7053", {"start": v(10.6, -19.15) * mm, "end": v(10.17, -18.82) * mm});
            skLineSegment(sketch, "E7054", {"start": v(10.17, -18.82) * mm, "end": v(10.12, -18.78) * mm});
            skLineSegment(sketch, "E7055", {"start": v(10.12, -18.78) * mm, "end": v(10.12, -18.77) * mm});
            skLineSegment(sketch, "E7056", {"start": v(-368.39, 15.64) * mm, "end": v(-371.54, 13.04) * mm});
            skLineSegment(sketch, "E7057", {"start": v(-371.54, 13.04) * mm, "end": v(-386.93, -0.42) * mm});
            skLineSegment(sketch, "E7058", {"start": v(-386.93, -0.42) * mm, "end": v(-401.71, -14.56) * mm});
            skLineSegment(sketch, "E7059", {"start": v(-401.71, -14.56) * mm, "end": v(-404.57, -17.5) * mm});
            skLineSegment(sketch, "E7060", {"start": v(-404.57, -17.5) * mm, "end": v(-405.51, -18.49) * mm});
            skLineSegment(sketch, "E7061", {"start": v(-405.51, -18.49) * mm, "end": v(-409.94, -23.67) * mm});
            skLineSegment(sketch, "E7062", {"start": v(-409.94, -23.67) * mm, "end": v(-414.35, -28.86) * mm});
            skLineSegment(sketch, "E7063", {"start": v(-414.35, -28.86) * mm, "end": v(-415.29, -29.85) * mm});
            skLineSegment(sketch, "E7064", {"start": v(-415.29, -29.85) * mm, "end": v(-416.29, -30.9) * mm});
            skLineSegment(sketch, "E7065", {"start": v(-416.29, -30.9) * mm, "end": v(-419.5, -33.88) * mm});
            skLineSegment(sketch, "E7066", {"start": v(-419.5, -33.88) * mm, "end": v(-423.95, -37.66) * mm});
            skLineSegment(sketch, "E7067", {"start": v(-423.95, -37.66) * mm, "end": v(-428.43, -41.4) * mm});
            skLineSegment(sketch, "E7068", {"start": v(-428.43, -41.4) * mm, "end": v(-431.7, -44.3) * mm});
            skLineSegment(sketch, "E7069", {"start": v(-431.7, -44.3) * mm, "end": v(-432.74, -45.32) * mm});
            skLineSegment(sketch, "E7070", {"start": v(-432.74, -45.32) * mm, "end": v(-433.04, -45.62) * mm});
            skLineSegment(sketch, "E7071", {"start": v(-433.04, -45.62) * mm, "end": v(-434.4, -47.26) * mm});
            skLineSegment(sketch, "E7072", {"start": v(-434.4, -47.26) * mm, "end": v(-435.78, -48.9) * mm});
            skLineSegment(sketch, "E7073", {"start": v(-435.78, -48.9) * mm, "end": v(-436.08, -49.21) * mm});
            skLineSegment(sketch, "E7074", {"start": v(-436.08, -49.21) * mm, "end": v(-437.35, -50.5) * mm});
            skLineSegment(sketch, "E7075", {"start": v(-437.35, -50.5) * mm, "end": v(-441.05, -54.48) * mm});
            skLineSegment(sketch, "E7076", {"start": v(-441.05, -54.48) * mm, "end": v(-445.93, -59.85) * mm});
            skLineSegment(sketch, "E7077", {"start": v(-445.93, -59.85) * mm, "end": v(-450.87, -65.15) * mm});
            skLineSegment(sketch, "E7078", {"start": v(-450.87, -65.15) * mm, "end": v(-454.7, -69) * mm});
            skLineSegment(sketch, "E7079", {"start": v(-454.7, -69) * mm, "end": v(-456.03, -70.22) * mm});
            skLineSegment(sketch, "E7080", {"start": v(-456.03, -70.22) * mm, "end": v(-459.6, -73.52) * mm});
            skLineSegment(sketch, "E7081", {"start": v(-459.6, -73.52) * mm, "end": v(-452.23, -55.67) * mm});
            skLineSegment(sketch, "E7082", {"start": v(-452.23, -55.67) * mm, "end": v(-452.09, -55.51) * mm});
            skLineSegment(sketch, "E7083", {"start": v(-452.09, -55.51) * mm, "end": v(-451.51, -54.94) * mm});
            skLineSegment(sketch, "E7084", {"start": v(-451.51, -54.94) * mm, "end": v(-445.88, -49.05) * mm});
            skLineSegment(sketch, "E7085", {"start": v(-445.88, -49.05) * mm, "end": v(-445.35, -48.44) * mm});
            skLineSegment(sketch, "E7086", {"start": v(-445.35, -48.44) * mm, "end": v(-444.63, -47.63) * mm});
            skLineSegment(sketch, "E7087", {"start": v(-444.63, -47.63) * mm, "end": v(-437.35, -39.7) * mm});
            skLineSegment(sketch, "E7088", {"start": v(-437.35, -39.7) * mm, "end": v(-436.6, -38.91) * mm});
            skLineSegment(sketch, "E7089", {"start": v(-436.6, -38.91) * mm, "end": v(-435.87, -38.13) * mm});
            skLineSegment(sketch, "E7090", {"start": v(-435.87, -38.13) * mm, "end": v(-432.53, -33.92) * mm});
            skLineSegment(sketch, "E7091", {"start": v(-432.53, -33.92) * mm, "end": v(-429.3, -29.6) * mm});
            skLineSegment(sketch, "E7092", {"start": v(-429.3, -29.6) * mm, "end": v(-428.61, -28.77) * mm});
            skLineSegment(sketch, "E7093", {"start": v(-428.61, -28.77) * mm, "end": v(-428.44, -28.56) * mm});
            skLineSegment(sketch, "E7094", {"start": v(-428.44, -28.56) * mm, "end": v(-427.8, -27.99) * mm});
            skLineSegment(sketch, "E7095", {"start": v(-427.8, -27.99) * mm, "end": v(-426.9, -27.33) * mm});
            skLineSegment(sketch, "E7096", {"start": v(-426.9, -27.33) * mm, "end": v(-426.01, -26.7) * mm});
            skLineSegment(sketch, "E7097", {"start": v(-426.01, -26.7) * mm, "end": v(-425.43, -26.19) * mm});
            skLineSegment(sketch, "E7098", {"start": v(-425.43, -26.19) * mm, "end": v(-425.28, -25.99) * mm});
            skLineSegment(sketch, "E7099", {"start": v(-425.28, -25.99) * mm, "end": v(-425.05, -25.7) * mm});
            skLineSegment(sketch, "E7100", {"start": v(-425.05, -25.7) * mm, "end": v(-424.48, -24.72) * mm});
            skLineSegment(sketch, "E7101", {"start": v(-424.48, -24.72) * mm, "end": v(-423.8, -23.37) * mm});
            skLineSegment(sketch, "E7102", {"start": v(-423.8, -23.37) * mm, "end": v(-423.1, -22) * mm});
            skLineSegment(sketch, "E7103", {"start": v(-423.1, -22) * mm, "end": v(-422.51, -21.02) * mm});
            skLineSegment(sketch, "E7104", {"start": v(-422.51, -21.02) * mm, "end": v(-422.28, -20.72) * mm});
            skLineSegment(sketch, "E7105", {"start": v(-422.28, -20.72) * mm, "end": v(-421.42, -19.6) * mm});
            skLineSegment(sketch, "E7106", {"start": v(-421.42, -19.6) * mm, "end": v(-416.92, -14.12) * mm});
            skLineSegment(sketch, "E7107", {"start": v(-416.92, -14.12) * mm, "end": v(-412.57, -8.51) * mm});
            skLineSegment(sketch, "E7108", {"start": v(-412.57, -8.51) * mm, "end": v(-411.79, -7.31) * mm});
            skLineSegment(sketch, "E7109", {"start": v(-411.79, -7.31) * mm, "end": v(-411.8, -6.75) * mm});
            skLineSegment(sketch, "E7110", {"start": v(-411.8, -6.75) * mm, "end": v(-412.1, -5.08) * mm});
            skLineSegment(sketch, "E7111", {"start": v(-412.1, -5.08) * mm, "end": v(-412.81, -3.35) * mm});
            skLineSegment(sketch, "E7112", {"start": v(-412.81, -3.35) * mm, "end": v(-413.89, -2.08) * mm});
            skLineSegment(sketch, "E7113", {"start": v(-413.89, -2.08) * mm, "end": v(-415.26, -1.25) * mm});
            skLineSegment(sketch, "E7114", {"start": v(-415.26, -1.25) * mm, "end": v(-416.88, -0.81) * mm});
            skLineSegment(sketch, "E7115", {"start": v(-416.88, -0.81) * mm, "end": v(-418.71, -0.74) * mm});
            skLineSegment(sketch, "E7116", {"start": v(-418.71, -0.74) * mm, "end": v(-420.68, -1.02) * mm});
            skLineSegment(sketch, "E7117", {"start": v(-420.68, -1.02) * mm, "end": v(-422.25, -1.42) * mm});
            skLineSegment(sketch, "E7118", {"start": v(-422.25, -1.42) * mm, "end": v(-422.75, -1.6) * mm});
            skLineSegment(sketch, "E7119", {"start": v(-422.75, -1.6) * mm, "end": v(-423.24, -1.76) * mm});
            skLineSegment(sketch, "E7120", {"start": v(-423.24, -1.76) * mm, "end": v(-424.62, -2.5) * mm});
            skLineSegment(sketch, "E7121", {"start": v(-424.62, -2.5) * mm, "end": v(-426.6, -3.84) * mm});
            skLineSegment(sketch, "E7122", {"start": v(-426.6, -3.84) * mm, "end": v(-428.5, -5.32) * mm});
            skLineSegment(sketch, "E7123", {"start": v(-428.5, -5.32) * mm, "end": v(-429.73, -6.33) * mm});
            skLineSegment(sketch, "E7124", {"start": v(-429.73, -6.33) * mm, "end": v(-430.14, -6.67) * mm});
            skLineSegment(sketch, "E7125", {"start": v(-430.14, -6.67) * mm, "end": v(-430.29, -6.8) * mm});
            skLineSegment(sketch, "E7126", {"start": v(-430.29, -6.8) * mm, "end": v(-431.64, -8.26) * mm});
            skLineSegment(sketch, "E7127", {"start": v(-431.64, -8.26) * mm, "end": v(-431.77, -8.41) * mm});
            skLineSegment(sketch, "E7128", {"start": v(-431.77, -8.41) * mm, "end": v(-432.1, -8.81) * mm});
            skLineSegment(sketch, "E7129", {"start": v(-432.1, -8.81) * mm, "end": v(-433.17, -9.97) * mm});
            skLineSegment(sketch, "E7130", {"start": v(-433.17, -9.97) * mm, "end": v(-434.72, -11.22) * mm});
            skLineSegment(sketch, "E7131", {"start": v(-434.72, -11.22) * mm, "end": v(-436.5, -11.81) * mm});
            skLineSegment(sketch, "E7132", {"start": v(-436.5, -11.81) * mm, "end": v(-438.13, -11.63) * mm});
            skLineSegment(sketch, "E7133", {"start": v(-438.13, -11.63) * mm, "end": v(-438.61, -11.42) * mm});
            skLineSegment(sketch, "E7134", {"start": v(-438.61, -11.42) * mm, "end": v(-439.25, -11.15) * mm});
            skLineSegment(sketch, "E7135", {"start": v(-439.25, -11.15) * mm, "end": v(-439.25, -10.45) * mm});
            skLineSegment(sketch, "E7136", {"start": v(-439.25, -10.45) * mm, "end": v(-439.27, -9.9) * mm});
            skLineSegment(sketch, "E7137", {"start": v(-439.27, -9.9) * mm, "end": v(-438.86, -8.2) * mm});
            skLineSegment(sketch, "E7138", {"start": v(-438.86, -8.2) * mm, "end": v(-437.76, -6.22) * mm});
            skLineSegment(sketch, "E7139", {"start": v(-437.76, -6.22) * mm, "end": v(-436.22, -4.47) * mm});
            skLineSegment(sketch, "E7140", {"start": v(-436.22, -4.47) * mm, "end": v(-434.96, -3.31) * mm});
            skLineSegment(sketch, "E7141", {"start": v(-434.96, -3.31) * mm, "end": v(-434.52, -2.95) * mm});
            skLineSegment(sketch, "E7142", {"start": v(-434.52, -2.95) * mm, "end": v(-433.43, -2.02) * mm});
            skLineSegment(sketch, "E7143", {"start": v(-433.43, -2.02) * mm, "end": v(-430.09, 0.7) * mm});
            skLineSegment(sketch, "E7144", {"start": v(-430.09, 0.7) * mm, "end": v(-425.62, 4.3) * mm});
            skLineSegment(sketch, "E7145", {"start": v(-425.62, 4.3) * mm, "end": v(-421.28, 8.04) * mm});
            skLineSegment(sketch, "E7146", {"start": v(-421.28, 8.04) * mm, "end": v(-418.17, 11.03) * mm});
            skLineSegment(sketch, "E7147", {"start": v(-418.17, 11.03) * mm, "end": v(-417.2, 12.1) * mm});
            skLineSegment(sketch, "E7148", {"start": v(-417.2, 12.1) * mm, "end": v(-417, 12.34) * mm});
            skLineSegment(sketch, "E7149", {"start": v(-417, 12.34) * mm, "end": v(-416.66, 12.43) * mm});
            skLineSegment(sketch, "E7150", {"start": v(-416.66, 12.43) * mm, "end": v(-416.1, 12.56) * mm});
            skLineSegment(sketch, "E7151", {"start": v(-416.1, 12.56) * mm, "end": v(-413.65, 13.86) * mm});
            skLineSegment(sketch, "E7152", {"start": v(-413.65, 13.86) * mm, "end": v(-411.4, 15.5) * mm});
            skLineSegment(sketch, "E7153", {"start": v(-411.4, 15.5) * mm, "end": v(-410.92, 15.8) * mm});
            skLineSegment(sketch, "E7154", {"start": v(-410.92, 15.8) * mm, "end": v(-410.82, 15.86) * mm});
            skLineSegment(sketch, "E7155", {"start": v(-410.82, 15.86) * mm, "end": v(-410.69, 15.9) * mm});
            skLineSegment(sketch, "E7156", {"start": v(-410.69, 15.9) * mm, "end": v(-409.95, 16.14) * mm});
            skLineSegment(sketch, "E7157", {"start": v(-409.95, 16.14) * mm, "end": v(-406.36, 16.35) * mm});
            skLineSegment(sketch, "E7158", {"start": v(-406.36, 16.35) * mm, "end": v(-402.8, 15.62) * mm});
            skLineSegment(sketch, "E7159", {"start": v(-402.8, 15.62) * mm, "end": v(-402.09, 15.4) * mm});
            skLineSegment(sketch, "E7160", {"start": v(-402.09, 15.4) * mm, "end": v(-401.7, 15.28) * mm});
            skLineSegment(sketch, "E7161", {"start": v(-401.7, 15.28) * mm, "end": v(-400.52, 14.9) * mm});
            skLineSegment(sketch, "E7162", {"start": v(-400.52, 14.9) * mm, "end": v(-398.83, 14.42) * mm});
            skLineSegment(sketch, "E7163", {"start": v(-398.83, 14.42) * mm, "end": v(-397.12, 14.13) * mm});
            skLineSegment(sketch, "E7164", {"start": v(-397.12, 14.13) * mm, "end": v(-395.89, 14.11) * mm});
            skLineSegment(sketch, "E7165", {"start": v(-395.89, 14.11) * mm, "end": v(-395.5, 14.19) * mm});
            skLineSegment(sketch, "E7166", {"start": v(-395.5, 14.19) * mm, "end": v(-394.9, 14.3) * mm});
            skLineSegment(sketch, "E7167", {"start": v(-394.9, 14.3) * mm, "end": v(-393.2, 15.05) * mm});
            skLineSegment(sketch, "E7168", {"start": v(-393.2, 15.05) * mm, "end": v(-391.12, 16.35) * mm});
            skLineSegment(sketch, "E7169", {"start": v(-391.12, 16.35) * mm, "end": v(-389.04, 17.64) * mm});
            skLineSegment(sketch, "E7170", {"start": v(-389.04, 17.64) * mm, "end": v(-387.33, 18.33) * mm});
            skLineSegment(sketch, "E7171", {"start": v(-387.33, 18.33) * mm, "end": v(-386.73, 18.41) * mm});
            skLineSegment(sketch, "E7172", {"start": v(-386.73, 18.41) * mm, "end": v(-386.17, 18.5) * mm});
            skLineSegment(sketch, "E7173", {"start": v(-386.17, 18.5) * mm, "end": v(-382.81, 18.77) * mm});
            skLineSegment(sketch, "E7174", {"start": v(-382.81, 18.77) * mm, "end": v(-379.44, 18.8) * mm});
            skLineSegment(sketch, "E7175", {"start": v(-379.44, 18.8) * mm, "end": v(-378.87, 18.77) * mm});
            skLineSegment(sketch, "E7176", {"start": v(-378.87, 18.77) * mm, "end": v(-378.64, 18.77) * mm});
            skLineSegment(sketch, "E7177", {"start": v(-378.64, 18.77) * mm, "end": v(-377.93, 18.65) * mm});
            skLineSegment(sketch, "E7178", {"start": v(-377.93, 18.65) * mm, "end": v(-377, 18.4) * mm});
            skLineSegment(sketch, "E7179", {"start": v(-377, 18.4) * mm, "end": v(-376.1, 18.16) * mm});
            skLineSegment(sketch, "E7180", {"start": v(-376.1, 18.16) * mm, "end": v(-375.5, 18.08) * mm});
            skLineSegment(sketch, "E7181", {"start": v(-375.5, 18.08) * mm, "end": v(-375.3, 18.1) * mm});
            skLineSegment(sketch, "E7182", {"start": v(-375.3, 18.1) * mm, "end": v(-375.08, 18.13) * mm});
            skLineSegment(sketch, "E7183", {"start": v(-375.08, 18.13) * mm, "end": v(-374.45, 18.35) * mm});
            skLineSegment(sketch, "E7184", {"start": v(-374.45, 18.35) * mm, "end": v(-373.43, 18.83) * mm});
            skLineSegment(sketch, "E7185", {"start": v(-373.43, 18.83) * mm, "end": v(-372.4, 19.37) * mm});
            skLineSegment(sketch, "E7186", {"start": v(-372.4, 19.37) * mm, "end": v(-371.8, 19.7) * mm});
            skLineSegment(sketch, "E7187", {"start": v(-371.8, 19.7) * mm, "end": v(-371.59, 19.8) * mm});
            skLineSegment(sketch, "E7188", {"start": v(-371.59, 19.8) * mm, "end": v(-371.02, 20.1) * mm});
            skLineSegment(sketch, "E7189", {"start": v(-371.02, 20.1) * mm, "end": v(-369.24, 20.77) * mm});
            skLineSegment(sketch, "E7190", {"start": v(-369.24, 20.77) * mm, "end": v(-367.03, 21.03) * mm});
            skLineSegment(sketch, "E7191", {"start": v(-367.03, 21.03) * mm, "end": v(-365.07, 20.27) * mm});
            skLineSegment(sketch, "E7192", {"start": v(-365.07, 20.27) * mm, "end": v(-363.76, 18.75) * mm});
            skLineSegment(sketch, "E7193", {"start": v(-363.76, 18.75) * mm, "end": v(-363.48, 18.17) * mm});
            skLineSegment(sketch, "E7194", {"start": v(-363.48, 18.17) * mm, "end": v(-363.35, 17.9) * mm});
            skLineSegment(sketch, "E7195", {"start": v(-363.35, 17.9) * mm, "end": v(-363.37, 17.62) * mm});
            skLineSegment(sketch, "E7196", {"start": v(-363.37, 17.62) * mm, "end": v(-363.38, 17.49) * mm});
            skLineSegment(sketch, "E7197", {"start": v(-363.38, 17.49) * mm, "end": v(-363.56, 16.87) * mm});
            skLineSegment(sketch, "E7198", {"start": v(-363.56, 16.87) * mm, "end": v(-363.91, 16.32) * mm});
            skLineSegment(sketch, "E7199", {"start": v(-363.91, 16.32) * mm, "end": v(-364.01, 16.23) * mm});
            skLineSegment(sketch, "E7200", {"start": v(-364.01, 16.23) * mm, "end": v(-364.2, 16.04) * mm});
            skLineSegment(sketch, "E7201", {"start": v(-364.2, 16.04) * mm, "end": v(-365, 15.7) * mm});
            skLineSegment(sketch, "E7202", {"start": v(-365, 15.7) * mm, "end": v(-366.11, 15.57) * mm});
            skLineSegment(sketch, "E7203", {"start": v(-366.11, 15.57) * mm, "end": v(-367.28, 15.64) * mm});
            skLineSegment(sketch, "E7204", {"start": v(-367.28, 15.64) * mm, "end": v(-368.11, 15.67) * mm});
            skLineSegment(sketch, "E7205", {"start": v(-368.11, 15.67) * mm, "end": v(-368.38, 15.65) * mm});
            skLineSegment(sketch, "E7206", {"start": v(-368.38, 15.65) * mm, "end": v(-368.39, 15.64) * mm});
            skLineSegment(sketch, "E7207", {"start": v(270.57, 23.1) * mm, "end": v(270.1, 23.01) * mm});
            skLineSegment(sketch, "E7208", {"start": v(270.1, 23.01) * mm, "end": v(268.72, 22.77) * mm});
            skLineSegment(sketch, "E7209", {"start": v(268.72, 22.77) * mm, "end": v(266.84, 22.67) * mm});
            skLineSegment(sketch, "E7210", {"start": v(266.84, 22.67) * mm, "end": v(265.07, 23) * mm});
            skLineSegment(sketch, "E7211", {"start": v(265.07, 23) * mm, "end": v(263.85, 23.68) * mm});
            skLineSegment(sketch, "E7212", {"start": v(263.85, 23.68) * mm, "end": v(263.53, 24) * mm});
            skLineSegment(sketch, "E7213", {"start": v(263.53, 24) * mm, "end": v(263.24, 24.28) * mm});
            skLineSegment(sketch, "E7214", {"start": v(263.24, 24.28) * mm, "end": v(263.22, 24.68) * mm});
            skLineSegment(sketch, "E7215", {"start": v(263.22, 24.68) * mm, "end": v(263.2, 24.97) * mm});
            skLineSegment(sketch, "E7216", {"start": v(263.2, 24.97) * mm, "end": v(263.24, 25.84) * mm});
            skLineSegment(sketch, "E7217", {"start": v(263.24, 25.84) * mm, "end": v(263.5, 26.89) * mm});
            skLineSegment(sketch, "E7218", {"start": v(263.5, 26.89) * mm, "end": v(263.98, 27.84) * mm});
            skLineSegment(sketch, "E7219", {"start": v(263.98, 27.84) * mm, "end": v(264.52, 28.52) * mm});
            skLineSegment(sketch, "E7220", {"start": v(264.52, 28.52) * mm, "end": v(264.73, 28.72) * mm});
            skLineSegment(sketch, "E7221", {"start": v(264.73, 28.72) * mm, "end": v(264.86, 28.85) * mm});
            skLineSegment(sketch, "E7222", {"start": v(264.86, 28.85) * mm, "end": v(265.7, 29.53) * mm});
            skLineSegment(sketch, "E7223", {"start": v(265.7, 29.53) * mm, "end": v(266.56, 30.26) * mm});
            skLineSegment(sketch, "E7224", {"start": v(266.56, 30.26) * mm, "end": v(266.69, 30.41) * mm});
            skLineSegment(sketch, "E7225", {"start": v(266.69, 30.41) * mm, "end": v(266.64, 30.47) * mm});
            skLineSegment(sketch, "E7226", {"start": v(266.64, 30.47) * mm, "end": v(266.08, 30.94) * mm});
            skLineSegment(sketch, "E7227", {"start": v(266.08, 30.94) * mm, "end": v(266.01, 30.98) * mm});
            skLineSegment(sketch, "E7228", {"start": v(266.01, 30.98) * mm, "end": v(265.5, 31.27) * mm});
            skLineSegment(sketch, "E7229", {"start": v(265.5, 31.27) * mm, "end": v(263.62, 31.57) * mm});
            skLineSegment(sketch, "E7230", {"start": v(263.62, 31.57) * mm, "end": v(260.72, 31.57) * mm});
            skLineSegment(sketch, "E7231", {"start": v(260.72, 31.57) * mm, "end": v(257.61, 31.79) * mm});
            skLineSegment(sketch, "E7232", {"start": v(257.61, 31.79) * mm, "end": v(255.26, 32.58) * mm});
            skLineSegment(sketch, "E7233", {"start": v(255.26, 32.58) * mm, "end": v(254.62, 33.04) * mm});
            skLineSegment(sketch, "E7234", {"start": v(254.62, 33.04) * mm, "end": v(254.17, 33.37) * mm});
            skLineSegment(sketch, "E7235", {"start": v(254.17, 33.37) * mm, "end": v(254.18, 33.93) * mm});
            skLineSegment(sketch, "E7236", {"start": v(254.18, 33.93) * mm, "end": v(254.18, 34.24) * mm});
            skLineSegment(sketch, "E7237", {"start": v(254.18, 34.24) * mm, "end": v(254.35, 35.15) * mm});
            skLineSegment(sketch, "E7238", {"start": v(254.35, 35.15) * mm, "end": v(254.72, 36.03) * mm});
            skLineSegment(sketch, "E7239", {"start": v(254.72, 36.03) * mm, "end": v(255.16, 36.82) * mm});
            skLineSegment(sketch, "E7240", {"start": v(255.16, 36.82) * mm, "end": v(255.47, 37.52) * mm});
            skLineSegment(sketch, "E7241", {"start": v(255.47, 37.52) * mm, "end": v(255.55, 37.77) * mm});
            skLineSegment(sketch, "E7242", {"start": v(255.55, 37.77) * mm, "end": v(255.71, 38.4) * mm});
            skLineSegment(sketch, "E7243", {"start": v(255.71, 38.4) * mm, "end": v(256.36, 38.52) * mm});
            skLineSegment(sketch, "E7244", {"start": v(256.36, 38.52) * mm, "end": v(257.33, 38.72) * mm});
            skLineSegment(sketch, "E7245", {"start": v(257.33, 38.72) * mm, "end": v(260.36, 38.81) * mm});
            skLineSegment(sketch, "E7246", {"start": v(260.36, 38.81) * mm, "end": v(264.84, 38.3) * mm});
            skLineSegment(sketch, "E7247", {"start": v(264.84, 38.3) * mm, "end": v(269.15, 37.05) * mm});
            skLineSegment(sketch, "E7248", {"start": v(269.15, 37.05) * mm, "end": v(271.87, 35.72) * mm});
            skLineSegment(sketch, "E7249", {"start": v(271.87, 35.72) * mm, "end": v(272.65, 35.12) * mm});
            skLineSegment(sketch, "E7250", {"start": v(272.65, 35.12) * mm, "end": v(273.02, 34.84) * mm});
            skLineSegment(sketch, "E7251", {"start": v(273.02, 34.84) * mm, "end": v(274.02, 33.86) * mm});
            skLineSegment(sketch, "E7252", {"start": v(274.02, 33.86) * mm, "end": v(275.61, 32.07) * mm});
            skLineSegment(sketch, "E7253", {"start": v(275.61, 32.07) * mm, "end": v(277, 30.15) * mm});
            skLineSegment(sketch, "E7254", {"start": v(277, 30.15) * mm, "end": v(277.66, 28.95) * mm});
            skLineSegment(sketch, "E7255", {"start": v(277.66, 28.95) * mm, "end": v(277.76, 28.52) * mm});
            skLineSegment(sketch, "E7256", {"start": v(277.76, 28.52) * mm, "end": v(277.84, 28.14) * mm});
            skLineSegment(sketch, "E7257", {"start": v(277.84, 28.14) * mm, "end": v(277.85, 26.95) * mm});
            skLineSegment(sketch, "E7258", {"start": v(277.85, 26.95) * mm, "end": v(277.63, 25.5) * mm});
            skLineSegment(sketch, "E7259", {"start": v(277.63, 25.5) * mm, "end": v(277.37, 24.13) * mm});
            skLineSegment(sketch, "E7260", {"start": v(277.37, 24.13) * mm, "end": v(277.32, 23.11) * mm});
            skLineSegment(sketch, "E7261", {"start": v(277.32, 23.11) * mm, "end": v(277.37, 22.78) * mm});
            skLineSegment(sketch, "E7262", {"start": v(277.37, 22.78) * mm, "end": v(277.52, 21.79) * mm});
            skLineSegment(sketch, "E7263", {"start": v(277.52, 21.79) * mm, "end": v(276.54, 21.57) * mm});
            skLineSegment(sketch, "E7264", {"start": v(276.54, 21.57) * mm, "end": v(276.42, 21.55) * mm});
            skLineSegment(sketch, "E7265", {"start": v(276.42, 21.55) * mm, "end": v(275.2, 21.3) * mm});
            skLineSegment(sketch, "E7266", {"start": v(275.2, 21.3) * mm, "end": v(275.08, 21.27) * mm});
            skLineSegment(sketch, "E7267", {"start": v(275.08, 21.27) * mm, "end": v(274.78, 21.18) * mm});
            skLineSegment(sketch, "E7268", {"start": v(274.78, 21.18) * mm, "end": v(274.49, 21.28) * mm});
            skLineSegment(sketch, "E7269", {"start": v(274.49, 21.28) * mm, "end": v(274.26, 21.34) * mm});
            skLineSegment(sketch, "E7270", {"start": v(274.26, 21.34) * mm, "end": v(273.37, 21.6) * mm});
            skLineSegment(sketch, "E7271", {"start": v(273.37, 21.6) * mm, "end": v(272.95, 21.72) * mm});
            skLineSegment(sketch, "E7272", {"start": v(272.95, 21.72) * mm, "end": v(272.84, 21.75) * mm});
            skLineSegment(sketch, "E7273", {"start": v(272.84, 21.75) * mm, "end": v(271.66, 21.98) * mm});
            skLineSegment(sketch, "E7274", {"start": v(271.66, 21.98) * mm, "end": v(271.54, 22) * mm});
            skLineSegment(sketch, "E7275", {"start": v(271.54, 22) * mm, "end": v(270.2, 22.18) * mm});
            skLineSegment(sketch, "E7276", {"start": v(270.2, 22.18) * mm, "end": v(270.57, 23.1) * mm});
            skLineSegment(sketch, "E7277", {"start": v(220.5, 18.27) * mm, "end": v(220.36, 18.2) * mm});
            skLineSegment(sketch, "E7278", {"start": v(220.36, 18.2) * mm, "end": v(219.62, 17.8) * mm});
            skLineSegment(sketch, "E7279", {"start": v(219.62, 17.8) * mm, "end": v(212.35, 13.78) * mm});
            skLineSegment(sketch, "E7280", {"start": v(212.35, 13.78) * mm, "end": v(211.62, 13.37) * mm});
            skLineSegment(sketch, "E7281", {"start": v(211.62, 13.37) * mm, "end": v(211.18, 13.13) * mm});
            skLineSegment(sketch, "E7282", {"start": v(211.18, 13.13) * mm, "end": v(210.7, 13.32) * mm});
            skLineSegment(sketch, "E7283", {"start": v(210.7, 13.32) * mm, "end": v(210.66, 13.34) * mm});
            skLineSegment(sketch, "E7284", {"start": v(210.66, 13.34) * mm, "end": v(210.19, 13.52) * mm});
            skLineSegment(sketch, "E7285", {"start": v(210.19, 13.52) * mm, "end": v(210.14, 13.53) * mm});
            skLineSegment(sketch, "E7286", {"start": v(210.14, 13.53) * mm, "end": v(206.34, 13.23) * mm});
            skLineSegment(sketch, "E7287", {"start": v(206.34, 13.23) * mm, "end": v(206.15, 13.2) * mm});
            skLineSegment(sketch, "E7288", {"start": v(206.15, 13.2) * mm, "end": v(204.2, 12.92) * mm});
            skLineSegment(sketch, "E7289", {"start": v(204.2, 12.92) * mm, "end": v(204, 12.88) * mm});
            skLineSegment(sketch, "E7290", {"start": v(204, 12.88) * mm, "end": v(201.73, 12.45) * mm});
            skLineSegment(sketch, "E7291", {"start": v(201.73, 12.45) * mm, "end": v(202.88, 14.47) * mm});
            skLineSegment(sketch, "E7292", {"start": v(202.88, 14.47) * mm, "end": v(202.92, 14.55) * mm});
            skLineSegment(sketch, "E7293", {"start": v(202.92, 14.55) * mm, "end": v(203.37, 15.4) * mm});
            skLineSegment(sketch, "E7294", {"start": v(203.37, 15.4) * mm, "end": v(203.4, 15.5) * mm});
            skLineSegment(sketch, "E7295", {"start": v(203.4, 15.5) * mm, "end": v(202.3, 15.38) * mm});
            skLineSegment(sketch, "E7296", {"start": v(202.3, 15.38) * mm, "end": v(199.06, 14.67) * mm});
            skLineSegment(sketch, "E7297", {"start": v(199.06, 14.67) * mm, "end": v(195.19, 13.14) * mm});
            skLineSegment(sketch, "E7298", {"start": v(195.19, 13.14) * mm, "end": v(191.56, 10.96) * mm});
            skLineSegment(sketch, "E7299", {"start": v(191.56, 10.96) * mm, "end": v(188.84, 8.92) * mm});
            skLineSegment(sketch, "E7300", {"start": v(188.84, 8.92) * mm, "end": v(187.97, 8.19) * mm});
            skLineSegment(sketch, "E7301", {"start": v(187.97, 8.19) * mm, "end": v(187.72, 7.97) * mm});
            skLineSegment(sketch, "E7302", {"start": v(187.72, 7.97) * mm, "end": v(187.38, 7.93) * mm});
            skLineSegment(sketch, "E7303", {"start": v(187.38, 7.93) * mm, "end": v(185.36, 7.75) * mm});
            skLineSegment(sketch, "E7304", {"start": v(185.36, 7.75) * mm, "end": v(175.17, 6.23) * mm});
            skLineSegment(sketch, "E7305", {"start": v(175.17, 6.23) * mm, "end": v(165.08, 4.13) * mm});
            skLineSegment(sketch, "E7306", {"start": v(165.08, 4.13) * mm, "end": v(163.1, 3.66) * mm});
            skLineSegment(sketch, "E7307", {"start": v(163.1, 3.66) * mm, "end": v(161.3, 3.24) * mm});
            skLineSegment(sketch, "E7308", {"start": v(161.3, 3.24) * mm, "end": v(161.85, 5.02) * mm});
            skLineSegment(sketch, "E7309", {"start": v(161.85, 5.02) * mm, "end": v(161.9, 5.22) * mm});
            skLineSegment(sketch, "E7310", {"start": v(161.9, 5.22) * mm, "end": v(162.72, 7.13) * mm});
            skLineSegment(sketch, "E7311", {"start": v(162.72, 7.13) * mm, "end": v(162.83, 7.31) * mm});
            skLineSegment(sketch, "E7312", {"start": v(162.83, 7.31) * mm, "end": v(162.97, 7.58) * mm});
            skLineSegment(sketch, "E7313", {"start": v(162.97, 7.58) * mm, "end": v(163.52, 8.34) * mm});
            skLineSegment(sketch, "E7314", {"start": v(163.52, 8.34) * mm, "end": v(164.46, 9.4) * mm});
            skLineSegment(sketch, "E7315", {"start": v(164.46, 9.4) * mm, "end": v(165.5, 10.4) * mm});
            skLineSegment(sketch, "E7316", {"start": v(165.5, 10.4) * mm, "end": v(166.21, 11) * mm});
            skLineSegment(sketch, "E7317", {"start": v(166.21, 11) * mm, "end": v(166.46, 11.2) * mm});
            skLineSegment(sketch, "E7318", {"start": v(166.46, 11.2) * mm, "end": v(167.34, 11.85) * mm});
            skLineSegment(sketch, "E7319", {"start": v(167.34, 11.85) * mm, "end": v(170.1, 13.64) * mm});
            skLineSegment(sketch, "E7320", {"start": v(170.1, 13.64) * mm, "end": v(174.3, 15.99) * mm});
            skLineSegment(sketch, "E7321", {"start": v(174.3, 15.99) * mm, "end": v(178.86, 18.18) * mm});
            skLineSegment(sketch, "E7322", {"start": v(178.86, 18.18) * mm, "end": v(183.68, 20.19) * mm});
            skLineSegment(sketch, "E7323", {"start": v(183.68, 20.19) * mm, "end": v(188.6, 21.96) * mm});
            skLineSegment(sketch, "E7324", {"start": v(188.6, 21.96) * mm, "end": v(193.47, 23.46) * mm});
            skLineSegment(sketch, "E7325", {"start": v(193.47, 23.46) * mm, "end": v(198.15, 24.65) * mm});
            skLineSegment(sketch, "E7326", {"start": v(198.15, 24.65) * mm, "end": v(201.4, 25.3) * mm});
            skLineSegment(sketch, "E7327", {"start": v(201.4, 25.3) * mm, "end": v(202.5, 25.47) * mm});
            skLineSegment(sketch, "E7328", {"start": v(202.5, 25.47) * mm, "end": v(203.1, 25.57) * mm});
            skLineSegment(sketch, "E7329", {"start": v(203.1, 25.57) * mm, "end": v(204.97, 25.76) * mm});
            skLineSegment(sketch, "E7330", {"start": v(204.97, 25.76) * mm, "end": v(208.3, 25.97) * mm});
            skLineSegment(sketch, "E7331", {"start": v(208.3, 25.97) * mm, "end": v(212.12, 26.02) * mm});
            skLineSegment(sketch, "E7332", {"start": v(212.12, 26.02) * mm, "end": v(216.14, 25.84) * mm});
            skLineSegment(sketch, "E7333", {"start": v(216.14, 25.84) * mm, "end": v(220.01, 25.34) * mm});
            skLineSegment(sketch, "E7334", {"start": v(220.01, 25.34) * mm, "end": v(223.42, 24.44) * mm});
            skLineSegment(sketch, "E7335", {"start": v(223.42, 24.44) * mm, "end": v(226.03, 23.06) * mm});
            skLineSegment(sketch, "E7336", {"start": v(226.03, 23.06) * mm, "end": v(227.3, 21.66) * mm});
            skLineSegment(sketch, "E7337", {"start": v(227.3, 21.66) * mm, "end": v(227.5, 21.12) * mm});
            skLineSegment(sketch, "E7338", {"start": v(227.5, 21.12) * mm, "end": v(227.96, 19.85) * mm});
            skLineSegment(sketch, "E7339", {"start": v(227.96, 19.85) * mm, "end": v(226.63, 19.7) * mm});
            skLineSegment(sketch, "E7340", {"start": v(226.63, 19.7) * mm, "end": v(226.18, 19.64) * mm});
            skLineSegment(sketch, "E7341", {"start": v(226.18, 19.64) * mm, "end": v(223.97, 19.27) * mm});
            skLineSegment(sketch, "E7342", {"start": v(223.97, 19.27) * mm, "end": v(221.8, 18.72) * mm});
            skLineSegment(sketch, "E7343", {"start": v(221.8, 18.72) * mm, "end": v(221.37, 18.57) * mm});
            skLineSegment(sketch, "E7344", {"start": v(221.37, 18.57) * mm, "end": v(220.5, 18.27) * mm});
            skLineSegment(sketch, "E7345", {"start": v(-227.8, -55.58) * mm, "end": v(-227.89, -55.5) * mm});
            skLineSegment(sketch, "E7346", {"start": v(-227.89, -55.5) * mm, "end": v(-228.81, -54.84) * mm});
            skLineSegment(sketch, "E7347", {"start": v(-228.81, -54.84) * mm, "end": v(-228.91, -54.78) * mm});
            skLineSegment(sketch, "E7348", {"start": v(-228.91, -54.78) * mm, "end": v(-229.93, -54.17) * mm});
            skLineSegment(sketch, "E7349", {"start": v(-229.93, -54.17) * mm, "end": v(-229.2, -53.22) * mm});
            skLineSegment(sketch, "E7350", {"start": v(-229.2, -53.22) * mm, "end": v(-228.79, -52.67) * mm});
            skLineSegment(sketch, "E7351", {"start": v(-228.79, -52.67) * mm, "end": v(-227.69, -50.9) * mm});
            skLineSegment(sketch, "E7352", {"start": v(-227.69, -50.9) * mm, "end": v(-226.63, -48.48) * mm});
            skLineSegment(sketch, "E7353", {"start": v(-226.63, -48.48) * mm, "end": v(-226, -45.91) * mm});
            skLineSegment(sketch, "E7354", {"start": v(-226, -45.91) * mm, "end": v(-225.77, -43.84) * mm});
            skLineSegment(sketch, "E7355", {"start": v(-225.77, -43.84) * mm, "end": v(-225.76, -43.15) * mm});
            skLineSegment(sketch, "E7356", {"start": v(-225.76, -43.15) * mm, "end": v(-225.76, -42.74) * mm});
            skLineSegment(sketch, "E7357", {"start": v(-225.76, -42.74) * mm, "end": v(-225.48, -42.44) * mm});
            skLineSegment(sketch, "E7358", {"start": v(-225.48, -42.44) * mm, "end": v(-225.23, -42.16) * mm});
            skLineSegment(sketch, "E7359", {"start": v(-225.23, -42.16) * mm, "end": v(-224.47, -41.34) * mm});
            skLineSegment(sketch, "E7360", {"start": v(-224.47, -41.34) * mm, "end": v(-223.47, -40.4) * mm});
            skLineSegment(sketch, "E7361", {"start": v(-223.47, -40.4) * mm, "end": v(-222.3, -39.7) * mm});
            skLineSegment(sketch, "E7362", {"start": v(-222.3, -39.7) * mm, "end": v(-221.2, -39.34) * mm});
            skLineSegment(sketch, "E7363", {"start": v(-221.2, -39.34) * mm, "end": v(-220.81, -39.3) * mm});
            skLineSegment(sketch, "E7364", {"start": v(-220.81, -39.3) * mm, "end": v(-220.24, -39.22) * mm});
            skLineSegment(sketch, "E7365", {"start": v(-220.24, -39.22) * mm, "end": v(-219.87, -39.66) * mm});
            skLineSegment(sketch, "E7366", {"start": v(-219.87, -39.66) * mm, "end": v(-219.26, -40.36) * mm});
            skLineSegment(sketch, "E7367", {"start": v(-219.26, -40.36) * mm, "end": v(-216.4, -44.02) * mm});
            skLineSegment(sketch, "E7368", {"start": v(-216.4, -44.02) * mm, "end": v(-213.53, -47.68) * mm});
            skLineSegment(sketch, "E7369", {"start": v(-213.53, -47.68) * mm, "end": v(-212.92, -48.38) * mm});
            skLineSegment(sketch, "E7370", {"start": v(-212.92, -48.38) * mm, "end": v(-211.92, -49.56) * mm});
            skLineSegment(sketch, "E7371", {"start": v(-211.92, -49.56) * mm, "end": v(-213.37, -50.08) * mm});
            skLineSegment(sketch, "E7372", {"start": v(-213.37, -50.08) * mm, "end": v(-214.48, -50.48) * mm});
            skLineSegment(sketch, "E7373", {"start": v(-214.48, -50.48) * mm, "end": v(-219.86, -52.9) * mm});
            skLineSegment(sketch, "E7374", {"start": v(-219.86, -52.9) * mm, "end": v(-225.01, -55.74) * mm});
            skLineSegment(sketch, "E7375", {"start": v(-225.01, -55.74) * mm, "end": v(-226.02, -56.35) * mm});
            skLineSegment(sketch, "E7376", {"start": v(-226.02, -56.35) * mm, "end": v(-226.72, -56.78) * mm});
            skLineSegment(sketch, "E7377", {"start": v(-226.72, -56.78) * mm, "end": v(-227.31, -56.22) * mm});
            skLineSegment(sketch, "E7378", {"start": v(-227.31, -56.22) * mm, "end": v(-227.38, -56.16) * mm});
            skLineSegment(sketch, "E7379", {"start": v(-227.38, -56.16) * mm, "end": v(-227.58, -55.9) * mm});
            skLineSegment(sketch, "E7380", {"start": v(-227.58, -55.9) * mm, "end": v(-227.75, -55.63) * mm});
            skLineSegment(sketch, "E7381", {"start": v(-227.75, -55.63) * mm, "end": v(-227.8, -55.57) * mm});
            skLineSegment(sketch, "E7382", {"start": v(-227.8, -55.57) * mm, "end": v(-227.8, -55.58) * mm});
            skLineSegment(sketch, "E7383", {"start": v(993.9, -42.55) * mm, "end": v(994.28, -42.07) * mm});
            skLineSegment(sketch, "E7384", {"start": v(994.28, -42.07) * mm, "end": v(995.23, -40.47) * mm});
            skLineSegment(sketch, "E7385", {"start": v(995.23, -40.47) * mm, "end": v(996.3, -38.14) * mm});
            skLineSegment(sketch, "E7386", {"start": v(996.3, -38.14) * mm, "end": v(997.18, -35.7) * mm});
            skLineSegment(sketch, "E7387", {"start": v(997.18, -35.7) * mm, "end": v(997.75, -33.93) * mm});
            skLineSegment(sketch, "E7388", {"start": v(997.75, -33.93) * mm, "end": v(997.93, -33.33) * mm});
            skLineSegment(sketch, "E7389", {"start": v(997.93, -33.33) * mm, "end": v(997.44, -32.97) * mm});
            skLineSegment(sketch, "E7390", {"start": v(997.44, -32.97) * mm, "end": v(995.7, -32.22) * mm});
            skLineSegment(sketch, "E7391", {"start": v(995.7, -32.22) * mm, "end": v(993.47, -31.99) * mm});
            skLineSegment(sketch, "E7392", {"start": v(993.47, -31.99) * mm, "end": v(991.27, -32.49) * mm});
            skLineSegment(sketch, "E7393", {"start": v(991.27, -32.49) * mm, "end": v(989.17, -33.58) * mm});
            skLineSegment(sketch, "E7394", {"start": v(989.17, -33.58) * mm, "end": v(987.21, -35.12) * mm});
            skLineSegment(sketch, "E7395", {"start": v(987.21, -35.12) * mm, "end": v(985.46, -36.96) * mm});
            skLineSegment(sketch, "E7396", {"start": v(985.46, -36.96) * mm, "end": v(983.97, -38.97) * mm});
            skLineSegment(sketch, "E7397", {"start": v(983.97, -38.97) * mm, "end": v(983.06, -40.47) * mm});
            skLineSegment(sketch, "E7398", {"start": v(983.06, -40.47) * mm, "end": v(982.8, -41) * mm});
            skLineSegment(sketch, "E7399", {"start": v(982.8, -41) * mm, "end": v(983.36, -41.24) * mm});
            skLineSegment(sketch, "E7400", {"start": v(983.36, -41.24) * mm, "end": v(985.24, -41.55) * mm});
            skLineSegment(sketch, "E7401", {"start": v(985.24, -41.55) * mm, "end": v(988.1, -41.66) * mm});
            skLineSegment(sketch, "E7402", {"start": v(988.1, -41.66) * mm, "end": v(991.08, -41.82) * mm});
            skLineSegment(sketch, "E7403", {"start": v(991.08, -41.82) * mm, "end": v(993.25, -42.26) * mm});
            skLineSegment(sketch, "E7404", {"start": v(993.25, -42.26) * mm, "end": v(993.9, -42.55) * mm});
            skSolve(sketch);
        }
        {
            var Q0;
            Q0=makeQuery(id+"F0.imprint","IMPRINT",FACE,{"disambiguationData":[TD([[makeQuery(id+"F0.imprint","IMPRINT",EDGE,{"derivedFrom":sQuery(id+"F0.wireOp",EDGE,"E7207")}),-1.0]])]});
            extrude(context, id + "F1", {"entities" : qUnion([Q0]), "oppositeDirection" : true, "depth" : 1.52 * mm});
        }
        {
            var Q0;
            Q0=makeQuery(id+"F0.imprint","IMPRINT",FACE,{"disambiguationData":[TD([[makeQuery(id+"F0.imprint","IMPRINT",EDGE,{"derivedFrom":sQuery(id+"F0.wireOp",EDGE,"E7277")}),-1.0]])]});
            var Q1;
            Q1=makeQuery(id+"F0.imprint","IMPRINT",FACE,{"disambiguationData":[TD([[makeQuery(id+"F0.imprint","IMPRINT",EDGE,{"derivedFrom":sQuery(id+"F0.wireOp",EDGE,"E6997")}),-1.0]])]});
            var Q2;
            Q2=makeQuery(id+"F0.imprint","IMPRINT",FACE,{"disambiguationData":[TD([[makeQuery(id+"F0.imprint","IMPRINT",EDGE,{"derivedFrom":sQuery(id+"F0.wireOp",EDGE,"E7345")}),-1.0]])]});
            var Q3;
            Q3=makeQuery(id+"F0.imprint","IMPRINT",FACE,{"disambiguationData":[TD([[makeQuery(id+"F0.imprint","IMPRINT",EDGE,{"derivedFrom":sQuery(id+"F0.wireOp",EDGE,"E7056")}),-1.0]])]});
            extrude(context, id + "F2", {"entities" : qUnion([Q0, Q1, Q2, Q3]), "oppositeDirection" : true, "depth" : 1.52 * mm});
        }
        {
            var Q0;
            Q0=makeQuery(id+"F0.imprint","IMPRINT",FACE,{"disambiguationData":[TD([[makeQuery(id+"F0.imprint","IMPRINT",EDGE,{"derivedFrom":sQuery(id+"F0.wireOp",EDGE,"E1921")}),-1.0]])]});
            extrude(context, id + "F3", {"entities" : qUnion([Q0]), "oppositeDirection" : true, "depth" : 1.52 * mm});
        }
        {
            var Q0;
            Q0=makeQuery(id+"F0.imprint","IMPRINT",FACE,{"disambiguationData":[TD([[makeQuery(id+"F0.imprint","IMPRINT",EDGE,{"derivedFrom":sQuery(id+"F0.wireOp",EDGE,"E0")}),1.0]])]});
            extrude(context, id + "F4", {"entities" : qUnion([Q0]), "oppositeDirection" : true, "depth" : 1.52 * mm});
        }
        {
            var Q0;
            Q0=makeQuery(id+"F0.imprint","IMPRINT",FACE,{"disambiguationData":[TD([[makeQuery(id+"F0.imprint","IMPRINT",EDGE,{"derivedFrom":sQuery(id+"F0.wireOp",EDGE,"E3347")}),-1.0]])]});
            extrude(context, id + "F5", {"entities" : qUnion([Q0]), "oppositeDirection" : true, "depth" : 1.52 * mm});
        }
        {
            var Q0;
            Q0=qCreatedBy(makeId("Front.planeOp"),FACE);
            cPlane(context, id + "F6", {"entities" : qUnion([Q0]), "cplaneType" : CPlaneType.OFFSET, "offset" : 12.7 * mm, "width" : 152.4 * mm, "height" : 152.4 * mm});
        }
    });
